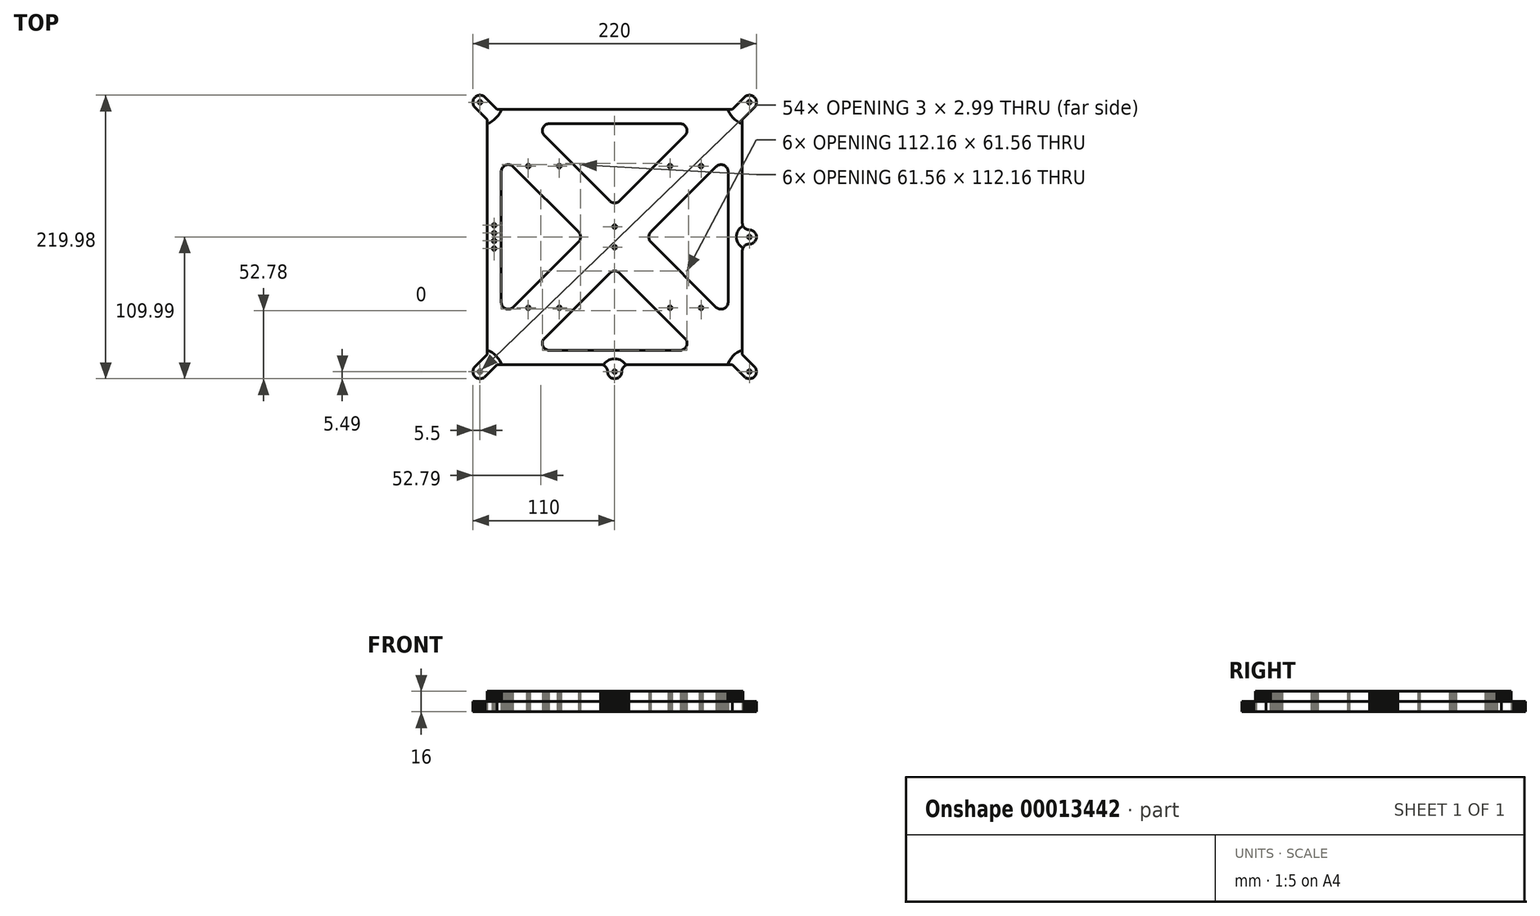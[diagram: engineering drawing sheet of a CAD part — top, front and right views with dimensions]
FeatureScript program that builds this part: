
annotation { "Feature Type Name" : "Feature", "Feature Type Description" : "" }
export const myFeature = defineFeature(function(context is Context, id is Id, definition is map)
    precondition{}
    {
        {
            var Q0;
            Q0=qCreatedBy(makeId("Top.planeOp"),FACE);
            var sketch = newSketch(context, id + "F0", { "sketchPlane" : qUnion([Q0])});
            skLineSegment(sketch, "E0", {"start": v(391.25, -176.92) * mm, "end": v(392.49, -176.69) * mm});
            skLineSegment(sketch, "E1", {"start": v(392.49, -176.69) * mm, "end": v(393.68, -176.3) * mm});
            skLineSegment(sketch, "E2", {"start": v(393.68, -176.3) * mm, "end": v(394.82, -175.76) * mm});
            skLineSegment(sketch, "E3", {"start": v(394.82, -175.76) * mm, "end": v(395.88, -175.1) * mm});
            skLineSegment(sketch, "E4", {"start": v(395.88, -175.1) * mm, "end": v(396.85, -174.29) * mm});
            skLineSegment(sketch, "E5", {"start": v(396.85, -174.29) * mm, "end": v(397.7, -173.37) * mm});
            skLineSegment(sketch, "E6", {"start": v(397.7, -173.37) * mm, "end": v(398.44, -172.36) * mm});
            skLineSegment(sketch, "E7", {"start": v(398.44, -172.36) * mm, "end": v(399.05, -171.26) * mm});
            skLineSegment(sketch, "E8", {"start": v(399.05, -171.26) * mm, "end": v(399.51, -170.1) * mm});
            skLineSegment(sketch, "E9", {"start": v(399.51, -170.1) * mm, "end": v(399.82, -168.87) * mm});
            skLineSegment(sketch, "E10", {"start": v(399.82, -168.87) * mm, "end": v(399.98, -167.63) * mm});
            skLineSegment(sketch, "E11", {"start": v(399.98, -167.63) * mm, "end": v(399.98, -167) * mm});
            skLineSegment(sketch, "E12", {"start": v(399.98, -167) * mm, "end": v(400, -167) * mm});
            skLineSegment(sketch, "E13", {"start": v(400, -167) * mm, "end": v(400, 109) * mm});
            skLineSegment(sketch, "E14", {"start": v(400, 109) * mm, "end": v(360, 109) * mm});
            skLineSegment(sketch, "E15", {"start": v(360, 109) * mm, "end": v(360, 125) * mm});
            skLineSegment(sketch, "E16", {"start": v(360, 125) * mm, "end": v(400, 125) * mm});
            skLineSegment(sketch, "E17", {"start": v(400, 125) * mm, "end": v(400, 253) * mm});
            skLineSegment(sketch, "E18", {"start": v(400, 253) * mm, "end": v(399.92, 254.25) * mm});
            skLineSegment(sketch, "E19", {"start": v(399.92, 254.25) * mm, "end": v(399.69, 255.49) * mm});
            skLineSegment(sketch, "E20", {"start": v(399.69, 255.49) * mm, "end": v(399.3, 256.68) * mm});
            skLineSegment(sketch, "E21", {"start": v(399.3, 256.68) * mm, "end": v(398.76, 257.82) * mm});
            skLineSegment(sketch, "E22", {"start": v(398.76, 257.82) * mm, "end": v(398.09, 258.88) * mm});
            skLineSegment(sketch, "E23", {"start": v(398.09, 258.88) * mm, "end": v(397.3, 259.85) * mm});
            skLineSegment(sketch, "E24", {"start": v(397.3, 259.85) * mm, "end": v(396.37, 260.7) * mm});
            skLineSegment(sketch, "E25", {"start": v(396.37, 260.7) * mm, "end": v(395.36, 261.44) * mm});
            skLineSegment(sketch, "E26", {"start": v(395.36, 261.44) * mm, "end": v(394.26, 262.05) * mm});
            skLineSegment(sketch, "E27", {"start": v(394.26, 262.05) * mm, "end": v(393.09, 262.51) * mm});
            skLineSegment(sketch, "E28", {"start": v(393.09, 262.51) * mm, "end": v(391.87, 262.82) * mm});
            skLineSegment(sketch, "E29", {"start": v(391.87, 262.82) * mm, "end": v(390.63, 262.98) * mm});
            skLineSegment(sketch, "E30", {"start": v(390.63, 262.98) * mm, "end": v(390, 262.98) * mm});
            skLineSegment(sketch, "E31", {"start": v(390, 262.98) * mm, "end": v(390, 263) * mm});
            skLineSegment(sketch, "E32", {"start": v(390, 263) * mm, "end": v(20, 263) * mm});
            skLineSegment(sketch, "E33", {"start": v(20, 263) * mm, "end": v(18.75, 262.92) * mm});
            skLineSegment(sketch, "E34", {"start": v(18.75, 262.92) * mm, "end": v(17.51, 262.69) * mm});
            skLineSegment(sketch, "E35", {"start": v(17.51, 262.69) * mm, "end": v(16.32, 262.3) * mm});
            skLineSegment(sketch, "E36", {"start": v(16.32, 262.3) * mm, "end": v(15.18, 261.76) * mm});
            skLineSegment(sketch, "E37", {"start": v(15.18, 261.76) * mm, "end": v(14.12, 261.09) * mm});
            skLineSegment(sketch, "E38", {"start": v(14.12, 261.09) * mm, "end": v(13.15, 260.3) * mm});
            skLineSegment(sketch, "E39", {"start": v(13.15, 260.3) * mm, "end": v(12.3, 259.37) * mm});
            skLineSegment(sketch, "E40", {"start": v(12.3, 259.37) * mm, "end": v(11.56, 258.36) * mm});
            skLineSegment(sketch, "E41", {"start": v(11.56, 258.36) * mm, "end": v(10.95, 257.26) * mm});
            skLineSegment(sketch, "E42", {"start": v(10.95, 257.26) * mm, "end": v(10.49, 256.09) * mm});
            skLineSegment(sketch, "E43", {"start": v(10.49, 256.09) * mm, "end": v(10.18, 254.87) * mm});
            skLineSegment(sketch, "E44", {"start": v(10.18, 254.87) * mm, "end": v(10.02, 253.63) * mm});
            skLineSegment(sketch, "E45", {"start": v(10.02, 253.63) * mm, "end": v(10.02, 253) * mm});
            skLineSegment(sketch, "E46", {"start": v(10.02, 253) * mm, "end": v(10, 253) * mm});
            skLineSegment(sketch, "E47", {"start": v(10, 253) * mm, "end": v(10, 125) * mm});
            skLineSegment(sketch, "E48", {"start": v(10, 125) * mm, "end": v(50, 125) * mm});
            skLineSegment(sketch, "E49", {"start": v(50, 125) * mm, "end": v(50, 109) * mm});
            skLineSegment(sketch, "E50", {"start": v(50, 109) * mm, "end": v(10, 109) * mm});
            skLineSegment(sketch, "E51", {"start": v(10, 109) * mm, "end": v(10, -167) * mm});
            skLineSegment(sketch, "E52", {"start": v(10, -167) * mm, "end": v(10.08, -168.25) * mm});
            skLineSegment(sketch, "E53", {"start": v(10.08, -168.25) * mm, "end": v(10.31, -169.49) * mm});
            skLineSegment(sketch, "E54", {"start": v(10.31, -169.49) * mm, "end": v(10.7, -170.68) * mm});
            skLineSegment(sketch, "E55", {"start": v(10.7, -170.68) * mm, "end": v(11.24, -171.82) * mm});
            skLineSegment(sketch, "E56", {"start": v(11.24, -171.82) * mm, "end": v(11.9, -172.88) * mm});
            skLineSegment(sketch, "E57", {"start": v(11.9, -172.88) * mm, "end": v(12.71, -173.85) * mm});
            skLineSegment(sketch, "E58", {"start": v(12.71, -173.85) * mm, "end": v(13.63, -174.7) * mm});
            skLineSegment(sketch, "E59", {"start": v(13.63, -174.7) * mm, "end": v(14.64, -175.44) * mm});
            skLineSegment(sketch, "E60", {"start": v(14.64, -175.44) * mm, "end": v(15.74, -176.05) * mm});
            skLineSegment(sketch, "E61", {"start": v(15.74, -176.05) * mm, "end": v(16.9, -176.51) * mm});
            skLineSegment(sketch, "E62", {"start": v(16.9, -176.51) * mm, "end": v(18.13, -176.82) * mm});
            skLineSegment(sketch, "E63", {"start": v(18.13, -176.82) * mm, "end": v(19.37, -176.98) * mm});
            skLineSegment(sketch, "E64", {"start": v(19.37, -176.98) * mm, "end": v(20, -176.98) * mm});
            skLineSegment(sketch, "E65", {"start": v(20, -176.98) * mm, "end": v(20, -177) * mm});
            skLineSegment(sketch, "E66", {"start": v(20, -177) * mm, "end": v(390, -177) * mm});
            skLineSegment(sketch, "E67", {"start": v(390, -177) * mm, "end": v(391.25, -176.92) * mm});
            skLineSegment(sketch, "E68", {"start": v(50, 236.5) * mm, "end": v(50, 252.5) * mm});
            skLineSegment(sketch, "E69", {"start": v(50, 252.5) * mm, "end": v(70, 252.5) * mm});
            skLineSegment(sketch, "E70", {"start": v(70, 252.5) * mm, "end": v(70, 236.5) * mm});
            skLineSegment(sketch, "E71", {"start": v(70, 236.5) * mm, "end": v(50, 236.5) * mm});
            skLineSegment(sketch, "E72", {"start": v(195, 236.5) * mm, "end": v(195, 252.5) * mm});
            skLineSegment(sketch, "E73", {"start": v(195, 252.5) * mm, "end": v(215, 252.5) * mm});
            skLineSegment(sketch, "E74", {"start": v(215, 252.5) * mm, "end": v(215, 236.5) * mm});
            skLineSegment(sketch, "E75", {"start": v(215, 236.5) * mm, "end": v(195, 236.5) * mm});
            skLineSegment(sketch, "E76", {"start": v(340, 236.5) * mm, "end": v(340, 252.5) * mm});
            skLineSegment(sketch, "E77", {"start": v(340, 252.5) * mm, "end": v(360, 252.5) * mm});
            skLineSegment(sketch, "E78", {"start": v(360, 252.5) * mm, "end": v(360, 236.5) * mm});
            skLineSegment(sketch, "E79", {"start": v(360, 236.5) * mm, "end": v(340, 236.5) * mm});
            skLineSegment(sketch, "E80", {"start": v(287.37, 242.5) * mm, "end": v(287.12, 242.53) * mm});
            skLineSegment(sketch, "E81", {"start": v(287.12, 242.53) * mm, "end": v(286.88, 242.6) * mm});
            skLineSegment(sketch, "E82", {"start": v(286.88, 242.6) * mm, "end": v(286.65, 242.7) * mm});
            skLineSegment(sketch, "E83", {"start": v(286.65, 242.7) * mm, "end": v(286.43, 242.81) * mm});
            skLineSegment(sketch, "E84", {"start": v(286.43, 242.81) * mm, "end": v(286.23, 242.96) * mm});
            skLineSegment(sketch, "E85", {"start": v(286.23, 242.96) * mm, "end": v(286.04, 243.13) * mm});
            skLineSegment(sketch, "E86", {"start": v(286.04, 243.13) * mm, "end": v(285.88, 243.32) * mm});
            skLineSegment(sketch, "E87", {"start": v(285.88, 243.32) * mm, "end": v(285.75, 243.54) * mm});
            skLineSegment(sketch, "E88", {"start": v(285.75, 243.54) * mm, "end": v(285.64, 243.76) * mm});
            skLineSegment(sketch, "E89", {"start": v(285.64, 243.76) * mm, "end": v(285.56, 244) * mm});
            skLineSegment(sketch, "E90", {"start": v(285.56, 244) * mm, "end": v(285.52, 244.25) * mm});
            skLineSegment(sketch, "E91", {"start": v(285.52, 244.25) * mm, "end": v(285.5, 244.5) * mm});
            skLineSegment(sketch, "E92", {"start": v(285.5, 244.5) * mm, "end": v(285.52, 244.75) * mm});
            skLineSegment(sketch, "E93", {"start": v(285.52, 244.75) * mm, "end": v(285.56, 245) * mm});
            skLineSegment(sketch, "E94", {"start": v(285.56, 245) * mm, "end": v(285.64, 245.24) * mm});
            skLineSegment(sketch, "E95", {"start": v(285.64, 245.24) * mm, "end": v(285.75, 245.46) * mm});
            skLineSegment(sketch, "E96", {"start": v(285.75, 245.46) * mm, "end": v(285.88, 245.68) * mm});
            skLineSegment(sketch, "E97", {"start": v(285.88, 245.68) * mm, "end": v(286.04, 245.87) * mm});
            skLineSegment(sketch, "E98", {"start": v(286.04, 245.87) * mm, "end": v(286.23, 246.04) * mm});
            skLineSegment(sketch, "E99", {"start": v(286.23, 246.04) * mm, "end": v(286.43, 246.19) * mm});
            skLineSegment(sketch, "E100", {"start": v(286.43, 246.19) * mm, "end": v(286.65, 246.3) * mm});
            skLineSegment(sketch, "E101", {"start": v(286.65, 246.3) * mm, "end": v(286.88, 246.4) * mm});
            skLineSegment(sketch, "E102", {"start": v(286.88, 246.4) * mm, "end": v(287.12, 246.47) * mm});
            skLineSegment(sketch, "E103", {"start": v(287.12, 246.47) * mm, "end": v(287.37, 246.5) * mm});
            skLineSegment(sketch, "E104", {"start": v(287.37, 246.5) * mm, "end": v(287.63, 246.5) * mm});
            skLineSegment(sketch, "E105", {"start": v(287.63, 246.5) * mm, "end": v(287.88, 246.47) * mm});
            skLineSegment(sketch, "E106", {"start": v(287.88, 246.47) * mm, "end": v(288.12, 246.4) * mm});
            skLineSegment(sketch, "E107", {"start": v(288.12, 246.4) * mm, "end": v(288.35, 246.3) * mm});
            skLineSegment(sketch, "E108", {"start": v(288.35, 246.3) * mm, "end": v(288.57, 246.19) * mm});
            skLineSegment(sketch, "E109", {"start": v(288.57, 246.19) * mm, "end": v(288.77, 246.04) * mm});
            skLineSegment(sketch, "E110", {"start": v(288.77, 246.04) * mm, "end": v(288.96, 245.87) * mm});
            skLineSegment(sketch, "E111", {"start": v(288.96, 245.87) * mm, "end": v(289.12, 245.68) * mm});
            skLineSegment(sketch, "E112", {"start": v(289.12, 245.68) * mm, "end": v(289.25, 245.46) * mm});
            skLineSegment(sketch, "E113", {"start": v(289.25, 245.46) * mm, "end": v(289.36, 245.24) * mm});
            skLineSegment(sketch, "E114", {"start": v(289.36, 245.24) * mm, "end": v(289.44, 245) * mm});
            skLineSegment(sketch, "E115", {"start": v(289.44, 245) * mm, "end": v(289.48, 244.75) * mm});
            skLineSegment(sketch, "E116", {"start": v(289.48, 244.75) * mm, "end": v(289.5, 244.5) * mm});
            skLineSegment(sketch, "E117", {"start": v(289.5, 244.5) * mm, "end": v(289.48, 244.25) * mm});
            skLineSegment(sketch, "E118", {"start": v(289.48, 244.25) * mm, "end": v(289.44, 244) * mm});
            skLineSegment(sketch, "E119", {"start": v(289.44, 244) * mm, "end": v(289.36, 243.76) * mm});
            skLineSegment(sketch, "E120", {"start": v(289.36, 243.76) * mm, "end": v(289.25, 243.54) * mm});
            skLineSegment(sketch, "E121", {"start": v(289.25, 243.54) * mm, "end": v(289.12, 243.32) * mm});
            skLineSegment(sketch, "E122", {"start": v(289.12, 243.32) * mm, "end": v(288.96, 243.13) * mm});
            skLineSegment(sketch, "E123", {"start": v(288.96, 243.13) * mm, "end": v(288.77, 242.96) * mm});
            skLineSegment(sketch, "E124", {"start": v(288.77, 242.96) * mm, "end": v(288.57, 242.81) * mm});
            skLineSegment(sketch, "E125", {"start": v(288.57, 242.81) * mm, "end": v(288.35, 242.7) * mm});
            skLineSegment(sketch, "E126", {"start": v(288.35, 242.7) * mm, "end": v(288.12, 242.6) * mm});
            skLineSegment(sketch, "E127", {"start": v(288.12, 242.6) * mm, "end": v(287.88, 242.53) * mm});
            skLineSegment(sketch, "E128", {"start": v(287.88, 242.53) * mm, "end": v(287.63, 242.5) * mm});
            skLineSegment(sketch, "E129", {"start": v(287.63, 242.5) * mm, "end": v(287.37, 242.5) * mm});
            skLineSegment(sketch, "E130", {"start": v(122.37, 242.5) * mm, "end": v(122.12, 242.53) * mm});
            skLineSegment(sketch, "E131", {"start": v(122.12, 242.53) * mm, "end": v(121.88, 242.6) * mm});
            skLineSegment(sketch, "E132", {"start": v(121.88, 242.6) * mm, "end": v(121.65, 242.7) * mm});
            skLineSegment(sketch, "E133", {"start": v(121.65, 242.7) * mm, "end": v(121.43, 242.81) * mm});
            skLineSegment(sketch, "E134", {"start": v(121.43, 242.81) * mm, "end": v(121.22, 242.96) * mm});
            skLineSegment(sketch, "E135", {"start": v(121.22, 242.96) * mm, "end": v(121.04, 243.13) * mm});
            skLineSegment(sketch, "E136", {"start": v(121.04, 243.13) * mm, "end": v(120.88, 243.32) * mm});
            skLineSegment(sketch, "E137", {"start": v(120.88, 243.32) * mm, "end": v(120.75, 243.54) * mm});
            skLineSegment(sketch, "E138", {"start": v(120.75, 243.54) * mm, "end": v(120.64, 243.76) * mm});
            skLineSegment(sketch, "E139", {"start": v(120.64, 243.76) * mm, "end": v(120.56, 244) * mm});
            skLineSegment(sketch, "E140", {"start": v(120.56, 244) * mm, "end": v(120.52, 244.25) * mm});
            skLineSegment(sketch, "E141", {"start": v(120.52, 244.25) * mm, "end": v(120.5, 244.5) * mm});
            skLineSegment(sketch, "E142", {"start": v(120.5, 244.5) * mm, "end": v(120.52, 244.75) * mm});
            skLineSegment(sketch, "E143", {"start": v(120.52, 244.75) * mm, "end": v(120.56, 245) * mm});
            skLineSegment(sketch, "E144", {"start": v(120.56, 245) * mm, "end": v(120.64, 245.24) * mm});
            skLineSegment(sketch, "E145", {"start": v(120.64, 245.24) * mm, "end": v(120.75, 245.46) * mm});
            skLineSegment(sketch, "E146", {"start": v(120.75, 245.46) * mm, "end": v(120.88, 245.68) * mm});
            skLineSegment(sketch, "E147", {"start": v(120.88, 245.68) * mm, "end": v(121.04, 245.87) * mm});
            skLineSegment(sketch, "E148", {"start": v(121.04, 245.87) * mm, "end": v(121.22, 246.04) * mm});
            skLineSegment(sketch, "E149", {"start": v(121.22, 246.04) * mm, "end": v(121.43, 246.19) * mm});
            skLineSegment(sketch, "E150", {"start": v(121.43, 246.19) * mm, "end": v(121.65, 246.3) * mm});
            skLineSegment(sketch, "E151", {"start": v(121.65, 246.3) * mm, "end": v(121.88, 246.4) * mm});
            skLineSegment(sketch, "E152", {"start": v(121.88, 246.4) * mm, "end": v(122.12, 246.47) * mm});
            skLineSegment(sketch, "E153", {"start": v(122.12, 246.47) * mm, "end": v(122.37, 246.5) * mm});
            skLineSegment(sketch, "E154", {"start": v(122.37, 246.5) * mm, "end": v(122.63, 246.5) * mm});
            skLineSegment(sketch, "E155", {"start": v(122.63, 246.5) * mm, "end": v(122.88, 246.47) * mm});
            skLineSegment(sketch, "E156", {"start": v(122.88, 246.47) * mm, "end": v(123.12, 246.4) * mm});
            skLineSegment(sketch, "E157", {"start": v(123.12, 246.4) * mm, "end": v(123.35, 246.3) * mm});
            skLineSegment(sketch, "E158", {"start": v(123.35, 246.3) * mm, "end": v(123.57, 246.19) * mm});
            skLineSegment(sketch, "E159", {"start": v(123.57, 246.19) * mm, "end": v(123.78, 246.04) * mm});
            skLineSegment(sketch, "E160", {"start": v(123.78, 246.04) * mm, "end": v(123.96, 245.87) * mm});
            skLineSegment(sketch, "E161", {"start": v(123.96, 245.87) * mm, "end": v(124.12, 245.68) * mm});
            skLineSegment(sketch, "E162", {"start": v(124.12, 245.68) * mm, "end": v(124.25, 245.46) * mm});
            skLineSegment(sketch, "E163", {"start": v(124.25, 245.46) * mm, "end": v(124.36, 245.24) * mm});
            skLineSegment(sketch, "E164", {"start": v(124.36, 245.24) * mm, "end": v(124.44, 245) * mm});
            skLineSegment(sketch, "E165", {"start": v(124.44, 245) * mm, "end": v(124.48, 244.75) * mm});
            skLineSegment(sketch, "E166", {"start": v(124.48, 244.75) * mm, "end": v(124.5, 244.5) * mm});
            skLineSegment(sketch, "E167", {"start": v(124.5, 244.5) * mm, "end": v(124.48, 244.25) * mm});
            skLineSegment(sketch, "E168", {"start": v(124.48, 244.25) * mm, "end": v(124.44, 244) * mm});
            skLineSegment(sketch, "E169", {"start": v(124.44, 244) * mm, "end": v(124.36, 243.76) * mm});
            skLineSegment(sketch, "E170", {"start": v(124.36, 243.76) * mm, "end": v(124.25, 243.54) * mm});
            skLineSegment(sketch, "E171", {"start": v(124.25, 243.54) * mm, "end": v(124.12, 243.32) * mm});
            skLineSegment(sketch, "E172", {"start": v(124.12, 243.32) * mm, "end": v(123.96, 243.13) * mm});
            skLineSegment(sketch, "E173", {"start": v(123.96, 243.13) * mm, "end": v(123.78, 242.96) * mm});
            skLineSegment(sketch, "E174", {"start": v(123.78, 242.96) * mm, "end": v(123.57, 242.81) * mm});
            skLineSegment(sketch, "E175", {"start": v(123.57, 242.81) * mm, "end": v(123.35, 242.7) * mm});
            skLineSegment(sketch, "E176", {"start": v(123.35, 242.7) * mm, "end": v(123.12, 242.6) * mm});
            skLineSegment(sketch, "E177", {"start": v(123.12, 242.6) * mm, "end": v(122.88, 242.53) * mm});
            skLineSegment(sketch, "E178", {"start": v(122.88, 242.53) * mm, "end": v(122.63, 242.5) * mm});
            skLineSegment(sketch, "E179", {"start": v(122.63, 242.5) * mm, "end": v(122.37, 242.5) * mm});
            skLineSegment(sketch, "E180", {"start": v(267.9, 231.5) * mm, "end": v(267.72, 231.53) * mm});
            skLineSegment(sketch, "E181", {"start": v(267.72, 231.53) * mm, "end": v(267.54, 231.57) * mm});
            skLineSegment(sketch, "E182", {"start": v(267.54, 231.57) * mm, "end": v(267.36, 231.64) * mm});
            skLineSegment(sketch, "E183", {"start": v(267.36, 231.64) * mm, "end": v(267.2, 231.73) * mm});
            skLineSegment(sketch, "E184", {"start": v(267.2, 231.73) * mm, "end": v(267.04, 231.84) * mm});
            skLineSegment(sketch, "E185", {"start": v(267.04, 231.84) * mm, "end": v(266.9, 231.97) * mm});
            skLineSegment(sketch, "E186", {"start": v(266.9, 231.97) * mm, "end": v(266.79, 232.12) * mm});
            skLineSegment(sketch, "E187", {"start": v(266.79, 232.12) * mm, "end": v(266.69, 232.28) * mm});
            skLineSegment(sketch, "E188", {"start": v(266.69, 232.28) * mm, "end": v(266.6, 232.45) * mm});
            skLineSegment(sketch, "E189", {"start": v(266.6, 232.45) * mm, "end": v(266.55, 232.63) * mm});
            skLineSegment(sketch, "E190", {"start": v(266.55, 232.63) * mm, "end": v(266.51, 232.81) * mm});
            skLineSegment(sketch, "E191", {"start": v(266.51, 232.81) * mm, "end": v(266.5, 233) * mm});
            skLineSegment(sketch, "E192", {"start": v(266.5, 233) * mm, "end": v(266.51, 233.19) * mm});
            skLineSegment(sketch, "E193", {"start": v(266.51, 233.19) * mm, "end": v(266.55, 233.37) * mm});
            skLineSegment(sketch, "E194", {"start": v(266.55, 233.37) * mm, "end": v(266.6, 233.55) * mm});
            skLineSegment(sketch, "E195", {"start": v(266.6, 233.55) * mm, "end": v(266.69, 233.72) * mm});
            skLineSegment(sketch, "E196", {"start": v(266.69, 233.72) * mm, "end": v(266.79, 233.88) * mm});
            skLineSegment(sketch, "E197", {"start": v(266.79, 233.88) * mm, "end": v(266.9, 234.03) * mm});
            skLineSegment(sketch, "E198", {"start": v(266.9, 234.03) * mm, "end": v(267.04, 234.16) * mm});
            skLineSegment(sketch, "E199", {"start": v(267.04, 234.16) * mm, "end": v(267.2, 234.27) * mm});
            skLineSegment(sketch, "E200", {"start": v(267.2, 234.27) * mm, "end": v(267.36, 234.36) * mm});
            skLineSegment(sketch, "E201", {"start": v(267.36, 234.36) * mm, "end": v(267.54, 234.43) * mm});
            skLineSegment(sketch, "E202", {"start": v(267.54, 234.43) * mm, "end": v(267.72, 234.47) * mm});
            skLineSegment(sketch, "E203", {"start": v(267.72, 234.47) * mm, "end": v(267.9, 234.5) * mm});
            skLineSegment(sketch, "E204", {"start": v(267.9, 234.5) * mm, "end": v(268.1, 234.5) * mm});
            skLineSegment(sketch, "E205", {"start": v(268.1, 234.5) * mm, "end": v(268.28, 234.47) * mm});
            skLineSegment(sketch, "E206", {"start": v(268.28, 234.47) * mm, "end": v(268.46, 234.43) * mm});
            skLineSegment(sketch, "E207", {"start": v(268.46, 234.43) * mm, "end": v(268.64, 234.36) * mm});
            skLineSegment(sketch, "E208", {"start": v(268.64, 234.36) * mm, "end": v(268.8, 234.27) * mm});
            skLineSegment(sketch, "E209", {"start": v(268.8, 234.27) * mm, "end": v(268.96, 234.16) * mm});
            skLineSegment(sketch, "E210", {"start": v(268.96, 234.16) * mm, "end": v(269.1, 234.03) * mm});
            skLineSegment(sketch, "E211", {"start": v(269.1, 234.03) * mm, "end": v(269.21, 233.88) * mm});
            skLineSegment(sketch, "E212", {"start": v(269.21, 233.88) * mm, "end": v(269.31, 233.72) * mm});
            skLineSegment(sketch, "E213", {"start": v(269.31, 233.72) * mm, "end": v(269.4, 233.55) * mm});
            skLineSegment(sketch, "E214", {"start": v(269.4, 233.55) * mm, "end": v(269.45, 233.37) * mm});
            skLineSegment(sketch, "E215", {"start": v(269.45, 233.37) * mm, "end": v(269.49, 233.19) * mm});
            skLineSegment(sketch, "E216", {"start": v(269.49, 233.19) * mm, "end": v(269.5, 233) * mm});
            skLineSegment(sketch, "E217", {"start": v(269.5, 233) * mm, "end": v(269.49, 232.81) * mm});
            skLineSegment(sketch, "E218", {"start": v(269.49, 232.81) * mm, "end": v(269.45, 232.63) * mm});
            skLineSegment(sketch, "E219", {"start": v(269.45, 232.63) * mm, "end": v(269.4, 232.45) * mm});
            skLineSegment(sketch, "E220", {"start": v(269.4, 232.45) * mm, "end": v(269.31, 232.28) * mm});
            skLineSegment(sketch, "E221", {"start": v(269.31, 232.28) * mm, "end": v(269.21, 232.12) * mm});
            skLineSegment(sketch, "E222", {"start": v(269.21, 232.12) * mm, "end": v(269.1, 231.97) * mm});
            skLineSegment(sketch, "E223", {"start": v(269.1, 231.97) * mm, "end": v(268.96, 231.84) * mm});
            skLineSegment(sketch, "E224", {"start": v(268.96, 231.84) * mm, "end": v(268.8, 231.73) * mm});
            skLineSegment(sketch, "E225", {"start": v(268.8, 231.73) * mm, "end": v(268.64, 231.64) * mm});
            skLineSegment(sketch, "E226", {"start": v(268.64, 231.64) * mm, "end": v(268.46, 231.57) * mm});
            skLineSegment(sketch, "E227", {"start": v(268.46, 231.57) * mm, "end": v(268.28, 231.53) * mm});
            skLineSegment(sketch, "E228", {"start": v(268.28, 231.53) * mm, "end": v(268.1, 231.5) * mm});
            skLineSegment(sketch, "E229", {"start": v(268.1, 231.5) * mm, "end": v(267.9, 231.5) * mm});
            skLineSegment(sketch, "E230", {"start": v(251.9, 231.5) * mm, "end": v(251.72, 231.53) * mm});
            skLineSegment(sketch, "E231", {"start": v(251.72, 231.53) * mm, "end": v(251.54, 231.57) * mm});
            skLineSegment(sketch, "E232", {"start": v(251.54, 231.57) * mm, "end": v(251.36, 231.64) * mm});
            skLineSegment(sketch, "E233", {"start": v(251.36, 231.64) * mm, "end": v(251.2, 231.73) * mm});
            skLineSegment(sketch, "E234", {"start": v(251.2, 231.73) * mm, "end": v(251.04, 231.84) * mm});
            skLineSegment(sketch, "E235", {"start": v(251.04, 231.84) * mm, "end": v(250.9, 231.97) * mm});
            skLineSegment(sketch, "E236", {"start": v(250.9, 231.97) * mm, "end": v(250.79, 232.12) * mm});
            skLineSegment(sketch, "E237", {"start": v(250.79, 232.12) * mm, "end": v(250.69, 232.28) * mm});
            skLineSegment(sketch, "E238", {"start": v(250.69, 232.28) * mm, "end": v(250.6, 232.45) * mm});
            skLineSegment(sketch, "E239", {"start": v(250.6, 232.45) * mm, "end": v(250.55, 232.63) * mm});
            skLineSegment(sketch, "E240", {"start": v(250.55, 232.63) * mm, "end": v(250.51, 232.81) * mm});
            skLineSegment(sketch, "E241", {"start": v(250.51, 232.81) * mm, "end": v(250.5, 233) * mm});
            skLineSegment(sketch, "E242", {"start": v(250.5, 233) * mm, "end": v(250.51, 233.19) * mm});
            skLineSegment(sketch, "E243", {"start": v(250.51, 233.19) * mm, "end": v(250.55, 233.37) * mm});
            skLineSegment(sketch, "E244", {"start": v(250.55, 233.37) * mm, "end": v(250.6, 233.55) * mm});
            skLineSegment(sketch, "E245", {"start": v(250.6, 233.55) * mm, "end": v(250.69, 233.72) * mm});
            skLineSegment(sketch, "E246", {"start": v(250.69, 233.72) * mm, "end": v(250.79, 233.88) * mm});
            skLineSegment(sketch, "E247", {"start": v(250.79, 233.88) * mm, "end": v(250.9, 234.03) * mm});
            skLineSegment(sketch, "E248", {"start": v(250.9, 234.03) * mm, "end": v(251.04, 234.16) * mm});
            skLineSegment(sketch, "E249", {"start": v(251.04, 234.16) * mm, "end": v(251.2, 234.27) * mm});
            skLineSegment(sketch, "E250", {"start": v(251.2, 234.27) * mm, "end": v(251.36, 234.36) * mm});
            skLineSegment(sketch, "E251", {"start": v(251.36, 234.36) * mm, "end": v(251.54, 234.43) * mm});
            skLineSegment(sketch, "E252", {"start": v(251.54, 234.43) * mm, "end": v(251.72, 234.47) * mm});
            skLineSegment(sketch, "E253", {"start": v(251.72, 234.47) * mm, "end": v(251.9, 234.5) * mm});
            skLineSegment(sketch, "E254", {"start": v(251.9, 234.5) * mm, "end": v(252.1, 234.5) * mm});
            skLineSegment(sketch, "E255", {"start": v(252.1, 234.5) * mm, "end": v(252.28, 234.47) * mm});
            skLineSegment(sketch, "E256", {"start": v(252.28, 234.47) * mm, "end": v(252.46, 234.43) * mm});
            skLineSegment(sketch, "E257", {"start": v(252.46, 234.43) * mm, "end": v(252.64, 234.36) * mm});
            skLineSegment(sketch, "E258", {"start": v(252.64, 234.36) * mm, "end": v(252.8, 234.27) * mm});
            skLineSegment(sketch, "E259", {"start": v(252.8, 234.27) * mm, "end": v(252.96, 234.16) * mm});
            skLineSegment(sketch, "E260", {"start": v(252.96, 234.16) * mm, "end": v(253.1, 234.03) * mm});
            skLineSegment(sketch, "E261", {"start": v(253.1, 234.03) * mm, "end": v(253.21, 233.88) * mm});
            skLineSegment(sketch, "E262", {"start": v(253.21, 233.88) * mm, "end": v(253.31, 233.72) * mm});
            skLineSegment(sketch, "E263", {"start": v(253.31, 233.72) * mm, "end": v(253.4, 233.55) * mm});
            skLineSegment(sketch, "E264", {"start": v(253.4, 233.55) * mm, "end": v(253.45, 233.37) * mm});
            skLineSegment(sketch, "E265", {"start": v(253.45, 233.37) * mm, "end": v(253.49, 233.19) * mm});
            skLineSegment(sketch, "E266", {"start": v(253.49, 233.19) * mm, "end": v(253.5, 233) * mm});
            skLineSegment(sketch, "E267", {"start": v(253.5, 233) * mm, "end": v(253.49, 232.81) * mm});
            skLineSegment(sketch, "E268", {"start": v(253.49, 232.81) * mm, "end": v(253.45, 232.63) * mm});
            skLineSegment(sketch, "E269", {"start": v(253.45, 232.63) * mm, "end": v(253.4, 232.45) * mm});
            skLineSegment(sketch, "E270", {"start": v(253.4, 232.45) * mm, "end": v(253.31, 232.28) * mm});
            skLineSegment(sketch, "E271", {"start": v(253.31, 232.28) * mm, "end": v(253.21, 232.12) * mm});
            skLineSegment(sketch, "E272", {"start": v(253.21, 232.12) * mm, "end": v(253.1, 231.97) * mm});
            skLineSegment(sketch, "E273", {"start": v(253.1, 231.97) * mm, "end": v(252.96, 231.84) * mm});
            skLineSegment(sketch, "E274", {"start": v(252.96, 231.84) * mm, "end": v(252.8, 231.73) * mm});
            skLineSegment(sketch, "E275", {"start": v(252.8, 231.73) * mm, "end": v(252.64, 231.64) * mm});
            skLineSegment(sketch, "E276", {"start": v(252.64, 231.64) * mm, "end": v(252.46, 231.57) * mm});
            skLineSegment(sketch, "E277", {"start": v(252.46, 231.57) * mm, "end": v(252.28, 231.53) * mm});
            skLineSegment(sketch, "E278", {"start": v(252.28, 231.53) * mm, "end": v(252.1, 231.5) * mm});
            skLineSegment(sketch, "E279", {"start": v(252.1, 231.5) * mm, "end": v(251.9, 231.5) * mm});
            skLineSegment(sketch, "E280", {"start": v(157.9, 231.5) * mm, "end": v(157.72, 231.53) * mm});
            skLineSegment(sketch, "E281", {"start": v(157.72, 231.53) * mm, "end": v(157.54, 231.57) * mm});
            skLineSegment(sketch, "E282", {"start": v(157.54, 231.57) * mm, "end": v(157.36, 231.64) * mm});
            skLineSegment(sketch, "E283", {"start": v(157.36, 231.64) * mm, "end": v(157.2, 231.73) * mm});
            skLineSegment(sketch, "E284", {"start": v(157.2, 231.73) * mm, "end": v(157.04, 231.84) * mm});
            skLineSegment(sketch, "E285", {"start": v(157.04, 231.84) * mm, "end": v(156.9, 231.97) * mm});
            skLineSegment(sketch, "E286", {"start": v(156.9, 231.97) * mm, "end": v(156.79, 232.12) * mm});
            skLineSegment(sketch, "E287", {"start": v(156.79, 232.12) * mm, "end": v(156.69, 232.28) * mm});
            skLineSegment(sketch, "E288", {"start": v(156.69, 232.28) * mm, "end": v(156.6, 232.45) * mm});
            skLineSegment(sketch, "E289", {"start": v(156.6, 232.45) * mm, "end": v(156.55, 232.63) * mm});
            skLineSegment(sketch, "E290", {"start": v(156.55, 232.63) * mm, "end": v(156.51, 232.81) * mm});
            skLineSegment(sketch, "E291", {"start": v(156.51, 232.81) * mm, "end": v(156.5, 233) * mm});
            skLineSegment(sketch, "E292", {"start": v(156.5, 233) * mm, "end": v(156.51, 233.19) * mm});
            skLineSegment(sketch, "E293", {"start": v(156.51, 233.19) * mm, "end": v(156.55, 233.37) * mm});
            skLineSegment(sketch, "E294", {"start": v(156.55, 233.37) * mm, "end": v(156.6, 233.55) * mm});
            skLineSegment(sketch, "E295", {"start": v(156.6, 233.55) * mm, "end": v(156.69, 233.72) * mm});
            skLineSegment(sketch, "E296", {"start": v(156.69, 233.72) * mm, "end": v(156.79, 233.88) * mm});
            skLineSegment(sketch, "E297", {"start": v(156.79, 233.88) * mm, "end": v(156.9, 234.03) * mm});
            skLineSegment(sketch, "E298", {"start": v(156.9, 234.03) * mm, "end": v(157.04, 234.16) * mm});
            skLineSegment(sketch, "E299", {"start": v(157.04, 234.16) * mm, "end": v(157.2, 234.27) * mm});
            skLineSegment(sketch, "E300", {"start": v(157.2, 234.27) * mm, "end": v(157.36, 234.36) * mm});
            skLineSegment(sketch, "E301", {"start": v(157.36, 234.36) * mm, "end": v(157.54, 234.43) * mm});
            skLineSegment(sketch, "E302", {"start": v(157.54, 234.43) * mm, "end": v(157.72, 234.47) * mm});
            skLineSegment(sketch, "E303", {"start": v(157.72, 234.47) * mm, "end": v(157.9, 234.5) * mm});
            skLineSegment(sketch, "E304", {"start": v(157.9, 234.5) * mm, "end": v(158.1, 234.5) * mm});
            skLineSegment(sketch, "E305", {"start": v(158.1, 234.5) * mm, "end": v(158.28, 234.47) * mm});
            skLineSegment(sketch, "E306", {"start": v(158.28, 234.47) * mm, "end": v(158.46, 234.43) * mm});
            skLineSegment(sketch, "E307", {"start": v(158.46, 234.43) * mm, "end": v(158.64, 234.36) * mm});
            skLineSegment(sketch, "E308", {"start": v(158.64, 234.36) * mm, "end": v(158.8, 234.27) * mm});
            skLineSegment(sketch, "E309", {"start": v(158.8, 234.27) * mm, "end": v(158.96, 234.16) * mm});
            skLineSegment(sketch, "E310", {"start": v(158.96, 234.16) * mm, "end": v(159.1, 234.03) * mm});
            skLineSegment(sketch, "E311", {"start": v(159.1, 234.03) * mm, "end": v(159.21, 233.88) * mm});
            skLineSegment(sketch, "E312", {"start": v(159.21, 233.88) * mm, "end": v(159.31, 233.72) * mm});
            skLineSegment(sketch, "E313", {"start": v(159.31, 233.72) * mm, "end": v(159.4, 233.55) * mm});
            skLineSegment(sketch, "E314", {"start": v(159.4, 233.55) * mm, "end": v(159.45, 233.37) * mm});
            skLineSegment(sketch, "E315", {"start": v(159.45, 233.37) * mm, "end": v(159.49, 233.19) * mm});
            skLineSegment(sketch, "E316", {"start": v(159.49, 233.19) * mm, "end": v(159.5, 233) * mm});
            skLineSegment(sketch, "E317", {"start": v(159.5, 233) * mm, "end": v(159.49, 232.81) * mm});
            skLineSegment(sketch, "E318", {"start": v(159.49, 232.81) * mm, "end": v(159.45, 232.63) * mm});
            skLineSegment(sketch, "E319", {"start": v(159.45, 232.63) * mm, "end": v(159.4, 232.45) * mm});
            skLineSegment(sketch, "E320", {"start": v(159.4, 232.45) * mm, "end": v(159.31, 232.28) * mm});
            skLineSegment(sketch, "E321", {"start": v(159.31, 232.28) * mm, "end": v(159.21, 232.12) * mm});
            skLineSegment(sketch, "E322", {"start": v(159.21, 232.12) * mm, "end": v(159.1, 231.97) * mm});
            skLineSegment(sketch, "E323", {"start": v(159.1, 231.97) * mm, "end": v(158.96, 231.84) * mm});
            skLineSegment(sketch, "E324", {"start": v(158.96, 231.84) * mm, "end": v(158.8, 231.73) * mm});
            skLineSegment(sketch, "E325", {"start": v(158.8, 231.73) * mm, "end": v(158.64, 231.64) * mm});
            skLineSegment(sketch, "E326", {"start": v(158.64, 231.64) * mm, "end": v(158.46, 231.57) * mm});
            skLineSegment(sketch, "E327", {"start": v(158.46, 231.57) * mm, "end": v(158.28, 231.53) * mm});
            skLineSegment(sketch, "E328", {"start": v(158.28, 231.53) * mm, "end": v(158.1, 231.5) * mm});
            skLineSegment(sketch, "E329", {"start": v(158.1, 231.5) * mm, "end": v(157.9, 231.5) * mm});
            skLineSegment(sketch, "E330", {"start": v(141.9, 231.5) * mm, "end": v(141.72, 231.53) * mm});
            skLineSegment(sketch, "E331", {"start": v(141.72, 231.53) * mm, "end": v(141.54, 231.57) * mm});
            skLineSegment(sketch, "E332", {"start": v(141.54, 231.57) * mm, "end": v(141.36, 231.64) * mm});
            skLineSegment(sketch, "E333", {"start": v(141.36, 231.64) * mm, "end": v(141.2, 231.73) * mm});
            skLineSegment(sketch, "E334", {"start": v(141.2, 231.73) * mm, "end": v(141.04, 231.84) * mm});
            skLineSegment(sketch, "E335", {"start": v(141.04, 231.84) * mm, "end": v(140.9, 231.97) * mm});
            skLineSegment(sketch, "E336", {"start": v(140.9, 231.97) * mm, "end": v(140.79, 232.12) * mm});
            skLineSegment(sketch, "E337", {"start": v(140.79, 232.12) * mm, "end": v(140.69, 232.28) * mm});
            skLineSegment(sketch, "E338", {"start": v(140.69, 232.28) * mm, "end": v(140.6, 232.45) * mm});
            skLineSegment(sketch, "E339", {"start": v(140.6, 232.45) * mm, "end": v(140.55, 232.63) * mm});
            skLineSegment(sketch, "E340", {"start": v(140.55, 232.63) * mm, "end": v(140.51, 232.81) * mm});
            skLineSegment(sketch, "E341", {"start": v(140.51, 232.81) * mm, "end": v(140.5, 233) * mm});
            skLineSegment(sketch, "E342", {"start": v(140.5, 233) * mm, "end": v(140.51, 233.19) * mm});
            skLineSegment(sketch, "E343", {"start": v(140.51, 233.19) * mm, "end": v(140.55, 233.37) * mm});
            skLineSegment(sketch, "E344", {"start": v(140.55, 233.37) * mm, "end": v(140.6, 233.55) * mm});
            skLineSegment(sketch, "E345", {"start": v(140.6, 233.55) * mm, "end": v(140.69, 233.72) * mm});
            skLineSegment(sketch, "E346", {"start": v(140.69, 233.72) * mm, "end": v(140.79, 233.88) * mm});
            skLineSegment(sketch, "E347", {"start": v(140.79, 233.88) * mm, "end": v(140.9, 234.03) * mm});
            skLineSegment(sketch, "E348", {"start": v(140.9, 234.03) * mm, "end": v(141.04, 234.16) * mm});
            skLineSegment(sketch, "E349", {"start": v(141.04, 234.16) * mm, "end": v(141.2, 234.27) * mm});
            skLineSegment(sketch, "E350", {"start": v(141.2, 234.27) * mm, "end": v(141.36, 234.36) * mm});
            skLineSegment(sketch, "E351", {"start": v(141.36, 234.36) * mm, "end": v(141.54, 234.43) * mm});
            skLineSegment(sketch, "E352", {"start": v(141.54, 234.43) * mm, "end": v(141.72, 234.47) * mm});
            skLineSegment(sketch, "E353", {"start": v(141.72, 234.47) * mm, "end": v(141.9, 234.5) * mm});
            skLineSegment(sketch, "E354", {"start": v(141.9, 234.5) * mm, "end": v(142.1, 234.5) * mm});
            skLineSegment(sketch, "E355", {"start": v(142.1, 234.5) * mm, "end": v(142.28, 234.47) * mm});
            skLineSegment(sketch, "E356", {"start": v(142.28, 234.47) * mm, "end": v(142.46, 234.43) * mm});
            skLineSegment(sketch, "E357", {"start": v(142.46, 234.43) * mm, "end": v(142.64, 234.36) * mm});
            skLineSegment(sketch, "E358", {"start": v(142.64, 234.36) * mm, "end": v(142.8, 234.27) * mm});
            skLineSegment(sketch, "E359", {"start": v(142.8, 234.27) * mm, "end": v(142.96, 234.16) * mm});
            skLineSegment(sketch, "E360", {"start": v(142.96, 234.16) * mm, "end": v(143.1, 234.03) * mm});
            skLineSegment(sketch, "E361", {"start": v(143.1, 234.03) * mm, "end": v(143.21, 233.88) * mm});
            skLineSegment(sketch, "E362", {"start": v(143.21, 233.88) * mm, "end": v(143.31, 233.72) * mm});
            skLineSegment(sketch, "E363", {"start": v(143.31, 233.72) * mm, "end": v(143.4, 233.55) * mm});
            skLineSegment(sketch, "E364", {"start": v(143.4, 233.55) * mm, "end": v(143.45, 233.37) * mm});
            skLineSegment(sketch, "E365", {"start": v(143.45, 233.37) * mm, "end": v(143.49, 233.19) * mm});
            skLineSegment(sketch, "E366", {"start": v(143.49, 233.19) * mm, "end": v(143.5, 233) * mm});
            skLineSegment(sketch, "E367", {"start": v(143.5, 233) * mm, "end": v(143.49, 232.81) * mm});
            skLineSegment(sketch, "E368", {"start": v(143.49, 232.81) * mm, "end": v(143.45, 232.63) * mm});
            skLineSegment(sketch, "E369", {"start": v(143.45, 232.63) * mm, "end": v(143.4, 232.45) * mm});
            skLineSegment(sketch, "E370", {"start": v(143.4, 232.45) * mm, "end": v(143.31, 232.28) * mm});
            skLineSegment(sketch, "E371", {"start": v(143.31, 232.28) * mm, "end": v(143.21, 232.12) * mm});
            skLineSegment(sketch, "E372", {"start": v(143.21, 232.12) * mm, "end": v(143.1, 231.97) * mm});
            skLineSegment(sketch, "E373", {"start": v(143.1, 231.97) * mm, "end": v(142.96, 231.84) * mm});
            skLineSegment(sketch, "E374", {"start": v(142.96, 231.84) * mm, "end": v(142.8, 231.73) * mm});
            skLineSegment(sketch, "E375", {"start": v(142.8, 231.73) * mm, "end": v(142.64, 231.64) * mm});
            skLineSegment(sketch, "E376", {"start": v(142.64, 231.64) * mm, "end": v(142.46, 231.57) * mm});
            skLineSegment(sketch, "E377", {"start": v(142.46, 231.57) * mm, "end": v(142.28, 231.53) * mm});
            skLineSegment(sketch, "E378", {"start": v(142.28, 231.53) * mm, "end": v(142.1, 231.5) * mm});
            skLineSegment(sketch, "E379", {"start": v(142.1, 231.5) * mm, "end": v(141.9, 231.5) * mm});
            skLineSegment(sketch, "E380", {"start": v(220.4, 225) * mm, "end": v(220.32, 225.01) * mm});
            skLineSegment(sketch, "E381", {"start": v(220.32, 225.01) * mm, "end": v(220.22, 225.03) * mm});
            skLineSegment(sketch, "E382", {"start": v(220.22, 225.03) * mm, "end": v(220.19, 225.03) * mm});
            skLineSegment(sketch, "E383", {"start": v(220.19, 225.03) * mm, "end": v(220.06, 225.07) * mm});
            skLineSegment(sketch, "E384", {"start": v(220.06, 225.07) * mm, "end": v(219.93, 225.11) * mm});
            skLineSegment(sketch, "E385", {"start": v(219.93, 225.11) * mm, "end": v(219.86, 225.14) * mm});
            skLineSegment(sketch, "E386", {"start": v(219.86, 225.14) * mm, "end": v(219.8, 225.17) * mm});
            skLineSegment(sketch, "E387", {"start": v(219.8, 225.17) * mm, "end": v(219.7, 225.23) * mm});
            skLineSegment(sketch, "E388", {"start": v(219.7, 225.23) * mm, "end": v(219.59, 225.31) * mm});
            skLineSegment(sketch, "E389", {"start": v(219.59, 225.31) * mm, "end": v(219.54, 225.34) * mm});
            skLineSegment(sketch, "E390", {"start": v(219.54, 225.34) * mm, "end": v(219.48, 225.4) * mm});
            skLineSegment(sketch, "E391", {"start": v(219.48, 225.4) * mm, "end": v(219.4, 225.47) * mm});
            skLineSegment(sketch, "E392", {"start": v(219.4, 225.47) * mm, "end": v(219.38, 225.5) * mm});
            skLineSegment(sketch, "E393", {"start": v(219.38, 225.5) * mm, "end": v(219.3, 225.6) * mm});
            skLineSegment(sketch, "E394", {"start": v(219.3, 225.6) * mm, "end": v(219.22, 225.71) * mm});
            skLineSegment(sketch, "E395", {"start": v(219.22, 225.71) * mm, "end": v(219.2, 225.75) * mm});
            skLineSegment(sketch, "E396", {"start": v(219.2, 225.75) * mm, "end": v(219.19, 225.78) * mm});
            skLineSegment(sketch, "E397", {"start": v(219.19, 225.78) * mm, "end": v(219.16, 225.83) * mm});
            skLineSegment(sketch, "E398", {"start": v(219.16, 225.83) * mm, "end": v(219.1, 225.95) * mm});
            skLineSegment(sketch, "E399", {"start": v(219.1, 225.95) * mm, "end": v(219.06, 226.08) * mm});
            skLineSegment(sketch, "E400", {"start": v(219.06, 226.08) * mm, "end": v(219.05, 226.13) * mm});
            skLineSegment(sketch, "E401", {"start": v(219.05, 226.13) * mm, "end": v(219.03, 226.2) * mm});
            skLineSegment(sketch, "E402", {"start": v(219.03, 226.2) * mm, "end": v(219.01, 226.31) * mm});
            skLineSegment(sketch, "E403", {"start": v(219.01, 226.31) * mm, "end": v(219, 226.34) * mm});
            skLineSegment(sketch, "E404", {"start": v(219, 226.34) * mm, "end": v(219, 226.47) * mm});
            skLineSegment(sketch, "E405", {"start": v(219, 226.47) * mm, "end": v(219, 226.61) * mm});
            skLineSegment(sketch, "E406", {"start": v(219, 226.61) * mm, "end": v(219, 226.66) * mm});
            skLineSegment(sketch, "E407", {"start": v(219, 226.66) * mm, "end": v(219.01, 226.69) * mm});
            skLineSegment(sketch, "E408", {"start": v(219.01, 226.69) * mm, "end": v(219.02, 226.75) * mm});
            skLineSegment(sketch, "E409", {"start": v(219.02, 226.75) * mm, "end": v(219.05, 226.87) * mm});
            skLineSegment(sketch, "E410", {"start": v(219.05, 226.87) * mm, "end": v(219.09, 227) * mm});
            skLineSegment(sketch, "E411", {"start": v(219.09, 227) * mm, "end": v(219.1, 227.05) * mm});
            skLineSegment(sketch, "E412", {"start": v(219.1, 227.05) * mm, "end": v(219.14, 227.13) * mm});
            skLineSegment(sketch, "E413", {"start": v(219.14, 227.13) * mm, "end": v(219.19, 227.22) * mm});
            skLineSegment(sketch, "E414", {"start": v(219.19, 227.22) * mm, "end": v(219.2, 227.25) * mm});
            skLineSegment(sketch, "E415", {"start": v(219.2, 227.25) * mm, "end": v(219.27, 227.36) * mm});
            skLineSegment(sketch, "E416", {"start": v(219.27, 227.36) * mm, "end": v(219.35, 227.47) * mm});
            skLineSegment(sketch, "E417", {"start": v(219.35, 227.47) * mm, "end": v(219.4, 227.53) * mm});
            skLineSegment(sketch, "E418", {"start": v(219.4, 227.53) * mm, "end": v(219.45, 227.57) * mm});
            skLineSegment(sketch, "E419", {"start": v(219.45, 227.57) * mm, "end": v(219.54, 227.66) * mm});
            skLineSegment(sketch, "E420", {"start": v(219.54, 227.66) * mm, "end": v(219.65, 227.74) * mm});
            skLineSegment(sketch, "E421", {"start": v(219.65, 227.74) * mm, "end": v(219.7, 227.77) * mm});
            skLineSegment(sketch, "E422", {"start": v(219.7, 227.77) * mm, "end": v(219.77, 227.8) * mm});
            skLineSegment(sketch, "E423", {"start": v(219.77, 227.8) * mm, "end": v(219.86, 227.86) * mm});
            skLineSegment(sketch, "E424", {"start": v(219.86, 227.86) * mm, "end": v(219.9, 227.87) * mm});
            skLineSegment(sketch, "E425", {"start": v(219.9, 227.87) * mm, "end": v(220.01, 227.92) * mm});
            skLineSegment(sketch, "E426", {"start": v(220.01, 227.92) * mm, "end": v(220.14, 227.96) * mm});
            skLineSegment(sketch, "E427", {"start": v(220.14, 227.96) * mm, "end": v(220.22, 227.97) * mm});
            skLineSegment(sketch, "E428", {"start": v(220.22, 227.97) * mm, "end": v(220.28, 227.98) * mm});
            skLineSegment(sketch, "E429", {"start": v(220.28, 227.98) * mm, "end": v(220.4, 228) * mm});
            skLineSegment(sketch, "E430", {"start": v(220.4, 228) * mm, "end": v(220.54, 228) * mm});
            skLineSegment(sketch, "E431", {"start": v(220.54, 228) * mm, "end": v(220.6, 228) * mm});
            skLineSegment(sketch, "E432", {"start": v(220.6, 228) * mm, "end": v(220.68, 227.99) * mm});
            skLineSegment(sketch, "E433", {"start": v(220.68, 227.99) * mm, "end": v(220.78, 227.97) * mm});
            skLineSegment(sketch, "E434", {"start": v(220.78, 227.97) * mm, "end": v(220.81, 227.97) * mm});
            skLineSegment(sketch, "E435", {"start": v(220.81, 227.97) * mm, "end": v(220.94, 227.93) * mm});
            skLineSegment(sketch, "E436", {"start": v(220.94, 227.93) * mm, "end": v(221.07, 227.89) * mm});
            skLineSegment(sketch, "E437", {"start": v(221.07, 227.89) * mm, "end": v(221.14, 227.86) * mm});
            skLineSegment(sketch, "E438", {"start": v(221.14, 227.86) * mm, "end": v(221.2, 227.83) * mm});
            skLineSegment(sketch, "E439", {"start": v(221.2, 227.83) * mm, "end": v(221.3, 227.77) * mm});
            skLineSegment(sketch, "E440", {"start": v(221.3, 227.77) * mm, "end": v(221.41, 227.69) * mm});
            skLineSegment(sketch, "E441", {"start": v(221.41, 227.69) * mm, "end": v(221.46, 227.66) * mm});
            skLineSegment(sketch, "E442", {"start": v(221.46, 227.66) * mm, "end": v(221.52, 227.6) * mm});
            skLineSegment(sketch, "E443", {"start": v(221.52, 227.6) * mm, "end": v(221.6, 227.53) * mm});
            skLineSegment(sketch, "E444", {"start": v(221.6, 227.53) * mm, "end": v(221.62, 227.5) * mm});
            skLineSegment(sketch, "E445", {"start": v(221.62, 227.5) * mm, "end": v(221.7, 227.4) * mm});
            skLineSegment(sketch, "E446", {"start": v(221.7, 227.4) * mm, "end": v(221.78, 227.29) * mm});
            skLineSegment(sketch, "E447", {"start": v(221.78, 227.29) * mm, "end": v(221.81, 227.22) * mm});
            skLineSegment(sketch, "E448", {"start": v(221.81, 227.22) * mm, "end": v(221.84, 227.17) * mm});
            skLineSegment(sketch, "E449", {"start": v(221.84, 227.17) * mm, "end": v(221.9, 227.05) * mm});
            skLineSegment(sketch, "E450", {"start": v(221.9, 227.05) * mm, "end": v(221.94, 226.92) * mm});
            skLineSegment(sketch, "E451", {"start": v(221.94, 226.92) * mm, "end": v(221.95, 226.87) * mm});
            skLineSegment(sketch, "E452", {"start": v(221.95, 226.87) * mm, "end": v(221.97, 226.8) * mm});
            skLineSegment(sketch, "E453", {"start": v(221.97, 226.8) * mm, "end": v(221.99, 226.69) * mm});
            skLineSegment(sketch, "E454", {"start": v(221.99, 226.69) * mm, "end": v(222, 226.66) * mm});
            skLineSegment(sketch, "E455", {"start": v(222, 226.66) * mm, "end": v(222, 226.53) * mm});
            skLineSegment(sketch, "E456", {"start": v(222, 226.53) * mm, "end": v(222, 226.39) * mm});
            skLineSegment(sketch, "E457", {"start": v(222, 226.39) * mm, "end": v(221.99, 226.31) * mm});
            skLineSegment(sketch, "E458", {"start": v(221.99, 226.31) * mm, "end": v(221.98, 226.26) * mm});
            skLineSegment(sketch, "E459", {"start": v(221.98, 226.26) * mm, "end": v(221.95, 226.13) * mm});
            skLineSegment(sketch, "E460", {"start": v(221.95, 226.13) * mm, "end": v(221.91, 226) * mm});
            skLineSegment(sketch, "E461", {"start": v(221.91, 226) * mm, "end": v(221.9, 225.95) * mm});
            skLineSegment(sketch, "E462", {"start": v(221.9, 225.95) * mm, "end": v(221.86, 225.87) * mm});
            skLineSegment(sketch, "E463", {"start": v(221.86, 225.87) * mm, "end": v(221.81, 225.78) * mm});
            skLineSegment(sketch, "E464", {"start": v(221.81, 225.78) * mm, "end": v(221.8, 225.75) * mm});
            skLineSegment(sketch, "E465", {"start": v(221.8, 225.75) * mm, "end": v(221.73, 225.64) * mm});
            skLineSegment(sketch, "E466", {"start": v(221.73, 225.64) * mm, "end": v(221.65, 225.53) * mm});
            skLineSegment(sketch, "E467", {"start": v(221.65, 225.53) * mm, "end": v(221.6, 225.47) * mm});
            skLineSegment(sketch, "E468", {"start": v(221.6, 225.47) * mm, "end": v(221.55, 225.43) * mm});
            skLineSegment(sketch, "E469", {"start": v(221.55, 225.43) * mm, "end": v(221.46, 225.34) * mm});
            skLineSegment(sketch, "E470", {"start": v(221.46, 225.34) * mm, "end": v(221.35, 225.26) * mm});
            skLineSegment(sketch, "E471", {"start": v(221.35, 225.26) * mm, "end": v(221.3, 225.23) * mm});
            skLineSegment(sketch, "E472", {"start": v(221.3, 225.23) * mm, "end": v(221.23, 225.2) * mm});
            skLineSegment(sketch, "E473", {"start": v(221.23, 225.2) * mm, "end": v(221.14, 225.14) * mm});
            skLineSegment(sketch, "E474", {"start": v(221.14, 225.14) * mm, "end": v(221.11, 225.13) * mm});
            skLineSegment(sketch, "E475", {"start": v(221.11, 225.13) * mm, "end": v(220.99, 225.08) * mm});
            skLineSegment(sketch, "E476", {"start": v(220.99, 225.08) * mm, "end": v(220.86, 225.04) * mm});
            skLineSegment(sketch, "E477", {"start": v(220.86, 225.04) * mm, "end": v(220.8, 225.03) * mm});
            skLineSegment(sketch, "E478", {"start": v(220.8, 225.03) * mm, "end": v(220.78, 225.03) * mm});
            skLineSegment(sketch, "E479", {"start": v(220.78, 225.03) * mm, "end": v(220.72, 225.02) * mm});
            skLineSegment(sketch, "E480", {"start": v(220.72, 225.02) * mm, "end": v(220.6, 225) * mm});
            skLineSegment(sketch, "E481", {"start": v(220.6, 225) * mm, "end": v(220.46, 225) * mm});
            skLineSegment(sketch, "E482", {"start": v(220.46, 225) * mm, "end": v(220.4, 225) * mm});
            skLineSegment(sketch, "E483", {"start": v(189.54, 220.7) * mm, "end": v(189.36, 220.75) * mm});
            skLineSegment(sketch, "E484", {"start": v(189.36, 220.75) * mm, "end": v(189.18, 220.82) * mm});
            skLineSegment(sketch, "E485", {"start": v(189.18, 220.82) * mm, "end": v(189.02, 220.9) * mm});
            skLineSegment(sketch, "E486", {"start": v(189.02, 220.9) * mm, "end": v(188.86, 221.02) * mm});
            skLineSegment(sketch, "E487", {"start": v(188.86, 221.02) * mm, "end": v(188.72, 221.14) * mm});
            skLineSegment(sketch, "E488", {"start": v(188.72, 221.14) * mm, "end": v(188.6, 221.29) * mm});
            skLineSegment(sketch, "E489", {"start": v(188.6, 221.29) * mm, "end": v(188.5, 221.44) * mm});
            skLineSegment(sketch, "E490", {"start": v(188.5, 221.44) * mm, "end": v(188.41, 221.61) * mm});
            skLineSegment(sketch, "E491", {"start": v(188.41, 221.61) * mm, "end": v(188.35, 221.8) * mm});
            skLineSegment(sketch, "E492", {"start": v(188.35, 221.8) * mm, "end": v(188.32, 221.98) * mm});
            skLineSegment(sketch, "E493", {"start": v(188.32, 221.98) * mm, "end": v(188.3, 222.16) * mm});
            skLineSegment(sketch, "E494", {"start": v(188.3, 222.16) * mm, "end": v(188.3, 222.26) * mm});
            skLineSegment(sketch, "E495", {"start": v(188.3, 222.26) * mm, "end": v(188.28, 222.35) * mm});
            skLineSegment(sketch, "E496", {"start": v(188.28, 222.35) * mm, "end": v(188.24, 222.54) * mm});
            skLineSegment(sketch, "E497", {"start": v(188.24, 222.54) * mm, "end": v(188.23, 222.73) * mm});
            skLineSegment(sketch, "E498", {"start": v(188.23, 222.73) * mm, "end": v(188.24, 222.82) * mm});
            skLineSegment(sketch, "E499", {"start": v(188.24, 222.82) * mm, "end": v(188.2, 222.92) * mm});
            skLineSegment(sketch, "E500", {"start": v(188.2, 222.92) * mm, "end": v(188.18, 223.1) * mm});
            skLineSegment(sketch, "E501", {"start": v(188.18, 223.1) * mm, "end": v(188.17, 223.3) * mm});
            skLineSegment(sketch, "E502", {"start": v(188.17, 223.3) * mm, "end": v(188.18, 223.39) * mm});
            skLineSegment(sketch, "E503", {"start": v(188.18, 223.39) * mm, "end": v(188.15, 223.48) * mm});
            skLineSegment(sketch, "E504", {"start": v(188.15, 223.48) * mm, "end": v(188.12, 223.67) * mm});
            skLineSegment(sketch, "E505", {"start": v(188.12, 223.67) * mm, "end": v(188.12, 223.86) * mm});
            skLineSegment(sketch, "E506", {"start": v(188.12, 223.86) * mm, "end": v(188.13, 223.95) * mm});
            skLineSegment(sketch, "E507", {"start": v(188.13, 223.95) * mm, "end": v(188.1, 224.05) * mm});
            skLineSegment(sketch, "E508", {"start": v(188.1, 224.05) * mm, "end": v(188.08, 224.23) * mm});
            skLineSegment(sketch, "E509", {"start": v(188.08, 224.23) * mm, "end": v(188.08, 224.42) * mm});
            skLineSegment(sketch, "E510", {"start": v(188.08, 224.42) * mm, "end": v(188.09, 224.52) * mm});
            skLineSegment(sketch, "E511", {"start": v(188.09, 224.52) * mm, "end": v(188.07, 224.61) * mm});
            skLineSegment(sketch, "E512", {"start": v(188.07, 224.61) * mm, "end": v(188.04, 224.8) * mm});
            skLineSegment(sketch, "E513", {"start": v(188.04, 224.8) * mm, "end": v(188.05, 224.99) * mm});
            skLineSegment(sketch, "E514", {"start": v(188.05, 224.99) * mm, "end": v(188.06, 225.08) * mm});
            skLineSegment(sketch, "E515", {"start": v(188.06, 225.08) * mm, "end": v(188.04, 225.18) * mm});
            skLineSegment(sketch, "E516", {"start": v(188.04, 225.18) * mm, "end": v(188.02, 225.37) * mm});
            skLineSegment(sketch, "E517", {"start": v(188.02, 225.37) * mm, "end": v(188.03, 225.55) * mm});
            skLineSegment(sketch, "E518", {"start": v(188.03, 225.55) * mm, "end": v(188.04, 225.65) * mm});
            skLineSegment(sketch, "E519", {"start": v(188.04, 225.65) * mm, "end": v(188.02, 225.75) * mm});
            skLineSegment(sketch, "E520", {"start": v(188.02, 225.75) * mm, "end": v(188, 225.93) * mm});
            skLineSegment(sketch, "E521", {"start": v(188, 225.93) * mm, "end": v(188.01, 226.12) * mm});
            skLineSegment(sketch, "E522", {"start": v(188.01, 226.12) * mm, "end": v(188.03, 226.22) * mm});
            skLineSegment(sketch, "E523", {"start": v(188.03, 226.22) * mm, "end": v(188.01, 226.31) * mm});
            skLineSegment(sketch, "E524", {"start": v(188.01, 226.31) * mm, "end": v(188, 226.5) * mm});
            skLineSegment(sketch, "E525", {"start": v(188, 226.5) * mm, "end": v(188.01, 226.69) * mm});
            skLineSegment(sketch, "E526", {"start": v(188.01, 226.69) * mm, "end": v(188.05, 226.87) * mm});
            skLineSegment(sketch, "E527", {"start": v(188.05, 226.87) * mm, "end": v(188.1, 227.05) * mm});
            skLineSegment(sketch, "E528", {"start": v(188.1, 227.05) * mm, "end": v(188.19, 227.22) * mm});
            skLineSegment(sketch, "E529", {"start": v(188.19, 227.22) * mm, "end": v(188.29, 227.38) * mm});
            skLineSegment(sketch, "E530", {"start": v(188.29, 227.38) * mm, "end": v(188.4, 227.53) * mm});
            skLineSegment(sketch, "E531", {"start": v(188.4, 227.53) * mm, "end": v(188.54, 227.66) * mm});
            skLineSegment(sketch, "E532", {"start": v(188.54, 227.66) * mm, "end": v(188.7, 227.77) * mm});
            skLineSegment(sketch, "E533", {"start": v(188.7, 227.77) * mm, "end": v(188.86, 227.86) * mm});
            skLineSegment(sketch, "E534", {"start": v(188.86, 227.86) * mm, "end": v(189.04, 227.93) * mm});
            skLineSegment(sketch, "E535", {"start": v(189.04, 227.93) * mm, "end": v(189.22, 227.97) * mm});
            skLineSegment(sketch, "E536", {"start": v(189.22, 227.97) * mm, "end": v(189.4, 228) * mm});
            skLineSegment(sketch, "E537", {"start": v(189.4, 228) * mm, "end": v(189.6, 228) * mm});
            skLineSegment(sketch, "E538", {"start": v(189.6, 228) * mm, "end": v(189.78, 227.97) * mm});
            skLineSegment(sketch, "E539", {"start": v(189.78, 227.97) * mm, "end": v(189.96, 227.93) * mm});
            skLineSegment(sketch, "E540", {"start": v(189.96, 227.93) * mm, "end": v(190.14, 227.86) * mm});
            skLineSegment(sketch, "E541", {"start": v(190.14, 227.86) * mm, "end": v(190.3, 227.77) * mm});
            skLineSegment(sketch, "E542", {"start": v(190.3, 227.77) * mm, "end": v(190.46, 227.66) * mm});
            skLineSegment(sketch, "E543", {"start": v(190.46, 227.66) * mm, "end": v(190.6, 227.53) * mm});
            skLineSegment(sketch, "E544", {"start": v(190.6, 227.53) * mm, "end": v(190.71, 227.38) * mm});
            skLineSegment(sketch, "E545", {"start": v(190.71, 227.38) * mm, "end": v(190.81, 227.22) * mm});
            skLineSegment(sketch, "E546", {"start": v(190.81, 227.22) * mm, "end": v(190.9, 227.05) * mm});
            skLineSegment(sketch, "E547", {"start": v(190.9, 227.05) * mm, "end": v(190.95, 226.87) * mm});
            skLineSegment(sketch, "E548", {"start": v(190.95, 226.87) * mm, "end": v(190.99, 226.69) * mm});
            skLineSegment(sketch, "E549", {"start": v(190.99, 226.69) * mm, "end": v(191, 226.5) * mm});
            skLineSegment(sketch, "E550", {"start": v(191, 226.5) * mm, "end": v(190.99, 226.31) * mm});
            skLineSegment(sketch, "E551", {"start": v(190.99, 226.31) * mm, "end": v(190.97, 226.24) * mm});
            skLineSegment(sketch, "E552", {"start": v(190.97, 226.24) * mm, "end": v(190.99, 226.17) * mm});
            skLineSegment(sketch, "E553", {"start": v(190.99, 226.17) * mm, "end": v(191, 225.99) * mm});
            skLineSegment(sketch, "E554", {"start": v(191, 225.99) * mm, "end": v(191, 225.8) * mm});
            skLineSegment(sketch, "E555", {"start": v(191, 225.8) * mm, "end": v(190.98, 225.73) * mm});
            skLineSegment(sketch, "E556", {"start": v(190.98, 225.73) * mm, "end": v(191, 225.66) * mm});
            skLineSegment(sketch, "E557", {"start": v(191, 225.66) * mm, "end": v(191.02, 225.47) * mm});
            skLineSegment(sketch, "E558", {"start": v(191.02, 225.47) * mm, "end": v(191.01, 225.28) * mm});
            skLineSegment(sketch, "E559", {"start": v(191.01, 225.28) * mm, "end": v(191, 225.21) * mm});
            skLineSegment(sketch, "E560", {"start": v(191, 225.21) * mm, "end": v(191.02, 225.14) * mm});
            skLineSegment(sketch, "E561", {"start": v(191.02, 225.14) * mm, "end": v(191.04, 224.96) * mm});
            skLineSegment(sketch, "E562", {"start": v(191.04, 224.96) * mm, "end": v(191.04, 224.77) * mm});
            skLineSegment(sketch, "E563", {"start": v(191.04, 224.77) * mm, "end": v(191.03, 224.7) * mm});
            skLineSegment(sketch, "E564", {"start": v(191.03, 224.7) * mm, "end": v(191.05, 224.63) * mm});
            skLineSegment(sketch, "E565", {"start": v(191.05, 224.63) * mm, "end": v(191.07, 224.44) * mm});
            skLineSegment(sketch, "E566", {"start": v(191.07, 224.44) * mm, "end": v(191.07, 224.25) * mm});
            skLineSegment(sketch, "E567", {"start": v(191.07, 224.25) * mm, "end": v(191.07, 224.18) * mm});
            skLineSegment(sketch, "E568", {"start": v(191.07, 224.18) * mm, "end": v(191.08, 224.12) * mm});
            skLineSegment(sketch, "E569", {"start": v(191.08, 224.12) * mm, "end": v(191.11, 223.93) * mm});
            skLineSegment(sketch, "E570", {"start": v(191.11, 223.93) * mm, "end": v(191.12, 223.74) * mm});
            skLineSegment(sketch, "E571", {"start": v(191.12, 223.74) * mm, "end": v(191.11, 223.67) * mm});
            skLineSegment(sketch, "E572", {"start": v(191.11, 223.67) * mm, "end": v(191.13, 223.6) * mm});
            skLineSegment(sketch, "E573", {"start": v(191.13, 223.6) * mm, "end": v(191.16, 223.42) * mm});
            skLineSegment(sketch, "E574", {"start": v(191.16, 223.42) * mm, "end": v(191.17, 223.23) * mm});
            skLineSegment(sketch, "E575", {"start": v(191.17, 223.23) * mm, "end": v(191.16, 223.16) * mm});
            skLineSegment(sketch, "E576", {"start": v(191.16, 223.16) * mm, "end": v(191.19, 223.1) * mm});
            skLineSegment(sketch, "E577", {"start": v(191.19, 223.1) * mm, "end": v(191.22, 222.9) * mm});
            skLineSegment(sketch, "E578", {"start": v(191.22, 222.9) * mm, "end": v(191.23, 222.72) * mm});
            skLineSegment(sketch, "E579", {"start": v(191.23, 222.72) * mm, "end": v(191.23, 222.65) * mm});
            skLineSegment(sketch, "E580", {"start": v(191.23, 222.65) * mm, "end": v(191.25, 222.58) * mm});
            skLineSegment(sketch, "E581", {"start": v(191.25, 222.58) * mm, "end": v(191.29, 222.4) * mm});
            skLineSegment(sketch, "E582", {"start": v(191.29, 222.4) * mm, "end": v(191.3, 222.2) * mm});
            skLineSegment(sketch, "E583", {"start": v(191.3, 222.2) * mm, "end": v(191.3, 222.02) * mm});
            skLineSegment(sketch, "E584", {"start": v(191.3, 222.02) * mm, "end": v(191.26, 221.83) * mm});
            skLineSegment(sketch, "E585", {"start": v(191.26, 221.83) * mm, "end": v(191.2, 221.65) * mm});
            skLineSegment(sketch, "E586", {"start": v(191.2, 221.65) * mm, "end": v(191.13, 221.48) * mm});
            skLineSegment(sketch, "E587", {"start": v(191.13, 221.48) * mm, "end": v(191.03, 221.32) * mm});
            skLineSegment(sketch, "E588", {"start": v(191.03, 221.32) * mm, "end": v(190.9, 221.17) * mm});
            skLineSegment(sketch, "E589", {"start": v(190.9, 221.17) * mm, "end": v(190.77, 221.04) * mm});
            skLineSegment(sketch, "E590", {"start": v(190.77, 221.04) * mm, "end": v(190.62, 220.93) * mm});
            skLineSegment(sketch, "E591", {"start": v(190.62, 220.93) * mm, "end": v(190.46, 220.84) * mm});
            skLineSegment(sketch, "E592", {"start": v(190.46, 220.84) * mm, "end": v(190.28, 220.77) * mm});
            skLineSegment(sketch, "E593", {"start": v(190.28, 220.77) * mm, "end": v(190.1, 220.72) * mm});
            skLineSegment(sketch, "E594", {"start": v(190.1, 220.72) * mm, "end": v(189.92, 220.7) * mm});
            skLineSegment(sketch, "E595", {"start": v(189.92, 220.7) * mm, "end": v(189.73, 220.69) * mm});
            skLineSegment(sketch, "E596", {"start": v(189.73, 220.69) * mm, "end": v(189.54, 220.7) * mm});
            skLineSegment(sketch, "E597", {"start": v(122, -137) * mm, "end": v(122, -136.94) * mm});
            skLineSegment(sketch, "E598", {"start": v(122, -136.94) * mm, "end": v(120.12, -136.94) * mm});
            skLineSegment(sketch, "E599", {"start": v(120.12, -136.94) * mm, "end": v(116.38, -136.47) * mm});
            skLineSegment(sketch, "E600", {"start": v(116.38, -136.47) * mm, "end": v(112.73, -135.53) * mm});
            skLineSegment(sketch, "E601", {"start": v(112.73, -135.53) * mm, "end": v(109.23, -134.15) * mm});
            skLineSegment(sketch, "E602", {"start": v(109.23, -134.15) * mm, "end": v(105.93, -132.33) * mm});
            skLineSegment(sketch, "E603", {"start": v(105.93, -132.33) * mm, "end": v(102.88, -130.12) * mm});
            skLineSegment(sketch, "E604", {"start": v(102.88, -130.12) * mm, "end": v(100.13, -127.54) * mm});
            skLineSegment(sketch, "E605", {"start": v(100.13, -127.54) * mm, "end": v(97.73, -124.63) * mm});
            skLineSegment(sketch, "E606", {"start": v(97.73, -124.63) * mm, "end": v(95.71, -121.45) * mm});
            skLineSegment(sketch, "E607", {"start": v(95.71, -121.45) * mm, "end": v(94.1, -118.04) * mm});
            skLineSegment(sketch, "E608", {"start": v(94.1, -118.04) * mm, "end": v(92.94, -114.46) * mm});
            skLineSegment(sketch, "E609", {"start": v(92.94, -114.46) * mm, "end": v(92.24, -110.76) * mm});
            skLineSegment(sketch, "E610", {"start": v(92.24, -110.76) * mm, "end": v(92, -107) * mm});
            skLineSegment(sketch, "E611", {"start": v(92, -107) * mm, "end": v(92, 154.6) * mm});
            skLineSegment(sketch, "E612", {"start": v(92, 154.6) * mm, "end": v(92.02, 154.6) * mm});
            skLineSegment(sketch, "E613", {"start": v(92.02, 154.6) * mm, "end": v(92.02, 155.23) * mm});
            skLineSegment(sketch, "E614", {"start": v(92.02, 155.23) * mm, "end": v(92.18, 156.47) * mm});
            skLineSegment(sketch, "E615", {"start": v(92.18, 156.47) * mm, "end": v(92.49, 157.7) * mm});
            skLineSegment(sketch, "E616", {"start": v(92.49, 157.7) * mm, "end": v(92.95, 158.86) * mm});
            skLineSegment(sketch, "E617", {"start": v(92.95, 158.86) * mm, "end": v(93.56, 159.96) * mm});
            skLineSegment(sketch, "E618", {"start": v(93.56, 159.96) * mm, "end": v(94.3, 160.97) * mm});
            skLineSegment(sketch, "E619", {"start": v(94.3, 160.97) * mm, "end": v(95.15, 161.89) * mm});
            skLineSegment(sketch, "E620", {"start": v(95.15, 161.89) * mm, "end": v(96.12, 162.7) * mm});
            skLineSegment(sketch, "E621", {"start": v(96.12, 162.7) * mm, "end": v(97.18, 163.36) * mm});
            skLineSegment(sketch, "E622", {"start": v(97.18, 163.36) * mm, "end": v(98.32, 163.9) * mm});
            skLineSegment(sketch, "E623", {"start": v(98.32, 163.9) * mm, "end": v(99.51, 164.29) * mm});
            skLineSegment(sketch, "E624", {"start": v(99.51, 164.29) * mm, "end": v(100.75, 164.52) * mm});
            skLineSegment(sketch, "E625", {"start": v(100.75, 164.52) * mm, "end": v(102, 164.6) * mm});
            skLineSegment(sketch, "E626", {"start": v(102, 164.6) * mm, "end": v(108.8, 164.6) * mm});
            skLineSegment(sketch, "E627", {"start": v(108.8, 164.6) * mm, "end": v(109.83, 164.66) * mm});
            skLineSegment(sketch, "E628", {"start": v(109.83, 164.66) * mm, "end": v(110.84, 164.86) * mm});
            skLineSegment(sketch, "E629", {"start": v(110.84, 164.86) * mm, "end": v(111.82, 165.18) * mm});
            skLineSegment(sketch, "E630", {"start": v(111.82, 165.18) * mm, "end": v(112.75, 165.61) * mm});
            skLineSegment(sketch, "E631", {"start": v(112.75, 165.61) * mm, "end": v(113.62, 166.17) * mm});
            skLineSegment(sketch, "E632", {"start": v(113.62, 166.17) * mm, "end": v(114.41, 166.82) * mm});
            skLineSegment(sketch, "E633", {"start": v(114.41, 166.82) * mm, "end": v(115.12, 167.57) * mm});
            skLineSegment(sketch, "E634", {"start": v(115.12, 167.57) * mm, "end": v(115.72, 168.4) * mm});
            skLineSegment(sketch, "E635", {"start": v(115.72, 168.4) * mm, "end": v(116.22, 169.3) * mm});
            skLineSegment(sketch, "E636", {"start": v(116.22, 169.3) * mm, "end": v(116.6, 170.27) * mm});
            skLineSegment(sketch, "E637", {"start": v(116.6, 170.27) * mm, "end": v(116.86, 171.26) * mm});
            skLineSegment(sketch, "E638", {"start": v(116.86, 171.26) * mm, "end": v(116.98, 172.28) * mm});
            skLineSegment(sketch, "E639", {"start": v(116.98, 172.28) * mm, "end": v(116.98, 172.8) * mm});
            skLineSegment(sketch, "E640", {"start": v(116.98, 172.8) * mm, "end": v(117, 172.8) * mm});
            skLineSegment(sketch, "E641", {"start": v(117, 172.8) * mm, "end": v(116.94, 173.83) * mm});
            skLineSegment(sketch, "E642", {"start": v(116.94, 173.83) * mm, "end": v(116.74, 174.84) * mm});
            skLineSegment(sketch, "E643", {"start": v(116.74, 174.84) * mm, "end": v(116.42, 175.82) * mm});
            skLineSegment(sketch, "E644", {"start": v(116.42, 175.82) * mm, "end": v(115.99, 176.75) * mm});
            skLineSegment(sketch, "E645", {"start": v(115.99, 176.75) * mm, "end": v(115.43, 177.62) * mm});
            skLineSegment(sketch, "E646", {"start": v(115.43, 177.62) * mm, "end": v(114.78, 178.41) * mm});
            skLineSegment(sketch, "E647", {"start": v(114.78, 178.41) * mm, "end": v(114.03, 179.12) * mm});
            skLineSegment(sketch, "E648", {"start": v(114.03, 179.12) * mm, "end": v(113.2, 179.72) * mm});
            skLineSegment(sketch, "E649", {"start": v(113.2, 179.72) * mm, "end": v(112.3, 180.22) * mm});
            skLineSegment(sketch, "E650", {"start": v(112.3, 180.22) * mm, "end": v(111.33, 180.6) * mm});
            skLineSegment(sketch, "E651", {"start": v(111.33, 180.6) * mm, "end": v(110.34, 180.85) * mm});
            skLineSegment(sketch, "E652", {"start": v(110.34, 180.85) * mm, "end": v(109.31, 180.98) * mm});
            skLineSegment(sketch, "E653", {"start": v(109.31, 180.98) * mm, "end": v(108.8, 180.98) * mm});
            skLineSegment(sketch, "E654", {"start": v(108.8, 180.98) * mm, "end": v(108.8, 181) * mm});
            skLineSegment(sketch, "E655", {"start": v(108.8, 181) * mm, "end": v(102, 181) * mm});
            skLineSegment(sketch, "E656", {"start": v(102, 181) * mm, "end": v(100.75, 181.08) * mm});
            skLineSegment(sketch, "E657", {"start": v(100.75, 181.08) * mm, "end": v(99.51, 181.31) * mm});
            skLineSegment(sketch, "E658", {"start": v(99.51, 181.31) * mm, "end": v(98.32, 181.7) * mm});
            skLineSegment(sketch, "E659", {"start": v(98.32, 181.7) * mm, "end": v(97.18, 182.24) * mm});
            skLineSegment(sketch, "E660", {"start": v(97.18, 182.24) * mm, "end": v(96.12, 182.9) * mm});
            skLineSegment(sketch, "E661", {"start": v(96.12, 182.9) * mm, "end": v(95.15, 183.71) * mm});
            skLineSegment(sketch, "E662", {"start": v(95.15, 183.71) * mm, "end": v(94.3, 184.63) * mm});
            skLineSegment(sketch, "E663", {"start": v(94.3, 184.63) * mm, "end": v(93.56, 185.64) * mm});
            skLineSegment(sketch, "E664", {"start": v(93.56, 185.64) * mm, "end": v(92.95, 186.74) * mm});
            skLineSegment(sketch, "E665", {"start": v(92.95, 186.74) * mm, "end": v(92.49, 187.9) * mm});
            skLineSegment(sketch, "E666", {"start": v(92.49, 187.9) * mm, "end": v(92.18, 189.13) * mm});
            skLineSegment(sketch, "E667", {"start": v(92.18, 189.13) * mm, "end": v(92.02, 190.37) * mm});
            skLineSegment(sketch, "E668", {"start": v(92.02, 190.37) * mm, "end": v(92.02, 191) * mm});
            skLineSegment(sketch, "E669", {"start": v(92.02, 191) * mm, "end": v(92, 191) * mm});
            skLineSegment(sketch, "E670", {"start": v(92, 191) * mm, "end": v(92, 193) * mm});
            skLineSegment(sketch, "E671", {"start": v(92, 193) * mm, "end": v(92.06, 193) * mm});
            skLineSegment(sketch, "E672", {"start": v(92.06, 193) * mm, "end": v(92.06, 194.88) * mm});
            skLineSegment(sketch, "E673", {"start": v(92.06, 194.88) * mm, "end": v(92.53, 198.62) * mm});
            skLineSegment(sketch, "E674", {"start": v(92.53, 198.62) * mm, "end": v(93.47, 202.27) * mm});
            skLineSegment(sketch, "E675", {"start": v(93.47, 202.27) * mm, "end": v(94.86, 205.77) * mm});
            skLineSegment(sketch, "E676", {"start": v(94.86, 205.77) * mm, "end": v(96.67, 209.07) * mm});
            skLineSegment(sketch, "E677", {"start": v(96.67, 209.07) * mm, "end": v(98.88, 212.12) * mm});
            skLineSegment(sketch, "E678", {"start": v(98.88, 212.12) * mm, "end": v(101.46, 214.87) * mm});
            skLineSegment(sketch, "E679", {"start": v(101.46, 214.87) * mm, "end": v(104.37, 217.27) * mm});
            skLineSegment(sketch, "E680", {"start": v(104.37, 217.27) * mm, "end": v(107.55, 219.29) * mm});
            skLineSegment(sketch, "E681", {"start": v(107.55, 219.29) * mm, "end": v(110.96, 220.9) * mm});
            skLineSegment(sketch, "E682", {"start": v(110.96, 220.9) * mm, "end": v(114.54, 222.06) * mm});
            skLineSegment(sketch, "E683", {"start": v(114.54, 222.06) * mm, "end": v(118.24, 222.76) * mm});
            skLineSegment(sketch, "E684", {"start": v(118.24, 222.76) * mm, "end": v(122, 223) * mm});
            skLineSegment(sketch, "E685", {"start": v(122, 223) * mm, "end": v(170, 223) * mm});
            skLineSegment(sketch, "E686", {"start": v(170, 223) * mm, "end": v(170, 222.98) * mm});
            skLineSegment(sketch, "E687", {"start": v(170, 222.98) * mm, "end": v(170.63, 222.98) * mm});
            skLineSegment(sketch, "E688", {"start": v(170.63, 222.98) * mm, "end": v(171.87, 222.82) * mm});
            skLineSegment(sketch, "E689", {"start": v(171.87, 222.82) * mm, "end": v(173.1, 222.51) * mm});
            skLineSegment(sketch, "E690", {"start": v(173.1, 222.51) * mm, "end": v(174.26, 222.05) * mm});
            skLineSegment(sketch, "E691", {"start": v(174.26, 222.05) * mm, "end": v(175.36, 221.44) * mm});
            skLineSegment(sketch, "E692", {"start": v(175.36, 221.44) * mm, "end": v(176.37, 220.7) * mm});
            skLineSegment(sketch, "E693", {"start": v(176.37, 220.7) * mm, "end": v(177.29, 219.84) * mm});
            skLineSegment(sketch, "E694", {"start": v(177.29, 219.84) * mm, "end": v(178.1, 218.88) * mm});
            skLineSegment(sketch, "E695", {"start": v(178.1, 218.88) * mm, "end": v(178.76, 217.82) * mm});
            skLineSegment(sketch, "E696", {"start": v(178.76, 217.82) * mm, "end": v(179.3, 216.68) * mm});
            skLineSegment(sketch, "E697", {"start": v(179.3, 216.68) * mm, "end": v(179.69, 215.49) * mm});
            skLineSegment(sketch, "E698", {"start": v(179.69, 215.49) * mm, "end": v(179.92, 214.25) * mm});
            skLineSegment(sketch, "E699", {"start": v(179.92, 214.25) * mm, "end": v(180, 213) * mm});
            skLineSegment(sketch, "E700", {"start": v(180, 213) * mm, "end": v(180, 192) * mm});
            skLineSegment(sketch, "E701", {"start": v(180, 192) * mm, "end": v(180, 192) * mm});
            skLineSegment(sketch, "E702", {"start": v(180, 192) * mm, "end": v(180, 191.69) * mm});
            skLineSegment(sketch, "E703", {"start": v(180, 191.69) * mm, "end": v(180.09, 191.06) * mm});
            skLineSegment(sketch, "E704", {"start": v(180.09, 191.06) * mm, "end": v(180.25, 190.46) * mm});
            skLineSegment(sketch, "E705", {"start": v(180.25, 190.46) * mm, "end": v(180.48, 189.87) * mm});
            skLineSegment(sketch, "E706", {"start": v(180.48, 189.87) * mm, "end": v(180.78, 189.32) * mm});
            skLineSegment(sketch, "E707", {"start": v(180.78, 189.32) * mm, "end": v(181.15, 188.81) * mm});
            skLineSegment(sketch, "E708", {"start": v(181.15, 188.81) * mm, "end": v(181.58, 188.35) * mm});
            skLineSegment(sketch, "E709", {"start": v(181.58, 188.35) * mm, "end": v(182.06, 187.96) * mm});
            skLineSegment(sketch, "E710", {"start": v(182.06, 187.96) * mm, "end": v(182.6, 187.62) * mm});
            skLineSegment(sketch, "E711", {"start": v(182.6, 187.62) * mm, "end": v(183.16, 187.35) * mm});
            skLineSegment(sketch, "E712", {"start": v(183.16, 187.35) * mm, "end": v(183.76, 187.16) * mm});
            skLineSegment(sketch, "E713", {"start": v(183.76, 187.16) * mm, "end": v(184.37, 187.04) * mm});
            skLineSegment(sketch, "E714", {"start": v(184.37, 187.04) * mm, "end": v(185, 187) * mm});
            skLineSegment(sketch, "E715", {"start": v(185, 187) * mm, "end": v(225, 187) * mm});
            skLineSegment(sketch, "E716", {"start": v(225, 187) * mm, "end": v(225, 187) * mm});
            skLineSegment(sketch, "E717", {"start": v(225, 187) * mm, "end": v(225.31, 187) * mm});
            skLineSegment(sketch, "E718", {"start": v(225.31, 187) * mm, "end": v(225.94, 187.09) * mm});
            skLineSegment(sketch, "E719", {"start": v(225.94, 187.09) * mm, "end": v(226.54, 187.25) * mm});
            skLineSegment(sketch, "E720", {"start": v(226.54, 187.25) * mm, "end": v(227.13, 187.48) * mm});
            skLineSegment(sketch, "E721", {"start": v(227.13, 187.48) * mm, "end": v(227.68, 187.78) * mm});
            skLineSegment(sketch, "E722", {"start": v(227.68, 187.78) * mm, "end": v(228.19, 188.15) * mm});
            skLineSegment(sketch, "E723", {"start": v(228.19, 188.15) * mm, "end": v(228.65, 188.58) * mm});
            skLineSegment(sketch, "E724", {"start": v(228.65, 188.58) * mm, "end": v(229.04, 189.06) * mm});
            skLineSegment(sketch, "E725", {"start": v(229.04, 189.06) * mm, "end": v(229.38, 189.6) * mm});
            skLineSegment(sketch, "E726", {"start": v(229.38, 189.6) * mm, "end": v(229.65, 190.16) * mm});
            skLineSegment(sketch, "E727", {"start": v(229.65, 190.16) * mm, "end": v(229.84, 190.76) * mm});
            skLineSegment(sketch, "E728", {"start": v(229.84, 190.76) * mm, "end": v(229.96, 191.37) * mm});
            skLineSegment(sketch, "E729", {"start": v(229.96, 191.37) * mm, "end": v(230, 192) * mm});
            skLineSegment(sketch, "E730", {"start": v(230, 192) * mm, "end": v(230, 213) * mm});
            skLineSegment(sketch, "E731", {"start": v(230, 213) * mm, "end": v(230.08, 214.25) * mm});
            skLineSegment(sketch, "E732", {"start": v(230.08, 214.25) * mm, "end": v(230.31, 215.49) * mm});
            skLineSegment(sketch, "E733", {"start": v(230.31, 215.49) * mm, "end": v(230.7, 216.68) * mm});
            skLineSegment(sketch, "E734", {"start": v(230.7, 216.68) * mm, "end": v(231.24, 217.82) * mm});
            skLineSegment(sketch, "E735", {"start": v(231.24, 217.82) * mm, "end": v(231.9, 218.88) * mm});
            skLineSegment(sketch, "E736", {"start": v(231.9, 218.88) * mm, "end": v(232.71, 219.84) * mm});
            skLineSegment(sketch, "E737", {"start": v(232.71, 219.84) * mm, "end": v(233.63, 220.7) * mm});
            skLineSegment(sketch, "E738", {"start": v(233.63, 220.7) * mm, "end": v(234.64, 221.44) * mm});
            skLineSegment(sketch, "E739", {"start": v(234.64, 221.44) * mm, "end": v(235.74, 222.05) * mm});
            skLineSegment(sketch, "E740", {"start": v(235.74, 222.05) * mm, "end": v(236.9, 222.51) * mm});
            skLineSegment(sketch, "E741", {"start": v(236.9, 222.51) * mm, "end": v(238.13, 222.82) * mm});
            skLineSegment(sketch, "E742", {"start": v(238.13, 222.82) * mm, "end": v(239.37, 222.98) * mm});
            skLineSegment(sketch, "E743", {"start": v(239.37, 222.98) * mm, "end": v(240, 222.98) * mm});
            skLineSegment(sketch, "E744", {"start": v(240, 222.98) * mm, "end": v(240, 223) * mm});
            skLineSegment(sketch, "E745", {"start": v(240, 223) * mm, "end": v(288, 223) * mm});
            skLineSegment(sketch, "E746", {"start": v(288, 223) * mm, "end": v(288, 222.94) * mm});
            skLineSegment(sketch, "E747", {"start": v(288, 222.94) * mm, "end": v(289.88, 222.94) * mm});
            skLineSegment(sketch, "E748", {"start": v(289.88, 222.94) * mm, "end": v(293.62, 222.47) * mm});
            skLineSegment(sketch, "E749", {"start": v(293.62, 222.47) * mm, "end": v(297.27, 221.53) * mm});
            skLineSegment(sketch, "E750", {"start": v(297.27, 221.53) * mm, "end": v(300.77, 220.15) * mm});
            skLineSegment(sketch, "E751", {"start": v(300.77, 220.15) * mm, "end": v(304.07, 218.33) * mm});
            skLineSegment(sketch, "E752", {"start": v(304.07, 218.33) * mm, "end": v(307.12, 216.12) * mm});
            skLineSegment(sketch, "E753", {"start": v(307.12, 216.12) * mm, "end": v(309.87, 213.54) * mm});
            skLineSegment(sketch, "E754", {"start": v(309.87, 213.54) * mm, "end": v(312.27, 210.63) * mm});
            skLineSegment(sketch, "E755", {"start": v(312.27, 210.63) * mm, "end": v(314.29, 207.45) * mm});
            skLineSegment(sketch, "E756", {"start": v(314.29, 207.45) * mm, "end": v(315.9, 204.04) * mm});
            skLineSegment(sketch, "E757", {"start": v(315.9, 204.04) * mm, "end": v(317.06, 200.46) * mm});
            skLineSegment(sketch, "E758", {"start": v(317.06, 200.46) * mm, "end": v(317.76, 196.76) * mm});
            skLineSegment(sketch, "E759", {"start": v(317.76, 196.76) * mm, "end": v(318, 193) * mm});
            skLineSegment(sketch, "E760", {"start": v(318, 193) * mm, "end": v(318, -107) * mm});
            skLineSegment(sketch, "E761", {"start": v(318, -107) * mm, "end": v(317.94, -107) * mm});
            skLineSegment(sketch, "E762", {"start": v(317.94, -107) * mm, "end": v(317.94, -108.88) * mm});
            skLineSegment(sketch, "E763", {"start": v(317.94, -108.88) * mm, "end": v(317.47, -112.62) * mm});
            skLineSegment(sketch, "E764", {"start": v(317.47, -112.62) * mm, "end": v(316.53, -116.27) * mm});
            skLineSegment(sketch, "E765", {"start": v(316.53, -116.27) * mm, "end": v(315.14, -119.77) * mm});
            skLineSegment(sketch, "E766", {"start": v(315.14, -119.77) * mm, "end": v(313.33, -123.08) * mm});
            skLineSegment(sketch, "E767", {"start": v(313.33, -123.08) * mm, "end": v(311.12, -126.12) * mm});
            skLineSegment(sketch, "E768", {"start": v(311.12, -126.12) * mm, "end": v(308.54, -128.87) * mm});
            skLineSegment(sketch, "E769", {"start": v(308.54, -128.87) * mm, "end": v(305.63, -131.27) * mm});
            skLineSegment(sketch, "E770", {"start": v(305.63, -131.27) * mm, "end": v(302.45, -133.29) * mm});
            skLineSegment(sketch, "E771", {"start": v(302.45, -133.29) * mm, "end": v(299.04, -134.9) * mm});
            skLineSegment(sketch, "E772", {"start": v(299.04, -134.9) * mm, "end": v(295.46, -136.06) * mm});
            skLineSegment(sketch, "E773", {"start": v(295.46, -136.06) * mm, "end": v(291.76, -136.76) * mm});
            skLineSegment(sketch, "E774", {"start": v(291.76, -136.76) * mm, "end": v(288, -137) * mm});
            skLineSegment(sketch, "E775", {"start": v(288, -137) * mm, "end": v(237, -137) * mm});
            skLineSegment(sketch, "E776", {"start": v(237, -137) * mm, "end": v(237, -136.98) * mm});
            skLineSegment(sketch, "E777", {"start": v(237, -136.98) * mm, "end": v(236.37, -136.98) * mm});
            skLineSegment(sketch, "E778", {"start": v(236.37, -136.98) * mm, "end": v(235.13, -136.82) * mm});
            skLineSegment(sketch, "E779", {"start": v(235.13, -136.82) * mm, "end": v(233.9, -136.51) * mm});
            skLineSegment(sketch, "E780", {"start": v(233.9, -136.51) * mm, "end": v(232.74, -136.05) * mm});
            skLineSegment(sketch, "E781", {"start": v(232.74, -136.05) * mm, "end": v(231.64, -135.44) * mm});
            skLineSegment(sketch, "E782", {"start": v(231.64, -135.44) * mm, "end": v(230.63, -134.7) * mm});
            skLineSegment(sketch, "E783", {"start": v(230.63, -134.7) * mm, "end": v(229.71, -133.84) * mm});
            skLineSegment(sketch, "E784", {"start": v(229.71, -133.84) * mm, "end": v(228.9, -132.88) * mm});
            skLineSegment(sketch, "E785", {"start": v(228.9, -132.88) * mm, "end": v(228.24, -131.82) * mm});
            skLineSegment(sketch, "E786", {"start": v(228.24, -131.82) * mm, "end": v(227.7, -130.68) * mm});
            skLineSegment(sketch, "E787", {"start": v(227.7, -130.68) * mm, "end": v(227.31, -129.49) * mm});
            skLineSegment(sketch, "E788", {"start": v(227.31, -129.49) * mm, "end": v(227.08, -128.25) * mm});
            skLineSegment(sketch, "E789", {"start": v(227.08, -128.25) * mm, "end": v(227, -127) * mm});
            skLineSegment(sketch, "E790", {"start": v(227, -127) * mm, "end": v(227, -118) * mm});
            skLineSegment(sketch, "E791", {"start": v(227, -118) * mm, "end": v(226.96, -117.37) * mm});
            skLineSegment(sketch, "E792", {"start": v(226.96, -117.37) * mm, "end": v(226.84, -116.76) * mm});
            skLineSegment(sketch, "E793", {"start": v(226.84, -116.76) * mm, "end": v(226.65, -116.16) * mm});
            skLineSegment(sketch, "E794", {"start": v(226.65, -116.16) * mm, "end": v(226.38, -115.6) * mm});
            skLineSegment(sketch, "E795", {"start": v(226.38, -115.6) * mm, "end": v(226.04, -115.06) * mm});
            skLineSegment(sketch, "E796", {"start": v(226.04, -115.06) * mm, "end": v(225.65, -114.58) * mm});
            skLineSegment(sketch, "E797", {"start": v(225.65, -114.58) * mm, "end": v(225.19, -114.15) * mm});
            skLineSegment(sketch, "E798", {"start": v(225.19, -114.15) * mm, "end": v(224.68, -113.78) * mm});
            skLineSegment(sketch, "E799", {"start": v(224.68, -113.78) * mm, "end": v(224.13, -113.48) * mm});
            skLineSegment(sketch, "E800", {"start": v(224.13, -113.48) * mm, "end": v(223.54, -113.25) * mm});
            skLineSegment(sketch, "E801", {"start": v(223.54, -113.25) * mm, "end": v(222.94, -113.09) * mm});
            skLineSegment(sketch, "E802", {"start": v(222.94, -113.09) * mm, "end": v(222.31, -113.01) * mm});
            skLineSegment(sketch, "E803", {"start": v(222.31, -113.01) * mm, "end": v(222, -113.01) * mm});
            skLineSegment(sketch, "E804", {"start": v(222, -113.01) * mm, "end": v(222, -113) * mm});
            skLineSegment(sketch, "E805", {"start": v(222, -113) * mm, "end": v(188, -113) * mm});
            skLineSegment(sketch, "E806", {"start": v(188, -113) * mm, "end": v(187.37, -113.04) * mm});
            skLineSegment(sketch, "E807", {"start": v(187.37, -113.04) * mm, "end": v(186.76, -113.16) * mm});
            skLineSegment(sketch, "E808", {"start": v(186.76, -113.16) * mm, "end": v(186.16, -113.35) * mm});
            skLineSegment(sketch, "E809", {"start": v(186.16, -113.35) * mm, "end": v(185.6, -113.62) * mm});
            skLineSegment(sketch, "E810", {"start": v(185.6, -113.62) * mm, "end": v(185.06, -113.95) * mm});
            skLineSegment(sketch, "E811", {"start": v(185.06, -113.95) * mm, "end": v(184.58, -114.36) * mm});
            skLineSegment(sketch, "E812", {"start": v(184.58, -114.36) * mm, "end": v(184.15, -114.81) * mm});
            skLineSegment(sketch, "E813", {"start": v(184.15, -114.81) * mm, "end": v(183.78, -115.32) * mm});
            skLineSegment(sketch, "E814", {"start": v(183.78, -115.32) * mm, "end": v(183.48, -115.87) * mm});
            skLineSegment(sketch, "E815", {"start": v(183.48, -115.87) * mm, "end": v(183.25, -116.45) * mm});
            skLineSegment(sketch, "E816", {"start": v(183.25, -116.45) * mm, "end": v(183.09, -117.06) * mm});
            skLineSegment(sketch, "E817", {"start": v(183.09, -117.06) * mm, "end": v(183.01, -117.69) * mm});
            skLineSegment(sketch, "E818", {"start": v(183.01, -117.69) * mm, "end": v(183.01, -118) * mm});
            skLineSegment(sketch, "E819", {"start": v(183.01, -118) * mm, "end": v(183, -118) * mm});
            skLineSegment(sketch, "E820", {"start": v(183, -118) * mm, "end": v(183, -127) * mm});
            skLineSegment(sketch, "E821", {"start": v(183, -127) * mm, "end": v(182.92, -128.25) * mm});
            skLineSegment(sketch, "E822", {"start": v(182.92, -128.25) * mm, "end": v(182.69, -129.49) * mm});
            skLineSegment(sketch, "E823", {"start": v(182.69, -129.49) * mm, "end": v(182.3, -130.68) * mm});
            skLineSegment(sketch, "E824", {"start": v(182.3, -130.68) * mm, "end": v(181.76, -131.82) * mm});
            skLineSegment(sketch, "E825", {"start": v(181.76, -131.82) * mm, "end": v(181.1, -132.88) * mm});
            skLineSegment(sketch, "E826", {"start": v(181.1, -132.88) * mm, "end": v(180.29, -133.84) * mm});
            skLineSegment(sketch, "E827", {"start": v(180.29, -133.84) * mm, "end": v(179.37, -134.7) * mm});
            skLineSegment(sketch, "E828", {"start": v(179.37, -134.7) * mm, "end": v(178.36, -135.44) * mm});
            skLineSegment(sketch, "E829", {"start": v(178.36, -135.44) * mm, "end": v(177.26, -136.05) * mm});
            skLineSegment(sketch, "E830", {"start": v(177.26, -136.05) * mm, "end": v(176.1, -136.51) * mm});
            skLineSegment(sketch, "E831", {"start": v(176.1, -136.51) * mm, "end": v(174.87, -136.82) * mm});
            skLineSegment(sketch, "E832", {"start": v(174.87, -136.82) * mm, "end": v(173.63, -136.98) * mm});
            skLineSegment(sketch, "E833", {"start": v(173.63, -136.98) * mm, "end": v(173, -136.98) * mm});
            skLineSegment(sketch, "E834", {"start": v(173, -136.98) * mm, "end": v(173, -137) * mm});
            skLineSegment(sketch, "E835", {"start": v(173, -137) * mm, "end": v(122, -137) * mm});
            skLineSegment(sketch, "E836", {"start": v(101.53, -102.9) * mm, "end": v(102.2, -102.73) * mm});
            skLineSegment(sketch, "E837", {"start": v(102.2, -102.73) * mm, "end": v(102.84, -102.48) * mm});
            skLineSegment(sketch, "E838", {"start": v(102.84, -102.48) * mm, "end": v(103.45, -102.14) * mm});
            skLineSegment(sketch, "E839", {"start": v(103.45, -102.14) * mm, "end": v(104, -101.74) * mm});
            skLineSegment(sketch, "E840", {"start": v(104, -101.74) * mm, "end": v(104.5, -101.27) * mm});
            skLineSegment(sketch, "E841", {"start": v(104.5, -101.27) * mm, "end": v(113.77, -92) * mm});
            skLineSegment(sketch, "E842", {"start": v(113.77, -92) * mm, "end": v(194, -92) * mm});
            skLineSegment(sketch, "E843", {"start": v(194, -92) * mm, "end": v(194, -92.01) * mm});
            skLineSegment(sketch, "E844", {"start": v(194, -92.01) * mm, "end": v(194.34, -92.01) * mm});
            skLineSegment(sketch, "E845", {"start": v(194.34, -92.01) * mm, "end": v(195.03, -92.1) * mm});
            skLineSegment(sketch, "E846", {"start": v(195.03, -92.1) * mm, "end": v(195.7, -92.27) * mm});
            skLineSegment(sketch, "E847", {"start": v(195.7, -92.27) * mm, "end": v(196.34, -92.52) * mm});
            skLineSegment(sketch, "E848", {"start": v(196.34, -92.52) * mm, "end": v(196.95, -92.86) * mm});
            skLineSegment(sketch, "E849", {"start": v(196.95, -92.86) * mm, "end": v(197.5, -93.26) * mm});
            skLineSegment(sketch, "E850", {"start": v(197.5, -93.26) * mm, "end": v(198, -93.73) * mm});
            skLineSegment(sketch, "E851", {"start": v(198, -93.73) * mm, "end": v(198.45, -94.27) * mm});
            skLineSegment(sketch, "E852", {"start": v(198.45, -94.27) * mm, "end": v(198.82, -94.85) * mm});
            skLineSegment(sketch, "E853", {"start": v(198.82, -94.85) * mm, "end": v(199.11, -95.47) * mm});
            skLineSegment(sketch, "E854", {"start": v(199.11, -95.47) * mm, "end": v(199.33, -96.13) * mm});
            skLineSegment(sketch, "E855", {"start": v(199.33, -96.13) * mm, "end": v(199.46, -96.81) * mm});
            skLineSegment(sketch, "E856", {"start": v(199.46, -96.81) * mm, "end": v(199.54, -98.19) * mm});
            skLineSegment(sketch, "E857", {"start": v(199.54, -98.19) * mm, "end": v(199.67, -98.87) * mm});
            skLineSegment(sketch, "E858", {"start": v(199.67, -98.87) * mm, "end": v(199.89, -99.53) * mm});
            skLineSegment(sketch, "E859", {"start": v(199.89, -99.53) * mm, "end": v(200.18, -100.15) * mm});
            skLineSegment(sketch, "E860", {"start": v(200.18, -100.15) * mm, "end": v(200.55, -100.73) * mm});
            skLineSegment(sketch, "E861", {"start": v(200.55, -100.73) * mm, "end": v(201, -101.27) * mm});
            skLineSegment(sketch, "E862", {"start": v(201, -101.27) * mm, "end": v(201.5, -101.74) * mm});
            skLineSegment(sketch, "E863", {"start": v(201.5, -101.74) * mm, "end": v(202.05, -102.14) * mm});
            skLineSegment(sketch, "E864", {"start": v(202.05, -102.14) * mm, "end": v(202.66, -102.48) * mm});
            skLineSegment(sketch, "E865", {"start": v(202.66, -102.48) * mm, "end": v(203.3, -102.73) * mm});
            skLineSegment(sketch, "E866", {"start": v(203.3, -102.73) * mm, "end": v(203.97, -102.9) * mm});
            skLineSegment(sketch, "E867", {"start": v(203.97, -102.9) * mm, "end": v(204.66, -102.99) * mm});
            skLineSegment(sketch, "E868", {"start": v(204.66, -102.99) * mm, "end": v(205.34, -102.99) * mm});
            skLineSegment(sketch, "E869", {"start": v(205.34, -102.99) * mm, "end": v(206.03, -102.9) * mm});
            skLineSegment(sketch, "E870", {"start": v(206.03, -102.9) * mm, "end": v(206.7, -102.73) * mm});
            skLineSegment(sketch, "E871", {"start": v(206.7, -102.73) * mm, "end": v(207.34, -102.48) * mm});
            skLineSegment(sketch, "E872", {"start": v(207.34, -102.48) * mm, "end": v(207.95, -102.14) * mm});
            skLineSegment(sketch, "E873", {"start": v(207.95, -102.14) * mm, "end": v(208.5, -101.74) * mm});
            skLineSegment(sketch, "E874", {"start": v(208.5, -101.74) * mm, "end": v(209, -101.27) * mm});
            skLineSegment(sketch, "E875", {"start": v(209, -101.27) * mm, "end": v(209.45, -100.73) * mm});
            skLineSegment(sketch, "E876", {"start": v(209.45, -100.73) * mm, "end": v(209.82, -100.15) * mm});
            skLineSegment(sketch, "E877", {"start": v(209.82, -100.15) * mm, "end": v(210.11, -99.53) * mm});
            skLineSegment(sketch, "E878", {"start": v(210.11, -99.53) * mm, "end": v(210.33, -98.87) * mm});
            skLineSegment(sketch, "E879", {"start": v(210.33, -98.87) * mm, "end": v(210.46, -98.19) * mm});
            skLineSegment(sketch, "E880", {"start": v(210.46, -98.19) * mm, "end": v(210.54, -96.81) * mm});
            skLineSegment(sketch, "E881", {"start": v(210.54, -96.81) * mm, "end": v(210.67, -96.13) * mm});
            skLineSegment(sketch, "E882", {"start": v(210.67, -96.13) * mm, "end": v(210.89, -95.47) * mm});
            skLineSegment(sketch, "E883", {"start": v(210.89, -95.47) * mm, "end": v(211.18, -94.85) * mm});
            skLineSegment(sketch, "E884", {"start": v(211.18, -94.85) * mm, "end": v(211.55, -94.27) * mm});
            skLineSegment(sketch, "E885", {"start": v(211.55, -94.27) * mm, "end": v(212, -93.73) * mm});
            skLineSegment(sketch, "E886", {"start": v(212, -93.73) * mm, "end": v(212.5, -93.26) * mm});
            skLineSegment(sketch, "E887", {"start": v(212.5, -93.26) * mm, "end": v(213.05, -92.86) * mm});
            skLineSegment(sketch, "E888", {"start": v(213.05, -92.86) * mm, "end": v(213.66, -92.52) * mm});
            skLineSegment(sketch, "E889", {"start": v(213.66, -92.52) * mm, "end": v(214.3, -92.27) * mm});
            skLineSegment(sketch, "E890", {"start": v(214.3, -92.27) * mm, "end": v(214.97, -92.1) * mm});
            skLineSegment(sketch, "E891", {"start": v(214.97, -92.1) * mm, "end": v(215.66, -92.01) * mm});
            skLineSegment(sketch, "E892", {"start": v(215.66, -92.01) * mm, "end": v(216, -92.01) * mm});
            skLineSegment(sketch, "E893", {"start": v(216, -92.01) * mm, "end": v(216, -92) * mm});
            skLineSegment(sketch, "E894", {"start": v(216, -92) * mm, "end": v(296.23, -92) * mm});
            skLineSegment(sketch, "E895", {"start": v(296.23, -92) * mm, "end": v(305.5, -101.27) * mm});
            skLineSegment(sketch, "E896", {"start": v(305.5, -101.27) * mm, "end": v(306, -101.74) * mm});
            skLineSegment(sketch, "E897", {"start": v(306, -101.74) * mm, "end": v(306.55, -102.14) * mm});
            skLineSegment(sketch, "E898", {"start": v(306.55, -102.14) * mm, "end": v(307.16, -102.48) * mm});
            skLineSegment(sketch, "E899", {"start": v(307.16, -102.48) * mm, "end": v(307.8, -102.73) * mm});
            skLineSegment(sketch, "E900", {"start": v(307.8, -102.73) * mm, "end": v(308.47, -102.9) * mm});
            skLineSegment(sketch, "E901", {"start": v(308.47, -102.9) * mm, "end": v(309.15, -102.99) * mm});
            skLineSegment(sketch, "E902", {"start": v(309.15, -102.99) * mm, "end": v(309.85, -102.99) * mm});
            skLineSegment(sketch, "E903", {"start": v(309.85, -102.99) * mm, "end": v(310.53, -102.9) * mm});
            skLineSegment(sketch, "E904", {"start": v(310.53, -102.9) * mm, "end": v(311.2, -102.73) * mm});
            skLineSegment(sketch, "E905", {"start": v(311.2, -102.73) * mm, "end": v(311.84, -102.48) * mm});
            skLineSegment(sketch, "E906", {"start": v(311.84, -102.48) * mm, "end": v(312.45, -102.14) * mm});
            skLineSegment(sketch, "E907", {"start": v(312.45, -102.14) * mm, "end": v(313, -101.74) * mm});
            skLineSegment(sketch, "E908", {"start": v(313, -101.74) * mm, "end": v(313.5, -101.27) * mm});
            skLineSegment(sketch, "E909", {"start": v(313.5, -101.27) * mm, "end": v(313.95, -100.73) * mm});
            skLineSegment(sketch, "E910", {"start": v(313.95, -100.73) * mm, "end": v(314.32, -100.15) * mm});
            skLineSegment(sketch, "E911", {"start": v(314.32, -100.15) * mm, "end": v(314.61, -99.53) * mm});
            skLineSegment(sketch, "E912", {"start": v(314.61, -99.53) * mm, "end": v(314.83, -98.87) * mm});
            skLineSegment(sketch, "E913", {"start": v(314.83, -98.87) * mm, "end": v(314.96, -98.19) * mm});
            skLineSegment(sketch, "E914", {"start": v(314.96, -98.19) * mm, "end": v(315, -97.5) * mm});
            skLineSegment(sketch, "E915", {"start": v(315, -97.5) * mm, "end": v(314.96, -96.81) * mm});
            skLineSegment(sketch, "E916", {"start": v(314.96, -96.81) * mm, "end": v(314.83, -96.13) * mm});
            skLineSegment(sketch, "E917", {"start": v(314.83, -96.13) * mm, "end": v(314.61, -95.47) * mm});
            skLineSegment(sketch, "E918", {"start": v(314.61, -95.47) * mm, "end": v(314.32, -94.85) * mm});
            skLineSegment(sketch, "E919", {"start": v(314.32, -94.85) * mm, "end": v(313.95, -94.27) * mm});
            skLineSegment(sketch, "E920", {"start": v(313.95, -94.27) * mm, "end": v(313.5, -93.73) * mm});
            skLineSegment(sketch, "E921", {"start": v(313.5, -93.73) * mm, "end": v(304, -84.23) * mm});
            skLineSegment(sketch, "E922", {"start": v(304, -84.23) * mm, "end": v(304, -4) * mm});
            skLineSegment(sketch, "E923", {"start": v(304, -4) * mm, "end": v(304.01, -4) * mm});
            skLineSegment(sketch, "E924", {"start": v(304.01, -4) * mm, "end": v(304.01, -3.65) * mm});
            skLineSegment(sketch, "E925", {"start": v(304.01, -3.65) * mm, "end": v(304.1, -2.97) * mm});
            skLineSegment(sketch, "E926", {"start": v(304.1, -2.97) * mm, "end": v(304.27, -2.3) * mm});
            skLineSegment(sketch, "E927", {"start": v(304.27, -2.3) * mm, "end": v(304.52, -1.66) * mm});
            skLineSegment(sketch, "E928", {"start": v(304.52, -1.66) * mm, "end": v(304.86, -1.05) * mm});
            skLineSegment(sketch, "E929", {"start": v(304.86, -1.05) * mm, "end": v(305.26, -0.5) * mm});
            skLineSegment(sketch, "E930", {"start": v(305.26, -0.5) * mm, "end": v(305.74, 0) * mm});
            skLineSegment(sketch, "E931", {"start": v(305.74, 0) * mm, "end": v(306.27, 0.45) * mm});
            skLineSegment(sketch, "E932", {"start": v(306.27, 0.45) * mm, "end": v(306.85, 0.82) * mm});
            skLineSegment(sketch, "E933", {"start": v(306.85, 0.82) * mm, "end": v(307.48, 1.11) * mm});
            skLineSegment(sketch, "E934", {"start": v(307.48, 1.11) * mm, "end": v(308.13, 1.33) * mm});
            skLineSegment(sketch, "E935", {"start": v(308.13, 1.33) * mm, "end": v(308.81, 1.46) * mm});
            skLineSegment(sketch, "E936", {"start": v(308.81, 1.46) * mm, "end": v(310.19, 1.54) * mm});
            skLineSegment(sketch, "E937", {"start": v(310.19, 1.54) * mm, "end": v(310.87, 1.67) * mm});
            skLineSegment(sketch, "E938", {"start": v(310.87, 1.67) * mm, "end": v(311.52, 1.89) * mm});
            skLineSegment(sketch, "E939", {"start": v(311.52, 1.89) * mm, "end": v(312.15, 2.18) * mm});
            skLineSegment(sketch, "E940", {"start": v(312.15, 2.18) * mm, "end": v(312.73, 2.55) * mm});
            skLineSegment(sketch, "E941", {"start": v(312.73, 2.55) * mm, "end": v(313.27, 3) * mm});
            skLineSegment(sketch, "E942", {"start": v(313.27, 3) * mm, "end": v(313.74, 3.5) * mm});
            skLineSegment(sketch, "E943", {"start": v(313.74, 3.5) * mm, "end": v(314.14, 4.05) * mm});
            skLineSegment(sketch, "E944", {"start": v(314.14, 4.05) * mm, "end": v(314.48, 4.66) * mm});
            skLineSegment(sketch, "E945", {"start": v(314.48, 4.66) * mm, "end": v(314.73, 5.3) * mm});
            skLineSegment(sketch, "E946", {"start": v(314.73, 5.3) * mm, "end": v(314.9, 5.97) * mm});
            skLineSegment(sketch, "E947", {"start": v(314.9, 5.97) * mm, "end": v(314.99, 6.66) * mm});
            skLineSegment(sketch, "E948", {"start": v(314.99, 6.66) * mm, "end": v(314.99, 7.34) * mm});
            skLineSegment(sketch, "E949", {"start": v(314.99, 7.34) * mm, "end": v(314.9, 8.03) * mm});
            skLineSegment(sketch, "E950", {"start": v(314.9, 8.03) * mm, "end": v(314.73, 8.7) * mm});
            skLineSegment(sketch, "E951", {"start": v(314.73, 8.7) * mm, "end": v(314.48, 9.34) * mm});
            skLineSegment(sketch, "E952", {"start": v(314.48, 9.34) * mm, "end": v(314.14, 9.95) * mm});
            skLineSegment(sketch, "E953", {"start": v(314.14, 9.95) * mm, "end": v(313.74, 10.5) * mm});
            skLineSegment(sketch, "E954", {"start": v(313.74, 10.5) * mm, "end": v(313.27, 11) * mm});
            skLineSegment(sketch, "E955", {"start": v(313.27, 11) * mm, "end": v(312.73, 11.45) * mm});
            skLineSegment(sketch, "E956", {"start": v(312.73, 11.45) * mm, "end": v(312.15, 11.82) * mm});
            skLineSegment(sketch, "E957", {"start": v(312.15, 11.82) * mm, "end": v(311.52, 12.11) * mm});
            skLineSegment(sketch, "E958", {"start": v(311.52, 12.11) * mm, "end": v(310.87, 12.33) * mm});
            skLineSegment(sketch, "E959", {"start": v(310.87, 12.33) * mm, "end": v(310.19, 12.46) * mm});
            skLineSegment(sketch, "E960", {"start": v(310.19, 12.46) * mm, "end": v(308.81, 12.54) * mm});
            skLineSegment(sketch, "E961", {"start": v(308.81, 12.54) * mm, "end": v(308.13, 12.67) * mm});
            skLineSegment(sketch, "E962", {"start": v(308.13, 12.67) * mm, "end": v(307.48, 12.89) * mm});
            skLineSegment(sketch, "E963", {"start": v(307.48, 12.89) * mm, "end": v(306.85, 13.18) * mm});
            skLineSegment(sketch, "E964", {"start": v(306.85, 13.18) * mm, "end": v(306.27, 13.55) * mm});
            skLineSegment(sketch, "E965", {"start": v(306.27, 13.55) * mm, "end": v(305.74, 14) * mm});
            skLineSegment(sketch, "E966", {"start": v(305.74, 14) * mm, "end": v(305.26, 14.5) * mm});
            skLineSegment(sketch, "E967", {"start": v(305.26, 14.5) * mm, "end": v(304.86, 15.05) * mm});
            skLineSegment(sketch, "E968", {"start": v(304.86, 15.05) * mm, "end": v(304.52, 15.66) * mm});
            skLineSegment(sketch, "E969", {"start": v(304.52, 15.66) * mm, "end": v(304.27, 16.3) * mm});
            skLineSegment(sketch, "E970", {"start": v(304.27, 16.3) * mm, "end": v(304.1, 16.97) * mm});
            skLineSegment(sketch, "E971", {"start": v(304.1, 16.97) * mm, "end": v(304.01, 17.66) * mm});
            skLineSegment(sketch, "E972", {"start": v(304.01, 17.66) * mm, "end": v(304.01, 18) * mm});
            skLineSegment(sketch, "E973", {"start": v(304.01, 18) * mm, "end": v(304, 18) * mm});
            skLineSegment(sketch, "E974", {"start": v(304, 18) * mm, "end": v(304, 98.23) * mm});
            skLineSegment(sketch, "E975", {"start": v(304, 98.23) * mm, "end": v(313.5, 107.73) * mm});
            skLineSegment(sketch, "E976", {"start": v(313.5, 107.73) * mm, "end": v(313.95, 108.27) * mm});
            skLineSegment(sketch, "E977", {"start": v(313.95, 108.27) * mm, "end": v(314.32, 108.85) * mm});
            skLineSegment(sketch, "E978", {"start": v(314.32, 108.85) * mm, "end": v(314.61, 109.48) * mm});
            skLineSegment(sketch, "E979", {"start": v(314.61, 109.48) * mm, "end": v(314.83, 110.13) * mm});
            skLineSegment(sketch, "E980", {"start": v(314.83, 110.13) * mm, "end": v(314.96, 110.81) * mm});
            skLineSegment(sketch, "E981", {"start": v(314.96, 110.81) * mm, "end": v(315, 111.5) * mm});
            skLineSegment(sketch, "E982", {"start": v(315, 111.5) * mm, "end": v(314.96, 112.19) * mm});
            skLineSegment(sketch, "E983", {"start": v(314.96, 112.19) * mm, "end": v(314.83, 112.87) * mm});
            skLineSegment(sketch, "E984", {"start": v(314.83, 112.87) * mm, "end": v(314.61, 113.53) * mm});
            skLineSegment(sketch, "E985", {"start": v(314.61, 113.53) * mm, "end": v(314.32, 114.15) * mm});
            skLineSegment(sketch, "E986", {"start": v(314.32, 114.15) * mm, "end": v(313.95, 114.73) * mm});
            skLineSegment(sketch, "E987", {"start": v(313.95, 114.73) * mm, "end": v(313.5, 115.27) * mm});
            skLineSegment(sketch, "E988", {"start": v(313.5, 115.27) * mm, "end": v(313, 115.74) * mm});
            skLineSegment(sketch, "E989", {"start": v(313, 115.74) * mm, "end": v(312.45, 116.14) * mm});
            skLineSegment(sketch, "E990", {"start": v(312.45, 116.14) * mm, "end": v(311.84, 116.48) * mm});
            skLineSegment(sketch, "E991", {"start": v(311.84, 116.48) * mm, "end": v(311.2, 116.73) * mm});
            skLineSegment(sketch, "E992", {"start": v(311.2, 116.73) * mm, "end": v(310.53, 116.9) * mm});
            skLineSegment(sketch, "E993", {"start": v(310.53, 116.9) * mm, "end": v(309.85, 116.99) * mm});
            skLineSegment(sketch, "E994", {"start": v(309.85, 116.99) * mm, "end": v(309.15, 116.99) * mm});
            skLineSegment(sketch, "E995", {"start": v(309.15, 116.99) * mm, "end": v(308.47, 116.9) * mm});
            skLineSegment(sketch, "E996", {"start": v(308.47, 116.9) * mm, "end": v(307.8, 116.73) * mm});
            skLineSegment(sketch, "E997", {"start": v(307.8, 116.73) * mm, "end": v(307.16, 116.48) * mm});
            skLineSegment(sketch, "E998", {"start": v(307.16, 116.48) * mm, "end": v(306.55, 116.14) * mm});
            skLineSegment(sketch, "E999", {"start": v(306.55, 116.14) * mm, "end": v(306, 115.74) * mm});
            skLineSegment(sketch, "E1000", {"start": v(306, 115.74) * mm, "end": v(305.5, 115.27) * mm});
            skLineSegment(sketch, "E1001", {"start": v(305.5, 115.27) * mm, "end": v(296.23, 106) * mm});
            skLineSegment(sketch, "E1002", {"start": v(296.23, 106) * mm, "end": v(113.77, 106) * mm});
            skLineSegment(sketch, "E1003", {"start": v(113.77, 106) * mm, "end": v(104.5, 115.27) * mm});
            skLineSegment(sketch, "E1004", {"start": v(104.5, 115.27) * mm, "end": v(104, 115.74) * mm});
            skLineSegment(sketch, "E1005", {"start": v(104, 115.74) * mm, "end": v(103.45, 116.14) * mm});
            skLineSegment(sketch, "E1006", {"start": v(103.45, 116.14) * mm, "end": v(102.84, 116.48) * mm});
            skLineSegment(sketch, "E1007", {"start": v(102.84, 116.48) * mm, "end": v(102.2, 116.73) * mm});
            skLineSegment(sketch, "E1008", {"start": v(102.2, 116.73) * mm, "end": v(101.53, 116.9) * mm});
            skLineSegment(sketch, "E1009", {"start": v(101.53, 116.9) * mm, "end": v(100.84, 116.99) * mm});
            skLineSegment(sketch, "E1010", {"start": v(100.84, 116.99) * mm, "end": v(100.16, 116.99) * mm});
            skLineSegment(sketch, "E1011", {"start": v(100.16, 116.99) * mm, "end": v(99.47, 116.9) * mm});
            skLineSegment(sketch, "E1012", {"start": v(99.47, 116.9) * mm, "end": v(98.8, 116.73) * mm});
            skLineSegment(sketch, "E1013", {"start": v(98.8, 116.73) * mm, "end": v(98.16, 116.48) * mm});
            skLineSegment(sketch, "E1014", {"start": v(98.16, 116.48) * mm, "end": v(97.55, 116.14) * mm});
            skLineSegment(sketch, "E1015", {"start": v(97.55, 116.14) * mm, "end": v(97, 115.74) * mm});
            skLineSegment(sketch, "E1016", {"start": v(97, 115.74) * mm, "end": v(96.5, 115.27) * mm});
            skLineSegment(sketch, "E1017", {"start": v(96.5, 115.27) * mm, "end": v(96.05, 114.73) * mm});
            skLineSegment(sketch, "E1018", {"start": v(96.05, 114.73) * mm, "end": v(95.68, 114.15) * mm});
            skLineSegment(sketch, "E1019", {"start": v(95.68, 114.15) * mm, "end": v(95.39, 113.53) * mm});
            skLineSegment(sketch, "E1020", {"start": v(95.39, 113.53) * mm, "end": v(95.17, 112.87) * mm});
            skLineSegment(sketch, "E1021", {"start": v(95.17, 112.87) * mm, "end": v(95.04, 112.19) * mm});
            skLineSegment(sketch, "E1022", {"start": v(95.04, 112.19) * mm, "end": v(95, 111.5) * mm});
            skLineSegment(sketch, "E1023", {"start": v(95, 111.5) * mm, "end": v(95.04, 110.81) * mm});
            skLineSegment(sketch, "E1024", {"start": v(95.04, 110.81) * mm, "end": v(95.17, 110.13) * mm});
            skLineSegment(sketch, "E1025", {"start": v(95.17, 110.13) * mm, "end": v(95.39, 109.48) * mm});
            skLineSegment(sketch, "E1026", {"start": v(95.39, 109.48) * mm, "end": v(95.68, 108.85) * mm});
            skLineSegment(sketch, "E1027", {"start": v(95.68, 108.85) * mm, "end": v(96.05, 108.27) * mm});
            skLineSegment(sketch, "E1028", {"start": v(96.05, 108.27) * mm, "end": v(96.5, 107.73) * mm});
            skLineSegment(sketch, "E1029", {"start": v(96.5, 107.73) * mm, "end": v(106, 98.23) * mm});
            skLineSegment(sketch, "E1030", {"start": v(106, 98.23) * mm, "end": v(106, -84.23) * mm});
            skLineSegment(sketch, "E1031", {"start": v(106, -84.23) * mm, "end": v(96.5, -93.73) * mm});
            skLineSegment(sketch, "E1032", {"start": v(96.5, -93.73) * mm, "end": v(96.05, -94.27) * mm});
            skLineSegment(sketch, "E1033", {"start": v(96.05, -94.27) * mm, "end": v(95.68, -94.85) * mm});
            skLineSegment(sketch, "E1034", {"start": v(95.68, -94.85) * mm, "end": v(95.39, -95.47) * mm});
            skLineSegment(sketch, "E1035", {"start": v(95.39, -95.47) * mm, "end": v(95.17, -96.13) * mm});
            skLineSegment(sketch, "E1036", {"start": v(95.17, -96.13) * mm, "end": v(95.04, -96.81) * mm});
            skLineSegment(sketch, "E1037", {"start": v(95.04, -96.81) * mm, "end": v(95, -97.5) * mm});
            skLineSegment(sketch, "E1038", {"start": v(95, -97.5) * mm, "end": v(95.04, -98.19) * mm});
            skLineSegment(sketch, "E1039", {"start": v(95.04, -98.19) * mm, "end": v(95.17, -98.87) * mm});
            skLineSegment(sketch, "E1040", {"start": v(95.17, -98.87) * mm, "end": v(95.39, -99.53) * mm});
            skLineSegment(sketch, "E1041", {"start": v(95.39, -99.53) * mm, "end": v(95.68, -100.15) * mm});
            skLineSegment(sketch, "E1042", {"start": v(95.68, -100.15) * mm, "end": v(96.05, -100.73) * mm});
            skLineSegment(sketch, "E1043", {"start": v(96.05, -100.73) * mm, "end": v(96.5, -101.27) * mm});
            skLineSegment(sketch, "E1044", {"start": v(96.5, -101.27) * mm, "end": v(97, -101.74) * mm});
            skLineSegment(sketch, "E1045", {"start": v(97, -101.74) * mm, "end": v(97.55, -102.14) * mm});
            skLineSegment(sketch, "E1046", {"start": v(97.55, -102.14) * mm, "end": v(98.16, -102.48) * mm});
            skLineSegment(sketch, "E1047", {"start": v(98.16, -102.48) * mm, "end": v(98.8, -102.73) * mm});
            skLineSegment(sketch, "E1048", {"start": v(98.8, -102.73) * mm, "end": v(99.47, -102.9) * mm});
            skLineSegment(sketch, "E1049", {"start": v(99.47, -102.9) * mm, "end": v(100.16, -102.99) * mm});
            skLineSegment(sketch, "E1050", {"start": v(100.16, -102.99) * mm, "end": v(100.84, -102.99) * mm});
            skLineSegment(sketch, "E1051", {"start": v(100.84, -102.99) * mm, "end": v(101.53, -102.9) * mm});
            skLineSegment(sketch, "E1052", {"start": v(100.4, 110) * mm, "end": v(100.22, 110.03) * mm});
            skLineSegment(sketch, "E1053", {"start": v(100.22, 110.03) * mm, "end": v(100.04, 110.07) * mm});
            skLineSegment(sketch, "E1054", {"start": v(100.04, 110.07) * mm, "end": v(99.86, 110.14) * mm});
            skLineSegment(sketch, "E1055", {"start": v(99.86, 110.14) * mm, "end": v(99.7, 110.23) * mm});
            skLineSegment(sketch, "E1056", {"start": v(99.7, 110.23) * mm, "end": v(99.54, 110.34) * mm});
            skLineSegment(sketch, "E1057", {"start": v(99.54, 110.34) * mm, "end": v(99.4, 110.47) * mm});
            skLineSegment(sketch, "E1058", {"start": v(99.4, 110.47) * mm, "end": v(99.29, 110.62) * mm});
            skLineSegment(sketch, "E1059", {"start": v(99.29, 110.62) * mm, "end": v(99.19, 110.78) * mm});
            skLineSegment(sketch, "E1060", {"start": v(99.19, 110.78) * mm, "end": v(99.1, 110.95) * mm});
            skLineSegment(sketch, "E1061", {"start": v(99.1, 110.95) * mm, "end": v(99.05, 111.13) * mm});
            skLineSegment(sketch, "E1062", {"start": v(99.05, 111.13) * mm, "end": v(99.01, 111.31) * mm});
            skLineSegment(sketch, "E1063", {"start": v(99.01, 111.31) * mm, "end": v(99, 111.5) * mm});
            skLineSegment(sketch, "E1064", {"start": v(99, 111.5) * mm, "end": v(99.01, 111.69) * mm});
            skLineSegment(sketch, "E1065", {"start": v(99.01, 111.69) * mm, "end": v(99.05, 111.87) * mm});
            skLineSegment(sketch, "E1066", {"start": v(99.05, 111.87) * mm, "end": v(99.1, 112.05) * mm});
            skLineSegment(sketch, "E1067", {"start": v(99.1, 112.05) * mm, "end": v(99.19, 112.22) * mm});
            skLineSegment(sketch, "E1068", {"start": v(99.19, 112.22) * mm, "end": v(99.29, 112.38) * mm});
            skLineSegment(sketch, "E1069", {"start": v(99.29, 112.38) * mm, "end": v(99.4, 112.53) * mm});
            skLineSegment(sketch, "E1070", {"start": v(99.4, 112.53) * mm, "end": v(99.54, 112.66) * mm});
            skLineSegment(sketch, "E1071", {"start": v(99.54, 112.66) * mm, "end": v(99.7, 112.77) * mm});
            skLineSegment(sketch, "E1072", {"start": v(99.7, 112.77) * mm, "end": v(99.86, 112.86) * mm});
            skLineSegment(sketch, "E1073", {"start": v(99.86, 112.86) * mm, "end": v(100.04, 112.93) * mm});
            skLineSegment(sketch, "E1074", {"start": v(100.04, 112.93) * mm, "end": v(100.22, 112.97) * mm});
            skLineSegment(sketch, "E1075", {"start": v(100.22, 112.97) * mm, "end": v(100.4, 113) * mm});
            skLineSegment(sketch, "E1076", {"start": v(100.4, 113) * mm, "end": v(100.6, 113) * mm});
            skLineSegment(sketch, "E1077", {"start": v(100.6, 113) * mm, "end": v(100.78, 112.97) * mm});
            skLineSegment(sketch, "E1078", {"start": v(100.78, 112.97) * mm, "end": v(100.96, 112.93) * mm});
            skLineSegment(sketch, "E1079", {"start": v(100.96, 112.93) * mm, "end": v(101.14, 112.86) * mm});
            skLineSegment(sketch, "E1080", {"start": v(101.14, 112.86) * mm, "end": v(101.3, 112.77) * mm});
            skLineSegment(sketch, "E1081", {"start": v(101.3, 112.77) * mm, "end": v(101.46, 112.66) * mm});
            skLineSegment(sketch, "E1082", {"start": v(101.46, 112.66) * mm, "end": v(101.6, 112.53) * mm});
            skLineSegment(sketch, "E1083", {"start": v(101.6, 112.53) * mm, "end": v(101.71, 112.38) * mm});
            skLineSegment(sketch, "E1084", {"start": v(101.71, 112.38) * mm, "end": v(101.81, 112.22) * mm});
            skLineSegment(sketch, "E1085", {"start": v(101.81, 112.22) * mm, "end": v(101.9, 112.05) * mm});
            skLineSegment(sketch, "E1086", {"start": v(101.9, 112.05) * mm, "end": v(101.95, 111.87) * mm});
            skLineSegment(sketch, "E1087", {"start": v(101.95, 111.87) * mm, "end": v(101.99, 111.69) * mm});
            skLineSegment(sketch, "E1088", {"start": v(101.99, 111.69) * mm, "end": v(102, 111.5) * mm});
            skLineSegment(sketch, "E1089", {"start": v(102, 111.5) * mm, "end": v(101.99, 111.31) * mm});
            skLineSegment(sketch, "E1090", {"start": v(101.99, 111.31) * mm, "end": v(101.95, 111.13) * mm});
            skLineSegment(sketch, "E1091", {"start": v(101.95, 111.13) * mm, "end": v(101.9, 110.95) * mm});
            skLineSegment(sketch, "E1092", {"start": v(101.9, 110.95) * mm, "end": v(101.81, 110.78) * mm});
            skLineSegment(sketch, "E1093", {"start": v(101.81, 110.78) * mm, "end": v(101.71, 110.62) * mm});
            skLineSegment(sketch, "E1094", {"start": v(101.71, 110.62) * mm, "end": v(101.6, 110.47) * mm});
            skLineSegment(sketch, "E1095", {"start": v(101.6, 110.47) * mm, "end": v(101.46, 110.34) * mm});
            skLineSegment(sketch, "E1096", {"start": v(101.46, 110.34) * mm, "end": v(101.3, 110.23) * mm});
            skLineSegment(sketch, "E1097", {"start": v(101.3, 110.23) * mm, "end": v(101.14, 110.14) * mm});
            skLineSegment(sketch, "E1098", {"start": v(101.14, 110.14) * mm, "end": v(100.96, 110.07) * mm});
            skLineSegment(sketch, "E1099", {"start": v(100.96, 110.07) * mm, "end": v(100.78, 110.03) * mm});
            skLineSegment(sketch, "E1100", {"start": v(100.78, 110.03) * mm, "end": v(100.6, 110) * mm});
            skLineSegment(sketch, "E1101", {"start": v(100.6, 110) * mm, "end": v(100.4, 110) * mm});
            skLineSegment(sketch, "E1102", {"start": v(309.4, 110) * mm, "end": v(309.22, 110.03) * mm});
            skLineSegment(sketch, "E1103", {"start": v(309.22, 110.03) * mm, "end": v(309.04, 110.07) * mm});
            skLineSegment(sketch, "E1104", {"start": v(309.04, 110.07) * mm, "end": v(308.86, 110.14) * mm});
            skLineSegment(sketch, "E1105", {"start": v(308.86, 110.14) * mm, "end": v(308.7, 110.23) * mm});
            skLineSegment(sketch, "E1106", {"start": v(308.7, 110.23) * mm, "end": v(308.54, 110.34) * mm});
            skLineSegment(sketch, "E1107", {"start": v(308.54, 110.34) * mm, "end": v(308.4, 110.47) * mm});
            skLineSegment(sketch, "E1108", {"start": v(308.4, 110.47) * mm, "end": v(308.29, 110.62) * mm});
            skLineSegment(sketch, "E1109", {"start": v(308.29, 110.62) * mm, "end": v(308.19, 110.78) * mm});
            skLineSegment(sketch, "E1110", {"start": v(308.19, 110.78) * mm, "end": v(308.1, 110.95) * mm});
            skLineSegment(sketch, "E1111", {"start": v(308.1, 110.95) * mm, "end": v(308.05, 111.13) * mm});
            skLineSegment(sketch, "E1112", {"start": v(308.05, 111.13) * mm, "end": v(308.01, 111.31) * mm});
            skLineSegment(sketch, "E1113", {"start": v(308.01, 111.31) * mm, "end": v(308, 111.5) * mm});
            skLineSegment(sketch, "E1114", {"start": v(308, 111.5) * mm, "end": v(308.01, 111.69) * mm});
            skLineSegment(sketch, "E1115", {"start": v(308.01, 111.69) * mm, "end": v(308.05, 111.87) * mm});
            skLineSegment(sketch, "E1116", {"start": v(308.05, 111.87) * mm, "end": v(308.1, 112.05) * mm});
            skLineSegment(sketch, "E1117", {"start": v(308.1, 112.05) * mm, "end": v(308.19, 112.22) * mm});
            skLineSegment(sketch, "E1118", {"start": v(308.19, 112.22) * mm, "end": v(308.29, 112.38) * mm});
            skLineSegment(sketch, "E1119", {"start": v(308.29, 112.38) * mm, "end": v(308.4, 112.53) * mm});
            skLineSegment(sketch, "E1120", {"start": v(308.4, 112.53) * mm, "end": v(308.54, 112.66) * mm});
            skLineSegment(sketch, "E1121", {"start": v(308.54, 112.66) * mm, "end": v(308.7, 112.77) * mm});
            skLineSegment(sketch, "E1122", {"start": v(308.7, 112.77) * mm, "end": v(308.86, 112.86) * mm});
            skLineSegment(sketch, "E1123", {"start": v(308.86, 112.86) * mm, "end": v(309.04, 112.93) * mm});
            skLineSegment(sketch, "E1124", {"start": v(309.04, 112.93) * mm, "end": v(309.22, 112.97) * mm});
            skLineSegment(sketch, "E1125", {"start": v(309.22, 112.97) * mm, "end": v(309.4, 113) * mm});
            skLineSegment(sketch, "E1126", {"start": v(309.4, 113) * mm, "end": v(309.6, 113) * mm});
            skLineSegment(sketch, "E1127", {"start": v(309.6, 113) * mm, "end": v(309.78, 112.97) * mm});
            skLineSegment(sketch, "E1128", {"start": v(309.78, 112.97) * mm, "end": v(309.96, 112.93) * mm});
            skLineSegment(sketch, "E1129", {"start": v(309.96, 112.93) * mm, "end": v(310.14, 112.86) * mm});
            skLineSegment(sketch, "E1130", {"start": v(310.14, 112.86) * mm, "end": v(310.3, 112.77) * mm});
            skLineSegment(sketch, "E1131", {"start": v(310.3, 112.77) * mm, "end": v(310.46, 112.66) * mm});
            skLineSegment(sketch, "E1132", {"start": v(310.46, 112.66) * mm, "end": v(310.6, 112.53) * mm});
            skLineSegment(sketch, "E1133", {"start": v(310.6, 112.53) * mm, "end": v(310.71, 112.38) * mm});
            skLineSegment(sketch, "E1134", {"start": v(310.71, 112.38) * mm, "end": v(310.81, 112.22) * mm});
            skLineSegment(sketch, "E1135", {"start": v(310.81, 112.22) * mm, "end": v(310.9, 112.05) * mm});
            skLineSegment(sketch, "E1136", {"start": v(310.9, 112.05) * mm, "end": v(310.95, 111.87) * mm});
            skLineSegment(sketch, "E1137", {"start": v(310.95, 111.87) * mm, "end": v(310.99, 111.69) * mm});
            skLineSegment(sketch, "E1138", {"start": v(310.99, 111.69) * mm, "end": v(311, 111.5) * mm});
            skLineSegment(sketch, "E1139", {"start": v(311, 111.5) * mm, "end": v(310.99, 111.31) * mm});
            skLineSegment(sketch, "E1140", {"start": v(310.99, 111.31) * mm, "end": v(310.95, 111.13) * mm});
            skLineSegment(sketch, "E1141", {"start": v(310.95, 111.13) * mm, "end": v(310.9, 110.95) * mm});
            skLineSegment(sketch, "E1142", {"start": v(310.9, 110.95) * mm, "end": v(310.81, 110.78) * mm});
            skLineSegment(sketch, "E1143", {"start": v(310.81, 110.78) * mm, "end": v(310.71, 110.62) * mm});
            skLineSegment(sketch, "E1144", {"start": v(310.71, 110.62) * mm, "end": v(310.6, 110.47) * mm});
            skLineSegment(sketch, "E1145", {"start": v(310.6, 110.47) * mm, "end": v(310.46, 110.34) * mm});
            skLineSegment(sketch, "E1146", {"start": v(310.46, 110.34) * mm, "end": v(310.3, 110.23) * mm});
            skLineSegment(sketch, "E1147", {"start": v(310.3, 110.23) * mm, "end": v(310.14, 110.14) * mm});
            skLineSegment(sketch, "E1148", {"start": v(310.14, 110.14) * mm, "end": v(309.96, 110.07) * mm});
            skLineSegment(sketch, "E1149", {"start": v(309.96, 110.07) * mm, "end": v(309.78, 110.03) * mm});
            skLineSegment(sketch, "E1150", {"start": v(309.78, 110.03) * mm, "end": v(309.6, 110) * mm});
            skLineSegment(sketch, "E1151", {"start": v(309.6, 110) * mm, "end": v(309.4, 110) * mm});
            skLineSegment(sketch, "E1152", {"start": v(204.66, 33.43) * mm, "end": v(203.97, 33.52) * mm});
            skLineSegment(sketch, "E1153", {"start": v(203.97, 33.52) * mm, "end": v(203.3, 33.69) * mm});
            skLineSegment(sketch, "E1154", {"start": v(203.3, 33.69) * mm, "end": v(202.66, 33.94) * mm});
            skLineSegment(sketch, "E1155", {"start": v(202.66, 33.94) * mm, "end": v(202.05, 34.28) * mm});
            skLineSegment(sketch, "E1156", {"start": v(202.05, 34.28) * mm, "end": v(201.5, 34.68) * mm});
            skLineSegment(sketch, "E1157", {"start": v(201.5, 34.68) * mm, "end": v(201, 35.16) * mm});
            skLineSegment(sketch, "E1158", {"start": v(201, 35.16) * mm, "end": v(150.41, 85.73) * mm});
            skLineSegment(sketch, "E1159", {"start": v(150.41, 85.73) * mm, "end": v(149.97, 86.27) * mm});
            skLineSegment(sketch, "E1160", {"start": v(149.97, 86.27) * mm, "end": v(149.6, 86.85) * mm});
            skLineSegment(sketch, "E1161", {"start": v(149.6, 86.85) * mm, "end": v(149.3, 87.47) * mm});
            skLineSegment(sketch, "E1162", {"start": v(149.3, 87.47) * mm, "end": v(149.1, 88.13) * mm});
            skLineSegment(sketch, "E1163", {"start": v(149.1, 88.13) * mm, "end": v(148.96, 88.81) * mm});
            skLineSegment(sketch, "E1164", {"start": v(148.96, 88.81) * mm, "end": v(148.92, 89.5) * mm});
            skLineSegment(sketch, "E1165", {"start": v(148.92, 89.5) * mm, "end": v(148.96, 90.19) * mm});
            skLineSegment(sketch, "E1166", {"start": v(148.96, 90.19) * mm, "end": v(149.1, 90.87) * mm});
            skLineSegment(sketch, "E1167", {"start": v(149.1, 90.87) * mm, "end": v(149.3, 91.53) * mm});
            skLineSegment(sketch, "E1168", {"start": v(149.3, 91.53) * mm, "end": v(149.6, 92.15) * mm});
            skLineSegment(sketch, "E1169", {"start": v(149.6, 92.15) * mm, "end": v(149.97, 92.73) * mm});
            skLineSegment(sketch, "E1170", {"start": v(149.97, 92.73) * mm, "end": v(150.41, 93.27) * mm});
            skLineSegment(sketch, "E1171", {"start": v(150.41, 93.27) * mm, "end": v(150.91, 93.74) * mm});
            skLineSegment(sketch, "E1172", {"start": v(150.91, 93.74) * mm, "end": v(151.47, 94.14) * mm});
            skLineSegment(sketch, "E1173", {"start": v(151.47, 94.14) * mm, "end": v(152.08, 94.48) * mm});
            skLineSegment(sketch, "E1174", {"start": v(152.08, 94.48) * mm, "end": v(152.72, 94.73) * mm});
            skLineSegment(sketch, "E1175", {"start": v(152.72, 94.73) * mm, "end": v(153.39, 94.9) * mm});
            skLineSegment(sketch, "E1176", {"start": v(153.39, 94.9) * mm, "end": v(154.07, 94.99) * mm});
            skLineSegment(sketch, "E1177", {"start": v(154.07, 94.99) * mm, "end": v(255.93, 94.99) * mm});
            skLineSegment(sketch, "E1178", {"start": v(255.93, 94.99) * mm, "end": v(256.6, 94.9) * mm});
            skLineSegment(sketch, "E1179", {"start": v(256.6, 94.9) * mm, "end": v(257.28, 94.73) * mm});
            skLineSegment(sketch, "E1180", {"start": v(257.28, 94.73) * mm, "end": v(257.92, 94.48) * mm});
            skLineSegment(sketch, "E1181", {"start": v(257.92, 94.48) * mm, "end": v(258.53, 94.14) * mm});
            skLineSegment(sketch, "E1182", {"start": v(258.53, 94.14) * mm, "end": v(259.09, 93.74) * mm});
            skLineSegment(sketch, "E1183", {"start": v(259.09, 93.74) * mm, "end": v(259.59, 93.27) * mm});
            skLineSegment(sketch, "E1184", {"start": v(259.59, 93.27) * mm, "end": v(260.03, 92.73) * mm});
            skLineSegment(sketch, "E1185", {"start": v(260.03, 92.73) * mm, "end": v(260.4, 92.15) * mm});
            skLineSegment(sketch, "E1186", {"start": v(260.4, 92.15) * mm, "end": v(260.7, 91.53) * mm});
            skLineSegment(sketch, "E1187", {"start": v(260.7, 91.53) * mm, "end": v(260.9, 90.87) * mm});
            skLineSegment(sketch, "E1188", {"start": v(260.9, 90.87) * mm, "end": v(261.04, 90.19) * mm});
            skLineSegment(sketch, "E1189", {"start": v(261.04, 90.19) * mm, "end": v(261.08, 89.5) * mm});
            skLineSegment(sketch, "E1190", {"start": v(261.08, 89.5) * mm, "end": v(261.04, 88.81) * mm});
            skLineSegment(sketch, "E1191", {"start": v(261.04, 88.81) * mm, "end": v(260.9, 88.13) * mm});
            skLineSegment(sketch, "E1192", {"start": v(260.9, 88.13) * mm, "end": v(260.7, 87.47) * mm});
            skLineSegment(sketch, "E1193", {"start": v(260.7, 87.47) * mm, "end": v(260.4, 86.85) * mm});
            skLineSegment(sketch, "E1194", {"start": v(260.4, 86.85) * mm, "end": v(260.03, 86.27) * mm});
            skLineSegment(sketch, "E1195", {"start": v(260.03, 86.27) * mm, "end": v(259.59, 85.73) * mm});
            skLineSegment(sketch, "E1196", {"start": v(259.59, 85.73) * mm, "end": v(209, 35.16) * mm});
            skLineSegment(sketch, "E1197", {"start": v(209, 35.16) * mm, "end": v(208.5, 34.68) * mm});
            skLineSegment(sketch, "E1198", {"start": v(208.5, 34.68) * mm, "end": v(207.95, 34.28) * mm});
            skLineSegment(sketch, "E1199", {"start": v(207.95, 34.28) * mm, "end": v(207.34, 33.94) * mm});
            skLineSegment(sketch, "E1200", {"start": v(207.34, 33.94) * mm, "end": v(206.7, 33.69) * mm});
            skLineSegment(sketch, "E1201", {"start": v(206.7, 33.69) * mm, "end": v(206.03, 33.52) * mm});
            skLineSegment(sketch, "E1202", {"start": v(206.03, 33.52) * mm, "end": v(205.34, 33.43) * mm});
            skLineSegment(sketch, "E1203", {"start": v(205.34, 33.43) * mm, "end": v(204.66, 33.43) * mm});
            skLineSegment(sketch, "E1204", {"start": v(247.9, 60.5) * mm, "end": v(247.72, 60.53) * mm});
            skLineSegment(sketch, "E1205", {"start": v(247.72, 60.53) * mm, "end": v(247.54, 60.57) * mm});
            skLineSegment(sketch, "E1206", {"start": v(247.54, 60.57) * mm, "end": v(247.36, 60.64) * mm});
            skLineSegment(sketch, "E1207", {"start": v(247.36, 60.64) * mm, "end": v(247.2, 60.73) * mm});
            skLineSegment(sketch, "E1208", {"start": v(247.2, 60.73) * mm, "end": v(247.04, 60.84) * mm});
            skLineSegment(sketch, "E1209", {"start": v(247.04, 60.84) * mm, "end": v(246.9, 60.97) * mm});
            skLineSegment(sketch, "E1210", {"start": v(246.9, 60.97) * mm, "end": v(246.79, 61.12) * mm});
            skLineSegment(sketch, "E1211", {"start": v(246.79, 61.12) * mm, "end": v(246.69, 61.28) * mm});
            skLineSegment(sketch, "E1212", {"start": v(246.69, 61.28) * mm, "end": v(246.6, 61.45) * mm});
            skLineSegment(sketch, "E1213", {"start": v(246.6, 61.45) * mm, "end": v(246.55, 61.63) * mm});
            skLineSegment(sketch, "E1214", {"start": v(246.55, 61.63) * mm, "end": v(246.51, 61.81) * mm});
            skLineSegment(sketch, "E1215", {"start": v(246.51, 61.81) * mm, "end": v(246.5, 62) * mm});
            skLineSegment(sketch, "E1216", {"start": v(246.5, 62) * mm, "end": v(246.51, 62.19) * mm});
            skLineSegment(sketch, "E1217", {"start": v(246.51, 62.19) * mm, "end": v(246.55, 62.37) * mm});
            skLineSegment(sketch, "E1218", {"start": v(246.55, 62.37) * mm, "end": v(246.6, 62.55) * mm});
            skLineSegment(sketch, "E1219", {"start": v(246.6, 62.55) * mm, "end": v(246.69, 62.72) * mm});
            skLineSegment(sketch, "E1220", {"start": v(246.69, 62.72) * mm, "end": v(246.79, 62.88) * mm});
            skLineSegment(sketch, "E1221", {"start": v(246.79, 62.88) * mm, "end": v(246.9, 63.03) * mm});
            skLineSegment(sketch, "E1222", {"start": v(246.9, 63.03) * mm, "end": v(247.04, 63.16) * mm});
            skLineSegment(sketch, "E1223", {"start": v(247.04, 63.16) * mm, "end": v(247.2, 63.27) * mm});
            skLineSegment(sketch, "E1224", {"start": v(247.2, 63.27) * mm, "end": v(247.36, 63.36) * mm});
            skLineSegment(sketch, "E1225", {"start": v(247.36, 63.36) * mm, "end": v(247.54, 63.43) * mm});
            skLineSegment(sketch, "E1226", {"start": v(247.54, 63.43) * mm, "end": v(247.72, 63.47) * mm});
            skLineSegment(sketch, "E1227", {"start": v(247.72, 63.47) * mm, "end": v(247.9, 63.5) * mm});
            skLineSegment(sketch, "E1228", {"start": v(247.9, 63.5) * mm, "end": v(248.1, 63.5) * mm});
            skLineSegment(sketch, "E1229", {"start": v(248.1, 63.5) * mm, "end": v(248.28, 63.47) * mm});
            skLineSegment(sketch, "E1230", {"start": v(248.28, 63.47) * mm, "end": v(248.46, 63.43) * mm});
            skLineSegment(sketch, "E1231", {"start": v(248.46, 63.43) * mm, "end": v(248.64, 63.36) * mm});
            skLineSegment(sketch, "E1232", {"start": v(248.64, 63.36) * mm, "end": v(248.8, 63.27) * mm});
            skLineSegment(sketch, "E1233", {"start": v(248.8, 63.27) * mm, "end": v(248.96, 63.16) * mm});
            skLineSegment(sketch, "E1234", {"start": v(248.96, 63.16) * mm, "end": v(249.1, 63.03) * mm});
            skLineSegment(sketch, "E1235", {"start": v(249.1, 63.03) * mm, "end": v(249.21, 62.88) * mm});
            skLineSegment(sketch, "E1236", {"start": v(249.21, 62.88) * mm, "end": v(249.31, 62.72) * mm});
            skLineSegment(sketch, "E1237", {"start": v(249.31, 62.72) * mm, "end": v(249.4, 62.55) * mm});
            skLineSegment(sketch, "E1238", {"start": v(249.4, 62.55) * mm, "end": v(249.45, 62.37) * mm});
            skLineSegment(sketch, "E1239", {"start": v(249.45, 62.37) * mm, "end": v(249.49, 62.19) * mm});
            skLineSegment(sketch, "E1240", {"start": v(249.49, 62.19) * mm, "end": v(249.5, 62) * mm});
            skLineSegment(sketch, "E1241", {"start": v(249.5, 62) * mm, "end": v(249.49, 61.81) * mm});
            skLineSegment(sketch, "E1242", {"start": v(249.49, 61.81) * mm, "end": v(249.45, 61.63) * mm});
            skLineSegment(sketch, "E1243", {"start": v(249.45, 61.63) * mm, "end": v(249.4, 61.45) * mm});
            skLineSegment(sketch, "E1244", {"start": v(249.4, 61.45) * mm, "end": v(249.31, 61.28) * mm});
            skLineSegment(sketch, "E1245", {"start": v(249.31, 61.28) * mm, "end": v(249.21, 61.12) * mm});
            skLineSegment(sketch, "E1246", {"start": v(249.21, 61.12) * mm, "end": v(249.1, 60.97) * mm});
            skLineSegment(sketch, "E1247", {"start": v(249.1, 60.97) * mm, "end": v(248.96, 60.84) * mm});
            skLineSegment(sketch, "E1248", {"start": v(248.96, 60.84) * mm, "end": v(248.8, 60.73) * mm});
            skLineSegment(sketch, "E1249", {"start": v(248.8, 60.73) * mm, "end": v(248.64, 60.64) * mm});
            skLineSegment(sketch, "E1250", {"start": v(248.64, 60.64) * mm, "end": v(248.46, 60.57) * mm});
            skLineSegment(sketch, "E1251", {"start": v(248.46, 60.57) * mm, "end": v(248.28, 60.53) * mm});
            skLineSegment(sketch, "E1252", {"start": v(248.28, 60.53) * mm, "end": v(248.1, 60.5) * mm});
            skLineSegment(sketch, "E1253", {"start": v(248.1, 60.5) * mm, "end": v(247.9, 60.5) * mm});
            skLineSegment(sketch, "E1254", {"start": v(271.9, 60.5) * mm, "end": v(271.72, 60.53) * mm});
            skLineSegment(sketch, "E1255", {"start": v(271.72, 60.53) * mm, "end": v(271.54, 60.57) * mm});
            skLineSegment(sketch, "E1256", {"start": v(271.54, 60.57) * mm, "end": v(271.36, 60.64) * mm});
            skLineSegment(sketch, "E1257", {"start": v(271.36, 60.64) * mm, "end": v(271.2, 60.73) * mm});
            skLineSegment(sketch, "E1258", {"start": v(271.2, 60.73) * mm, "end": v(271.04, 60.84) * mm});
            skLineSegment(sketch, "E1259", {"start": v(271.04, 60.84) * mm, "end": v(270.9, 60.97) * mm});
            skLineSegment(sketch, "E1260", {"start": v(270.9, 60.97) * mm, "end": v(270.79, 61.12) * mm});
            skLineSegment(sketch, "E1261", {"start": v(270.79, 61.12) * mm, "end": v(270.69, 61.28) * mm});
            skLineSegment(sketch, "E1262", {"start": v(270.69, 61.28) * mm, "end": v(270.6, 61.45) * mm});
            skLineSegment(sketch, "E1263", {"start": v(270.6, 61.45) * mm, "end": v(270.55, 61.63) * mm});
            skLineSegment(sketch, "E1264", {"start": v(270.55, 61.63) * mm, "end": v(270.51, 61.81) * mm});
            skLineSegment(sketch, "E1265", {"start": v(270.51, 61.81) * mm, "end": v(270.5, 62) * mm});
            skLineSegment(sketch, "E1266", {"start": v(270.5, 62) * mm, "end": v(270.51, 62.19) * mm});
            skLineSegment(sketch, "E1267", {"start": v(270.51, 62.19) * mm, "end": v(270.55, 62.37) * mm});
            skLineSegment(sketch, "E1268", {"start": v(270.55, 62.37) * mm, "end": v(270.6, 62.55) * mm});
            skLineSegment(sketch, "E1269", {"start": v(270.6, 62.55) * mm, "end": v(270.69, 62.72) * mm});
            skLineSegment(sketch, "E1270", {"start": v(270.69, 62.72) * mm, "end": v(270.79, 62.88) * mm});
            skLineSegment(sketch, "E1271", {"start": v(270.79, 62.88) * mm, "end": v(270.9, 63.03) * mm});
            skLineSegment(sketch, "E1272", {"start": v(270.9, 63.03) * mm, "end": v(271.04, 63.16) * mm});
            skLineSegment(sketch, "E1273", {"start": v(271.04, 63.16) * mm, "end": v(271.2, 63.27) * mm});
            skLineSegment(sketch, "E1274", {"start": v(271.2, 63.27) * mm, "end": v(271.36, 63.36) * mm});
            skLineSegment(sketch, "E1275", {"start": v(271.36, 63.36) * mm, "end": v(271.54, 63.43) * mm});
            skLineSegment(sketch, "E1276", {"start": v(271.54, 63.43) * mm, "end": v(271.72, 63.47) * mm});
            skLineSegment(sketch, "E1277", {"start": v(271.72, 63.47) * mm, "end": v(271.9, 63.5) * mm});
            skLineSegment(sketch, "E1278", {"start": v(271.9, 63.5) * mm, "end": v(272.1, 63.5) * mm});
            skLineSegment(sketch, "E1279", {"start": v(272.1, 63.5) * mm, "end": v(272.28, 63.47) * mm});
            skLineSegment(sketch, "E1280", {"start": v(272.28, 63.47) * mm, "end": v(272.46, 63.43) * mm});
            skLineSegment(sketch, "E1281", {"start": v(272.46, 63.43) * mm, "end": v(272.64, 63.36) * mm});
            skLineSegment(sketch, "E1282", {"start": v(272.64, 63.36) * mm, "end": v(272.8, 63.27) * mm});
            skLineSegment(sketch, "E1283", {"start": v(272.8, 63.27) * mm, "end": v(272.96, 63.16) * mm});
            skLineSegment(sketch, "E1284", {"start": v(272.96, 63.16) * mm, "end": v(273.1, 63.03) * mm});
            skLineSegment(sketch, "E1285", {"start": v(273.1, 63.03) * mm, "end": v(273.21, 62.88) * mm});
            skLineSegment(sketch, "E1286", {"start": v(273.21, 62.88) * mm, "end": v(273.31, 62.72) * mm});
            skLineSegment(sketch, "E1287", {"start": v(273.31, 62.72) * mm, "end": v(273.4, 62.55) * mm});
            skLineSegment(sketch, "E1288", {"start": v(273.4, 62.55) * mm, "end": v(273.45, 62.37) * mm});
            skLineSegment(sketch, "E1289", {"start": v(273.45, 62.37) * mm, "end": v(273.49, 62.19) * mm});
            skLineSegment(sketch, "E1290", {"start": v(273.49, 62.19) * mm, "end": v(273.5, 62) * mm});
            skLineSegment(sketch, "E1291", {"start": v(273.5, 62) * mm, "end": v(273.49, 61.81) * mm});
            skLineSegment(sketch, "E1292", {"start": v(273.49, 61.81) * mm, "end": v(273.45, 61.63) * mm});
            skLineSegment(sketch, "E1293", {"start": v(273.45, 61.63) * mm, "end": v(273.4, 61.45) * mm});
            skLineSegment(sketch, "E1294", {"start": v(273.4, 61.45) * mm, "end": v(273.31, 61.28) * mm});
            skLineSegment(sketch, "E1295", {"start": v(273.31, 61.28) * mm, "end": v(273.21, 61.12) * mm});
            skLineSegment(sketch, "E1296", {"start": v(273.21, 61.12) * mm, "end": v(273.1, 60.97) * mm});
            skLineSegment(sketch, "E1297", {"start": v(273.1, 60.97) * mm, "end": v(272.96, 60.84) * mm});
            skLineSegment(sketch, "E1298", {"start": v(272.96, 60.84) * mm, "end": v(272.8, 60.73) * mm});
            skLineSegment(sketch, "E1299", {"start": v(272.8, 60.73) * mm, "end": v(272.64, 60.64) * mm});
            skLineSegment(sketch, "E1300", {"start": v(272.64, 60.64) * mm, "end": v(272.46, 60.57) * mm});
            skLineSegment(sketch, "E1301", {"start": v(272.46, 60.57) * mm, "end": v(272.28, 60.53) * mm});
            skLineSegment(sketch, "E1302", {"start": v(272.28, 60.53) * mm, "end": v(272.1, 60.5) * mm});
            skLineSegment(sketch, "E1303", {"start": v(272.1, 60.5) * mm, "end": v(271.9, 60.5) * mm});
            skLineSegment(sketch, "E1304", {"start": v(137.9, 60.5) * mm, "end": v(137.72, 60.53) * mm});
            skLineSegment(sketch, "E1305", {"start": v(137.72, 60.53) * mm, "end": v(137.54, 60.57) * mm});
            skLineSegment(sketch, "E1306", {"start": v(137.54, 60.57) * mm, "end": v(137.36, 60.64) * mm});
            skLineSegment(sketch, "E1307", {"start": v(137.36, 60.64) * mm, "end": v(137.2, 60.73) * mm});
            skLineSegment(sketch, "E1308", {"start": v(137.2, 60.73) * mm, "end": v(137.04, 60.84) * mm});
            skLineSegment(sketch, "E1309", {"start": v(137.04, 60.84) * mm, "end": v(136.9, 60.97) * mm});
            skLineSegment(sketch, "E1310", {"start": v(136.9, 60.97) * mm, "end": v(136.79, 61.12) * mm});
            skLineSegment(sketch, "E1311", {"start": v(136.79, 61.12) * mm, "end": v(136.69, 61.28) * mm});
            skLineSegment(sketch, "E1312", {"start": v(136.69, 61.28) * mm, "end": v(136.6, 61.45) * mm});
            skLineSegment(sketch, "E1313", {"start": v(136.6, 61.45) * mm, "end": v(136.55, 61.63) * mm});
            skLineSegment(sketch, "E1314", {"start": v(136.55, 61.63) * mm, "end": v(136.51, 61.81) * mm});
            skLineSegment(sketch, "E1315", {"start": v(136.51, 61.81) * mm, "end": v(136.5, 62) * mm});
            skLineSegment(sketch, "E1316", {"start": v(136.5, 62) * mm, "end": v(136.51, 62.19) * mm});
            skLineSegment(sketch, "E1317", {"start": v(136.51, 62.19) * mm, "end": v(136.55, 62.37) * mm});
            skLineSegment(sketch, "E1318", {"start": v(136.55, 62.37) * mm, "end": v(136.6, 62.55) * mm});
            skLineSegment(sketch, "E1319", {"start": v(136.6, 62.55) * mm, "end": v(136.69, 62.72) * mm});
            skLineSegment(sketch, "E1320", {"start": v(136.69, 62.72) * mm, "end": v(136.79, 62.88) * mm});
            skLineSegment(sketch, "E1321", {"start": v(136.79, 62.88) * mm, "end": v(136.9, 63.03) * mm});
            skLineSegment(sketch, "E1322", {"start": v(136.9, 63.03) * mm, "end": v(137.04, 63.16) * mm});
            skLineSegment(sketch, "E1323", {"start": v(137.04, 63.16) * mm, "end": v(137.2, 63.27) * mm});
            skLineSegment(sketch, "E1324", {"start": v(137.2, 63.27) * mm, "end": v(137.36, 63.36) * mm});
            skLineSegment(sketch, "E1325", {"start": v(137.36, 63.36) * mm, "end": v(137.54, 63.43) * mm});
            skLineSegment(sketch, "E1326", {"start": v(137.54, 63.43) * mm, "end": v(137.72, 63.47) * mm});
            skLineSegment(sketch, "E1327", {"start": v(137.72, 63.47) * mm, "end": v(137.9, 63.5) * mm});
            skLineSegment(sketch, "E1328", {"start": v(137.9, 63.5) * mm, "end": v(138.1, 63.5) * mm});
            skLineSegment(sketch, "E1329", {"start": v(138.1, 63.5) * mm, "end": v(138.28, 63.47) * mm});
            skLineSegment(sketch, "E1330", {"start": v(138.28, 63.47) * mm, "end": v(138.46, 63.43) * mm});
            skLineSegment(sketch, "E1331", {"start": v(138.46, 63.43) * mm, "end": v(138.64, 63.36) * mm});
            skLineSegment(sketch, "E1332", {"start": v(138.64, 63.36) * mm, "end": v(138.8, 63.27) * mm});
            skLineSegment(sketch, "E1333", {"start": v(138.8, 63.27) * mm, "end": v(138.96, 63.16) * mm});
            skLineSegment(sketch, "E1334", {"start": v(138.96, 63.16) * mm, "end": v(139.1, 63.03) * mm});
            skLineSegment(sketch, "E1335", {"start": v(139.1, 63.03) * mm, "end": v(139.21, 62.88) * mm});
            skLineSegment(sketch, "E1336", {"start": v(139.21, 62.88) * mm, "end": v(139.31, 62.72) * mm});
            skLineSegment(sketch, "E1337", {"start": v(139.31, 62.72) * mm, "end": v(139.4, 62.55) * mm});
            skLineSegment(sketch, "E1338", {"start": v(139.4, 62.55) * mm, "end": v(139.45, 62.37) * mm});
            skLineSegment(sketch, "E1339", {"start": v(139.45, 62.37) * mm, "end": v(139.49, 62.19) * mm});
            skLineSegment(sketch, "E1340", {"start": v(139.49, 62.19) * mm, "end": v(139.5, 62) * mm});
            skLineSegment(sketch, "E1341", {"start": v(139.5, 62) * mm, "end": v(139.49, 61.81) * mm});
            skLineSegment(sketch, "E1342", {"start": v(139.49, 61.81) * mm, "end": v(139.45, 61.63) * mm});
            skLineSegment(sketch, "E1343", {"start": v(139.45, 61.63) * mm, "end": v(139.4, 61.45) * mm});
            skLineSegment(sketch, "E1344", {"start": v(139.4, 61.45) * mm, "end": v(139.31, 61.28) * mm});
            skLineSegment(sketch, "E1345", {"start": v(139.31, 61.28) * mm, "end": v(139.21, 61.12) * mm});
            skLineSegment(sketch, "E1346", {"start": v(139.21, 61.12) * mm, "end": v(139.1, 60.97) * mm});
            skLineSegment(sketch, "E1347", {"start": v(139.1, 60.97) * mm, "end": v(138.96, 60.84) * mm});
            skLineSegment(sketch, "E1348", {"start": v(138.96, 60.84) * mm, "end": v(138.8, 60.73) * mm});
            skLineSegment(sketch, "E1349", {"start": v(138.8, 60.73) * mm, "end": v(138.64, 60.64) * mm});
            skLineSegment(sketch, "E1350", {"start": v(138.64, 60.64) * mm, "end": v(138.46, 60.57) * mm});
            skLineSegment(sketch, "E1351", {"start": v(138.46, 60.57) * mm, "end": v(138.28, 60.53) * mm});
            skLineSegment(sketch, "E1352", {"start": v(138.28, 60.53) * mm, "end": v(138.1, 60.5) * mm});
            skLineSegment(sketch, "E1353", {"start": v(138.1, 60.5) * mm, "end": v(137.9, 60.5) * mm});
            skLineSegment(sketch, "E1354", {"start": v(161.9, 60.5) * mm, "end": v(161.72, 60.53) * mm});
            skLineSegment(sketch, "E1355", {"start": v(161.72, 60.53) * mm, "end": v(161.54, 60.57) * mm});
            skLineSegment(sketch, "E1356", {"start": v(161.54, 60.57) * mm, "end": v(161.36, 60.64) * mm});
            skLineSegment(sketch, "E1357", {"start": v(161.36, 60.64) * mm, "end": v(161.2, 60.73) * mm});
            skLineSegment(sketch, "E1358", {"start": v(161.2, 60.73) * mm, "end": v(161.04, 60.84) * mm});
            skLineSegment(sketch, "E1359", {"start": v(161.04, 60.84) * mm, "end": v(160.9, 60.97) * mm});
            skLineSegment(sketch, "E1360", {"start": v(160.9, 60.97) * mm, "end": v(160.79, 61.12) * mm});
            skLineSegment(sketch, "E1361", {"start": v(160.79, 61.12) * mm, "end": v(160.69, 61.28) * mm});
            skLineSegment(sketch, "E1362", {"start": v(160.69, 61.28) * mm, "end": v(160.6, 61.45) * mm});
            skLineSegment(sketch, "E1363", {"start": v(160.6, 61.45) * mm, "end": v(160.55, 61.63) * mm});
            skLineSegment(sketch, "E1364", {"start": v(160.55, 61.63) * mm, "end": v(160.51, 61.81) * mm});
            skLineSegment(sketch, "E1365", {"start": v(160.51, 61.81) * mm, "end": v(160.5, 62) * mm});
            skLineSegment(sketch, "E1366", {"start": v(160.5, 62) * mm, "end": v(160.51, 62.19) * mm});
            skLineSegment(sketch, "E1367", {"start": v(160.51, 62.19) * mm, "end": v(160.55, 62.37) * mm});
            skLineSegment(sketch, "E1368", {"start": v(160.55, 62.37) * mm, "end": v(160.6, 62.55) * mm});
            skLineSegment(sketch, "E1369", {"start": v(160.6, 62.55) * mm, "end": v(160.69, 62.72) * mm});
            skLineSegment(sketch, "E1370", {"start": v(160.69, 62.72) * mm, "end": v(160.79, 62.88) * mm});
            skLineSegment(sketch, "E1371", {"start": v(160.79, 62.88) * mm, "end": v(160.9, 63.03) * mm});
            skLineSegment(sketch, "E1372", {"start": v(160.9, 63.03) * mm, "end": v(161.04, 63.16) * mm});
            skLineSegment(sketch, "E1373", {"start": v(161.04, 63.16) * mm, "end": v(161.2, 63.27) * mm});
            skLineSegment(sketch, "E1374", {"start": v(161.2, 63.27) * mm, "end": v(161.36, 63.36) * mm});
            skLineSegment(sketch, "E1375", {"start": v(161.36, 63.36) * mm, "end": v(161.54, 63.43) * mm});
            skLineSegment(sketch, "E1376", {"start": v(161.54, 63.43) * mm, "end": v(161.72, 63.47) * mm});
            skLineSegment(sketch, "E1377", {"start": v(161.72, 63.47) * mm, "end": v(161.9, 63.5) * mm});
            skLineSegment(sketch, "E1378", {"start": v(161.9, 63.5) * mm, "end": v(162.1, 63.5) * mm});
            skLineSegment(sketch, "E1379", {"start": v(162.1, 63.5) * mm, "end": v(162.28, 63.47) * mm});
            skLineSegment(sketch, "E1380", {"start": v(162.28, 63.47) * mm, "end": v(162.46, 63.43) * mm});
            skLineSegment(sketch, "E1381", {"start": v(162.46, 63.43) * mm, "end": v(162.64, 63.36) * mm});
            skLineSegment(sketch, "E1382", {"start": v(162.64, 63.36) * mm, "end": v(162.8, 63.27) * mm});
            skLineSegment(sketch, "E1383", {"start": v(162.8, 63.27) * mm, "end": v(162.96, 63.16) * mm});
            skLineSegment(sketch, "E1384", {"start": v(162.96, 63.16) * mm, "end": v(163.1, 63.03) * mm});
            skLineSegment(sketch, "E1385", {"start": v(163.1, 63.03) * mm, "end": v(163.21, 62.88) * mm});
            skLineSegment(sketch, "E1386", {"start": v(163.21, 62.88) * mm, "end": v(163.31, 62.72) * mm});
            skLineSegment(sketch, "E1387", {"start": v(163.31, 62.72) * mm, "end": v(163.4, 62.55) * mm});
            skLineSegment(sketch, "E1388", {"start": v(163.4, 62.55) * mm, "end": v(163.45, 62.37) * mm});
            skLineSegment(sketch, "E1389", {"start": v(163.45, 62.37) * mm, "end": v(163.49, 62.19) * mm});
            skLineSegment(sketch, "E1390", {"start": v(163.49, 62.19) * mm, "end": v(163.5, 62) * mm});
            skLineSegment(sketch, "E1391", {"start": v(163.5, 62) * mm, "end": v(163.49, 61.81) * mm});
            skLineSegment(sketch, "E1392", {"start": v(163.49, 61.81) * mm, "end": v(163.45, 61.63) * mm});
            skLineSegment(sketch, "E1393", {"start": v(163.45, 61.63) * mm, "end": v(163.4, 61.45) * mm});
            skLineSegment(sketch, "E1394", {"start": v(163.4, 61.45) * mm, "end": v(163.31, 61.28) * mm});
            skLineSegment(sketch, "E1395", {"start": v(163.31, 61.28) * mm, "end": v(163.21, 61.12) * mm});
            skLineSegment(sketch, "E1396", {"start": v(163.21, 61.12) * mm, "end": v(163.1, 60.97) * mm});
            skLineSegment(sketch, "E1397", {"start": v(163.1, 60.97) * mm, "end": v(162.96, 60.84) * mm});
            skLineSegment(sketch, "E1398", {"start": v(162.96, 60.84) * mm, "end": v(162.8, 60.73) * mm});
            skLineSegment(sketch, "E1399", {"start": v(162.8, 60.73) * mm, "end": v(162.64, 60.64) * mm});
            skLineSegment(sketch, "E1400", {"start": v(162.64, 60.64) * mm, "end": v(162.46, 60.57) * mm});
            skLineSegment(sketch, "E1401", {"start": v(162.46, 60.57) * mm, "end": v(162.28, 60.53) * mm});
            skLineSegment(sketch, "E1402", {"start": v(162.28, 60.53) * mm, "end": v(162.1, 60.5) * mm});
            skLineSegment(sketch, "E1403", {"start": v(162.1, 60.5) * mm, "end": v(161.9, 60.5) * mm});
            skLineSegment(sketch, "E1404", {"start": v(121.81, -49.04) * mm, "end": v(121.13, -48.9) * mm});
            skLineSegment(sketch, "E1405", {"start": v(121.13, -48.9) * mm, "end": v(120.47, -48.7) * mm});
            skLineSegment(sketch, "E1406", {"start": v(120.47, -48.7) * mm, "end": v(119.85, -48.4) * mm});
            skLineSegment(sketch, "E1407", {"start": v(119.85, -48.4) * mm, "end": v(119.27, -48.03) * mm});
            skLineSegment(sketch, "E1408", {"start": v(119.27, -48.03) * mm, "end": v(118.74, -47.59) * mm});
            skLineSegment(sketch, "E1409", {"start": v(118.74, -47.59) * mm, "end": v(118.26, -47.09) * mm});
            skLineSegment(sketch, "E1410", {"start": v(118.26, -47.09) * mm, "end": v(117.86, -46.53) * mm});
            skLineSegment(sketch, "E1411", {"start": v(117.86, -46.53) * mm, "end": v(117.52, -45.92) * mm});
            skLineSegment(sketch, "E1412", {"start": v(117.52, -45.92) * mm, "end": v(117.27, -45.28) * mm});
            skLineSegment(sketch, "E1413", {"start": v(117.27, -45.28) * mm, "end": v(117.1, -44.61) * mm});
            skLineSegment(sketch, "E1414", {"start": v(117.1, -44.61) * mm, "end": v(117.01, -43.92) * mm});
            skLineSegment(sketch, "E1415", {"start": v(117.01, -43.92) * mm, "end": v(117.01, 57.92) * mm});
            skLineSegment(sketch, "E1416", {"start": v(117.01, 57.92) * mm, "end": v(117.1, 58.6) * mm});
            skLineSegment(sketch, "E1417", {"start": v(117.1, 58.6) * mm, "end": v(117.27, 59.28) * mm});
            skLineSegment(sketch, "E1418", {"start": v(117.27, 59.28) * mm, "end": v(117.52, 59.92) * mm});
            skLineSegment(sketch, "E1419", {"start": v(117.52, 59.92) * mm, "end": v(117.86, 60.53) * mm});
            skLineSegment(sketch, "E1420", {"start": v(117.86, 60.53) * mm, "end": v(118.26, 61.09) * mm});
            skLineSegment(sketch, "E1421", {"start": v(118.26, 61.09) * mm, "end": v(118.74, 61.59) * mm});
            skLineSegment(sketch, "E1422", {"start": v(118.74, 61.59) * mm, "end": v(119.27, 62.03) * mm});
            skLineSegment(sketch, "E1423", {"start": v(119.27, 62.03) * mm, "end": v(119.85, 62.4) * mm});
            skLineSegment(sketch, "E1424", {"start": v(119.85, 62.4) * mm, "end": v(120.47, 62.7) * mm});
            skLineSegment(sketch, "E1425", {"start": v(120.47, 62.7) * mm, "end": v(121.13, 62.9) * mm});
            skLineSegment(sketch, "E1426", {"start": v(121.13, 62.9) * mm, "end": v(121.81, 63.04) * mm});
            skLineSegment(sketch, "E1427", {"start": v(121.81, 63.04) * mm, "end": v(122.5, 63.08) * mm});
            skLineSegment(sketch, "E1428", {"start": v(122.5, 63.08) * mm, "end": v(123.19, 63.04) * mm});
            skLineSegment(sketch, "E1429", {"start": v(123.19, 63.04) * mm, "end": v(123.87, 62.9) * mm});
            skLineSegment(sketch, "E1430", {"start": v(123.87, 62.9) * mm, "end": v(124.53, 62.7) * mm});
            skLineSegment(sketch, "E1431", {"start": v(124.53, 62.7) * mm, "end": v(125.15, 62.4) * mm});
            skLineSegment(sketch, "E1432", {"start": v(125.15, 62.4) * mm, "end": v(125.73, 62.03) * mm});
            skLineSegment(sketch, "E1433", {"start": v(125.73, 62.03) * mm, "end": v(126.27, 61.59) * mm});
            skLineSegment(sketch, "E1434", {"start": v(126.27, 61.59) * mm, "end": v(176.84, 11) * mm});
            skLineSegment(sketch, "E1435", {"start": v(176.84, 11) * mm, "end": v(177.32, 10.5) * mm});
            skLineSegment(sketch, "E1436", {"start": v(177.32, 10.5) * mm, "end": v(177.72, 9.95) * mm});
            skLineSegment(sketch, "E1437", {"start": v(177.72, 9.95) * mm, "end": v(178.06, 9.34) * mm});
            skLineSegment(sketch, "E1438", {"start": v(178.06, 9.34) * mm, "end": v(178.3, 8.7) * mm});
            skLineSegment(sketch, "E1439", {"start": v(178.3, 8.7) * mm, "end": v(178.48, 8.03) * mm});
            skLineSegment(sketch, "E1440", {"start": v(178.48, 8.03) * mm, "end": v(178.57, 7.34) * mm});
            skLineSegment(sketch, "E1441", {"start": v(178.57, 7.34) * mm, "end": v(178.57, 6.66) * mm});
            skLineSegment(sketch, "E1442", {"start": v(178.57, 6.66) * mm, "end": v(178.48, 5.97) * mm});
            skLineSegment(sketch, "E1443", {"start": v(178.48, 5.97) * mm, "end": v(178.3, 5.3) * mm});
            skLineSegment(sketch, "E1444", {"start": v(178.3, 5.3) * mm, "end": v(178.06, 4.66) * mm});
            skLineSegment(sketch, "E1445", {"start": v(178.06, 4.66) * mm, "end": v(177.72, 4.05) * mm});
            skLineSegment(sketch, "E1446", {"start": v(177.72, 4.05) * mm, "end": v(177.32, 3.5) * mm});
            skLineSegment(sketch, "E1447", {"start": v(177.32, 3.5) * mm, "end": v(176.84, 3) * mm});
            skLineSegment(sketch, "E1448", {"start": v(176.84, 3) * mm, "end": v(126.27, -47.59) * mm});
            skLineSegment(sketch, "E1449", {"start": v(126.27, -47.59) * mm, "end": v(125.73, -48.03) * mm});
            skLineSegment(sketch, "E1450", {"start": v(125.73, -48.03) * mm, "end": v(125.15, -48.4) * mm});
            skLineSegment(sketch, "E1451", {"start": v(125.15, -48.4) * mm, "end": v(124.53, -48.7) * mm});
            skLineSegment(sketch, "E1452", {"start": v(124.53, -48.7) * mm, "end": v(123.87, -48.9) * mm});
            skLineSegment(sketch, "E1453", {"start": v(123.87, -48.9) * mm, "end": v(123.19, -49.04) * mm});
            skLineSegment(sketch, "E1454", {"start": v(123.19, -49.04) * mm, "end": v(122.5, -49.08) * mm});
            skLineSegment(sketch, "E1455", {"start": v(122.5, -49.08) * mm, "end": v(121.81, -49.04) * mm});
            skLineSegment(sketch, "E1456", {"start": v(286.81, -49.04) * mm, "end": v(286.13, -48.9) * mm});
            skLineSegment(sketch, "E1457", {"start": v(286.13, -48.9) * mm, "end": v(285.48, -48.7) * mm});
            skLineSegment(sketch, "E1458", {"start": v(285.48, -48.7) * mm, "end": v(284.85, -48.4) * mm});
            skLineSegment(sketch, "E1459", {"start": v(284.85, -48.4) * mm, "end": v(284.27, -48.03) * mm});
            skLineSegment(sketch, "E1460", {"start": v(284.27, -48.03) * mm, "end": v(283.74, -47.59) * mm});
            skLineSegment(sketch, "E1461", {"start": v(283.74, -47.59) * mm, "end": v(233.16, 3) * mm});
            skLineSegment(sketch, "E1462", {"start": v(233.16, 3) * mm, "end": v(232.68, 3.5) * mm});
            skLineSegment(sketch, "E1463", {"start": v(232.68, 3.5) * mm, "end": v(232.28, 4.05) * mm});
            skLineSegment(sketch, "E1464", {"start": v(232.28, 4.05) * mm, "end": v(231.94, 4.66) * mm});
            skLineSegment(sketch, "E1465", {"start": v(231.94, 4.66) * mm, "end": v(231.7, 5.3) * mm});
            skLineSegment(sketch, "E1466", {"start": v(231.7, 5.3) * mm, "end": v(231.52, 5.97) * mm});
            skLineSegment(sketch, "E1467", {"start": v(231.52, 5.97) * mm, "end": v(231.43, 6.66) * mm});
            skLineSegment(sketch, "E1468", {"start": v(231.43, 6.66) * mm, "end": v(231.43, 7.34) * mm});
            skLineSegment(sketch, "E1469", {"start": v(231.43, 7.34) * mm, "end": v(231.52, 8.03) * mm});
            skLineSegment(sketch, "E1470", {"start": v(231.52, 8.03) * mm, "end": v(231.7, 8.7) * mm});
            skLineSegment(sketch, "E1471", {"start": v(231.7, 8.7) * mm, "end": v(231.94, 9.34) * mm});
            skLineSegment(sketch, "E1472", {"start": v(231.94, 9.34) * mm, "end": v(232.28, 9.95) * mm});
            skLineSegment(sketch, "E1473", {"start": v(232.28, 9.95) * mm, "end": v(232.68, 10.5) * mm});
            skLineSegment(sketch, "E1474", {"start": v(232.68, 10.5) * mm, "end": v(233.16, 11) * mm});
            skLineSegment(sketch, "E1475", {"start": v(233.16, 11) * mm, "end": v(283.74, 61.59) * mm});
            skLineSegment(sketch, "E1476", {"start": v(283.74, 61.59) * mm, "end": v(284.27, 62.03) * mm});
            skLineSegment(sketch, "E1477", {"start": v(284.27, 62.03) * mm, "end": v(284.85, 62.4) * mm});
            skLineSegment(sketch, "E1478", {"start": v(284.85, 62.4) * mm, "end": v(285.48, 62.7) * mm});
            skLineSegment(sketch, "E1479", {"start": v(285.48, 62.7) * mm, "end": v(286.13, 62.9) * mm});
            skLineSegment(sketch, "E1480", {"start": v(286.13, 62.9) * mm, "end": v(286.81, 63.04) * mm});
            skLineSegment(sketch, "E1481", {"start": v(286.81, 63.04) * mm, "end": v(287.5, 63.08) * mm});
            skLineSegment(sketch, "E1482", {"start": v(287.5, 63.08) * mm, "end": v(288.19, 63.04) * mm});
            skLineSegment(sketch, "E1483", {"start": v(288.19, 63.04) * mm, "end": v(288.87, 62.9) * mm});
            skLineSegment(sketch, "E1484", {"start": v(288.87, 62.9) * mm, "end": v(289.52, 62.7) * mm});
            skLineSegment(sketch, "E1485", {"start": v(289.52, 62.7) * mm, "end": v(290.15, 62.4) * mm});
            skLineSegment(sketch, "E1486", {"start": v(290.15, 62.4) * mm, "end": v(290.73, 62.03) * mm});
            skLineSegment(sketch, "E1487", {"start": v(290.73, 62.03) * mm, "end": v(291.26, 61.59) * mm});
            skLineSegment(sketch, "E1488", {"start": v(291.26, 61.59) * mm, "end": v(291.74, 61.09) * mm});
            skLineSegment(sketch, "E1489", {"start": v(291.74, 61.09) * mm, "end": v(292.14, 60.53) * mm});
            skLineSegment(sketch, "E1490", {"start": v(292.14, 60.53) * mm, "end": v(292.48, 59.92) * mm});
            skLineSegment(sketch, "E1491", {"start": v(292.48, 59.92) * mm, "end": v(292.73, 59.28) * mm});
            skLineSegment(sketch, "E1492", {"start": v(292.73, 59.28) * mm, "end": v(292.9, 58.6) * mm});
            skLineSegment(sketch, "E1493", {"start": v(292.9, 58.6) * mm, "end": v(292.99, 57.92) * mm});
            skLineSegment(sketch, "E1494", {"start": v(292.99, 57.92) * mm, "end": v(292.99, -43.92) * mm});
            skLineSegment(sketch, "E1495", {"start": v(292.99, -43.92) * mm, "end": v(292.9, -44.61) * mm});
            skLineSegment(sketch, "E1496", {"start": v(292.9, -44.61) * mm, "end": v(292.73, -45.28) * mm});
            skLineSegment(sketch, "E1497", {"start": v(292.73, -45.28) * mm, "end": v(292.48, -45.92) * mm});
            skLineSegment(sketch, "E1498", {"start": v(292.48, -45.92) * mm, "end": v(292.14, -46.53) * mm});
            skLineSegment(sketch, "E1499", {"start": v(292.14, -46.53) * mm, "end": v(291.74, -47.09) * mm});
            skLineSegment(sketch, "E1500", {"start": v(291.74, -47.09) * mm, "end": v(291.26, -47.59) * mm});
            skLineSegment(sketch, "E1501", {"start": v(291.26, -47.59) * mm, "end": v(290.73, -48.03) * mm});
            skLineSegment(sketch, "E1502", {"start": v(290.73, -48.03) * mm, "end": v(290.15, -48.4) * mm});
            skLineSegment(sketch, "E1503", {"start": v(290.15, -48.4) * mm, "end": v(289.52, -48.7) * mm});
            skLineSegment(sketch, "E1504", {"start": v(289.52, -48.7) * mm, "end": v(288.87, -48.9) * mm});
            skLineSegment(sketch, "E1505", {"start": v(288.87, -48.9) * mm, "end": v(288.19, -49.04) * mm});
            skLineSegment(sketch, "E1506", {"start": v(288.19, -49.04) * mm, "end": v(287.5, -49.08) * mm});
            skLineSegment(sketch, "E1507", {"start": v(287.5, -49.08) * mm, "end": v(286.81, -49.04) * mm});
            skLineSegment(sketch, "E1508", {"start": v(111.4, 14.5) * mm, "end": v(111.22, 14.53) * mm});
            skLineSegment(sketch, "E1509", {"start": v(111.22, 14.53) * mm, "end": v(111.04, 14.57) * mm});
            skLineSegment(sketch, "E1510", {"start": v(111.04, 14.57) * mm, "end": v(110.86, 14.64) * mm});
            skLineSegment(sketch, "E1511", {"start": v(110.86, 14.64) * mm, "end": v(110.7, 14.73) * mm});
            skLineSegment(sketch, "E1512", {"start": v(110.7, 14.73) * mm, "end": v(110.54, 14.84) * mm});
            skLineSegment(sketch, "E1513", {"start": v(110.54, 14.84) * mm, "end": v(110.4, 14.97) * mm});
            skLineSegment(sketch, "E1514", {"start": v(110.4, 14.97) * mm, "end": v(110.29, 15.12) * mm});
            skLineSegment(sketch, "E1515", {"start": v(110.29, 15.12) * mm, "end": v(110.19, 15.28) * mm});
            skLineSegment(sketch, "E1516", {"start": v(110.19, 15.28) * mm, "end": v(110.1, 15.45) * mm});
            skLineSegment(sketch, "E1517", {"start": v(110.1, 15.45) * mm, "end": v(110.05, 15.63) * mm});
            skLineSegment(sketch, "E1518", {"start": v(110.05, 15.63) * mm, "end": v(110.01, 15.81) * mm});
            skLineSegment(sketch, "E1519", {"start": v(110.01, 15.81) * mm, "end": v(110, 16) * mm});
            skLineSegment(sketch, "E1520", {"start": v(110, 16) * mm, "end": v(110.01, 16.19) * mm});
            skLineSegment(sketch, "E1521", {"start": v(110.01, 16.19) * mm, "end": v(110.05, 16.37) * mm});
            skLineSegment(sketch, "E1522", {"start": v(110.05, 16.37) * mm, "end": v(110.1, 16.55) * mm});
            skLineSegment(sketch, "E1523", {"start": v(110.1, 16.55) * mm, "end": v(110.19, 16.72) * mm});
            skLineSegment(sketch, "E1524", {"start": v(110.19, 16.72) * mm, "end": v(110.29, 16.88) * mm});
            skLineSegment(sketch, "E1525", {"start": v(110.29, 16.88) * mm, "end": v(110.4, 17.03) * mm});
            skLineSegment(sketch, "E1526", {"start": v(110.4, 17.03) * mm, "end": v(110.54, 17.16) * mm});
            skLineSegment(sketch, "E1527", {"start": v(110.54, 17.16) * mm, "end": v(110.7, 17.27) * mm});
            skLineSegment(sketch, "E1528", {"start": v(110.7, 17.27) * mm, "end": v(110.86, 17.36) * mm});
            skLineSegment(sketch, "E1529", {"start": v(110.86, 17.36) * mm, "end": v(111.04, 17.43) * mm});
            skLineSegment(sketch, "E1530", {"start": v(111.04, 17.43) * mm, "end": v(111.22, 17.47) * mm});
            skLineSegment(sketch, "E1531", {"start": v(111.22, 17.47) * mm, "end": v(111.4, 17.5) * mm});
            skLineSegment(sketch, "E1532", {"start": v(111.4, 17.5) * mm, "end": v(111.6, 17.5) * mm});
            skLineSegment(sketch, "E1533", {"start": v(111.6, 17.5) * mm, "end": v(111.78, 17.47) * mm});
            skLineSegment(sketch, "E1534", {"start": v(111.78, 17.47) * mm, "end": v(111.96, 17.43) * mm});
            skLineSegment(sketch, "E1535", {"start": v(111.96, 17.43) * mm, "end": v(112.14, 17.36) * mm});
            skLineSegment(sketch, "E1536", {"start": v(112.14, 17.36) * mm, "end": v(112.3, 17.27) * mm});
            skLineSegment(sketch, "E1537", {"start": v(112.3, 17.27) * mm, "end": v(112.46, 17.16) * mm});
            skLineSegment(sketch, "E1538", {"start": v(112.46, 17.16) * mm, "end": v(112.6, 17.03) * mm});
            skLineSegment(sketch, "E1539", {"start": v(112.6, 17.03) * mm, "end": v(112.71, 16.88) * mm});
            skLineSegment(sketch, "E1540", {"start": v(112.71, 16.88) * mm, "end": v(112.81, 16.72) * mm});
            skLineSegment(sketch, "E1541", {"start": v(112.81, 16.72) * mm, "end": v(112.9, 16.55) * mm});
            skLineSegment(sketch, "E1542", {"start": v(112.9, 16.55) * mm, "end": v(112.95, 16.37) * mm});
            skLineSegment(sketch, "E1543", {"start": v(112.95, 16.37) * mm, "end": v(112.99, 16.19) * mm});
            skLineSegment(sketch, "E1544", {"start": v(112.99, 16.19) * mm, "end": v(113, 16) * mm});
            skLineSegment(sketch, "E1545", {"start": v(113, 16) * mm, "end": v(112.99, 15.81) * mm});
            skLineSegment(sketch, "E1546", {"start": v(112.99, 15.81) * mm, "end": v(112.95, 15.63) * mm});
            skLineSegment(sketch, "E1547", {"start": v(112.95, 15.63) * mm, "end": v(112.9, 15.45) * mm});
            skLineSegment(sketch, "E1548", {"start": v(112.9, 15.45) * mm, "end": v(112.81, 15.28) * mm});
            skLineSegment(sketch, "E1549", {"start": v(112.81, 15.28) * mm, "end": v(112.71, 15.12) * mm});
            skLineSegment(sketch, "E1550", {"start": v(112.71, 15.12) * mm, "end": v(112.6, 14.97) * mm});
            skLineSegment(sketch, "E1551", {"start": v(112.6, 14.97) * mm, "end": v(112.46, 14.84) * mm});
            skLineSegment(sketch, "E1552", {"start": v(112.46, 14.84) * mm, "end": v(112.3, 14.73) * mm});
            skLineSegment(sketch, "E1553", {"start": v(112.3, 14.73) * mm, "end": v(112.14, 14.64) * mm});
            skLineSegment(sketch, "E1554", {"start": v(112.14, 14.64) * mm, "end": v(111.96, 14.57) * mm});
            skLineSegment(sketch, "E1555", {"start": v(111.96, 14.57) * mm, "end": v(111.78, 14.53) * mm});
            skLineSegment(sketch, "E1556", {"start": v(111.78, 14.53) * mm, "end": v(111.6, 14.5) * mm});
            skLineSegment(sketch, "E1557", {"start": v(111.6, 14.5) * mm, "end": v(111.4, 14.5) * mm});
            skLineSegment(sketch, "E1558", {"start": v(204.9, 13.5) * mm, "end": v(204.72, 13.53) * mm});
            skLineSegment(sketch, "E1559", {"start": v(204.72, 13.53) * mm, "end": v(204.54, 13.57) * mm});
            skLineSegment(sketch, "E1560", {"start": v(204.54, 13.57) * mm, "end": v(204.36, 13.64) * mm});
            skLineSegment(sketch, "E1561", {"start": v(204.36, 13.64) * mm, "end": v(204.2, 13.73) * mm});
            skLineSegment(sketch, "E1562", {"start": v(204.2, 13.73) * mm, "end": v(204.04, 13.84) * mm});
            skLineSegment(sketch, "E1563", {"start": v(204.04, 13.84) * mm, "end": v(203.9, 13.97) * mm});
            skLineSegment(sketch, "E1564", {"start": v(203.9, 13.97) * mm, "end": v(203.79, 14.12) * mm});
            skLineSegment(sketch, "E1565", {"start": v(203.79, 14.12) * mm, "end": v(203.69, 14.28) * mm});
            skLineSegment(sketch, "E1566", {"start": v(203.69, 14.28) * mm, "end": v(203.6, 14.45) * mm});
            skLineSegment(sketch, "E1567", {"start": v(203.6, 14.45) * mm, "end": v(203.55, 14.63) * mm});
            skLineSegment(sketch, "E1568", {"start": v(203.55, 14.63) * mm, "end": v(203.51, 14.81) * mm});
            skLineSegment(sketch, "E1569", {"start": v(203.51, 14.81) * mm, "end": v(203.5, 15) * mm});
            skLineSegment(sketch, "E1570", {"start": v(203.5, 15) * mm, "end": v(203.51, 15.19) * mm});
            skLineSegment(sketch, "E1571", {"start": v(203.51, 15.19) * mm, "end": v(203.55, 15.37) * mm});
            skLineSegment(sketch, "E1572", {"start": v(203.55, 15.37) * mm, "end": v(203.6, 15.55) * mm});
            skLineSegment(sketch, "E1573", {"start": v(203.6, 15.55) * mm, "end": v(203.69, 15.72) * mm});
            skLineSegment(sketch, "E1574", {"start": v(203.69, 15.72) * mm, "end": v(203.79, 15.88) * mm});
            skLineSegment(sketch, "E1575", {"start": v(203.79, 15.88) * mm, "end": v(203.9, 16.03) * mm});
            skLineSegment(sketch, "E1576", {"start": v(203.9, 16.03) * mm, "end": v(204.04, 16.16) * mm});
            skLineSegment(sketch, "E1577", {"start": v(204.04, 16.16) * mm, "end": v(204.2, 16.27) * mm});
            skLineSegment(sketch, "E1578", {"start": v(204.2, 16.27) * mm, "end": v(204.36, 16.36) * mm});
            skLineSegment(sketch, "E1579", {"start": v(204.36, 16.36) * mm, "end": v(204.54, 16.43) * mm});
            skLineSegment(sketch, "E1580", {"start": v(204.54, 16.43) * mm, "end": v(204.72, 16.47) * mm});
            skLineSegment(sketch, "E1581", {"start": v(204.72, 16.47) * mm, "end": v(204.9, 16.5) * mm});
            skLineSegment(sketch, "E1582", {"start": v(204.9, 16.5) * mm, "end": v(205.1, 16.5) * mm});
            skLineSegment(sketch, "E1583", {"start": v(205.1, 16.5) * mm, "end": v(205.28, 16.47) * mm});
            skLineSegment(sketch, "E1584", {"start": v(205.28, 16.47) * mm, "end": v(205.46, 16.43) * mm});
            skLineSegment(sketch, "E1585", {"start": v(205.46, 16.43) * mm, "end": v(205.64, 16.36) * mm});
            skLineSegment(sketch, "E1586", {"start": v(205.64, 16.36) * mm, "end": v(205.8, 16.27) * mm});
            skLineSegment(sketch, "E1587", {"start": v(205.8, 16.27) * mm, "end": v(205.96, 16.16) * mm});
            skLineSegment(sketch, "E1588", {"start": v(205.96, 16.16) * mm, "end": v(206.1, 16.03) * mm});
            skLineSegment(sketch, "E1589", {"start": v(206.1, 16.03) * mm, "end": v(206.21, 15.88) * mm});
            skLineSegment(sketch, "E1590", {"start": v(206.21, 15.88) * mm, "end": v(206.31, 15.72) * mm});
            skLineSegment(sketch, "E1591", {"start": v(206.31, 15.72) * mm, "end": v(206.4, 15.55) * mm});
            skLineSegment(sketch, "E1592", {"start": v(206.4, 15.55) * mm, "end": v(206.45, 15.37) * mm});
            skLineSegment(sketch, "E1593", {"start": v(206.45, 15.37) * mm, "end": v(206.49, 15.19) * mm});
            skLineSegment(sketch, "E1594", {"start": v(206.49, 15.19) * mm, "end": v(206.5, 15) * mm});
            skLineSegment(sketch, "E1595", {"start": v(206.5, 15) * mm, "end": v(206.49, 14.81) * mm});
            skLineSegment(sketch, "E1596", {"start": v(206.49, 14.81) * mm, "end": v(206.45, 14.63) * mm});
            skLineSegment(sketch, "E1597", {"start": v(206.45, 14.63) * mm, "end": v(206.4, 14.45) * mm});
            skLineSegment(sketch, "E1598", {"start": v(206.4, 14.45) * mm, "end": v(206.31, 14.28) * mm});
            skLineSegment(sketch, "E1599", {"start": v(206.31, 14.28) * mm, "end": v(206.21, 14.12) * mm});
            skLineSegment(sketch, "E1600", {"start": v(206.21, 14.12) * mm, "end": v(206.1, 13.97) * mm});
            skLineSegment(sketch, "E1601", {"start": v(206.1, 13.97) * mm, "end": v(205.96, 13.84) * mm});
            skLineSegment(sketch, "E1602", {"start": v(205.96, 13.84) * mm, "end": v(205.8, 13.73) * mm});
            skLineSegment(sketch, "E1603", {"start": v(205.8, 13.73) * mm, "end": v(205.64, 13.64) * mm});
            skLineSegment(sketch, "E1604", {"start": v(205.64, 13.64) * mm, "end": v(205.46, 13.57) * mm});
            skLineSegment(sketch, "E1605", {"start": v(205.46, 13.57) * mm, "end": v(205.28, 13.53) * mm});
            skLineSegment(sketch, "E1606", {"start": v(205.28, 13.53) * mm, "end": v(205.1, 13.5) * mm});
            skLineSegment(sketch, "E1607", {"start": v(205.1, 13.5) * mm, "end": v(204.9, 13.5) * mm});
            skLineSegment(sketch, "E1608", {"start": v(111.4, 8.5) * mm, "end": v(111.22, 8.53) * mm});
            skLineSegment(sketch, "E1609", {"start": v(111.22, 8.53) * mm, "end": v(111.04, 8.57) * mm});
            skLineSegment(sketch, "E1610", {"start": v(111.04, 8.57) * mm, "end": v(110.86, 8.64) * mm});
            skLineSegment(sketch, "E1611", {"start": v(110.86, 8.64) * mm, "end": v(110.7, 8.73) * mm});
            skLineSegment(sketch, "E1612", {"start": v(110.7, 8.73) * mm, "end": v(110.54, 8.84) * mm});
            skLineSegment(sketch, "E1613", {"start": v(110.54, 8.84) * mm, "end": v(110.4, 8.97) * mm});
            skLineSegment(sketch, "E1614", {"start": v(110.4, 8.97) * mm, "end": v(110.29, 9.12) * mm});
            skLineSegment(sketch, "E1615", {"start": v(110.29, 9.12) * mm, "end": v(110.19, 9.28) * mm});
            skLineSegment(sketch, "E1616", {"start": v(110.19, 9.28) * mm, "end": v(110.1, 9.45) * mm});
            skLineSegment(sketch, "E1617", {"start": v(110.1, 9.45) * mm, "end": v(110.05, 9.63) * mm});
            skLineSegment(sketch, "E1618", {"start": v(110.05, 9.63) * mm, "end": v(110.01, 9.81) * mm});
            skLineSegment(sketch, "E1619", {"start": v(110.01, 9.81) * mm, "end": v(110, 10) * mm});
            skLineSegment(sketch, "E1620", {"start": v(110, 10) * mm, "end": v(110.01, 10.19) * mm});
            skLineSegment(sketch, "E1621", {"start": v(110.01, 10.19) * mm, "end": v(110.05, 10.37) * mm});
            skLineSegment(sketch, "E1622", {"start": v(110.05, 10.37) * mm, "end": v(110.1, 10.55) * mm});
            skLineSegment(sketch, "E1623", {"start": v(110.1, 10.55) * mm, "end": v(110.19, 10.72) * mm});
            skLineSegment(sketch, "E1624", {"start": v(110.19, 10.72) * mm, "end": v(110.29, 10.88) * mm});
            skLineSegment(sketch, "E1625", {"start": v(110.29, 10.88) * mm, "end": v(110.4, 11.03) * mm});
            skLineSegment(sketch, "E1626", {"start": v(110.4, 11.03) * mm, "end": v(110.54, 11.16) * mm});
            skLineSegment(sketch, "E1627", {"start": v(110.54, 11.16) * mm, "end": v(110.7, 11.27) * mm});
            skLineSegment(sketch, "E1628", {"start": v(110.7, 11.27) * mm, "end": v(110.86, 11.36) * mm});
            skLineSegment(sketch, "E1629", {"start": v(110.86, 11.36) * mm, "end": v(111.04, 11.43) * mm});
            skLineSegment(sketch, "E1630", {"start": v(111.04, 11.43) * mm, "end": v(111.22, 11.47) * mm});
            skLineSegment(sketch, "E1631", {"start": v(111.22, 11.47) * mm, "end": v(111.4, 11.5) * mm});
            skLineSegment(sketch, "E1632", {"start": v(111.4, 11.5) * mm, "end": v(111.6, 11.5) * mm});
            skLineSegment(sketch, "E1633", {"start": v(111.6, 11.5) * mm, "end": v(111.78, 11.47) * mm});
            skLineSegment(sketch, "E1634", {"start": v(111.78, 11.47) * mm, "end": v(111.96, 11.43) * mm});
            skLineSegment(sketch, "E1635", {"start": v(111.96, 11.43) * mm, "end": v(112.14, 11.36) * mm});
            skLineSegment(sketch, "E1636", {"start": v(112.14, 11.36) * mm, "end": v(112.3, 11.27) * mm});
            skLineSegment(sketch, "E1637", {"start": v(112.3, 11.27) * mm, "end": v(112.46, 11.16) * mm});
            skLineSegment(sketch, "E1638", {"start": v(112.46, 11.16) * mm, "end": v(112.6, 11.03) * mm});
            skLineSegment(sketch, "E1639", {"start": v(112.6, 11.03) * mm, "end": v(112.71, 10.88) * mm});
            skLineSegment(sketch, "E1640", {"start": v(112.71, 10.88) * mm, "end": v(112.81, 10.72) * mm});
            skLineSegment(sketch, "E1641", {"start": v(112.81, 10.72) * mm, "end": v(112.9, 10.55) * mm});
            skLineSegment(sketch, "E1642", {"start": v(112.9, 10.55) * mm, "end": v(112.95, 10.37) * mm});
            skLineSegment(sketch, "E1643", {"start": v(112.95, 10.37) * mm, "end": v(112.99, 10.19) * mm});
            skLineSegment(sketch, "E1644", {"start": v(112.99, 10.19) * mm, "end": v(113, 10) * mm});
            skLineSegment(sketch, "E1645", {"start": v(113, 10) * mm, "end": v(112.99, 9.81) * mm});
            skLineSegment(sketch, "E1646", {"start": v(112.99, 9.81) * mm, "end": v(112.95, 9.63) * mm});
            skLineSegment(sketch, "E1647", {"start": v(112.95, 9.63) * mm, "end": v(112.9, 9.45) * mm});
            skLineSegment(sketch, "E1648", {"start": v(112.9, 9.45) * mm, "end": v(112.81, 9.28) * mm});
            skLineSegment(sketch, "E1649", {"start": v(112.81, 9.28) * mm, "end": v(112.71, 9.12) * mm});
            skLineSegment(sketch, "E1650", {"start": v(112.71, 9.12) * mm, "end": v(112.6, 8.97) * mm});
            skLineSegment(sketch, "E1651", {"start": v(112.6, 8.97) * mm, "end": v(112.46, 8.84) * mm});
            skLineSegment(sketch, "E1652", {"start": v(112.46, 8.84) * mm, "end": v(112.3, 8.73) * mm});
            skLineSegment(sketch, "E1653", {"start": v(112.3, 8.73) * mm, "end": v(112.14, 8.64) * mm});
            skLineSegment(sketch, "E1654", {"start": v(112.14, 8.64) * mm, "end": v(111.96, 8.57) * mm});
            skLineSegment(sketch, "E1655", {"start": v(111.96, 8.57) * mm, "end": v(111.78, 8.53) * mm});
            skLineSegment(sketch, "E1656", {"start": v(111.78, 8.53) * mm, "end": v(111.6, 8.5) * mm});
            skLineSegment(sketch, "E1657", {"start": v(111.6, 8.5) * mm, "end": v(111.4, 8.5) * mm});
            skLineSegment(sketch, "E1658", {"start": v(309.4, 5.5) * mm, "end": v(309.22, 5.53) * mm});
            skLineSegment(sketch, "E1659", {"start": v(309.22, 5.53) * mm, "end": v(309.04, 5.57) * mm});
            skLineSegment(sketch, "E1660", {"start": v(309.04, 5.57) * mm, "end": v(308.86, 5.64) * mm});
            skLineSegment(sketch, "E1661", {"start": v(308.86, 5.64) * mm, "end": v(308.7, 5.73) * mm});
            skLineSegment(sketch, "E1662", {"start": v(308.7, 5.73) * mm, "end": v(308.54, 5.84) * mm});
            skLineSegment(sketch, "E1663", {"start": v(308.54, 5.84) * mm, "end": v(308.4, 5.97) * mm});
            skLineSegment(sketch, "E1664", {"start": v(308.4, 5.97) * mm, "end": v(308.29, 6.12) * mm});
            skLineSegment(sketch, "E1665", {"start": v(308.29, 6.12) * mm, "end": v(308.19, 6.28) * mm});
            skLineSegment(sketch, "E1666", {"start": v(308.19, 6.28) * mm, "end": v(308.1, 6.45) * mm});
            skLineSegment(sketch, "E1667", {"start": v(308.1, 6.45) * mm, "end": v(308.05, 6.63) * mm});
            skLineSegment(sketch, "E1668", {"start": v(308.05, 6.63) * mm, "end": v(308.01, 6.81) * mm});
            skLineSegment(sketch, "E1669", {"start": v(308.01, 6.81) * mm, "end": v(308, 7) * mm});
            skLineSegment(sketch, "E1670", {"start": v(308, 7) * mm, "end": v(308.01, 7.19) * mm});
            skLineSegment(sketch, "E1671", {"start": v(308.01, 7.19) * mm, "end": v(308.05, 7.37) * mm});
            skLineSegment(sketch, "E1672", {"start": v(308.05, 7.37) * mm, "end": v(308.1, 7.55) * mm});
            skLineSegment(sketch, "E1673", {"start": v(308.1, 7.55) * mm, "end": v(308.19, 7.72) * mm});
            skLineSegment(sketch, "E1674", {"start": v(308.19, 7.72) * mm, "end": v(308.29, 7.88) * mm});
            skLineSegment(sketch, "E1675", {"start": v(308.29, 7.88) * mm, "end": v(308.4, 8.03) * mm});
            skLineSegment(sketch, "E1676", {"start": v(308.4, 8.03) * mm, "end": v(308.54, 8.16) * mm});
            skLineSegment(sketch, "E1677", {"start": v(308.54, 8.16) * mm, "end": v(308.7, 8.27) * mm});
            skLineSegment(sketch, "E1678", {"start": v(308.7, 8.27) * mm, "end": v(308.86, 8.36) * mm});
            skLineSegment(sketch, "E1679", {"start": v(308.86, 8.36) * mm, "end": v(309.04, 8.43) * mm});
            skLineSegment(sketch, "E1680", {"start": v(309.04, 8.43) * mm, "end": v(309.22, 8.47) * mm});
            skLineSegment(sketch, "E1681", {"start": v(309.22, 8.47) * mm, "end": v(309.4, 8.5) * mm});
            skLineSegment(sketch, "E1682", {"start": v(309.4, 8.5) * mm, "end": v(309.6, 8.5) * mm});
            skLineSegment(sketch, "E1683", {"start": v(309.6, 8.5) * mm, "end": v(309.78, 8.47) * mm});
            skLineSegment(sketch, "E1684", {"start": v(309.78, 8.47) * mm, "end": v(309.96, 8.43) * mm});
            skLineSegment(sketch, "E1685", {"start": v(309.96, 8.43) * mm, "end": v(310.14, 8.36) * mm});
            skLineSegment(sketch, "E1686", {"start": v(310.14, 8.36) * mm, "end": v(310.3, 8.27) * mm});
            skLineSegment(sketch, "E1687", {"start": v(310.3, 8.27) * mm, "end": v(310.46, 8.16) * mm});
            skLineSegment(sketch, "E1688", {"start": v(310.46, 8.16) * mm, "end": v(310.6, 8.03) * mm});
            skLineSegment(sketch, "E1689", {"start": v(310.6, 8.03) * mm, "end": v(310.71, 7.88) * mm});
            skLineSegment(sketch, "E1690", {"start": v(310.71, 7.88) * mm, "end": v(310.81, 7.72) * mm});
            skLineSegment(sketch, "E1691", {"start": v(310.81, 7.72) * mm, "end": v(310.9, 7.55) * mm});
            skLineSegment(sketch, "E1692", {"start": v(310.9, 7.55) * mm, "end": v(310.95, 7.37) * mm});
            skLineSegment(sketch, "E1693", {"start": v(310.95, 7.37) * mm, "end": v(310.99, 7.19) * mm});
            skLineSegment(sketch, "E1694", {"start": v(310.99, 7.19) * mm, "end": v(311, 7) * mm});
            skLineSegment(sketch, "E1695", {"start": v(311, 7) * mm, "end": v(310.99, 6.81) * mm});
            skLineSegment(sketch, "E1696", {"start": v(310.99, 6.81) * mm, "end": v(310.95, 6.63) * mm});
            skLineSegment(sketch, "E1697", {"start": v(310.95, 6.63) * mm, "end": v(310.9, 6.45) * mm});
            skLineSegment(sketch, "E1698", {"start": v(310.9, 6.45) * mm, "end": v(310.81, 6.28) * mm});
            skLineSegment(sketch, "E1699", {"start": v(310.81, 6.28) * mm, "end": v(310.71, 6.12) * mm});
            skLineSegment(sketch, "E1700", {"start": v(310.71, 6.12) * mm, "end": v(310.6, 5.97) * mm});
            skLineSegment(sketch, "E1701", {"start": v(310.6, 5.97) * mm, "end": v(310.46, 5.84) * mm});
            skLineSegment(sketch, "E1702", {"start": v(310.46, 5.84) * mm, "end": v(310.3, 5.73) * mm});
            skLineSegment(sketch, "E1703", {"start": v(310.3, 5.73) * mm, "end": v(310.14, 5.64) * mm});
            skLineSegment(sketch, "E1704", {"start": v(310.14, 5.64) * mm, "end": v(309.96, 5.57) * mm});
            skLineSegment(sketch, "E1705", {"start": v(309.96, 5.57) * mm, "end": v(309.78, 5.53) * mm});
            skLineSegment(sketch, "E1706", {"start": v(309.78, 5.53) * mm, "end": v(309.6, 5.5) * mm});
            skLineSegment(sketch, "E1707", {"start": v(309.6, 5.5) * mm, "end": v(309.4, 5.5) * mm});
            skLineSegment(sketch, "E1708", {"start": v(111.4, 2.5) * mm, "end": v(111.22, 2.53) * mm});
            skLineSegment(sketch, "E1709", {"start": v(111.22, 2.53) * mm, "end": v(111.04, 2.57) * mm});
            skLineSegment(sketch, "E1710", {"start": v(111.04, 2.57) * mm, "end": v(110.86, 2.64) * mm});
            skLineSegment(sketch, "E1711", {"start": v(110.86, 2.64) * mm, "end": v(110.7, 2.73) * mm});
            skLineSegment(sketch, "E1712", {"start": v(110.7, 2.73) * mm, "end": v(110.54, 2.84) * mm});
            skLineSegment(sketch, "E1713", {"start": v(110.54, 2.84) * mm, "end": v(110.4, 2.97) * mm});
            skLineSegment(sketch, "E1714", {"start": v(110.4, 2.97) * mm, "end": v(110.29, 3.12) * mm});
            skLineSegment(sketch, "E1715", {"start": v(110.29, 3.12) * mm, "end": v(110.19, 3.28) * mm});
            skLineSegment(sketch, "E1716", {"start": v(110.19, 3.28) * mm, "end": v(110.1, 3.45) * mm});
            skLineSegment(sketch, "E1717", {"start": v(110.1, 3.45) * mm, "end": v(110.05, 3.63) * mm});
            skLineSegment(sketch, "E1718", {"start": v(110.05, 3.63) * mm, "end": v(110.01, 3.81) * mm});
            skLineSegment(sketch, "E1719", {"start": v(110.01, 3.81) * mm, "end": v(110, 4) * mm});
            skLineSegment(sketch, "E1720", {"start": v(110, 4) * mm, "end": v(110.01, 4.19) * mm});
            skLineSegment(sketch, "E1721", {"start": v(110.01, 4.19) * mm, "end": v(110.05, 4.37) * mm});
            skLineSegment(sketch, "E1722", {"start": v(110.05, 4.37) * mm, "end": v(110.1, 4.55) * mm});
            skLineSegment(sketch, "E1723", {"start": v(110.1, 4.55) * mm, "end": v(110.19, 4.72) * mm});
            skLineSegment(sketch, "E1724", {"start": v(110.19, 4.72) * mm, "end": v(110.29, 4.88) * mm});
            skLineSegment(sketch, "E1725", {"start": v(110.29, 4.88) * mm, "end": v(110.4, 5.03) * mm});
            skLineSegment(sketch, "E1726", {"start": v(110.4, 5.03) * mm, "end": v(110.54, 5.16) * mm});
            skLineSegment(sketch, "E1727", {"start": v(110.54, 5.16) * mm, "end": v(110.7, 5.27) * mm});
            skLineSegment(sketch, "E1728", {"start": v(110.7, 5.27) * mm, "end": v(110.86, 5.36) * mm});
            skLineSegment(sketch, "E1729", {"start": v(110.86, 5.36) * mm, "end": v(111.04, 5.43) * mm});
            skLineSegment(sketch, "E1730", {"start": v(111.04, 5.43) * mm, "end": v(111.22, 5.47) * mm});
            skLineSegment(sketch, "E1731", {"start": v(111.22, 5.47) * mm, "end": v(111.4, 5.5) * mm});
            skLineSegment(sketch, "E1732", {"start": v(111.4, 5.5) * mm, "end": v(111.6, 5.5) * mm});
            skLineSegment(sketch, "E1733", {"start": v(111.6, 5.5) * mm, "end": v(111.78, 5.47) * mm});
            skLineSegment(sketch, "E1734", {"start": v(111.78, 5.47) * mm, "end": v(111.96, 5.43) * mm});
            skLineSegment(sketch, "E1735", {"start": v(111.96, 5.43) * mm, "end": v(112.14, 5.36) * mm});
            skLineSegment(sketch, "E1736", {"start": v(112.14, 5.36) * mm, "end": v(112.3, 5.27) * mm});
            skLineSegment(sketch, "E1737", {"start": v(112.3, 5.27) * mm, "end": v(112.46, 5.16) * mm});
            skLineSegment(sketch, "E1738", {"start": v(112.46, 5.16) * mm, "end": v(112.6, 5.03) * mm});
            skLineSegment(sketch, "E1739", {"start": v(112.6, 5.03) * mm, "end": v(112.71, 4.88) * mm});
            skLineSegment(sketch, "E1740", {"start": v(112.71, 4.88) * mm, "end": v(112.81, 4.72) * mm});
            skLineSegment(sketch, "E1741", {"start": v(112.81, 4.72) * mm, "end": v(112.9, 4.55) * mm});
            skLineSegment(sketch, "E1742", {"start": v(112.9, 4.55) * mm, "end": v(112.95, 4.37) * mm});
            skLineSegment(sketch, "E1743", {"start": v(112.95, 4.37) * mm, "end": v(112.99, 4.19) * mm});
            skLineSegment(sketch, "E1744", {"start": v(112.99, 4.19) * mm, "end": v(113, 4) * mm});
            skLineSegment(sketch, "E1745", {"start": v(113, 4) * mm, "end": v(112.99, 3.81) * mm});
            skLineSegment(sketch, "E1746", {"start": v(112.99, 3.81) * mm, "end": v(112.95, 3.63) * mm});
            skLineSegment(sketch, "E1747", {"start": v(112.95, 3.63) * mm, "end": v(112.9, 3.45) * mm});
            skLineSegment(sketch, "E1748", {"start": v(112.9, 3.45) * mm, "end": v(112.81, 3.28) * mm});
            skLineSegment(sketch, "E1749", {"start": v(112.81, 3.28) * mm, "end": v(112.71, 3.12) * mm});
            skLineSegment(sketch, "E1750", {"start": v(112.71, 3.12) * mm, "end": v(112.6, 2.97) * mm});
            skLineSegment(sketch, "E1751", {"start": v(112.6, 2.97) * mm, "end": v(112.46, 2.84) * mm});
            skLineSegment(sketch, "E1752", {"start": v(112.46, 2.84) * mm, "end": v(112.3, 2.73) * mm});
            skLineSegment(sketch, "E1753", {"start": v(112.3, 2.73) * mm, "end": v(112.14, 2.64) * mm});
            skLineSegment(sketch, "E1754", {"start": v(112.14, 2.64) * mm, "end": v(111.96, 2.57) * mm});
            skLineSegment(sketch, "E1755", {"start": v(111.96, 2.57) * mm, "end": v(111.78, 2.53) * mm});
            skLineSegment(sketch, "E1756", {"start": v(111.78, 2.53) * mm, "end": v(111.6, 2.5) * mm});
            skLineSegment(sketch, "E1757", {"start": v(111.6, 2.5) * mm, "end": v(111.4, 2.5) * mm});
            skLineSegment(sketch, "E1758", {"start": v(204.9, -2.5) * mm, "end": v(204.72, -2.47) * mm});
            skLineSegment(sketch, "E1759", {"start": v(204.72, -2.47) * mm, "end": v(204.54, -2.43) * mm});
            skLineSegment(sketch, "E1760", {"start": v(204.54, -2.43) * mm, "end": v(204.36, -2.36) * mm});
            skLineSegment(sketch, "E1761", {"start": v(204.36, -2.36) * mm, "end": v(204.2, -2.27) * mm});
            skLineSegment(sketch, "E1762", {"start": v(204.2, -2.27) * mm, "end": v(204.04, -2.16) * mm});
            skLineSegment(sketch, "E1763", {"start": v(204.04, -2.16) * mm, "end": v(203.9, -2.03) * mm});
            skLineSegment(sketch, "E1764", {"start": v(203.9, -2.03) * mm, "end": v(203.79, -1.88) * mm});
            skLineSegment(sketch, "E1765", {"start": v(203.79, -1.88) * mm, "end": v(203.69, -1.72) * mm});
            skLineSegment(sketch, "E1766", {"start": v(203.69, -1.72) * mm, "end": v(203.6, -1.55) * mm});
            skLineSegment(sketch, "E1767", {"start": v(203.6, -1.55) * mm, "end": v(203.55, -1.37) * mm});
            skLineSegment(sketch, "E1768", {"start": v(203.55, -1.37) * mm, "end": v(203.51, -1.19) * mm});
            skLineSegment(sketch, "E1769", {"start": v(203.51, -1.19) * mm, "end": v(203.5, -1) * mm});
            skLineSegment(sketch, "E1770", {"start": v(203.5, -1) * mm, "end": v(203.51, -0.81) * mm});
            skLineSegment(sketch, "E1771", {"start": v(203.51, -0.81) * mm, "end": v(203.55, -0.63) * mm});
            skLineSegment(sketch, "E1772", {"start": v(203.55, -0.63) * mm, "end": v(203.6, -0.45) * mm});
            skLineSegment(sketch, "E1773", {"start": v(203.6, -0.45) * mm, "end": v(203.69, -0.28) * mm});
            skLineSegment(sketch, "E1774", {"start": v(203.69, -0.28) * mm, "end": v(203.79, -0.12) * mm});
            skLineSegment(sketch, "E1775", {"start": v(203.79, -0.12) * mm, "end": v(203.9, 0.03) * mm});
            skLineSegment(sketch, "E1776", {"start": v(203.9, 0.03) * mm, "end": v(204.04, 0.16) * mm});
            skLineSegment(sketch, "E1777", {"start": v(204.04, 0.16) * mm, "end": v(204.2, 0.27) * mm});
            skLineSegment(sketch, "E1778", {"start": v(204.2, 0.27) * mm, "end": v(204.36, 0.36) * mm});
            skLineSegment(sketch, "E1779", {"start": v(204.36, 0.36) * mm, "end": v(204.54, 0.43) * mm});
            skLineSegment(sketch, "E1780", {"start": v(204.54, 0.43) * mm, "end": v(204.72, 0.47) * mm});
            skLineSegment(sketch, "E1781", {"start": v(204.72, 0.47) * mm, "end": v(204.9, 0.5) * mm});
            skLineSegment(sketch, "E1782", {"start": v(204.9, 0.5) * mm, "end": v(205.1, 0.5) * mm});
            skLineSegment(sketch, "E1783", {"start": v(205.1, 0.5) * mm, "end": v(205.28, 0.47) * mm});
            skLineSegment(sketch, "E1784", {"start": v(205.28, 0.47) * mm, "end": v(205.46, 0.43) * mm});
            skLineSegment(sketch, "E1785", {"start": v(205.46, 0.43) * mm, "end": v(205.64, 0.36) * mm});
            skLineSegment(sketch, "E1786", {"start": v(205.64, 0.36) * mm, "end": v(205.8, 0.27) * mm});
            skLineSegment(sketch, "E1787", {"start": v(205.8, 0.27) * mm, "end": v(205.96, 0.16) * mm});
            skLineSegment(sketch, "E1788", {"start": v(205.96, 0.16) * mm, "end": v(206.1, 0.03) * mm});
            skLineSegment(sketch, "E1789", {"start": v(206.1, 0.03) * mm, "end": v(206.21, -0.12) * mm});
            skLineSegment(sketch, "E1790", {"start": v(206.21, -0.12) * mm, "end": v(206.31, -0.28) * mm});
            skLineSegment(sketch, "E1791", {"start": v(206.31, -0.28) * mm, "end": v(206.4, -0.45) * mm});
            skLineSegment(sketch, "E1792", {"start": v(206.4, -0.45) * mm, "end": v(206.45, -0.63) * mm});
            skLineSegment(sketch, "E1793", {"start": v(206.45, -0.63) * mm, "end": v(206.49, -0.81) * mm});
            skLineSegment(sketch, "E1794", {"start": v(206.49, -0.81) * mm, "end": v(206.5, -1) * mm});
            skLineSegment(sketch, "E1795", {"start": v(206.5, -1) * mm, "end": v(206.49, -1.19) * mm});
            skLineSegment(sketch, "E1796", {"start": v(206.49, -1.19) * mm, "end": v(206.45, -1.37) * mm});
            skLineSegment(sketch, "E1797", {"start": v(206.45, -1.37) * mm, "end": v(206.4, -1.55) * mm});
            skLineSegment(sketch, "E1798", {"start": v(206.4, -1.55) * mm, "end": v(206.31, -1.72) * mm});
            skLineSegment(sketch, "E1799", {"start": v(206.31, -1.72) * mm, "end": v(206.21, -1.88) * mm});
            skLineSegment(sketch, "E1800", {"start": v(206.21, -1.88) * mm, "end": v(206.1, -2.03) * mm});
            skLineSegment(sketch, "E1801", {"start": v(206.1, -2.03) * mm, "end": v(205.96, -2.16) * mm});
            skLineSegment(sketch, "E1802", {"start": v(205.96, -2.16) * mm, "end": v(205.8, -2.27) * mm});
            skLineSegment(sketch, "E1803", {"start": v(205.8, -2.27) * mm, "end": v(205.64, -2.36) * mm});
            skLineSegment(sketch, "E1804", {"start": v(205.64, -2.36) * mm, "end": v(205.46, -2.43) * mm});
            skLineSegment(sketch, "E1805", {"start": v(205.46, -2.43) * mm, "end": v(205.28, -2.47) * mm});
            skLineSegment(sketch, "E1806", {"start": v(205.28, -2.47) * mm, "end": v(205.1, -2.5) * mm});
            skLineSegment(sketch, "E1807", {"start": v(205.1, -2.5) * mm, "end": v(204.9, -2.5) * mm});
            skLineSegment(sketch, "E1808", {"start": v(111.4, -3.5) * mm, "end": v(111.22, -3.47) * mm});
            skLineSegment(sketch, "E1809", {"start": v(111.22, -3.47) * mm, "end": v(111.04, -3.43) * mm});
            skLineSegment(sketch, "E1810", {"start": v(111.04, -3.43) * mm, "end": v(110.86, -3.36) * mm});
            skLineSegment(sketch, "E1811", {"start": v(110.86, -3.36) * mm, "end": v(110.7, -3.27) * mm});
            skLineSegment(sketch, "E1812", {"start": v(110.7, -3.27) * mm, "end": v(110.54, -3.16) * mm});
            skLineSegment(sketch, "E1813", {"start": v(110.54, -3.16) * mm, "end": v(110.4, -3.03) * mm});
            skLineSegment(sketch, "E1814", {"start": v(110.4, -3.03) * mm, "end": v(110.29, -2.88) * mm});
            skLineSegment(sketch, "E1815", {"start": v(110.29, -2.88) * mm, "end": v(110.19, -2.72) * mm});
            skLineSegment(sketch, "E1816", {"start": v(110.19, -2.72) * mm, "end": v(110.1, -2.55) * mm});
            skLineSegment(sketch, "E1817", {"start": v(110.1, -2.55) * mm, "end": v(110.05, -2.37) * mm});
            skLineSegment(sketch, "E1818", {"start": v(110.05, -2.37) * mm, "end": v(110.01, -2.19) * mm});
            skLineSegment(sketch, "E1819", {"start": v(110.01, -2.19) * mm, "end": v(110, -2) * mm});
            skLineSegment(sketch, "E1820", {"start": v(110, -2) * mm, "end": v(110.01, -1.81) * mm});
            skLineSegment(sketch, "E1821", {"start": v(110.01, -1.81) * mm, "end": v(110.05, -1.63) * mm});
            skLineSegment(sketch, "E1822", {"start": v(110.05, -1.63) * mm, "end": v(110.1, -1.45) * mm});
            skLineSegment(sketch, "E1823", {"start": v(110.1, -1.45) * mm, "end": v(110.19, -1.28) * mm});
            skLineSegment(sketch, "E1824", {"start": v(110.19, -1.28) * mm, "end": v(110.29, -1.12) * mm});
            skLineSegment(sketch, "E1825", {"start": v(110.29, -1.12) * mm, "end": v(110.4, -0.97) * mm});
            skLineSegment(sketch, "E1826", {"start": v(110.4, -0.97) * mm, "end": v(110.54, -0.84) * mm});
            skLineSegment(sketch, "E1827", {"start": v(110.54, -0.84) * mm, "end": v(110.7, -0.73) * mm});
            skLineSegment(sketch, "E1828", {"start": v(110.7, -0.73) * mm, "end": v(110.86, -0.64) * mm});
            skLineSegment(sketch, "E1829", {"start": v(110.86, -0.64) * mm, "end": v(111.04, -0.57) * mm});
            skLineSegment(sketch, "E1830", {"start": v(111.04, -0.57) * mm, "end": v(111.22, -0.53) * mm});
            skLineSegment(sketch, "E1831", {"start": v(111.22, -0.53) * mm, "end": v(111.4, -0.5) * mm});
            skLineSegment(sketch, "E1832", {"start": v(111.4, -0.5) * mm, "end": v(111.6, -0.5) * mm});
            skLineSegment(sketch, "E1833", {"start": v(111.6, -0.5) * mm, "end": v(111.78, -0.53) * mm});
            skLineSegment(sketch, "E1834", {"start": v(111.78, -0.53) * mm, "end": v(111.96, -0.57) * mm});
            skLineSegment(sketch, "E1835", {"start": v(111.96, -0.57) * mm, "end": v(112.14, -0.64) * mm});
            skLineSegment(sketch, "E1836", {"start": v(112.14, -0.64) * mm, "end": v(112.3, -0.73) * mm});
            skLineSegment(sketch, "E1837", {"start": v(112.3, -0.73) * mm, "end": v(112.46, -0.84) * mm});
            skLineSegment(sketch, "E1838", {"start": v(112.46, -0.84) * mm, "end": v(112.6, -0.97) * mm});
            skLineSegment(sketch, "E1839", {"start": v(112.6, -0.97) * mm, "end": v(112.71, -1.12) * mm});
            skLineSegment(sketch, "E1840", {"start": v(112.71, -1.12) * mm, "end": v(112.81, -1.28) * mm});
            skLineSegment(sketch, "E1841", {"start": v(112.81, -1.28) * mm, "end": v(112.9, -1.45) * mm});
            skLineSegment(sketch, "E1842", {"start": v(112.9, -1.45) * mm, "end": v(112.95, -1.63) * mm});
            skLineSegment(sketch, "E1843", {"start": v(112.95, -1.63) * mm, "end": v(112.99, -1.81) * mm});
            skLineSegment(sketch, "E1844", {"start": v(112.99, -1.81) * mm, "end": v(113, -2) * mm});
            skLineSegment(sketch, "E1845", {"start": v(113, -2) * mm, "end": v(112.99, -2.19) * mm});
            skLineSegment(sketch, "E1846", {"start": v(112.99, -2.19) * mm, "end": v(112.95, -2.37) * mm});
            skLineSegment(sketch, "E1847", {"start": v(112.95, -2.37) * mm, "end": v(112.9, -2.55) * mm});
            skLineSegment(sketch, "E1848", {"start": v(112.9, -2.55) * mm, "end": v(112.81, -2.72) * mm});
            skLineSegment(sketch, "E1849", {"start": v(112.81, -2.72) * mm, "end": v(112.71, -2.88) * mm});
            skLineSegment(sketch, "E1850", {"start": v(112.71, -2.88) * mm, "end": v(112.6, -3.03) * mm});
            skLineSegment(sketch, "E1851", {"start": v(112.6, -3.03) * mm, "end": v(112.46, -3.16) * mm});
            skLineSegment(sketch, "E1852", {"start": v(112.46, -3.16) * mm, "end": v(112.3, -3.27) * mm});
            skLineSegment(sketch, "E1853", {"start": v(112.3, -3.27) * mm, "end": v(112.14, -3.36) * mm});
            skLineSegment(sketch, "E1854", {"start": v(112.14, -3.36) * mm, "end": v(111.96, -3.43) * mm});
            skLineSegment(sketch, "E1855", {"start": v(111.96, -3.43) * mm, "end": v(111.78, -3.47) * mm});
            skLineSegment(sketch, "E1856", {"start": v(111.78, -3.47) * mm, "end": v(111.6, -3.5) * mm});
            skLineSegment(sketch, "E1857", {"start": v(111.6, -3.5) * mm, "end": v(111.4, -3.5) * mm});
            skLineSegment(sketch, "E1858", {"start": v(154.07, -80.99) * mm, "end": v(153.39, -80.9) * mm});
            skLineSegment(sketch, "E1859", {"start": v(153.39, -80.9) * mm, "end": v(152.72, -80.73) * mm});
            skLineSegment(sketch, "E1860", {"start": v(152.72, -80.73) * mm, "end": v(152.08, -80.48) * mm});
            skLineSegment(sketch, "E1861", {"start": v(152.08, -80.48) * mm, "end": v(151.47, -80.14) * mm});
            skLineSegment(sketch, "E1862", {"start": v(151.47, -80.14) * mm, "end": v(150.91, -79.74) * mm});
            skLineSegment(sketch, "E1863", {"start": v(150.91, -79.74) * mm, "end": v(150.41, -79.27) * mm});
            skLineSegment(sketch, "E1864", {"start": v(150.41, -79.27) * mm, "end": v(149.97, -78.73) * mm});
            skLineSegment(sketch, "E1865", {"start": v(149.97, -78.73) * mm, "end": v(149.6, -78.15) * mm});
            skLineSegment(sketch, "E1866", {"start": v(149.6, -78.15) * mm, "end": v(149.3, -77.53) * mm});
            skLineSegment(sketch, "E1867", {"start": v(149.3, -77.53) * mm, "end": v(149.1, -76.87) * mm});
            skLineSegment(sketch, "E1868", {"start": v(149.1, -76.87) * mm, "end": v(148.96, -76.19) * mm});
            skLineSegment(sketch, "E1869", {"start": v(148.96, -76.19) * mm, "end": v(148.92, -75.5) * mm});
            skLineSegment(sketch, "E1870", {"start": v(148.92, -75.5) * mm, "end": v(148.96, -74.81) * mm});
            skLineSegment(sketch, "E1871", {"start": v(148.96, -74.81) * mm, "end": v(149.1, -74.13) * mm});
            skLineSegment(sketch, "E1872", {"start": v(149.1, -74.13) * mm, "end": v(149.3, -73.47) * mm});
            skLineSegment(sketch, "E1873", {"start": v(149.3, -73.47) * mm, "end": v(149.6, -72.85) * mm});
            skLineSegment(sketch, "E1874", {"start": v(149.6, -72.85) * mm, "end": v(149.97, -72.27) * mm});
            skLineSegment(sketch, "E1875", {"start": v(149.97, -72.27) * mm, "end": v(150.41, -71.74) * mm});
            skLineSegment(sketch, "E1876", {"start": v(150.41, -71.74) * mm, "end": v(201, -21.16) * mm});
            skLineSegment(sketch, "E1877", {"start": v(201, -21.16) * mm, "end": v(201.5, -20.68) * mm});
            skLineSegment(sketch, "E1878", {"start": v(201.5, -20.68) * mm, "end": v(202.05, -20.28) * mm});
            skLineSegment(sketch, "E1879", {"start": v(202.05, -20.28) * mm, "end": v(202.66, -19.94) * mm});
            skLineSegment(sketch, "E1880", {"start": v(202.66, -19.94) * mm, "end": v(203.3, -19.7) * mm});
            skLineSegment(sketch, "E1881", {"start": v(203.3, -19.7) * mm, "end": v(203.97, -19.52) * mm});
            skLineSegment(sketch, "E1882", {"start": v(203.97, -19.52) * mm, "end": v(204.66, -19.43) * mm});
            skLineSegment(sketch, "E1883", {"start": v(204.66, -19.43) * mm, "end": v(205.34, -19.43) * mm});
            skLineSegment(sketch, "E1884", {"start": v(205.34, -19.43) * mm, "end": v(206.03, -19.52) * mm});
            skLineSegment(sketch, "E1885", {"start": v(206.03, -19.52) * mm, "end": v(206.7, -19.7) * mm});
            skLineSegment(sketch, "E1886", {"start": v(206.7, -19.7) * mm, "end": v(207.34, -19.94) * mm});
            skLineSegment(sketch, "E1887", {"start": v(207.34, -19.94) * mm, "end": v(207.95, -20.28) * mm});
            skLineSegment(sketch, "E1888", {"start": v(207.95, -20.28) * mm, "end": v(208.5, -20.68) * mm});
            skLineSegment(sketch, "E1889", {"start": v(208.5, -20.68) * mm, "end": v(209, -21.16) * mm});
            skLineSegment(sketch, "E1890", {"start": v(209, -21.16) * mm, "end": v(259.59, -71.73) * mm});
            skLineSegment(sketch, "E1891", {"start": v(259.59, -71.74) * mm, "end": v(260.03, -72.27) * mm});
            skLineSegment(sketch, "E1892", {"start": v(260.03, -72.27) * mm, "end": v(260.4, -72.85) * mm});
            skLineSegment(sketch, "E1893", {"start": v(260.4, -72.85) * mm, "end": v(260.7, -73.47) * mm});
            skLineSegment(sketch, "E1894", {"start": v(260.7, -73.47) * mm, "end": v(260.9, -74.13) * mm});
            skLineSegment(sketch, "E1895", {"start": v(260.9, -74.13) * mm, "end": v(261.04, -74.81) * mm});
            skLineSegment(sketch, "E1896", {"start": v(261.04, -74.81) * mm, "end": v(261.08, -75.5) * mm});
            skLineSegment(sketch, "E1897", {"start": v(261.08, -75.5) * mm, "end": v(261.04, -76.19) * mm});
            skLineSegment(sketch, "E1898", {"start": v(261.04, -76.19) * mm, "end": v(260.9, -76.87) * mm});
            skLineSegment(sketch, "E1899", {"start": v(260.9, -76.87) * mm, "end": v(260.7, -77.53) * mm});
            skLineSegment(sketch, "E1900", {"start": v(260.7, -77.53) * mm, "end": v(260.4, -78.15) * mm});
            skLineSegment(sketch, "E1901", {"start": v(260.4, -78.15) * mm, "end": v(260.03, -78.73) * mm});
            skLineSegment(sketch, "E1902", {"start": v(260.03, -78.73) * mm, "end": v(259.59, -79.27) * mm});
            skLineSegment(sketch, "E1903", {"start": v(259.59, -79.27) * mm, "end": v(259.09, -79.74) * mm});
            skLineSegment(sketch, "E1904", {"start": v(259.09, -79.74) * mm, "end": v(258.53, -80.14) * mm});
            skLineSegment(sketch, "E1905", {"start": v(258.53, -80.14) * mm, "end": v(257.92, -80.48) * mm});
            skLineSegment(sketch, "E1906", {"start": v(257.92, -80.48) * mm, "end": v(257.28, -80.73) * mm});
            skLineSegment(sketch, "E1907", {"start": v(257.28, -80.73) * mm, "end": v(256.6, -80.9) * mm});
            skLineSegment(sketch, "E1908", {"start": v(256.6, -80.9) * mm, "end": v(255.93, -80.99) * mm});
            skLineSegment(sketch, "E1909", {"start": v(255.93, -80.99) * mm, "end": v(154.07, -80.99) * mm});
            skLineSegment(sketch, "E1910", {"start": v(247.9, -49.5) * mm, "end": v(247.72, -49.47) * mm});
            skLineSegment(sketch, "E1911", {"start": v(247.72, -49.47) * mm, "end": v(247.54, -49.43) * mm});
            skLineSegment(sketch, "E1912", {"start": v(247.54, -49.43) * mm, "end": v(247.36, -49.36) * mm});
            skLineSegment(sketch, "E1913", {"start": v(247.36, -49.36) * mm, "end": v(247.2, -49.27) * mm});
            skLineSegment(sketch, "E1914", {"start": v(247.2, -49.27) * mm, "end": v(247.04, -49.16) * mm});
            skLineSegment(sketch, "E1915", {"start": v(247.04, -49.16) * mm, "end": v(246.9, -49.03) * mm});
            skLineSegment(sketch, "E1916", {"start": v(246.9, -49.03) * mm, "end": v(246.79, -48.88) * mm});
            skLineSegment(sketch, "E1917", {"start": v(246.79, -48.88) * mm, "end": v(246.69, -48.72) * mm});
            skLineSegment(sketch, "E1918", {"start": v(246.69, -48.72) * mm, "end": v(246.6, -48.55) * mm});
            skLineSegment(sketch, "E1919", {"start": v(246.6, -48.55) * mm, "end": v(246.55, -48.37) * mm});
            skLineSegment(sketch, "E1920", {"start": v(246.55, -48.37) * mm, "end": v(246.51, -48.19) * mm});
            skLineSegment(sketch, "E1921", {"start": v(246.51, -48.19) * mm, "end": v(246.5, -48) * mm});
            skLineSegment(sketch, "E1922", {"start": v(246.5, -48) * mm, "end": v(246.51, -47.81) * mm});
            skLineSegment(sketch, "E1923", {"start": v(246.51, -47.81) * mm, "end": v(246.55, -47.63) * mm});
            skLineSegment(sketch, "E1924", {"start": v(246.55, -47.63) * mm, "end": v(246.6, -47.45) * mm});
            skLineSegment(sketch, "E1925", {"start": v(246.6, -47.45) * mm, "end": v(246.69, -47.28) * mm});
            skLineSegment(sketch, "E1926", {"start": v(246.69, -47.28) * mm, "end": v(246.79, -47.12) * mm});
            skLineSegment(sketch, "E1927", {"start": v(246.79, -47.12) * mm, "end": v(246.9, -46.97) * mm});
            skLineSegment(sketch, "E1928", {"start": v(246.9, -46.97) * mm, "end": v(247.04, -46.84) * mm});
            skLineSegment(sketch, "E1929", {"start": v(247.04, -46.84) * mm, "end": v(247.2, -46.73) * mm});
            skLineSegment(sketch, "E1930", {"start": v(247.2, -46.73) * mm, "end": v(247.36, -46.64) * mm});
            skLineSegment(sketch, "E1931", {"start": v(247.36, -46.64) * mm, "end": v(247.54, -46.57) * mm});
            skLineSegment(sketch, "E1932", {"start": v(247.54, -46.57) * mm, "end": v(247.72, -46.53) * mm});
            skLineSegment(sketch, "E1933", {"start": v(247.72, -46.53) * mm, "end": v(247.9, -46.5) * mm});
            skLineSegment(sketch, "E1934", {"start": v(247.9, -46.5) * mm, "end": v(248.1, -46.5) * mm});
            skLineSegment(sketch, "E1935", {"start": v(248.1, -46.5) * mm, "end": v(248.28, -46.53) * mm});
            skLineSegment(sketch, "E1936", {"start": v(248.28, -46.53) * mm, "end": v(248.46, -46.57) * mm});
            skLineSegment(sketch, "E1937", {"start": v(248.46, -46.57) * mm, "end": v(248.64, -46.64) * mm});
            skLineSegment(sketch, "E1938", {"start": v(248.64, -46.64) * mm, "end": v(248.8, -46.73) * mm});
            skLineSegment(sketch, "E1939", {"start": v(248.8, -46.73) * mm, "end": v(248.96, -46.84) * mm});
            skLineSegment(sketch, "E1940", {"start": v(248.96, -46.84) * mm, "end": v(249.1, -46.97) * mm});
            skLineSegment(sketch, "E1941", {"start": v(249.1, -46.97) * mm, "end": v(249.21, -47.12) * mm});
            skLineSegment(sketch, "E1942", {"start": v(249.21, -47.12) * mm, "end": v(249.31, -47.28) * mm});
            skLineSegment(sketch, "E1943", {"start": v(249.31, -47.28) * mm, "end": v(249.4, -47.45) * mm});
            skLineSegment(sketch, "E1944", {"start": v(249.4, -47.45) * mm, "end": v(249.45, -47.63) * mm});
            skLineSegment(sketch, "E1945", {"start": v(249.45, -47.63) * mm, "end": v(249.49, -47.81) * mm});
            skLineSegment(sketch, "E1946", {"start": v(249.49, -47.81) * mm, "end": v(249.5, -48) * mm});
            skLineSegment(sketch, "E1947", {"start": v(249.5, -48) * mm, "end": v(249.49, -48.19) * mm});
            skLineSegment(sketch, "E1948", {"start": v(249.49, -48.19) * mm, "end": v(249.45, -48.37) * mm});
            skLineSegment(sketch, "E1949", {"start": v(249.45, -48.37) * mm, "end": v(249.4, -48.55) * mm});
            skLineSegment(sketch, "E1950", {"start": v(249.4, -48.55) * mm, "end": v(249.31, -48.72) * mm});
            skLineSegment(sketch, "E1951", {"start": v(249.31, -48.72) * mm, "end": v(249.21, -48.88) * mm});
            skLineSegment(sketch, "E1952", {"start": v(249.21, -48.88) * mm, "end": v(249.1, -49.03) * mm});
            skLineSegment(sketch, "E1953", {"start": v(249.1, -49.03) * mm, "end": v(248.96, -49.16) * mm});
            skLineSegment(sketch, "E1954", {"start": v(248.96, -49.16) * mm, "end": v(248.8, -49.27) * mm});
            skLineSegment(sketch, "E1955", {"start": v(248.8, -49.27) * mm, "end": v(248.64, -49.36) * mm});
            skLineSegment(sketch, "E1956", {"start": v(248.64, -49.36) * mm, "end": v(248.46, -49.43) * mm});
            skLineSegment(sketch, "E1957", {"start": v(248.46, -49.43) * mm, "end": v(248.28, -49.47) * mm});
            skLineSegment(sketch, "E1958", {"start": v(248.28, -49.47) * mm, "end": v(248.1, -49.5) * mm});
            skLineSegment(sketch, "E1959", {"start": v(248.1, -49.5) * mm, "end": v(247.9, -49.5) * mm});
            skLineSegment(sketch, "E1960", {"start": v(271.9, -49.5) * mm, "end": v(271.72, -49.47) * mm});
            skLineSegment(sketch, "E1961", {"start": v(271.72, -49.47) * mm, "end": v(271.54, -49.43) * mm});
            skLineSegment(sketch, "E1962", {"start": v(271.54, -49.43) * mm, "end": v(271.36, -49.36) * mm});
            skLineSegment(sketch, "E1963", {"start": v(271.36, -49.36) * mm, "end": v(271.2, -49.27) * mm});
            skLineSegment(sketch, "E1964", {"start": v(271.2, -49.27) * mm, "end": v(271.04, -49.16) * mm});
            skLineSegment(sketch, "E1965", {"start": v(271.04, -49.16) * mm, "end": v(270.9, -49.03) * mm});
            skLineSegment(sketch, "E1966", {"start": v(270.9, -49.03) * mm, "end": v(270.79, -48.88) * mm});
            skLineSegment(sketch, "E1967", {"start": v(270.79, -48.88) * mm, "end": v(270.69, -48.72) * mm});
            skLineSegment(sketch, "E1968", {"start": v(270.69, -48.72) * mm, "end": v(270.6, -48.55) * mm});
            skLineSegment(sketch, "E1969", {"start": v(270.6, -48.55) * mm, "end": v(270.55, -48.37) * mm});
            skLineSegment(sketch, "E1970", {"start": v(270.55, -48.37) * mm, "end": v(270.51, -48.19) * mm});
            skLineSegment(sketch, "E1971", {"start": v(270.51, -48.19) * mm, "end": v(270.5, -48) * mm});
            skLineSegment(sketch, "E1972", {"start": v(270.5, -48) * mm, "end": v(270.51, -47.81) * mm});
            skLineSegment(sketch, "E1973", {"start": v(270.51, -47.81) * mm, "end": v(270.55, -47.63) * mm});
            skLineSegment(sketch, "E1974", {"start": v(270.55, -47.63) * mm, "end": v(270.6, -47.45) * mm});
            skLineSegment(sketch, "E1975", {"start": v(270.6, -47.45) * mm, "end": v(270.69, -47.28) * mm});
            skLineSegment(sketch, "E1976", {"start": v(270.69, -47.28) * mm, "end": v(270.79, -47.12) * mm});
            skLineSegment(sketch, "E1977", {"start": v(270.79, -47.12) * mm, "end": v(270.9, -46.97) * mm});
            skLineSegment(sketch, "E1978", {"start": v(270.9, -46.97) * mm, "end": v(271.04, -46.84) * mm});
            skLineSegment(sketch, "E1979", {"start": v(271.04, -46.84) * mm, "end": v(271.2, -46.73) * mm});
            skLineSegment(sketch, "E1980", {"start": v(271.2, -46.73) * mm, "end": v(271.36, -46.64) * mm});
            skLineSegment(sketch, "E1981", {"start": v(271.36, -46.64) * mm, "end": v(271.54, -46.57) * mm});
            skLineSegment(sketch, "E1982", {"start": v(271.54, -46.57) * mm, "end": v(271.72, -46.53) * mm});
            skLineSegment(sketch, "E1983", {"start": v(271.72, -46.53) * mm, "end": v(271.9, -46.5) * mm});
            skLineSegment(sketch, "E1984", {"start": v(271.9, -46.5) * mm, "end": v(272.1, -46.5) * mm});
            skLineSegment(sketch, "E1985", {"start": v(272.1, -46.5) * mm, "end": v(272.28, -46.53) * mm});
            skLineSegment(sketch, "E1986", {"start": v(272.28, -46.53) * mm, "end": v(272.46, -46.57) * mm});
            skLineSegment(sketch, "E1987", {"start": v(272.46, -46.57) * mm, "end": v(272.64, -46.64) * mm});
            skLineSegment(sketch, "E1988", {"start": v(272.64, -46.64) * mm, "end": v(272.8, -46.73) * mm});
            skLineSegment(sketch, "E1989", {"start": v(272.8, -46.73) * mm, "end": v(272.96, -46.84) * mm});
            skLineSegment(sketch, "E1990", {"start": v(272.96, -46.84) * mm, "end": v(273.1, -46.97) * mm});
            skLineSegment(sketch, "E1991", {"start": v(273.1, -46.97) * mm, "end": v(273.21, -47.12) * mm});
            skLineSegment(sketch, "E1992", {"start": v(273.21, -47.12) * mm, "end": v(273.31, -47.28) * mm});
            skLineSegment(sketch, "E1993", {"start": v(273.31, -47.28) * mm, "end": v(273.4, -47.45) * mm});
            skLineSegment(sketch, "E1994", {"start": v(273.4, -47.45) * mm, "end": v(273.45, -47.63) * mm});
            skLineSegment(sketch, "E1995", {"start": v(273.45, -47.63) * mm, "end": v(273.49, -47.81) * mm});
            skLineSegment(sketch, "E1996", {"start": v(273.49, -47.81) * mm, "end": v(273.5, -48) * mm});
            skLineSegment(sketch, "E1997", {"start": v(273.5, -48) * mm, "end": v(273.49, -48.19) * mm});
            skLineSegment(sketch, "E1998", {"start": v(273.49, -48.19) * mm, "end": v(273.45, -48.37) * mm});
            skLineSegment(sketch, "E1999", {"start": v(273.45, -48.37) * mm, "end": v(273.4, -48.55) * mm});
            skLineSegment(sketch, "E2000", {"start": v(273.4, -48.55) * mm, "end": v(273.31, -48.72) * mm});
            skLineSegment(sketch, "E2001", {"start": v(273.31, -48.72) * mm, "end": v(273.21, -48.88) * mm});
            skLineSegment(sketch, "E2002", {"start": v(273.21, -48.88) * mm, "end": v(273.1, -49.03) * mm});
            skLineSegment(sketch, "E2003", {"start": v(273.1, -49.03) * mm, "end": v(272.96, -49.16) * mm});
            skLineSegment(sketch, "E2004", {"start": v(272.96, -49.16) * mm, "end": v(272.8, -49.27) * mm});
            skLineSegment(sketch, "E2005", {"start": v(272.8, -49.27) * mm, "end": v(272.64, -49.36) * mm});
            skLineSegment(sketch, "E2006", {"start": v(272.64, -49.36) * mm, "end": v(272.46, -49.43) * mm});
            skLineSegment(sketch, "E2007", {"start": v(272.46, -49.43) * mm, "end": v(272.28, -49.47) * mm});
            skLineSegment(sketch, "E2008", {"start": v(272.28, -49.47) * mm, "end": v(272.1, -49.5) * mm});
            skLineSegment(sketch, "E2009", {"start": v(272.1, -49.5) * mm, "end": v(271.9, -49.5) * mm});
            skLineSegment(sketch, "E2010", {"start": v(137.9, -49.5) * mm, "end": v(137.72, -49.47) * mm});
            skLineSegment(sketch, "E2011", {"start": v(137.72, -49.47) * mm, "end": v(137.54, -49.43) * mm});
            skLineSegment(sketch, "E2012", {"start": v(137.54, -49.43) * mm, "end": v(137.36, -49.36) * mm});
            skLineSegment(sketch, "E2013", {"start": v(137.36, -49.36) * mm, "end": v(137.2, -49.27) * mm});
            skLineSegment(sketch, "E2014", {"start": v(137.2, -49.27) * mm, "end": v(137.04, -49.16) * mm});
            skLineSegment(sketch, "E2015", {"start": v(137.04, -49.16) * mm, "end": v(136.9, -49.03) * mm});
            skLineSegment(sketch, "E2016", {"start": v(136.9, -49.03) * mm, "end": v(136.79, -48.88) * mm});
            skLineSegment(sketch, "E2017", {"start": v(136.79, -48.88) * mm, "end": v(136.69, -48.72) * mm});
            skLineSegment(sketch, "E2018", {"start": v(136.69, -48.72) * mm, "end": v(136.6, -48.55) * mm});
            skLineSegment(sketch, "E2019", {"start": v(136.6, -48.55) * mm, "end": v(136.55, -48.37) * mm});
            skLineSegment(sketch, "E2020", {"start": v(136.55, -48.37) * mm, "end": v(136.51, -48.19) * mm});
            skLineSegment(sketch, "E2021", {"start": v(136.51, -48.19) * mm, "end": v(136.5, -48) * mm});
            skLineSegment(sketch, "E2022", {"start": v(136.5, -48) * mm, "end": v(136.51, -47.81) * mm});
            skLineSegment(sketch, "E2023", {"start": v(136.51, -47.81) * mm, "end": v(136.55, -47.63) * mm});
            skLineSegment(sketch, "E2024", {"start": v(136.55, -47.63) * mm, "end": v(136.6, -47.45) * mm});
            skLineSegment(sketch, "E2025", {"start": v(136.6, -47.45) * mm, "end": v(136.69, -47.28) * mm});
            skLineSegment(sketch, "E2026", {"start": v(136.69, -47.28) * mm, "end": v(136.79, -47.12) * mm});
            skLineSegment(sketch, "E2027", {"start": v(136.79, -47.12) * mm, "end": v(136.9, -46.97) * mm});
            skLineSegment(sketch, "E2028", {"start": v(136.9, -46.97) * mm, "end": v(137.04, -46.84) * mm});
            skLineSegment(sketch, "E2029", {"start": v(137.04, -46.84) * mm, "end": v(137.2, -46.73) * mm});
            skLineSegment(sketch, "E2030", {"start": v(137.2, -46.73) * mm, "end": v(137.36, -46.64) * mm});
            skLineSegment(sketch, "E2031", {"start": v(137.36, -46.64) * mm, "end": v(137.54, -46.57) * mm});
            skLineSegment(sketch, "E2032", {"start": v(137.54, -46.57) * mm, "end": v(137.72, -46.53) * mm});
            skLineSegment(sketch, "E2033", {"start": v(137.72, -46.53) * mm, "end": v(137.9, -46.5) * mm});
            skLineSegment(sketch, "E2034", {"start": v(137.9, -46.5) * mm, "end": v(138.1, -46.5) * mm});
            skLineSegment(sketch, "E2035", {"start": v(138.1, -46.5) * mm, "end": v(138.28, -46.53) * mm});
            skLineSegment(sketch, "E2036", {"start": v(138.28, -46.53) * mm, "end": v(138.46, -46.57) * mm});
            skLineSegment(sketch, "E2037", {"start": v(138.46, -46.57) * mm, "end": v(138.64, -46.64) * mm});
            skLineSegment(sketch, "E2038", {"start": v(138.64, -46.64) * mm, "end": v(138.8, -46.73) * mm});
            skLineSegment(sketch, "E2039", {"start": v(138.8, -46.73) * mm, "end": v(138.96, -46.84) * mm});
            skLineSegment(sketch, "E2040", {"start": v(138.96, -46.84) * mm, "end": v(139.1, -46.97) * mm});
            skLineSegment(sketch, "E2041", {"start": v(139.1, -46.97) * mm, "end": v(139.21, -47.12) * mm});
            skLineSegment(sketch, "E2042", {"start": v(139.21, -47.12) * mm, "end": v(139.31, -47.28) * mm});
            skLineSegment(sketch, "E2043", {"start": v(139.31, -47.28) * mm, "end": v(139.4, -47.45) * mm});
            skLineSegment(sketch, "E2044", {"start": v(139.4, -47.45) * mm, "end": v(139.45, -47.63) * mm});
            skLineSegment(sketch, "E2045", {"start": v(139.45, -47.63) * mm, "end": v(139.49, -47.81) * mm});
            skLineSegment(sketch, "E2046", {"start": v(139.49, -47.81) * mm, "end": v(139.5, -48) * mm});
            skLineSegment(sketch, "E2047", {"start": v(139.5, -48) * mm, "end": v(139.49, -48.19) * mm});
            skLineSegment(sketch, "E2048", {"start": v(139.49, -48.19) * mm, "end": v(139.45, -48.37) * mm});
            skLineSegment(sketch, "E2049", {"start": v(139.45, -48.37) * mm, "end": v(139.4, -48.55) * mm});
            skLineSegment(sketch, "E2050", {"start": v(139.4, -48.55) * mm, "end": v(139.31, -48.72) * mm});
            skLineSegment(sketch, "E2051", {"start": v(139.31, -48.72) * mm, "end": v(139.21, -48.88) * mm});
            skLineSegment(sketch, "E2052", {"start": v(139.21, -48.88) * mm, "end": v(139.1, -49.03) * mm});
            skLineSegment(sketch, "E2053", {"start": v(139.1, -49.03) * mm, "end": v(138.96, -49.16) * mm});
            skLineSegment(sketch, "E2054", {"start": v(138.96, -49.16) * mm, "end": v(138.8, -49.27) * mm});
            skLineSegment(sketch, "E2055", {"start": v(138.8, -49.27) * mm, "end": v(138.64, -49.36) * mm});
            skLineSegment(sketch, "E2056", {"start": v(138.64, -49.36) * mm, "end": v(138.46, -49.43) * mm});
            skLineSegment(sketch, "E2057", {"start": v(138.46, -49.43) * mm, "end": v(138.28, -49.47) * mm});
            skLineSegment(sketch, "E2058", {"start": v(138.28, -49.47) * mm, "end": v(138.1, -49.5) * mm});
            skLineSegment(sketch, "E2059", {"start": v(138.1, -49.5) * mm, "end": v(137.9, -49.5) * mm});
            skLineSegment(sketch, "E2060", {"start": v(161.9, -49.5) * mm, "end": v(161.72, -49.47) * mm});
            skLineSegment(sketch, "E2061", {"start": v(161.72, -49.47) * mm, "end": v(161.54, -49.43) * mm});
            skLineSegment(sketch, "E2062", {"start": v(161.54, -49.43) * mm, "end": v(161.36, -49.36) * mm});
            skLineSegment(sketch, "E2063", {"start": v(161.36, -49.36) * mm, "end": v(161.2, -49.27) * mm});
            skLineSegment(sketch, "E2064", {"start": v(161.2, -49.27) * mm, "end": v(161.04, -49.16) * mm});
            skLineSegment(sketch, "E2065", {"start": v(161.04, -49.16) * mm, "end": v(160.9, -49.03) * mm});
            skLineSegment(sketch, "E2066", {"start": v(160.9, -49.03) * mm, "end": v(160.79, -48.88) * mm});
            skLineSegment(sketch, "E2067", {"start": v(160.79, -48.88) * mm, "end": v(160.69, -48.72) * mm});
            skLineSegment(sketch, "E2068", {"start": v(160.69, -48.72) * mm, "end": v(160.6, -48.55) * mm});
            skLineSegment(sketch, "E2069", {"start": v(160.6, -48.55) * mm, "end": v(160.55, -48.37) * mm});
            skLineSegment(sketch, "E2070", {"start": v(160.55, -48.37) * mm, "end": v(160.51, -48.19) * mm});
            skLineSegment(sketch, "E2071", {"start": v(160.51, -48.19) * mm, "end": v(160.5, -48) * mm});
            skLineSegment(sketch, "E2072", {"start": v(160.5, -48) * mm, "end": v(160.51, -47.81) * mm});
            skLineSegment(sketch, "E2073", {"start": v(160.51, -47.81) * mm, "end": v(160.55, -47.63) * mm});
            skLineSegment(sketch, "E2074", {"start": v(160.55, -47.63) * mm, "end": v(160.6, -47.45) * mm});
            skLineSegment(sketch, "E2075", {"start": v(160.6, -47.45) * mm, "end": v(160.69, -47.28) * mm});
            skLineSegment(sketch, "E2076", {"start": v(160.69, -47.28) * mm, "end": v(160.79, -47.12) * mm});
            skLineSegment(sketch, "E2077", {"start": v(160.79, -47.12) * mm, "end": v(160.9, -46.97) * mm});
            skLineSegment(sketch, "E2078", {"start": v(160.9, -46.97) * mm, "end": v(161.04, -46.84) * mm});
            skLineSegment(sketch, "E2079", {"start": v(161.04, -46.84) * mm, "end": v(161.2, -46.73) * mm});
            skLineSegment(sketch, "E2080", {"start": v(161.2, -46.73) * mm, "end": v(161.36, -46.64) * mm});
            skLineSegment(sketch, "E2081", {"start": v(161.36, -46.64) * mm, "end": v(161.54, -46.57) * mm});
            skLineSegment(sketch, "E2082", {"start": v(161.54, -46.57) * mm, "end": v(161.72, -46.53) * mm});
            skLineSegment(sketch, "E2083", {"start": v(161.72, -46.53) * mm, "end": v(161.9, -46.5) * mm});
            skLineSegment(sketch, "E2084", {"start": v(161.9, -46.5) * mm, "end": v(162.1, -46.5) * mm});
            skLineSegment(sketch, "E2085", {"start": v(162.1, -46.5) * mm, "end": v(162.28, -46.53) * mm});
            skLineSegment(sketch, "E2086", {"start": v(162.28, -46.53) * mm, "end": v(162.46, -46.57) * mm});
            skLineSegment(sketch, "E2087", {"start": v(162.46, -46.57) * mm, "end": v(162.64, -46.64) * mm});
            skLineSegment(sketch, "E2088", {"start": v(162.64, -46.64) * mm, "end": v(162.8, -46.73) * mm});
            skLineSegment(sketch, "E2089", {"start": v(162.8, -46.73) * mm, "end": v(162.96, -46.84) * mm});
            skLineSegment(sketch, "E2090", {"start": v(162.96, -46.84) * mm, "end": v(163.1, -46.97) * mm});
            skLineSegment(sketch, "E2091", {"start": v(163.1, -46.97) * mm, "end": v(163.21, -47.12) * mm});
            skLineSegment(sketch, "E2092", {"start": v(163.21, -47.12) * mm, "end": v(163.31, -47.28) * mm});
            skLineSegment(sketch, "E2093", {"start": v(163.31, -47.28) * mm, "end": v(163.4, -47.45) * mm});
            skLineSegment(sketch, "E2094", {"start": v(163.4, -47.45) * mm, "end": v(163.45, -47.63) * mm});
            skLineSegment(sketch, "E2095", {"start": v(163.45, -47.63) * mm, "end": v(163.49, -47.81) * mm});
            skLineSegment(sketch, "E2096", {"start": v(163.49, -47.81) * mm, "end": v(163.5, -48) * mm});
            skLineSegment(sketch, "E2097", {"start": v(163.5, -48) * mm, "end": v(163.49, -48.19) * mm});
            skLineSegment(sketch, "E2098", {"start": v(163.49, -48.19) * mm, "end": v(163.45, -48.37) * mm});
            skLineSegment(sketch, "E2099", {"start": v(163.45, -48.37) * mm, "end": v(163.4, -48.55) * mm});
            skLineSegment(sketch, "E2100", {"start": v(163.4, -48.55) * mm, "end": v(163.31, -48.72) * mm});
            skLineSegment(sketch, "E2101", {"start": v(163.31, -48.72) * mm, "end": v(163.21, -48.88) * mm});
            skLineSegment(sketch, "E2102", {"start": v(163.21, -48.88) * mm, "end": v(163.1, -49.03) * mm});
            skLineSegment(sketch, "E2103", {"start": v(163.1, -49.03) * mm, "end": v(162.96, -49.16) * mm});
            skLineSegment(sketch, "E2104", {"start": v(162.96, -49.16) * mm, "end": v(162.8, -49.27) * mm});
            skLineSegment(sketch, "E2105", {"start": v(162.8, -49.27) * mm, "end": v(162.64, -49.36) * mm});
            skLineSegment(sketch, "E2106", {"start": v(162.64, -49.36) * mm, "end": v(162.46, -49.43) * mm});
            skLineSegment(sketch, "E2107", {"start": v(162.46, -49.43) * mm, "end": v(162.28, -49.47) * mm});
            skLineSegment(sketch, "E2108", {"start": v(162.28, -49.47) * mm, "end": v(162.1, -49.5) * mm});
            skLineSegment(sketch, "E2109", {"start": v(162.1, -49.5) * mm, "end": v(161.9, -49.5) * mm});
            skLineSegment(sketch, "E2110", {"start": v(309.4, -99) * mm, "end": v(309.22, -98.97) * mm});
            skLineSegment(sketch, "E2111", {"start": v(309.22, -98.97) * mm, "end": v(309.04, -98.93) * mm});
            skLineSegment(sketch, "E2112", {"start": v(309.04, -98.93) * mm, "end": v(308.86, -98.86) * mm});
            skLineSegment(sketch, "E2113", {"start": v(308.86, -98.86) * mm, "end": v(308.7, -98.77) * mm});
            skLineSegment(sketch, "E2114", {"start": v(308.7, -98.77) * mm, "end": v(308.54, -98.66) * mm});
            skLineSegment(sketch, "E2115", {"start": v(308.54, -98.66) * mm, "end": v(308.4, -98.53) * mm});
            skLineSegment(sketch, "E2116", {"start": v(308.4, -98.53) * mm, "end": v(308.29, -98.38) * mm});
            skLineSegment(sketch, "E2117", {"start": v(308.29, -98.38) * mm, "end": v(308.19, -98.22) * mm});
            skLineSegment(sketch, "E2118", {"start": v(308.19, -98.22) * mm, "end": v(308.1, -98.05) * mm});
            skLineSegment(sketch, "E2119", {"start": v(308.1, -98.05) * mm, "end": v(308.05, -97.87) * mm});
            skLineSegment(sketch, "E2120", {"start": v(308.05, -97.87) * mm, "end": v(308.01, -97.69) * mm});
            skLineSegment(sketch, "E2121", {"start": v(308.01, -97.69) * mm, "end": v(308, -97.5) * mm});
            skLineSegment(sketch, "E2122", {"start": v(308, -97.5) * mm, "end": v(308.01, -97.31) * mm});
            skLineSegment(sketch, "E2123", {"start": v(308.01, -97.31) * mm, "end": v(308.05, -97.13) * mm});
            skLineSegment(sketch, "E2124", {"start": v(308.05, -97.13) * mm, "end": v(308.1, -96.95) * mm});
            skLineSegment(sketch, "E2125", {"start": v(308.1, -96.95) * mm, "end": v(308.19, -96.78) * mm});
            skLineSegment(sketch, "E2126", {"start": v(308.19, -96.78) * mm, "end": v(308.29, -96.62) * mm});
            skLineSegment(sketch, "E2127", {"start": v(308.29, -96.62) * mm, "end": v(308.4, -96.47) * mm});
            skLineSegment(sketch, "E2128", {"start": v(308.4, -96.47) * mm, "end": v(308.54, -96.34) * mm});
            skLineSegment(sketch, "E2129", {"start": v(308.54, -96.34) * mm, "end": v(308.7, -96.23) * mm});
            skLineSegment(sketch, "E2130", {"start": v(308.7, -96.23) * mm, "end": v(308.86, -96.14) * mm});
            skLineSegment(sketch, "E2131", {"start": v(308.86, -96.14) * mm, "end": v(309.04, -96.07) * mm});
            skLineSegment(sketch, "E2132", {"start": v(309.04, -96.07) * mm, "end": v(309.22, -96.03) * mm});
            skLineSegment(sketch, "E2133", {"start": v(309.22, -96.03) * mm, "end": v(309.4, -96) * mm});
            skLineSegment(sketch, "E2134", {"start": v(309.4, -96) * mm, "end": v(309.6, -96) * mm});
            skLineSegment(sketch, "E2135", {"start": v(309.6, -96) * mm, "end": v(309.78, -96.03) * mm});
            skLineSegment(sketch, "E2136", {"start": v(309.78, -96.03) * mm, "end": v(309.96, -96.07) * mm});
            skLineSegment(sketch, "E2137", {"start": v(309.96, -96.07) * mm, "end": v(310.14, -96.14) * mm});
            skLineSegment(sketch, "E2138", {"start": v(310.14, -96.14) * mm, "end": v(310.3, -96.23) * mm});
            skLineSegment(sketch, "E2139", {"start": v(310.3, -96.23) * mm, "end": v(310.46, -96.34) * mm});
            skLineSegment(sketch, "E2140", {"start": v(310.46, -96.34) * mm, "end": v(310.6, -96.47) * mm});
            skLineSegment(sketch, "E2141", {"start": v(310.6, -96.47) * mm, "end": v(310.71, -96.62) * mm});
            skLineSegment(sketch, "E2142", {"start": v(310.71, -96.62) * mm, "end": v(310.81, -96.78) * mm});
            skLineSegment(sketch, "E2143", {"start": v(310.81, -96.78) * mm, "end": v(310.9, -96.95) * mm});
            skLineSegment(sketch, "E2144", {"start": v(310.9, -96.95) * mm, "end": v(310.95, -97.13) * mm});
            skLineSegment(sketch, "E2145", {"start": v(310.95, -97.13) * mm, "end": v(310.99, -97.31) * mm});
            skLineSegment(sketch, "E2146", {"start": v(310.99, -97.31) * mm, "end": v(311, -97.5) * mm});
            skLineSegment(sketch, "E2147", {"start": v(311, -97.5) * mm, "end": v(310.99, -97.69) * mm});
            skLineSegment(sketch, "E2148", {"start": v(310.99, -97.69) * mm, "end": v(310.95, -97.87) * mm});
            skLineSegment(sketch, "E2149", {"start": v(310.95, -97.87) * mm, "end": v(310.9, -98.05) * mm});
            skLineSegment(sketch, "E2150", {"start": v(310.9, -98.05) * mm, "end": v(310.81, -98.22) * mm});
            skLineSegment(sketch, "E2151", {"start": v(310.81, -98.22) * mm, "end": v(310.71, -98.38) * mm});
            skLineSegment(sketch, "E2152", {"start": v(310.71, -98.38) * mm, "end": v(310.6, -98.53) * mm});
            skLineSegment(sketch, "E2153", {"start": v(310.6, -98.53) * mm, "end": v(310.46, -98.66) * mm});
            skLineSegment(sketch, "E2154", {"start": v(310.46, -98.66) * mm, "end": v(310.3, -98.77) * mm});
            skLineSegment(sketch, "E2155", {"start": v(310.3, -98.77) * mm, "end": v(310.14, -98.86) * mm});
            skLineSegment(sketch, "E2156", {"start": v(310.14, -98.86) * mm, "end": v(309.96, -98.93) * mm});
            skLineSegment(sketch, "E2157", {"start": v(309.96, -98.93) * mm, "end": v(309.78, -98.97) * mm});
            skLineSegment(sketch, "E2158", {"start": v(309.78, -98.97) * mm, "end": v(309.6, -99) * mm});
            skLineSegment(sketch, "E2159", {"start": v(309.6, -99) * mm, "end": v(309.4, -99) * mm});
            skLineSegment(sketch, "E2160", {"start": v(100.4, -99) * mm, "end": v(100.22, -98.97) * mm});
            skLineSegment(sketch, "E2161", {"start": v(100.22, -98.97) * mm, "end": v(100.04, -98.93) * mm});
            skLineSegment(sketch, "E2162", {"start": v(100.04, -98.93) * mm, "end": v(99.86, -98.86) * mm});
            skLineSegment(sketch, "E2163", {"start": v(99.86, -98.86) * mm, "end": v(99.7, -98.77) * mm});
            skLineSegment(sketch, "E2164", {"start": v(99.7, -98.77) * mm, "end": v(99.54, -98.66) * mm});
            skLineSegment(sketch, "E2165", {"start": v(99.54, -98.66) * mm, "end": v(99.4, -98.53) * mm});
            skLineSegment(sketch, "E2166", {"start": v(99.4, -98.53) * mm, "end": v(99.29, -98.38) * mm});
            skLineSegment(sketch, "E2167", {"start": v(99.29, -98.38) * mm, "end": v(99.19, -98.22) * mm});
            skLineSegment(sketch, "E2168", {"start": v(99.19, -98.22) * mm, "end": v(99.1, -98.05) * mm});
            skLineSegment(sketch, "E2169", {"start": v(99.1, -98.05) * mm, "end": v(99.05, -97.87) * mm});
            skLineSegment(sketch, "E2170", {"start": v(99.05, -97.87) * mm, "end": v(99.01, -97.69) * mm});
            skLineSegment(sketch, "E2171", {"start": v(99.01, -97.69) * mm, "end": v(99, -97.5) * mm});
            skLineSegment(sketch, "E2172", {"start": v(99, -97.5) * mm, "end": v(99.01, -97.31) * mm});
            skLineSegment(sketch, "E2173", {"start": v(99.01, -97.31) * mm, "end": v(99.05, -97.13) * mm});
            skLineSegment(sketch, "E2174", {"start": v(99.05, -97.13) * mm, "end": v(99.1, -96.95) * mm});
            skLineSegment(sketch, "E2175", {"start": v(99.1, -96.95) * mm, "end": v(99.19, -96.78) * mm});
            skLineSegment(sketch, "E2176", {"start": v(99.19, -96.78) * mm, "end": v(99.29, -96.62) * mm});
            skLineSegment(sketch, "E2177", {"start": v(99.29, -96.62) * mm, "end": v(99.4, -96.47) * mm});
            skLineSegment(sketch, "E2178", {"start": v(99.4, -96.47) * mm, "end": v(99.54, -96.34) * mm});
            skLineSegment(sketch, "E2179", {"start": v(99.54, -96.34) * mm, "end": v(99.7, -96.23) * mm});
            skLineSegment(sketch, "E2180", {"start": v(99.7, -96.23) * mm, "end": v(99.86, -96.14) * mm});
            skLineSegment(sketch, "E2181", {"start": v(99.86, -96.14) * mm, "end": v(100.04, -96.07) * mm});
            skLineSegment(sketch, "E2182", {"start": v(100.04, -96.07) * mm, "end": v(100.22, -96.03) * mm});
            skLineSegment(sketch, "E2183", {"start": v(100.22, -96.03) * mm, "end": v(100.4, -96) * mm});
            skLineSegment(sketch, "E2184", {"start": v(100.4, -96) * mm, "end": v(100.6, -96) * mm});
            skLineSegment(sketch, "E2185", {"start": v(100.6, -96) * mm, "end": v(100.78, -96.03) * mm});
            skLineSegment(sketch, "E2186", {"start": v(100.78, -96.03) * mm, "end": v(100.96, -96.07) * mm});
            skLineSegment(sketch, "E2187", {"start": v(100.96, -96.07) * mm, "end": v(101.14, -96.14) * mm});
            skLineSegment(sketch, "E2188", {"start": v(101.14, -96.14) * mm, "end": v(101.3, -96.23) * mm});
            skLineSegment(sketch, "E2189", {"start": v(101.3, -96.23) * mm, "end": v(101.46, -96.34) * mm});
            skLineSegment(sketch, "E2190", {"start": v(101.46, -96.34) * mm, "end": v(101.6, -96.47) * mm});
            skLineSegment(sketch, "E2191", {"start": v(101.6, -96.47) * mm, "end": v(101.71, -96.62) * mm});
            skLineSegment(sketch, "E2192", {"start": v(101.71, -96.62) * mm, "end": v(101.81, -96.78) * mm});
            skLineSegment(sketch, "E2193", {"start": v(101.81, -96.78) * mm, "end": v(101.9, -96.95) * mm});
            skLineSegment(sketch, "E2194", {"start": v(101.9, -96.95) * mm, "end": v(101.95, -97.13) * mm});
            skLineSegment(sketch, "E2195", {"start": v(101.95, -97.13) * mm, "end": v(101.99, -97.31) * mm});
            skLineSegment(sketch, "E2196", {"start": v(101.99, -97.31) * mm, "end": v(102, -97.5) * mm});
            skLineSegment(sketch, "E2197", {"start": v(102, -97.5) * mm, "end": v(101.99, -97.69) * mm});
            skLineSegment(sketch, "E2198", {"start": v(101.99, -97.69) * mm, "end": v(101.95, -97.87) * mm});
            skLineSegment(sketch, "E2199", {"start": v(101.95, -97.87) * mm, "end": v(101.9, -98.05) * mm});
            skLineSegment(sketch, "E2200", {"start": v(101.9, -98.05) * mm, "end": v(101.81, -98.22) * mm});
            skLineSegment(sketch, "E2201", {"start": v(101.81, -98.22) * mm, "end": v(101.71, -98.38) * mm});
            skLineSegment(sketch, "E2202", {"start": v(101.71, -98.38) * mm, "end": v(101.6, -98.53) * mm});
            skLineSegment(sketch, "E2203", {"start": v(101.6, -98.53) * mm, "end": v(101.46, -98.66) * mm});
            skLineSegment(sketch, "E2204", {"start": v(101.46, -98.66) * mm, "end": v(101.3, -98.77) * mm});
            skLineSegment(sketch, "E2205", {"start": v(101.3, -98.77) * mm, "end": v(101.14, -98.86) * mm});
            skLineSegment(sketch, "E2206", {"start": v(101.14, -98.86) * mm, "end": v(100.96, -98.93) * mm});
            skLineSegment(sketch, "E2207", {"start": v(100.96, -98.93) * mm, "end": v(100.78, -98.97) * mm});
            skLineSegment(sketch, "E2208", {"start": v(100.78, -98.97) * mm, "end": v(100.6, -99) * mm});
            skLineSegment(sketch, "E2209", {"start": v(100.6, -99) * mm, "end": v(100.4, -99) * mm});
            skLineSegment(sketch, "E2210", {"start": v(204.9, -99) * mm, "end": v(204.72, -98.97) * mm});
            skLineSegment(sketch, "E2211", {"start": v(204.72, -98.97) * mm, "end": v(204.54, -98.93) * mm});
            skLineSegment(sketch, "E2212", {"start": v(204.54, -98.93) * mm, "end": v(204.36, -98.86) * mm});
            skLineSegment(sketch, "E2213", {"start": v(204.36, -98.86) * mm, "end": v(204.2, -98.77) * mm});
            skLineSegment(sketch, "E2214", {"start": v(204.2, -98.77) * mm, "end": v(204.04, -98.66) * mm});
            skLineSegment(sketch, "E2215", {"start": v(204.04, -98.66) * mm, "end": v(203.9, -98.53) * mm});
            skLineSegment(sketch, "E2216", {"start": v(203.9, -98.53) * mm, "end": v(203.79, -98.38) * mm});
            skLineSegment(sketch, "E2217", {"start": v(203.79, -98.38) * mm, "end": v(203.69, -98.22) * mm});
            skLineSegment(sketch, "E2218", {"start": v(203.69, -98.22) * mm, "end": v(203.6, -98.05) * mm});
            skLineSegment(sketch, "E2219", {"start": v(203.6, -98.05) * mm, "end": v(203.55, -97.87) * mm});
            skLineSegment(sketch, "E2220", {"start": v(203.55, -97.87) * mm, "end": v(203.51, -97.69) * mm});
            skLineSegment(sketch, "E2221", {"start": v(203.51, -97.69) * mm, "end": v(203.5, -97.5) * mm});
            skLineSegment(sketch, "E2222", {"start": v(203.5, -97.5) * mm, "end": v(203.51, -97.31) * mm});
            skLineSegment(sketch, "E2223", {"start": v(203.51, -97.31) * mm, "end": v(203.55, -97.13) * mm});
            skLineSegment(sketch, "E2224", {"start": v(203.55, -97.13) * mm, "end": v(203.6, -96.95) * mm});
            skLineSegment(sketch, "E2225", {"start": v(203.6, -96.95) * mm, "end": v(203.69, -96.78) * mm});
            skLineSegment(sketch, "E2226", {"start": v(203.69, -96.78) * mm, "end": v(203.79, -96.62) * mm});
            skLineSegment(sketch, "E2227", {"start": v(203.79, -96.62) * mm, "end": v(203.9, -96.47) * mm});
            skLineSegment(sketch, "E2228", {"start": v(203.9, -96.47) * mm, "end": v(204.04, -96.34) * mm});
            skLineSegment(sketch, "E2229", {"start": v(204.04, -96.34) * mm, "end": v(204.2, -96.23) * mm});
            skLineSegment(sketch, "E2230", {"start": v(204.2, -96.23) * mm, "end": v(204.36, -96.14) * mm});
            skLineSegment(sketch, "E2231", {"start": v(204.36, -96.14) * mm, "end": v(204.54, -96.07) * mm});
            skLineSegment(sketch, "E2232", {"start": v(204.54, -96.07) * mm, "end": v(204.72, -96.03) * mm});
            skLineSegment(sketch, "E2233", {"start": v(204.72, -96.03) * mm, "end": v(204.9, -96) * mm});
            skLineSegment(sketch, "E2234", {"start": v(204.9, -96) * mm, "end": v(205.1, -96) * mm});
            skLineSegment(sketch, "E2235", {"start": v(205.1, -96) * mm, "end": v(205.28, -96.03) * mm});
            skLineSegment(sketch, "E2236", {"start": v(205.28, -96.03) * mm, "end": v(205.46, -96.07) * mm});
            skLineSegment(sketch, "E2237", {"start": v(205.46, -96.07) * mm, "end": v(205.64, -96.14) * mm});
            skLineSegment(sketch, "E2238", {"start": v(205.64, -96.14) * mm, "end": v(205.8, -96.23) * mm});
            skLineSegment(sketch, "E2239", {"start": v(205.8, -96.23) * mm, "end": v(205.96, -96.34) * mm});
            skLineSegment(sketch, "E2240", {"start": v(205.96, -96.34) * mm, "end": v(206.1, -96.47) * mm});
            skLineSegment(sketch, "E2241", {"start": v(206.1, -96.47) * mm, "end": v(206.21, -96.62) * mm});
            skLineSegment(sketch, "E2242", {"start": v(206.21, -96.62) * mm, "end": v(206.31, -96.78) * mm});
            skLineSegment(sketch, "E2243", {"start": v(206.31, -96.78) * mm, "end": v(206.4, -96.95) * mm});
            skLineSegment(sketch, "E2244", {"start": v(206.4, -96.95) * mm, "end": v(206.45, -97.13) * mm});
            skLineSegment(sketch, "E2245", {"start": v(206.45, -97.13) * mm, "end": v(206.49, -97.31) * mm});
            skLineSegment(sketch, "E2246", {"start": v(206.49, -97.31) * mm, "end": v(206.5, -97.5) * mm});
            skLineSegment(sketch, "E2247", {"start": v(206.5, -97.5) * mm, "end": v(206.49, -97.69) * mm});
            skLineSegment(sketch, "E2248", {"start": v(206.49, -97.69) * mm, "end": v(206.45, -97.87) * mm});
            skLineSegment(sketch, "E2249", {"start": v(206.45, -97.87) * mm, "end": v(206.4, -98.05) * mm});
            skLineSegment(sketch, "E2250", {"start": v(206.4, -98.05) * mm, "end": v(206.31, -98.22) * mm});
            skLineSegment(sketch, "E2251", {"start": v(206.31, -98.22) * mm, "end": v(206.21, -98.38) * mm});
            skLineSegment(sketch, "E2252", {"start": v(206.21, -98.38) * mm, "end": v(206.1, -98.53) * mm});
            skLineSegment(sketch, "E2253", {"start": v(206.1, -98.53) * mm, "end": v(205.96, -98.66) * mm});
            skLineSegment(sketch, "E2254", {"start": v(205.96, -98.66) * mm, "end": v(205.8, -98.77) * mm});
            skLineSegment(sketch, "E2255", {"start": v(205.8, -98.77) * mm, "end": v(205.64, -98.86) * mm});
            skLineSegment(sketch, "E2256", {"start": v(205.64, -98.86) * mm, "end": v(205.46, -98.93) * mm});
            skLineSegment(sketch, "E2257", {"start": v(205.46, -98.93) * mm, "end": v(205.28, -98.97) * mm});
            skLineSegment(sketch, "E2258", {"start": v(205.28, -98.97) * mm, "end": v(205.1, -99) * mm});
            skLineSegment(sketch, "E2259", {"start": v(205.1, -99) * mm, "end": v(204.9, -99) * mm});
            skLineSegment(sketch, "E2260", {"start": v(205.22, 197.18) * mm, "end": v(203.76, 197.53) * mm});
            skLineSegment(sketch, "E2261", {"start": v(203.76, 197.53) * mm, "end": v(202.35, 198.06) * mm});
            skLineSegment(sketch, "E2262", {"start": v(202.35, 198.06) * mm, "end": v(201.02, 198.77) * mm});
            skLineSegment(sketch, "E2263", {"start": v(201.02, 198.77) * mm, "end": v(199.79, 199.64) * mm});
            skLineSegment(sketch, "E2264", {"start": v(199.79, 199.64) * mm, "end": v(199.65, 199.77) * mm});
            skLineSegment(sketch, "E2265", {"start": v(199.65, 199.77) * mm, "end": v(199.32, 200) * mm});
            skLineSegment(sketch, "E2266", {"start": v(199.32, 200) * mm, "end": v(199.19, 200.13) * mm});
            skLineSegment(sketch, "E2267", {"start": v(199.19, 200.13) * mm, "end": v(198.86, 200.38) * mm});
            skLineSegment(sketch, "E2268", {"start": v(198.86, 200.38) * mm, "end": v(198.73, 200.5) * mm});
            skLineSegment(sketch, "E2269", {"start": v(198.73, 200.5) * mm, "end": v(198.41, 200.76) * mm});
            skLineSegment(sketch, "E2270", {"start": v(198.41, 200.76) * mm, "end": v(198.28, 200.9) * mm});
            skLineSegment(sketch, "E2271", {"start": v(198.28, 200.9) * mm, "end": v(197.97, 201.15) * mm});
            skLineSegment(sketch, "E2272", {"start": v(197.97, 201.15) * mm, "end": v(197.84, 201.29) * mm});
            skLineSegment(sketch, "E2273", {"start": v(197.84, 201.29) * mm, "end": v(197.53, 201.55) * mm});
            skLineSegment(sketch, "E2274", {"start": v(197.53, 201.55) * mm, "end": v(197.4, 201.69) * mm});
            skLineSegment(sketch, "E2275", {"start": v(197.4, 201.69) * mm, "end": v(197.1, 201.95) * mm});
            skLineSegment(sketch, "E2276", {"start": v(197.1, 201.95) * mm, "end": v(196.97, 202.1) * mm});
            skLineSegment(sketch, "E2277", {"start": v(196.97, 202.1) * mm, "end": v(196.67, 202.37) * mm});
            skLineSegment(sketch, "E2278", {"start": v(196.67, 202.37) * mm, "end": v(196.55, 202.5) * mm});
            skLineSegment(sketch, "E2279", {"start": v(196.55, 202.5) * mm, "end": v(196.25, 202.78) * mm});
            skLineSegment(sketch, "E2280", {"start": v(196.25, 202.78) * mm, "end": v(195.3, 203.95) * mm});
            skLineSegment(sketch, "E2281", {"start": v(195.3, 203.95) * mm, "end": v(194.48, 205.22) * mm});
            skLineSegment(sketch, "E2282", {"start": v(194.48, 205.22) * mm, "end": v(193.84, 206.58) * mm});
            skLineSegment(sketch, "E2283", {"start": v(193.84, 206.58) * mm, "end": v(193.38, 208.02) * mm});
            skLineSegment(sketch, "E2284", {"start": v(193.38, 208.02) * mm, "end": v(193.1, 209.5) * mm});
            skLineSegment(sketch, "E2285", {"start": v(193.1, 209.5) * mm, "end": v(193, 211) * mm});
            skLineSegment(sketch, "E2286", {"start": v(193, 211) * mm, "end": v(193.1, 212.5) * mm});
            skLineSegment(sketch, "E2287", {"start": v(193.1, 212.5) * mm, "end": v(193.38, 213.98) * mm});
            skLineSegment(sketch, "E2288", {"start": v(193.38, 213.98) * mm, "end": v(193.84, 215.42) * mm});
            skLineSegment(sketch, "E2289", {"start": v(193.84, 215.42) * mm, "end": v(194.48, 216.78) * mm});
            skLineSegment(sketch, "E2290", {"start": v(194.48, 216.78) * mm, "end": v(195.3, 218.05) * mm});
            skLineSegment(sketch, "E2291", {"start": v(195.3, 218.05) * mm, "end": v(196.25, 219.22) * mm});
            skLineSegment(sketch, "E2292", {"start": v(196.25, 219.22) * mm, "end": v(197.35, 220.25) * mm});
            skLineSegment(sketch, "E2293", {"start": v(197.35, 220.25) * mm, "end": v(198.57, 221.13) * mm});
            skLineSegment(sketch, "E2294", {"start": v(198.57, 221.13) * mm, "end": v(199.9, 221.86) * mm});
            skLineSegment(sketch, "E2295", {"start": v(199.9, 221.86) * mm, "end": v(201.3, 222.41) * mm});
            skLineSegment(sketch, "E2296", {"start": v(201.3, 222.41) * mm, "end": v(202.75, 222.79) * mm});
            skLineSegment(sketch, "E2297", {"start": v(202.75, 222.79) * mm, "end": v(204.25, 222.98) * mm});
            skLineSegment(sketch, "E2298", {"start": v(204.25, 222.98) * mm, "end": v(205.75, 222.98) * mm});
            skLineSegment(sketch, "E2299", {"start": v(205.75, 222.98) * mm, "end": v(207.25, 222.79) * mm});
            skLineSegment(sketch, "E2300", {"start": v(207.25, 222.79) * mm, "end": v(208.7, 222.41) * mm});
            skLineSegment(sketch, "E2301", {"start": v(208.7, 222.41) * mm, "end": v(210.1, 221.86) * mm});
            skLineSegment(sketch, "E2302", {"start": v(210.1, 221.86) * mm, "end": v(211.43, 221.13) * mm});
            skLineSegment(sketch, "E2303", {"start": v(211.43, 221.13) * mm, "end": v(212.65, 220.25) * mm});
            skLineSegment(sketch, "E2304", {"start": v(212.65, 220.25) * mm, "end": v(213.75, 219.22) * mm});
            skLineSegment(sketch, "E2305", {"start": v(213.75, 219.22) * mm, "end": v(213.88, 219.1) * mm});
            skLineSegment(sketch, "E2306", {"start": v(213.88, 219.1) * mm, "end": v(214, 218.98) * mm});
            skLineSegment(sketch, "E2307", {"start": v(214, 218.98) * mm, "end": v(214.14, 218.87) * mm});
            skLineSegment(sketch, "E2308", {"start": v(214.14, 218.87) * mm, "end": v(214.27, 218.76) * mm});
            skLineSegment(sketch, "E2309", {"start": v(214.27, 218.76) * mm, "end": v(214.4, 218.65) * mm});
            skLineSegment(sketch, "E2310", {"start": v(214.4, 218.65) * mm, "end": v(214.55, 218.55) * mm});
            skLineSegment(sketch, "E2311", {"start": v(214.55, 218.55) * mm, "end": v(214.69, 218.45) * mm});
            skLineSegment(sketch, "E2312", {"start": v(214.69, 218.45) * mm, "end": v(214.83, 218.35) * mm});
            skLineSegment(sketch, "E2313", {"start": v(214.83, 218.35) * mm, "end": v(215.94, 217.33) * mm});
            skLineSegment(sketch, "E2314", {"start": v(215.94, 217.33) * mm, "end": v(216.92, 216.18) * mm});
            skLineSegment(sketch, "E2315", {"start": v(216.92, 216.18) * mm, "end": v(217.74, 214.92) * mm});
            skLineSegment(sketch, "E2316", {"start": v(217.74, 214.92) * mm, "end": v(218.4, 213.57) * mm});
            skLineSegment(sketch, "E2317", {"start": v(218.4, 213.57) * mm, "end": v(218.89, 212.14) * mm});
            skLineSegment(sketch, "E2318", {"start": v(218.89, 212.14) * mm, "end": v(219.2, 210.66) * mm});
            skLineSegment(sketch, "E2319", {"start": v(219.2, 210.66) * mm, "end": v(219.3, 209.16) * mm});
            skLineSegment(sketch, "E2320", {"start": v(219.3, 209.16) * mm, "end": v(219.23, 207.66) * mm});
            skLineSegment(sketch, "E2321", {"start": v(219.23, 207.66) * mm, "end": v(218.97, 206.17) * mm});
            skLineSegment(sketch, "E2322", {"start": v(218.97, 206.17) * mm, "end": v(218.53, 204.73) * mm});
            skLineSegment(sketch, "E2323", {"start": v(218.53, 204.73) * mm, "end": v(217.9, 203.36) * mm});
            skLineSegment(sketch, "E2324", {"start": v(217.9, 203.36) * mm, "end": v(217.11, 202.08) * mm});
            skLineSegment(sketch, "E2325", {"start": v(217.11, 202.08) * mm, "end": v(216.17, 200.9) * mm});
            skLineSegment(sketch, "E2326", {"start": v(216.17, 200.9) * mm, "end": v(215.09, 199.86) * mm});
            skLineSegment(sketch, "E2327", {"start": v(215.09, 199.86) * mm, "end": v(213.88, 198.95) * mm});
            skLineSegment(sketch, "E2328", {"start": v(213.88, 198.95) * mm, "end": v(212.57, 198.2) * mm});
            skLineSegment(sketch, "E2329", {"start": v(212.57, 198.2) * mm, "end": v(211.18, 197.63) * mm});
            skLineSegment(sketch, "E2330", {"start": v(211.18, 197.63) * mm, "end": v(209.72, 197.24) * mm});
            skLineSegment(sketch, "E2331", {"start": v(209.72, 197.24) * mm, "end": v(208.23, 197.03) * mm});
            skLineSegment(sketch, "E2332", {"start": v(208.23, 197.03) * mm, "end": v(206.72, 197) * mm});
            skLineSegment(sketch, "E2333", {"start": v(206.72, 197) * mm, "end": v(205.22, 197.18) * mm});
            skLineSegment(sketch, "E2334", {"start": v(39.87, 218) * mm, "end": v(39.63, 218.03) * mm});
            skLineSegment(sketch, "E2335", {"start": v(39.63, 218.03) * mm, "end": v(39.38, 218.1) * mm});
            skLineSegment(sketch, "E2336", {"start": v(39.38, 218.1) * mm, "end": v(39.15, 218.2) * mm});
            skLineSegment(sketch, "E2337", {"start": v(39.15, 218.2) * mm, "end": v(38.93, 218.31) * mm});
            skLineSegment(sketch, "E2338", {"start": v(38.93, 218.31) * mm, "end": v(38.73, 218.46) * mm});
            skLineSegment(sketch, "E2339", {"start": v(38.73, 218.46) * mm, "end": v(38.54, 218.63) * mm});
            skLineSegment(sketch, "E2340", {"start": v(38.54, 218.63) * mm, "end": v(38.38, 218.82) * mm});
            skLineSegment(sketch, "E2341", {"start": v(38.38, 218.82) * mm, "end": v(38.25, 219.04) * mm});
            skLineSegment(sketch, "E2342", {"start": v(38.25, 219.04) * mm, "end": v(38.14, 219.26) * mm});
            skLineSegment(sketch, "E2343", {"start": v(38.14, 219.26) * mm, "end": v(38.06, 219.5) * mm});
            skLineSegment(sketch, "E2344", {"start": v(38.06, 219.5) * mm, "end": v(38.02, 219.75) * mm});
            skLineSegment(sketch, "E2345", {"start": v(38.02, 219.75) * mm, "end": v(38, 220) * mm});
            skLineSegment(sketch, "E2346", {"start": v(38, 220) * mm, "end": v(38.02, 220.25) * mm});
            skLineSegment(sketch, "E2347", {"start": v(38.02, 220.25) * mm, "end": v(38.06, 220.5) * mm});
            skLineSegment(sketch, "E2348", {"start": v(38.06, 220.5) * mm, "end": v(38.14, 220.74) * mm});
            skLineSegment(sketch, "E2349", {"start": v(38.14, 220.74) * mm, "end": v(38.25, 220.96) * mm});
            skLineSegment(sketch, "E2350", {"start": v(38.25, 220.96) * mm, "end": v(38.38, 221.18) * mm});
            skLineSegment(sketch, "E2351", {"start": v(38.38, 221.18) * mm, "end": v(38.54, 221.37) * mm});
            skLineSegment(sketch, "E2352", {"start": v(38.54, 221.37) * mm, "end": v(38.73, 221.54) * mm});
            skLineSegment(sketch, "E2353", {"start": v(38.73, 221.54) * mm, "end": v(38.93, 221.69) * mm});
            skLineSegment(sketch, "E2354", {"start": v(38.93, 221.69) * mm, "end": v(39.15, 221.8) * mm});
            skLineSegment(sketch, "E2355", {"start": v(39.15, 221.8) * mm, "end": v(39.38, 221.9) * mm});
            skLineSegment(sketch, "E2356", {"start": v(39.38, 221.9) * mm, "end": v(39.63, 221.97) * mm});
            skLineSegment(sketch, "E2357", {"start": v(39.63, 221.97) * mm, "end": v(39.87, 222) * mm});
            skLineSegment(sketch, "E2358", {"start": v(39.87, 222) * mm, "end": v(40.13, 222) * mm});
            skLineSegment(sketch, "E2359", {"start": v(40.13, 222) * mm, "end": v(40.37, 221.97) * mm});
            skLineSegment(sketch, "E2360", {"start": v(40.37, 221.97) * mm, "end": v(40.62, 221.9) * mm});
            skLineSegment(sketch, "E2361", {"start": v(40.62, 221.9) * mm, "end": v(40.85, 221.8) * mm});
            skLineSegment(sketch, "E2362", {"start": v(40.85, 221.8) * mm, "end": v(41.07, 221.69) * mm});
            skLineSegment(sketch, "E2363", {"start": v(41.07, 221.69) * mm, "end": v(41.27, 221.54) * mm});
            skLineSegment(sketch, "E2364", {"start": v(41.27, 221.54) * mm, "end": v(41.46, 221.37) * mm});
            skLineSegment(sketch, "E2365", {"start": v(41.46, 221.37) * mm, "end": v(41.62, 221.18) * mm});
            skLineSegment(sketch, "E2366", {"start": v(41.62, 221.18) * mm, "end": v(41.75, 220.96) * mm});
            skLineSegment(sketch, "E2367", {"start": v(41.75, 220.96) * mm, "end": v(41.86, 220.74) * mm});
            skLineSegment(sketch, "E2368", {"start": v(41.86, 220.74) * mm, "end": v(41.94, 220.5) * mm});
            skLineSegment(sketch, "E2369", {"start": v(41.94, 220.5) * mm, "end": v(41.98, 220.25) * mm});
            skLineSegment(sketch, "E2370", {"start": v(41.98, 220.25) * mm, "end": v(42, 220) * mm});
            skLineSegment(sketch, "E2371", {"start": v(42, 220) * mm, "end": v(41.98, 219.75) * mm});
            skLineSegment(sketch, "E2372", {"start": v(41.98, 219.75) * mm, "end": v(41.94, 219.5) * mm});
            skLineSegment(sketch, "E2373", {"start": v(41.94, 219.5) * mm, "end": v(41.86, 219.26) * mm});
            skLineSegment(sketch, "E2374", {"start": v(41.86, 219.26) * mm, "end": v(41.75, 219.04) * mm});
            skLineSegment(sketch, "E2375", {"start": v(41.75, 219.04) * mm, "end": v(41.62, 218.82) * mm});
            skLineSegment(sketch, "E2376", {"start": v(41.62, 218.82) * mm, "end": v(41.46, 218.63) * mm});
            skLineSegment(sketch, "E2377", {"start": v(41.46, 218.63) * mm, "end": v(41.27, 218.46) * mm});
            skLineSegment(sketch, "E2378", {"start": v(41.27, 218.46) * mm, "end": v(41.07, 218.31) * mm});
            skLineSegment(sketch, "E2379", {"start": v(41.07, 218.31) * mm, "end": v(40.85, 218.2) * mm});
            skLineSegment(sketch, "E2380", {"start": v(40.85, 218.2) * mm, "end": v(40.62, 218.1) * mm});
            skLineSegment(sketch, "E2381", {"start": v(40.62, 218.1) * mm, "end": v(40.37, 218.03) * mm});
            skLineSegment(sketch, "E2382", {"start": v(40.37, 218.03) * mm, "end": v(40.13, 218) * mm});
            skLineSegment(sketch, "E2383", {"start": v(40.13, 218) * mm, "end": v(39.87, 218) * mm});
            skLineSegment(sketch, "E2384", {"start": v(369.87, 218) * mm, "end": v(369.62, 218.03) * mm});
            skLineSegment(sketch, "E2385", {"start": v(369.62, 218.03) * mm, "end": v(369.38, 218.1) * mm});
            skLineSegment(sketch, "E2386", {"start": v(369.38, 218.1) * mm, "end": v(369.15, 218.2) * mm});
            skLineSegment(sketch, "E2387", {"start": v(369.15, 218.2) * mm, "end": v(368.93, 218.31) * mm});
            skLineSegment(sketch, "E2388", {"start": v(368.93, 218.31) * mm, "end": v(368.73, 218.46) * mm});
            skLineSegment(sketch, "E2389", {"start": v(368.73, 218.46) * mm, "end": v(368.54, 218.63) * mm});
            skLineSegment(sketch, "E2390", {"start": v(368.54, 218.63) * mm, "end": v(368.38, 218.82) * mm});
            skLineSegment(sketch, "E2391", {"start": v(368.38, 218.82) * mm, "end": v(368.25, 219.04) * mm});
            skLineSegment(sketch, "E2392", {"start": v(368.25, 219.04) * mm, "end": v(368.14, 219.26) * mm});
            skLineSegment(sketch, "E2393", {"start": v(368.14, 219.26) * mm, "end": v(368.06, 219.5) * mm});
            skLineSegment(sketch, "E2394", {"start": v(368.06, 219.5) * mm, "end": v(368.02, 219.75) * mm});
            skLineSegment(sketch, "E2395", {"start": v(368.02, 219.75) * mm, "end": v(368, 220) * mm});
            skLineSegment(sketch, "E2396", {"start": v(368, 220) * mm, "end": v(368.02, 220.25) * mm});
            skLineSegment(sketch, "E2397", {"start": v(368.02, 220.25) * mm, "end": v(368.06, 220.5) * mm});
            skLineSegment(sketch, "E2398", {"start": v(368.06, 220.5) * mm, "end": v(368.14, 220.74) * mm});
            skLineSegment(sketch, "E2399", {"start": v(368.14, 220.74) * mm, "end": v(368.25, 220.96) * mm});
            skLineSegment(sketch, "E2400", {"start": v(368.25, 220.96) * mm, "end": v(368.38, 221.18) * mm});
            skLineSegment(sketch, "E2401", {"start": v(368.38, 221.18) * mm, "end": v(368.54, 221.37) * mm});
            skLineSegment(sketch, "E2402", {"start": v(368.54, 221.37) * mm, "end": v(368.73, 221.54) * mm});
            skLineSegment(sketch, "E2403", {"start": v(368.73, 221.54) * mm, "end": v(368.93, 221.69) * mm});
            skLineSegment(sketch, "E2404", {"start": v(368.93, 221.69) * mm, "end": v(369.15, 221.8) * mm});
            skLineSegment(sketch, "E2405", {"start": v(369.15, 221.8) * mm, "end": v(369.38, 221.9) * mm});
            skLineSegment(sketch, "E2406", {"start": v(369.38, 221.9) * mm, "end": v(369.62, 221.97) * mm});
            skLineSegment(sketch, "E2407", {"start": v(369.62, 221.97) * mm, "end": v(369.87, 222) * mm});
            skLineSegment(sketch, "E2408", {"start": v(369.87, 222) * mm, "end": v(370.13, 222) * mm});
            skLineSegment(sketch, "E2409", {"start": v(370.13, 222) * mm, "end": v(370.38, 221.97) * mm});
            skLineSegment(sketch, "E2410", {"start": v(370.38, 221.97) * mm, "end": v(370.62, 221.9) * mm});
            skLineSegment(sketch, "E2411", {"start": v(370.62, 221.9) * mm, "end": v(370.85, 221.8) * mm});
            skLineSegment(sketch, "E2412", {"start": v(370.85, 221.8) * mm, "end": v(371.07, 221.69) * mm});
            skLineSegment(sketch, "E2413", {"start": v(371.07, 221.69) * mm, "end": v(371.27, 221.54) * mm});
            skLineSegment(sketch, "E2414", {"start": v(371.27, 221.54) * mm, "end": v(371.46, 221.37) * mm});
            skLineSegment(sketch, "E2415", {"start": v(371.46, 221.37) * mm, "end": v(371.62, 221.18) * mm});
            skLineSegment(sketch, "E2416", {"start": v(371.62, 221.18) * mm, "end": v(371.75, 220.96) * mm});
            skLineSegment(sketch, "E2417", {"start": v(371.75, 220.96) * mm, "end": v(371.86, 220.74) * mm});
            skLineSegment(sketch, "E2418", {"start": v(371.86, 220.74) * mm, "end": v(371.94, 220.5) * mm});
            skLineSegment(sketch, "E2419", {"start": v(371.94, 220.5) * mm, "end": v(371.98, 220.25) * mm});
            skLineSegment(sketch, "E2420", {"start": v(371.98, 220.25) * mm, "end": v(372, 220) * mm});
            skLineSegment(sketch, "E2421", {"start": v(372, 220) * mm, "end": v(371.98, 219.75) * mm});
            skLineSegment(sketch, "E2422", {"start": v(371.98, 219.75) * mm, "end": v(371.94, 219.5) * mm});
            skLineSegment(sketch, "E2423", {"start": v(371.94, 219.5) * mm, "end": v(371.86, 219.26) * mm});
            skLineSegment(sketch, "E2424", {"start": v(371.86, 219.26) * mm, "end": v(371.75, 219.04) * mm});
            skLineSegment(sketch, "E2425", {"start": v(371.75, 219.04) * mm, "end": v(371.62, 218.82) * mm});
            skLineSegment(sketch, "E2426", {"start": v(371.62, 218.82) * mm, "end": v(371.46, 218.63) * mm});
            skLineSegment(sketch, "E2427", {"start": v(371.46, 218.63) * mm, "end": v(371.27, 218.46) * mm});
            skLineSegment(sketch, "E2428", {"start": v(371.27, 218.46) * mm, "end": v(371.07, 218.31) * mm});
            skLineSegment(sketch, "E2429", {"start": v(371.07, 218.31) * mm, "end": v(370.85, 218.2) * mm});
            skLineSegment(sketch, "E2430", {"start": v(370.85, 218.2) * mm, "end": v(370.62, 218.1) * mm});
            skLineSegment(sketch, "E2431", {"start": v(370.62, 218.1) * mm, "end": v(370.38, 218.03) * mm});
            skLineSegment(sketch, "E2432", {"start": v(370.38, 218.03) * mm, "end": v(370.13, 218) * mm});
            skLineSegment(sketch, "E2433", {"start": v(370.13, 218) * mm, "end": v(369.87, 218) * mm});
            skLineSegment(sketch, "E2434", {"start": v(362, 180) * mm, "end": v(362, 200) * mm});
            skLineSegment(sketch, "E2435", {"start": v(362, 200) * mm, "end": v(378, 200) * mm});
            skLineSegment(sketch, "E2436", {"start": v(378, 200) * mm, "end": v(378, 180) * mm});
            skLineSegment(sketch, "E2437", {"start": v(378, 180) * mm, "end": v(362, 180) * mm});
            skLineSegment(sketch, "E2438", {"start": v(32, 180) * mm, "end": v(32, 200) * mm});
            skLineSegment(sketch, "E2439", {"start": v(32, 200) * mm, "end": v(48, 200) * mm});
            skLineSegment(sketch, "E2440", {"start": v(48, 200) * mm, "end": v(48, 180) * mm});
            skLineSegment(sketch, "E2441", {"start": v(48, 180) * mm, "end": v(32, 180) * mm});
            skLineSegment(sketch, "E2442", {"start": v(220.4, 194) * mm, "end": v(220.22, 194.03) * mm});
            skLineSegment(sketch, "E2443", {"start": v(220.22, 194.03) * mm, "end": v(220.04, 194.07) * mm});
            skLineSegment(sketch, "E2444", {"start": v(220.04, 194.07) * mm, "end": v(219.86, 194.14) * mm});
            skLineSegment(sketch, "E2445", {"start": v(219.86, 194.14) * mm, "end": v(219.7, 194.23) * mm});
            skLineSegment(sketch, "E2446", {"start": v(219.7, 194.23) * mm, "end": v(219.54, 194.34) * mm});
            skLineSegment(sketch, "E2447", {"start": v(219.54, 194.34) * mm, "end": v(219.4, 194.47) * mm});
            skLineSegment(sketch, "E2448", {"start": v(219.4, 194.47) * mm, "end": v(219.29, 194.62) * mm});
            skLineSegment(sketch, "E2449", {"start": v(219.29, 194.62) * mm, "end": v(219.19, 194.78) * mm});
            skLineSegment(sketch, "E2450", {"start": v(219.19, 194.78) * mm, "end": v(219.1, 194.95) * mm});
            skLineSegment(sketch, "E2451", {"start": v(219.1, 194.95) * mm, "end": v(219.05, 195.13) * mm});
            skLineSegment(sketch, "E2452", {"start": v(219.05, 195.13) * mm, "end": v(219.01, 195.31) * mm});
            skLineSegment(sketch, "E2453", {"start": v(219.01, 195.31) * mm, "end": v(219, 195.5) * mm});
            skLineSegment(sketch, "E2454", {"start": v(219, 195.5) * mm, "end": v(219.01, 195.69) * mm});
            skLineSegment(sketch, "E2455", {"start": v(219.01, 195.69) * mm, "end": v(219.05, 195.87) * mm});
            skLineSegment(sketch, "E2456", {"start": v(219.05, 195.87) * mm, "end": v(219.1, 196.05) * mm});
            skLineSegment(sketch, "E2457", {"start": v(219.1, 196.05) * mm, "end": v(219.19, 196.22) * mm});
            skLineSegment(sketch, "E2458", {"start": v(219.19, 196.22) * mm, "end": v(219.29, 196.38) * mm});
            skLineSegment(sketch, "E2459", {"start": v(219.29, 196.38) * mm, "end": v(219.4, 196.53) * mm});
            skLineSegment(sketch, "E2460", {"start": v(219.4, 196.53) * mm, "end": v(219.54, 196.66) * mm});
            skLineSegment(sketch, "E2461", {"start": v(219.54, 196.66) * mm, "end": v(219.7, 196.77) * mm});
            skLineSegment(sketch, "E2462", {"start": v(219.7, 196.77) * mm, "end": v(219.86, 196.86) * mm});
            skLineSegment(sketch, "E2463", {"start": v(219.86, 196.86) * mm, "end": v(220.04, 196.93) * mm});
            skLineSegment(sketch, "E2464", {"start": v(220.04, 196.93) * mm, "end": v(220.22, 196.97) * mm});
            skLineSegment(sketch, "E2465", {"start": v(220.22, 196.97) * mm, "end": v(220.4, 197) * mm});
            skLineSegment(sketch, "E2466", {"start": v(220.4, 197) * mm, "end": v(220.6, 197) * mm});
            skLineSegment(sketch, "E2467", {"start": v(220.6, 197) * mm, "end": v(220.76, 196.98) * mm});
            skLineSegment(sketch, "E2468", {"start": v(220.76, 196.98) * mm, "end": v(220.92, 197) * mm});
            skLineSegment(sketch, "E2469", {"start": v(220.92, 197) * mm, "end": v(221.1, 197) * mm});
            skLineSegment(sketch, "E2470", {"start": v(221.1, 197) * mm, "end": v(221.27, 196.99) * mm});
            skLineSegment(sketch, "E2471", {"start": v(221.27, 196.99) * mm, "end": v(221.44, 197.01) * mm});
            skLineSegment(sketch, "E2472", {"start": v(221.44, 197.01) * mm, "end": v(221.62, 197.02) * mm});
            skLineSegment(sketch, "E2473", {"start": v(221.62, 197.02) * mm, "end": v(221.79, 197) * mm});
            skLineSegment(sketch, "E2474", {"start": v(221.79, 197) * mm, "end": v(221.95, 197.03) * mm});
            skLineSegment(sketch, "E2475", {"start": v(221.95, 197.03) * mm, "end": v(222.14, 197.04) * mm});
            skLineSegment(sketch, "E2476", {"start": v(222.14, 197.04) * mm, "end": v(222.3, 197.03) * mm});
            skLineSegment(sketch, "E2477", {"start": v(222.3, 197.03) * mm, "end": v(222.46, 197.06) * mm});
            skLineSegment(sketch, "E2478", {"start": v(222.46, 197.06) * mm, "end": v(222.65, 197.08) * mm});
            skLineSegment(sketch, "E2479", {"start": v(222.65, 197.08) * mm, "end": v(222.82, 197.07) * mm});
            skLineSegment(sketch, "E2480", {"start": v(222.82, 197.07) * mm, "end": v(222.98, 197.1) * mm});
            skLineSegment(sketch, "E2481", {"start": v(222.98, 197.1) * mm, "end": v(223.16, 197.12) * mm});
            skLineSegment(sketch, "E2482", {"start": v(223.16, 197.12) * mm, "end": v(223.33, 197.11) * mm});
            skLineSegment(sketch, "E2483", {"start": v(223.33, 197.11) * mm, "end": v(223.5, 197.15) * mm});
            skLineSegment(sketch, "E2484", {"start": v(223.5, 197.15) * mm, "end": v(223.68, 197.17) * mm});
            skLineSegment(sketch, "E2485", {"start": v(223.68, 197.17) * mm, "end": v(223.84, 197.17) * mm});
            skLineSegment(sketch, "E2486", {"start": v(223.84, 197.17) * mm, "end": v(224, 197.2) * mm});
            skLineSegment(sketch, "E2487", {"start": v(224, 197.2) * mm, "end": v(224.19, 197.23) * mm});
            skLineSegment(sketch, "E2488", {"start": v(224.19, 197.23) * mm, "end": v(224.35, 197.23) * mm});
            skLineSegment(sketch, "E2489", {"start": v(224.35, 197.23) * mm, "end": v(224.51, 197.27) * mm});
            skLineSegment(sketch, "E2490", {"start": v(224.51, 197.27) * mm, "end": v(224.7, 197.3) * mm});
            skLineSegment(sketch, "E2491", {"start": v(224.7, 197.3) * mm, "end": v(224.89, 197.3) * mm});
            skLineSegment(sketch, "E2492", {"start": v(224.89, 197.3) * mm, "end": v(225.07, 197.28) * mm});
            skLineSegment(sketch, "E2493", {"start": v(225.07, 197.28) * mm, "end": v(225.26, 197.24) * mm});
            skLineSegment(sketch, "E2494", {"start": v(225.26, 197.24) * mm, "end": v(225.43, 197.17) * mm});
            skLineSegment(sketch, "E2495", {"start": v(225.43, 197.17) * mm, "end": v(225.6, 197.08) * mm});
            skLineSegment(sketch, "E2496", {"start": v(225.6, 197.08) * mm, "end": v(225.75, 196.97) * mm});
            skLineSegment(sketch, "E2497", {"start": v(225.75, 196.97) * mm, "end": v(225.9, 196.84) * mm});
            skLineSegment(sketch, "E2498", {"start": v(225.9, 196.84) * mm, "end": v(226.01, 196.7) * mm});
            skLineSegment(sketch, "E2499", {"start": v(226.01, 196.7) * mm, "end": v(226.12, 196.54) * mm});
            skLineSegment(sketch, "E2500", {"start": v(226.12, 196.54) * mm, "end": v(226.2, 196.37) * mm});
            skLineSegment(sketch, "E2501", {"start": v(226.2, 196.37) * mm, "end": v(226.26, 196.2) * mm});
            skLineSegment(sketch, "E2502", {"start": v(226.26, 196.2) * mm, "end": v(226.3, 196) * mm});
            skLineSegment(sketch, "E2503", {"start": v(226.3, 196) * mm, "end": v(226.31, 195.82) * mm});
            skLineSegment(sketch, "E2504", {"start": v(226.31, 195.82) * mm, "end": v(226.3, 195.63) * mm});
            skLineSegment(sketch, "E2505", {"start": v(226.3, 195.63) * mm, "end": v(226.27, 195.45) * mm});
            skLineSegment(sketch, "E2506", {"start": v(226.27, 195.45) * mm, "end": v(226.22, 195.27) * mm});
            skLineSegment(sketch, "E2507", {"start": v(226.22, 195.27) * mm, "end": v(226.14, 195.1) * mm});
            skLineSegment(sketch, "E2508", {"start": v(226.14, 195.1) * mm, "end": v(226.04, 194.94) * mm});
            skLineSegment(sketch, "E2509", {"start": v(226.04, 194.94) * mm, "end": v(225.92, 194.79) * mm});
            skLineSegment(sketch, "E2510", {"start": v(225.92, 194.79) * mm, "end": v(225.79, 194.66) * mm});
            skLineSegment(sketch, "E2511", {"start": v(225.79, 194.66) * mm, "end": v(225.64, 194.55) * mm});
            skLineSegment(sketch, "E2512", {"start": v(225.64, 194.55) * mm, "end": v(225.47, 194.45) * mm});
            skLineSegment(sketch, "E2513", {"start": v(225.47, 194.45) * mm, "end": v(225.3, 194.38) * mm});
            skLineSegment(sketch, "E2514", {"start": v(225.3, 194.38) * mm, "end": v(225.12, 194.33) * mm});
            skLineSegment(sketch, "E2515", {"start": v(225.12, 194.33) * mm, "end": v(224.93, 194.3) * mm});
            skLineSegment(sketch, "E2516", {"start": v(224.93, 194.3) * mm, "end": v(224.74, 194.3) * mm});
            skLineSegment(sketch, "E2517", {"start": v(224.74, 194.3) * mm, "end": v(224.55, 194.26) * mm});
            skLineSegment(sketch, "E2518", {"start": v(224.55, 194.26) * mm, "end": v(224.37, 194.23) * mm});
            skLineSegment(sketch, "E2519", {"start": v(224.37, 194.23) * mm, "end": v(224.18, 194.23) * mm});
            skLineSegment(sketch, "E2520", {"start": v(224.18, 194.23) * mm, "end": v(224, 194.2) * mm});
            skLineSegment(sketch, "E2521", {"start": v(224, 194.2) * mm, "end": v(223.8, 194.17) * mm});
            skLineSegment(sketch, "E2522", {"start": v(223.8, 194.17) * mm, "end": v(223.62, 194.18) * mm});
            skLineSegment(sketch, "E2523", {"start": v(223.62, 194.18) * mm, "end": v(223.43, 194.13) * mm});
            skLineSegment(sketch, "E2524", {"start": v(223.43, 194.13) * mm, "end": v(223.24, 194.12) * mm});
            skLineSegment(sketch, "E2525", {"start": v(223.24, 194.12) * mm, "end": v(223.05, 194.13) * mm});
            skLineSegment(sketch, "E2526", {"start": v(223.05, 194.13) * mm, "end": v(222.86, 194.09) * mm});
            skLineSegment(sketch, "E2527", {"start": v(222.86, 194.09) * mm, "end": v(222.67, 194.08) * mm});
            skLineSegment(sketch, "E2528", {"start": v(222.67, 194.08) * mm, "end": v(222.49, 194.09) * mm});
            skLineSegment(sketch, "E2529", {"start": v(222.49, 194.09) * mm, "end": v(222.3, 194.05) * mm});
            skLineSegment(sketch, "E2530", {"start": v(222.3, 194.05) * mm, "end": v(222.1, 194.04) * mm});
            skLineSegment(sketch, "E2531", {"start": v(222.1, 194.04) * mm, "end": v(221.92, 194.06) * mm});
            skLineSegment(sketch, "E2532", {"start": v(221.92, 194.06) * mm, "end": v(221.73, 194.03) * mm});
            skLineSegment(sketch, "E2533", {"start": v(221.73, 194.03) * mm, "end": v(221.54, 194.02) * mm});
            skLineSegment(sketch, "E2534", {"start": v(221.54, 194.02) * mm, "end": v(221.35, 194.04) * mm});
            skLineSegment(sketch, "E2535", {"start": v(221.35, 194.04) * mm, "end": v(221.16, 194) * mm});
            skLineSegment(sketch, "E2536", {"start": v(221.16, 194) * mm, "end": v(220.97, 194) * mm});
            skLineSegment(sketch, "E2537", {"start": v(220.97, 194) * mm, "end": v(220.79, 194.03) * mm});
            skLineSegment(sketch, "E2538", {"start": v(220.79, 194.03) * mm, "end": v(220.6, 194) * mm});
            skLineSegment(sketch, "E2539", {"start": v(220.6, 194) * mm, "end": v(220.4, 194) * mm});
            skLineSegment(sketch, "E2540", {"start": v(193.86, 190) * mm, "end": v(193.67, 190.05) * mm});
            skLineSegment(sketch, "E2541", {"start": v(193.67, 190.05) * mm, "end": v(193.5, 190.12) * mm});
            skLineSegment(sketch, "E2542", {"start": v(193.5, 190.12) * mm, "end": v(193.33, 190.21) * mm});
            skLineSegment(sketch, "E2543", {"start": v(193.33, 190.21) * mm, "end": v(193.18, 190.32) * mm});
            skLineSegment(sketch, "E2544", {"start": v(193.18, 190.32) * mm, "end": v(193.04, 190.44) * mm});
            skLineSegment(sketch, "E2545", {"start": v(193.04, 190.44) * mm, "end": v(192.93, 190.57) * mm});
            skLineSegment(sketch, "E2546", {"start": v(192.93, 190.57) * mm, "end": v(192.87, 190.6) * mm});
            skLineSegment(sketch, "E2547", {"start": v(192.87, 190.6) * mm, "end": v(192.7, 190.69) * mm});
            skLineSegment(sketch, "E2548", {"start": v(192.7, 190.69) * mm, "end": v(192.55, 190.8) * mm});
            skLineSegment(sketch, "E2549", {"start": v(192.55, 190.8) * mm, "end": v(192.41, 190.93) * mm});
            skLineSegment(sketch, "E2550", {"start": v(192.41, 190.93) * mm, "end": v(192.3, 191.06) * mm});
            skLineSegment(sketch, "E2551", {"start": v(192.3, 191.06) * mm, "end": v(192.24, 191.09) * mm});
            skLineSegment(sketch, "E2552", {"start": v(192.24, 191.09) * mm, "end": v(192.08, 191.18) * mm});
            skLineSegment(sketch, "E2553", {"start": v(192.08, 191.18) * mm, "end": v(191.93, 191.3) * mm});
            skLineSegment(sketch, "E2554", {"start": v(191.93, 191.3) * mm, "end": v(191.8, 191.43) * mm});
            skLineSegment(sketch, "E2555", {"start": v(191.8, 191.43) * mm, "end": v(191.7, 191.56) * mm});
            skLineSegment(sketch, "E2556", {"start": v(191.7, 191.56) * mm, "end": v(191.63, 191.58) * mm});
            skLineSegment(sketch, "E2557", {"start": v(191.63, 191.58) * mm, "end": v(191.47, 191.68) * mm});
            skLineSegment(sketch, "E2558", {"start": v(191.47, 191.68) * mm, "end": v(191.32, 191.8) * mm});
            skLineSegment(sketch, "E2559", {"start": v(191.32, 191.8) * mm, "end": v(191.19, 191.93) * mm});
            skLineSegment(sketch, "E2560", {"start": v(191.19, 191.93) * mm, "end": v(191.09, 192.07) * mm});
            skLineSegment(sketch, "E2561", {"start": v(191.09, 192.07) * mm, "end": v(191.03, 192.1) * mm});
            skLineSegment(sketch, "E2562", {"start": v(191.03, 192.1) * mm, "end": v(190.87, 192.2) * mm});
            skLineSegment(sketch, "E2563", {"start": v(190.87, 192.2) * mm, "end": v(190.72, 192.31) * mm});
            skLineSegment(sketch, "E2564", {"start": v(190.72, 192.31) * mm, "end": v(190.59, 192.45) * mm});
            skLineSegment(sketch, "E2565", {"start": v(190.59, 192.45) * mm, "end": v(190.49, 192.58) * mm});
            skLineSegment(sketch, "E2566", {"start": v(190.49, 192.58) * mm, "end": v(190.43, 192.61) * mm});
            skLineSegment(sketch, "E2567", {"start": v(190.43, 192.61) * mm, "end": v(190.27, 192.72) * mm});
            skLineSegment(sketch, "E2568", {"start": v(190.27, 192.72) * mm, "end": v(190.13, 192.84) * mm});
            skLineSegment(sketch, "E2569", {"start": v(190.13, 192.84) * mm, "end": v(190, 192.98) * mm});
            skLineSegment(sketch, "E2570", {"start": v(190, 192.98) * mm, "end": v(189.9, 193.11) * mm});
            skLineSegment(sketch, "E2571", {"start": v(189.9, 193.11) * mm, "end": v(189.84, 193.14) * mm});
            skLineSegment(sketch, "E2572", {"start": v(189.84, 193.14) * mm, "end": v(189.69, 193.25) * mm});
            skLineSegment(sketch, "E2573", {"start": v(189.69, 193.25) * mm, "end": v(189.54, 193.37) * mm});
            skLineSegment(sketch, "E2574", {"start": v(189.54, 193.37) * mm, "end": v(189.42, 193.51) * mm});
            skLineSegment(sketch, "E2575", {"start": v(189.42, 193.51) * mm, "end": v(189.32, 193.65) * mm});
            skLineSegment(sketch, "E2576", {"start": v(189.32, 193.65) * mm, "end": v(189.26, 193.68) * mm});
            skLineSegment(sketch, "E2577", {"start": v(189.26, 193.68) * mm, "end": v(189.11, 193.8) * mm});
            skLineSegment(sketch, "E2578", {"start": v(189.11, 193.8) * mm, "end": v(188.97, 193.92) * mm});
            skLineSegment(sketch, "E2579", {"start": v(188.97, 193.92) * mm, "end": v(188.85, 194.06) * mm});
            skLineSegment(sketch, "E2580", {"start": v(188.85, 194.06) * mm, "end": v(188.76, 194.2) * mm});
            skLineSegment(sketch, "E2581", {"start": v(188.76, 194.2) * mm, "end": v(188.7, 194.23) * mm});
            skLineSegment(sketch, "E2582", {"start": v(188.7, 194.23) * mm, "end": v(188.54, 194.34) * mm});
            skLineSegment(sketch, "E2583", {"start": v(188.54, 194.34) * mm, "end": v(188.4, 194.47) * mm});
            skLineSegment(sketch, "E2584", {"start": v(188.4, 194.47) * mm, "end": v(188.29, 194.62) * mm});
            skLineSegment(sketch, "E2585", {"start": v(188.29, 194.62) * mm, "end": v(188.19, 194.78) * mm});
            skLineSegment(sketch, "E2586", {"start": v(188.19, 194.78) * mm, "end": v(188.1, 194.95) * mm});
            skLineSegment(sketch, "E2587", {"start": v(188.1, 194.95) * mm, "end": v(188.05, 195.13) * mm});
            skLineSegment(sketch, "E2588", {"start": v(188.05, 195.13) * mm, "end": v(188.01, 195.31) * mm});
            skLineSegment(sketch, "E2589", {"start": v(188.01, 195.31) * mm, "end": v(188, 195.5) * mm});
            skLineSegment(sketch, "E2590", {"start": v(188, 195.5) * mm, "end": v(188.01, 195.69) * mm});
            skLineSegment(sketch, "E2591", {"start": v(188.01, 195.69) * mm, "end": v(188.05, 195.87) * mm});
            skLineSegment(sketch, "E2592", {"start": v(188.05, 195.87) * mm, "end": v(188.1, 196.05) * mm});
            skLineSegment(sketch, "E2593", {"start": v(188.1, 196.05) * mm, "end": v(188.19, 196.22) * mm});
            skLineSegment(sketch, "E2594", {"start": v(188.19, 196.22) * mm, "end": v(188.29, 196.38) * mm});
            skLineSegment(sketch, "E2595", {"start": v(188.29, 196.38) * mm, "end": v(188.4, 196.53) * mm});
            skLineSegment(sketch, "E2596", {"start": v(188.4, 196.53) * mm, "end": v(188.54, 196.66) * mm});
            skLineSegment(sketch, "E2597", {"start": v(188.54, 196.66) * mm, "end": v(188.7, 196.77) * mm});
            skLineSegment(sketch, "E2598", {"start": v(188.7, 196.77) * mm, "end": v(188.86, 196.86) * mm});
            skLineSegment(sketch, "E2599", {"start": v(188.86, 196.86) * mm, "end": v(189.04, 196.93) * mm});
            skLineSegment(sketch, "E2600", {"start": v(189.04, 196.93) * mm, "end": v(189.22, 196.97) * mm});
            skLineSegment(sketch, "E2601", {"start": v(189.22, 196.97) * mm, "end": v(189.4, 197) * mm});
            skLineSegment(sketch, "E2602", {"start": v(189.4, 197) * mm, "end": v(189.6, 197) * mm});
            skLineSegment(sketch, "E2603", {"start": v(189.6, 197) * mm, "end": v(189.78, 196.97) * mm});
            skLineSegment(sketch, "E2604", {"start": v(189.78, 196.97) * mm, "end": v(189.96, 196.93) * mm});
            skLineSegment(sketch, "E2605", {"start": v(189.96, 196.93) * mm, "end": v(190.14, 196.86) * mm});
            skLineSegment(sketch, "E2606", {"start": v(190.14, 196.86) * mm, "end": v(190.3, 196.77) * mm});
            skLineSegment(sketch, "E2607", {"start": v(190.3, 196.77) * mm, "end": v(190.46, 196.66) * mm});
            skLineSegment(sketch, "E2608", {"start": v(190.46, 196.66) * mm, "end": v(190.6, 196.53) * mm});
            skLineSegment(sketch, "E2609", {"start": v(190.6, 196.53) * mm, "end": v(190.71, 196.38) * mm});
            skLineSegment(sketch, "E2610", {"start": v(190.71, 196.38) * mm, "end": v(190.79, 196.26) * mm});
            skLineSegment(sketch, "E2611", {"start": v(190.79, 196.26) * mm, "end": v(190.83, 196.24) * mm});
            skLineSegment(sketch, "E2612", {"start": v(190.83, 196.24) * mm, "end": v(190.98, 196.14) * mm});
            skLineSegment(sketch, "E2613", {"start": v(190.98, 196.14) * mm, "end": v(191.12, 196) * mm});
            skLineSegment(sketch, "E2614", {"start": v(191.12, 196) * mm, "end": v(191.24, 195.87) * mm});
            skLineSegment(sketch, "E2615", {"start": v(191.24, 195.87) * mm, "end": v(191.32, 195.75) * mm});
            skLineSegment(sketch, "E2616", {"start": v(191.32, 195.75) * mm, "end": v(191.36, 195.73) * mm});
            skLineSegment(sketch, "E2617", {"start": v(191.36, 195.73) * mm, "end": v(191.52, 195.62) * mm});
            skLineSegment(sketch, "E2618", {"start": v(191.52, 195.62) * mm, "end": v(191.66, 195.5) * mm});
            skLineSegment(sketch, "E2619", {"start": v(191.66, 195.5) * mm, "end": v(191.78, 195.36) * mm});
            skLineSegment(sketch, "E2620", {"start": v(191.78, 195.36) * mm, "end": v(191.86, 195.25) * mm});
            skLineSegment(sketch, "E2621", {"start": v(191.86, 195.25) * mm, "end": v(191.9, 195.23) * mm});
            skLineSegment(sketch, "E2622", {"start": v(191.9, 195.23) * mm, "end": v(192.06, 195.12) * mm});
            skLineSegment(sketch, "E2623", {"start": v(192.06, 195.12) * mm, "end": v(192.2, 195) * mm});
            skLineSegment(sketch, "E2624", {"start": v(192.2, 195) * mm, "end": v(192.33, 194.86) * mm});
            skLineSegment(sketch, "E2625", {"start": v(192.33, 194.86) * mm, "end": v(192.41, 194.75) * mm});
            skLineSegment(sketch, "E2626", {"start": v(192.41, 194.75) * mm, "end": v(192.45, 194.73) * mm});
            skLineSegment(sketch, "E2627", {"start": v(192.45, 194.73) * mm, "end": v(192.61, 194.63) * mm});
            skLineSegment(sketch, "E2628", {"start": v(192.61, 194.63) * mm, "end": v(192.76, 194.51) * mm});
            skLineSegment(sketch, "E2629", {"start": v(192.76, 194.51) * mm, "end": v(192.89, 194.38) * mm});
            skLineSegment(sketch, "E2630", {"start": v(192.89, 194.38) * mm, "end": v(192.97, 194.27) * mm});
            skLineSegment(sketch, "E2631", {"start": v(192.97, 194.27) * mm, "end": v(193, 194.25) * mm});
            skLineSegment(sketch, "E2632", {"start": v(193, 194.25) * mm, "end": v(193.17, 194.15) * mm});
            skLineSegment(sketch, "E2633", {"start": v(193.17, 194.15) * mm, "end": v(193.32, 194.03) * mm});
            skLineSegment(sketch, "E2634", {"start": v(193.32, 194.03) * mm, "end": v(193.45, 193.9) * mm});
            skLineSegment(sketch, "E2635", {"start": v(193.45, 193.9) * mm, "end": v(193.54, 193.79) * mm});
            skLineSegment(sketch, "E2636", {"start": v(193.54, 193.79) * mm, "end": v(193.58, 193.77) * mm});
            skLineSegment(sketch, "E2637", {"start": v(193.58, 193.77) * mm, "end": v(193.74, 193.68) * mm});
            skLineSegment(sketch, "E2638", {"start": v(193.74, 193.68) * mm, "end": v(193.89, 193.57) * mm});
            skLineSegment(sketch, "E2639", {"start": v(193.89, 193.57) * mm, "end": v(194.03, 193.43) * mm});
            skLineSegment(sketch, "E2640", {"start": v(194.03, 193.43) * mm, "end": v(194.11, 193.32) * mm});
            skLineSegment(sketch, "E2641", {"start": v(194.11, 193.32) * mm, "end": v(194.15, 193.3) * mm});
            skLineSegment(sketch, "E2642", {"start": v(194.15, 193.3) * mm, "end": v(194.32, 193.22) * mm});
            skLineSegment(sketch, "E2643", {"start": v(194.32, 193.22) * mm, "end": v(194.47, 193.1) * mm});
            skLineSegment(sketch, "E2644", {"start": v(194.47, 193.1) * mm, "end": v(194.6, 192.98) * mm});
            skLineSegment(sketch, "E2645", {"start": v(194.6, 192.98) * mm, "end": v(194.7, 192.87) * mm});
            skLineSegment(sketch, "E2646", {"start": v(194.7, 192.87) * mm, "end": v(194.74, 192.85) * mm});
            skLineSegment(sketch, "E2647", {"start": v(194.74, 192.85) * mm, "end": v(194.9, 192.76) * mm});
            skLineSegment(sketch, "E2648", {"start": v(194.9, 192.76) * mm, "end": v(195.06, 192.66) * mm});
            skLineSegment(sketch, "E2649", {"start": v(195.06, 192.66) * mm, "end": v(195.2, 192.53) * mm});
            skLineSegment(sketch, "E2650", {"start": v(195.2, 192.53) * mm, "end": v(195.32, 192.39) * mm});
            skLineSegment(sketch, "E2651", {"start": v(195.32, 192.39) * mm, "end": v(195.42, 192.23) * mm});
            skLineSegment(sketch, "E2652", {"start": v(195.42, 192.23) * mm, "end": v(195.5, 192.06) * mm});
            skLineSegment(sketch, "E2653", {"start": v(195.5, 192.06) * mm, "end": v(195.56, 191.88) * mm});
            skLineSegment(sketch, "E2654", {"start": v(195.56, 191.88) * mm, "end": v(195.6, 191.7) * mm});
            skLineSegment(sketch, "E2655", {"start": v(195.6, 191.7) * mm, "end": v(195.62, 191.5) * mm});
            skLineSegment(sketch, "E2656", {"start": v(195.62, 191.5) * mm, "end": v(195.6, 191.32) * mm});
            skLineSegment(sketch, "E2657", {"start": v(195.6, 191.32) * mm, "end": v(195.57, 191.13) * mm});
            skLineSegment(sketch, "E2658", {"start": v(195.57, 191.13) * mm, "end": v(195.52, 190.96) * mm});
            skLineSegment(sketch, "E2659", {"start": v(195.52, 190.96) * mm, "end": v(195.44, 190.78) * mm});
            skLineSegment(sketch, "E2660", {"start": v(195.44, 190.78) * mm, "end": v(195.34, 190.62) * mm});
            skLineSegment(sketch, "E2661", {"start": v(195.34, 190.62) * mm, "end": v(195.22, 190.48) * mm});
            skLineSegment(sketch, "E2662", {"start": v(195.22, 190.48) * mm, "end": v(195.09, 190.35) * mm});
            skLineSegment(sketch, "E2663", {"start": v(195.09, 190.35) * mm, "end": v(194.94, 190.23) * mm});
            skLineSegment(sketch, "E2664", {"start": v(194.94, 190.23) * mm, "end": v(194.77, 190.14) * mm});
            skLineSegment(sketch, "E2665", {"start": v(194.77, 190.14) * mm, "end": v(194.6, 190.07) * mm});
            skLineSegment(sketch, "E2666", {"start": v(194.6, 190.07) * mm, "end": v(194.42, 190.02) * mm});
            skLineSegment(sketch, "E2667", {"start": v(194.42, 190.02) * mm, "end": v(194.23, 190) * mm});
            skLineSegment(sketch, "E2668", {"start": v(194.23, 190) * mm, "end": v(194.04, 189.99) * mm});
            skLineSegment(sketch, "E2669", {"start": v(194.04, 189.99) * mm, "end": v(193.86, 190) * mm});
            skLineSegment(sketch, "E2670", {"start": v(98.9, 171.3) * mm, "end": v(98.72, 171.33) * mm});
            skLineSegment(sketch, "E2671", {"start": v(98.72, 171.33) * mm, "end": v(98.54, 171.37) * mm});
            skLineSegment(sketch, "E2672", {"start": v(98.54, 171.37) * mm, "end": v(98.36, 171.44) * mm});
            skLineSegment(sketch, "E2673", {"start": v(98.36, 171.44) * mm, "end": v(98.2, 171.53) * mm});
            skLineSegment(sketch, "E2674", {"start": v(98.2, 171.53) * mm, "end": v(98.04, 171.64) * mm});
            skLineSegment(sketch, "E2675", {"start": v(98.04, 171.64) * mm, "end": v(97.9, 171.77) * mm});
            skLineSegment(sketch, "E2676", {"start": v(97.9, 171.77) * mm, "end": v(97.79, 171.92) * mm});
            skLineSegment(sketch, "E2677", {"start": v(97.79, 171.92) * mm, "end": v(97.69, 172.08) * mm});
            skLineSegment(sketch, "E2678", {"start": v(97.69, 172.08) * mm, "end": v(97.6, 172.25) * mm});
            skLineSegment(sketch, "E2679", {"start": v(97.6, 172.25) * mm, "end": v(97.55, 172.43) * mm});
            skLineSegment(sketch, "E2680", {"start": v(97.55, 172.43) * mm, "end": v(97.51, 172.61) * mm});
            skLineSegment(sketch, "E2681", {"start": v(97.51, 172.61) * mm, "end": v(97.5, 172.8) * mm});
            skLineSegment(sketch, "E2682", {"start": v(97.5, 172.8) * mm, "end": v(97.51, 172.99) * mm});
            skLineSegment(sketch, "E2683", {"start": v(97.51, 172.99) * mm, "end": v(97.55, 173.17) * mm});
            skLineSegment(sketch, "E2684", {"start": v(97.55, 173.17) * mm, "end": v(97.6, 173.35) * mm});
            skLineSegment(sketch, "E2685", {"start": v(97.6, 173.35) * mm, "end": v(97.69, 173.52) * mm});
            skLineSegment(sketch, "E2686", {"start": v(97.69, 173.52) * mm, "end": v(97.79, 173.68) * mm});
            skLineSegment(sketch, "E2687", {"start": v(97.79, 173.68) * mm, "end": v(97.9, 173.83) * mm});
            skLineSegment(sketch, "E2688", {"start": v(97.9, 173.83) * mm, "end": v(98.04, 173.96) * mm});
            skLineSegment(sketch, "E2689", {"start": v(98.04, 173.96) * mm, "end": v(98.2, 174.07) * mm});
            skLineSegment(sketch, "E2690", {"start": v(98.2, 174.07) * mm, "end": v(98.36, 174.16) * mm});
            skLineSegment(sketch, "E2691", {"start": v(98.36, 174.16) * mm, "end": v(98.54, 174.23) * mm});
            skLineSegment(sketch, "E2692", {"start": v(98.54, 174.23) * mm, "end": v(98.72, 174.27) * mm});
            skLineSegment(sketch, "E2693", {"start": v(98.72, 174.27) * mm, "end": v(98.9, 174.3) * mm});
            skLineSegment(sketch, "E2694", {"start": v(98.9, 174.3) * mm, "end": v(99.1, 174.3) * mm});
            skLineSegment(sketch, "E2695", {"start": v(99.1, 174.3) * mm, "end": v(99.28, 174.27) * mm});
            skLineSegment(sketch, "E2696", {"start": v(99.28, 174.27) * mm, "end": v(99.46, 174.23) * mm});
            skLineSegment(sketch, "E2697", {"start": v(99.46, 174.23) * mm, "end": v(99.64, 174.16) * mm});
            skLineSegment(sketch, "E2698", {"start": v(99.64, 174.16) * mm, "end": v(99.8, 174.07) * mm});
            skLineSegment(sketch, "E2699", {"start": v(99.8, 174.07) * mm, "end": v(99.96, 173.96) * mm});
            skLineSegment(sketch, "E2700", {"start": v(99.96, 173.96) * mm, "end": v(100.1, 173.83) * mm});
            skLineSegment(sketch, "E2701", {"start": v(100.1, 173.83) * mm, "end": v(100.21, 173.68) * mm});
            skLineSegment(sketch, "E2702", {"start": v(100.21, 173.68) * mm, "end": v(100.31, 173.52) * mm});
            skLineSegment(sketch, "E2703", {"start": v(100.31, 173.52) * mm, "end": v(100.4, 173.35) * mm});
            skLineSegment(sketch, "E2704", {"start": v(100.4, 173.35) * mm, "end": v(100.45, 173.17) * mm});
            skLineSegment(sketch, "E2705", {"start": v(100.45, 173.17) * mm, "end": v(100.49, 172.99) * mm});
            skLineSegment(sketch, "E2706", {"start": v(100.49, 172.99) * mm, "end": v(100.5, 172.8) * mm});
            skLineSegment(sketch, "E2707", {"start": v(100.5, 172.8) * mm, "end": v(100.49, 172.61) * mm});
            skLineSegment(sketch, "E2708", {"start": v(100.49, 172.61) * mm, "end": v(100.45, 172.43) * mm});
            skLineSegment(sketch, "E2709", {"start": v(100.45, 172.43) * mm, "end": v(100.4, 172.25) * mm});
            skLineSegment(sketch, "E2710", {"start": v(100.4, 172.25) * mm, "end": v(100.31, 172.08) * mm});
            skLineSegment(sketch, "E2711", {"start": v(100.31, 172.08) * mm, "end": v(100.21, 171.92) * mm});
            skLineSegment(sketch, "E2712", {"start": v(100.21, 171.92) * mm, "end": v(100.1, 171.77) * mm});
            skLineSegment(sketch, "E2713", {"start": v(100.1, 171.77) * mm, "end": v(99.96, 171.64) * mm});
            skLineSegment(sketch, "E2714", {"start": v(99.96, 171.64) * mm, "end": v(99.8, 171.53) * mm});
            skLineSegment(sketch, "E2715", {"start": v(99.8, 171.53) * mm, "end": v(99.64, 171.44) * mm});
            skLineSegment(sketch, "E2716", {"start": v(99.64, 171.44) * mm, "end": v(99.46, 171.37) * mm});
            skLineSegment(sketch, "E2717", {"start": v(99.46, 171.37) * mm, "end": v(99.28, 171.33) * mm});
            skLineSegment(sketch, "E2718", {"start": v(99.28, 171.33) * mm, "end": v(99.1, 171.3) * mm});
            skLineSegment(sketch, "E2719", {"start": v(99.1, 171.3) * mm, "end": v(98.9, 171.3) * mm});
            skLineSegment(sketch, "E2720", {"start": v(108.4, 171.3) * mm, "end": v(108.22, 171.33) * mm});
            skLineSegment(sketch, "E2721", {"start": v(108.22, 171.33) * mm, "end": v(108.04, 171.37) * mm});
            skLineSegment(sketch, "E2722", {"start": v(108.04, 171.37) * mm, "end": v(107.86, 171.44) * mm});
            skLineSegment(sketch, "E2723", {"start": v(107.86, 171.44) * mm, "end": v(107.7, 171.53) * mm});
            skLineSegment(sketch, "E2724", {"start": v(107.7, 171.53) * mm, "end": v(107.54, 171.64) * mm});
            skLineSegment(sketch, "E2725", {"start": v(107.54, 171.64) * mm, "end": v(107.4, 171.77) * mm});
            skLineSegment(sketch, "E2726", {"start": v(107.4, 171.77) * mm, "end": v(107.29, 171.92) * mm});
            skLineSegment(sketch, "E2727", {"start": v(107.29, 171.92) * mm, "end": v(107.19, 172.08) * mm});
            skLineSegment(sketch, "E2728", {"start": v(107.19, 172.08) * mm, "end": v(107.1, 172.25) * mm});
            skLineSegment(sketch, "E2729", {"start": v(107.1, 172.25) * mm, "end": v(107.05, 172.43) * mm});
            skLineSegment(sketch, "E2730", {"start": v(107.05, 172.43) * mm, "end": v(107.01, 172.61) * mm});
            skLineSegment(sketch, "E2731", {"start": v(107.01, 172.61) * mm, "end": v(107, 172.8) * mm});
            skLineSegment(sketch, "E2732", {"start": v(107, 172.8) * mm, "end": v(107.01, 172.99) * mm});
            skLineSegment(sketch, "E2733", {"start": v(107.01, 172.99) * mm, "end": v(107.05, 173.17) * mm});
            skLineSegment(sketch, "E2734", {"start": v(107.05, 173.17) * mm, "end": v(107.1, 173.35) * mm});
            skLineSegment(sketch, "E2735", {"start": v(107.1, 173.35) * mm, "end": v(107.19, 173.52) * mm});
            skLineSegment(sketch, "E2736", {"start": v(107.19, 173.52) * mm, "end": v(107.29, 173.68) * mm});
            skLineSegment(sketch, "E2737", {"start": v(107.29, 173.68) * mm, "end": v(107.4, 173.83) * mm});
            skLineSegment(sketch, "E2738", {"start": v(107.4, 173.83) * mm, "end": v(107.54, 173.96) * mm});
            skLineSegment(sketch, "E2739", {"start": v(107.54, 173.96) * mm, "end": v(107.7, 174.07) * mm});
            skLineSegment(sketch, "E2740", {"start": v(107.7, 174.07) * mm, "end": v(107.86, 174.16) * mm});
            skLineSegment(sketch, "E2741", {"start": v(107.86, 174.16) * mm, "end": v(108.04, 174.23) * mm});
            skLineSegment(sketch, "E2742", {"start": v(108.04, 174.23) * mm, "end": v(108.22, 174.27) * mm});
            skLineSegment(sketch, "E2743", {"start": v(108.22, 174.27) * mm, "end": v(108.4, 174.3) * mm});
            skLineSegment(sketch, "E2744", {"start": v(108.4, 174.3) * mm, "end": v(108.6, 174.3) * mm});
            skLineSegment(sketch, "E2745", {"start": v(108.6, 174.3) * mm, "end": v(108.78, 174.27) * mm});
            skLineSegment(sketch, "E2746", {"start": v(108.78, 174.27) * mm, "end": v(108.96, 174.23) * mm});
            skLineSegment(sketch, "E2747", {"start": v(108.96, 174.23) * mm, "end": v(109.14, 174.16) * mm});
            skLineSegment(sketch, "E2748", {"start": v(109.14, 174.16) * mm, "end": v(109.3, 174.07) * mm});
            skLineSegment(sketch, "E2749", {"start": v(109.3, 174.07) * mm, "end": v(109.46, 173.96) * mm});
            skLineSegment(sketch, "E2750", {"start": v(109.46, 173.96) * mm, "end": v(109.6, 173.83) * mm});
            skLineSegment(sketch, "E2751", {"start": v(109.6, 173.83) * mm, "end": v(109.71, 173.68) * mm});
            skLineSegment(sketch, "E2752", {"start": v(109.71, 173.68) * mm, "end": v(109.81, 173.52) * mm});
            skLineSegment(sketch, "E2753", {"start": v(109.81, 173.52) * mm, "end": v(109.9, 173.35) * mm});
            skLineSegment(sketch, "E2754", {"start": v(109.9, 173.35) * mm, "end": v(109.95, 173.17) * mm});
            skLineSegment(sketch, "E2755", {"start": v(109.95, 173.17) * mm, "end": v(109.99, 172.99) * mm});
            skLineSegment(sketch, "E2756", {"start": v(109.99, 172.99) * mm, "end": v(110, 172.8) * mm});
            skLineSegment(sketch, "E2757", {"start": v(110, 172.8) * mm, "end": v(109.99, 172.61) * mm});
            skLineSegment(sketch, "E2758", {"start": v(109.99, 172.61) * mm, "end": v(109.95, 172.43) * mm});
            skLineSegment(sketch, "E2759", {"start": v(109.95, 172.43) * mm, "end": v(109.9, 172.25) * mm});
            skLineSegment(sketch, "E2760", {"start": v(109.9, 172.25) * mm, "end": v(109.81, 172.08) * mm});
            skLineSegment(sketch, "E2761", {"start": v(109.81, 172.08) * mm, "end": v(109.71, 171.92) * mm});
            skLineSegment(sketch, "E2762", {"start": v(109.71, 171.92) * mm, "end": v(109.6, 171.77) * mm});
            skLineSegment(sketch, "E2763", {"start": v(109.6, 171.77) * mm, "end": v(109.46, 171.64) * mm});
            skLineSegment(sketch, "E2764", {"start": v(109.46, 171.64) * mm, "end": v(109.3, 171.53) * mm});
            skLineSegment(sketch, "E2765", {"start": v(109.3, 171.53) * mm, "end": v(109.14, 171.44) * mm});
            skLineSegment(sketch, "E2766", {"start": v(109.14, 171.44) * mm, "end": v(108.96, 171.37) * mm});
            skLineSegment(sketch, "E2767", {"start": v(108.96, 171.37) * mm, "end": v(108.78, 171.33) * mm});
            skLineSegment(sketch, "E2768", {"start": v(108.78, 171.33) * mm, "end": v(108.6, 171.3) * mm});
            skLineSegment(sketch, "E2769", {"start": v(108.6, 171.3) * mm, "end": v(108.4, 171.3) * mm});
            skLineSegment(sketch, "E2770", {"start": v(369.87, 158) * mm, "end": v(369.62, 158.03) * mm});
            skLineSegment(sketch, "E2771", {"start": v(369.62, 158.03) * mm, "end": v(369.38, 158.1) * mm});
            skLineSegment(sketch, "E2772", {"start": v(369.38, 158.1) * mm, "end": v(369.15, 158.2) * mm});
            skLineSegment(sketch, "E2773", {"start": v(369.15, 158.2) * mm, "end": v(368.93, 158.31) * mm});
            skLineSegment(sketch, "E2774", {"start": v(368.93, 158.31) * mm, "end": v(368.73, 158.46) * mm});
            skLineSegment(sketch, "E2775", {"start": v(368.73, 158.46) * mm, "end": v(368.54, 158.63) * mm});
            skLineSegment(sketch, "E2776", {"start": v(368.54, 158.63) * mm, "end": v(368.38, 158.82) * mm});
            skLineSegment(sketch, "E2777", {"start": v(368.38, 158.82) * mm, "end": v(368.25, 159.04) * mm});
            skLineSegment(sketch, "E2778", {"start": v(368.25, 159.04) * mm, "end": v(368.14, 159.26) * mm});
            skLineSegment(sketch, "E2779", {"start": v(368.14, 159.26) * mm, "end": v(368.06, 159.5) * mm});
            skLineSegment(sketch, "E2780", {"start": v(368.06, 159.5) * mm, "end": v(368.02, 159.75) * mm});
            skLineSegment(sketch, "E2781", {"start": v(368.02, 159.75) * mm, "end": v(368, 160) * mm});
            skLineSegment(sketch, "E2782", {"start": v(368, 160) * mm, "end": v(368.02, 160.25) * mm});
            skLineSegment(sketch, "E2783", {"start": v(368.02, 160.25) * mm, "end": v(368.06, 160.5) * mm});
            skLineSegment(sketch, "E2784", {"start": v(368.06, 160.5) * mm, "end": v(368.14, 160.74) * mm});
            skLineSegment(sketch, "E2785", {"start": v(368.14, 160.74) * mm, "end": v(368.25, 160.96) * mm});
            skLineSegment(sketch, "E2786", {"start": v(368.25, 160.96) * mm, "end": v(368.38, 161.18) * mm});
            skLineSegment(sketch, "E2787", {"start": v(368.38, 161.18) * mm, "end": v(368.54, 161.37) * mm});
            skLineSegment(sketch, "E2788", {"start": v(368.54, 161.37) * mm, "end": v(368.73, 161.54) * mm});
            skLineSegment(sketch, "E2789", {"start": v(368.73, 161.54) * mm, "end": v(368.93, 161.69) * mm});
            skLineSegment(sketch, "E2790", {"start": v(368.93, 161.69) * mm, "end": v(369.15, 161.8) * mm});
            skLineSegment(sketch, "E2791", {"start": v(369.15, 161.8) * mm, "end": v(369.38, 161.9) * mm});
            skLineSegment(sketch, "E2792", {"start": v(369.38, 161.9) * mm, "end": v(369.62, 161.97) * mm});
            skLineSegment(sketch, "E2793", {"start": v(369.62, 161.97) * mm, "end": v(369.87, 162) * mm});
            skLineSegment(sketch, "E2794", {"start": v(369.87, 162) * mm, "end": v(370.13, 162) * mm});
            skLineSegment(sketch, "E2795", {"start": v(370.13, 162) * mm, "end": v(370.38, 161.97) * mm});
            skLineSegment(sketch, "E2796", {"start": v(370.38, 161.97) * mm, "end": v(370.62, 161.9) * mm});
            skLineSegment(sketch, "E2797", {"start": v(370.62, 161.9) * mm, "end": v(370.85, 161.8) * mm});
            skLineSegment(sketch, "E2798", {"start": v(370.85, 161.8) * mm, "end": v(371.07, 161.69) * mm});
            skLineSegment(sketch, "E2799", {"start": v(371.07, 161.69) * mm, "end": v(371.27, 161.54) * mm});
            skLineSegment(sketch, "E2800", {"start": v(371.27, 161.54) * mm, "end": v(371.46, 161.37) * mm});
            skLineSegment(sketch, "E2801", {"start": v(371.46, 161.37) * mm, "end": v(371.62, 161.18) * mm});
            skLineSegment(sketch, "E2802", {"start": v(371.62, 161.18) * mm, "end": v(371.75, 160.96) * mm});
            skLineSegment(sketch, "E2803", {"start": v(371.75, 160.96) * mm, "end": v(371.86, 160.74) * mm});
            skLineSegment(sketch, "E2804", {"start": v(371.86, 160.74) * mm, "end": v(371.94, 160.5) * mm});
            skLineSegment(sketch, "E2805", {"start": v(371.94, 160.5) * mm, "end": v(371.98, 160.25) * mm});
            skLineSegment(sketch, "E2806", {"start": v(371.98, 160.25) * mm, "end": v(372, 160) * mm});
            skLineSegment(sketch, "E2807", {"start": v(372, 160) * mm, "end": v(371.98, 159.75) * mm});
            skLineSegment(sketch, "E2808", {"start": v(371.98, 159.75) * mm, "end": v(371.94, 159.5) * mm});
            skLineSegment(sketch, "E2809", {"start": v(371.94, 159.5) * mm, "end": v(371.86, 159.26) * mm});
            skLineSegment(sketch, "E2810", {"start": v(371.86, 159.26) * mm, "end": v(371.75, 159.04) * mm});
            skLineSegment(sketch, "E2811", {"start": v(371.75, 159.04) * mm, "end": v(371.62, 158.82) * mm});
            skLineSegment(sketch, "E2812", {"start": v(371.62, 158.82) * mm, "end": v(371.46, 158.63) * mm});
            skLineSegment(sketch, "E2813", {"start": v(371.46, 158.63) * mm, "end": v(371.27, 158.46) * mm});
            skLineSegment(sketch, "E2814", {"start": v(371.27, 158.46) * mm, "end": v(371.07, 158.31) * mm});
            skLineSegment(sketch, "E2815", {"start": v(371.07, 158.31) * mm, "end": v(370.85, 158.2) * mm});
            skLineSegment(sketch, "E2816", {"start": v(370.85, 158.2) * mm, "end": v(370.62, 158.1) * mm});
            skLineSegment(sketch, "E2817", {"start": v(370.62, 158.1) * mm, "end": v(370.38, 158.03) * mm});
            skLineSegment(sketch, "E2818", {"start": v(370.38, 158.03) * mm, "end": v(370.13, 158) * mm});
            skLineSegment(sketch, "E2819", {"start": v(370.13, 158) * mm, "end": v(369.87, 158) * mm});
            skLineSegment(sketch, "E2820", {"start": v(39.87, 158) * mm, "end": v(39.63, 158.03) * mm});
            skLineSegment(sketch, "E2821", {"start": v(39.63, 158.03) * mm, "end": v(39.38, 158.1) * mm});
            skLineSegment(sketch, "E2822", {"start": v(39.38, 158.1) * mm, "end": v(39.15, 158.2) * mm});
            skLineSegment(sketch, "E2823", {"start": v(39.15, 158.2) * mm, "end": v(38.93, 158.31) * mm});
            skLineSegment(sketch, "E2824", {"start": v(38.93, 158.31) * mm, "end": v(38.73, 158.46) * mm});
            skLineSegment(sketch, "E2825", {"start": v(38.73, 158.46) * mm, "end": v(38.54, 158.63) * mm});
            skLineSegment(sketch, "E2826", {"start": v(38.54, 158.63) * mm, "end": v(38.38, 158.82) * mm});
            skLineSegment(sketch, "E2827", {"start": v(38.38, 158.82) * mm, "end": v(38.25, 159.04) * mm});
            skLineSegment(sketch, "E2828", {"start": v(38.25, 159.04) * mm, "end": v(38.14, 159.26) * mm});
            skLineSegment(sketch, "E2829", {"start": v(38.14, 159.26) * mm, "end": v(38.06, 159.5) * mm});
            skLineSegment(sketch, "E2830", {"start": v(38.06, 159.5) * mm, "end": v(38.02, 159.75) * mm});
            skLineSegment(sketch, "E2831", {"start": v(38.02, 159.75) * mm, "end": v(38, 160) * mm});
            skLineSegment(sketch, "E2832", {"start": v(38, 160) * mm, "end": v(38.02, 160.25) * mm});
            skLineSegment(sketch, "E2833", {"start": v(38.02, 160.25) * mm, "end": v(38.06, 160.5) * mm});
            skLineSegment(sketch, "E2834", {"start": v(38.06, 160.5) * mm, "end": v(38.14, 160.74) * mm});
            skLineSegment(sketch, "E2835", {"start": v(38.14, 160.74) * mm, "end": v(38.25, 160.96) * mm});
            skLineSegment(sketch, "E2836", {"start": v(38.25, 160.96) * mm, "end": v(38.38, 161.18) * mm});
            skLineSegment(sketch, "E2837", {"start": v(38.38, 161.18) * mm, "end": v(38.54, 161.37) * mm});
            skLineSegment(sketch, "E2838", {"start": v(38.54, 161.37) * mm, "end": v(38.73, 161.54) * mm});
            skLineSegment(sketch, "E2839", {"start": v(38.73, 161.54) * mm, "end": v(38.93, 161.69) * mm});
            skLineSegment(sketch, "E2840", {"start": v(38.93, 161.69) * mm, "end": v(39.15, 161.8) * mm});
            skLineSegment(sketch, "E2841", {"start": v(39.15, 161.8) * mm, "end": v(39.38, 161.9) * mm});
            skLineSegment(sketch, "E2842", {"start": v(39.38, 161.9) * mm, "end": v(39.63, 161.97) * mm});
            skLineSegment(sketch, "E2843", {"start": v(39.63, 161.97) * mm, "end": v(39.87, 162) * mm});
            skLineSegment(sketch, "E2844", {"start": v(39.87, 162) * mm, "end": v(40.13, 162) * mm});
            skLineSegment(sketch, "E2845", {"start": v(40.13, 162) * mm, "end": v(40.37, 161.97) * mm});
            skLineSegment(sketch, "E2846", {"start": v(40.37, 161.97) * mm, "end": v(40.62, 161.9) * mm});
            skLineSegment(sketch, "E2847", {"start": v(40.62, 161.9) * mm, "end": v(40.85, 161.8) * mm});
            skLineSegment(sketch, "E2848", {"start": v(40.85, 161.8) * mm, "end": v(41.07, 161.69) * mm});
            skLineSegment(sketch, "E2849", {"start": v(41.07, 161.69) * mm, "end": v(41.27, 161.54) * mm});
            skLineSegment(sketch, "E2850", {"start": v(41.27, 161.54) * mm, "end": v(41.46, 161.37) * mm});
            skLineSegment(sketch, "E2851", {"start": v(41.46, 161.37) * mm, "end": v(41.62, 161.18) * mm});
            skLineSegment(sketch, "E2852", {"start": v(41.62, 161.18) * mm, "end": v(41.75, 160.96) * mm});
            skLineSegment(sketch, "E2853", {"start": v(41.75, 160.96) * mm, "end": v(41.86, 160.74) * mm});
            skLineSegment(sketch, "E2854", {"start": v(41.86, 160.74) * mm, "end": v(41.94, 160.5) * mm});
            skLineSegment(sketch, "E2855", {"start": v(41.94, 160.5) * mm, "end": v(41.98, 160.25) * mm});
            skLineSegment(sketch, "E2856", {"start": v(41.98, 160.25) * mm, "end": v(42, 160) * mm});
            skLineSegment(sketch, "E2857", {"start": v(42, 160) * mm, "end": v(41.98, 159.75) * mm});
            skLineSegment(sketch, "E2858", {"start": v(41.98, 159.75) * mm, "end": v(41.94, 159.5) * mm});
            skLineSegment(sketch, "E2859", {"start": v(41.94, 159.5) * mm, "end": v(41.86, 159.26) * mm});
            skLineSegment(sketch, "E2860", {"start": v(41.86, 159.26) * mm, "end": v(41.75, 159.04) * mm});
            skLineSegment(sketch, "E2861", {"start": v(41.75, 159.04) * mm, "end": v(41.62, 158.82) * mm});
            skLineSegment(sketch, "E2862", {"start": v(41.62, 158.82) * mm, "end": v(41.46, 158.63) * mm});
            skLineSegment(sketch, "E2863", {"start": v(41.46, 158.63) * mm, "end": v(41.27, 158.46) * mm});
            skLineSegment(sketch, "E2864", {"start": v(41.27, 158.46) * mm, "end": v(41.07, 158.31) * mm});
            skLineSegment(sketch, "E2865", {"start": v(41.07, 158.31) * mm, "end": v(40.85, 158.2) * mm});
            skLineSegment(sketch, "E2866", {"start": v(40.85, 158.2) * mm, "end": v(40.62, 158.1) * mm});
            skLineSegment(sketch, "E2867", {"start": v(40.62, 158.1) * mm, "end": v(40.37, 158.03) * mm});
            skLineSegment(sketch, "E2868", {"start": v(40.37, 158.03) * mm, "end": v(40.13, 158) * mm});
            skLineSegment(sketch, "E2869", {"start": v(40.13, 158) * mm, "end": v(39.87, 158) * mm});
            skLineSegment(sketch, "E2870", {"start": v(385.4, 94) * mm, "end": v(385.22, 94.03) * mm});
            skLineSegment(sketch, "E2871", {"start": v(385.22, 94.03) * mm, "end": v(385.04, 94.07) * mm});
            skLineSegment(sketch, "E2872", {"start": v(385.04, 94.07) * mm, "end": v(384.86, 94.14) * mm});
            skLineSegment(sketch, "E2873", {"start": v(384.86, 94.14) * mm, "end": v(384.7, 94.23) * mm});
            skLineSegment(sketch, "E2874", {"start": v(384.7, 94.23) * mm, "end": v(384.54, 94.34) * mm});
            skLineSegment(sketch, "E2875", {"start": v(384.54, 94.34) * mm, "end": v(384.4, 94.47) * mm});
            skLineSegment(sketch, "E2876", {"start": v(384.4, 94.47) * mm, "end": v(384.29, 94.62) * mm});
            skLineSegment(sketch, "E2877", {"start": v(384.29, 94.62) * mm, "end": v(384.19, 94.78) * mm});
            skLineSegment(sketch, "E2878", {"start": v(384.19, 94.78) * mm, "end": v(384.1, 94.95) * mm});
            skLineSegment(sketch, "E2879", {"start": v(384.1, 94.95) * mm, "end": v(384.05, 95.13) * mm});
            skLineSegment(sketch, "E2880", {"start": v(384.05, 95.13) * mm, "end": v(384.01, 95.31) * mm});
            skLineSegment(sketch, "E2881", {"start": v(384.01, 95.31) * mm, "end": v(384, 95.5) * mm});
            skLineSegment(sketch, "E2882", {"start": v(384, 95.5) * mm, "end": v(384.01, 95.69) * mm});
            skLineSegment(sketch, "E2883", {"start": v(384.01, 95.69) * mm, "end": v(384.05, 95.87) * mm});
            skLineSegment(sketch, "E2884", {"start": v(384.05, 95.87) * mm, "end": v(384.1, 96.05) * mm});
            skLineSegment(sketch, "E2885", {"start": v(384.1, 96.05) * mm, "end": v(384.19, 96.22) * mm});
            skLineSegment(sketch, "E2886", {"start": v(384.19, 96.22) * mm, "end": v(384.29, 96.38) * mm});
            skLineSegment(sketch, "E2887", {"start": v(384.29, 96.38) * mm, "end": v(384.4, 96.53) * mm});
            skLineSegment(sketch, "E2888", {"start": v(384.4, 96.53) * mm, "end": v(384.54, 96.66) * mm});
            skLineSegment(sketch, "E2889", {"start": v(384.54, 96.66) * mm, "end": v(384.7, 96.77) * mm});
            skLineSegment(sketch, "E2890", {"start": v(384.7, 96.77) * mm, "end": v(384.86, 96.86) * mm});
            skLineSegment(sketch, "E2891", {"start": v(384.86, 96.86) * mm, "end": v(385.04, 96.93) * mm});
            skLineSegment(sketch, "E2892", {"start": v(385.04, 96.93) * mm, "end": v(385.22, 96.97) * mm});
            skLineSegment(sketch, "E2893", {"start": v(385.22, 96.97) * mm, "end": v(385.4, 97) * mm});
            skLineSegment(sketch, "E2894", {"start": v(385.4, 97) * mm, "end": v(385.6, 97) * mm});
            skLineSegment(sketch, "E2895", {"start": v(385.6, 97) * mm, "end": v(385.78, 96.97) * mm});
            skLineSegment(sketch, "E2896", {"start": v(385.78, 96.97) * mm, "end": v(385.96, 96.93) * mm});
            skLineSegment(sketch, "E2897", {"start": v(385.96, 96.93) * mm, "end": v(386.14, 96.86) * mm});
            skLineSegment(sketch, "E2898", {"start": v(386.14, 96.86) * mm, "end": v(386.3, 96.77) * mm});
            skLineSegment(sketch, "E2899", {"start": v(386.3, 96.77) * mm, "end": v(386.46, 96.66) * mm});
            skLineSegment(sketch, "E2900", {"start": v(386.46, 96.66) * mm, "end": v(386.6, 96.53) * mm});
            skLineSegment(sketch, "E2901", {"start": v(386.6, 96.53) * mm, "end": v(386.71, 96.38) * mm});
            skLineSegment(sketch, "E2902", {"start": v(386.71, 96.38) * mm, "end": v(386.81, 96.22) * mm});
            skLineSegment(sketch, "E2903", {"start": v(386.81, 96.22) * mm, "end": v(386.9, 96.05) * mm});
            skLineSegment(sketch, "E2904", {"start": v(386.9, 96.05) * mm, "end": v(386.95, 95.87) * mm});
            skLineSegment(sketch, "E2905", {"start": v(386.95, 95.87) * mm, "end": v(386.99, 95.69) * mm});
            skLineSegment(sketch, "E2906", {"start": v(386.99, 95.69) * mm, "end": v(387, 95.5) * mm});
            skLineSegment(sketch, "E2907", {"start": v(387, 95.5) * mm, "end": v(386.99, 95.31) * mm});
            skLineSegment(sketch, "E2908", {"start": v(386.99, 95.31) * mm, "end": v(386.95, 95.13) * mm});
            skLineSegment(sketch, "E2909", {"start": v(386.95, 95.13) * mm, "end": v(386.9, 94.95) * mm});
            skLineSegment(sketch, "E2910", {"start": v(386.9, 94.95) * mm, "end": v(386.81, 94.78) * mm});
            skLineSegment(sketch, "E2911", {"start": v(386.81, 94.78) * mm, "end": v(386.71, 94.62) * mm});
            skLineSegment(sketch, "E2912", {"start": v(386.71, 94.62) * mm, "end": v(386.6, 94.47) * mm});
            skLineSegment(sketch, "E2913", {"start": v(386.6, 94.47) * mm, "end": v(386.46, 94.34) * mm});
            skLineSegment(sketch, "E2914", {"start": v(386.46, 94.34) * mm, "end": v(386.3, 94.23) * mm});
            skLineSegment(sketch, "E2915", {"start": v(386.3, 94.23) * mm, "end": v(386.14, 94.14) * mm});
            skLineSegment(sketch, "E2916", {"start": v(386.14, 94.14) * mm, "end": v(385.96, 94.07) * mm});
            skLineSegment(sketch, "E2917", {"start": v(385.96, 94.07) * mm, "end": v(385.78, 94.03) * mm});
            skLineSegment(sketch, "E2918", {"start": v(385.78, 94.03) * mm, "end": v(385.6, 94) * mm});
            skLineSegment(sketch, "E2919", {"start": v(385.6, 94) * mm, "end": v(385.4, 94) * mm});
            skLineSegment(sketch, "E2920", {"start": v(354.4, 94) * mm, "end": v(354.22, 94.03) * mm});
            skLineSegment(sketch, "E2921", {"start": v(354.22, 94.03) * mm, "end": v(354.04, 94.07) * mm});
            skLineSegment(sketch, "E2922", {"start": v(354.04, 94.07) * mm, "end": v(353.86, 94.14) * mm});
            skLineSegment(sketch, "E2923", {"start": v(353.86, 94.14) * mm, "end": v(353.7, 94.23) * mm});
            skLineSegment(sketch, "E2924", {"start": v(353.7, 94.23) * mm, "end": v(353.54, 94.34) * mm});
            skLineSegment(sketch, "E2925", {"start": v(353.54, 94.34) * mm, "end": v(353.4, 94.47) * mm});
            skLineSegment(sketch, "E2926", {"start": v(353.4, 94.47) * mm, "end": v(353.29, 94.62) * mm});
            skLineSegment(sketch, "E2927", {"start": v(353.29, 94.62) * mm, "end": v(353.19, 94.78) * mm});
            skLineSegment(sketch, "E2928", {"start": v(353.19, 94.78) * mm, "end": v(353.1, 94.95) * mm});
            skLineSegment(sketch, "E2929", {"start": v(353.1, 94.95) * mm, "end": v(353.05, 95.13) * mm});
            skLineSegment(sketch, "E2930", {"start": v(353.05, 95.13) * mm, "end": v(353.01, 95.31) * mm});
            skLineSegment(sketch, "E2931", {"start": v(353.01, 95.31) * mm, "end": v(353, 95.5) * mm});
            skLineSegment(sketch, "E2932", {"start": v(353, 95.5) * mm, "end": v(353.01, 95.69) * mm});
            skLineSegment(sketch, "E2933", {"start": v(353.01, 95.69) * mm, "end": v(353.05, 95.87) * mm});
            skLineSegment(sketch, "E2934", {"start": v(353.05, 95.87) * mm, "end": v(353.1, 96.05) * mm});
            skLineSegment(sketch, "E2935", {"start": v(353.1, 96.05) * mm, "end": v(353.19, 96.22) * mm});
            skLineSegment(sketch, "E2936", {"start": v(353.19, 96.22) * mm, "end": v(353.29, 96.38) * mm});
            skLineSegment(sketch, "E2937", {"start": v(353.29, 96.38) * mm, "end": v(353.4, 96.53) * mm});
            skLineSegment(sketch, "E2938", {"start": v(353.4, 96.53) * mm, "end": v(353.54, 96.66) * mm});
            skLineSegment(sketch, "E2939", {"start": v(353.54, 96.66) * mm, "end": v(353.7, 96.77) * mm});
            skLineSegment(sketch, "E2940", {"start": v(353.7, 96.77) * mm, "end": v(353.86, 96.86) * mm});
            skLineSegment(sketch, "E2941", {"start": v(353.86, 96.86) * mm, "end": v(354.04, 96.93) * mm});
            skLineSegment(sketch, "E2942", {"start": v(354.04, 96.93) * mm, "end": v(354.22, 96.97) * mm});
            skLineSegment(sketch, "E2943", {"start": v(354.22, 96.97) * mm, "end": v(354.4, 97) * mm});
            skLineSegment(sketch, "E2944", {"start": v(354.4, 97) * mm, "end": v(354.6, 97) * mm});
            skLineSegment(sketch, "E2945", {"start": v(354.6, 97) * mm, "end": v(354.78, 96.97) * mm});
            skLineSegment(sketch, "E2946", {"start": v(354.78, 96.97) * mm, "end": v(354.96, 96.93) * mm});
            skLineSegment(sketch, "E2947", {"start": v(354.96, 96.93) * mm, "end": v(355.14, 96.86) * mm});
            skLineSegment(sketch, "E2948", {"start": v(355.14, 96.86) * mm, "end": v(355.3, 96.77) * mm});
            skLineSegment(sketch, "E2949", {"start": v(355.3, 96.77) * mm, "end": v(355.46, 96.66) * mm});
            skLineSegment(sketch, "E2950", {"start": v(355.46, 96.66) * mm, "end": v(355.6, 96.53) * mm});
            skLineSegment(sketch, "E2951", {"start": v(355.6, 96.53) * mm, "end": v(355.71, 96.38) * mm});
            skLineSegment(sketch, "E2952", {"start": v(355.71, 96.38) * mm, "end": v(355.81, 96.22) * mm});
            skLineSegment(sketch, "E2953", {"start": v(355.81, 96.22) * mm, "end": v(355.9, 96.05) * mm});
            skLineSegment(sketch, "E2954", {"start": v(355.9, 96.05) * mm, "end": v(355.95, 95.87) * mm});
            skLineSegment(sketch, "E2955", {"start": v(355.95, 95.87) * mm, "end": v(355.99, 95.69) * mm});
            skLineSegment(sketch, "E2956", {"start": v(355.99, 95.69) * mm, "end": v(356, 95.5) * mm});
            skLineSegment(sketch, "E2957", {"start": v(356, 95.5) * mm, "end": v(355.99, 95.31) * mm});
            skLineSegment(sketch, "E2958", {"start": v(355.99, 95.31) * mm, "end": v(355.95, 95.13) * mm});
            skLineSegment(sketch, "E2959", {"start": v(355.95, 95.13) * mm, "end": v(355.9, 94.95) * mm});
            skLineSegment(sketch, "E2960", {"start": v(355.9, 94.95) * mm, "end": v(355.81, 94.78) * mm});
            skLineSegment(sketch, "E2961", {"start": v(355.81, 94.78) * mm, "end": v(355.71, 94.62) * mm});
            skLineSegment(sketch, "E2962", {"start": v(355.71, 94.62) * mm, "end": v(355.6, 94.47) * mm});
            skLineSegment(sketch, "E2963", {"start": v(355.6, 94.47) * mm, "end": v(355.46, 94.34) * mm});
            skLineSegment(sketch, "E2964", {"start": v(355.46, 94.34) * mm, "end": v(355.3, 94.23) * mm});
            skLineSegment(sketch, "E2965", {"start": v(355.3, 94.23) * mm, "end": v(355.14, 94.14) * mm});
            skLineSegment(sketch, "E2966", {"start": v(355.14, 94.14) * mm, "end": v(354.96, 94.07) * mm});
            skLineSegment(sketch, "E2967", {"start": v(354.96, 94.07) * mm, "end": v(354.78, 94.03) * mm});
            skLineSegment(sketch, "E2968", {"start": v(354.78, 94.03) * mm, "end": v(354.6, 94) * mm});
            skLineSegment(sketch, "E2969", {"start": v(354.6, 94) * mm, "end": v(354.4, 94) * mm});
            skLineSegment(sketch, "E2970", {"start": v(55.4, 94) * mm, "end": v(55.22, 94.03) * mm});
            skLineSegment(sketch, "E2971", {"start": v(55.22, 94.03) * mm, "end": v(55.04, 94.07) * mm});
            skLineSegment(sketch, "E2972", {"start": v(55.04, 94.07) * mm, "end": v(54.86, 94.14) * mm});
            skLineSegment(sketch, "E2973", {"start": v(54.86, 94.14) * mm, "end": v(54.7, 94.23) * mm});
            skLineSegment(sketch, "E2974", {"start": v(54.7, 94.23) * mm, "end": v(54.54, 94.34) * mm});
            skLineSegment(sketch, "E2975", {"start": v(54.54, 94.34) * mm, "end": v(54.4, 94.47) * mm});
            skLineSegment(sketch, "E2976", {"start": v(54.4, 94.47) * mm, "end": v(54.29, 94.62) * mm});
            skLineSegment(sketch, "E2977", {"start": v(54.29, 94.62) * mm, "end": v(54.19, 94.78) * mm});
            skLineSegment(sketch, "E2978", {"start": v(54.19, 94.78) * mm, "end": v(54.1, 94.95) * mm});
            skLineSegment(sketch, "E2979", {"start": v(54.1, 94.95) * mm, "end": v(54.05, 95.13) * mm});
            skLineSegment(sketch, "E2980", {"start": v(54.05, 95.13) * mm, "end": v(54.01, 95.31) * mm});
            skLineSegment(sketch, "E2981", {"start": v(54.01, 95.31) * mm, "end": v(54, 95.5) * mm});
            skLineSegment(sketch, "E2982", {"start": v(54, 95.5) * mm, "end": v(54.01, 95.69) * mm});
            skLineSegment(sketch, "E2983", {"start": v(54.01, 95.69) * mm, "end": v(54.05, 95.87) * mm});
            skLineSegment(sketch, "E2984", {"start": v(54.05, 95.87) * mm, "end": v(54.1, 96.05) * mm});
            skLineSegment(sketch, "E2985", {"start": v(54.1, 96.05) * mm, "end": v(54.19, 96.22) * mm});
            skLineSegment(sketch, "E2986", {"start": v(54.19, 96.22) * mm, "end": v(54.29, 96.38) * mm});
            skLineSegment(sketch, "E2987", {"start": v(54.29, 96.38) * mm, "end": v(54.4, 96.53) * mm});
            skLineSegment(sketch, "E2988", {"start": v(54.4, 96.53) * mm, "end": v(54.54, 96.66) * mm});
            skLineSegment(sketch, "E2989", {"start": v(54.54, 96.66) * mm, "end": v(54.7, 96.77) * mm});
            skLineSegment(sketch, "E2990", {"start": v(54.7, 96.77) * mm, "end": v(54.86, 96.86) * mm});
            skLineSegment(sketch, "E2991", {"start": v(54.86, 96.86) * mm, "end": v(55.04, 96.93) * mm});
            skLineSegment(sketch, "E2992", {"start": v(55.04, 96.93) * mm, "end": v(55.22, 96.97) * mm});
            skLineSegment(sketch, "E2993", {"start": v(55.22, 96.97) * mm, "end": v(55.4, 97) * mm});
            skLineSegment(sketch, "E2994", {"start": v(55.4, 97) * mm, "end": v(55.6, 97) * mm});
            skLineSegment(sketch, "E2995", {"start": v(55.6, 97) * mm, "end": v(55.78, 96.97) * mm});
            skLineSegment(sketch, "E2996", {"start": v(55.78, 96.97) * mm, "end": v(55.96, 96.93) * mm});
            skLineSegment(sketch, "E2997", {"start": v(55.96, 96.93) * mm, "end": v(56.14, 96.86) * mm});
            skLineSegment(sketch, "E2998", {"start": v(56.14, 96.86) * mm, "end": v(56.3, 96.77) * mm});
            skLineSegment(sketch, "E2999", {"start": v(56.3, 96.77) * mm, "end": v(56.46, 96.66) * mm});
            skLineSegment(sketch, "E3000", {"start": v(56.46, 96.66) * mm, "end": v(56.6, 96.53) * mm});
            skLineSegment(sketch, "E3001", {"start": v(56.6, 96.53) * mm, "end": v(56.71, 96.38) * mm});
            skLineSegment(sketch, "E3002", {"start": v(56.71, 96.38) * mm, "end": v(56.81, 96.22) * mm});
            skLineSegment(sketch, "E3003", {"start": v(56.81, 96.22) * mm, "end": v(56.9, 96.05) * mm});
            skLineSegment(sketch, "E3004", {"start": v(56.9, 96.05) * mm, "end": v(56.95, 95.87) * mm});
            skLineSegment(sketch, "E3005", {"start": v(56.95, 95.87) * mm, "end": v(56.99, 95.69) * mm});
            skLineSegment(sketch, "E3006", {"start": v(56.99, 95.69) * mm, "end": v(57, 95.5) * mm});
            skLineSegment(sketch, "E3007", {"start": v(57, 95.5) * mm, "end": v(56.99, 95.31) * mm});
            skLineSegment(sketch, "E3008", {"start": v(56.99, 95.31) * mm, "end": v(56.95, 95.13) * mm});
            skLineSegment(sketch, "E3009", {"start": v(56.95, 95.13) * mm, "end": v(56.9, 94.95) * mm});
            skLineSegment(sketch, "E3010", {"start": v(56.9, 94.95) * mm, "end": v(56.81, 94.78) * mm});
            skLineSegment(sketch, "E3011", {"start": v(56.81, 94.78) * mm, "end": v(56.71, 94.62) * mm});
            skLineSegment(sketch, "E3012", {"start": v(56.71, 94.62) * mm, "end": v(56.6, 94.47) * mm});
            skLineSegment(sketch, "E3013", {"start": v(56.6, 94.47) * mm, "end": v(56.46, 94.34) * mm});
            skLineSegment(sketch, "E3014", {"start": v(56.46, 94.34) * mm, "end": v(56.3, 94.23) * mm});
            skLineSegment(sketch, "E3015", {"start": v(56.3, 94.23) * mm, "end": v(56.14, 94.14) * mm});
            skLineSegment(sketch, "E3016", {"start": v(56.14, 94.14) * mm, "end": v(55.96, 94.07) * mm});
            skLineSegment(sketch, "E3017", {"start": v(55.96, 94.07) * mm, "end": v(55.78, 94.03) * mm});
            skLineSegment(sketch, "E3018", {"start": v(55.78, 94.03) * mm, "end": v(55.6, 94) * mm});
            skLineSegment(sketch, "E3019", {"start": v(55.6, 94) * mm, "end": v(55.4, 94) * mm});
            skLineSegment(sketch, "E3020", {"start": v(24.4, 94) * mm, "end": v(24.22, 94.03) * mm});
            skLineSegment(sketch, "E3021", {"start": v(24.22, 94.03) * mm, "end": v(24.04, 94.07) * mm});
            skLineSegment(sketch, "E3022", {"start": v(24.04, 94.07) * mm, "end": v(23.86, 94.14) * mm});
            skLineSegment(sketch, "E3023", {"start": v(23.86, 94.14) * mm, "end": v(23.7, 94.23) * mm});
            skLineSegment(sketch, "E3024", {"start": v(23.7, 94.23) * mm, "end": v(23.54, 94.34) * mm});
            skLineSegment(sketch, "E3025", {"start": v(23.54, 94.34) * mm, "end": v(23.4, 94.47) * mm});
            skLineSegment(sketch, "E3026", {"start": v(23.4, 94.47) * mm, "end": v(23.29, 94.62) * mm});
            skLineSegment(sketch, "E3027", {"start": v(23.29, 94.62) * mm, "end": v(23.19, 94.78) * mm});
            skLineSegment(sketch, "E3028", {"start": v(23.19, 94.78) * mm, "end": v(23.1, 94.95) * mm});
            skLineSegment(sketch, "E3029", {"start": v(23.1, 94.95) * mm, "end": v(23.05, 95.13) * mm});
            skLineSegment(sketch, "E3030", {"start": v(23.05, 95.13) * mm, "end": v(23.01, 95.31) * mm});
            skLineSegment(sketch, "E3031", {"start": v(23.01, 95.31) * mm, "end": v(23, 95.5) * mm});
            skLineSegment(sketch, "E3032", {"start": v(23, 95.5) * mm, "end": v(23.01, 95.69) * mm});
            skLineSegment(sketch, "E3033", {"start": v(23.01, 95.69) * mm, "end": v(23.05, 95.87) * mm});
            skLineSegment(sketch, "E3034", {"start": v(23.05, 95.87) * mm, "end": v(23.1, 96.05) * mm});
            skLineSegment(sketch, "E3035", {"start": v(23.1, 96.05) * mm, "end": v(23.19, 96.22) * mm});
            skLineSegment(sketch, "E3036", {"start": v(23.19, 96.22) * mm, "end": v(23.29, 96.38) * mm});
            skLineSegment(sketch, "E3037", {"start": v(23.29, 96.38) * mm, "end": v(23.4, 96.53) * mm});
            skLineSegment(sketch, "E3038", {"start": v(23.4, 96.53) * mm, "end": v(23.54, 96.66) * mm});
            skLineSegment(sketch, "E3039", {"start": v(23.54, 96.66) * mm, "end": v(23.7, 96.77) * mm});
            skLineSegment(sketch, "E3040", {"start": v(23.7, 96.77) * mm, "end": v(23.86, 96.86) * mm});
            skLineSegment(sketch, "E3041", {"start": v(23.86, 96.86) * mm, "end": v(24.04, 96.93) * mm});
            skLineSegment(sketch, "E3042", {"start": v(24.04, 96.93) * mm, "end": v(24.22, 96.97) * mm});
            skLineSegment(sketch, "E3043", {"start": v(24.22, 96.97) * mm, "end": v(24.4, 97) * mm});
            skLineSegment(sketch, "E3044", {"start": v(24.4, 97) * mm, "end": v(24.6, 97) * mm});
            skLineSegment(sketch, "E3045", {"start": v(24.6, 97) * mm, "end": v(24.78, 96.97) * mm});
            skLineSegment(sketch, "E3046", {"start": v(24.78, 96.97) * mm, "end": v(24.96, 96.93) * mm});
            skLineSegment(sketch, "E3047", {"start": v(24.96, 96.93) * mm, "end": v(25.14, 96.86) * mm});
            skLineSegment(sketch, "E3048", {"start": v(25.14, 96.86) * mm, "end": v(25.3, 96.77) * mm});
            skLineSegment(sketch, "E3049", {"start": v(25.3, 96.77) * mm, "end": v(25.46, 96.66) * mm});
            skLineSegment(sketch, "E3050", {"start": v(25.46, 96.66) * mm, "end": v(25.6, 96.53) * mm});
            skLineSegment(sketch, "E3051", {"start": v(25.6, 96.53) * mm, "end": v(25.71, 96.38) * mm});
            skLineSegment(sketch, "E3052", {"start": v(25.71, 96.38) * mm, "end": v(25.81, 96.22) * mm});
            skLineSegment(sketch, "E3053", {"start": v(25.81, 96.22) * mm, "end": v(25.9, 96.05) * mm});
            skLineSegment(sketch, "E3054", {"start": v(25.9, 96.05) * mm, "end": v(25.95, 95.87) * mm});
            skLineSegment(sketch, "E3055", {"start": v(25.95, 95.87) * mm, "end": v(25.99, 95.69) * mm});
            skLineSegment(sketch, "E3056", {"start": v(25.99, 95.69) * mm, "end": v(26, 95.5) * mm});
            skLineSegment(sketch, "E3057", {"start": v(26, 95.5) * mm, "end": v(25.99, 95.31) * mm});
            skLineSegment(sketch, "E3058", {"start": v(25.99, 95.31) * mm, "end": v(25.95, 95.13) * mm});
            skLineSegment(sketch, "E3059", {"start": v(25.95, 95.13) * mm, "end": v(25.9, 94.95) * mm});
            skLineSegment(sketch, "E3060", {"start": v(25.9, 94.95) * mm, "end": v(25.81, 94.78) * mm});
            skLineSegment(sketch, "E3061", {"start": v(25.81, 94.78) * mm, "end": v(25.71, 94.62) * mm});
            skLineSegment(sketch, "E3062", {"start": v(25.71, 94.62) * mm, "end": v(25.6, 94.47) * mm});
            skLineSegment(sketch, "E3063", {"start": v(25.6, 94.47) * mm, "end": v(25.46, 94.34) * mm});
            skLineSegment(sketch, "E3064", {"start": v(25.46, 94.34) * mm, "end": v(25.3, 94.23) * mm});
            skLineSegment(sketch, "E3065", {"start": v(25.3, 94.23) * mm, "end": v(25.14, 94.14) * mm});
            skLineSegment(sketch, "E3066", {"start": v(25.14, 94.14) * mm, "end": v(24.96, 94.07) * mm});
            skLineSegment(sketch, "E3067", {"start": v(24.96, 94.07) * mm, "end": v(24.78, 94.03) * mm});
            skLineSegment(sketch, "E3068", {"start": v(24.78, 94.03) * mm, "end": v(24.6, 94) * mm});
            skLineSegment(sketch, "E3069", {"start": v(24.6, 94) * mm, "end": v(24.4, 94) * mm});
            skLineSegment(sketch, "E3070", {"start": v(39.25, 68.02) * mm, "end": v(37.75, 68.21) * mm});
            skLineSegment(sketch, "E3071", {"start": v(37.75, 68.21) * mm, "end": v(36.3, 68.59) * mm});
            skLineSegment(sketch, "E3072", {"start": v(36.3, 68.59) * mm, "end": v(34.9, 69.14) * mm});
            skLineSegment(sketch, "E3073", {"start": v(34.9, 69.14) * mm, "end": v(33.57, 69.87) * mm});
            skLineSegment(sketch, "E3074", {"start": v(33.57, 69.87) * mm, "end": v(32.35, 70.75) * mm});
            skLineSegment(sketch, "E3075", {"start": v(32.35, 70.75) * mm, "end": v(31.25, 71.78) * mm});
            skLineSegment(sketch, "E3076", {"start": v(31.25, 71.78) * mm, "end": v(30.3, 72.95) * mm});
            skLineSegment(sketch, "E3077", {"start": v(30.3, 72.95) * mm, "end": v(29.48, 74.22) * mm});
            skLineSegment(sketch, "E3078", {"start": v(29.48, 74.22) * mm, "end": v(28.84, 75.58) * mm});
            skLineSegment(sketch, "E3079", {"start": v(28.84, 75.58) * mm, "end": v(28.38, 77.02) * mm});
            skLineSegment(sketch, "E3080", {"start": v(28.38, 77.02) * mm, "end": v(28.1, 78.5) * mm});
            skLineSegment(sketch, "E3081", {"start": v(28.1, 78.5) * mm, "end": v(28, 80) * mm});
            skLineSegment(sketch, "E3082", {"start": v(28, 80) * mm, "end": v(28.1, 81.5) * mm});
            skLineSegment(sketch, "E3083", {"start": v(28.1, 81.5) * mm, "end": v(28.38, 82.98) * mm});
            skLineSegment(sketch, "E3084", {"start": v(28.38, 82.98) * mm, "end": v(28.84, 84.42) * mm});
            skLineSegment(sketch, "E3085", {"start": v(28.84, 84.42) * mm, "end": v(29.48, 85.78) * mm});
            skLineSegment(sketch, "E3086", {"start": v(29.48, 85.78) * mm, "end": v(30.3, 87.05) * mm});
            skLineSegment(sketch, "E3087", {"start": v(30.3, 87.05) * mm, "end": v(31.25, 88.22) * mm});
            skLineSegment(sketch, "E3088", {"start": v(31.25, 88.22) * mm, "end": v(32.35, 89.25) * mm});
            skLineSegment(sketch, "E3089", {"start": v(32.35, 89.25) * mm, "end": v(33.57, 90.13) * mm});
            skLineSegment(sketch, "E3090", {"start": v(33.57, 90.13) * mm, "end": v(34.9, 90.86) * mm});
            skLineSegment(sketch, "E3091", {"start": v(34.9, 90.86) * mm, "end": v(36.3, 91.41) * mm});
            skLineSegment(sketch, "E3092", {"start": v(36.3, 91.41) * mm, "end": v(37.75, 91.79) * mm});
            skLineSegment(sketch, "E3093", {"start": v(37.75, 91.79) * mm, "end": v(39.25, 91.98) * mm});
            skLineSegment(sketch, "E3094", {"start": v(39.25, 91.98) * mm, "end": v(40.75, 91.98) * mm});
            skLineSegment(sketch, "E3095", {"start": v(40.75, 91.98) * mm, "end": v(42.25, 91.79) * mm});
            skLineSegment(sketch, "E3096", {"start": v(42.25, 91.79) * mm, "end": v(43.7, 91.41) * mm});
            skLineSegment(sketch, "E3097", {"start": v(43.7, 91.41) * mm, "end": v(45.1, 90.86) * mm});
            skLineSegment(sketch, "E3098", {"start": v(45.1, 90.86) * mm, "end": v(46.43, 90.13) * mm});
            skLineSegment(sketch, "E3099", {"start": v(46.43, 90.13) * mm, "end": v(47.65, 89.25) * mm});
            skLineSegment(sketch, "E3100", {"start": v(47.65, 89.25) * mm, "end": v(48.75, 88.22) * mm});
            skLineSegment(sketch, "E3101", {"start": v(48.75, 88.22) * mm, "end": v(49.7, 87.05) * mm});
            skLineSegment(sketch, "E3102", {"start": v(49.7, 87.05) * mm, "end": v(50.52, 85.78) * mm});
            skLineSegment(sketch, "E3103", {"start": v(50.52, 85.78) * mm, "end": v(51.16, 84.42) * mm});
            skLineSegment(sketch, "E3104", {"start": v(51.16, 84.42) * mm, "end": v(51.62, 82.98) * mm});
            skLineSegment(sketch, "E3105", {"start": v(51.62, 82.98) * mm, "end": v(51.9, 81.5) * mm});
            skLineSegment(sketch, "E3106", {"start": v(51.9, 81.5) * mm, "end": v(52, 80) * mm});
            skLineSegment(sketch, "E3107", {"start": v(52, 80) * mm, "end": v(51.9, 78.5) * mm});
            skLineSegment(sketch, "E3108", {"start": v(51.9, 78.5) * mm, "end": v(51.62, 77.02) * mm});
            skLineSegment(sketch, "E3109", {"start": v(51.62, 77.02) * mm, "end": v(51.16, 75.58) * mm});
            skLineSegment(sketch, "E3110", {"start": v(51.16, 75.58) * mm, "end": v(50.52, 74.22) * mm});
            skLineSegment(sketch, "E3111", {"start": v(50.52, 74.22) * mm, "end": v(49.7, 72.95) * mm});
            skLineSegment(sketch, "E3112", {"start": v(49.7, 72.95) * mm, "end": v(48.75, 71.78) * mm});
            skLineSegment(sketch, "E3113", {"start": v(48.75, 71.78) * mm, "end": v(47.65, 70.75) * mm});
            skLineSegment(sketch, "E3114", {"start": v(47.65, 70.75) * mm, "end": v(46.43, 69.87) * mm});
            skLineSegment(sketch, "E3115", {"start": v(46.43, 69.87) * mm, "end": v(45.1, 69.14) * mm});
            skLineSegment(sketch, "E3116", {"start": v(45.1, 69.14) * mm, "end": v(43.7, 68.59) * mm});
            skLineSegment(sketch, "E3117", {"start": v(43.7, 68.59) * mm, "end": v(42.25, 68.21) * mm});
            skLineSegment(sketch, "E3118", {"start": v(42.25, 68.21) * mm, "end": v(40.75, 68.02) * mm});
            skLineSegment(sketch, "E3119", {"start": v(40.75, 68.02) * mm, "end": v(39.25, 68.02) * mm});
            skLineSegment(sketch, "E3120", {"start": v(369.25, 68.02) * mm, "end": v(367.75, 68.21) * mm});
            skLineSegment(sketch, "E3121", {"start": v(367.75, 68.21) * mm, "end": v(366.3, 68.59) * mm});
            skLineSegment(sketch, "E3122", {"start": v(366.3, 68.59) * mm, "end": v(364.9, 69.14) * mm});
            skLineSegment(sketch, "E3123", {"start": v(364.9, 69.14) * mm, "end": v(363.57, 69.87) * mm});
            skLineSegment(sketch, "E3124", {"start": v(363.57, 69.87) * mm, "end": v(362.35, 70.75) * mm});
            skLineSegment(sketch, "E3125", {"start": v(362.35, 70.75) * mm, "end": v(361.25, 71.78) * mm});
            skLineSegment(sketch, "E3126", {"start": v(361.25, 71.78) * mm, "end": v(360.3, 72.95) * mm});
            skLineSegment(sketch, "E3127", {"start": v(360.3, 72.95) * mm, "end": v(359.48, 74.22) * mm});
            skLineSegment(sketch, "E3128", {"start": v(359.48, 74.22) * mm, "end": v(358.84, 75.58) * mm});
            skLineSegment(sketch, "E3129", {"start": v(358.84, 75.58) * mm, "end": v(358.38, 77.02) * mm});
            skLineSegment(sketch, "E3130", {"start": v(358.38, 77.02) * mm, "end": v(358.1, 78.5) * mm});
            skLineSegment(sketch, "E3131", {"start": v(358.1, 78.5) * mm, "end": v(358, 80) * mm});
            skLineSegment(sketch, "E3132", {"start": v(358, 80) * mm, "end": v(358.1, 81.5) * mm});
            skLineSegment(sketch, "E3133", {"start": v(358.1, 81.5) * mm, "end": v(358.38, 82.98) * mm});
            skLineSegment(sketch, "E3134", {"start": v(358.38, 82.98) * mm, "end": v(358.84, 84.42) * mm});
            skLineSegment(sketch, "E3135", {"start": v(358.84, 84.42) * mm, "end": v(359.48, 85.78) * mm});
            skLineSegment(sketch, "E3136", {"start": v(359.48, 85.78) * mm, "end": v(360.3, 87.05) * mm});
            skLineSegment(sketch, "E3137", {"start": v(360.3, 87.05) * mm, "end": v(361.25, 88.22) * mm});
            skLineSegment(sketch, "E3138", {"start": v(361.25, 88.22) * mm, "end": v(362.35, 89.25) * mm});
            skLineSegment(sketch, "E3139", {"start": v(362.35, 89.25) * mm, "end": v(363.57, 90.13) * mm});
            skLineSegment(sketch, "E3140", {"start": v(363.57, 90.13) * mm, "end": v(364.9, 90.86) * mm});
            skLineSegment(sketch, "E3141", {"start": v(364.9, 90.86) * mm, "end": v(366.3, 91.41) * mm});
            skLineSegment(sketch, "E3142", {"start": v(366.3, 91.41) * mm, "end": v(367.75, 91.79) * mm});
            skLineSegment(sketch, "E3143", {"start": v(367.75, 91.79) * mm, "end": v(369.25, 91.98) * mm});
            skLineSegment(sketch, "E3144", {"start": v(369.25, 91.98) * mm, "end": v(370.75, 91.98) * mm});
            skLineSegment(sketch, "E3145", {"start": v(370.75, 91.98) * mm, "end": v(372.25, 91.79) * mm});
            skLineSegment(sketch, "E3146", {"start": v(372.25, 91.79) * mm, "end": v(373.7, 91.41) * mm});
            skLineSegment(sketch, "E3147", {"start": v(373.7, 91.41) * mm, "end": v(375.1, 90.86) * mm});
            skLineSegment(sketch, "E3148", {"start": v(375.1, 90.86) * mm, "end": v(376.43, 90.13) * mm});
            skLineSegment(sketch, "E3149", {"start": v(376.43, 90.13) * mm, "end": v(377.65, 89.25) * mm});
            skLineSegment(sketch, "E3150", {"start": v(377.65, 89.25) * mm, "end": v(378.75, 88.22) * mm});
            skLineSegment(sketch, "E3151", {"start": v(378.75, 88.22) * mm, "end": v(379.7, 87.05) * mm});
            skLineSegment(sketch, "E3152", {"start": v(379.7, 87.05) * mm, "end": v(380.52, 85.78) * mm});
            skLineSegment(sketch, "E3153", {"start": v(380.52, 85.78) * mm, "end": v(381.16, 84.42) * mm});
            skLineSegment(sketch, "E3154", {"start": v(381.16, 84.42) * mm, "end": v(381.62, 82.98) * mm});
            skLineSegment(sketch, "E3155", {"start": v(381.62, 82.98) * mm, "end": v(381.9, 81.5) * mm});
            skLineSegment(sketch, "E3156", {"start": v(381.9, 81.5) * mm, "end": v(382, 80) * mm});
            skLineSegment(sketch, "E3157", {"start": v(382, 80) * mm, "end": v(381.9, 78.5) * mm});
            skLineSegment(sketch, "E3158", {"start": v(381.9, 78.5) * mm, "end": v(381.62, 77.02) * mm});
            skLineSegment(sketch, "E3159", {"start": v(381.62, 77.02) * mm, "end": v(381.16, 75.58) * mm});
            skLineSegment(sketch, "E3160", {"start": v(381.16, 75.58) * mm, "end": v(380.52, 74.22) * mm});
            skLineSegment(sketch, "E3161", {"start": v(380.52, 74.22) * mm, "end": v(379.7, 72.95) * mm});
            skLineSegment(sketch, "E3162", {"start": v(379.7, 72.95) * mm, "end": v(378.75, 71.78) * mm});
            skLineSegment(sketch, "E3163", {"start": v(378.75, 71.78) * mm, "end": v(377.65, 70.75) * mm});
            skLineSegment(sketch, "E3164", {"start": v(377.65, 70.75) * mm, "end": v(376.43, 69.87) * mm});
            skLineSegment(sketch, "E3165", {"start": v(376.43, 69.87) * mm, "end": v(375.1, 69.14) * mm});
            skLineSegment(sketch, "E3166", {"start": v(375.1, 69.14) * mm, "end": v(373.7, 68.59) * mm});
            skLineSegment(sketch, "E3167", {"start": v(373.7, 68.59) * mm, "end": v(372.25, 68.21) * mm});
            skLineSegment(sketch, "E3168", {"start": v(372.25, 68.21) * mm, "end": v(370.75, 68.02) * mm});
            skLineSegment(sketch, "E3169", {"start": v(370.75, 68.02) * mm, "end": v(369.25, 68.02) * mm});
            skLineSegment(sketch, "E3170", {"start": v(386.75, 76) * mm, "end": v(386.25, 76.07) * mm});
            skLineSegment(sketch, "E3171", {"start": v(386.25, 76.07) * mm, "end": v(385.76, 76.2) * mm});
            skLineSegment(sketch, "E3172", {"start": v(385.76, 76.2) * mm, "end": v(385.3, 76.38) * mm});
            skLineSegment(sketch, "E3173", {"start": v(385.3, 76.38) * mm, "end": v(384.86, 76.62) * mm});
            skLineSegment(sketch, "E3174", {"start": v(384.86, 76.62) * mm, "end": v(384.45, 76.92) * mm});
            skLineSegment(sketch, "E3175", {"start": v(384.45, 76.92) * mm, "end": v(384.08, 77.26) * mm});
            skLineSegment(sketch, "E3176", {"start": v(384.08, 77.26) * mm, "end": v(383.76, 77.65) * mm});
            skLineSegment(sketch, "E3177", {"start": v(383.76, 77.65) * mm, "end": v(383.5, 78.07) * mm});
            skLineSegment(sketch, "E3178", {"start": v(383.5, 78.07) * mm, "end": v(383.28, 78.53) * mm});
            skLineSegment(sketch, "E3179", {"start": v(383.28, 78.53) * mm, "end": v(383.13, 79) * mm});
            skLineSegment(sketch, "E3180", {"start": v(383.13, 79) * mm, "end": v(383.03, 79.5) * mm});
            skLineSegment(sketch, "E3181", {"start": v(383.03, 79.5) * mm, "end": v(383, 80) * mm});
            skLineSegment(sketch, "E3182", {"start": v(383, 80) * mm, "end": v(383.03, 80.5) * mm});
            skLineSegment(sketch, "E3183", {"start": v(383.03, 80.5) * mm, "end": v(383.13, 81) * mm});
            skLineSegment(sketch, "E3184", {"start": v(383.13, 81) * mm, "end": v(383.28, 81.47) * mm});
            skLineSegment(sketch, "E3185", {"start": v(383.28, 81.47) * mm, "end": v(383.5, 81.93) * mm});
            skLineSegment(sketch, "E3186", {"start": v(383.5, 81.93) * mm, "end": v(383.76, 82.35) * mm});
            skLineSegment(sketch, "E3187", {"start": v(383.76, 82.35) * mm, "end": v(384.08, 82.74) * mm});
            skLineSegment(sketch, "E3188", {"start": v(384.08, 82.74) * mm, "end": v(384.45, 83.08) * mm});
            skLineSegment(sketch, "E3189", {"start": v(384.45, 83.08) * mm, "end": v(384.86, 83.38) * mm});
            skLineSegment(sketch, "E3190", {"start": v(384.86, 83.38) * mm, "end": v(385.3, 83.62) * mm});
            skLineSegment(sketch, "E3191", {"start": v(385.3, 83.62) * mm, "end": v(385.76, 83.8) * mm});
            skLineSegment(sketch, "E3192", {"start": v(385.76, 83.8) * mm, "end": v(386.25, 83.93) * mm});
            skLineSegment(sketch, "E3193", {"start": v(386.25, 83.93) * mm, "end": v(386.75, 84) * mm});
            skLineSegment(sketch, "E3194", {"start": v(386.75, 84) * mm, "end": v(387.25, 84) * mm});
            skLineSegment(sketch, "E3195", {"start": v(387.25, 84) * mm, "end": v(387.75, 83.93) * mm});
            skLineSegment(sketch, "E3196", {"start": v(387.75, 83.93) * mm, "end": v(388.24, 83.8) * mm});
            skLineSegment(sketch, "E3197", {"start": v(388.24, 83.8) * mm, "end": v(388.7, 83.62) * mm});
            skLineSegment(sketch, "E3198", {"start": v(388.7, 83.62) * mm, "end": v(389.14, 83.38) * mm});
            skLineSegment(sketch, "E3199", {"start": v(389.14, 83.38) * mm, "end": v(389.55, 83.08) * mm});
            skLineSegment(sketch, "E3200", {"start": v(389.55, 83.08) * mm, "end": v(389.92, 82.74) * mm});
            skLineSegment(sketch, "E3201", {"start": v(389.92, 82.74) * mm, "end": v(390.24, 82.35) * mm});
            skLineSegment(sketch, "E3202", {"start": v(390.24, 82.35) * mm, "end": v(390.5, 81.93) * mm});
            skLineSegment(sketch, "E3203", {"start": v(390.5, 81.93) * mm, "end": v(390.72, 81.47) * mm});
            skLineSegment(sketch, "E3204", {"start": v(390.72, 81.47) * mm, "end": v(390.87, 81) * mm});
            skLineSegment(sketch, "E3205", {"start": v(390.87, 81) * mm, "end": v(390.97, 80.5) * mm});
            skLineSegment(sketch, "E3206", {"start": v(390.97, 80.5) * mm, "end": v(391, 80) * mm});
            skLineSegment(sketch, "E3207", {"start": v(391, 80) * mm, "end": v(390.97, 79.5) * mm});
            skLineSegment(sketch, "E3208", {"start": v(390.97, 79.5) * mm, "end": v(390.87, 79) * mm});
            skLineSegment(sketch, "E3209", {"start": v(390.87, 79) * mm, "end": v(390.72, 78.53) * mm});
            skLineSegment(sketch, "E3210", {"start": v(390.72, 78.53) * mm, "end": v(390.5, 78.07) * mm});
            skLineSegment(sketch, "E3211", {"start": v(390.5, 78.07) * mm, "end": v(390.24, 77.65) * mm});
            skLineSegment(sketch, "E3212", {"start": v(390.24, 77.65) * mm, "end": v(389.92, 77.26) * mm});
            skLineSegment(sketch, "E3213", {"start": v(389.92, 77.26) * mm, "end": v(389.55, 76.92) * mm});
            skLineSegment(sketch, "E3214", {"start": v(389.55, 76.92) * mm, "end": v(389.14, 76.62) * mm});
            skLineSegment(sketch, "E3215", {"start": v(389.14, 76.62) * mm, "end": v(388.7, 76.38) * mm});
            skLineSegment(sketch, "E3216", {"start": v(388.7, 76.38) * mm, "end": v(388.24, 76.2) * mm});
            skLineSegment(sketch, "E3217", {"start": v(388.24, 76.2) * mm, "end": v(387.75, 76.07) * mm});
            skLineSegment(sketch, "E3218", {"start": v(387.75, 76.07) * mm, "end": v(387.25, 76) * mm});
            skLineSegment(sketch, "E3219", {"start": v(387.25, 76) * mm, "end": v(386.75, 76) * mm});
            skLineSegment(sketch, "E3220", {"start": v(22.75, 76) * mm, "end": v(22.25, 76.07) * mm});
            skLineSegment(sketch, "E3221", {"start": v(22.25, 76.07) * mm, "end": v(21.76, 76.2) * mm});
            skLineSegment(sketch, "E3222", {"start": v(21.76, 76.2) * mm, "end": v(21.3, 76.38) * mm});
            skLineSegment(sketch, "E3223", {"start": v(21.3, 76.38) * mm, "end": v(20.86, 76.62) * mm});
            skLineSegment(sketch, "E3224", {"start": v(20.86, 76.62) * mm, "end": v(20.45, 76.92) * mm});
            skLineSegment(sketch, "E3225", {"start": v(20.45, 76.92) * mm, "end": v(20.08, 77.26) * mm});
            skLineSegment(sketch, "E3226", {"start": v(20.08, 77.26) * mm, "end": v(19.76, 77.65) * mm});
            skLineSegment(sketch, "E3227", {"start": v(19.76, 77.65) * mm, "end": v(19.5, 78.07) * mm});
            skLineSegment(sketch, "E3228", {"start": v(19.5, 78.07) * mm, "end": v(19.28, 78.53) * mm});
            skLineSegment(sketch, "E3229", {"start": v(19.28, 78.53) * mm, "end": v(19.13, 79) * mm});
            skLineSegment(sketch, "E3230", {"start": v(19.13, 79) * mm, "end": v(19.03, 79.5) * mm});
            skLineSegment(sketch, "E3231", {"start": v(19.03, 79.5) * mm, "end": v(19, 80) * mm});
            skLineSegment(sketch, "E3232", {"start": v(19, 80) * mm, "end": v(19.03, 80.5) * mm});
            skLineSegment(sketch, "E3233", {"start": v(19.03, 80.5) * mm, "end": v(19.13, 81) * mm});
            skLineSegment(sketch, "E3234", {"start": v(19.13, 81) * mm, "end": v(19.28, 81.47) * mm});
            skLineSegment(sketch, "E3235", {"start": v(19.28, 81.47) * mm, "end": v(19.5, 81.93) * mm});
            skLineSegment(sketch, "E3236", {"start": v(19.5, 81.93) * mm, "end": v(19.76, 82.35) * mm});
            skLineSegment(sketch, "E3237", {"start": v(19.76, 82.35) * mm, "end": v(20.08, 82.74) * mm});
            skLineSegment(sketch, "E3238", {"start": v(20.08, 82.74) * mm, "end": v(20.45, 83.08) * mm});
            skLineSegment(sketch, "E3239", {"start": v(20.45, 83.08) * mm, "end": v(20.86, 83.38) * mm});
            skLineSegment(sketch, "E3240", {"start": v(20.86, 83.38) * mm, "end": v(21.3, 83.62) * mm});
            skLineSegment(sketch, "E3241", {"start": v(21.3, 83.62) * mm, "end": v(21.76, 83.8) * mm});
            skLineSegment(sketch, "E3242", {"start": v(21.76, 83.8) * mm, "end": v(22.25, 83.93) * mm});
            skLineSegment(sketch, "E3243", {"start": v(22.25, 83.93) * mm, "end": v(22.75, 84) * mm});
            skLineSegment(sketch, "E3244", {"start": v(22.75, 84) * mm, "end": v(23.25, 84) * mm});
            skLineSegment(sketch, "E3245", {"start": v(23.25, 84) * mm, "end": v(23.75, 83.93) * mm});
            skLineSegment(sketch, "E3246", {"start": v(23.75, 83.93) * mm, "end": v(24.24, 83.8) * mm});
            skLineSegment(sketch, "E3247", {"start": v(24.24, 83.8) * mm, "end": v(24.7, 83.62) * mm});
            skLineSegment(sketch, "E3248", {"start": v(24.7, 83.62) * mm, "end": v(25.14, 83.38) * mm});
            skLineSegment(sketch, "E3249", {"start": v(25.14, 83.38) * mm, "end": v(25.55, 83.08) * mm});
            skLineSegment(sketch, "E3250", {"start": v(25.55, 83.08) * mm, "end": v(25.92, 82.74) * mm});
            skLineSegment(sketch, "E3251", {"start": v(25.92, 82.74) * mm, "end": v(26.24, 82.35) * mm});
            skLineSegment(sketch, "E3252", {"start": v(26.24, 82.35) * mm, "end": v(26.5, 81.93) * mm});
            skLineSegment(sketch, "E3253", {"start": v(26.5, 81.93) * mm, "end": v(26.72, 81.47) * mm});
            skLineSegment(sketch, "E3254", {"start": v(26.72, 81.47) * mm, "end": v(26.87, 81) * mm});
            skLineSegment(sketch, "E3255", {"start": v(26.87, 81) * mm, "end": v(26.97, 80.5) * mm});
            skLineSegment(sketch, "E3256", {"start": v(26.97, 80.5) * mm, "end": v(27, 80) * mm});
            skLineSegment(sketch, "E3257", {"start": v(27, 80) * mm, "end": v(26.97, 79.5) * mm});
            skLineSegment(sketch, "E3258", {"start": v(26.97, 79.5) * mm, "end": v(26.87, 79) * mm});
            skLineSegment(sketch, "E3259", {"start": v(26.87, 79) * mm, "end": v(26.72, 78.53) * mm});
            skLineSegment(sketch, "E3260", {"start": v(26.72, 78.53) * mm, "end": v(26.5, 78.07) * mm});
            skLineSegment(sketch, "E3261", {"start": v(26.5, 78.07) * mm, "end": v(26.24, 77.65) * mm});
            skLineSegment(sketch, "E3262", {"start": v(26.24, 77.65) * mm, "end": v(25.92, 77.26) * mm});
            skLineSegment(sketch, "E3263", {"start": v(25.92, 77.26) * mm, "end": v(25.55, 76.92) * mm});
            skLineSegment(sketch, "E3264", {"start": v(25.55, 76.92) * mm, "end": v(25.14, 76.62) * mm});
            skLineSegment(sketch, "E3265", {"start": v(25.14, 76.62) * mm, "end": v(24.7, 76.38) * mm});
            skLineSegment(sketch, "E3266", {"start": v(24.7, 76.38) * mm, "end": v(24.24, 76.2) * mm});
            skLineSegment(sketch, "E3267", {"start": v(24.24, 76.2) * mm, "end": v(23.75, 76.07) * mm});
            skLineSegment(sketch, "E3268", {"start": v(23.75, 76.07) * mm, "end": v(23.25, 76) * mm});
            skLineSegment(sketch, "E3269", {"start": v(23.25, 76) * mm, "end": v(22.75, 76) * mm});
            skLineSegment(sketch, "E3270", {"start": v(24.4, 63) * mm, "end": v(24.22, 63.03) * mm});
            skLineSegment(sketch, "E3271", {"start": v(24.22, 63.03) * mm, "end": v(24.04, 63.07) * mm});
            skLineSegment(sketch, "E3272", {"start": v(24.04, 63.07) * mm, "end": v(23.86, 63.14) * mm});
            skLineSegment(sketch, "E3273", {"start": v(23.86, 63.14) * mm, "end": v(23.7, 63.23) * mm});
            skLineSegment(sketch, "E3274", {"start": v(23.7, 63.23) * mm, "end": v(23.54, 63.34) * mm});
            skLineSegment(sketch, "E3275", {"start": v(23.54, 63.34) * mm, "end": v(23.4, 63.47) * mm});
            skLineSegment(sketch, "E3276", {"start": v(23.4, 63.47) * mm, "end": v(23.29, 63.62) * mm});
            skLineSegment(sketch, "E3277", {"start": v(23.29, 63.62) * mm, "end": v(23.19, 63.78) * mm});
            skLineSegment(sketch, "E3278", {"start": v(23.19, 63.78) * mm, "end": v(23.1, 63.95) * mm});
            skLineSegment(sketch, "E3279", {"start": v(23.1, 63.95) * mm, "end": v(23.05, 64.13) * mm});
            skLineSegment(sketch, "E3280", {"start": v(23.05, 64.13) * mm, "end": v(23.01, 64.31) * mm});
            skLineSegment(sketch, "E3281", {"start": v(23.01, 64.31) * mm, "end": v(23, 64.5) * mm});
            skLineSegment(sketch, "E3282", {"start": v(23, 64.5) * mm, "end": v(23.01, 64.69) * mm});
            skLineSegment(sketch, "E3283", {"start": v(23.01, 64.69) * mm, "end": v(23.05, 64.87) * mm});
            skLineSegment(sketch, "E3284", {"start": v(23.05, 64.87) * mm, "end": v(23.1, 65.05) * mm});
            skLineSegment(sketch, "E3285", {"start": v(23.1, 65.05) * mm, "end": v(23.19, 65.22) * mm});
            skLineSegment(sketch, "E3286", {"start": v(23.19, 65.22) * mm, "end": v(23.29, 65.38) * mm});
            skLineSegment(sketch, "E3287", {"start": v(23.29, 65.38) * mm, "end": v(23.4, 65.53) * mm});
            skLineSegment(sketch, "E3288", {"start": v(23.4, 65.53) * mm, "end": v(23.54, 65.66) * mm});
            skLineSegment(sketch, "E3289", {"start": v(23.54, 65.66) * mm, "end": v(23.7, 65.77) * mm});
            skLineSegment(sketch, "E3290", {"start": v(23.7, 65.77) * mm, "end": v(23.86, 65.86) * mm});
            skLineSegment(sketch, "E3291", {"start": v(23.86, 65.86) * mm, "end": v(24.04, 65.93) * mm});
            skLineSegment(sketch, "E3292", {"start": v(24.04, 65.93) * mm, "end": v(24.22, 65.97) * mm});
            skLineSegment(sketch, "E3293", {"start": v(24.22, 65.97) * mm, "end": v(24.4, 66) * mm});
            skLineSegment(sketch, "E3294", {"start": v(24.4, 66) * mm, "end": v(24.6, 66) * mm});
            skLineSegment(sketch, "E3295", {"start": v(24.6, 66) * mm, "end": v(24.78, 65.97) * mm});
            skLineSegment(sketch, "E3296", {"start": v(24.78, 65.97) * mm, "end": v(24.96, 65.93) * mm});
            skLineSegment(sketch, "E3297", {"start": v(24.96, 65.93) * mm, "end": v(25.14, 65.86) * mm});
            skLineSegment(sketch, "E3298", {"start": v(25.14, 65.86) * mm, "end": v(25.3, 65.77) * mm});
            skLineSegment(sketch, "E3299", {"start": v(25.3, 65.77) * mm, "end": v(25.46, 65.66) * mm});
            skLineSegment(sketch, "E3300", {"start": v(25.46, 65.66) * mm, "end": v(25.6, 65.53) * mm});
            skLineSegment(sketch, "E3301", {"start": v(25.6, 65.53) * mm, "end": v(25.71, 65.38) * mm});
            skLineSegment(sketch, "E3302", {"start": v(25.71, 65.38) * mm, "end": v(25.81, 65.22) * mm});
            skLineSegment(sketch, "E3303", {"start": v(25.81, 65.22) * mm, "end": v(25.9, 65.05) * mm});
            skLineSegment(sketch, "E3304", {"start": v(25.9, 65.05) * mm, "end": v(25.95, 64.87) * mm});
            skLineSegment(sketch, "E3305", {"start": v(25.95, 64.87) * mm, "end": v(25.99, 64.69) * mm});
            skLineSegment(sketch, "E3306", {"start": v(25.99, 64.69) * mm, "end": v(26, 64.5) * mm});
            skLineSegment(sketch, "E3307", {"start": v(26, 64.5) * mm, "end": v(25.99, 64.31) * mm});
            skLineSegment(sketch, "E3308", {"start": v(25.99, 64.31) * mm, "end": v(25.95, 64.13) * mm});
            skLineSegment(sketch, "E3309", {"start": v(25.95, 64.13) * mm, "end": v(25.9, 63.95) * mm});
            skLineSegment(sketch, "E3310", {"start": v(25.9, 63.95) * mm, "end": v(25.81, 63.78) * mm});
            skLineSegment(sketch, "E3311", {"start": v(25.81, 63.78) * mm, "end": v(25.71, 63.62) * mm});
            skLineSegment(sketch, "E3312", {"start": v(25.71, 63.62) * mm, "end": v(25.6, 63.47) * mm});
            skLineSegment(sketch, "E3313", {"start": v(25.6, 63.47) * mm, "end": v(25.46, 63.34) * mm});
            skLineSegment(sketch, "E3314", {"start": v(25.46, 63.34) * mm, "end": v(25.3, 63.23) * mm});
            skLineSegment(sketch, "E3315", {"start": v(25.3, 63.23) * mm, "end": v(25.14, 63.14) * mm});
            skLineSegment(sketch, "E3316", {"start": v(25.14, 63.14) * mm, "end": v(24.96, 63.07) * mm});
            skLineSegment(sketch, "E3317", {"start": v(24.96, 63.07) * mm, "end": v(24.78, 63.03) * mm});
            skLineSegment(sketch, "E3318", {"start": v(24.78, 63.03) * mm, "end": v(24.6, 63) * mm});
            skLineSegment(sketch, "E3319", {"start": v(24.6, 63) * mm, "end": v(24.4, 63) * mm});
            skLineSegment(sketch, "E3320", {"start": v(55.4, 63) * mm, "end": v(55.22, 63.03) * mm});
            skLineSegment(sketch, "E3321", {"start": v(55.22, 63.03) * mm, "end": v(55.04, 63.07) * mm});
            skLineSegment(sketch, "E3322", {"start": v(55.04, 63.07) * mm, "end": v(54.86, 63.14) * mm});
            skLineSegment(sketch, "E3323", {"start": v(54.86, 63.14) * mm, "end": v(54.7, 63.23) * mm});
            skLineSegment(sketch, "E3324", {"start": v(54.7, 63.23) * mm, "end": v(54.54, 63.34) * mm});
            skLineSegment(sketch, "E3325", {"start": v(54.54, 63.34) * mm, "end": v(54.4, 63.47) * mm});
            skLineSegment(sketch, "E3326", {"start": v(54.4, 63.47) * mm, "end": v(54.29, 63.62) * mm});
            skLineSegment(sketch, "E3327", {"start": v(54.29, 63.62) * mm, "end": v(54.19, 63.78) * mm});
            skLineSegment(sketch, "E3328", {"start": v(54.19, 63.78) * mm, "end": v(54.1, 63.95) * mm});
            skLineSegment(sketch, "E3329", {"start": v(54.1, 63.95) * mm, "end": v(54.05, 64.13) * mm});
            skLineSegment(sketch, "E3330", {"start": v(54.05, 64.13) * mm, "end": v(54.01, 64.31) * mm});
            skLineSegment(sketch, "E3331", {"start": v(54.01, 64.31) * mm, "end": v(54, 64.5) * mm});
            skLineSegment(sketch, "E3332", {"start": v(54, 64.5) * mm, "end": v(54.01, 64.69) * mm});
            skLineSegment(sketch, "E3333", {"start": v(54.01, 64.69) * mm, "end": v(54.05, 64.87) * mm});
            skLineSegment(sketch, "E3334", {"start": v(54.05, 64.87) * mm, "end": v(54.1, 65.05) * mm});
            skLineSegment(sketch, "E3335", {"start": v(54.1, 65.05) * mm, "end": v(54.19, 65.22) * mm});
            skLineSegment(sketch, "E3336", {"start": v(54.19, 65.22) * mm, "end": v(54.29, 65.38) * mm});
            skLineSegment(sketch, "E3337", {"start": v(54.29, 65.38) * mm, "end": v(54.4, 65.53) * mm});
            skLineSegment(sketch, "E3338", {"start": v(54.4, 65.53) * mm, "end": v(54.54, 65.66) * mm});
            skLineSegment(sketch, "E3339", {"start": v(54.54, 65.66) * mm, "end": v(54.7, 65.77) * mm});
            skLineSegment(sketch, "E3340", {"start": v(54.7, 65.77) * mm, "end": v(54.86, 65.86) * mm});
            skLineSegment(sketch, "E3341", {"start": v(54.86, 65.86) * mm, "end": v(55.04, 65.93) * mm});
            skLineSegment(sketch, "E3342", {"start": v(55.04, 65.93) * mm, "end": v(55.22, 65.97) * mm});
            skLineSegment(sketch, "E3343", {"start": v(55.22, 65.97) * mm, "end": v(55.4, 66) * mm});
            skLineSegment(sketch, "E3344", {"start": v(55.4, 66) * mm, "end": v(55.6, 66) * mm});
            skLineSegment(sketch, "E3345", {"start": v(55.6, 66) * mm, "end": v(55.78, 65.97) * mm});
            skLineSegment(sketch, "E3346", {"start": v(55.78, 65.97) * mm, "end": v(55.96, 65.93) * mm});
            skLineSegment(sketch, "E3347", {"start": v(55.96, 65.93) * mm, "end": v(56.14, 65.86) * mm});
            skLineSegment(sketch, "E3348", {"start": v(56.14, 65.86) * mm, "end": v(56.3, 65.77) * mm});
            skLineSegment(sketch, "E3349", {"start": v(56.3, 65.77) * mm, "end": v(56.46, 65.66) * mm});
            skLineSegment(sketch, "E3350", {"start": v(56.46, 65.66) * mm, "end": v(56.6, 65.53) * mm});
            skLineSegment(sketch, "E3351", {"start": v(56.6, 65.53) * mm, "end": v(56.71, 65.38) * mm});
            skLineSegment(sketch, "E3352", {"start": v(56.71, 65.38) * mm, "end": v(56.81, 65.22) * mm});
            skLineSegment(sketch, "E3353", {"start": v(56.81, 65.22) * mm, "end": v(56.9, 65.05) * mm});
            skLineSegment(sketch, "E3354", {"start": v(56.9, 65.05) * mm, "end": v(56.95, 64.87) * mm});
            skLineSegment(sketch, "E3355", {"start": v(56.95, 64.87) * mm, "end": v(56.99, 64.69) * mm});
            skLineSegment(sketch, "E3356", {"start": v(56.99, 64.69) * mm, "end": v(57, 64.5) * mm});
            skLineSegment(sketch, "E3357", {"start": v(57, 64.5) * mm, "end": v(56.99, 64.31) * mm});
            skLineSegment(sketch, "E3358", {"start": v(56.99, 64.31) * mm, "end": v(56.95, 64.13) * mm});
            skLineSegment(sketch, "E3359", {"start": v(56.95, 64.13) * mm, "end": v(56.9, 63.95) * mm});
            skLineSegment(sketch, "E3360", {"start": v(56.9, 63.95) * mm, "end": v(56.81, 63.78) * mm});
            skLineSegment(sketch, "E3361", {"start": v(56.81, 63.78) * mm, "end": v(56.71, 63.62) * mm});
            skLineSegment(sketch, "E3362", {"start": v(56.71, 63.62) * mm, "end": v(56.6, 63.47) * mm});
            skLineSegment(sketch, "E3363", {"start": v(56.6, 63.47) * mm, "end": v(56.46, 63.34) * mm});
            skLineSegment(sketch, "E3364", {"start": v(56.46, 63.34) * mm, "end": v(56.3, 63.23) * mm});
            skLineSegment(sketch, "E3365", {"start": v(56.3, 63.23) * mm, "end": v(56.14, 63.14) * mm});
            skLineSegment(sketch, "E3366", {"start": v(56.14, 63.14) * mm, "end": v(55.96, 63.07) * mm});
            skLineSegment(sketch, "E3367", {"start": v(55.96, 63.07) * mm, "end": v(55.78, 63.03) * mm});
            skLineSegment(sketch, "E3368", {"start": v(55.78, 63.03) * mm, "end": v(55.6, 63) * mm});
            skLineSegment(sketch, "E3369", {"start": v(55.6, 63) * mm, "end": v(55.4, 63) * mm});
            skLineSegment(sketch, "E3370", {"start": v(354.4, 63) * mm, "end": v(354.22, 63.03) * mm});
            skLineSegment(sketch, "E3371", {"start": v(354.22, 63.03) * mm, "end": v(354.04, 63.07) * mm});
            skLineSegment(sketch, "E3372", {"start": v(354.04, 63.07) * mm, "end": v(353.86, 63.14) * mm});
            skLineSegment(sketch, "E3373", {"start": v(353.86, 63.14) * mm, "end": v(353.7, 63.23) * mm});
            skLineSegment(sketch, "E3374", {"start": v(353.7, 63.23) * mm, "end": v(353.54, 63.34) * mm});
            skLineSegment(sketch, "E3375", {"start": v(353.54, 63.34) * mm, "end": v(353.4, 63.47) * mm});
            skLineSegment(sketch, "E3376", {"start": v(353.4, 63.47) * mm, "end": v(353.29, 63.62) * mm});
            skLineSegment(sketch, "E3377", {"start": v(353.29, 63.62) * mm, "end": v(353.19, 63.78) * mm});
            skLineSegment(sketch, "E3378", {"start": v(353.19, 63.78) * mm, "end": v(353.1, 63.95) * mm});
            skLineSegment(sketch, "E3379", {"start": v(353.1, 63.95) * mm, "end": v(353.05, 64.13) * mm});
            skLineSegment(sketch, "E3380", {"start": v(353.05, 64.13) * mm, "end": v(353.01, 64.31) * mm});
            skLineSegment(sketch, "E3381", {"start": v(353.01, 64.31) * mm, "end": v(353, 64.5) * mm});
            skLineSegment(sketch, "E3382", {"start": v(353, 64.5) * mm, "end": v(353.01, 64.69) * mm});
            skLineSegment(sketch, "E3383", {"start": v(353.01, 64.69) * mm, "end": v(353.05, 64.87) * mm});
            skLineSegment(sketch, "E3384", {"start": v(353.05, 64.87) * mm, "end": v(353.1, 65.05) * mm});
            skLineSegment(sketch, "E3385", {"start": v(353.1, 65.05) * mm, "end": v(353.19, 65.22) * mm});
            skLineSegment(sketch, "E3386", {"start": v(353.19, 65.22) * mm, "end": v(353.29, 65.38) * mm});
            skLineSegment(sketch, "E3387", {"start": v(353.29, 65.38) * mm, "end": v(353.4, 65.53) * mm});
            skLineSegment(sketch, "E3388", {"start": v(353.4, 65.53) * mm, "end": v(353.54, 65.66) * mm});
            skLineSegment(sketch, "E3389", {"start": v(353.54, 65.66) * mm, "end": v(353.7, 65.77) * mm});
            skLineSegment(sketch, "E3390", {"start": v(353.7, 65.77) * mm, "end": v(353.86, 65.86) * mm});
            skLineSegment(sketch, "E3391", {"start": v(353.86, 65.86) * mm, "end": v(354.04, 65.93) * mm});
            skLineSegment(sketch, "E3392", {"start": v(354.04, 65.93) * mm, "end": v(354.22, 65.97) * mm});
            skLineSegment(sketch, "E3393", {"start": v(354.22, 65.97) * mm, "end": v(354.4, 66) * mm});
            skLineSegment(sketch, "E3394", {"start": v(354.4, 66) * mm, "end": v(354.6, 66) * mm});
            skLineSegment(sketch, "E3395", {"start": v(354.6, 66) * mm, "end": v(354.78, 65.97) * mm});
            skLineSegment(sketch, "E3396", {"start": v(354.78, 65.97) * mm, "end": v(354.96, 65.93) * mm});
            skLineSegment(sketch, "E3397", {"start": v(354.96, 65.93) * mm, "end": v(355.14, 65.86) * mm});
            skLineSegment(sketch, "E3398", {"start": v(355.14, 65.86) * mm, "end": v(355.3, 65.77) * mm});
            skLineSegment(sketch, "E3399", {"start": v(355.3, 65.77) * mm, "end": v(355.46, 65.66) * mm});
            skLineSegment(sketch, "E3400", {"start": v(355.46, 65.66) * mm, "end": v(355.6, 65.53) * mm});
            skLineSegment(sketch, "E3401", {"start": v(355.6, 65.53) * mm, "end": v(355.71, 65.38) * mm});
            skLineSegment(sketch, "E3402", {"start": v(355.71, 65.38) * mm, "end": v(355.81, 65.22) * mm});
            skLineSegment(sketch, "E3403", {"start": v(355.81, 65.22) * mm, "end": v(355.9, 65.05) * mm});
            skLineSegment(sketch, "E3404", {"start": v(355.9, 65.05) * mm, "end": v(355.95, 64.87) * mm});
            skLineSegment(sketch, "E3405", {"start": v(355.95, 64.87) * mm, "end": v(355.99, 64.69) * mm});
            skLineSegment(sketch, "E3406", {"start": v(355.99, 64.69) * mm, "end": v(356, 64.5) * mm});
            skLineSegment(sketch, "E3407", {"start": v(356, 64.5) * mm, "end": v(355.99, 64.31) * mm});
            skLineSegment(sketch, "E3408", {"start": v(355.99, 64.31) * mm, "end": v(355.95, 64.13) * mm});
            skLineSegment(sketch, "E3409", {"start": v(355.95, 64.13) * mm, "end": v(355.9, 63.95) * mm});
            skLineSegment(sketch, "E3410", {"start": v(355.9, 63.95) * mm, "end": v(355.81, 63.78) * mm});
            skLineSegment(sketch, "E3411", {"start": v(355.81, 63.78) * mm, "end": v(355.71, 63.62) * mm});
            skLineSegment(sketch, "E3412", {"start": v(355.71, 63.62) * mm, "end": v(355.6, 63.47) * mm});
            skLineSegment(sketch, "E3413", {"start": v(355.6, 63.47) * mm, "end": v(355.46, 63.34) * mm});
            skLineSegment(sketch, "E3414", {"start": v(355.46, 63.34) * mm, "end": v(355.3, 63.23) * mm});
            skLineSegment(sketch, "E3415", {"start": v(355.3, 63.23) * mm, "end": v(355.14, 63.14) * mm});
            skLineSegment(sketch, "E3416", {"start": v(355.14, 63.14) * mm, "end": v(354.96, 63.07) * mm});
            skLineSegment(sketch, "E3417", {"start": v(354.96, 63.07) * mm, "end": v(354.78, 63.03) * mm});
            skLineSegment(sketch, "E3418", {"start": v(354.78, 63.03) * mm, "end": v(354.6, 63) * mm});
            skLineSegment(sketch, "E3419", {"start": v(354.6, 63) * mm, "end": v(354.4, 63) * mm});
            skLineSegment(sketch, "E3420", {"start": v(385.4, 63) * mm, "end": v(385.22, 63.03) * mm});
            skLineSegment(sketch, "E3421", {"start": v(385.22, 63.03) * mm, "end": v(385.04, 63.07) * mm});
            skLineSegment(sketch, "E3422", {"start": v(385.04, 63.07) * mm, "end": v(384.86, 63.14) * mm});
            skLineSegment(sketch, "E3423", {"start": v(384.86, 63.14) * mm, "end": v(384.7, 63.23) * mm});
            skLineSegment(sketch, "E3424", {"start": v(384.7, 63.23) * mm, "end": v(384.54, 63.34) * mm});
            skLineSegment(sketch, "E3425", {"start": v(384.54, 63.34) * mm, "end": v(384.4, 63.47) * mm});
            skLineSegment(sketch, "E3426", {"start": v(384.4, 63.47) * mm, "end": v(384.29, 63.62) * mm});
            skLineSegment(sketch, "E3427", {"start": v(384.29, 63.62) * mm, "end": v(384.19, 63.78) * mm});
            skLineSegment(sketch, "E3428", {"start": v(384.19, 63.78) * mm, "end": v(384.1, 63.95) * mm});
            skLineSegment(sketch, "E3429", {"start": v(384.1, 63.95) * mm, "end": v(384.05, 64.13) * mm});
            skLineSegment(sketch, "E3430", {"start": v(384.05, 64.13) * mm, "end": v(384.01, 64.31) * mm});
            skLineSegment(sketch, "E3431", {"start": v(384.01, 64.31) * mm, "end": v(384, 64.5) * mm});
            skLineSegment(sketch, "E3432", {"start": v(384, 64.5) * mm, "end": v(384.01, 64.69) * mm});
            skLineSegment(sketch, "E3433", {"start": v(384.01, 64.69) * mm, "end": v(384.05, 64.87) * mm});
            skLineSegment(sketch, "E3434", {"start": v(384.05, 64.87) * mm, "end": v(384.1, 65.05) * mm});
            skLineSegment(sketch, "E3435", {"start": v(384.1, 65.05) * mm, "end": v(384.19, 65.22) * mm});
            skLineSegment(sketch, "E3436", {"start": v(384.19, 65.22) * mm, "end": v(384.29, 65.38) * mm});
            skLineSegment(sketch, "E3437", {"start": v(384.29, 65.38) * mm, "end": v(384.4, 65.53) * mm});
            skLineSegment(sketch, "E3438", {"start": v(384.4, 65.53) * mm, "end": v(384.54, 65.66) * mm});
            skLineSegment(sketch, "E3439", {"start": v(384.54, 65.66) * mm, "end": v(384.7, 65.77) * mm});
            skLineSegment(sketch, "E3440", {"start": v(384.7, 65.77) * mm, "end": v(384.86, 65.86) * mm});
            skLineSegment(sketch, "E3441", {"start": v(384.86, 65.86) * mm, "end": v(385.04, 65.93) * mm});
            skLineSegment(sketch, "E3442", {"start": v(385.04, 65.93) * mm, "end": v(385.22, 65.97) * mm});
            skLineSegment(sketch, "E3443", {"start": v(385.22, 65.97) * mm, "end": v(385.4, 66) * mm});
            skLineSegment(sketch, "E3444", {"start": v(385.4, 66) * mm, "end": v(385.6, 66) * mm});
            skLineSegment(sketch, "E3445", {"start": v(385.6, 66) * mm, "end": v(385.78, 65.97) * mm});
            skLineSegment(sketch, "E3446", {"start": v(385.78, 65.97) * mm, "end": v(385.96, 65.93) * mm});
            skLineSegment(sketch, "E3447", {"start": v(385.96, 65.93) * mm, "end": v(386.14, 65.86) * mm});
            skLineSegment(sketch, "E3448", {"start": v(386.14, 65.86) * mm, "end": v(386.3, 65.77) * mm});
            skLineSegment(sketch, "E3449", {"start": v(386.3, 65.77) * mm, "end": v(386.46, 65.66) * mm});
            skLineSegment(sketch, "E3450", {"start": v(386.46, 65.66) * mm, "end": v(386.6, 65.53) * mm});
            skLineSegment(sketch, "E3451", {"start": v(386.6, 65.53) * mm, "end": v(386.71, 65.38) * mm});
            skLineSegment(sketch, "E3452", {"start": v(386.71, 65.38) * mm, "end": v(386.81, 65.22) * mm});
            skLineSegment(sketch, "E3453", {"start": v(386.81, 65.22) * mm, "end": v(386.9, 65.05) * mm});
            skLineSegment(sketch, "E3454", {"start": v(386.9, 65.05) * mm, "end": v(386.95, 64.87) * mm});
            skLineSegment(sketch, "E3455", {"start": v(386.95, 64.87) * mm, "end": v(386.99, 64.69) * mm});
            skLineSegment(sketch, "E3456", {"start": v(386.99, 64.69) * mm, "end": v(387, 64.5) * mm});
            skLineSegment(sketch, "E3457", {"start": v(387, 64.5) * mm, "end": v(386.99, 64.31) * mm});
            skLineSegment(sketch, "E3458", {"start": v(386.99, 64.31) * mm, "end": v(386.95, 64.13) * mm});
            skLineSegment(sketch, "E3459", {"start": v(386.95, 64.13) * mm, "end": v(386.9, 63.95) * mm});
            skLineSegment(sketch, "E3460", {"start": v(386.9, 63.95) * mm, "end": v(386.81, 63.78) * mm});
            skLineSegment(sketch, "E3461", {"start": v(386.81, 63.78) * mm, "end": v(386.71, 63.62) * mm});
            skLineSegment(sketch, "E3462", {"start": v(386.71, 63.62) * mm, "end": v(386.6, 63.47) * mm});
            skLineSegment(sketch, "E3463", {"start": v(386.6, 63.47) * mm, "end": v(386.46, 63.34) * mm});
            skLineSegment(sketch, "E3464", {"start": v(386.46, 63.34) * mm, "end": v(386.3, 63.23) * mm});
            skLineSegment(sketch, "E3465", {"start": v(386.3, 63.23) * mm, "end": v(386.14, 63.14) * mm});
            skLineSegment(sketch, "E3466", {"start": v(386.14, 63.14) * mm, "end": v(385.96, 63.07) * mm});
            skLineSegment(sketch, "E3467", {"start": v(385.96, 63.07) * mm, "end": v(385.78, 63.03) * mm});
            skLineSegment(sketch, "E3468", {"start": v(385.78, 63.03) * mm, "end": v(385.6, 63) * mm});
            skLineSegment(sketch, "E3469", {"start": v(385.6, 63) * mm, "end": v(385.4, 63) * mm});
            skLineSegment(sketch, "E3470", {"start": v(204.84, -127.5) * mm, "end": v(204.53, -127.46) * mm});
            skLineSegment(sketch, "E3471", {"start": v(204.53, -127.46) * mm, "end": v(204.23, -127.38) * mm});
            skLineSegment(sketch, "E3472", {"start": v(204.23, -127.38) * mm, "end": v(203.94, -127.26) * mm});
            skLineSegment(sketch, "E3473", {"start": v(203.94, -127.26) * mm, "end": v(203.66, -127.11) * mm});
            skLineSegment(sketch, "E3474", {"start": v(203.66, -127.11) * mm, "end": v(203.4, -126.93) * mm});
            skLineSegment(sketch, "E3475", {"start": v(203.4, -126.93) * mm, "end": v(203.18, -126.71) * mm});
            skLineSegment(sketch, "E3476", {"start": v(203.18, -126.71) * mm, "end": v(202.98, -126.47) * mm});
            skLineSegment(sketch, "E3477", {"start": v(202.98, -126.47) * mm, "end": v(202.8, -126.2) * mm});
            skLineSegment(sketch, "E3478", {"start": v(202.8, -126.2) * mm, "end": v(202.68, -125.92) * mm});
            skLineSegment(sketch, "E3479", {"start": v(202.68, -125.92) * mm, "end": v(202.58, -125.62) * mm});
            skLineSegment(sketch, "E3480", {"start": v(202.58, -125.62) * mm, "end": v(202.52, -125.31) * mm});
            skLineSegment(sketch, "E3481", {"start": v(202.52, -125.31) * mm, "end": v(202.5, -125) * mm});
            skLineSegment(sketch, "E3482", {"start": v(202.5, -125) * mm, "end": v(202.52, -124.69) * mm});
            skLineSegment(sketch, "E3483", {"start": v(202.52, -124.69) * mm, "end": v(202.58, -124.38) * mm});
            skLineSegment(sketch, "E3484", {"start": v(202.58, -124.38) * mm, "end": v(202.68, -124.08) * mm});
            skLineSegment(sketch, "E3485", {"start": v(202.68, -124.08) * mm, "end": v(202.8, -123.8) * mm});
            skLineSegment(sketch, "E3486", {"start": v(202.8, -123.8) * mm, "end": v(202.98, -123.53) * mm});
            skLineSegment(sketch, "E3487", {"start": v(202.98, -123.53) * mm, "end": v(203.18, -123.29) * mm});
            skLineSegment(sketch, "E3488", {"start": v(203.18, -123.29) * mm, "end": v(203.4, -123.07) * mm});
            skLineSegment(sketch, "E3489", {"start": v(203.4, -123.07) * mm, "end": v(203.66, -122.89) * mm});
            skLineSegment(sketch, "E3490", {"start": v(203.66, -122.89) * mm, "end": v(203.94, -122.74) * mm});
            skLineSegment(sketch, "E3491", {"start": v(203.94, -122.74) * mm, "end": v(204.23, -122.62) * mm});
            skLineSegment(sketch, "E3492", {"start": v(204.23, -122.62) * mm, "end": v(204.53, -122.54) * mm});
            skLineSegment(sketch, "E3493", {"start": v(204.53, -122.54) * mm, "end": v(204.84, -122.5) * mm});
            skLineSegment(sketch, "E3494", {"start": v(204.84, -122.5) * mm, "end": v(205.16, -122.5) * mm});
            skLineSegment(sketch, "E3495", {"start": v(205.16, -122.5) * mm, "end": v(205.47, -122.54) * mm});
            skLineSegment(sketch, "E3496", {"start": v(205.47, -122.54) * mm, "end": v(205.77, -122.62) * mm});
            skLineSegment(sketch, "E3497", {"start": v(205.77, -122.62) * mm, "end": v(206.06, -122.74) * mm});
            skLineSegment(sketch, "E3498", {"start": v(206.06, -122.74) * mm, "end": v(206.34, -122.89) * mm});
            skLineSegment(sketch, "E3499", {"start": v(206.34, -122.89) * mm, "end": v(206.6, -123.07) * mm});
            skLineSegment(sketch, "E3500", {"start": v(206.6, -123.07) * mm, "end": v(206.82, -123.29) * mm});
            skLineSegment(sketch, "E3501", {"start": v(206.82, -123.29) * mm, "end": v(207.02, -123.53) * mm});
            skLineSegment(sketch, "E3502", {"start": v(207.02, -123.53) * mm, "end": v(207.2, -123.8) * mm});
            skLineSegment(sketch, "E3503", {"start": v(207.2, -123.8) * mm, "end": v(207.32, -124.08) * mm});
            skLineSegment(sketch, "E3504", {"start": v(207.32, -124.08) * mm, "end": v(207.42, -124.38) * mm});
            skLineSegment(sketch, "E3505", {"start": v(207.42, -124.38) * mm, "end": v(207.48, -124.69) * mm});
            skLineSegment(sketch, "E3506", {"start": v(207.48, -124.69) * mm, "end": v(207.5, -125) * mm});
            skLineSegment(sketch, "E3507", {"start": v(207.5, -125) * mm, "end": v(207.48, -125.31) * mm});
            skLineSegment(sketch, "E3508", {"start": v(207.48, -125.31) * mm, "end": v(207.42, -125.62) * mm});
            skLineSegment(sketch, "E3509", {"start": v(207.42, -125.62) * mm, "end": v(207.32, -125.92) * mm});
            skLineSegment(sketch, "E3510", {"start": v(207.32, -125.92) * mm, "end": v(207.2, -126.2) * mm});
            skLineSegment(sketch, "E3511", {"start": v(207.2, -126.2) * mm, "end": v(207.02, -126.47) * mm});
            skLineSegment(sketch, "E3512", {"start": v(207.02, -126.47) * mm, "end": v(206.82, -126.71) * mm});
            skLineSegment(sketch, "E3513", {"start": v(206.82, -126.71) * mm, "end": v(206.6, -126.93) * mm});
            skLineSegment(sketch, "E3514", {"start": v(206.6, -126.93) * mm, "end": v(206.34, -127.11) * mm});
            skLineSegment(sketch, "E3515", {"start": v(206.34, -127.11) * mm, "end": v(206.06, -127.26) * mm});
            skLineSegment(sketch, "E3516", {"start": v(206.06, -127.26) * mm, "end": v(205.77, -127.38) * mm});
            skLineSegment(sketch, "E3517", {"start": v(205.77, -127.38) * mm, "end": v(205.47, -127.46) * mm});
            skLineSegment(sketch, "E3518", {"start": v(205.47, -127.46) * mm, "end": v(205.16, -127.5) * mm});
            skLineSegment(sketch, "E3519", {"start": v(205.16, -127.5) * mm, "end": v(204.84, -127.5) * mm});
            skLineSegment(sketch, "E3520", {"start": v(267.9, -148.5) * mm, "end": v(267.72, -148.47) * mm});
            skLineSegment(sketch, "E3521", {"start": v(267.72, -148.47) * mm, "end": v(267.54, -148.43) * mm});
            skLineSegment(sketch, "E3522", {"start": v(267.54, -148.43) * mm, "end": v(267.36, -148.36) * mm});
            skLineSegment(sketch, "E3523", {"start": v(267.36, -148.36) * mm, "end": v(267.2, -148.27) * mm});
            skLineSegment(sketch, "E3524", {"start": v(267.2, -148.27) * mm, "end": v(267.04, -148.16) * mm});
            skLineSegment(sketch, "E3525", {"start": v(267.04, -148.16) * mm, "end": v(266.9, -148.03) * mm});
            skLineSegment(sketch, "E3526", {"start": v(266.9, -148.03) * mm, "end": v(266.79, -147.88) * mm});
            skLineSegment(sketch, "E3527", {"start": v(266.79, -147.88) * mm, "end": v(266.69, -147.72) * mm});
            skLineSegment(sketch, "E3528", {"start": v(266.69, -147.72) * mm, "end": v(266.6, -147.55) * mm});
            skLineSegment(sketch, "E3529", {"start": v(266.6, -147.55) * mm, "end": v(266.55, -147.37) * mm});
            skLineSegment(sketch, "E3530", {"start": v(266.55, -147.37) * mm, "end": v(266.51, -147.19) * mm});
            skLineSegment(sketch, "E3531", {"start": v(266.51, -147.19) * mm, "end": v(266.5, -147) * mm});
            skLineSegment(sketch, "E3532", {"start": v(266.5, -147) * mm, "end": v(266.51, -146.81) * mm});
            skLineSegment(sketch, "E3533", {"start": v(266.51, -146.81) * mm, "end": v(266.55, -146.63) * mm});
            skLineSegment(sketch, "E3534", {"start": v(266.55, -146.63) * mm, "end": v(266.6, -146.45) * mm});
            skLineSegment(sketch, "E3535", {"start": v(266.6, -146.45) * mm, "end": v(266.69, -146.28) * mm});
            skLineSegment(sketch, "E3536", {"start": v(266.69, -146.28) * mm, "end": v(266.79, -146.12) * mm});
            skLineSegment(sketch, "E3537", {"start": v(266.79, -146.12) * mm, "end": v(266.9, -145.97) * mm});
            skLineSegment(sketch, "E3538", {"start": v(266.9, -145.97) * mm, "end": v(267.04, -145.84) * mm});
            skLineSegment(sketch, "E3539", {"start": v(267.04, -145.84) * mm, "end": v(267.2, -145.73) * mm});
            skLineSegment(sketch, "E3540", {"start": v(267.2, -145.73) * mm, "end": v(267.36, -145.64) * mm});
            skLineSegment(sketch, "E3541", {"start": v(267.36, -145.64) * mm, "end": v(267.54, -145.57) * mm});
            skLineSegment(sketch, "E3542", {"start": v(267.54, -145.57) * mm, "end": v(267.72, -145.53) * mm});
            skLineSegment(sketch, "E3543", {"start": v(267.72, -145.53) * mm, "end": v(267.9, -145.5) * mm});
            skLineSegment(sketch, "E3544", {"start": v(267.9, -145.5) * mm, "end": v(268.1, -145.5) * mm});
            skLineSegment(sketch, "E3545", {"start": v(268.1, -145.5) * mm, "end": v(268.28, -145.53) * mm});
            skLineSegment(sketch, "E3546", {"start": v(268.28, -145.53) * mm, "end": v(268.46, -145.57) * mm});
            skLineSegment(sketch, "E3547", {"start": v(268.46, -145.57) * mm, "end": v(268.64, -145.64) * mm});
            skLineSegment(sketch, "E3548", {"start": v(268.64, -145.64) * mm, "end": v(268.8, -145.73) * mm});
            skLineSegment(sketch, "E3549", {"start": v(268.8, -145.73) * mm, "end": v(268.96, -145.84) * mm});
            skLineSegment(sketch, "E3550", {"start": v(268.96, -145.84) * mm, "end": v(269.1, -145.97) * mm});
            skLineSegment(sketch, "E3551", {"start": v(269.1, -145.97) * mm, "end": v(269.21, -146.12) * mm});
            skLineSegment(sketch, "E3552", {"start": v(269.21, -146.12) * mm, "end": v(269.31, -146.28) * mm});
            skLineSegment(sketch, "E3553", {"start": v(269.31, -146.28) * mm, "end": v(269.4, -146.45) * mm});
            skLineSegment(sketch, "E3554", {"start": v(269.4, -146.45) * mm, "end": v(269.45, -146.63) * mm});
            skLineSegment(sketch, "E3555", {"start": v(269.45, -146.63) * mm, "end": v(269.49, -146.81) * mm});
            skLineSegment(sketch, "E3556", {"start": v(269.49, -146.81) * mm, "end": v(269.5, -147) * mm});
            skLineSegment(sketch, "E3557", {"start": v(269.5, -147) * mm, "end": v(269.49, -147.19) * mm});
            skLineSegment(sketch, "E3558", {"start": v(269.49, -147.19) * mm, "end": v(269.45, -147.37) * mm});
            skLineSegment(sketch, "E3559", {"start": v(269.45, -147.37) * mm, "end": v(269.4, -147.55) * mm});
            skLineSegment(sketch, "E3560", {"start": v(269.4, -147.55) * mm, "end": v(269.31, -147.72) * mm});
            skLineSegment(sketch, "E3561", {"start": v(269.31, -147.72) * mm, "end": v(269.21, -147.88) * mm});
            skLineSegment(sketch, "E3562", {"start": v(269.21, -147.88) * mm, "end": v(269.1, -148.03) * mm});
            skLineSegment(sketch, "E3563", {"start": v(269.1, -148.03) * mm, "end": v(268.96, -148.16) * mm});
            skLineSegment(sketch, "E3564", {"start": v(268.96, -148.16) * mm, "end": v(268.8, -148.27) * mm});
            skLineSegment(sketch, "E3565", {"start": v(268.8, -148.27) * mm, "end": v(268.64, -148.36) * mm});
            skLineSegment(sketch, "E3566", {"start": v(268.64, -148.36) * mm, "end": v(268.46, -148.43) * mm});
            skLineSegment(sketch, "E3567", {"start": v(268.46, -148.43) * mm, "end": v(268.28, -148.47) * mm});
            skLineSegment(sketch, "E3568", {"start": v(268.28, -148.47) * mm, "end": v(268.1, -148.5) * mm});
            skLineSegment(sketch, "E3569", {"start": v(268.1, -148.5) * mm, "end": v(267.9, -148.5) * mm});
            skLineSegment(sketch, "E3570", {"start": v(251.9, -148.5) * mm, "end": v(251.72, -148.47) * mm});
            skLineSegment(sketch, "E3571", {"start": v(251.72, -148.47) * mm, "end": v(251.54, -148.43) * mm});
            skLineSegment(sketch, "E3572", {"start": v(251.54, -148.43) * mm, "end": v(251.36, -148.36) * mm});
            skLineSegment(sketch, "E3573", {"start": v(251.36, -148.36) * mm, "end": v(251.2, -148.27) * mm});
            skLineSegment(sketch, "E3574", {"start": v(251.2, -148.27) * mm, "end": v(251.04, -148.16) * mm});
            skLineSegment(sketch, "E3575", {"start": v(251.04, -148.16) * mm, "end": v(250.9, -148.03) * mm});
            skLineSegment(sketch, "E3576", {"start": v(250.9, -148.03) * mm, "end": v(250.79, -147.88) * mm});
            skLineSegment(sketch, "E3577", {"start": v(250.79, -147.88) * mm, "end": v(250.69, -147.72) * mm});
            skLineSegment(sketch, "E3578", {"start": v(250.69, -147.72) * mm, "end": v(250.6, -147.55) * mm});
            skLineSegment(sketch, "E3579", {"start": v(250.6, -147.55) * mm, "end": v(250.55, -147.37) * mm});
            skLineSegment(sketch, "E3580", {"start": v(250.55, -147.37) * mm, "end": v(250.51, -147.19) * mm});
            skLineSegment(sketch, "E3581", {"start": v(250.51, -147.19) * mm, "end": v(250.5, -147) * mm});
            skLineSegment(sketch, "E3582", {"start": v(250.5, -147) * mm, "end": v(250.51, -146.81) * mm});
            skLineSegment(sketch, "E3583", {"start": v(250.51, -146.81) * mm, "end": v(250.55, -146.63) * mm});
            skLineSegment(sketch, "E3584", {"start": v(250.55, -146.63) * mm, "end": v(250.6, -146.45) * mm});
            skLineSegment(sketch, "E3585", {"start": v(250.6, -146.45) * mm, "end": v(250.69, -146.28) * mm});
            skLineSegment(sketch, "E3586", {"start": v(250.69, -146.28) * mm, "end": v(250.79, -146.12) * mm});
            skLineSegment(sketch, "E3587", {"start": v(250.79, -146.12) * mm, "end": v(250.9, -145.97) * mm});
            skLineSegment(sketch, "E3588", {"start": v(250.9, -145.97) * mm, "end": v(251.04, -145.84) * mm});
            skLineSegment(sketch, "E3589", {"start": v(251.04, -145.84) * mm, "end": v(251.2, -145.73) * mm});
            skLineSegment(sketch, "E3590", {"start": v(251.2, -145.73) * mm, "end": v(251.36, -145.64) * mm});
            skLineSegment(sketch, "E3591", {"start": v(251.36, -145.64) * mm, "end": v(251.54, -145.57) * mm});
            skLineSegment(sketch, "E3592", {"start": v(251.54, -145.57) * mm, "end": v(251.72, -145.53) * mm});
            skLineSegment(sketch, "E3593", {"start": v(251.72, -145.53) * mm, "end": v(251.9, -145.5) * mm});
            skLineSegment(sketch, "E3594", {"start": v(251.9, -145.5) * mm, "end": v(252.1, -145.5) * mm});
            skLineSegment(sketch, "E3595", {"start": v(252.1, -145.5) * mm, "end": v(252.28, -145.53) * mm});
            skLineSegment(sketch, "E3596", {"start": v(252.28, -145.53) * mm, "end": v(252.46, -145.57) * mm});
            skLineSegment(sketch, "E3597", {"start": v(252.46, -145.57) * mm, "end": v(252.64, -145.64) * mm});
            skLineSegment(sketch, "E3598", {"start": v(252.64, -145.64) * mm, "end": v(252.8, -145.73) * mm});
            skLineSegment(sketch, "E3599", {"start": v(252.8, -145.73) * mm, "end": v(252.96, -145.84) * mm});
            skLineSegment(sketch, "E3600", {"start": v(252.96, -145.84) * mm, "end": v(253.1, -145.97) * mm});
            skLineSegment(sketch, "E3601", {"start": v(253.1, -145.97) * mm, "end": v(253.21, -146.12) * mm});
            skLineSegment(sketch, "E3602", {"start": v(253.21, -146.12) * mm, "end": v(253.31, -146.28) * mm});
            skLineSegment(sketch, "E3603", {"start": v(253.31, -146.28) * mm, "end": v(253.4, -146.45) * mm});
            skLineSegment(sketch, "E3604", {"start": v(253.4, -146.45) * mm, "end": v(253.45, -146.63) * mm});
            skLineSegment(sketch, "E3605", {"start": v(253.45, -146.63) * mm, "end": v(253.49, -146.81) * mm});
            skLineSegment(sketch, "E3606", {"start": v(253.49, -146.81) * mm, "end": v(253.5, -147) * mm});
            skLineSegment(sketch, "E3607", {"start": v(253.5, -147) * mm, "end": v(253.49, -147.19) * mm});
            skLineSegment(sketch, "E3608", {"start": v(253.49, -147.19) * mm, "end": v(253.45, -147.37) * mm});
            skLineSegment(sketch, "E3609", {"start": v(253.45, -147.37) * mm, "end": v(253.4, -147.55) * mm});
            skLineSegment(sketch, "E3610", {"start": v(253.4, -147.55) * mm, "end": v(253.31, -147.72) * mm});
            skLineSegment(sketch, "E3611", {"start": v(253.31, -147.72) * mm, "end": v(253.21, -147.88) * mm});
            skLineSegment(sketch, "E3612", {"start": v(253.21, -147.88) * mm, "end": v(253.1, -148.03) * mm});
            skLineSegment(sketch, "E3613", {"start": v(253.1, -148.03) * mm, "end": v(252.96, -148.16) * mm});
            skLineSegment(sketch, "E3614", {"start": v(252.96, -148.16) * mm, "end": v(252.8, -148.27) * mm});
            skLineSegment(sketch, "E3615", {"start": v(252.8, -148.27) * mm, "end": v(252.64, -148.36) * mm});
            skLineSegment(sketch, "E3616", {"start": v(252.64, -148.36) * mm, "end": v(252.46, -148.43) * mm});
            skLineSegment(sketch, "E3617", {"start": v(252.46, -148.43) * mm, "end": v(252.28, -148.47) * mm});
            skLineSegment(sketch, "E3618", {"start": v(252.28, -148.47) * mm, "end": v(252.1, -148.5) * mm});
            skLineSegment(sketch, "E3619", {"start": v(252.1, -148.5) * mm, "end": v(251.9, -148.5) * mm});
            skLineSegment(sketch, "E3620", {"start": v(157.9, -148.5) * mm, "end": v(157.72, -148.47) * mm});
            skLineSegment(sketch, "E3621", {"start": v(157.72, -148.47) * mm, "end": v(157.54, -148.43) * mm});
            skLineSegment(sketch, "E3622", {"start": v(157.54, -148.43) * mm, "end": v(157.36, -148.36) * mm});
            skLineSegment(sketch, "E3623", {"start": v(157.36, -148.36) * mm, "end": v(157.2, -148.27) * mm});
            skLineSegment(sketch, "E3624", {"start": v(157.2, -148.27) * mm, "end": v(157.04, -148.16) * mm});
            skLineSegment(sketch, "E3625", {"start": v(157.04, -148.16) * mm, "end": v(156.9, -148.03) * mm});
            skLineSegment(sketch, "E3626", {"start": v(156.9, -148.03) * mm, "end": v(156.79, -147.88) * mm});
            skLineSegment(sketch, "E3627", {"start": v(156.79, -147.88) * mm, "end": v(156.69, -147.72) * mm});
            skLineSegment(sketch, "E3628", {"start": v(156.69, -147.72) * mm, "end": v(156.6, -147.55) * mm});
            skLineSegment(sketch, "E3629", {"start": v(156.6, -147.55) * mm, "end": v(156.55, -147.37) * mm});
            skLineSegment(sketch, "E3630", {"start": v(156.55, -147.37) * mm, "end": v(156.51, -147.19) * mm});
            skLineSegment(sketch, "E3631", {"start": v(156.51, -147.19) * mm, "end": v(156.5, -147) * mm});
            skLineSegment(sketch, "E3632", {"start": v(156.5, -147) * mm, "end": v(156.51, -146.81) * mm});
            skLineSegment(sketch, "E3633", {"start": v(156.51, -146.81) * mm, "end": v(156.55, -146.63) * mm});
            skLineSegment(sketch, "E3634", {"start": v(156.55, -146.63) * mm, "end": v(156.6, -146.45) * mm});
            skLineSegment(sketch, "E3635", {"start": v(156.6, -146.45) * mm, "end": v(156.69, -146.28) * mm});
            skLineSegment(sketch, "E3636", {"start": v(156.69, -146.28) * mm, "end": v(156.79, -146.12) * mm});
            skLineSegment(sketch, "E3637", {"start": v(156.79, -146.12) * mm, "end": v(156.9, -145.97) * mm});
            skLineSegment(sketch, "E3638", {"start": v(156.9, -145.97) * mm, "end": v(157.04, -145.84) * mm});
            skLineSegment(sketch, "E3639", {"start": v(157.04, -145.84) * mm, "end": v(157.2, -145.73) * mm});
            skLineSegment(sketch, "E3640", {"start": v(157.2, -145.73) * mm, "end": v(157.36, -145.64) * mm});
            skLineSegment(sketch, "E3641", {"start": v(157.36, -145.64) * mm, "end": v(157.54, -145.57) * mm});
            skLineSegment(sketch, "E3642", {"start": v(157.54, -145.57) * mm, "end": v(157.72, -145.53) * mm});
            skLineSegment(sketch, "E3643", {"start": v(157.72, -145.53) * mm, "end": v(157.9, -145.5) * mm});
            skLineSegment(sketch, "E3644", {"start": v(157.9, -145.5) * mm, "end": v(158.1, -145.5) * mm});
            skLineSegment(sketch, "E3645", {"start": v(158.1, -145.5) * mm, "end": v(158.28, -145.53) * mm});
            skLineSegment(sketch, "E3646", {"start": v(158.28, -145.53) * mm, "end": v(158.46, -145.57) * mm});
            skLineSegment(sketch, "E3647", {"start": v(158.46, -145.57) * mm, "end": v(158.64, -145.64) * mm});
            skLineSegment(sketch, "E3648", {"start": v(158.64, -145.64) * mm, "end": v(158.8, -145.73) * mm});
            skLineSegment(sketch, "E3649", {"start": v(158.8, -145.73) * mm, "end": v(158.96, -145.84) * mm});
            skLineSegment(sketch, "E3650", {"start": v(158.96, -145.84) * mm, "end": v(159.1, -145.97) * mm});
            skLineSegment(sketch, "E3651", {"start": v(159.1, -145.97) * mm, "end": v(159.21, -146.12) * mm});
            skLineSegment(sketch, "E3652", {"start": v(159.21, -146.12) * mm, "end": v(159.31, -146.28) * mm});
            skLineSegment(sketch, "E3653", {"start": v(159.31, -146.28) * mm, "end": v(159.4, -146.45) * mm});
            skLineSegment(sketch, "E3654", {"start": v(159.4, -146.45) * mm, "end": v(159.45, -146.63) * mm});
            skLineSegment(sketch, "E3655", {"start": v(159.45, -146.63) * mm, "end": v(159.49, -146.81) * mm});
            skLineSegment(sketch, "E3656", {"start": v(159.49, -146.81) * mm, "end": v(159.5, -147) * mm});
            skLineSegment(sketch, "E3657", {"start": v(159.5, -147) * mm, "end": v(159.49, -147.19) * mm});
            skLineSegment(sketch, "E3658", {"start": v(159.49, -147.19) * mm, "end": v(159.45, -147.37) * mm});
            skLineSegment(sketch, "E3659", {"start": v(159.45, -147.37) * mm, "end": v(159.4, -147.55) * mm});
            skLineSegment(sketch, "E3660", {"start": v(159.4, -147.55) * mm, "end": v(159.31, -147.72) * mm});
            skLineSegment(sketch, "E3661", {"start": v(159.31, -147.72) * mm, "end": v(159.21, -147.88) * mm});
            skLineSegment(sketch, "E3662", {"start": v(159.21, -147.88) * mm, "end": v(159.1, -148.03) * mm});
            skLineSegment(sketch, "E3663", {"start": v(159.1, -148.03) * mm, "end": v(158.96, -148.16) * mm});
            skLineSegment(sketch, "E3664", {"start": v(158.96, -148.16) * mm, "end": v(158.8, -148.27) * mm});
            skLineSegment(sketch, "E3665", {"start": v(158.8, -148.27) * mm, "end": v(158.64, -148.36) * mm});
            skLineSegment(sketch, "E3666", {"start": v(158.64, -148.36) * mm, "end": v(158.46, -148.43) * mm});
            skLineSegment(sketch, "E3667", {"start": v(158.46, -148.43) * mm, "end": v(158.28, -148.47) * mm});
            skLineSegment(sketch, "E3668", {"start": v(158.28, -148.47) * mm, "end": v(158.1, -148.5) * mm});
            skLineSegment(sketch, "E3669", {"start": v(158.1, -148.5) * mm, "end": v(157.9, -148.5) * mm});
            skLineSegment(sketch, "E3670", {"start": v(141.9, -148.5) * mm, "end": v(141.72, -148.47) * mm});
            skLineSegment(sketch, "E3671", {"start": v(141.72, -148.47) * mm, "end": v(141.54, -148.43) * mm});
            skLineSegment(sketch, "E3672", {"start": v(141.54, -148.43) * mm, "end": v(141.36, -148.36) * mm});
            skLineSegment(sketch, "E3673", {"start": v(141.36, -148.36) * mm, "end": v(141.2, -148.27) * mm});
            skLineSegment(sketch, "E3674", {"start": v(141.2, -148.27) * mm, "end": v(141.04, -148.16) * mm});
            skLineSegment(sketch, "E3675", {"start": v(141.04, -148.16) * mm, "end": v(140.9, -148.03) * mm});
            skLineSegment(sketch, "E3676", {"start": v(140.9, -148.03) * mm, "end": v(140.79, -147.88) * mm});
            skLineSegment(sketch, "E3677", {"start": v(140.79, -147.88) * mm, "end": v(140.69, -147.72) * mm});
            skLineSegment(sketch, "E3678", {"start": v(140.69, -147.72) * mm, "end": v(140.6, -147.55) * mm});
            skLineSegment(sketch, "E3679", {"start": v(140.6, -147.55) * mm, "end": v(140.55, -147.37) * mm});
            skLineSegment(sketch, "E3680", {"start": v(140.55, -147.37) * mm, "end": v(140.51, -147.19) * mm});
            skLineSegment(sketch, "E3681", {"start": v(140.51, -147.19) * mm, "end": v(140.5, -147) * mm});
            skLineSegment(sketch, "E3682", {"start": v(140.5, -147) * mm, "end": v(140.51, -146.81) * mm});
            skLineSegment(sketch, "E3683", {"start": v(140.51, -146.81) * mm, "end": v(140.55, -146.63) * mm});
            skLineSegment(sketch, "E3684", {"start": v(140.55, -146.63) * mm, "end": v(140.6, -146.45) * mm});
            skLineSegment(sketch, "E3685", {"start": v(140.6, -146.45) * mm, "end": v(140.69, -146.28) * mm});
            skLineSegment(sketch, "E3686", {"start": v(140.69, -146.28) * mm, "end": v(140.79, -146.12) * mm});
            skLineSegment(sketch, "E3687", {"start": v(140.79, -146.12) * mm, "end": v(140.9, -145.97) * mm});
            skLineSegment(sketch, "E3688", {"start": v(140.9, -145.97) * mm, "end": v(141.04, -145.84) * mm});
            skLineSegment(sketch, "E3689", {"start": v(141.04, -145.84) * mm, "end": v(141.2, -145.73) * mm});
            skLineSegment(sketch, "E3690", {"start": v(141.2, -145.73) * mm, "end": v(141.36, -145.64) * mm});
            skLineSegment(sketch, "E3691", {"start": v(141.36, -145.64) * mm, "end": v(141.54, -145.57) * mm});
            skLineSegment(sketch, "E3692", {"start": v(141.54, -145.57) * mm, "end": v(141.72, -145.53) * mm});
            skLineSegment(sketch, "E3693", {"start": v(141.72, -145.53) * mm, "end": v(141.9, -145.5) * mm});
            skLineSegment(sketch, "E3694", {"start": v(141.9, -145.5) * mm, "end": v(142.1, -145.5) * mm});
            skLineSegment(sketch, "E3695", {"start": v(142.1, -145.5) * mm, "end": v(142.28, -145.53) * mm});
            skLineSegment(sketch, "E3696", {"start": v(142.28, -145.53) * mm, "end": v(142.46, -145.57) * mm});
            skLineSegment(sketch, "E3697", {"start": v(142.46, -145.57) * mm, "end": v(142.64, -145.64) * mm});
            skLineSegment(sketch, "E3698", {"start": v(142.64, -145.64) * mm, "end": v(142.8, -145.73) * mm});
            skLineSegment(sketch, "E3699", {"start": v(142.8, -145.73) * mm, "end": v(142.96, -145.84) * mm});
            skLineSegment(sketch, "E3700", {"start": v(142.96, -145.84) * mm, "end": v(143.1, -145.97) * mm});
            skLineSegment(sketch, "E3701", {"start": v(143.1, -145.97) * mm, "end": v(143.21, -146.12) * mm});
            skLineSegment(sketch, "E3702", {"start": v(143.21, -146.12) * mm, "end": v(143.31, -146.28) * mm});
            skLineSegment(sketch, "E3703", {"start": v(143.31, -146.28) * mm, "end": v(143.4, -146.45) * mm});
            skLineSegment(sketch, "E3704", {"start": v(143.4, -146.45) * mm, "end": v(143.45, -146.63) * mm});
            skLineSegment(sketch, "E3705", {"start": v(143.45, -146.63) * mm, "end": v(143.49, -146.81) * mm});
            skLineSegment(sketch, "E3706", {"start": v(143.49, -146.81) * mm, "end": v(143.5, -147) * mm});
            skLineSegment(sketch, "E3707", {"start": v(143.5, -147) * mm, "end": v(143.49, -147.19) * mm});
            skLineSegment(sketch, "E3708", {"start": v(143.49, -147.19) * mm, "end": v(143.45, -147.37) * mm});
            skLineSegment(sketch, "E3709", {"start": v(143.45, -147.37) * mm, "end": v(143.4, -147.55) * mm});
            skLineSegment(sketch, "E3710", {"start": v(143.4, -147.55) * mm, "end": v(143.31, -147.72) * mm});
            skLineSegment(sketch, "E3711", {"start": v(143.31, -147.72) * mm, "end": v(143.21, -147.88) * mm});
            skLineSegment(sketch, "E3712", {"start": v(143.21, -147.88) * mm, "end": v(143.1, -148.03) * mm});
            skLineSegment(sketch, "E3713", {"start": v(143.1, -148.03) * mm, "end": v(142.96, -148.16) * mm});
            skLineSegment(sketch, "E3714", {"start": v(142.96, -148.16) * mm, "end": v(142.8, -148.27) * mm});
            skLineSegment(sketch, "E3715", {"start": v(142.8, -148.27) * mm, "end": v(142.64, -148.36) * mm});
            skLineSegment(sketch, "E3716", {"start": v(142.64, -148.36) * mm, "end": v(142.46, -148.43) * mm});
            skLineSegment(sketch, "E3717", {"start": v(142.46, -148.43) * mm, "end": v(142.28, -148.47) * mm});
            skLineSegment(sketch, "E3718", {"start": v(142.28, -148.47) * mm, "end": v(142.1, -148.5) * mm});
            skLineSegment(sketch, "E3719", {"start": v(142.1, -148.5) * mm, "end": v(141.9, -148.5) * mm});
            skLineSegment(sketch, "E3720", {"start": v(50, -166.5) * mm, "end": v(50, -150.5) * mm});
            skLineSegment(sketch, "E3721", {"start": v(50, -150.5) * mm, "end": v(70, -150.5) * mm});
            skLineSegment(sketch, "E3722", {"start": v(70, -150.5) * mm, "end": v(70, -166.5) * mm});
            skLineSegment(sketch, "E3723", {"start": v(70, -166.5) * mm, "end": v(50, -166.5) * mm});
            skLineSegment(sketch, "E3724", {"start": v(340, -166.5) * mm, "end": v(340, -150.5) * mm});
            skLineSegment(sketch, "E3725", {"start": v(340, -150.5) * mm, "end": v(360, -150.5) * mm});
            skLineSegment(sketch, "E3726", {"start": v(360, -150.5) * mm, "end": v(360, -166.5) * mm});
            skLineSegment(sketch, "E3727", {"start": v(360, -166.5) * mm, "end": v(340, -166.5) * mm});
            skLineSegment(sketch, "E3728", {"start": v(195, -166.5) * mm, "end": v(195, -150.5) * mm});
            skLineSegment(sketch, "E3729", {"start": v(195, -150.5) * mm, "end": v(215, -150.5) * mm});
            skLineSegment(sketch, "E3730", {"start": v(215, -150.5) * mm, "end": v(215, -166.5) * mm});
            skLineSegment(sketch, "E3731", {"start": v(215, -166.5) * mm, "end": v(195, -166.5) * mm});
            skLineSegment(sketch, "E3732", {"start": v(287.37, -160.5) * mm, "end": v(287.12, -160.47) * mm});
            skLineSegment(sketch, "E3733", {"start": v(287.12, -160.47) * mm, "end": v(286.88, -160.4) * mm});
            skLineSegment(sketch, "E3734", {"start": v(286.88, -160.4) * mm, "end": v(286.65, -160.3) * mm});
            skLineSegment(sketch, "E3735", {"start": v(286.65, -160.3) * mm, "end": v(286.43, -160.19) * mm});
            skLineSegment(sketch, "E3736", {"start": v(286.43, -160.19) * mm, "end": v(286.23, -160.04) * mm});
            skLineSegment(sketch, "E3737", {"start": v(286.23, -160.04) * mm, "end": v(286.04, -159.87) * mm});
            skLineSegment(sketch, "E3738", {"start": v(286.04, -159.87) * mm, "end": v(285.88, -159.68) * mm});
            skLineSegment(sketch, "E3739", {"start": v(285.88, -159.68) * mm, "end": v(285.75, -159.46) * mm});
            skLineSegment(sketch, "E3740", {"start": v(285.75, -159.46) * mm, "end": v(285.64, -159.24) * mm});
            skLineSegment(sketch, "E3741", {"start": v(285.64, -159.24) * mm, "end": v(285.56, -159) * mm});
            skLineSegment(sketch, "E3742", {"start": v(285.56, -159) * mm, "end": v(285.52, -158.75) * mm});
            skLineSegment(sketch, "E3743", {"start": v(285.52, -158.75) * mm, "end": v(285.5, -158.5) * mm});
            skLineSegment(sketch, "E3744", {"start": v(285.5, -158.5) * mm, "end": v(285.52, -158.25) * mm});
            skLineSegment(sketch, "E3745", {"start": v(285.52, -158.25) * mm, "end": v(285.56, -158) * mm});
            skLineSegment(sketch, "E3746", {"start": v(285.56, -158) * mm, "end": v(285.64, -157.76) * mm});
            skLineSegment(sketch, "E3747", {"start": v(285.64, -157.76) * mm, "end": v(285.75, -157.54) * mm});
            skLineSegment(sketch, "E3748", {"start": v(285.75, -157.54) * mm, "end": v(285.88, -157.32) * mm});
            skLineSegment(sketch, "E3749", {"start": v(285.88, -157.32) * mm, "end": v(286.04, -157.13) * mm});
            skLineSegment(sketch, "E3750", {"start": v(286.04, -157.13) * mm, "end": v(286.23, -156.96) * mm});
            skLineSegment(sketch, "E3751", {"start": v(286.23, -156.96) * mm, "end": v(286.43, -156.81) * mm});
            skLineSegment(sketch, "E3752", {"start": v(286.43, -156.81) * mm, "end": v(286.65, -156.7) * mm});
            skLineSegment(sketch, "E3753", {"start": v(286.65, -156.7) * mm, "end": v(286.88, -156.6) * mm});
            skLineSegment(sketch, "E3754", {"start": v(286.88, -156.6) * mm, "end": v(287.12, -156.53) * mm});
            skLineSegment(sketch, "E3755", {"start": v(287.12, -156.53) * mm, "end": v(287.37, -156.5) * mm});
            skLineSegment(sketch, "E3756", {"start": v(287.37, -156.5) * mm, "end": v(287.63, -156.5) * mm});
            skLineSegment(sketch, "E3757", {"start": v(287.63, -156.5) * mm, "end": v(287.88, -156.53) * mm});
            skLineSegment(sketch, "E3758", {"start": v(287.88, -156.53) * mm, "end": v(288.12, -156.6) * mm});
            skLineSegment(sketch, "E3759", {"start": v(288.12, -156.6) * mm, "end": v(288.35, -156.7) * mm});
            skLineSegment(sketch, "E3760", {"start": v(288.35, -156.7) * mm, "end": v(288.57, -156.81) * mm});
            skLineSegment(sketch, "E3761", {"start": v(288.57, -156.81) * mm, "end": v(288.77, -156.96) * mm});
            skLineSegment(sketch, "E3762", {"start": v(288.77, -156.96) * mm, "end": v(288.96, -157.13) * mm});
            skLineSegment(sketch, "E3763", {"start": v(288.96, -157.13) * mm, "end": v(289.12, -157.32) * mm});
            skLineSegment(sketch, "E3764", {"start": v(289.12, -157.32) * mm, "end": v(289.25, -157.54) * mm});
            skLineSegment(sketch, "E3765", {"start": v(289.25, -157.54) * mm, "end": v(289.36, -157.76) * mm});
            skLineSegment(sketch, "E3766", {"start": v(289.36, -157.76) * mm, "end": v(289.44, -158) * mm});
            skLineSegment(sketch, "E3767", {"start": v(289.44, -158) * mm, "end": v(289.48, -158.25) * mm});
            skLineSegment(sketch, "E3768", {"start": v(289.48, -158.25) * mm, "end": v(289.5, -158.5) * mm});
            skLineSegment(sketch, "E3769", {"start": v(289.5, -158.5) * mm, "end": v(289.48, -158.75) * mm});
            skLineSegment(sketch, "E3770", {"start": v(289.48, -158.75) * mm, "end": v(289.44, -159) * mm});
            skLineSegment(sketch, "E3771", {"start": v(289.44, -159) * mm, "end": v(289.36, -159.24) * mm});
            skLineSegment(sketch, "E3772", {"start": v(289.36, -159.24) * mm, "end": v(289.25, -159.46) * mm});
            skLineSegment(sketch, "E3773", {"start": v(289.25, -159.46) * mm, "end": v(289.12, -159.68) * mm});
            skLineSegment(sketch, "E3774", {"start": v(289.12, -159.68) * mm, "end": v(288.96, -159.87) * mm});
            skLineSegment(sketch, "E3775", {"start": v(288.96, -159.87) * mm, "end": v(288.77, -160.04) * mm});
            skLineSegment(sketch, "E3776", {"start": v(288.77, -160.04) * mm, "end": v(288.57, -160.19) * mm});
            skLineSegment(sketch, "E3777", {"start": v(288.57, -160.19) * mm, "end": v(288.35, -160.3) * mm});
            skLineSegment(sketch, "E3778", {"start": v(288.35, -160.3) * mm, "end": v(288.12, -160.4) * mm});
            skLineSegment(sketch, "E3779", {"start": v(288.12, -160.4) * mm, "end": v(287.88, -160.47) * mm});
            skLineSegment(sketch, "E3780", {"start": v(287.88, -160.47) * mm, "end": v(287.63, -160.5) * mm});
            skLineSegment(sketch, "E3781", {"start": v(287.63, -160.5) * mm, "end": v(287.37, -160.5) * mm});
            skLineSegment(sketch, "E3782", {"start": v(122.37, -160.5) * mm, "end": v(122.12, -160.47) * mm});
            skLineSegment(sketch, "E3783", {"start": v(122.12, -160.47) * mm, "end": v(121.88, -160.4) * mm});
            skLineSegment(sketch, "E3784", {"start": v(121.88, -160.4) * mm, "end": v(121.65, -160.3) * mm});
            skLineSegment(sketch, "E3785", {"start": v(121.65, -160.3) * mm, "end": v(121.43, -160.19) * mm});
            skLineSegment(sketch, "E3786", {"start": v(121.43, -160.19) * mm, "end": v(121.22, -160.04) * mm});
            skLineSegment(sketch, "E3787", {"start": v(121.22, -160.04) * mm, "end": v(121.04, -159.87) * mm});
            skLineSegment(sketch, "E3788", {"start": v(121.04, -159.87) * mm, "end": v(120.88, -159.68) * mm});
            skLineSegment(sketch, "E3789", {"start": v(120.88, -159.68) * mm, "end": v(120.75, -159.46) * mm});
            skLineSegment(sketch, "E3790", {"start": v(120.75, -159.46) * mm, "end": v(120.64, -159.24) * mm});
            skLineSegment(sketch, "E3791", {"start": v(120.64, -159.24) * mm, "end": v(120.56, -159) * mm});
            skLineSegment(sketch, "E3792", {"start": v(120.56, -159) * mm, "end": v(120.52, -158.75) * mm});
            skLineSegment(sketch, "E3793", {"start": v(120.52, -158.75) * mm, "end": v(120.5, -158.5) * mm});
            skLineSegment(sketch, "E3794", {"start": v(120.5, -158.5) * mm, "end": v(120.52, -158.25) * mm});
            skLineSegment(sketch, "E3795", {"start": v(120.52, -158.25) * mm, "end": v(120.56, -158) * mm});
            skLineSegment(sketch, "E3796", {"start": v(120.56, -158) * mm, "end": v(120.64, -157.76) * mm});
            skLineSegment(sketch, "E3797", {"start": v(120.64, -157.76) * mm, "end": v(120.75, -157.54) * mm});
            skLineSegment(sketch, "E3798", {"start": v(120.75, -157.54) * mm, "end": v(120.88, -157.32) * mm});
            skLineSegment(sketch, "E3799", {"start": v(120.88, -157.32) * mm, "end": v(121.04, -157.13) * mm});
            skLineSegment(sketch, "E3800", {"start": v(121.04, -157.13) * mm, "end": v(121.22, -156.96) * mm});
            skLineSegment(sketch, "E3801", {"start": v(121.22, -156.96) * mm, "end": v(121.43, -156.81) * mm});
            skLineSegment(sketch, "E3802", {"start": v(121.43, -156.81) * mm, "end": v(121.65, -156.7) * mm});
            skLineSegment(sketch, "E3803", {"start": v(121.65, -156.7) * mm, "end": v(121.88, -156.6) * mm});
            skLineSegment(sketch, "E3804", {"start": v(121.88, -156.6) * mm, "end": v(122.12, -156.53) * mm});
            skLineSegment(sketch, "E3805", {"start": v(122.12, -156.53) * mm, "end": v(122.37, -156.5) * mm});
            skLineSegment(sketch, "E3806", {"start": v(122.37, -156.5) * mm, "end": v(122.63, -156.5) * mm});
            skLineSegment(sketch, "E3807", {"start": v(122.63, -156.5) * mm, "end": v(122.88, -156.53) * mm});
            skLineSegment(sketch, "E3808", {"start": v(122.88, -156.53) * mm, "end": v(123.12, -156.6) * mm});
            skLineSegment(sketch, "E3809", {"start": v(123.12, -156.6) * mm, "end": v(123.35, -156.7) * mm});
            skLineSegment(sketch, "E3810", {"start": v(123.35, -156.7) * mm, "end": v(123.57, -156.81) * mm});
            skLineSegment(sketch, "E3811", {"start": v(123.57, -156.81) * mm, "end": v(123.78, -156.96) * mm});
            skLineSegment(sketch, "E3812", {"start": v(123.78, -156.96) * mm, "end": v(123.96, -157.13) * mm});
            skLineSegment(sketch, "E3813", {"start": v(123.96, -157.13) * mm, "end": v(124.12, -157.32) * mm});
            skLineSegment(sketch, "E3814", {"start": v(124.12, -157.32) * mm, "end": v(124.25, -157.54) * mm});
            skLineSegment(sketch, "E3815", {"start": v(124.25, -157.54) * mm, "end": v(124.36, -157.76) * mm});
            skLineSegment(sketch, "E3816", {"start": v(124.36, -157.76) * mm, "end": v(124.44, -158) * mm});
            skLineSegment(sketch, "E3817", {"start": v(124.44, -158) * mm, "end": v(124.48, -158.25) * mm});
            skLineSegment(sketch, "E3818", {"start": v(124.48, -158.25) * mm, "end": v(124.5, -158.5) * mm});
            skLineSegment(sketch, "E3819", {"start": v(124.5, -158.5) * mm, "end": v(124.48, -158.75) * mm});
            skLineSegment(sketch, "E3820", {"start": v(124.48, -158.75) * mm, "end": v(124.44, -159) * mm});
            skLineSegment(sketch, "E3821", {"start": v(124.44, -159) * mm, "end": v(124.36, -159.24) * mm});
            skLineSegment(sketch, "E3822", {"start": v(124.36, -159.24) * mm, "end": v(124.25, -159.46) * mm});
            skLineSegment(sketch, "E3823", {"start": v(124.25, -159.46) * mm, "end": v(124.12, -159.68) * mm});
            skLineSegment(sketch, "E3824", {"start": v(124.12, -159.68) * mm, "end": v(123.96, -159.87) * mm});
            skLineSegment(sketch, "E3825", {"start": v(123.96, -159.87) * mm, "end": v(123.78, -160.04) * mm});
            skLineSegment(sketch, "E3826", {"start": v(123.78, -160.04) * mm, "end": v(123.57, -160.19) * mm});
            skLineSegment(sketch, "E3827", {"start": v(123.57, -160.19) * mm, "end": v(123.35, -160.3) * mm});
            skLineSegment(sketch, "E3828", {"start": v(123.35, -160.3) * mm, "end": v(123.12, -160.4) * mm});
            skLineSegment(sketch, "E3829", {"start": v(123.12, -160.4) * mm, "end": v(122.88, -160.47) * mm});
            skLineSegment(sketch, "E3830", {"start": v(122.88, -160.47) * mm, "end": v(122.63, -160.5) * mm});
            skLineSegment(sketch, "E3831", {"start": v(122.63, -160.5) * mm, "end": v(122.37, -160.5) * mm});
            skLineSegment(sketch, "E3832", {"start": v(-368.75, -176.92) * mm, "end": v(-367.51, -176.69) * mm});
            skLineSegment(sketch, "E3833", {"start": v(-367.51, -176.69) * mm, "end": v(-366.32, -176.3) * mm});
            skLineSegment(sketch, "E3834", {"start": v(-366.32, -176.3) * mm, "end": v(-365.18, -175.76) * mm});
            skLineSegment(sketch, "E3835", {"start": v(-365.18, -175.76) * mm, "end": v(-364.12, -175.1) * mm});
            skLineSegment(sketch, "E3836", {"start": v(-364.12, -175.1) * mm, "end": v(-363.16, -174.29) * mm});
            skLineSegment(sketch, "E3837", {"start": v(-363.16, -174.29) * mm, "end": v(-362.3, -173.37) * mm});
            skLineSegment(sketch, "E3838", {"start": v(-362.3, -173.37) * mm, "end": v(-361.56, -172.36) * mm});
            skLineSegment(sketch, "E3839", {"start": v(-361.56, -172.36) * mm, "end": v(-360.95, -171.26) * mm});
            skLineSegment(sketch, "E3840", {"start": v(-360.95, -171.26) * mm, "end": v(-360.49, -170.1) * mm});
            skLineSegment(sketch, "E3841", {"start": v(-360.49, -170.1) * mm, "end": v(-360.18, -168.87) * mm});
            skLineSegment(sketch, "E3842", {"start": v(-360.18, -168.87) * mm, "end": v(-360.02, -167.63) * mm});
            skLineSegment(sketch, "E3843", {"start": v(-360.02, -167.63) * mm, "end": v(-360.02, -167) * mm});
            skLineSegment(sketch, "E3844", {"start": v(-360.02, -167) * mm, "end": v(-360, -167) * mm});
            skLineSegment(sketch, "E3845", {"start": v(-360, -167) * mm, "end": v(-360, -117) * mm});
            skLineSegment(sketch, "E3846", {"start": v(-360, -117) * mm, "end": v(-340, -117) * mm});
            skLineSegment(sketch, "E3847", {"start": v(-340, -117) * mm, "end": v(-340, 193) * mm});
            skLineSegment(sketch, "E3848", {"start": v(-340, 193) * mm, "end": v(-339.98, 193) * mm});
            skLineSegment(sketch, "E3849", {"start": v(-339.98, 193) * mm, "end": v(-339.98, 193.63) * mm});
            skLineSegment(sketch, "E3850", {"start": v(-339.98, 193.63) * mm, "end": v(-339.82, 194.87) * mm});
            skLineSegment(sketch, "E3851", {"start": v(-339.82, 194.87) * mm, "end": v(-339.51, 196.1) * mm});
            skLineSegment(sketch, "E3852", {"start": v(-339.51, 196.1) * mm, "end": v(-339.05, 197.26) * mm});
            skLineSegment(sketch, "E3853", {"start": v(-339.05, 197.26) * mm, "end": v(-338.44, 198.36) * mm});
            skLineSegment(sketch, "E3854", {"start": v(-338.44, 198.36) * mm, "end": v(-337.7, 199.37) * mm});
            skLineSegment(sketch, "E3855", {"start": v(-337.7, 199.37) * mm, "end": v(-336.85, 200.29) * mm});
            skLineSegment(sketch, "E3856", {"start": v(-336.85, 200.29) * mm, "end": v(-335.88, 201.1) * mm});
            skLineSegment(sketch, "E3857", {"start": v(-335.88, 201.1) * mm, "end": v(-334.82, 201.76) * mm});
            skLineSegment(sketch, "E3858", {"start": v(-334.82, 201.76) * mm, "end": v(-333.68, 202.3) * mm});
            skLineSegment(sketch, "E3859", {"start": v(-333.68, 202.3) * mm, "end": v(-332.49, 202.69) * mm});
            skLineSegment(sketch, "E3860", {"start": v(-332.49, 202.69) * mm, "end": v(-331.25, 202.92) * mm});
            skLineSegment(sketch, "E3861", {"start": v(-331.25, 202.92) * mm, "end": v(-330, 203) * mm});
            skLineSegment(sketch, "E3862", {"start": v(-330, 203) * mm, "end": v(-80, 203) * mm});
            skLineSegment(sketch, "E3863", {"start": v(-80, 203) * mm, "end": v(-80, 202.98) * mm});
            skLineSegment(sketch, "E3864", {"start": v(-80, 202.98) * mm, "end": v(-79.37, 202.98) * mm});
            skLineSegment(sketch, "E3865", {"start": v(-79.37, 202.98) * mm, "end": v(-78.13, 202.82) * mm});
            skLineSegment(sketch, "E3866", {"start": v(-78.13, 202.82) * mm, "end": v(-76.9, 202.51) * mm});
            skLineSegment(sketch, "E3867", {"start": v(-76.9, 202.51) * mm, "end": v(-75.74, 202.05) * mm});
            skLineSegment(sketch, "E3868", {"start": v(-75.74, 202.05) * mm, "end": v(-74.64, 201.44) * mm});
            skLineSegment(sketch, "E3869", {"start": v(-74.64, 201.44) * mm, "end": v(-73.63, 200.7) * mm});
            skLineSegment(sketch, "E3870", {"start": v(-73.63, 200.7) * mm, "end": v(-72.71, 199.84) * mm});
            skLineSegment(sketch, "E3871", {"start": v(-72.71, 199.84) * mm, "end": v(-71.9, 198.88) * mm});
            skLineSegment(sketch, "E3872", {"start": v(-71.9, 198.88) * mm, "end": v(-71.24, 197.82) * mm});
            skLineSegment(sketch, "E3873", {"start": v(-71.24, 197.82) * mm, "end": v(-70.7, 196.68) * mm});
            skLineSegment(sketch, "E3874", {"start": v(-70.7, 196.68) * mm, "end": v(-70.31, 195.49) * mm});
            skLineSegment(sketch, "E3875", {"start": v(-70.31, 195.49) * mm, "end": v(-70.08, 194.25) * mm});
            skLineSegment(sketch, "E3876", {"start": v(-70.08, 194.25) * mm, "end": v(-70, 193) * mm});
            skLineSegment(sketch, "E3877", {"start": v(-70, 193) * mm, "end": v(-70, -117) * mm});
            skLineSegment(sketch, "E3878", {"start": v(-70, -117) * mm, "end": v(-50, -117) * mm});
            skLineSegment(sketch, "E3879", {"start": v(-50, -117) * mm, "end": v(-50, -167) * mm});
            skLineSegment(sketch, "E3880", {"start": v(-50, -167) * mm, "end": v(-49.92, -168.25) * mm});
            skLineSegment(sketch, "E3881", {"start": v(-49.92, -168.25) * mm, "end": v(-49.69, -169.49) * mm});
            skLineSegment(sketch, "E3882", {"start": v(-49.69, -169.49) * mm, "end": v(-49.3, -170.68) * mm});
            skLineSegment(sketch, "E3883", {"start": v(-49.3, -170.68) * mm, "end": v(-48.76, -171.82) * mm});
            skLineSegment(sketch, "E3884", {"start": v(-48.76, -171.82) * mm, "end": v(-48.1, -172.88) * mm});
            skLineSegment(sketch, "E3885", {"start": v(-48.1, -172.88) * mm, "end": v(-47.29, -173.85) * mm});
            skLineSegment(sketch, "E3886", {"start": v(-47.29, -173.85) * mm, "end": v(-46.37, -174.7) * mm});
            skLineSegment(sketch, "E3887", {"start": v(-46.37, -174.7) * mm, "end": v(-45.36, -175.44) * mm});
            skLineSegment(sketch, "E3888", {"start": v(-45.36, -175.44) * mm, "end": v(-44.26, -176.05) * mm});
            skLineSegment(sketch, "E3889", {"start": v(-44.26, -176.05) * mm, "end": v(-43.1, -176.51) * mm});
            skLineSegment(sketch, "E3890", {"start": v(-43.1, -176.51) * mm, "end": v(-41.87, -176.82) * mm});
            skLineSegment(sketch, "E3891", {"start": v(-41.87, -176.82) * mm, "end": v(-40.63, -176.98) * mm});
            skLineSegment(sketch, "E3892", {"start": v(-40.63, -176.98) * mm, "end": v(-40, -176.98) * mm});
            skLineSegment(sketch, "E3893", {"start": v(-40, -176.98) * mm, "end": v(-40, -177) * mm});
            skLineSegment(sketch, "E3894", {"start": v(-40, -177) * mm, "end": v(-20, -177) * mm});
            skLineSegment(sketch, "E3895", {"start": v(-20, -177) * mm, "end": v(-18.75, -176.92) * mm});
            skLineSegment(sketch, "E3896", {"start": v(-18.75, -176.92) * mm, "end": v(-17.51, -176.69) * mm});
            skLineSegment(sketch, "E3897", {"start": v(-17.51, -176.69) * mm, "end": v(-16.32, -176.3) * mm});
            skLineSegment(sketch, "E3898", {"start": v(-16.32, -176.3) * mm, "end": v(-15.18, -175.76) * mm});
            skLineSegment(sketch, "E3899", {"start": v(-15.18, -175.76) * mm, "end": v(-14.12, -175.1) * mm});
            skLineSegment(sketch, "E3900", {"start": v(-14.12, -175.1) * mm, "end": v(-13.15, -174.29) * mm});
            skLineSegment(sketch, "E3901", {"start": v(-13.15, -174.29) * mm, "end": v(-12.3, -173.37) * mm});
            skLineSegment(sketch, "E3902", {"start": v(-12.3, -173.37) * mm, "end": v(-11.56, -172.36) * mm});
            skLineSegment(sketch, "E3903", {"start": v(-11.56, -172.36) * mm, "end": v(-10.95, -171.26) * mm});
            skLineSegment(sketch, "E3904", {"start": v(-10.95, -171.26) * mm, "end": v(-10.49, -170.1) * mm});
            skLineSegment(sketch, "E3905", {"start": v(-10.49, -170.1) * mm, "end": v(-10.18, -168.87) * mm});
            skLineSegment(sketch, "E3906", {"start": v(-10.18, -168.87) * mm, "end": v(-10.02, -167.63) * mm});
            skLineSegment(sketch, "E3907", {"start": v(-10.02, -167.63) * mm, "end": v(-10.02, -167) * mm});
            skLineSegment(sketch, "E3908", {"start": v(-10.02, -167) * mm, "end": v(-10, -167) * mm});
            skLineSegment(sketch, "E3909", {"start": v(-10, -167) * mm, "end": v(-10, 253) * mm});
            skLineSegment(sketch, "E3910", {"start": v(-10, 253) * mm, "end": v(-10.08, 254.25) * mm});
            skLineSegment(sketch, "E3911", {"start": v(-10.08, 254.25) * mm, "end": v(-10.31, 255.49) * mm});
            skLineSegment(sketch, "E3912", {"start": v(-10.31, 255.49) * mm, "end": v(-10.7, 256.68) * mm});
            skLineSegment(sketch, "E3913", {"start": v(-10.7, 256.68) * mm, "end": v(-11.24, 257.82) * mm});
            skLineSegment(sketch, "E3914", {"start": v(-11.24, 257.82) * mm, "end": v(-11.9, 258.88) * mm});
            skLineSegment(sketch, "E3915", {"start": v(-11.9, 258.88) * mm, "end": v(-12.71, 259.85) * mm});
            skLineSegment(sketch, "E3916", {"start": v(-12.71, 259.85) * mm, "end": v(-13.63, 260.7) * mm});
            skLineSegment(sketch, "E3917", {"start": v(-13.63, 260.7) * mm, "end": v(-14.64, 261.44) * mm});
            skLineSegment(sketch, "E3918", {"start": v(-14.64, 261.44) * mm, "end": v(-15.74, 262.05) * mm});
            skLineSegment(sketch, "E3919", {"start": v(-15.74, 262.05) * mm, "end": v(-16.9, 262.51) * mm});
            skLineSegment(sketch, "E3920", {"start": v(-16.9, 262.51) * mm, "end": v(-18.13, 262.82) * mm});
            skLineSegment(sketch, "E3921", {"start": v(-18.13, 262.82) * mm, "end": v(-19.37, 262.98) * mm});
            skLineSegment(sketch, "E3922", {"start": v(-19.37, 262.98) * mm, "end": v(-20, 262.98) * mm});
            skLineSegment(sketch, "E3923", {"start": v(-20, 262.98) * mm, "end": v(-20, 263) * mm});
            skLineSegment(sketch, "E3924", {"start": v(-20, 263) * mm, "end": v(-390, 263) * mm});
            skLineSegment(sketch, "E3925", {"start": v(-390, 263) * mm, "end": v(-391.25, 262.92) * mm});
            skLineSegment(sketch, "E3926", {"start": v(-391.25, 262.92) * mm, "end": v(-392.49, 262.69) * mm});
            skLineSegment(sketch, "E3927", {"start": v(-392.49, 262.69) * mm, "end": v(-393.68, 262.3) * mm});
            skLineSegment(sketch, "E3928", {"start": v(-393.68, 262.3) * mm, "end": v(-394.82, 261.76) * mm});
            skLineSegment(sketch, "E3929", {"start": v(-394.82, 261.76) * mm, "end": v(-395.88, 261.09) * mm});
            skLineSegment(sketch, "E3930", {"start": v(-395.88, 261.09) * mm, "end": v(-396.85, 260.3) * mm});
            skLineSegment(sketch, "E3931", {"start": v(-396.85, 260.3) * mm, "end": v(-397.7, 259.37) * mm});
            skLineSegment(sketch, "E3932", {"start": v(-397.7, 259.37) * mm, "end": v(-398.44, 258.36) * mm});
            skLineSegment(sketch, "E3933", {"start": v(-398.44, 258.36) * mm, "end": v(-399.05, 257.26) * mm});
            skLineSegment(sketch, "E3934", {"start": v(-399.05, 257.26) * mm, "end": v(-399.51, 256.09) * mm});
            skLineSegment(sketch, "E3935", {"start": v(-399.51, 256.09) * mm, "end": v(-399.82, 254.87) * mm});
            skLineSegment(sketch, "E3936", {"start": v(-399.82, 254.87) * mm, "end": v(-399.98, 253.63) * mm});
            skLineSegment(sketch, "E3937", {"start": v(-399.98, 253.63) * mm, "end": v(-399.98, 253) * mm});
            skLineSegment(sketch, "E3938", {"start": v(-399.98, 253) * mm, "end": v(-400, 253) * mm});
            skLineSegment(sketch, "E3939", {"start": v(-400, 253) * mm, "end": v(-400, -167) * mm});
            skLineSegment(sketch, "E3940", {"start": v(-400, -167) * mm, "end": v(-399.92, -168.25) * mm});
            skLineSegment(sketch, "E3941", {"start": v(-399.92, -168.25) * mm, "end": v(-399.69, -169.49) * mm});
            skLineSegment(sketch, "E3942", {"start": v(-399.69, -169.49) * mm, "end": v(-399.3, -170.68) * mm});
            skLineSegment(sketch, "E3943", {"start": v(-399.3, -170.68) * mm, "end": v(-398.76, -171.82) * mm});
            skLineSegment(sketch, "E3944", {"start": v(-398.76, -171.82) * mm, "end": v(-398.09, -172.88) * mm});
            skLineSegment(sketch, "E3945", {"start": v(-398.09, -172.88) * mm, "end": v(-397.3, -173.85) * mm});
            skLineSegment(sketch, "E3946", {"start": v(-397.3, -173.85) * mm, "end": v(-396.37, -174.7) * mm});
            skLineSegment(sketch, "E3947", {"start": v(-396.37, -174.7) * mm, "end": v(-395.36, -175.44) * mm});
            skLineSegment(sketch, "E3948", {"start": v(-395.36, -175.44) * mm, "end": v(-394.26, -176.05) * mm});
            skLineSegment(sketch, "E3949", {"start": v(-394.26, -176.05) * mm, "end": v(-393.09, -176.51) * mm});
            skLineSegment(sketch, "E3950", {"start": v(-393.09, -176.51) * mm, "end": v(-391.87, -176.82) * mm});
            skLineSegment(sketch, "E3951", {"start": v(-391.87, -176.82) * mm, "end": v(-390.63, -176.98) * mm});
            skLineSegment(sketch, "E3952", {"start": v(-390.63, -176.98) * mm, "end": v(-390, -176.98) * mm});
            skLineSegment(sketch, "E3953", {"start": v(-390, -176.98) * mm, "end": v(-390, -177) * mm});
            skLineSegment(sketch, "E3954", {"start": v(-390, -177) * mm, "end": v(-370, -177) * mm});
            skLineSegment(sketch, "E3955", {"start": v(-370, -177) * mm, "end": v(-368.75, -176.92) * mm});
            skLineSegment(sketch, "E3956", {"start": v(-387.1, 249.5) * mm, "end": v(-387.28, 249.53) * mm});
            skLineSegment(sketch, "E3957", {"start": v(-387.28, 249.53) * mm, "end": v(-387.46, 249.57) * mm});
            skLineSegment(sketch, "E3958", {"start": v(-387.46, 249.57) * mm, "end": v(-387.64, 249.64) * mm});
            skLineSegment(sketch, "E3959", {"start": v(-387.64, 249.64) * mm, "end": v(-387.8, 249.73) * mm});
            skLineSegment(sketch, "E3960", {"start": v(-387.8, 249.73) * mm, "end": v(-387.96, 249.84) * mm});
            skLineSegment(sketch, "E3961", {"start": v(-387.96, 249.84) * mm, "end": v(-388.1, 249.97) * mm});
            skLineSegment(sketch, "E3962", {"start": v(-388.1, 249.97) * mm, "end": v(-388.21, 250.12) * mm});
            skLineSegment(sketch, "E3963", {"start": v(-388.21, 250.12) * mm, "end": v(-388.31, 250.28) * mm});
            skLineSegment(sketch, "E3964", {"start": v(-388.31, 250.28) * mm, "end": v(-388.4, 250.45) * mm});
            skLineSegment(sketch, "E3965", {"start": v(-388.4, 250.45) * mm, "end": v(-388.45, 250.63) * mm});
            skLineSegment(sketch, "E3966", {"start": v(-388.45, 250.63) * mm, "end": v(-388.49, 250.81) * mm});
            skLineSegment(sketch, "E3967", {"start": v(-388.49, 250.81) * mm, "end": v(-388.5, 251) * mm});
            skLineSegment(sketch, "E3968", {"start": v(-388.5, 251) * mm, "end": v(-388.49, 251.19) * mm});
            skLineSegment(sketch, "E3969", {"start": v(-388.49, 251.19) * mm, "end": v(-388.45, 251.37) * mm});
            skLineSegment(sketch, "E3970", {"start": v(-388.45, 251.37) * mm, "end": v(-388.4, 251.55) * mm});
            skLineSegment(sketch, "E3971", {"start": v(-388.4, 251.55) * mm, "end": v(-388.31, 251.72) * mm});
            skLineSegment(sketch, "E3972", {"start": v(-388.31, 251.72) * mm, "end": v(-388.21, 251.88) * mm});
            skLineSegment(sketch, "E3973", {"start": v(-388.21, 251.88) * mm, "end": v(-388.1, 252.03) * mm});
            skLineSegment(sketch, "E3974", {"start": v(-388.1, 252.03) * mm, "end": v(-387.96, 252.16) * mm});
            skLineSegment(sketch, "E3975", {"start": v(-387.96, 252.16) * mm, "end": v(-387.8, 252.27) * mm});
            skLineSegment(sketch, "E3976", {"start": v(-387.8, 252.27) * mm, "end": v(-387.64, 252.36) * mm});
            skLineSegment(sketch, "E3977", {"start": v(-387.64, 252.36) * mm, "end": v(-387.46, 252.43) * mm});
            skLineSegment(sketch, "E3978", {"start": v(-387.46, 252.43) * mm, "end": v(-387.28, 252.47) * mm});
            skLineSegment(sketch, "E3979", {"start": v(-387.28, 252.47) * mm, "end": v(-387.1, 252.5) * mm});
            skLineSegment(sketch, "E3980", {"start": v(-387.1, 252.5) * mm, "end": v(-386.9, 252.5) * mm});
            skLineSegment(sketch, "E3981", {"start": v(-386.9, 252.5) * mm, "end": v(-386.72, 252.47) * mm});
            skLineSegment(sketch, "E3982", {"start": v(-386.72, 252.47) * mm, "end": v(-386.54, 252.43) * mm});
            skLineSegment(sketch, "E3983", {"start": v(-386.54, 252.43) * mm, "end": v(-386.36, 252.36) * mm});
            skLineSegment(sketch, "E3984", {"start": v(-386.36, 252.36) * mm, "end": v(-386.2, 252.27) * mm});
            skLineSegment(sketch, "E3985", {"start": v(-386.2, 252.27) * mm, "end": v(-386.04, 252.16) * mm});
            skLineSegment(sketch, "E3986", {"start": v(-386.04, 252.16) * mm, "end": v(-385.9, 252.03) * mm});
            skLineSegment(sketch, "E3987", {"start": v(-385.9, 252.03) * mm, "end": v(-385.79, 251.88) * mm});
            skLineSegment(sketch, "E3988", {"start": v(-385.79, 251.88) * mm, "end": v(-385.69, 251.72) * mm});
            skLineSegment(sketch, "E3989", {"start": v(-385.69, 251.72) * mm, "end": v(-385.6, 251.55) * mm});
            skLineSegment(sketch, "E3990", {"start": v(-385.6, 251.55) * mm, "end": v(-385.55, 251.37) * mm});
            skLineSegment(sketch, "E3991", {"start": v(-385.55, 251.37) * mm, "end": v(-385.51, 251.19) * mm});
            skLineSegment(sketch, "E3992", {"start": v(-385.51, 251.19) * mm, "end": v(-385.5, 251) * mm});
            skLineSegment(sketch, "E3993", {"start": v(-385.5, 251) * mm, "end": v(-385.51, 250.81) * mm});
            skLineSegment(sketch, "E3994", {"start": v(-385.51, 250.81) * mm, "end": v(-385.55, 250.63) * mm});
            skLineSegment(sketch, "E3995", {"start": v(-385.55, 250.63) * mm, "end": v(-385.6, 250.45) * mm});
            skLineSegment(sketch, "E3996", {"start": v(-385.6, 250.45) * mm, "end": v(-385.69, 250.28) * mm});
            skLineSegment(sketch, "E3997", {"start": v(-385.69, 250.28) * mm, "end": v(-385.79, 250.12) * mm});
            skLineSegment(sketch, "E3998", {"start": v(-385.79, 250.12) * mm, "end": v(-385.9, 249.97) * mm});
            skLineSegment(sketch, "E3999", {"start": v(-385.9, 249.97) * mm, "end": v(-386.04, 249.84) * mm});
            skLineSegment(sketch, "E4000", {"start": v(-386.04, 249.84) * mm, "end": v(-386.2, 249.73) * mm});
            skLineSegment(sketch, "E4001", {"start": v(-386.2, 249.73) * mm, "end": v(-386.36, 249.64) * mm});
            skLineSegment(sketch, "E4002", {"start": v(-386.36, 249.64) * mm, "end": v(-386.54, 249.57) * mm});
            skLineSegment(sketch, "E4003", {"start": v(-386.54, 249.57) * mm, "end": v(-386.72, 249.53) * mm});
            skLineSegment(sketch, "E4004", {"start": v(-386.72, 249.53) * mm, "end": v(-386.9, 249.5) * mm});
            skLineSegment(sketch, "E4005", {"start": v(-386.9, 249.5) * mm, "end": v(-387.1, 249.5) * mm});
            skLineSegment(sketch, "E4006", {"start": v(-367.1, 249.5) * mm, "end": v(-367.28, 249.53) * mm});
            skLineSegment(sketch, "E4007", {"start": v(-367.28, 249.53) * mm, "end": v(-367.46, 249.57) * mm});
            skLineSegment(sketch, "E4008", {"start": v(-367.46, 249.57) * mm, "end": v(-367.64, 249.64) * mm});
            skLineSegment(sketch, "E4009", {"start": v(-367.64, 249.64) * mm, "end": v(-367.8, 249.73) * mm});
            skLineSegment(sketch, "E4010", {"start": v(-367.8, 249.73) * mm, "end": v(-367.96, 249.84) * mm});
            skLineSegment(sketch, "E4011", {"start": v(-367.96, 249.84) * mm, "end": v(-368.1, 249.97) * mm});
            skLineSegment(sketch, "E4012", {"start": v(-368.1, 249.97) * mm, "end": v(-368.21, 250.12) * mm});
            skLineSegment(sketch, "E4013", {"start": v(-368.21, 250.12) * mm, "end": v(-368.31, 250.28) * mm});
            skLineSegment(sketch, "E4014", {"start": v(-368.31, 250.28) * mm, "end": v(-368.4, 250.45) * mm});
            skLineSegment(sketch, "E4015", {"start": v(-368.4, 250.45) * mm, "end": v(-368.45, 250.63) * mm});
            skLineSegment(sketch, "E4016", {"start": v(-368.45, 250.63) * mm, "end": v(-368.49, 250.81) * mm});
            skLineSegment(sketch, "E4017", {"start": v(-368.49, 250.81) * mm, "end": v(-368.5, 251) * mm});
            skLineSegment(sketch, "E4018", {"start": v(-368.5, 251) * mm, "end": v(-368.49, 251.19) * mm});
            skLineSegment(sketch, "E4019", {"start": v(-368.49, 251.19) * mm, "end": v(-368.45, 251.37) * mm});
            skLineSegment(sketch, "E4020", {"start": v(-368.45, 251.37) * mm, "end": v(-368.4, 251.55) * mm});
            skLineSegment(sketch, "E4021", {"start": v(-368.4, 251.55) * mm, "end": v(-368.31, 251.72) * mm});
            skLineSegment(sketch, "E4022", {"start": v(-368.31, 251.72) * mm, "end": v(-368.21, 251.88) * mm});
            skLineSegment(sketch, "E4023", {"start": v(-368.21, 251.88) * mm, "end": v(-368.1, 252.03) * mm});
            skLineSegment(sketch, "E4024", {"start": v(-368.1, 252.03) * mm, "end": v(-367.96, 252.16) * mm});
            skLineSegment(sketch, "E4025", {"start": v(-367.96, 252.16) * mm, "end": v(-367.8, 252.27) * mm});
            skLineSegment(sketch, "E4026", {"start": v(-367.8, 252.27) * mm, "end": v(-367.64, 252.36) * mm});
            skLineSegment(sketch, "E4027", {"start": v(-367.64, 252.36) * mm, "end": v(-367.46, 252.43) * mm});
            skLineSegment(sketch, "E4028", {"start": v(-367.46, 252.43) * mm, "end": v(-367.28, 252.47) * mm});
            skLineSegment(sketch, "E4029", {"start": v(-367.28, 252.47) * mm, "end": v(-367.1, 252.5) * mm});
            skLineSegment(sketch, "E4030", {"start": v(-367.1, 252.5) * mm, "end": v(-366.9, 252.5) * mm});
            skLineSegment(sketch, "E4031", {"start": v(-366.9, 252.5) * mm, "end": v(-366.72, 252.47) * mm});
            skLineSegment(sketch, "E4032", {"start": v(-366.72, 252.47) * mm, "end": v(-366.54, 252.43) * mm});
            skLineSegment(sketch, "E4033", {"start": v(-366.54, 252.43) * mm, "end": v(-366.36, 252.36) * mm});
            skLineSegment(sketch, "E4034", {"start": v(-366.36, 252.36) * mm, "end": v(-366.2, 252.27) * mm});
            skLineSegment(sketch, "E4035", {"start": v(-366.2, 252.27) * mm, "end": v(-366.04, 252.16) * mm});
            skLineSegment(sketch, "E4036", {"start": v(-366.04, 252.16) * mm, "end": v(-365.9, 252.03) * mm});
            skLineSegment(sketch, "E4037", {"start": v(-365.9, 252.03) * mm, "end": v(-365.79, 251.88) * mm});
            skLineSegment(sketch, "E4038", {"start": v(-365.79, 251.88) * mm, "end": v(-365.69, 251.72) * mm});
            skLineSegment(sketch, "E4039", {"start": v(-365.69, 251.72) * mm, "end": v(-365.6, 251.55) * mm});
            skLineSegment(sketch, "E4040", {"start": v(-365.6, 251.55) * mm, "end": v(-365.55, 251.37) * mm});
            skLineSegment(sketch, "E4041", {"start": v(-365.55, 251.37) * mm, "end": v(-365.51, 251.19) * mm});
            skLineSegment(sketch, "E4042", {"start": v(-365.51, 251.19) * mm, "end": v(-365.5, 251) * mm});
            skLineSegment(sketch, "E4043", {"start": v(-365.5, 251) * mm, "end": v(-365.51, 250.81) * mm});
            skLineSegment(sketch, "E4044", {"start": v(-365.51, 250.81) * mm, "end": v(-365.55, 250.63) * mm});
            skLineSegment(sketch, "E4045", {"start": v(-365.55, 250.63) * mm, "end": v(-365.6, 250.45) * mm});
            skLineSegment(sketch, "E4046", {"start": v(-365.6, 250.45) * mm, "end": v(-365.69, 250.28) * mm});
            skLineSegment(sketch, "E4047", {"start": v(-365.69, 250.28) * mm, "end": v(-365.79, 250.12) * mm});
            skLineSegment(sketch, "E4048", {"start": v(-365.79, 250.12) * mm, "end": v(-365.9, 249.97) * mm});
            skLineSegment(sketch, "E4049", {"start": v(-365.9, 249.97) * mm, "end": v(-366.04, 249.84) * mm});
            skLineSegment(sketch, "E4050", {"start": v(-366.04, 249.84) * mm, "end": v(-366.2, 249.73) * mm});
            skLineSegment(sketch, "E4051", {"start": v(-366.2, 249.73) * mm, "end": v(-366.36, 249.64) * mm});
            skLineSegment(sketch, "E4052", {"start": v(-366.36, 249.64) * mm, "end": v(-366.54, 249.57) * mm});
            skLineSegment(sketch, "E4053", {"start": v(-366.54, 249.57) * mm, "end": v(-366.72, 249.53) * mm});
            skLineSegment(sketch, "E4054", {"start": v(-366.72, 249.53) * mm, "end": v(-366.9, 249.5) * mm});
            skLineSegment(sketch, "E4055", {"start": v(-366.9, 249.5) * mm, "end": v(-367.1, 249.5) * mm});
            skLineSegment(sketch, "E4056", {"start": v(-43.1, 249.5) * mm, "end": v(-43.28, 249.53) * mm});
            skLineSegment(sketch, "E4057", {"start": v(-43.28, 249.53) * mm, "end": v(-43.46, 249.57) * mm});
            skLineSegment(sketch, "E4058", {"start": v(-43.46, 249.57) * mm, "end": v(-43.64, 249.64) * mm});
            skLineSegment(sketch, "E4059", {"start": v(-43.64, 249.64) * mm, "end": v(-43.8, 249.73) * mm});
            skLineSegment(sketch, "E4060", {"start": v(-43.8, 249.73) * mm, "end": v(-43.96, 249.84) * mm});
            skLineSegment(sketch, "E4061", {"start": v(-43.96, 249.84) * mm, "end": v(-44.1, 249.97) * mm});
            skLineSegment(sketch, "E4062", {"start": v(-44.1, 249.97) * mm, "end": v(-44.21, 250.12) * mm});
            skLineSegment(sketch, "E4063", {"start": v(-44.21, 250.12) * mm, "end": v(-44.31, 250.28) * mm});
            skLineSegment(sketch, "E4064", {"start": v(-44.31, 250.28) * mm, "end": v(-44.4, 250.45) * mm});
            skLineSegment(sketch, "E4065", {"start": v(-44.4, 250.45) * mm, "end": v(-44.45, 250.63) * mm});
            skLineSegment(sketch, "E4066", {"start": v(-44.45, 250.63) * mm, "end": v(-44.49, 250.81) * mm});
            skLineSegment(sketch, "E4067", {"start": v(-44.49, 250.81) * mm, "end": v(-44.5, 251) * mm});
            skLineSegment(sketch, "E4068", {"start": v(-44.5, 251) * mm, "end": v(-44.49, 251.19) * mm});
            skLineSegment(sketch, "E4069", {"start": v(-44.49, 251.19) * mm, "end": v(-44.45, 251.37) * mm});
            skLineSegment(sketch, "E4070", {"start": v(-44.45, 251.37) * mm, "end": v(-44.4, 251.55) * mm});
            skLineSegment(sketch, "E4071", {"start": v(-44.4, 251.55) * mm, "end": v(-44.31, 251.72) * mm});
            skLineSegment(sketch, "E4072", {"start": v(-44.31, 251.72) * mm, "end": v(-44.21, 251.88) * mm});
            skLineSegment(sketch, "E4073", {"start": v(-44.21, 251.88) * mm, "end": v(-44.1, 252.03) * mm});
            skLineSegment(sketch, "E4074", {"start": v(-44.1, 252.03) * mm, "end": v(-43.96, 252.16) * mm});
            skLineSegment(sketch, "E4075", {"start": v(-43.96, 252.16) * mm, "end": v(-43.8, 252.27) * mm});
            skLineSegment(sketch, "E4076", {"start": v(-43.8, 252.27) * mm, "end": v(-43.64, 252.36) * mm});
            skLineSegment(sketch, "E4077", {"start": v(-43.64, 252.36) * mm, "end": v(-43.46, 252.43) * mm});
            skLineSegment(sketch, "E4078", {"start": v(-43.46, 252.43) * mm, "end": v(-43.28, 252.47) * mm});
            skLineSegment(sketch, "E4079", {"start": v(-43.28, 252.47) * mm, "end": v(-43.1, 252.5) * mm});
            skLineSegment(sketch, "E4080", {"start": v(-43.1, 252.5) * mm, "end": v(-42.9, 252.5) * mm});
            skLineSegment(sketch, "E4081", {"start": v(-42.9, 252.5) * mm, "end": v(-42.72, 252.47) * mm});
            skLineSegment(sketch, "E4082", {"start": v(-42.72, 252.47) * mm, "end": v(-42.54, 252.43) * mm});
            skLineSegment(sketch, "E4083", {"start": v(-42.54, 252.43) * mm, "end": v(-42.36, 252.36) * mm});
            skLineSegment(sketch, "E4084", {"start": v(-42.36, 252.36) * mm, "end": v(-42.2, 252.27) * mm});
            skLineSegment(sketch, "E4085", {"start": v(-42.2, 252.27) * mm, "end": v(-42.04, 252.16) * mm});
            skLineSegment(sketch, "E4086", {"start": v(-42.04, 252.16) * mm, "end": v(-41.9, 252.03) * mm});
            skLineSegment(sketch, "E4087", {"start": v(-41.9, 252.03) * mm, "end": v(-41.79, 251.88) * mm});
            skLineSegment(sketch, "E4088", {"start": v(-41.79, 251.88) * mm, "end": v(-41.69, 251.72) * mm});
            skLineSegment(sketch, "E4089", {"start": v(-41.69, 251.72) * mm, "end": v(-41.6, 251.55) * mm});
            skLineSegment(sketch, "E4090", {"start": v(-41.6, 251.55) * mm, "end": v(-41.55, 251.37) * mm});
            skLineSegment(sketch, "E4091", {"start": v(-41.55, 251.37) * mm, "end": v(-41.51, 251.19) * mm});
            skLineSegment(sketch, "E4092", {"start": v(-41.51, 251.19) * mm, "end": v(-41.5, 251) * mm});
            skLineSegment(sketch, "E4093", {"start": v(-41.5, 251) * mm, "end": v(-41.51, 250.81) * mm});
            skLineSegment(sketch, "E4094", {"start": v(-41.51, 250.81) * mm, "end": v(-41.55, 250.63) * mm});
            skLineSegment(sketch, "E4095", {"start": v(-41.55, 250.63) * mm, "end": v(-41.6, 250.45) * mm});
            skLineSegment(sketch, "E4096", {"start": v(-41.6, 250.45) * mm, "end": v(-41.69, 250.28) * mm});
            skLineSegment(sketch, "E4097", {"start": v(-41.69, 250.28) * mm, "end": v(-41.79, 250.12) * mm});
            skLineSegment(sketch, "E4098", {"start": v(-41.79, 250.12) * mm, "end": v(-41.9, 249.97) * mm});
            skLineSegment(sketch, "E4099", {"start": v(-41.9, 249.97) * mm, "end": v(-42.04, 249.84) * mm});
            skLineSegment(sketch, "E4100", {"start": v(-42.04, 249.84) * mm, "end": v(-42.2, 249.73) * mm});
            skLineSegment(sketch, "E4101", {"start": v(-42.2, 249.73) * mm, "end": v(-42.36, 249.64) * mm});
            skLineSegment(sketch, "E4102", {"start": v(-42.36, 249.64) * mm, "end": v(-42.54, 249.57) * mm});
            skLineSegment(sketch, "E4103", {"start": v(-42.54, 249.57) * mm, "end": v(-42.72, 249.53) * mm});
            skLineSegment(sketch, "E4104", {"start": v(-42.72, 249.53) * mm, "end": v(-42.9, 249.5) * mm});
            skLineSegment(sketch, "E4105", {"start": v(-42.9, 249.5) * mm, "end": v(-43.1, 249.5) * mm});
            skLineSegment(sketch, "E4106", {"start": v(-23.1, 249.5) * mm, "end": v(-23.28, 249.53) * mm});
            skLineSegment(sketch, "E4107", {"start": v(-23.28, 249.53) * mm, "end": v(-23.46, 249.57) * mm});
            skLineSegment(sketch, "E4108", {"start": v(-23.46, 249.57) * mm, "end": v(-23.64, 249.64) * mm});
            skLineSegment(sketch, "E4109", {"start": v(-23.64, 249.64) * mm, "end": v(-23.8, 249.73) * mm});
            skLineSegment(sketch, "E4110", {"start": v(-23.8, 249.73) * mm, "end": v(-23.96, 249.84) * mm});
            skLineSegment(sketch, "E4111", {"start": v(-23.96, 249.84) * mm, "end": v(-24.1, 249.97) * mm});
            skLineSegment(sketch, "E4112", {"start": v(-24.1, 249.97) * mm, "end": v(-24.21, 250.12) * mm});
            skLineSegment(sketch, "E4113", {"start": v(-24.21, 250.12) * mm, "end": v(-24.31, 250.28) * mm});
            skLineSegment(sketch, "E4114", {"start": v(-24.31, 250.28) * mm, "end": v(-24.4, 250.45) * mm});
            skLineSegment(sketch, "E4115", {"start": v(-24.4, 250.45) * mm, "end": v(-24.45, 250.63) * mm});
            skLineSegment(sketch, "E4116", {"start": v(-24.45, 250.63) * mm, "end": v(-24.49, 250.81) * mm});
            skLineSegment(sketch, "E4117", {"start": v(-24.49, 250.81) * mm, "end": v(-24.5, 251) * mm});
            skLineSegment(sketch, "E4118", {"start": v(-24.5, 251) * mm, "end": v(-24.49, 251.19) * mm});
            skLineSegment(sketch, "E4119", {"start": v(-24.49, 251.19) * mm, "end": v(-24.45, 251.37) * mm});
            skLineSegment(sketch, "E4120", {"start": v(-24.45, 251.37) * mm, "end": v(-24.4, 251.55) * mm});
            skLineSegment(sketch, "E4121", {"start": v(-24.4, 251.55) * mm, "end": v(-24.31, 251.72) * mm});
            skLineSegment(sketch, "E4122", {"start": v(-24.31, 251.72) * mm, "end": v(-24.21, 251.88) * mm});
            skLineSegment(sketch, "E4123", {"start": v(-24.21, 251.88) * mm, "end": v(-24.1, 252.03) * mm});
            skLineSegment(sketch, "E4124", {"start": v(-24.1, 252.03) * mm, "end": v(-23.96, 252.16) * mm});
            skLineSegment(sketch, "E4125", {"start": v(-23.96, 252.16) * mm, "end": v(-23.8, 252.27) * mm});
            skLineSegment(sketch, "E4126", {"start": v(-23.8, 252.27) * mm, "end": v(-23.64, 252.36) * mm});
            skLineSegment(sketch, "E4127", {"start": v(-23.64, 252.36) * mm, "end": v(-23.46, 252.43) * mm});
            skLineSegment(sketch, "E4128", {"start": v(-23.46, 252.43) * mm, "end": v(-23.28, 252.47) * mm});
            skLineSegment(sketch, "E4129", {"start": v(-23.28, 252.47) * mm, "end": v(-23.1, 252.5) * mm});
            skLineSegment(sketch, "E4130", {"start": v(-23.1, 252.5) * mm, "end": v(-22.9, 252.5) * mm});
            skLineSegment(sketch, "E4131", {"start": v(-22.9, 252.5) * mm, "end": v(-22.72, 252.47) * mm});
            skLineSegment(sketch, "E4132", {"start": v(-22.72, 252.47) * mm, "end": v(-22.54, 252.43) * mm});
            skLineSegment(sketch, "E4133", {"start": v(-22.54, 252.43) * mm, "end": v(-22.36, 252.36) * mm});
            skLineSegment(sketch, "E4134", {"start": v(-22.36, 252.36) * mm, "end": v(-22.2, 252.27) * mm});
            skLineSegment(sketch, "E4135", {"start": v(-22.2, 252.27) * mm, "end": v(-22.04, 252.16) * mm});
            skLineSegment(sketch, "E4136", {"start": v(-22.04, 252.16) * mm, "end": v(-21.9, 252.03) * mm});
            skLineSegment(sketch, "E4137", {"start": v(-21.9, 252.03) * mm, "end": v(-21.79, 251.88) * mm});
            skLineSegment(sketch, "E4138", {"start": v(-21.79, 251.88) * mm, "end": v(-21.69, 251.72) * mm});
            skLineSegment(sketch, "E4139", {"start": v(-21.69, 251.72) * mm, "end": v(-21.6, 251.55) * mm});
            skLineSegment(sketch, "E4140", {"start": v(-21.6, 251.55) * mm, "end": v(-21.55, 251.37) * mm});
            skLineSegment(sketch, "E4141", {"start": v(-21.55, 251.37) * mm, "end": v(-21.51, 251.19) * mm});
            skLineSegment(sketch, "E4142", {"start": v(-21.51, 251.19) * mm, "end": v(-21.5, 251) * mm});
            skLineSegment(sketch, "E4143", {"start": v(-21.5, 251) * mm, "end": v(-21.51, 250.81) * mm});
            skLineSegment(sketch, "E4144", {"start": v(-21.51, 250.81) * mm, "end": v(-21.55, 250.63) * mm});
            skLineSegment(sketch, "E4145", {"start": v(-21.55, 250.63) * mm, "end": v(-21.6, 250.45) * mm});
            skLineSegment(sketch, "E4146", {"start": v(-21.6, 250.45) * mm, "end": v(-21.69, 250.28) * mm});
            skLineSegment(sketch, "E4147", {"start": v(-21.69, 250.28) * mm, "end": v(-21.79, 250.12) * mm});
            skLineSegment(sketch, "E4148", {"start": v(-21.79, 250.12) * mm, "end": v(-21.9, 249.97) * mm});
            skLineSegment(sketch, "E4149", {"start": v(-21.9, 249.97) * mm, "end": v(-22.04, 249.84) * mm});
            skLineSegment(sketch, "E4150", {"start": v(-22.04, 249.84) * mm, "end": v(-22.2, 249.73) * mm});
            skLineSegment(sketch, "E4151", {"start": v(-22.2, 249.73) * mm, "end": v(-22.36, 249.64) * mm});
            skLineSegment(sketch, "E4152", {"start": v(-22.36, 249.64) * mm, "end": v(-22.54, 249.57) * mm});
            skLineSegment(sketch, "E4153", {"start": v(-22.54, 249.57) * mm, "end": v(-22.72, 249.53) * mm});
            skLineSegment(sketch, "E4154", {"start": v(-22.72, 249.53) * mm, "end": v(-22.9, 249.5) * mm});
            skLineSegment(sketch, "E4155", {"start": v(-22.9, 249.5) * mm, "end": v(-23.1, 249.5) * mm});
            skLineSegment(sketch, "E4156", {"start": v(-48, 183) * mm, "end": v(-48, 203) * mm});
            skLineSegment(sketch, "E4157", {"start": v(-48, 203) * mm, "end": v(-32, 203) * mm});
            skLineSegment(sketch, "E4158", {"start": v(-32, 203) * mm, "end": v(-32, 183) * mm});
            skLineSegment(sketch, "E4159", {"start": v(-32, 183) * mm, "end": v(-48, 183) * mm});
            skLineSegment(sketch, "E4160", {"start": v(-378, 183) * mm, "end": v(-378, 203) * mm});
            skLineSegment(sketch, "E4161", {"start": v(-378, 203) * mm, "end": v(-362, 203) * mm});
            skLineSegment(sketch, "E4162", {"start": v(-362, 203) * mm, "end": v(-362, 183) * mm});
            skLineSegment(sketch, "E4163", {"start": v(-362, 183) * mm, "end": v(-378, 183) * mm});
            skLineSegment(sketch, "E4164", {"start": v(-40.13, 121) * mm, "end": v(-40.37, 121.03) * mm});
            skLineSegment(sketch, "E4165", {"start": v(-40.37, 121.03) * mm, "end": v(-40.62, 121.1) * mm});
            skLineSegment(sketch, "E4166", {"start": v(-40.62, 121.1) * mm, "end": v(-40.85, 121.2) * mm});
            skLineSegment(sketch, "E4167", {"start": v(-40.85, 121.2) * mm, "end": v(-41.07, 121.31) * mm});
            skLineSegment(sketch, "E4168", {"start": v(-41.07, 121.31) * mm, "end": v(-41.27, 121.46) * mm});
            skLineSegment(sketch, "E4169", {"start": v(-41.27, 121.46) * mm, "end": v(-41.46, 121.63) * mm});
            skLineSegment(sketch, "E4170", {"start": v(-41.46, 121.63) * mm, "end": v(-41.62, 121.82) * mm});
            skLineSegment(sketch, "E4171", {"start": v(-41.62, 121.82) * mm, "end": v(-41.75, 122.04) * mm});
            skLineSegment(sketch, "E4172", {"start": v(-41.75, 122.04) * mm, "end": v(-41.86, 122.26) * mm});
            skLineSegment(sketch, "E4173", {"start": v(-41.86, 122.26) * mm, "end": v(-41.94, 122.5) * mm});
            skLineSegment(sketch, "E4174", {"start": v(-41.94, 122.5) * mm, "end": v(-41.98, 122.75) * mm});
            skLineSegment(sketch, "E4175", {"start": v(-41.98, 122.75) * mm, "end": v(-42, 123) * mm});
            skLineSegment(sketch, "E4176", {"start": v(-42, 123) * mm, "end": v(-41.98, 123.25) * mm});
            skLineSegment(sketch, "E4177", {"start": v(-41.98, 123.25) * mm, "end": v(-41.94, 123.5) * mm});
            skLineSegment(sketch, "E4178", {"start": v(-41.94, 123.5) * mm, "end": v(-41.86, 123.74) * mm});
            skLineSegment(sketch, "E4179", {"start": v(-41.86, 123.74) * mm, "end": v(-41.75, 123.96) * mm});
            skLineSegment(sketch, "E4180", {"start": v(-41.75, 123.96) * mm, "end": v(-41.62, 124.18) * mm});
            skLineSegment(sketch, "E4181", {"start": v(-41.62, 124.18) * mm, "end": v(-41.46, 124.37) * mm});
            skLineSegment(sketch, "E4182", {"start": v(-41.46, 124.37) * mm, "end": v(-41.27, 124.54) * mm});
            skLineSegment(sketch, "E4183", {"start": v(-41.27, 124.54) * mm, "end": v(-41.07, 124.69) * mm});
            skLineSegment(sketch, "E4184", {"start": v(-41.07, 124.69) * mm, "end": v(-40.85, 124.81) * mm});
            skLineSegment(sketch, "E4185", {"start": v(-40.85, 124.81) * mm, "end": v(-40.62, 124.9) * mm});
            skLineSegment(sketch, "E4186", {"start": v(-40.62, 124.9) * mm, "end": v(-40.37, 124.97) * mm});
            skLineSegment(sketch, "E4187", {"start": v(-40.37, 124.97) * mm, "end": v(-40.13, 125) * mm});
            skLineSegment(sketch, "E4188", {"start": v(-40.13, 125) * mm, "end": v(-39.87, 125) * mm});
            skLineSegment(sketch, "E4189", {"start": v(-39.87, 125) * mm, "end": v(-39.63, 124.97) * mm});
            skLineSegment(sketch, "E4190", {"start": v(-39.63, 124.97) * mm, "end": v(-39.38, 124.9) * mm});
            skLineSegment(sketch, "E4191", {"start": v(-39.38, 124.9) * mm, "end": v(-39.15, 124.81) * mm});
            skLineSegment(sketch, "E4192", {"start": v(-39.15, 124.81) * mm, "end": v(-38.93, 124.69) * mm});
            skLineSegment(sketch, "E4193", {"start": v(-38.93, 124.69) * mm, "end": v(-38.73, 124.54) * mm});
            skLineSegment(sketch, "E4194", {"start": v(-38.73, 124.54) * mm, "end": v(-38.54, 124.37) * mm});
            skLineSegment(sketch, "E4195", {"start": v(-38.54, 124.37) * mm, "end": v(-38.38, 124.18) * mm});
            skLineSegment(sketch, "E4196", {"start": v(-38.38, 124.18) * mm, "end": v(-38.25, 123.96) * mm});
            skLineSegment(sketch, "E4197", {"start": v(-38.25, 123.96) * mm, "end": v(-38.14, 123.74) * mm});
            skLineSegment(sketch, "E4198", {"start": v(-38.14, 123.74) * mm, "end": v(-38.06, 123.5) * mm});
            skLineSegment(sketch, "E4199", {"start": v(-38.06, 123.5) * mm, "end": v(-38.02, 123.25) * mm});
            skLineSegment(sketch, "E4200", {"start": v(-38.02, 123.25) * mm, "end": v(-38, 123) * mm});
            skLineSegment(sketch, "E4201", {"start": v(-38, 123) * mm, "end": v(-38.02, 122.75) * mm});
            skLineSegment(sketch, "E4202", {"start": v(-38.02, 122.75) * mm, "end": v(-38.06, 122.5) * mm});
            skLineSegment(sketch, "E4203", {"start": v(-38.06, 122.5) * mm, "end": v(-38.14, 122.26) * mm});
            skLineSegment(sketch, "E4204", {"start": v(-38.14, 122.26) * mm, "end": v(-38.25, 122.04) * mm});
            skLineSegment(sketch, "E4205", {"start": v(-38.25, 122.04) * mm, "end": v(-38.38, 121.82) * mm});
            skLineSegment(sketch, "E4206", {"start": v(-38.38, 121.82) * mm, "end": v(-38.54, 121.63) * mm});
            skLineSegment(sketch, "E4207", {"start": v(-38.54, 121.63) * mm, "end": v(-38.73, 121.46) * mm});
            skLineSegment(sketch, "E4208", {"start": v(-38.73, 121.46) * mm, "end": v(-38.93, 121.31) * mm});
            skLineSegment(sketch, "E4209", {"start": v(-38.93, 121.31) * mm, "end": v(-39.15, 121.2) * mm});
            skLineSegment(sketch, "E4210", {"start": v(-39.15, 121.2) * mm, "end": v(-39.38, 121.1) * mm});
            skLineSegment(sketch, "E4211", {"start": v(-39.38, 121.1) * mm, "end": v(-39.63, 121.03) * mm});
            skLineSegment(sketch, "E4212", {"start": v(-39.63, 121.03) * mm, "end": v(-39.87, 121) * mm});
            skLineSegment(sketch, "E4213", {"start": v(-39.87, 121) * mm, "end": v(-40.13, 121) * mm});
            skLineSegment(sketch, "E4214", {"start": v(-370.13, 121) * mm, "end": v(-370.38, 121.03) * mm});
            skLineSegment(sketch, "E4215", {"start": v(-370.38, 121.03) * mm, "end": v(-370.62, 121.1) * mm});
            skLineSegment(sketch, "E4216", {"start": v(-370.62, 121.1) * mm, "end": v(-370.85, 121.2) * mm});
            skLineSegment(sketch, "E4217", {"start": v(-370.85, 121.2) * mm, "end": v(-371.07, 121.31) * mm});
            skLineSegment(sketch, "E4218", {"start": v(-371.07, 121.31) * mm, "end": v(-371.27, 121.46) * mm});
            skLineSegment(sketch, "E4219", {"start": v(-371.27, 121.46) * mm, "end": v(-371.46, 121.63) * mm});
            skLineSegment(sketch, "E4220", {"start": v(-371.46, 121.63) * mm, "end": v(-371.62, 121.82) * mm});
            skLineSegment(sketch, "E4221", {"start": v(-371.62, 121.82) * mm, "end": v(-371.75, 122.04) * mm});
            skLineSegment(sketch, "E4222", {"start": v(-371.75, 122.04) * mm, "end": v(-371.86, 122.26) * mm});
            skLineSegment(sketch, "E4223", {"start": v(-371.86, 122.26) * mm, "end": v(-371.94, 122.5) * mm});
            skLineSegment(sketch, "E4224", {"start": v(-371.94, 122.5) * mm, "end": v(-371.98, 122.75) * mm});
            skLineSegment(sketch, "E4225", {"start": v(-371.98, 122.75) * mm, "end": v(-372, 123) * mm});
            skLineSegment(sketch, "E4226", {"start": v(-372, 123) * mm, "end": v(-371.98, 123.25) * mm});
            skLineSegment(sketch, "E4227", {"start": v(-371.98, 123.25) * mm, "end": v(-371.94, 123.5) * mm});
            skLineSegment(sketch, "E4228", {"start": v(-371.94, 123.5) * mm, "end": v(-371.86, 123.74) * mm});
            skLineSegment(sketch, "E4229", {"start": v(-371.86, 123.74) * mm, "end": v(-371.75, 123.96) * mm});
            skLineSegment(sketch, "E4230", {"start": v(-371.75, 123.96) * mm, "end": v(-371.62, 124.18) * mm});
            skLineSegment(sketch, "E4231", {"start": v(-371.62, 124.18) * mm, "end": v(-371.46, 124.37) * mm});
            skLineSegment(sketch, "E4232", {"start": v(-371.46, 124.37) * mm, "end": v(-371.27, 124.54) * mm});
            skLineSegment(sketch, "E4233", {"start": v(-371.27, 124.54) * mm, "end": v(-371.07, 124.69) * mm});
            skLineSegment(sketch, "E4234", {"start": v(-371.07, 124.69) * mm, "end": v(-370.85, 124.81) * mm});
            skLineSegment(sketch, "E4235", {"start": v(-370.85, 124.81) * mm, "end": v(-370.62, 124.9) * mm});
            skLineSegment(sketch, "E4236", {"start": v(-370.62, 124.9) * mm, "end": v(-370.38, 124.97) * mm});
            skLineSegment(sketch, "E4237", {"start": v(-370.38, 124.97) * mm, "end": v(-370.13, 125) * mm});
            skLineSegment(sketch, "E4238", {"start": v(-370.13, 125) * mm, "end": v(-369.87, 125) * mm});
            skLineSegment(sketch, "E4239", {"start": v(-369.87, 125) * mm, "end": v(-369.62, 124.97) * mm});
            skLineSegment(sketch, "E4240", {"start": v(-369.62, 124.97) * mm, "end": v(-369.38, 124.9) * mm});
            skLineSegment(sketch, "E4241", {"start": v(-369.38, 124.9) * mm, "end": v(-369.15, 124.81) * mm});
            skLineSegment(sketch, "E4242", {"start": v(-369.15, 124.81) * mm, "end": v(-368.93, 124.69) * mm});
            skLineSegment(sketch, "E4243", {"start": v(-368.93, 124.69) * mm, "end": v(-368.73, 124.54) * mm});
            skLineSegment(sketch, "E4244", {"start": v(-368.73, 124.54) * mm, "end": v(-368.54, 124.37) * mm});
            skLineSegment(sketch, "E4245", {"start": v(-368.54, 124.37) * mm, "end": v(-368.38, 124.18) * mm});
            skLineSegment(sketch, "E4246", {"start": v(-368.38, 124.18) * mm, "end": v(-368.25, 123.96) * mm});
            skLineSegment(sketch, "E4247", {"start": v(-368.25, 123.96) * mm, "end": v(-368.14, 123.74) * mm});
            skLineSegment(sketch, "E4248", {"start": v(-368.14, 123.74) * mm, "end": v(-368.06, 123.5) * mm});
            skLineSegment(sketch, "E4249", {"start": v(-368.06, 123.5) * mm, "end": v(-368.02, 123.25) * mm});
            skLineSegment(sketch, "E4250", {"start": v(-368.02, 123.25) * mm, "end": v(-368, 123) * mm});
            skLineSegment(sketch, "E4251", {"start": v(-368, 123) * mm, "end": v(-368.02, 122.75) * mm});
            skLineSegment(sketch, "E4252", {"start": v(-368.02, 122.75) * mm, "end": v(-368.06, 122.5) * mm});
            skLineSegment(sketch, "E4253", {"start": v(-368.06, 122.5) * mm, "end": v(-368.14, 122.26) * mm});
            skLineSegment(sketch, "E4254", {"start": v(-368.14, 122.26) * mm, "end": v(-368.25, 122.04) * mm});
            skLineSegment(sketch, "E4255", {"start": v(-368.25, 122.04) * mm, "end": v(-368.38, 121.82) * mm});
            skLineSegment(sketch, "E4256", {"start": v(-368.38, 121.82) * mm, "end": v(-368.54, 121.63) * mm});
            skLineSegment(sketch, "E4257", {"start": v(-368.54, 121.63) * mm, "end": v(-368.73, 121.46) * mm});
            skLineSegment(sketch, "E4258", {"start": v(-368.73, 121.46) * mm, "end": v(-368.93, 121.31) * mm});
            skLineSegment(sketch, "E4259", {"start": v(-368.93, 121.31) * mm, "end": v(-369.15, 121.2) * mm});
            skLineSegment(sketch, "E4260", {"start": v(-369.15, 121.2) * mm, "end": v(-369.38, 121.1) * mm});
            skLineSegment(sketch, "E4261", {"start": v(-369.38, 121.1) * mm, "end": v(-369.62, 121.03) * mm});
            skLineSegment(sketch, "E4262", {"start": v(-369.62, 121.03) * mm, "end": v(-369.87, 121) * mm});
            skLineSegment(sketch, "E4263", {"start": v(-369.87, 121) * mm, "end": v(-370.13, 121) * mm});
            skLineSegment(sketch, "E4264", {"start": v(-48, 43) * mm, "end": v(-48, 63) * mm});
            skLineSegment(sketch, "E4265", {"start": v(-48, 63) * mm, "end": v(-32, 63) * mm});
            skLineSegment(sketch, "E4266", {"start": v(-32, 63) * mm, "end": v(-32, 43) * mm});
            skLineSegment(sketch, "E4267", {"start": v(-32, 43) * mm, "end": v(-48, 43) * mm});
            skLineSegment(sketch, "E4268", {"start": v(-378, 43) * mm, "end": v(-378, 63) * mm});
            skLineSegment(sketch, "E4269", {"start": v(-378, 63) * mm, "end": v(-362, 63) * mm});
            skLineSegment(sketch, "E4270", {"start": v(-362, 63) * mm, "end": v(-362, 43) * mm});
            skLineSegment(sketch, "E4271", {"start": v(-362, 43) * mm, "end": v(-378, 43) * mm});
            skLineSegment(sketch, "E4272", {"start": v(-40.13, -19) * mm, "end": v(-40.37, -18.96) * mm});
            skLineSegment(sketch, "E4273", {"start": v(-40.37, -18.96) * mm, "end": v(-40.62, -18.9) * mm});
            skLineSegment(sketch, "E4274", {"start": v(-40.62, -18.9) * mm, "end": v(-40.85, -18.8) * mm});
            skLineSegment(sketch, "E4275", {"start": v(-40.85, -18.8) * mm, "end": v(-41.07, -18.69) * mm});
            skLineSegment(sketch, "E4276", {"start": v(-41.07, -18.69) * mm, "end": v(-41.27, -18.54) * mm});
            skLineSegment(sketch, "E4277", {"start": v(-41.27, -18.54) * mm, "end": v(-41.46, -18.37) * mm});
            skLineSegment(sketch, "E4278", {"start": v(-41.46, -18.37) * mm, "end": v(-41.62, -18.18) * mm});
            skLineSegment(sketch, "E4279", {"start": v(-41.62, -18.18) * mm, "end": v(-41.75, -17.96) * mm});
            skLineSegment(sketch, "E4280", {"start": v(-41.75, -17.96) * mm, "end": v(-41.86, -17.74) * mm});
            skLineSegment(sketch, "E4281", {"start": v(-41.86, -17.74) * mm, "end": v(-41.94, -17.5) * mm});
            skLineSegment(sketch, "E4282", {"start": v(-41.94, -17.5) * mm, "end": v(-41.98, -17.25) * mm});
            skLineSegment(sketch, "E4283", {"start": v(-41.98, -17.25) * mm, "end": v(-42, -17) * mm});
            skLineSegment(sketch, "E4284", {"start": v(-42, -17) * mm, "end": v(-41.98, -16.75) * mm});
            skLineSegment(sketch, "E4285", {"start": v(-41.98, -16.75) * mm, "end": v(-41.94, -16.5) * mm});
            skLineSegment(sketch, "E4286", {"start": v(-41.94, -16.5) * mm, "end": v(-41.86, -16.26) * mm});
            skLineSegment(sketch, "E4287", {"start": v(-41.86, -16.26) * mm, "end": v(-41.75, -16.04) * mm});
            skLineSegment(sketch, "E4288", {"start": v(-41.75, -16.04) * mm, "end": v(-41.62, -15.82) * mm});
            skLineSegment(sketch, "E4289", {"start": v(-41.62, -15.82) * mm, "end": v(-41.46, -15.63) * mm});
            skLineSegment(sketch, "E4290", {"start": v(-41.46, -15.63) * mm, "end": v(-41.27, -15.46) * mm});
            skLineSegment(sketch, "E4291", {"start": v(-41.27, -15.46) * mm, "end": v(-41.07, -15.31) * mm});
            skLineSegment(sketch, "E4292", {"start": v(-41.07, -15.31) * mm, "end": v(-40.85, -15.2) * mm});
            skLineSegment(sketch, "E4293", {"start": v(-40.85, -15.2) * mm, "end": v(-40.62, -15.1) * mm});
            skLineSegment(sketch, "E4294", {"start": v(-40.62, -15.1) * mm, "end": v(-40.37, -15.04) * mm});
            skLineSegment(sketch, "E4295", {"start": v(-40.37, -15.04) * mm, "end": v(-40.13, -15) * mm});
            skLineSegment(sketch, "E4296", {"start": v(-40.13, -15) * mm, "end": v(-39.87, -15) * mm});
            skLineSegment(sketch, "E4297", {"start": v(-39.87, -15) * mm, "end": v(-39.63, -15.04) * mm});
            skLineSegment(sketch, "E4298", {"start": v(-39.63, -15.04) * mm, "end": v(-39.38, -15.1) * mm});
            skLineSegment(sketch, "E4299", {"start": v(-39.38, -15.1) * mm, "end": v(-39.15, -15.2) * mm});
            skLineSegment(sketch, "E4300", {"start": v(-39.15, -15.2) * mm, "end": v(-38.93, -15.31) * mm});
            skLineSegment(sketch, "E4301", {"start": v(-38.93, -15.31) * mm, "end": v(-38.73, -15.46) * mm});
            skLineSegment(sketch, "E4302", {"start": v(-38.73, -15.46) * mm, "end": v(-38.54, -15.63) * mm});
            skLineSegment(sketch, "E4303", {"start": v(-38.54, -15.63) * mm, "end": v(-38.38, -15.82) * mm});
            skLineSegment(sketch, "E4304", {"start": v(-38.38, -15.82) * mm, "end": v(-38.25, -16.04) * mm});
            skLineSegment(sketch, "E4305", {"start": v(-38.25, -16.04) * mm, "end": v(-38.14, -16.26) * mm});
            skLineSegment(sketch, "E4306", {"start": v(-38.14, -16.26) * mm, "end": v(-38.06, -16.5) * mm});
            skLineSegment(sketch, "E4307", {"start": v(-38.06, -16.5) * mm, "end": v(-38.02, -16.75) * mm});
            skLineSegment(sketch, "E4308", {"start": v(-38.02, -16.75) * mm, "end": v(-38, -17) * mm});
            skLineSegment(sketch, "E4309", {"start": v(-38, -17) * mm, "end": v(-38.02, -17.25) * mm});
            skLineSegment(sketch, "E4310", {"start": v(-38.02, -17.25) * mm, "end": v(-38.06, -17.5) * mm});
            skLineSegment(sketch, "E4311", {"start": v(-38.06, -17.5) * mm, "end": v(-38.14, -17.74) * mm});
            skLineSegment(sketch, "E4312", {"start": v(-38.14, -17.74) * mm, "end": v(-38.25, -17.96) * mm});
            skLineSegment(sketch, "E4313", {"start": v(-38.25, -17.96) * mm, "end": v(-38.38, -18.18) * mm});
            skLineSegment(sketch, "E4314", {"start": v(-38.38, -18.18) * mm, "end": v(-38.54, -18.37) * mm});
            skLineSegment(sketch, "E4315", {"start": v(-38.54, -18.37) * mm, "end": v(-38.73, -18.54) * mm});
            skLineSegment(sketch, "E4316", {"start": v(-38.73, -18.54) * mm, "end": v(-38.93, -18.69) * mm});
            skLineSegment(sketch, "E4317", {"start": v(-38.93, -18.69) * mm, "end": v(-39.15, -18.8) * mm});
            skLineSegment(sketch, "E4318", {"start": v(-39.15, -18.8) * mm, "end": v(-39.38, -18.9) * mm});
            skLineSegment(sketch, "E4319", {"start": v(-39.38, -18.9) * mm, "end": v(-39.63, -18.96) * mm});
            skLineSegment(sketch, "E4320", {"start": v(-39.63, -18.96) * mm, "end": v(-39.87, -19) * mm});
            skLineSegment(sketch, "E4321", {"start": v(-39.87, -19) * mm, "end": v(-40.13, -19) * mm});
            skLineSegment(sketch, "E4322", {"start": v(-370.13, -19) * mm, "end": v(-370.38, -18.96) * mm});
            skLineSegment(sketch, "E4323", {"start": v(-370.38, -18.96) * mm, "end": v(-370.62, -18.9) * mm});
            skLineSegment(sketch, "E4324", {"start": v(-370.62, -18.9) * mm, "end": v(-370.85, -18.8) * mm});
            skLineSegment(sketch, "E4325", {"start": v(-370.85, -18.8) * mm, "end": v(-371.07, -18.69) * mm});
            skLineSegment(sketch, "E4326", {"start": v(-371.07, -18.69) * mm, "end": v(-371.27, -18.54) * mm});
            skLineSegment(sketch, "E4327", {"start": v(-371.27, -18.54) * mm, "end": v(-371.46, -18.37) * mm});
            skLineSegment(sketch, "E4328", {"start": v(-371.46, -18.37) * mm, "end": v(-371.62, -18.18) * mm});
            skLineSegment(sketch, "E4329", {"start": v(-371.62, -18.18) * mm, "end": v(-371.75, -17.96) * mm});
            skLineSegment(sketch, "E4330", {"start": v(-371.75, -17.96) * mm, "end": v(-371.86, -17.74) * mm});
            skLineSegment(sketch, "E4331", {"start": v(-371.86, -17.74) * mm, "end": v(-371.94, -17.5) * mm});
            skLineSegment(sketch, "E4332", {"start": v(-371.94, -17.5) * mm, "end": v(-371.98, -17.25) * mm});
            skLineSegment(sketch, "E4333", {"start": v(-371.98, -17.25) * mm, "end": v(-372, -17) * mm});
            skLineSegment(sketch, "E4334", {"start": v(-372, -17) * mm, "end": v(-371.98, -16.75) * mm});
            skLineSegment(sketch, "E4335", {"start": v(-371.98, -16.75) * mm, "end": v(-371.94, -16.5) * mm});
            skLineSegment(sketch, "E4336", {"start": v(-371.94, -16.5) * mm, "end": v(-371.86, -16.26) * mm});
            skLineSegment(sketch, "E4337", {"start": v(-371.86, -16.26) * mm, "end": v(-371.75, -16.04) * mm});
            skLineSegment(sketch, "E4338", {"start": v(-371.75, -16.04) * mm, "end": v(-371.62, -15.82) * mm});
            skLineSegment(sketch, "E4339", {"start": v(-371.62, -15.82) * mm, "end": v(-371.46, -15.63) * mm});
            skLineSegment(sketch, "E4340", {"start": v(-371.46, -15.63) * mm, "end": v(-371.27, -15.46) * mm});
            skLineSegment(sketch, "E4341", {"start": v(-371.27, -15.46) * mm, "end": v(-371.07, -15.31) * mm});
            skLineSegment(sketch, "E4342", {"start": v(-371.07, -15.31) * mm, "end": v(-370.85, -15.2) * mm});
            skLineSegment(sketch, "E4343", {"start": v(-370.85, -15.2) * mm, "end": v(-370.62, -15.1) * mm});
            skLineSegment(sketch, "E4344", {"start": v(-370.62, -15.1) * mm, "end": v(-370.38, -15.04) * mm});
            skLineSegment(sketch, "E4345", {"start": v(-370.38, -15.04) * mm, "end": v(-370.13, -15) * mm});
            skLineSegment(sketch, "E4346", {"start": v(-370.13, -15) * mm, "end": v(-369.87, -15) * mm});
            skLineSegment(sketch, "E4347", {"start": v(-369.87, -15) * mm, "end": v(-369.62, -15.04) * mm});
            skLineSegment(sketch, "E4348", {"start": v(-369.62, -15.04) * mm, "end": v(-369.38, -15.1) * mm});
            skLineSegment(sketch, "E4349", {"start": v(-369.38, -15.1) * mm, "end": v(-369.15, -15.2) * mm});
            skLineSegment(sketch, "E4350", {"start": v(-369.15, -15.2) * mm, "end": v(-368.93, -15.31) * mm});
            skLineSegment(sketch, "E4351", {"start": v(-368.93, -15.31) * mm, "end": v(-368.73, -15.46) * mm});
            skLineSegment(sketch, "E4352", {"start": v(-368.73, -15.46) * mm, "end": v(-368.54, -15.63) * mm});
            skLineSegment(sketch, "E4353", {"start": v(-368.54, -15.63) * mm, "end": v(-368.38, -15.82) * mm});
            skLineSegment(sketch, "E4354", {"start": v(-368.38, -15.82) * mm, "end": v(-368.25, -16.04) * mm});
            skLineSegment(sketch, "E4355", {"start": v(-368.25, -16.04) * mm, "end": v(-368.14, -16.26) * mm});
            skLineSegment(sketch, "E4356", {"start": v(-368.14, -16.26) * mm, "end": v(-368.06, -16.5) * mm});
            skLineSegment(sketch, "E4357", {"start": v(-368.06, -16.5) * mm, "end": v(-368.02, -16.75) * mm});
            skLineSegment(sketch, "E4358", {"start": v(-368.02, -16.75) * mm, "end": v(-368, -17) * mm});
            skLineSegment(sketch, "E4359", {"start": v(-368, -17) * mm, "end": v(-368.02, -17.25) * mm});
            skLineSegment(sketch, "E4360", {"start": v(-368.02, -17.25) * mm, "end": v(-368.06, -17.5) * mm});
            skLineSegment(sketch, "E4361", {"start": v(-368.06, -17.5) * mm, "end": v(-368.14, -17.74) * mm});
            skLineSegment(sketch, "E4362", {"start": v(-368.14, -17.74) * mm, "end": v(-368.25, -17.96) * mm});
            skLineSegment(sketch, "E4363", {"start": v(-368.25, -17.96) * mm, "end": v(-368.38, -18.18) * mm});
            skLineSegment(sketch, "E4364", {"start": v(-368.38, -18.18) * mm, "end": v(-368.54, -18.37) * mm});
            skLineSegment(sketch, "E4365", {"start": v(-368.54, -18.37) * mm, "end": v(-368.73, -18.54) * mm});
            skLineSegment(sketch, "E4366", {"start": v(-368.73, -18.54) * mm, "end": v(-368.93, -18.69) * mm});
            skLineSegment(sketch, "E4367", {"start": v(-368.93, -18.69) * mm, "end": v(-369.15, -18.8) * mm});
            skLineSegment(sketch, "E4368", {"start": v(-369.15, -18.8) * mm, "end": v(-369.38, -18.9) * mm});
            skLineSegment(sketch, "E4369", {"start": v(-369.38, -18.9) * mm, "end": v(-369.62, -18.96) * mm});
            skLineSegment(sketch, "E4370", {"start": v(-369.62, -18.96) * mm, "end": v(-369.87, -19) * mm});
            skLineSegment(sketch, "E4371", {"start": v(-369.87, -19) * mm, "end": v(-370.13, -19) * mm});
            skLineSegment(sketch, "E4372", {"start": v(-378, -97) * mm, "end": v(-378, -77) * mm});
            skLineSegment(sketch, "E4373", {"start": v(-378, -77) * mm, "end": v(-362, -77) * mm});
            skLineSegment(sketch, "E4374", {"start": v(-362, -77) * mm, "end": v(-362, -97) * mm});
            skLineSegment(sketch, "E4375", {"start": v(-362, -97) * mm, "end": v(-378, -97) * mm});
            skLineSegment(sketch, "E4376", {"start": v(-48, -97) * mm, "end": v(-48, -77) * mm});
            skLineSegment(sketch, "E4377", {"start": v(-48, -77) * mm, "end": v(-32, -77) * mm});
            skLineSegment(sketch, "E4378", {"start": v(-32, -77) * mm, "end": v(-32, -97) * mm});
            skLineSegment(sketch, "E4379", {"start": v(-32, -97) * mm, "end": v(-48, -97) * mm});
            skLineSegment(sketch, "E4380", {"start": v(-85, -142) * mm, "end": v(-101, -142) * mm});
            skLineSegment(sketch, "E4381", {"start": v(-101, -142) * mm, "end": v(-101, -22) * mm});
            skLineSegment(sketch, "E4382", {"start": v(-101, -22) * mm, "end": v(-85, -22) * mm});
            skLineSegment(sketch, "E4383", {"start": v(-85, -22) * mm, "end": v(-85, -2) * mm});
            skLineSegment(sketch, "E4384", {"start": v(-85, -2) * mm, "end": v(-101, -2) * mm});
            skLineSegment(sketch, "E4385", {"start": v(-101, -2) * mm, "end": v(-101, 118) * mm});
            skLineSegment(sketch, "E4386", {"start": v(-101, 118) * mm, "end": v(-85, 118) * mm});
            skLineSegment(sketch, "E4387", {"start": v(-85, 118) * mm, "end": v(-85, 138) * mm});
            skLineSegment(sketch, "E4388", {"start": v(-85, 138) * mm, "end": v(-101, 138) * mm});
            skLineSegment(sketch, "E4389", {"start": v(-101, 138) * mm, "end": v(-101, 158) * mm});
            skLineSegment(sketch, "E4390", {"start": v(-101, 158) * mm, "end": v(-156, 158) * mm});
            skLineSegment(sketch, "E4391", {"start": v(-156, 158) * mm, "end": v(-156, 174) * mm});
            skLineSegment(sketch, "E4392", {"start": v(-156, 174) * mm, "end": v(-176, 174) * mm});
            skLineSegment(sketch, "E4393", {"start": v(-176, 174) * mm, "end": v(-176, 158) * mm});
            skLineSegment(sketch, "E4394", {"start": v(-176, 158) * mm, "end": v(-239, 158) * mm});
            skLineSegment(sketch, "E4395", {"start": v(-239, 158) * mm, "end": v(-187.01, -2) * mm});
            skLineSegment(sketch, "E4396", {"start": v(-187.01, -2) * mm, "end": v(-187, -2) * mm});
            skLineSegment(sketch, "E4397", {"start": v(-187, -2) * mm, "end": v(-137.06, -155.68) * mm});
            skLineSegment(sketch, "E4398", {"start": v(-137.06, -155.68) * mm, "end": v(-136.52, -156.82) * mm});
            skLineSegment(sketch, "E4399", {"start": v(-136.52, -156.82) * mm, "end": v(-135.85, -157.88) * mm});
            skLineSegment(sketch, "E4400", {"start": v(-135.85, -157.88) * mm, "end": v(-135.05, -158.85) * mm});
            skLineSegment(sketch, "E4401", {"start": v(-135.05, -158.85) * mm, "end": v(-134.13, -159.7) * mm});
            skLineSegment(sketch, "E4402", {"start": v(-134.13, -159.7) * mm, "end": v(-133.12, -160.44) * mm});
            skLineSegment(sketch, "E4403", {"start": v(-133.12, -160.44) * mm, "end": v(-132.02, -161.05) * mm});
            skLineSegment(sketch, "E4404", {"start": v(-132.02, -161.05) * mm, "end": v(-130.85, -161.51) * mm});
            skLineSegment(sketch, "E4405", {"start": v(-130.85, -161.51) * mm, "end": v(-129.63, -161.82) * mm});
            skLineSegment(sketch, "E4406", {"start": v(-129.63, -161.82) * mm, "end": v(-128.39, -161.98) * mm});
            skLineSegment(sketch, "E4407", {"start": v(-128.39, -161.98) * mm, "end": v(-111, -161.98) * mm});
            skLineSegment(sketch, "E4408", {"start": v(-111, -161.98) * mm, "end": v(-111, -162) * mm});
            skLineSegment(sketch, "E4409", {"start": v(-111, -162) * mm, "end": v(-85, -162) * mm});
            skLineSegment(sketch, "E4410", {"start": v(-85, -162) * mm, "end": v(-85, -142) * mm});
            skLineSegment(sketch, "E4411", {"start": v(-234, -146) * mm, "end": v(-171, -146) * mm});
            skLineSegment(sketch, "E4412", {"start": v(-171, -146) * mm, "end": v(-222.99, 14) * mm});
            skLineSegment(sketch, "E4413", {"start": v(-222.99, 14) * mm, "end": v(-223, 14) * mm});
            skLineSegment(sketch, "E4414", {"start": v(-223, 14) * mm, "end": v(-272.94, 167.68) * mm});
            skLineSegment(sketch, "E4415", {"start": v(-272.94, 167.68) * mm, "end": v(-273.48, 168.82) * mm});
            skLineSegment(sketch, "E4416", {"start": v(-273.48, 168.82) * mm, "end": v(-274.15, 169.88) * mm});
            skLineSegment(sketch, "E4417", {"start": v(-274.15, 169.88) * mm, "end": v(-274.95, 170.84) * mm});
            skLineSegment(sketch, "E4418", {"start": v(-274.95, 170.84) * mm, "end": v(-275.87, 171.7) * mm});
            skLineSegment(sketch, "E4419", {"start": v(-275.87, 171.7) * mm, "end": v(-276.88, 172.44) * mm});
            skLineSegment(sketch, "E4420", {"start": v(-276.88, 172.44) * mm, "end": v(-277.98, 173.05) * mm});
            skLineSegment(sketch, "E4421", {"start": v(-277.98, 173.05) * mm, "end": v(-279.15, 173.51) * mm});
            skLineSegment(sketch, "E4422", {"start": v(-279.15, 173.51) * mm, "end": v(-280.37, 173.82) * mm});
            skLineSegment(sketch, "E4423", {"start": v(-280.37, 173.82) * mm, "end": v(-281.61, 173.98) * mm});
            skLineSegment(sketch, "E4424", {"start": v(-281.61, 173.98) * mm, "end": v(-299, 173.98) * mm});
            skLineSegment(sketch, "E4425", {"start": v(-299, 173.98) * mm, "end": v(-299, 174) * mm});
            skLineSegment(sketch, "E4426", {"start": v(-299, 174) * mm, "end": v(-325, 174) * mm});
            skLineSegment(sketch, "E4427", {"start": v(-325, 174) * mm, "end": v(-325, 154) * mm});
            skLineSegment(sketch, "E4428", {"start": v(-325, 154) * mm, "end": v(-309, 154) * mm});
            skLineSegment(sketch, "E4429", {"start": v(-309, 154) * mm, "end": v(-309, 34) * mm});
            skLineSegment(sketch, "E4430", {"start": v(-309, 34) * mm, "end": v(-325, 34) * mm});
            skLineSegment(sketch, "E4431", {"start": v(-325, 34) * mm, "end": v(-325, 14) * mm});
            skLineSegment(sketch, "E4432", {"start": v(-325, 14) * mm, "end": v(-309, 14) * mm});
            skLineSegment(sketch, "E4433", {"start": v(-309, 14) * mm, "end": v(-309, -106) * mm});
            skLineSegment(sketch, "E4434", {"start": v(-309, -106) * mm, "end": v(-325, -106) * mm});
            skLineSegment(sketch, "E4435", {"start": v(-325, -106) * mm, "end": v(-325, -126) * mm});
            skLineSegment(sketch, "E4436", {"start": v(-325, -126) * mm, "end": v(-309, -126) * mm});
            skLineSegment(sketch, "E4437", {"start": v(-309, -126) * mm, "end": v(-309, -146) * mm});
            skLineSegment(sketch, "E4438", {"start": v(-309, -146) * mm, "end": v(-254, -146) * mm});
            skLineSegment(sketch, "E4439", {"start": v(-254, -146) * mm, "end": v(-254, -162) * mm});
            skLineSegment(sketch, "E4440", {"start": v(-254, -162) * mm, "end": v(-234, -162) * mm});
            skLineSegment(sketch, "E4441", {"start": v(-234, -162) * mm, "end": v(-234, -146) * mm});
            skLineSegment(sketch, "E4442", {"start": v(40, -262.98) * mm, "end": v(40.63, -262.98) * mm});
            skLineSegment(sketch, "E4443", {"start": v(40.63, -262.98) * mm, "end": v(41.87, -262.82) * mm});
            skLineSegment(sketch, "E4444", {"start": v(41.87, -262.82) * mm, "end": v(43.1, -262.51) * mm});
            skLineSegment(sketch, "E4445", {"start": v(43.1, -262.51) * mm, "end": v(44.26, -262.05) * mm});
            skLineSegment(sketch, "E4446", {"start": v(44.26, -262.05) * mm, "end": v(45.36, -261.44) * mm});
            skLineSegment(sketch, "E4447", {"start": v(45.36, -261.44) * mm, "end": v(46.37, -260.7) * mm});
            skLineSegment(sketch, "E4448", {"start": v(46.37, -260.7) * mm, "end": v(47.29, -259.85) * mm});
            skLineSegment(sketch, "E4449", {"start": v(47.29, -259.85) * mm, "end": v(48.1, -258.88) * mm});
            skLineSegment(sketch, "E4450", {"start": v(48.1, -258.88) * mm, "end": v(48.76, -257.82) * mm});
            skLineSegment(sketch, "E4451", {"start": v(48.76, -257.82) * mm, "end": v(49.3, -256.68) * mm});
            skLineSegment(sketch, "E4452", {"start": v(49.3, -256.68) * mm, "end": v(49.69, -255.49) * mm});
            skLineSegment(sketch, "E4453", {"start": v(49.69, -255.49) * mm, "end": v(49.92, -254.25) * mm});
            skLineSegment(sketch, "E4454", {"start": v(49.92, -254.25) * mm, "end": v(50, -253) * mm});
            skLineSegment(sketch, "E4455", {"start": v(50, -253) * mm, "end": v(50.02, -253) * mm});
            skLineSegment(sketch, "E4456", {"start": v(50.02, -253) * mm, "end": v(50.02, -252.37) * mm});
            skLineSegment(sketch, "E4457", {"start": v(50.02, -252.37) * mm, "end": v(50.18, -251.13) * mm});
            skLineSegment(sketch, "E4458", {"start": v(50.18, -251.13) * mm, "end": v(50.49, -249.9) * mm});
            skLineSegment(sketch, "E4459", {"start": v(50.49, -249.9) * mm, "end": v(50.95, -248.74) * mm});
            skLineSegment(sketch, "E4460", {"start": v(50.95, -248.74) * mm, "end": v(51.56, -247.64) * mm});
            skLineSegment(sketch, "E4461", {"start": v(51.56, -247.64) * mm, "end": v(52.3, -246.63) * mm});
            skLineSegment(sketch, "E4462", {"start": v(52.3, -246.63) * mm, "end": v(53.15, -245.71) * mm});
            skLineSegment(sketch, "E4463", {"start": v(53.15, -245.71) * mm, "end": v(54.12, -244.9) * mm});
            skLineSegment(sketch, "E4464", {"start": v(54.12, -244.9) * mm, "end": v(55.18, -244.24) * mm});
            skLineSegment(sketch, "E4465", {"start": v(55.18, -244.24) * mm, "end": v(56.32, -243.7) * mm});
            skLineSegment(sketch, "E4466", {"start": v(56.32, -243.7) * mm, "end": v(57.51, -243.31) * mm});
            skLineSegment(sketch, "E4467", {"start": v(57.51, -243.31) * mm, "end": v(58.75, -243.08) * mm});
            skLineSegment(sketch, "E4468", {"start": v(58.75, -243.08) * mm, "end": v(60, -243) * mm});
            skLineSegment(sketch, "E4469", {"start": v(60, -243) * mm, "end": v(350, -243) * mm});
            skLineSegment(sketch, "E4470", {"start": v(350, -243) * mm, "end": v(350, -243.02) * mm});
            skLineSegment(sketch, "E4471", {"start": v(350, -243.02) * mm, "end": v(350.63, -243.02) * mm});
            skLineSegment(sketch, "E4472", {"start": v(350.63, -243.02) * mm, "end": v(351.87, -243.18) * mm});
            skLineSegment(sketch, "E4473", {"start": v(351.87, -243.18) * mm, "end": v(353.09, -243.49) * mm});
            skLineSegment(sketch, "E4474", {"start": v(353.09, -243.49) * mm, "end": v(354.26, -243.95) * mm});
            skLineSegment(sketch, "E4475", {"start": v(354.26, -243.95) * mm, "end": v(355.36, -244.56) * mm});
            skLineSegment(sketch, "E4476", {"start": v(355.36, -244.56) * mm, "end": v(356.37, -245.3) * mm});
            skLineSegment(sketch, "E4477", {"start": v(356.37, -245.3) * mm, "end": v(357.3, -246.15) * mm});
            skLineSegment(sketch, "E4478", {"start": v(357.3, -246.15) * mm, "end": v(358.09, -247.12) * mm});
            skLineSegment(sketch, "E4479", {"start": v(358.09, -247.12) * mm, "end": v(358.76, -248.18) * mm});
            skLineSegment(sketch, "E4480", {"start": v(358.76, -248.18) * mm, "end": v(359.3, -249.32) * mm});
            skLineSegment(sketch, "E4481", {"start": v(359.3, -249.32) * mm, "end": v(359.69, -250.51) * mm});
            skLineSegment(sketch, "E4482", {"start": v(359.69, -250.51) * mm, "end": v(359.92, -251.75) * mm});
            skLineSegment(sketch, "E4483", {"start": v(359.92, -251.75) * mm, "end": v(360.08, -254.25) * mm});
            skLineSegment(sketch, "E4484", {"start": v(360.08, -254.25) * mm, "end": v(360.31, -255.49) * mm});
            skLineSegment(sketch, "E4485", {"start": v(360.31, -255.49) * mm, "end": v(360.7, -256.68) * mm});
            skLineSegment(sketch, "E4486", {"start": v(360.7, -256.68) * mm, "end": v(361.24, -257.82) * mm});
            skLineSegment(sketch, "E4487", {"start": v(361.24, -257.82) * mm, "end": v(361.91, -258.88) * mm});
            skLineSegment(sketch, "E4488", {"start": v(361.91, -258.88) * mm, "end": v(362.7, -259.85) * mm});
            skLineSegment(sketch, "E4489", {"start": v(362.7, -259.85) * mm, "end": v(363.63, -260.7) * mm});
            skLineSegment(sketch, "E4490", {"start": v(363.63, -260.7) * mm, "end": v(364.64, -261.44) * mm});
            skLineSegment(sketch, "E4491", {"start": v(364.64, -261.44) * mm, "end": v(365.74, -262.05) * mm});
            skLineSegment(sketch, "E4492", {"start": v(365.74, -262.05) * mm, "end": v(366.91, -262.51) * mm});
            skLineSegment(sketch, "E4493", {"start": v(366.91, -262.51) * mm, "end": v(368.13, -262.82) * mm});
            skLineSegment(sketch, "E4494", {"start": v(368.13, -262.82) * mm, "end": v(369.37, -262.98) * mm});
            skLineSegment(sketch, "E4495", {"start": v(369.37, -262.98) * mm, "end": v(370, -262.98) * mm});
            skLineSegment(sketch, "E4496", {"start": v(370, -262.98) * mm, "end": v(370, -263) * mm});
            skLineSegment(sketch, "E4497", {"start": v(370, -263) * mm, "end": v(390, -263) * mm});
            skLineSegment(sketch, "E4498", {"start": v(390, -263) * mm, "end": v(391.25, -262.92) * mm});
            skLineSegment(sketch, "E4499", {"start": v(391.25, -262.92) * mm, "end": v(392.49, -262.69) * mm});
            skLineSegment(sketch, "E4500", {"start": v(392.49, -262.69) * mm, "end": v(393.68, -262.3) * mm});
            skLineSegment(sketch, "E4501", {"start": v(393.68, -262.3) * mm, "end": v(394.82, -261.76) * mm});
            skLineSegment(sketch, "E4502", {"start": v(394.82, -261.76) * mm, "end": v(395.88, -261.1) * mm});
            skLineSegment(sketch, "E4503", {"start": v(395.88, -261.1) * mm, "end": v(396.85, -260.29) * mm});
            skLineSegment(sketch, "E4504", {"start": v(396.85, -260.29) * mm, "end": v(397.7, -259.37) * mm});
            skLineSegment(sketch, "E4505", {"start": v(397.7, -259.37) * mm, "end": v(398.44, -258.36) * mm});
            skLineSegment(sketch, "E4506", {"start": v(398.44, -258.36) * mm, "end": v(399.05, -257.26) * mm});
            skLineSegment(sketch, "E4507", {"start": v(399.05, -257.26) * mm, "end": v(399.51, -256.1) * mm});
            skLineSegment(sketch, "E4508", {"start": v(399.51, -256.1) * mm, "end": v(399.82, -254.87) * mm});
            skLineSegment(sketch, "E4509", {"start": v(399.82, -254.87) * mm, "end": v(399.98, -253.63) * mm});
            skLineSegment(sketch, "E4510", {"start": v(399.98, -253.63) * mm, "end": v(399.98, -253) * mm});
            skLineSegment(sketch, "E4511", {"start": v(399.98, -253) * mm, "end": v(400, -253) * mm});
            skLineSegment(sketch, "E4512", {"start": v(400, -253) * mm, "end": v(400, -203) * mm});
            skLineSegment(sketch, "E4513", {"start": v(400, -203) * mm, "end": v(360, -203) * mm});
            skLineSegment(sketch, "E4514", {"start": v(360, -203) * mm, "end": v(360, -187) * mm});
            skLineSegment(sketch, "E4515", {"start": v(360, -187) * mm, "end": v(340, -187) * mm});
            skLineSegment(sketch, "E4516", {"start": v(340, -187) * mm, "end": v(340, -203) * mm});
            skLineSegment(sketch, "E4517", {"start": v(340, -203) * mm, "end": v(215, -203) * mm});
            skLineSegment(sketch, "E4518", {"start": v(215, -203) * mm, "end": v(215, -187) * mm});
            skLineSegment(sketch, "E4519", {"start": v(215, -187) * mm, "end": v(195, -187) * mm});
            skLineSegment(sketch, "E4520", {"start": v(195, -187) * mm, "end": v(195, -203) * mm});
            skLineSegment(sketch, "E4521", {"start": v(195, -203) * mm, "end": v(70, -203) * mm});
            skLineSegment(sketch, "E4522", {"start": v(70, -203) * mm, "end": v(70, -187) * mm});
            skLineSegment(sketch, "E4523", {"start": v(70, -187) * mm, "end": v(50, -187) * mm});
            skLineSegment(sketch, "E4524", {"start": v(50, -187) * mm, "end": v(50, -203) * mm});
            skLineSegment(sketch, "E4525", {"start": v(50, -203) * mm, "end": v(10, -203) * mm});
            skLineSegment(sketch, "E4526", {"start": v(10, -203) * mm, "end": v(10, -253) * mm});
            skLineSegment(sketch, "E4527", {"start": v(10, -253) * mm, "end": v(10.08, -254.25) * mm});
            skLineSegment(sketch, "E4528", {"start": v(10.08, -254.25) * mm, "end": v(10.31, -255.49) * mm});
            skLineSegment(sketch, "E4529", {"start": v(10.31, -255.49) * mm, "end": v(10.7, -256.68) * mm});
            skLineSegment(sketch, "E4530", {"start": v(10.7, -256.68) * mm, "end": v(11.24, -257.82) * mm});
            skLineSegment(sketch, "E4531", {"start": v(11.24, -257.82) * mm, "end": v(11.9, -258.88) * mm});
            skLineSegment(sketch, "E4532", {"start": v(11.9, -258.88) * mm, "end": v(12.71, -259.85) * mm});
            skLineSegment(sketch, "E4533", {"start": v(12.71, -259.85) * mm, "end": v(13.63, -260.7) * mm});
            skLineSegment(sketch, "E4534", {"start": v(13.63, -260.7) * mm, "end": v(14.64, -261.44) * mm});
            skLineSegment(sketch, "E4535", {"start": v(14.64, -261.44) * mm, "end": v(15.74, -262.05) * mm});
            skLineSegment(sketch, "E4536", {"start": v(15.74, -262.05) * mm, "end": v(16.9, -262.51) * mm});
            skLineSegment(sketch, "E4537", {"start": v(16.9, -262.51) * mm, "end": v(18.13, -262.82) * mm});
            skLineSegment(sketch, "E4538", {"start": v(18.13, -262.82) * mm, "end": v(19.37, -262.98) * mm});
            skLineSegment(sketch, "E4539", {"start": v(19.37, -262.98) * mm, "end": v(20, -262.98) * mm});
            skLineSegment(sketch, "E4540", {"start": v(20, -262.98) * mm, "end": v(20, -263) * mm});
            skLineSegment(sketch, "E4541", {"start": v(20, -263) * mm, "end": v(40, -263) * mm});
            skLineSegment(sketch, "E4542", {"start": v(40, -263) * mm, "end": v(40, -262.98) * mm});
            skLineSegment(sketch, "E4543", {"start": v(-370, -262.98) * mm, "end": v(-369.37, -262.98) * mm});
            skLineSegment(sketch, "E4544", {"start": v(-369.37, -262.98) * mm, "end": v(-368.13, -262.82) * mm});
            skLineSegment(sketch, "E4545", {"start": v(-368.13, -262.82) * mm, "end": v(-366.91, -262.51) * mm});
            skLineSegment(sketch, "E4546", {"start": v(-366.91, -262.51) * mm, "end": v(-365.74, -262.05) * mm});
            skLineSegment(sketch, "E4547", {"start": v(-365.74, -262.05) * mm, "end": v(-364.64, -261.44) * mm});
            skLineSegment(sketch, "E4548", {"start": v(-364.64, -261.44) * mm, "end": v(-363.63, -260.7) * mm});
            skLineSegment(sketch, "E4549", {"start": v(-363.63, -260.7) * mm, "end": v(-362.7, -259.85) * mm});
            skLineSegment(sketch, "E4550", {"start": v(-362.7, -259.85) * mm, "end": v(-361.91, -258.88) * mm});
            skLineSegment(sketch, "E4551", {"start": v(-361.91, -258.88) * mm, "end": v(-361.24, -257.82) * mm});
            skLineSegment(sketch, "E4552", {"start": v(-361.24, -257.82) * mm, "end": v(-360.7, -256.68) * mm});
            skLineSegment(sketch, "E4553", {"start": v(-360.7, -256.68) * mm, "end": v(-360.31, -255.49) * mm});
            skLineSegment(sketch, "E4554", {"start": v(-360.31, -255.49) * mm, "end": v(-360.08, -254.25) * mm});
            skLineSegment(sketch, "E4555", {"start": v(-360.08, -254.25) * mm, "end": v(-360, -253) * mm});
            skLineSegment(sketch, "E4556", {"start": v(-360, -253) * mm, "end": v(-359.98, -253) * mm});
            skLineSegment(sketch, "E4557", {"start": v(-359.98, -253) * mm, "end": v(-359.98, -252.37) * mm});
            skLineSegment(sketch, "E4558", {"start": v(-359.98, -252.37) * mm, "end": v(-359.82, -251.13) * mm});
            skLineSegment(sketch, "E4559", {"start": v(-359.82, -251.13) * mm, "end": v(-359.51, -249.9) * mm});
            skLineSegment(sketch, "E4560", {"start": v(-359.51, -249.9) * mm, "end": v(-359.05, -248.74) * mm});
            skLineSegment(sketch, "E4561", {"start": v(-359.05, -248.74) * mm, "end": v(-358.44, -247.64) * mm});
            skLineSegment(sketch, "E4562", {"start": v(-358.44, -247.64) * mm, "end": v(-357.7, -246.63) * mm});
            skLineSegment(sketch, "E4563", {"start": v(-357.7, -246.63) * mm, "end": v(-356.85, -245.71) * mm});
            skLineSegment(sketch, "E4564", {"start": v(-356.85, -245.71) * mm, "end": v(-355.88, -244.9) * mm});
            skLineSegment(sketch, "E4565", {"start": v(-355.88, -244.9) * mm, "end": v(-354.82, -244.24) * mm});
            skLineSegment(sketch, "E4566", {"start": v(-354.82, -244.24) * mm, "end": v(-353.68, -243.7) * mm});
            skLineSegment(sketch, "E4567", {"start": v(-353.68, -243.7) * mm, "end": v(-352.49, -243.31) * mm});
            skLineSegment(sketch, "E4568", {"start": v(-352.49, -243.31) * mm, "end": v(-351.25, -243.08) * mm});
            skLineSegment(sketch, "E4569", {"start": v(-351.25, -243.08) * mm, "end": v(-350, -243) * mm});
            skLineSegment(sketch, "E4570", {"start": v(-350, -243) * mm, "end": v(-60, -243) * mm});
            skLineSegment(sketch, "E4571", {"start": v(-60, -243) * mm, "end": v(-60, -243.02) * mm});
            skLineSegment(sketch, "E4572", {"start": v(-60, -243.02) * mm, "end": v(-59.37, -243.02) * mm});
            skLineSegment(sketch, "E4573", {"start": v(-59.37, -243.02) * mm, "end": v(-58.13, -243.18) * mm});
            skLineSegment(sketch, "E4574", {"start": v(-58.13, -243.18) * mm, "end": v(-56.9, -243.49) * mm});
            skLineSegment(sketch, "E4575", {"start": v(-56.9, -243.49) * mm, "end": v(-55.74, -243.95) * mm});
            skLineSegment(sketch, "E4576", {"start": v(-55.74, -243.95) * mm, "end": v(-54.64, -244.56) * mm});
            skLineSegment(sketch, "E4577", {"start": v(-54.64, -244.56) * mm, "end": v(-53.63, -245.3) * mm});
            skLineSegment(sketch, "E4578", {"start": v(-53.63, -245.3) * mm, "end": v(-52.71, -246.15) * mm});
            skLineSegment(sketch, "E4579", {"start": v(-52.71, -246.15) * mm, "end": v(-51.9, -247.12) * mm});
            skLineSegment(sketch, "E4580", {"start": v(-51.9, -247.12) * mm, "end": v(-51.24, -248.18) * mm});
            skLineSegment(sketch, "E4581", {"start": v(-51.24, -248.18) * mm, "end": v(-50.7, -249.32) * mm});
            skLineSegment(sketch, "E4582", {"start": v(-50.7, -249.32) * mm, "end": v(-50.31, -250.51) * mm});
            skLineSegment(sketch, "E4583", {"start": v(-50.31, -250.51) * mm, "end": v(-50.08, -251.75) * mm});
            skLineSegment(sketch, "E4584", {"start": v(-50.08, -251.75) * mm, "end": v(-49.92, -254.25) * mm});
            skLineSegment(sketch, "E4585", {"start": v(-49.92, -254.25) * mm, "end": v(-49.69, -255.49) * mm});
            skLineSegment(sketch, "E4586", {"start": v(-49.69, -255.49) * mm, "end": v(-49.3, -256.68) * mm});
            skLineSegment(sketch, "E4587", {"start": v(-49.3, -256.68) * mm, "end": v(-48.76, -257.82) * mm});
            skLineSegment(sketch, "E4588", {"start": v(-48.76, -257.82) * mm, "end": v(-48.1, -258.88) * mm});
            skLineSegment(sketch, "E4589", {"start": v(-48.1, -258.88) * mm, "end": v(-47.29, -259.85) * mm});
            skLineSegment(sketch, "E4590", {"start": v(-47.29, -259.85) * mm, "end": v(-46.37, -260.7) * mm});
            skLineSegment(sketch, "E4591", {"start": v(-46.37, -260.7) * mm, "end": v(-45.36, -261.44) * mm});
            skLineSegment(sketch, "E4592", {"start": v(-45.36, -261.44) * mm, "end": v(-44.26, -262.05) * mm});
            skLineSegment(sketch, "E4593", {"start": v(-44.26, -262.05) * mm, "end": v(-43.1, -262.51) * mm});
            skLineSegment(sketch, "E4594", {"start": v(-43.1, -262.51) * mm, "end": v(-41.87, -262.82) * mm});
            skLineSegment(sketch, "E4595", {"start": v(-41.87, -262.82) * mm, "end": v(-40.63, -262.98) * mm});
            skLineSegment(sketch, "E4596", {"start": v(-40.63, -262.98) * mm, "end": v(-40, -262.98) * mm});
            skLineSegment(sketch, "E4597", {"start": v(-40, -262.98) * mm, "end": v(-40, -263) * mm});
            skLineSegment(sketch, "E4598", {"start": v(-40, -263) * mm, "end": v(-20, -263) * mm});
            skLineSegment(sketch, "E4599", {"start": v(-20, -263) * mm, "end": v(-18.75, -262.92) * mm});
            skLineSegment(sketch, "E4600", {"start": v(-18.75, -262.92) * mm, "end": v(-17.51, -262.69) * mm});
            skLineSegment(sketch, "E4601", {"start": v(-17.51, -262.69) * mm, "end": v(-16.32, -262.3) * mm});
            skLineSegment(sketch, "E4602", {"start": v(-16.32, -262.3) * mm, "end": v(-15.18, -261.76) * mm});
            skLineSegment(sketch, "E4603", {"start": v(-15.18, -261.76) * mm, "end": v(-14.12, -261.1) * mm});
            skLineSegment(sketch, "E4604", {"start": v(-14.12, -261.1) * mm, "end": v(-13.15, -260.29) * mm});
            skLineSegment(sketch, "E4605", {"start": v(-13.15, -260.29) * mm, "end": v(-12.3, -259.37) * mm});
            skLineSegment(sketch, "E4606", {"start": v(-12.3, -259.37) * mm, "end": v(-11.56, -258.36) * mm});
            skLineSegment(sketch, "E4607", {"start": v(-11.56, -258.36) * mm, "end": v(-10.95, -257.26) * mm});
            skLineSegment(sketch, "E4608", {"start": v(-10.95, -257.26) * mm, "end": v(-10.49, -256.1) * mm});
            skLineSegment(sketch, "E4609", {"start": v(-10.49, -256.1) * mm, "end": v(-10.18, -254.87) * mm});
            skLineSegment(sketch, "E4610", {"start": v(-10.18, -254.87) * mm, "end": v(-10.02, -253.63) * mm});
            skLineSegment(sketch, "E4611", {"start": v(-10.02, -253.63) * mm, "end": v(-10.02, -253) * mm});
            skLineSegment(sketch, "E4612", {"start": v(-10.02, -253) * mm, "end": v(-10, -253) * mm});
            skLineSegment(sketch, "E4613", {"start": v(-10, -253) * mm, "end": v(-10, -203) * mm});
            skLineSegment(sketch, "E4614", {"start": v(-10, -203) * mm, "end": v(-50, -203) * mm});
            skLineSegment(sketch, "E4615", {"start": v(-50, -203) * mm, "end": v(-50, -187) * mm});
            skLineSegment(sketch, "E4616", {"start": v(-50, -187) * mm, "end": v(-70, -187) * mm});
            skLineSegment(sketch, "E4617", {"start": v(-70, -187) * mm, "end": v(-70, -203) * mm});
            skLineSegment(sketch, "E4618", {"start": v(-70, -203) * mm, "end": v(-195, -203) * mm});
            skLineSegment(sketch, "E4619", {"start": v(-195, -203) * mm, "end": v(-195, -187) * mm});
            skLineSegment(sketch, "E4620", {"start": v(-195, -187) * mm, "end": v(-215, -187) * mm});
            skLineSegment(sketch, "E4621", {"start": v(-215, -187) * mm, "end": v(-215, -203) * mm});
            skLineSegment(sketch, "E4622", {"start": v(-215, -203) * mm, "end": v(-340, -203) * mm});
            skLineSegment(sketch, "E4623", {"start": v(-340, -203) * mm, "end": v(-340, -187) * mm});
            skLineSegment(sketch, "E4624", {"start": v(-340, -187) * mm, "end": v(-360, -187) * mm});
            skLineSegment(sketch, "E4625", {"start": v(-360, -187) * mm, "end": v(-360, -203) * mm});
            skLineSegment(sketch, "E4626", {"start": v(-360, -203) * mm, "end": v(-400, -203) * mm});
            skLineSegment(sketch, "E4627", {"start": v(-400, -203) * mm, "end": v(-400, -253) * mm});
            skLineSegment(sketch, "E4628", {"start": v(-400, -253) * mm, "end": v(-399.92, -254.25) * mm});
            skLineSegment(sketch, "E4629", {"start": v(-399.92, -254.25) * mm, "end": v(-399.69, -255.49) * mm});
            skLineSegment(sketch, "E4630", {"start": v(-399.69, -255.49) * mm, "end": v(-399.3, -256.68) * mm});
            skLineSegment(sketch, "E4631", {"start": v(-399.3, -256.68) * mm, "end": v(-398.76, -257.82) * mm});
            skLineSegment(sketch, "E4632", {"start": v(-398.76, -257.82) * mm, "end": v(-398.09, -258.88) * mm});
            skLineSegment(sketch, "E4633", {"start": v(-398.09, -258.88) * mm, "end": v(-397.3, -259.85) * mm});
            skLineSegment(sketch, "E4634", {"start": v(-397.3, -259.85) * mm, "end": v(-396.37, -260.7) * mm});
            skLineSegment(sketch, "E4635", {"start": v(-396.37, -260.7) * mm, "end": v(-395.36, -261.44) * mm});
            skLineSegment(sketch, "E4636", {"start": v(-395.36, -261.44) * mm, "end": v(-394.26, -262.05) * mm});
            skLineSegment(sketch, "E4637", {"start": v(-394.26, -262.05) * mm, "end": v(-393.09, -262.51) * mm});
            skLineSegment(sketch, "E4638", {"start": v(-393.09, -262.51) * mm, "end": v(-391.87, -262.82) * mm});
            skLineSegment(sketch, "E4639", {"start": v(-391.87, -262.82) * mm, "end": v(-390.63, -262.98) * mm});
            skLineSegment(sketch, "E4640", {"start": v(-390.63, -262.98) * mm, "end": v(-390, -262.98) * mm});
            skLineSegment(sketch, "E4641", {"start": v(-390, -262.98) * mm, "end": v(-390, -263) * mm});
            skLineSegment(sketch, "E4642", {"start": v(-390, -263) * mm, "end": v(-370, -263) * mm});
            skLineSegment(sketch, "E4643", {"start": v(-370, -263) * mm, "end": v(-370, -262.98) * mm});
            skSolve(sketch);
        }
        {
            var Q0;
            Q0=makeQuery(id+"F0.imprint","IMPRINT",FACE,{"disambiguationData":[TD([[makeQuery(id+"F0.imprint","IMPRINT",EDGE,{"derivedFrom":sQuery(id+"F0.wireOp",EDGE,"E836")}),1.0]])]});
            extrude(context, id + "F1", {"entities" : qUnion([Q0]), "depth" : 8 * mm});
        }
        {
            var Q0;
            Q0=makeQuery(id+"F1.opExtrude","CAP_FACE",FACE,{"disambiguationData":[OSD([sQuery(id+"F0.wireOp",EDGE,"E836"),sQuery(id+"F0.wireOp",EDGE,"E837"),sQuery(id+"F0.wireOp",EDGE,"E838"),sQuery(id+"F0.wireOp",EDGE,"E839"),sQuery(id+"F0.wireOp",EDGE,"E840"),sQuery(id+"F0.wireOp",EDGE,"E841"),sQuery(id+"F0.wireOp",EDGE,"E842"),sQuery(id+"F0.wireOp",EDGE,"E843"),sQuery(id+"F0.wireOp",EDGE,"E844"),sQuery(id+"F0.wireOp",EDGE,"E845"),sQuery(id+"F0.wireOp",EDGE,"E846"),sQuery(id+"F0.wireOp",EDGE,"E847"),sQuery(id+"F0.wireOp",EDGE,"E848"),sQuery(id+"F0.wireOp",EDGE,"E849"),sQuery(id+"F0.wireOp",EDGE,"E850"),sQuery(id+"F0.wireOp",EDGE,"E851"),sQuery(id+"F0.wireOp",EDGE,"E852"),sQuery(id+"F0.wireOp",EDGE,"E853"),sQuery(id+"F0.wireOp",EDGE,"E854"),sQuery(id+"F0.wireOp",EDGE,"E855"),sQuery(id+"F0.wireOp",EDGE,"E856"),sQuery(id+"F0.wireOp",EDGE,"E857"),sQuery(id+"F0.wireOp",EDGE,"E858"),sQuery(id+"F0.wireOp",EDGE,"E859"),sQuery(id+"F0.wireOp",EDGE,"E860"),sQuery(id+"F0.wireOp",EDGE,"E861"),sQuery(id+"F0.wireOp",EDGE,"E862"),sQuery(id+"F0.wireOp",EDGE,"E863"),sQuery(id+"F0.wireOp",EDGE,"E864"),sQuery(id+"F0.wireOp",EDGE,"E865"),sQuery(id+"F0.wireOp",EDGE,"E866"),sQuery(id+"F0.wireOp",EDGE,"E867"),sQuery(id+"F0.wireOp",EDGE,"E868"),sQuery(id+"F0.wireOp",EDGE,"E869"),sQuery(id+"F0.wireOp",EDGE,"E870"),sQuery(id+"F0.wireOp",EDGE,"E871"),sQuery(id+"F0.wireOp",EDGE,"E872"),sQuery(id+"F0.wireOp",EDGE,"E873"),sQuery(id+"F0.wireOp",EDGE,"E874"),sQuery(id+"F0.wireOp",EDGE,"E875"),sQuery(id+"F0.wireOp",EDGE,"E876"),sQuery(id+"F0.wireOp",EDGE,"E877"),sQuery(id+"F0.wireOp",EDGE,"E878"),sQuery(id+"F0.wireOp",EDGE,"E879"),sQuery(id+"F0.wireOp",EDGE,"E880"),sQuery(id+"F0.wireOp",EDGE,"E881"),sQuery(id+"F0.wireOp",EDGE,"E882"),sQuery(id+"F0.wireOp",EDGE,"E883"),sQuery(id+"F0.wireOp",EDGE,"E884"),sQuery(id+"F0.wireOp",EDGE,"E885"),sQuery(id+"F0.wireOp",EDGE,"E886"),sQuery(id+"F0.wireOp",EDGE,"E887"),sQuery(id+"F0.wireOp",EDGE,"E888"),sQuery(id+"F0.wireOp",EDGE,"E889"),sQuery(id+"F0.wireOp",EDGE,"E890"),sQuery(id+"F0.wireOp",EDGE,"E891"),sQuery(id+"F0.wireOp",EDGE,"E892"),sQuery(id+"F0.wireOp",EDGE,"E893"),sQuery(id+"F0.wireOp",EDGE,"E894"),sQuery(id+"F0.wireOp",EDGE,"E895"),sQuery(id+"F0.wireOp",EDGE,"E896"),sQuery(id+"F0.wireOp",EDGE,"E897"),sQuery(id+"F0.wireOp",EDGE,"E898"),sQuery(id+"F0.wireOp",EDGE,"E899"),sQuery(id+"F0.wireOp",EDGE,"E900"),sQuery(id+"F0.wireOp",EDGE,"E901"),sQuery(id+"F0.wireOp",EDGE,"E902"),sQuery(id+"F0.wireOp",EDGE,"E903"),sQuery(id+"F0.wireOp",EDGE,"E904"),sQuery(id+"F0.wireOp",EDGE,"E905"),sQuery(id+"F0.wireOp",EDGE,"E906"),sQuery(id+"F0.wireOp",EDGE,"E907"),sQuery(id+"F0.wireOp",EDGE,"E908"),sQuery(id+"F0.wireOp",EDGE,"E909"),sQuery(id+"F0.wireOp",EDGE,"E910"),sQuery(id+"F0.wireOp",EDGE,"E911"),sQuery(id+"F0.wireOp",EDGE,"E912"),sQuery(id+"F0.wireOp",EDGE,"E913"),sQuery(id+"F0.wireOp",EDGE,"E914"),sQuery(id+"F0.wireOp",EDGE,"E915"),sQuery(id+"F0.wireOp",EDGE,"E916"),sQuery(id+"F0.wireOp",EDGE,"E917"),sQuery(id+"F0.wireOp",EDGE,"E918"),sQuery(id+"F0.wireOp",EDGE,"E919"),sQuery(id+"F0.wireOp",EDGE,"E920"),sQuery(id+"F0.wireOp",EDGE,"E921"),sQuery(id+"F0.wireOp",EDGE,"E922"),sQuery(id+"F0.wireOp",EDGE,"E923"),sQuery(id+"F0.wireOp",EDGE,"E924"),sQuery(id+"F0.wireOp",EDGE,"E925"),sQuery(id+"F0.wireOp",EDGE,"E926"),sQuery(id+"F0.wireOp",EDGE,"E927"),sQuery(id+"F0.wireOp",EDGE,"E928"),sQuery(id+"F0.wireOp",EDGE,"E929"),sQuery(id+"F0.wireOp",EDGE,"E930"),sQuery(id+"F0.wireOp",EDGE,"E931"),sQuery(id+"F0.wireOp",EDGE,"E932"),sQuery(id+"F0.wireOp",EDGE,"E933"),sQuery(id+"F0.wireOp",EDGE,"E934"),sQuery(id+"F0.wireOp",EDGE,"E935"),sQuery(id+"F0.wireOp",EDGE,"E936"),sQuery(id+"F0.wireOp",EDGE,"E937"),sQuery(id+"F0.wireOp",EDGE,"E938"),sQuery(id+"F0.wireOp",EDGE,"E939"),sQuery(id+"F0.wireOp",EDGE,"E940"),sQuery(id+"F0.wireOp",EDGE,"E941"),sQuery(id+"F0.wireOp",EDGE,"E942"),sQuery(id+"F0.wireOp",EDGE,"E943"),sQuery(id+"F0.wireOp",EDGE,"E944"),sQuery(id+"F0.wireOp",EDGE,"E945"),sQuery(id+"F0.wireOp",EDGE,"E946"),sQuery(id+"F0.wireOp",EDGE,"E947"),sQuery(id+"F0.wireOp",EDGE,"E948"),sQuery(id+"F0.wireOp",EDGE,"E949"),sQuery(id+"F0.wireOp",EDGE,"E950"),sQuery(id+"F0.wireOp",EDGE,"E951"),sQuery(id+"F0.wireOp",EDGE,"E952"),sQuery(id+"F0.wireOp",EDGE,"E953"),sQuery(id+"F0.wireOp",EDGE,"E954"),sQuery(id+"F0.wireOp",EDGE,"E955"),sQuery(id+"F0.wireOp",EDGE,"E956"),sQuery(id+"F0.wireOp",EDGE,"E957"),sQuery(id+"F0.wireOp",EDGE,"E958"),sQuery(id+"F0.wireOp",EDGE,"E959"),sQuery(id+"F0.wireOp",EDGE,"E960"),sQuery(id+"F0.wireOp",EDGE,"E961"),sQuery(id+"F0.wireOp",EDGE,"E962"),sQuery(id+"F0.wireOp",EDGE,"E963"),sQuery(id+"F0.wireOp",EDGE,"E964"),sQuery(id+"F0.wireOp",EDGE,"E965"),sQuery(id+"F0.wireOp",EDGE,"E966"),sQuery(id+"F0.wireOp",EDGE,"E967"),sQuery(id+"F0.wireOp",EDGE,"E968"),sQuery(id+"F0.wireOp",EDGE,"E969"),sQuery(id+"F0.wireOp",EDGE,"E970"),sQuery(id+"F0.wireOp",EDGE,"E971"),sQuery(id+"F0.wireOp",EDGE,"E972"),sQuery(id+"F0.wireOp",EDGE,"E973"),sQuery(id+"F0.wireOp",EDGE,"E974"),sQuery(id+"F0.wireOp",EDGE,"E975"),sQuery(id+"F0.wireOp",EDGE,"E976"),sQuery(id+"F0.wireOp",EDGE,"E977"),sQuery(id+"F0.wireOp",EDGE,"E978"),sQuery(id+"F0.wireOp",EDGE,"E979"),sQuery(id+"F0.wireOp",EDGE,"E980"),sQuery(id+"F0.wireOp",EDGE,"E981"),sQuery(id+"F0.wireOp",EDGE,"E982"),sQuery(id+"F0.wireOp",EDGE,"E983"),sQuery(id+"F0.wireOp",EDGE,"E984"),sQuery(id+"F0.wireOp",EDGE,"E985"),sQuery(id+"F0.wireOp",EDGE,"E986"),sQuery(id+"F0.wireOp",EDGE,"E987"),sQuery(id+"F0.wireOp",EDGE,"E988"),sQuery(id+"F0.wireOp",EDGE,"E989"),sQuery(id+"F0.wireOp",EDGE,"E990"),sQuery(id+"F0.wireOp",EDGE,"E991"),sQuery(id+"F0.wireOp",EDGE,"E992"),sQuery(id+"F0.wireOp",EDGE,"E993"),sQuery(id+"F0.wireOp",EDGE,"E994"),sQuery(id+"F0.wireOp",EDGE,"E995"),sQuery(id+"F0.wireOp",EDGE,"E996"),sQuery(id+"F0.wireOp",EDGE,"E997"),sQuery(id+"F0.wireOp",EDGE,"E998"),sQuery(id+"F0.wireOp",EDGE,"E999"),sQuery(id+"F0.wireOp",EDGE,"E1000"),sQuery(id+"F0.wireOp",EDGE,"E1001"),sQuery(id+"F0.wireOp",EDGE,"E1002"),sQuery(id+"F0.wireOp",EDGE,"E1003"),sQuery(id+"F0.wireOp",EDGE,"E1004"),sQuery(id+"F0.wireOp",EDGE,"E1005"),sQuery(id+"F0.wireOp",EDGE,"E1006"),sQuery(id+"F0.wireOp",EDGE,"E1007"),sQuery(id+"F0.wireOp",EDGE,"E1008"),sQuery(id+"F0.wireOp",EDGE,"E1009"),sQuery(id+"F0.wireOp",EDGE,"E1010"),sQuery(id+"F0.wireOp",EDGE,"E1011"),sQuery(id+"F0.wireOp",EDGE,"E1012"),sQuery(id+"F0.wireOp",EDGE,"E1013"),sQuery(id+"F0.wireOp",EDGE,"E1014"),sQuery(id+"F0.wireOp",EDGE,"E1015"),sQuery(id+"F0.wireOp",EDGE,"E1016"),sQuery(id+"F0.wireOp",EDGE,"E1017"),sQuery(id+"F0.wireOp",EDGE,"E1018"),sQuery(id+"F0.wireOp",EDGE,"E1019"),sQuery(id+"F0.wireOp",EDGE,"E1020"),sQuery(id+"F0.wireOp",EDGE,"E1021"),sQuery(id+"F0.wireOp",EDGE,"E1022"),sQuery(id+"F0.wireOp",EDGE,"E1023"),sQuery(id+"F0.wireOp",EDGE,"E1024"),sQuery(id+"F0.wireOp",EDGE,"E1025"),sQuery(id+"F0.wireOp",EDGE,"E1026"),sQuery(id+"F0.wireOp",EDGE,"E1027"),sQuery(id+"F0.wireOp",EDGE,"E1028"),sQuery(id+"F0.wireOp",EDGE,"E1029"),sQuery(id+"F0.wireOp",EDGE,"E1030"),sQuery(id+"F0.wireOp",EDGE,"E1031"),sQuery(id+"F0.wireOp",EDGE,"E1032"),sQuery(id+"F0.wireOp",EDGE,"E1033"),sQuery(id+"F0.wireOp",EDGE,"E1034"),sQuery(id+"F0.wireOp",EDGE,"E1035"),sQuery(id+"F0.wireOp",EDGE,"E1036"),sQuery(id+"F0.wireOp",EDGE,"E1037"),sQuery(id+"F0.wireOp",EDGE,"E1038"),sQuery(id+"F0.wireOp",EDGE,"E1039"),sQuery(id+"F0.wireOp",EDGE,"E1040"),sQuery(id+"F0.wireOp",EDGE,"E1041"),sQuery(id+"F0.wireOp",EDGE,"E1042"),sQuery(id+"F0.wireOp",EDGE,"E1043"),sQuery(id+"F0.wireOp",EDGE,"E1044"),sQuery(id+"F0.wireOp",EDGE,"E1045"),sQuery(id+"F0.wireOp",EDGE,"E1046"),sQuery(id+"F0.wireOp",EDGE,"E1047"),sQuery(id+"F0.wireOp",EDGE,"E1048"),sQuery(id+"F0.wireOp",EDGE,"E1049"),sQuery(id+"F0.wireOp",EDGE,"E1050"),sQuery(id+"F0.wireOp",EDGE,"E1051"),sQuery(id+"F0.wireOp",EDGE,"E1052"),sQuery(id+"F0.wireOp",EDGE,"E1053"),sQuery(id+"F0.wireOp",EDGE,"E1054"),sQuery(id+"F0.wireOp",EDGE,"E1055"),sQuery(id+"F0.wireOp",EDGE,"E1056"),sQuery(id+"F0.wireOp",EDGE,"E1057"),sQuery(id+"F0.wireOp",EDGE,"E1058"),sQuery(id+"F0.wireOp",EDGE,"E1059"),sQuery(id+"F0.wireOp",EDGE,"E1060"),sQuery(id+"F0.wireOp",EDGE,"E1061"),sQuery(id+"F0.wireOp",EDGE,"E1062"),sQuery(id+"F0.wireOp",EDGE,"E1063"),sQuery(id+"F0.wireOp",EDGE,"E1064"),sQuery(id+"F0.wireOp",EDGE,"E1065"),sQuery(id+"F0.wireOp",EDGE,"E1066"),sQuery(id+"F0.wireOp",EDGE,"E1067"),sQuery(id+"F0.wireOp",EDGE,"E1068"),sQuery(id+"F0.wireOp",EDGE,"E1069"),sQuery(id+"F0.wireOp",EDGE,"E1070"),sQuery(id+"F0.wireOp",EDGE,"E1071"),sQuery(id+"F0.wireOp",EDGE,"E1072"),sQuery(id+"F0.wireOp",EDGE,"E1073"),sQuery(id+"F0.wireOp",EDGE,"E1074"),sQuery(id+"F0.wireOp",EDGE,"E1075"),sQuery(id+"F0.wireOp",EDGE,"E1076"),sQuery(id+"F0.wireOp",EDGE,"E1077"),sQuery(id+"F0.wireOp",EDGE,"E1078"),sQuery(id+"F0.wireOp",EDGE,"E1079"),sQuery(id+"F0.wireOp",EDGE,"E1080"),sQuery(id+"F0.wireOp",EDGE,"E1081"),sQuery(id+"F0.wireOp",EDGE,"E1082"),sQuery(id+"F0.wireOp",EDGE,"E1083"),sQuery(id+"F0.wireOp",EDGE,"E1084"),sQuery(id+"F0.wireOp",EDGE,"E1085"),sQuery(id+"F0.wireOp",EDGE,"E1086"),sQuery(id+"F0.wireOp",EDGE,"E1087"),sQuery(id+"F0.wireOp",EDGE,"E1088"),sQuery(id+"F0.wireOp",EDGE,"E1089"),sQuery(id+"F0.wireOp",EDGE,"E1090"),sQuery(id+"F0.wireOp",EDGE,"E1091"),sQuery(id+"F0.wireOp",EDGE,"E1092"),sQuery(id+"F0.wireOp",EDGE,"E1093"),sQuery(id+"F0.wireOp",EDGE,"E1094"),sQuery(id+"F0.wireOp",EDGE,"E1095"),sQuery(id+"F0.wireOp",EDGE,"E1096"),sQuery(id+"F0.wireOp",EDGE,"E1097"),sQuery(id+"F0.wireOp",EDGE,"E1098"),sQuery(id+"F0.wireOp",EDGE,"E1099"),sQuery(id+"F0.wireOp",EDGE,"E1100"),sQuery(id+"F0.wireOp",EDGE,"E1101"),sQuery(id+"F0.wireOp",EDGE,"E1102"),sQuery(id+"F0.wireOp",EDGE,"E1103"),sQuery(id+"F0.wireOp",EDGE,"E1104"),sQuery(id+"F0.wireOp",EDGE,"E1105"),sQuery(id+"F0.wireOp",EDGE,"E1106"),sQuery(id+"F0.wireOp",EDGE,"E1107"),sQuery(id+"F0.wireOp",EDGE,"E1108"),sQuery(id+"F0.wireOp",EDGE,"E1109"),sQuery(id+"F0.wireOp",EDGE,"E1110"),sQuery(id+"F0.wireOp",EDGE,"E1111"),sQuery(id+"F0.wireOp",EDGE,"E1112"),sQuery(id+"F0.wireOp",EDGE,"E1113"),sQuery(id+"F0.wireOp",EDGE,"E1114"),sQuery(id+"F0.wireOp",EDGE,"E1115"),sQuery(id+"F0.wireOp",EDGE,"E1116"),sQuery(id+"F0.wireOp",EDGE,"E1117"),sQuery(id+"F0.wireOp",EDGE,"E1118"),sQuery(id+"F0.wireOp",EDGE,"E1119"),sQuery(id+"F0.wireOp",EDGE,"E1120"),sQuery(id+"F0.wireOp",EDGE,"E1121"),sQuery(id+"F0.wireOp",EDGE,"E1122"),sQuery(id+"F0.wireOp",EDGE,"E1123"),sQuery(id+"F0.wireOp",EDGE,"E1124"),sQuery(id+"F0.wireOp",EDGE,"E1125"),sQuery(id+"F0.wireOp",EDGE,"E1126"),sQuery(id+"F0.wireOp",EDGE,"E1127"),sQuery(id+"F0.wireOp",EDGE,"E1128"),sQuery(id+"F0.wireOp",EDGE,"E1129"),sQuery(id+"F0.wireOp",EDGE,"E1130"),sQuery(id+"F0.wireOp",EDGE,"E1131"),sQuery(id+"F0.wireOp",EDGE,"E1132"),sQuery(id+"F0.wireOp",EDGE,"E1133"),sQuery(id+"F0.wireOp",EDGE,"E1134"),sQuery(id+"F0.wireOp",EDGE,"E1135"),sQuery(id+"F0.wireOp",EDGE,"E1136"),sQuery(id+"F0.wireOp",EDGE,"E1137"),sQuery(id+"F0.wireOp",EDGE,"E1138"),sQuery(id+"F0.wireOp",EDGE,"E1139"),sQuery(id+"F0.wireOp",EDGE,"E1140"),sQuery(id+"F0.wireOp",EDGE,"E1141"),sQuery(id+"F0.wireOp",EDGE,"E1142"),sQuery(id+"F0.wireOp",EDGE,"E1143"),sQuery(id+"F0.wireOp",EDGE,"E1144"),sQuery(id+"F0.wireOp",EDGE,"E1145"),sQuery(id+"F0.wireOp",EDGE,"E1146"),sQuery(id+"F0.wireOp",EDGE,"E1147"),sQuery(id+"F0.wireOp",EDGE,"E1148"),sQuery(id+"F0.wireOp",EDGE,"E1149"),sQuery(id+"F0.wireOp",EDGE,"E1150"),sQuery(id+"F0.wireOp",EDGE,"E1151"),sQuery(id+"F0.wireOp",EDGE,"E1152"),sQuery(id+"F0.wireOp",EDGE,"E1153"),sQuery(id+"F0.wireOp",EDGE,"E1154"),sQuery(id+"F0.wireOp",EDGE,"E1155"),sQuery(id+"F0.wireOp",EDGE,"E1156"),sQuery(id+"F0.wireOp",EDGE,"E1157"),sQuery(id+"F0.wireOp",EDGE,"E1158"),sQuery(id+"F0.wireOp",EDGE,"E1159"),sQuery(id+"F0.wireOp",EDGE,"E1160"),sQuery(id+"F0.wireOp",EDGE,"E1161"),sQuery(id+"F0.wireOp",EDGE,"E1162"),sQuery(id+"F0.wireOp",EDGE,"E1163"),sQuery(id+"F0.wireOp",EDGE,"E1164"),sQuery(id+"F0.wireOp",EDGE,"E1165"),sQuery(id+"F0.wireOp",EDGE,"E1166"),sQuery(id+"F0.wireOp",EDGE,"E1167"),sQuery(id+"F0.wireOp",EDGE,"E1168"),sQuery(id+"F0.wireOp",EDGE,"E1169"),sQuery(id+"F0.wireOp",EDGE,"E1170"),sQuery(id+"F0.wireOp",EDGE,"E1171"),sQuery(id+"F0.wireOp",EDGE,"E1172"),sQuery(id+"F0.wireOp",EDGE,"E1173"),sQuery(id+"F0.wireOp",EDGE,"E1174"),sQuery(id+"F0.wireOp",EDGE,"E1175"),sQuery(id+"F0.wireOp",EDGE,"E1176"),sQuery(id+"F0.wireOp",EDGE,"E1177"),sQuery(id+"F0.wireOp",EDGE,"E1178"),sQuery(id+"F0.wireOp",EDGE,"E1179"),sQuery(id+"F0.wireOp",EDGE,"E1180"),sQuery(id+"F0.wireOp",EDGE,"E1181"),sQuery(id+"F0.wireOp",EDGE,"E1182"),sQuery(id+"F0.wireOp",EDGE,"E1183"),sQuery(id+"F0.wireOp",EDGE,"E1184"),sQuery(id+"F0.wireOp",EDGE,"E1185"),sQuery(id+"F0.wireOp",EDGE,"E1186"),sQuery(id+"F0.wireOp",EDGE,"E1187"),sQuery(id+"F0.wireOp",EDGE,"E1188"),sQuery(id+"F0.wireOp",EDGE,"E1189"),sQuery(id+"F0.wireOp",EDGE,"E1190"),sQuery(id+"F0.wireOp",EDGE,"E1191"),sQuery(id+"F0.wireOp",EDGE,"E1192"),sQuery(id+"F0.wireOp",EDGE,"E1193"),sQuery(id+"F0.wireOp",EDGE,"E1194"),sQuery(id+"F0.wireOp",EDGE,"E1195"),sQuery(id+"F0.wireOp",EDGE,"E1196"),sQuery(id+"F0.wireOp",EDGE,"E1197"),sQuery(id+"F0.wireOp",EDGE,"E1198"),sQuery(id+"F0.wireOp",EDGE,"E1199"),sQuery(id+"F0.wireOp",EDGE,"E1200"),sQuery(id+"F0.wireOp",EDGE,"E1201"),sQuery(id+"F0.wireOp",EDGE,"E1202"),sQuery(id+"F0.wireOp",EDGE,"E1203"),sQuery(id+"F0.wireOp",EDGE,"E1204"),sQuery(id+"F0.wireOp",EDGE,"E1205"),sQuery(id+"F0.wireOp",EDGE,"E1206"),sQuery(id+"F0.wireOp",EDGE,"E1207"),sQuery(id+"F0.wireOp",EDGE,"E1208"),sQuery(id+"F0.wireOp",EDGE,"E1209"),sQuery(id+"F0.wireOp",EDGE,"E1210"),sQuery(id+"F0.wireOp",EDGE,"E1211"),sQuery(id+"F0.wireOp",EDGE,"E1212"),sQuery(id+"F0.wireOp",EDGE,"E1213"),sQuery(id+"F0.wireOp",EDGE,"E1214"),sQuery(id+"F0.wireOp",EDGE,"E1215"),sQuery(id+"F0.wireOp",EDGE,"E1216"),sQuery(id+"F0.wireOp",EDGE,"E1217"),sQuery(id+"F0.wireOp",EDGE,"E1218"),sQuery(id+"F0.wireOp",EDGE,"E1219"),sQuery(id+"F0.wireOp",EDGE,"E1220"),sQuery(id+"F0.wireOp",EDGE,"E1221"),sQuery(id+"F0.wireOp",EDGE,"E1222"),sQuery(id+"F0.wireOp",EDGE,"E1223"),sQuery(id+"F0.wireOp",EDGE,"E1224"),sQuery(id+"F0.wireOp",EDGE,"E1225"),sQuery(id+"F0.wireOp",EDGE,"E1226"),sQuery(id+"F0.wireOp",EDGE,"E1227"),sQuery(id+"F0.wireOp",EDGE,"E1228"),sQuery(id+"F0.wireOp",EDGE,"E1229"),sQuery(id+"F0.wireOp",EDGE,"E1230"),sQuery(id+"F0.wireOp",EDGE,"E1231"),sQuery(id+"F0.wireOp",EDGE,"E1232"),sQuery(id+"F0.wireOp",EDGE,"E1233"),sQuery(id+"F0.wireOp",EDGE,"E1234"),sQuery(id+"F0.wireOp",EDGE,"E1235"),sQuery(id+"F0.wireOp",EDGE,"E1236"),sQuery(id+"F0.wireOp",EDGE,"E1237"),sQuery(id+"F0.wireOp",EDGE,"E1238"),sQuery(id+"F0.wireOp",EDGE,"E1239"),sQuery(id+"F0.wireOp",EDGE,"E1240"),sQuery(id+"F0.wireOp",EDGE,"E1241"),sQuery(id+"F0.wireOp",EDGE,"E1242"),sQuery(id+"F0.wireOp",EDGE,"E1243"),sQuery(id+"F0.wireOp",EDGE,"E1244"),sQuery(id+"F0.wireOp",EDGE,"E1245"),sQuery(id+"F0.wireOp",EDGE,"E1246"),sQuery(id+"F0.wireOp",EDGE,"E1247"),sQuery(id+"F0.wireOp",EDGE,"E1248"),sQuery(id+"F0.wireOp",EDGE,"E1249"),sQuery(id+"F0.wireOp",EDGE,"E1250"),sQuery(id+"F0.wireOp",EDGE,"E1251"),sQuery(id+"F0.wireOp",EDGE,"E1252"),sQuery(id+"F0.wireOp",EDGE,"E1253"),sQuery(id+"F0.wireOp",EDGE,"E1254"),sQuery(id+"F0.wireOp",EDGE,"E1255"),sQuery(id+"F0.wireOp",EDGE,"E1256"),sQuery(id+"F0.wireOp",EDGE,"E1257"),sQuery(id+"F0.wireOp",EDGE,"E1258"),sQuery(id+"F0.wireOp",EDGE,"E1259"),sQuery(id+"F0.wireOp",EDGE,"E1260"),sQuery(id+"F0.wireOp",EDGE,"E1261"),sQuery(id+"F0.wireOp",EDGE,"E1262"),sQuery(id+"F0.wireOp",EDGE,"E1263"),sQuery(id+"F0.wireOp",EDGE,"E1264"),sQuery(id+"F0.wireOp",EDGE,"E1265"),sQuery(id+"F0.wireOp",EDGE,"E1266"),sQuery(id+"F0.wireOp",EDGE,"E1267"),sQuery(id+"F0.wireOp",EDGE,"E1268"),sQuery(id+"F0.wireOp",EDGE,"E1269"),sQuery(id+"F0.wireOp",EDGE,"E1270"),sQuery(id+"F0.wireOp",EDGE,"E1271"),sQuery(id+"F0.wireOp",EDGE,"E1272"),sQuery(id+"F0.wireOp",EDGE,"E1273"),sQuery(id+"F0.wireOp",EDGE,"E1274"),sQuery(id+"F0.wireOp",EDGE,"E1275"),sQuery(id+"F0.wireOp",EDGE,"E1276"),sQuery(id+"F0.wireOp",EDGE,"E1277"),sQuery(id+"F0.wireOp",EDGE,"E1278"),sQuery(id+"F0.wireOp",EDGE,"E1279"),sQuery(id+"F0.wireOp",EDGE,"E1280"),sQuery(id+"F0.wireOp",EDGE,"E1281"),sQuery(id+"F0.wireOp",EDGE,"E1282"),sQuery(id+"F0.wireOp",EDGE,"E1283"),sQuery(id+"F0.wireOp",EDGE,"E1284"),sQuery(id+"F0.wireOp",EDGE,"E1285"),sQuery(id+"F0.wireOp",EDGE,"E1286"),sQuery(id+"F0.wireOp",EDGE,"E1287"),sQuery(id+"F0.wireOp",EDGE,"E1288"),sQuery(id+"F0.wireOp",EDGE,"E1289"),sQuery(id+"F0.wireOp",EDGE,"E1290"),sQuery(id+"F0.wireOp",EDGE,"E1291"),sQuery(id+"F0.wireOp",EDGE,"E1292"),sQuery(id+"F0.wireOp",EDGE,"E1293"),sQuery(id+"F0.wireOp",EDGE,"E1294"),sQuery(id+"F0.wireOp",EDGE,"E1295"),sQuery(id+"F0.wireOp",EDGE,"E1296"),sQuery(id+"F0.wireOp",EDGE,"E1297"),sQuery(id+"F0.wireOp",EDGE,"E1298"),sQuery(id+"F0.wireOp",EDGE,"E1299"),sQuery(id+"F0.wireOp",EDGE,"E1300"),sQuery(id+"F0.wireOp",EDGE,"E1301"),sQuery(id+"F0.wireOp",EDGE,"E1302"),sQuery(id+"F0.wireOp",EDGE,"E1303"),sQuery(id+"F0.wireOp",EDGE,"E1304"),sQuery(id+"F0.wireOp",EDGE,"E1305"),sQuery(id+"F0.wireOp",EDGE,"E1306"),sQuery(id+"F0.wireOp",EDGE,"E1307"),sQuery(id+"F0.wireOp",EDGE,"E1308"),sQuery(id+"F0.wireOp",EDGE,"E1309"),sQuery(id+"F0.wireOp",EDGE,"E1310"),sQuery(id+"F0.wireOp",EDGE,"E1311"),sQuery(id+"F0.wireOp",EDGE,"E1312"),sQuery(id+"F0.wireOp",EDGE,"E1313"),sQuery(id+"F0.wireOp",EDGE,"E1314"),sQuery(id+"F0.wireOp",EDGE,"E1315"),sQuery(id+"F0.wireOp",EDGE,"E1316"),sQuery(id+"F0.wireOp",EDGE,"E1317"),sQuery(id+"F0.wireOp",EDGE,"E1318"),sQuery(id+"F0.wireOp",EDGE,"E1319"),sQuery(id+"F0.wireOp",EDGE,"E1320"),sQuery(id+"F0.wireOp",EDGE,"E1321"),sQuery(id+"F0.wireOp",EDGE,"E1322"),sQuery(id+"F0.wireOp",EDGE,"E1323"),sQuery(id+"F0.wireOp",EDGE,"E1324"),sQuery(id+"F0.wireOp",EDGE,"E1325"),sQuery(id+"F0.wireOp",EDGE,"E1326"),sQuery(id+"F0.wireOp",EDGE,"E1327"),sQuery(id+"F0.wireOp",EDGE,"E1328"),sQuery(id+"F0.wireOp",EDGE,"E1329"),sQuery(id+"F0.wireOp",EDGE,"E1330"),sQuery(id+"F0.wireOp",EDGE,"E1331"),sQuery(id+"F0.wireOp",EDGE,"E1332"),sQuery(id+"F0.wireOp",EDGE,"E1333"),sQuery(id+"F0.wireOp",EDGE,"E1334"),sQuery(id+"F0.wireOp",EDGE,"E1335"),sQuery(id+"F0.wireOp",EDGE,"E1336"),sQuery(id+"F0.wireOp",EDGE,"E1337"),sQuery(id+"F0.wireOp",EDGE,"E1338"),sQuery(id+"F0.wireOp",EDGE,"E1339"),sQuery(id+"F0.wireOp",EDGE,"E1340"),sQuery(id+"F0.wireOp",EDGE,"E1341"),sQuery(id+"F0.wireOp",EDGE,"E1342"),sQuery(id+"F0.wireOp",EDGE,"E1343"),sQuery(id+"F0.wireOp",EDGE,"E1344"),sQuery(id+"F0.wireOp",EDGE,"E1345"),sQuery(id+"F0.wireOp",EDGE,"E1346"),sQuery(id+"F0.wireOp",EDGE,"E1347"),sQuery(id+"F0.wireOp",EDGE,"E1348"),sQuery(id+"F0.wireOp",EDGE,"E1349"),sQuery(id+"F0.wireOp",EDGE,"E1350"),sQuery(id+"F0.wireOp",EDGE,"E1351"),sQuery(id+"F0.wireOp",EDGE,"E1352"),sQuery(id+"F0.wireOp",EDGE,"E1353"),sQuery(id+"F0.wireOp",EDGE,"E1354"),sQuery(id+"F0.wireOp",EDGE,"E1355"),sQuery(id+"F0.wireOp",EDGE,"E1356"),sQuery(id+"F0.wireOp",EDGE,"E1357"),sQuery(id+"F0.wireOp",EDGE,"E1358"),sQuery(id+"F0.wireOp",EDGE,"E1359"),sQuery(id+"F0.wireOp",EDGE,"E1360"),sQuery(id+"F0.wireOp",EDGE,"E1361"),sQuery(id+"F0.wireOp",EDGE,"E1362"),sQuery(id+"F0.wireOp",EDGE,"E1363"),sQuery(id+"F0.wireOp",EDGE,"E1364"),sQuery(id+"F0.wireOp",EDGE,"E1365"),sQuery(id+"F0.wireOp",EDGE,"E1366"),sQuery(id+"F0.wireOp",EDGE,"E1367"),sQuery(id+"F0.wireOp",EDGE,"E1368"),sQuery(id+"F0.wireOp",EDGE,"E1369"),sQuery(id+"F0.wireOp",EDGE,"E1370"),sQuery(id+"F0.wireOp",EDGE,"E1371"),sQuery(id+"F0.wireOp",EDGE,"E1372"),sQuery(id+"F0.wireOp",EDGE,"E1373"),sQuery(id+"F0.wireOp",EDGE,"E1374"),sQuery(id+"F0.wireOp",EDGE,"E1375"),sQuery(id+"F0.wireOp",EDGE,"E1376"),sQuery(id+"F0.wireOp",EDGE,"E1377"),sQuery(id+"F0.wireOp",EDGE,"E1378"),sQuery(id+"F0.wireOp",EDGE,"E1379"),sQuery(id+"F0.wireOp",EDGE,"E1380"),sQuery(id+"F0.wireOp",EDGE,"E1381"),sQuery(id+"F0.wireOp",EDGE,"E1382"),sQuery(id+"F0.wireOp",EDGE,"E1383"),sQuery(id+"F0.wireOp",EDGE,"E1384"),sQuery(id+"F0.wireOp",EDGE,"E1385"),sQuery(id+"F0.wireOp",EDGE,"E1386"),sQuery(id+"F0.wireOp",EDGE,"E1387"),sQuery(id+"F0.wireOp",EDGE,"E1388"),sQuery(id+"F0.wireOp",EDGE,"E1389"),sQuery(id+"F0.wireOp",EDGE,"E1390"),sQuery(id+"F0.wireOp",EDGE,"E1391"),sQuery(id+"F0.wireOp",EDGE,"E1392"),sQuery(id+"F0.wireOp",EDGE,"E1393"),sQuery(id+"F0.wireOp",EDGE,"E1394"),sQuery(id+"F0.wireOp",EDGE,"E1395"),sQuery(id+"F0.wireOp",EDGE,"E1396"),sQuery(id+"F0.wireOp",EDGE,"E1397"),sQuery(id+"F0.wireOp",EDGE,"E1398"),sQuery(id+"F0.wireOp",EDGE,"E1399"),sQuery(id+"F0.wireOp",EDGE,"E1400"),sQuery(id+"F0.wireOp",EDGE,"E1401"),sQuery(id+"F0.wireOp",EDGE,"E1402"),sQuery(id+"F0.wireOp",EDGE,"E1403"),sQuery(id+"F0.wireOp",EDGE,"E1404"),sQuery(id+"F0.wireOp",EDGE,"E1405"),sQuery(id+"F0.wireOp",EDGE,"E1406"),sQuery(id+"F0.wireOp",EDGE,"E1407"),sQuery(id+"F0.wireOp",EDGE,"E1408"),sQuery(id+"F0.wireOp",EDGE,"E1409"),sQuery(id+"F0.wireOp",EDGE,"E1410"),sQuery(id+"F0.wireOp",EDGE,"E1411"),sQuery(id+"F0.wireOp",EDGE,"E1412"),sQuery(id+"F0.wireOp",EDGE,"E1413"),sQuery(id+"F0.wireOp",EDGE,"E1414"),sQuery(id+"F0.wireOp",EDGE,"E1415"),sQuery(id+"F0.wireOp",EDGE,"E1416"),sQuery(id+"F0.wireOp",EDGE,"E1417"),sQuery(id+"F0.wireOp",EDGE,"E1418"),sQuery(id+"F0.wireOp",EDGE,"E1419"),sQuery(id+"F0.wireOp",EDGE,"E1420"),sQuery(id+"F0.wireOp",EDGE,"E1421"),sQuery(id+"F0.wireOp",EDGE,"E1422"),sQuery(id+"F0.wireOp",EDGE,"E1423"),sQuery(id+"F0.wireOp",EDGE,"E1424"),sQuery(id+"F0.wireOp",EDGE,"E1425"),sQuery(id+"F0.wireOp",EDGE,"E1426"),sQuery(id+"F0.wireOp",EDGE,"E1427"),sQuery(id+"F0.wireOp",EDGE,"E1428"),sQuery(id+"F0.wireOp",EDGE,"E1429"),sQuery(id+"F0.wireOp",EDGE,"E1430"),sQuery(id+"F0.wireOp",EDGE,"E1431"),sQuery(id+"F0.wireOp",EDGE,"E1432"),sQuery(id+"F0.wireOp",EDGE,"E1433"),sQuery(id+"F0.wireOp",EDGE,"E1434"),sQuery(id+"F0.wireOp",EDGE,"E1435"),sQuery(id+"F0.wireOp",EDGE,"E1436"),sQuery(id+"F0.wireOp",EDGE,"E1437"),sQuery(id+"F0.wireOp",EDGE,"E1438"),sQuery(id+"F0.wireOp",EDGE,"E1439"),sQuery(id+"F0.wireOp",EDGE,"E1440"),sQuery(id+"F0.wireOp",EDGE,"E1441"),sQuery(id+"F0.wireOp",EDGE,"E1442"),sQuery(id+"F0.wireOp",EDGE,"E1443"),sQuery(id+"F0.wireOp",EDGE,"E1444"),sQuery(id+"F0.wireOp",EDGE,"E1445"),sQuery(id+"F0.wireOp",EDGE,"E1446"),sQuery(id+"F0.wireOp",EDGE,"E1447"),sQuery(id+"F0.wireOp",EDGE,"E1448"),sQuery(id+"F0.wireOp",EDGE,"E1449"),sQuery(id+"F0.wireOp",EDGE,"E1450"),sQuery(id+"F0.wireOp",EDGE,"E1451"),sQuery(id+"F0.wireOp",EDGE,"E1452"),sQuery(id+"F0.wireOp",EDGE,"E1453"),sQuery(id+"F0.wireOp",EDGE,"E1454"),sQuery(id+"F0.wireOp",EDGE,"E1455"),sQuery(id+"F0.wireOp",EDGE,"E1456"),sQuery(id+"F0.wireOp",EDGE,"E1457"),sQuery(id+"F0.wireOp",EDGE,"E1458"),sQuery(id+"F0.wireOp",EDGE,"E1459"),sQuery(id+"F0.wireOp",EDGE,"E1460"),sQuery(id+"F0.wireOp",EDGE,"E1461"),sQuery(id+"F0.wireOp",EDGE,"E1462"),sQuery(id+"F0.wireOp",EDGE,"E1463"),sQuery(id+"F0.wireOp",EDGE,"E1464"),sQuery(id+"F0.wireOp",EDGE,"E1465"),sQuery(id+"F0.wireOp",EDGE,"E1466"),sQuery(id+"F0.wireOp",EDGE,"E1467"),sQuery(id+"F0.wireOp",EDGE,"E1468"),sQuery(id+"F0.wireOp",EDGE,"E1469"),sQuery(id+"F0.wireOp",EDGE,"E1470"),sQuery(id+"F0.wireOp",EDGE,"E1471"),sQuery(id+"F0.wireOp",EDGE,"E1472"),sQuery(id+"F0.wireOp",EDGE,"E1473"),sQuery(id+"F0.wireOp",EDGE,"E1474"),sQuery(id+"F0.wireOp",EDGE,"E1475"),sQuery(id+"F0.wireOp",EDGE,"E1476"),sQuery(id+"F0.wireOp",EDGE,"E1477"),sQuery(id+"F0.wireOp",EDGE,"E1478"),sQuery(id+"F0.wireOp",EDGE,"E1479"),sQuery(id+"F0.wireOp",EDGE,"E1480"),sQuery(id+"F0.wireOp",EDGE,"E1481"),sQuery(id+"F0.wireOp",EDGE,"E1482"),sQuery(id+"F0.wireOp",EDGE,"E1483"),sQuery(id+"F0.wireOp",EDGE,"E1484"),sQuery(id+"F0.wireOp",EDGE,"E1485"),sQuery(id+"F0.wireOp",EDGE,"E1486"),sQuery(id+"F0.wireOp",EDGE,"E1487"),sQuery(id+"F0.wireOp",EDGE,"E1488"),sQuery(id+"F0.wireOp",EDGE,"E1489"),sQuery(id+"F0.wireOp",EDGE,"E1490"),sQuery(id+"F0.wireOp",EDGE,"E1491"),sQuery(id+"F0.wireOp",EDGE,"E1492"),sQuery(id+"F0.wireOp",EDGE,"E1493"),sQuery(id+"F0.wireOp",EDGE,"E1494"),sQuery(id+"F0.wireOp",EDGE,"E1495"),sQuery(id+"F0.wireOp",EDGE,"E1496"),sQuery(id+"F0.wireOp",EDGE,"E1497"),sQuery(id+"F0.wireOp",EDGE,"E1498"),sQuery(id+"F0.wireOp",EDGE,"E1499"),sQuery(id+"F0.wireOp",EDGE,"E1500"),sQuery(id+"F0.wireOp",EDGE,"E1501"),sQuery(id+"F0.wireOp",EDGE,"E1502"),sQuery(id+"F0.wireOp",EDGE,"E1503"),sQuery(id+"F0.wireOp",EDGE,"E1504"),sQuery(id+"F0.wireOp",EDGE,"E1505"),sQuery(id+"F0.wireOp",EDGE,"E1506"),sQuery(id+"F0.wireOp",EDGE,"E1507"),sQuery(id+"F0.wireOp",EDGE,"E1508"),sQuery(id+"F0.wireOp",EDGE,"E1509"),sQuery(id+"F0.wireOp",EDGE,"E1510"),sQuery(id+"F0.wireOp",EDGE,"E1511"),sQuery(id+"F0.wireOp",EDGE,"E1512"),sQuery(id+"F0.wireOp",EDGE,"E1513"),sQuery(id+"F0.wireOp",EDGE,"E1514"),sQuery(id+"F0.wireOp",EDGE,"E1515"),sQuery(id+"F0.wireOp",EDGE,"E1516"),sQuery(id+"F0.wireOp",EDGE,"E1517"),sQuery(id+"F0.wireOp",EDGE,"E1518"),sQuery(id+"F0.wireOp",EDGE,"E1519"),sQuery(id+"F0.wireOp",EDGE,"E1520"),sQuery(id+"F0.wireOp",EDGE,"E1521"),sQuery(id+"F0.wireOp",EDGE,"E1522"),sQuery(id+"F0.wireOp",EDGE,"E1523"),sQuery(id+"F0.wireOp",EDGE,"E1524"),sQuery(id+"F0.wireOp",EDGE,"E1525"),sQuery(id+"F0.wireOp",EDGE,"E1526"),sQuery(id+"F0.wireOp",EDGE,"E1527"),sQuery(id+"F0.wireOp",EDGE,"E1528"),sQuery(id+"F0.wireOp",EDGE,"E1529"),sQuery(id+"F0.wireOp",EDGE,"E1530"),sQuery(id+"F0.wireOp",EDGE,"E1531"),sQuery(id+"F0.wireOp",EDGE,"E1532"),sQuery(id+"F0.wireOp",EDGE,"E1533"),sQuery(id+"F0.wireOp",EDGE,"E1534"),sQuery(id+"F0.wireOp",EDGE,"E1535"),sQuery(id+"F0.wireOp",EDGE,"E1536"),sQuery(id+"F0.wireOp",EDGE,"E1537"),sQuery(id+"F0.wireOp",EDGE,"E1538"),sQuery(id+"F0.wireOp",EDGE,"E1539"),sQuery(id+"F0.wireOp",EDGE,"E1540"),sQuery(id+"F0.wireOp",EDGE,"E1541"),sQuery(id+"F0.wireOp",EDGE,"E1542"),sQuery(id+"F0.wireOp",EDGE,"E1543"),sQuery(id+"F0.wireOp",EDGE,"E1544"),sQuery(id+"F0.wireOp",EDGE,"E1545"),sQuery(id+"F0.wireOp",EDGE,"E1546"),sQuery(id+"F0.wireOp",EDGE,"E1547"),sQuery(id+"F0.wireOp",EDGE,"E1548"),sQuery(id+"F0.wireOp",EDGE,"E1549"),sQuery(id+"F0.wireOp",EDGE,"E1550"),sQuery(id+"F0.wireOp",EDGE,"E1551"),sQuery(id+"F0.wireOp",EDGE,"E1552"),sQuery(id+"F0.wireOp",EDGE,"E1553"),sQuery(id+"F0.wireOp",EDGE,"E1554"),sQuery(id+"F0.wireOp",EDGE,"E1555"),sQuery(id+"F0.wireOp",EDGE,"E1556"),sQuery(id+"F0.wireOp",EDGE,"E1557"),sQuery(id+"F0.wireOp",EDGE,"E1558"),sQuery(id+"F0.wireOp",EDGE,"E1559"),sQuery(id+"F0.wireOp",EDGE,"E1560"),sQuery(id+"F0.wireOp",EDGE,"E1561"),sQuery(id+"F0.wireOp",EDGE,"E1562"),sQuery(id+"F0.wireOp",EDGE,"E1563"),sQuery(id+"F0.wireOp",EDGE,"E1564"),sQuery(id+"F0.wireOp",EDGE,"E1565"),sQuery(id+"F0.wireOp",EDGE,"E1566"),sQuery(id+"F0.wireOp",EDGE,"E1567"),sQuery(id+"F0.wireOp",EDGE,"E1568"),sQuery(id+"F0.wireOp",EDGE,"E1569"),sQuery(id+"F0.wireOp",EDGE,"E1570"),sQuery(id+"F0.wireOp",EDGE,"E1571"),sQuery(id+"F0.wireOp",EDGE,"E1572"),sQuery(id+"F0.wireOp",EDGE,"E1573"),sQuery(id+"F0.wireOp",EDGE,"E1574"),sQuery(id+"F0.wireOp",EDGE,"E1575"),sQuery(id+"F0.wireOp",EDGE,"E1576"),sQuery(id+"F0.wireOp",EDGE,"E1577"),sQuery(id+"F0.wireOp",EDGE,"E1578"),sQuery(id+"F0.wireOp",EDGE,"E1579"),sQuery(id+"F0.wireOp",EDGE,"E1580"),sQuery(id+"F0.wireOp",EDGE,"E1581"),sQuery(id+"F0.wireOp",EDGE,"E1582"),sQuery(id+"F0.wireOp",EDGE,"E1583"),sQuery(id+"F0.wireOp",EDGE,"E1584"),sQuery(id+"F0.wireOp",EDGE,"E1585"),sQuery(id+"F0.wireOp",EDGE,"E1586"),sQuery(id+"F0.wireOp",EDGE,"E1587"),sQuery(id+"F0.wireOp",EDGE,"E1588"),sQuery(id+"F0.wireOp",EDGE,"E1589"),sQuery(id+"F0.wireOp",EDGE,"E1590"),sQuery(id+"F0.wireOp",EDGE,"E1591"),sQuery(id+"F0.wireOp",EDGE,"E1592"),sQuery(id+"F0.wireOp",EDGE,"E1593"),sQuery(id+"F0.wireOp",EDGE,"E1594"),sQuery(id+"F0.wireOp",EDGE,"E1595"),sQuery(id+"F0.wireOp",EDGE,"E1596"),sQuery(id+"F0.wireOp",EDGE,"E1597"),sQuery(id+"F0.wireOp",EDGE,"E1598"),sQuery(id+"F0.wireOp",EDGE,"E1599"),sQuery(id+"F0.wireOp",EDGE,"E1600"),sQuery(id+"F0.wireOp",EDGE,"E1601"),sQuery(id+"F0.wireOp",EDGE,"E1602"),sQuery(id+"F0.wireOp",EDGE,"E1603"),sQuery(id+"F0.wireOp",EDGE,"E1604"),sQuery(id+"F0.wireOp",EDGE,"E1605"),sQuery(id+"F0.wireOp",EDGE,"E1606"),sQuery(id+"F0.wireOp",EDGE,"E1607"),sQuery(id+"F0.wireOp",EDGE,"E1608"),sQuery(id+"F0.wireOp",EDGE,"E1609"),sQuery(id+"F0.wireOp",EDGE,"E1610"),sQuery(id+"F0.wireOp",EDGE,"E1611"),sQuery(id+"F0.wireOp",EDGE,"E1612"),sQuery(id+"F0.wireOp",EDGE,"E1613"),sQuery(id+"F0.wireOp",EDGE,"E1614"),sQuery(id+"F0.wireOp",EDGE,"E1615"),sQuery(id+"F0.wireOp",EDGE,"E1616"),sQuery(id+"F0.wireOp",EDGE,"E1617"),sQuery(id+"F0.wireOp",EDGE,"E1618"),sQuery(id+"F0.wireOp",EDGE,"E1619"),sQuery(id+"F0.wireOp",EDGE,"E1620"),sQuery(id+"F0.wireOp",EDGE,"E1621"),sQuery(id+"F0.wireOp",EDGE,"E1622"),sQuery(id+"F0.wireOp",EDGE,"E1623"),sQuery(id+"F0.wireOp",EDGE,"E1624"),sQuery(id+"F0.wireOp",EDGE,"E1625"),sQuery(id+"F0.wireOp",EDGE,"E1626"),sQuery(id+"F0.wireOp",EDGE,"E1627"),sQuery(id+"F0.wireOp",EDGE,"E1628"),sQuery(id+"F0.wireOp",EDGE,"E1629"),sQuery(id+"F0.wireOp",EDGE,"E1630"),sQuery(id+"F0.wireOp",EDGE,"E1631"),sQuery(id+"F0.wireOp",EDGE,"E1632"),sQuery(id+"F0.wireOp",EDGE,"E1633"),sQuery(id+"F0.wireOp",EDGE,"E1634"),sQuery(id+"F0.wireOp",EDGE,"E1635"),sQuery(id+"F0.wireOp",EDGE,"E1636"),sQuery(id+"F0.wireOp",EDGE,"E1637"),sQuery(id+"F0.wireOp",EDGE,"E1638"),sQuery(id+"F0.wireOp",EDGE,"E1639"),sQuery(id+"F0.wireOp",EDGE,"E1640"),sQuery(id+"F0.wireOp",EDGE,"E1641"),sQuery(id+"F0.wireOp",EDGE,"E1642"),sQuery(id+"F0.wireOp",EDGE,"E1643"),sQuery(id+"F0.wireOp",EDGE,"E1644"),sQuery(id+"F0.wireOp",EDGE,"E1645"),sQuery(id+"F0.wireOp",EDGE,"E1646"),sQuery(id+"F0.wireOp",EDGE,"E1647"),sQuery(id+"F0.wireOp",EDGE,"E1648"),sQuery(id+"F0.wireOp",EDGE,"E1649"),sQuery(id+"F0.wireOp",EDGE,"E1650"),sQuery(id+"F0.wireOp",EDGE,"E1651"),sQuery(id+"F0.wireOp",EDGE,"E1652"),sQuery(id+"F0.wireOp",EDGE,"E1653"),sQuery(id+"F0.wireOp",EDGE,"E1654"),sQuery(id+"F0.wireOp",EDGE,"E1655"),sQuery(id+"F0.wireOp",EDGE,"E1656"),sQuery(id+"F0.wireOp",EDGE,"E1657"),sQuery(id+"F0.wireOp",EDGE,"E1658"),sQuery(id+"F0.wireOp",EDGE,"E1659"),sQuery(id+"F0.wireOp",EDGE,"E1660"),sQuery(id+"F0.wireOp",EDGE,"E1661"),sQuery(id+"F0.wireOp",EDGE,"E1662"),sQuery(id+"F0.wireOp",EDGE,"E1663"),sQuery(id+"F0.wireOp",EDGE,"E1664"),sQuery(id+"F0.wireOp",EDGE,"E1665"),sQuery(id+"F0.wireOp",EDGE,"E1666"),sQuery(id+"F0.wireOp",EDGE,"E1667"),sQuery(id+"F0.wireOp",EDGE,"E1668"),sQuery(id+"F0.wireOp",EDGE,"E1669"),sQuery(id+"F0.wireOp",EDGE,"E1670"),sQuery(id+"F0.wireOp",EDGE,"E1671"),sQuery(id+"F0.wireOp",EDGE,"E1672"),sQuery(id+"F0.wireOp",EDGE,"E1673"),sQuery(id+"F0.wireOp",EDGE,"E1674"),sQuery(id+"F0.wireOp",EDGE,"E1675"),sQuery(id+"F0.wireOp",EDGE,"E1676"),sQuery(id+"F0.wireOp",EDGE,"E1677"),sQuery(id+"F0.wireOp",EDGE,"E1678"),sQuery(id+"F0.wireOp",EDGE,"E1679"),sQuery(id+"F0.wireOp",EDGE,"E1680"),sQuery(id+"F0.wireOp",EDGE,"E1681"),sQuery(id+"F0.wireOp",EDGE,"E1682"),sQuery(id+"F0.wireOp",EDGE,"E1683"),sQuery(id+"F0.wireOp",EDGE,"E1684"),sQuery(id+"F0.wireOp",EDGE,"E1685"),sQuery(id+"F0.wireOp",EDGE,"E1686"),sQuery(id+"F0.wireOp",EDGE,"E1687"),sQuery(id+"F0.wireOp",EDGE,"E1688"),sQuery(id+"F0.wireOp",EDGE,"E1689"),sQuery(id+"F0.wireOp",EDGE,"E1690"),sQuery(id+"F0.wireOp",EDGE,"E1691"),sQuery(id+"F0.wireOp",EDGE,"E1692"),sQuery(id+"F0.wireOp",EDGE,"E1693"),sQuery(id+"F0.wireOp",EDGE,"E1694"),sQuery(id+"F0.wireOp",EDGE,"E1695"),sQuery(id+"F0.wireOp",EDGE,"E1696"),sQuery(id+"F0.wireOp",EDGE,"E1697"),sQuery(id+"F0.wireOp",EDGE,"E1698"),sQuery(id+"F0.wireOp",EDGE,"E1699"),sQuery(id+"F0.wireOp",EDGE,"E1700"),sQuery(id+"F0.wireOp",EDGE,"E1701"),sQuery(id+"F0.wireOp",EDGE,"E1702"),sQuery(id+"F0.wireOp",EDGE,"E1703"),sQuery(id+"F0.wireOp",EDGE,"E1704"),sQuery(id+"F0.wireOp",EDGE,"E1705"),sQuery(id+"F0.wireOp",EDGE,"E1706"),sQuery(id+"F0.wireOp",EDGE,"E1707"),sQuery(id+"F0.wireOp",EDGE,"E1708"),sQuery(id+"F0.wireOp",EDGE,"E1709"),sQuery(id+"F0.wireOp",EDGE,"E1710"),sQuery(id+"F0.wireOp",EDGE,"E1711"),sQuery(id+"F0.wireOp",EDGE,"E1712"),sQuery(id+"F0.wireOp",EDGE,"E1713"),sQuery(id+"F0.wireOp",EDGE,"E1714"),sQuery(id+"F0.wireOp",EDGE,"E1715"),sQuery(id+"F0.wireOp",EDGE,"E1716"),sQuery(id+"F0.wireOp",EDGE,"E1717"),sQuery(id+"F0.wireOp",EDGE,"E1718"),sQuery(id+"F0.wireOp",EDGE,"E1719"),sQuery(id+"F0.wireOp",EDGE,"E1720"),sQuery(id+"F0.wireOp",EDGE,"E1721"),sQuery(id+"F0.wireOp",EDGE,"E1722"),sQuery(id+"F0.wireOp",EDGE,"E1723"),sQuery(id+"F0.wireOp",EDGE,"E1724"),sQuery(id+"F0.wireOp",EDGE,"E1725"),sQuery(id+"F0.wireOp",EDGE,"E1726"),sQuery(id+"F0.wireOp",EDGE,"E1727"),sQuery(id+"F0.wireOp",EDGE,"E1728"),sQuery(id+"F0.wireOp",EDGE,"E1729"),sQuery(id+"F0.wireOp",EDGE,"E1730"),sQuery(id+"F0.wireOp",EDGE,"E1731"),sQuery(id+"F0.wireOp",EDGE,"E1732"),sQuery(id+"F0.wireOp",EDGE,"E1733"),sQuery(id+"F0.wireOp",EDGE,"E1734"),sQuery(id+"F0.wireOp",EDGE,"E1735"),sQuery(id+"F0.wireOp",EDGE,"E1736"),sQuery(id+"F0.wireOp",EDGE,"E1737"),sQuery(id+"F0.wireOp",EDGE,"E1738"),sQuery(id+"F0.wireOp",EDGE,"E1739"),sQuery(id+"F0.wireOp",EDGE,"E1740"),sQuery(id+"F0.wireOp",EDGE,"E1741"),sQuery(id+"F0.wireOp",EDGE,"E1742"),sQuery(id+"F0.wireOp",EDGE,"E1743"),sQuery(id+"F0.wireOp",EDGE,"E1744"),sQuery(id+"F0.wireOp",EDGE,"E1745"),sQuery(id+"F0.wireOp",EDGE,"E1746"),sQuery(id+"F0.wireOp",EDGE,"E1747"),sQuery(id+"F0.wireOp",EDGE,"E1748"),sQuery(id+"F0.wireOp",EDGE,"E1749"),sQuery(id+"F0.wireOp",EDGE,"E1750"),sQuery(id+"F0.wireOp",EDGE,"E1751"),sQuery(id+"F0.wireOp",EDGE,"E1752"),sQuery(id+"F0.wireOp",EDGE,"E1753"),sQuery(id+"F0.wireOp",EDGE,"E1754"),sQuery(id+"F0.wireOp",EDGE,"E1755"),sQuery(id+"F0.wireOp",EDGE,"E1756"),sQuery(id+"F0.wireOp",EDGE,"E1757"),sQuery(id+"F0.wireOp",EDGE,"E1758"),sQuery(id+"F0.wireOp",EDGE,"E1759"),sQuery(id+"F0.wireOp",EDGE,"E1760"),sQuery(id+"F0.wireOp",EDGE,"E1761"),sQuery(id+"F0.wireOp",EDGE,"E1762"),sQuery(id+"F0.wireOp",EDGE,"E1763"),sQuery(id+"F0.wireOp",EDGE,"E1764"),sQuery(id+"F0.wireOp",EDGE,"E1765"),sQuery(id+"F0.wireOp",EDGE,"E1766"),sQuery(id+"F0.wireOp",EDGE,"E1767"),sQuery(id+"F0.wireOp",EDGE,"E1768"),sQuery(id+"F0.wireOp",EDGE,"E1769"),sQuery(id+"F0.wireOp",EDGE,"E1770"),sQuery(id+"F0.wireOp",EDGE,"E1771"),sQuery(id+"F0.wireOp",EDGE,"E1772"),sQuery(id+"F0.wireOp",EDGE,"E1773"),sQuery(id+"F0.wireOp",EDGE,"E1774"),sQuery(id+"F0.wireOp",EDGE,"E1775"),sQuery(id+"F0.wireOp",EDGE,"E1776"),sQuery(id+"F0.wireOp",EDGE,"E1777"),sQuery(id+"F0.wireOp",EDGE,"E1778"),sQuery(id+"F0.wireOp",EDGE,"E1779"),sQuery(id+"F0.wireOp",EDGE,"E1780"),sQuery(id+"F0.wireOp",EDGE,"E1781"),sQuery(id+"F0.wireOp",EDGE,"E1782"),sQuery(id+"F0.wireOp",EDGE,"E1783"),sQuery(id+"F0.wireOp",EDGE,"E1784"),sQuery(id+"F0.wireOp",EDGE,"E1785"),sQuery(id+"F0.wireOp",EDGE,"E1786"),sQuery(id+"F0.wireOp",EDGE,"E1787"),sQuery(id+"F0.wireOp",EDGE,"E1788"),sQuery(id+"F0.wireOp",EDGE,"E1789"),sQuery(id+"F0.wireOp",EDGE,"E1790"),sQuery(id+"F0.wireOp",EDGE,"E1791"),sQuery(id+"F0.wireOp",EDGE,"E1792"),sQuery(id+"F0.wireOp",EDGE,"E1793"),sQuery(id+"F0.wireOp",EDGE,"E1794"),sQuery(id+"F0.wireOp",EDGE,"E1795"),sQuery(id+"F0.wireOp",EDGE,"E1796"),sQuery(id+"F0.wireOp",EDGE,"E1797"),sQuery(id+"F0.wireOp",EDGE,"E1798"),sQuery(id+"F0.wireOp",EDGE,"E1799"),sQuery(id+"F0.wireOp",EDGE,"E1800"),sQuery(id+"F0.wireOp",EDGE,"E1801"),sQuery(id+"F0.wireOp",EDGE,"E1802"),sQuery(id+"F0.wireOp",EDGE,"E1803"),sQuery(id+"F0.wireOp",EDGE,"E1804"),sQuery(id+"F0.wireOp",EDGE,"E1805"),sQuery(id+"F0.wireOp",EDGE,"E1806"),sQuery(id+"F0.wireOp",EDGE,"E1807"),sQuery(id+"F0.wireOp",EDGE,"E1808"),sQuery(id+"F0.wireOp",EDGE,"E1809"),sQuery(id+"F0.wireOp",EDGE,"E1810"),sQuery(id+"F0.wireOp",EDGE,"E1811"),sQuery(id+"F0.wireOp",EDGE,"E1812"),sQuery(id+"F0.wireOp",EDGE,"E1813"),sQuery(id+"F0.wireOp",EDGE,"E1814"),sQuery(id+"F0.wireOp",EDGE,"E1815"),sQuery(id+"F0.wireOp",EDGE,"E1816"),sQuery(id+"F0.wireOp",EDGE,"E1817"),sQuery(id+"F0.wireOp",EDGE,"E1818"),sQuery(id+"F0.wireOp",EDGE,"E1819"),sQuery(id+"F0.wireOp",EDGE,"E1820"),sQuery(id+"F0.wireOp",EDGE,"E1821"),sQuery(id+"F0.wireOp",EDGE,"E1822"),sQuery(id+"F0.wireOp",EDGE,"E1823"),sQuery(id+"F0.wireOp",EDGE,"E1824"),sQuery(id+"F0.wireOp",EDGE,"E1825"),sQuery(id+"F0.wireOp",EDGE,"E1826"),sQuery(id+"F0.wireOp",EDGE,"E1827"),sQuery(id+"F0.wireOp",EDGE,"E1828"),sQuery(id+"F0.wireOp",EDGE,"E1829"),sQuery(id+"F0.wireOp",EDGE,"E1830"),sQuery(id+"F0.wireOp",EDGE,"E1831"),sQuery(id+"F0.wireOp",EDGE,"E1832"),sQuery(id+"F0.wireOp",EDGE,"E1833"),sQuery(id+"F0.wireOp",EDGE,"E1834"),sQuery(id+"F0.wireOp",EDGE,"E1835"),sQuery(id+"F0.wireOp",EDGE,"E1836"),sQuery(id+"F0.wireOp",EDGE,"E1837"),sQuery(id+"F0.wireOp",EDGE,"E1838"),sQuery(id+"F0.wireOp",EDGE,"E1839"),sQuery(id+"F0.wireOp",EDGE,"E1840"),sQuery(id+"F0.wireOp",EDGE,"E1841"),sQuery(id+"F0.wireOp",EDGE,"E1842"),sQuery(id+"F0.wireOp",EDGE,"E1843"),sQuery(id+"F0.wireOp",EDGE,"E1844"),sQuery(id+"F0.wireOp",EDGE,"E1845"),sQuery(id+"F0.wireOp",EDGE,"E1846"),sQuery(id+"F0.wireOp",EDGE,"E1847"),sQuery(id+"F0.wireOp",EDGE,"E1848"),sQuery(id+"F0.wireOp",EDGE,"E1849"),sQuery(id+"F0.wireOp",EDGE,"E1850"),sQuery(id+"F0.wireOp",EDGE,"E1851"),sQuery(id+"F0.wireOp",EDGE,"E1852"),sQuery(id+"F0.wireOp",EDGE,"E1853"),sQuery(id+"F0.wireOp",EDGE,"E1854"),sQuery(id+"F0.wireOp",EDGE,"E1855"),sQuery(id+"F0.wireOp",EDGE,"E1856"),sQuery(id+"F0.wireOp",EDGE,"E1857"),sQuery(id+"F0.wireOp",EDGE,"E1858"),sQuery(id+"F0.wireOp",EDGE,"E1859"),sQuery(id+"F0.wireOp",EDGE,"E1860"),sQuery(id+"F0.wireOp",EDGE,"E1861"),sQuery(id+"F0.wireOp",EDGE,"E1862"),sQuery(id+"F0.wireOp",EDGE,"E1863"),sQuery(id+"F0.wireOp",EDGE,"E1864"),sQuery(id+"F0.wireOp",EDGE,"E1865"),sQuery(id+"F0.wireOp",EDGE,"E1866"),sQuery(id+"F0.wireOp",EDGE,"E1867"),sQuery(id+"F0.wireOp",EDGE,"E1868"),sQuery(id+"F0.wireOp",EDGE,"E1869"),sQuery(id+"F0.wireOp",EDGE,"E1870"),sQuery(id+"F0.wireOp",EDGE,"E1871"),sQuery(id+"F0.wireOp",EDGE,"E1872"),sQuery(id+"F0.wireOp",EDGE,"E1873"),sQuery(id+"F0.wireOp",EDGE,"E1874"),sQuery(id+"F0.wireOp",EDGE,"E1875"),sQuery(id+"F0.wireOp",EDGE,"E1876"),sQuery(id+"F0.wireOp",EDGE,"E1877"),sQuery(id+"F0.wireOp",EDGE,"E1878"),sQuery(id+"F0.wireOp",EDGE,"E1879"),sQuery(id+"F0.wireOp",EDGE,"E1880"),sQuery(id+"F0.wireOp",EDGE,"E1881"),sQuery(id+"F0.wireOp",EDGE,"E1882"),sQuery(id+"F0.wireOp",EDGE,"E1883"),sQuery(id+"F0.wireOp",EDGE,"E1884"),sQuery(id+"F0.wireOp",EDGE,"E1885"),sQuery(id+"F0.wireOp",EDGE,"E1886"),sQuery(id+"F0.wireOp",EDGE,"E1887"),sQuery(id+"F0.wireOp",EDGE,"E1888"),sQuery(id+"F0.wireOp",EDGE,"E1889"),sQuery(id+"F0.wireOp",EDGE,"E1890"),sQuery(id+"F0.wireOp",EDGE,"E1891"),sQuery(id+"F0.wireOp",EDGE,"E1892"),sQuery(id+"F0.wireOp",EDGE,"E1893"),sQuery(id+"F0.wireOp",EDGE,"E1894"),sQuery(id+"F0.wireOp",EDGE,"E1895"),sQuery(id+"F0.wireOp",EDGE,"E1896"),sQuery(id+"F0.wireOp",EDGE,"E1897"),sQuery(id+"F0.wireOp",EDGE,"E1898"),sQuery(id+"F0.wireOp",EDGE,"E1899"),sQuery(id+"F0.wireOp",EDGE,"E1900"),sQuery(id+"F0.wireOp",EDGE,"E1901"),sQuery(id+"F0.wireOp",EDGE,"E1902"),sQuery(id+"F0.wireOp",EDGE,"E1903"),sQuery(id+"F0.wireOp",EDGE,"E1904"),sQuery(id+"F0.wireOp",EDGE,"E1905"),sQuery(id+"F0.wireOp",EDGE,"E1906"),sQuery(id+"F0.wireOp",EDGE,"E1907"),sQuery(id+"F0.wireOp",EDGE,"E1908"),sQuery(id+"F0.wireOp",EDGE,"E1909"),sQuery(id+"F0.wireOp",EDGE,"E1910"),sQuery(id+"F0.wireOp",EDGE,"E1911"),sQuery(id+"F0.wireOp",EDGE,"E1912"),sQuery(id+"F0.wireOp",EDGE,"E1913"),sQuery(id+"F0.wireOp",EDGE,"E1914"),sQuery(id+"F0.wireOp",EDGE,"E1915"),sQuery(id+"F0.wireOp",EDGE,"E1916"),sQuery(id+"F0.wireOp",EDGE,"E1917"),sQuery(id+"F0.wireOp",EDGE,"E1918"),sQuery(id+"F0.wireOp",EDGE,"E1919"),sQuery(id+"F0.wireOp",EDGE,"E1920"),sQuery(id+"F0.wireOp",EDGE,"E1921"),sQuery(id+"F0.wireOp",EDGE,"E1922"),sQuery(id+"F0.wireOp",EDGE,"E1923"),sQuery(id+"F0.wireOp",EDGE,"E1924"),sQuery(id+"F0.wireOp",EDGE,"E1925"),sQuery(id+"F0.wireOp",EDGE,"E1926"),sQuery(id+"F0.wireOp",EDGE,"E1927"),sQuery(id+"F0.wireOp",EDGE,"E1928"),sQuery(id+"F0.wireOp",EDGE,"E1929"),sQuery(id+"F0.wireOp",EDGE,"E1930"),sQuery(id+"F0.wireOp",EDGE,"E1931"),sQuery(id+"F0.wireOp",EDGE,"E1932"),sQuery(id+"F0.wireOp",EDGE,"E1933"),sQuery(id+"F0.wireOp",EDGE,"E1934"),sQuery(id+"F0.wireOp",EDGE,"E1935"),sQuery(id+"F0.wireOp",EDGE,"E1936"),sQuery(id+"F0.wireOp",EDGE,"E1937"),sQuery(id+"F0.wireOp",EDGE,"E1938"),sQuery(id+"F0.wireOp",EDGE,"E1939"),sQuery(id+"F0.wireOp",EDGE,"E1940"),sQuery(id+"F0.wireOp",EDGE,"E1941"),sQuery(id+"F0.wireOp",EDGE,"E1942"),sQuery(id+"F0.wireOp",EDGE,"E1943"),sQuery(id+"F0.wireOp",EDGE,"E1944"),sQuery(id+"F0.wireOp",EDGE,"E1945"),sQuery(id+"F0.wireOp",EDGE,"E1946"),sQuery(id+"F0.wireOp",EDGE,"E1947"),sQuery(id+"F0.wireOp",EDGE,"E1948"),sQuery(id+"F0.wireOp",EDGE,"E1949"),sQuery(id+"F0.wireOp",EDGE,"E1950"),sQuery(id+"F0.wireOp",EDGE,"E1951"),sQuery(id+"F0.wireOp",EDGE,"E1952"),sQuery(id+"F0.wireOp",EDGE,"E1953"),sQuery(id+"F0.wireOp",EDGE,"E1954"),sQuery(id+"F0.wireOp",EDGE,"E1955"),sQuery(id+"F0.wireOp",EDGE,"E1956"),sQuery(id+"F0.wireOp",EDGE,"E1957"),sQuery(id+"F0.wireOp",EDGE,"E1958"),sQuery(id+"F0.wireOp",EDGE,"E1959"),sQuery(id+"F0.wireOp",EDGE,"E1960"),sQuery(id+"F0.wireOp",EDGE,"E1961"),sQuery(id+"F0.wireOp",EDGE,"E1962"),sQuery(id+"F0.wireOp",EDGE,"E1963"),sQuery(id+"F0.wireOp",EDGE,"E1964"),sQuery(id+"F0.wireOp",EDGE,"E1965"),sQuery(id+"F0.wireOp",EDGE,"E1966"),sQuery(id+"F0.wireOp",EDGE,"E1967"),sQuery(id+"F0.wireOp",EDGE,"E1968"),sQuery(id+"F0.wireOp",EDGE,"E1969"),sQuery(id+"F0.wireOp",EDGE,"E1970"),sQuery(id+"F0.wireOp",EDGE,"E1971"),sQuery(id+"F0.wireOp",EDGE,"E1972"),sQuery(id+"F0.wireOp",EDGE,"E1973"),sQuery(id+"F0.wireOp",EDGE,"E1974"),sQuery(id+"F0.wireOp",EDGE,"E1975"),sQuery(id+"F0.wireOp",EDGE,"E1976"),sQuery(id+"F0.wireOp",EDGE,"E1977"),sQuery(id+"F0.wireOp",EDGE,"E1978"),sQuery(id+"F0.wireOp",EDGE,"E1979"),sQuery(id+"F0.wireOp",EDGE,"E1980"),sQuery(id+"F0.wireOp",EDGE,"E1981"),sQuery(id+"F0.wireOp",EDGE,"E1982"),sQuery(id+"F0.wireOp",EDGE,"E1983"),sQuery(id+"F0.wireOp",EDGE,"E1984"),sQuery(id+"F0.wireOp",EDGE,"E1985"),sQuery(id+"F0.wireOp",EDGE,"E1986"),sQuery(id+"F0.wireOp",EDGE,"E1987"),sQuery(id+"F0.wireOp",EDGE,"E1988"),sQuery(id+"F0.wireOp",EDGE,"E1989"),sQuery(id+"F0.wireOp",EDGE,"E1990"),sQuery(id+"F0.wireOp",EDGE,"E1991"),sQuery(id+"F0.wireOp",EDGE,"E1992"),sQuery(id+"F0.wireOp",EDGE,"E1993"),sQuery(id+"F0.wireOp",EDGE,"E1994"),sQuery(id+"F0.wireOp",EDGE,"E1995"),sQuery(id+"F0.wireOp",EDGE,"E1996"),sQuery(id+"F0.wireOp",EDGE,"E1997"),sQuery(id+"F0.wireOp",EDGE,"E1998"),sQuery(id+"F0.wireOp",EDGE,"E1999"),sQuery(id+"F0.wireOp",EDGE,"E2000"),sQuery(id+"F0.wireOp",EDGE,"E2001"),sQuery(id+"F0.wireOp",EDGE,"E2002"),sQuery(id+"F0.wireOp",EDGE,"E2003"),sQuery(id+"F0.wireOp",EDGE,"E2004"),sQuery(id+"F0.wireOp",EDGE,"E2005"),sQuery(id+"F0.wireOp",EDGE,"E2006"),sQuery(id+"F0.wireOp",EDGE,"E2007"),sQuery(id+"F0.wireOp",EDGE,"E2008"),sQuery(id+"F0.wireOp",EDGE,"E2009"),sQuery(id+"F0.wireOp",EDGE,"E2010"),sQuery(id+"F0.wireOp",EDGE,"E2011"),sQuery(id+"F0.wireOp",EDGE,"E2012"),sQuery(id+"F0.wireOp",EDGE,"E2013"),sQuery(id+"F0.wireOp",EDGE,"E2014"),sQuery(id+"F0.wireOp",EDGE,"E2015"),sQuery(id+"F0.wireOp",EDGE,"E2016"),sQuery(id+"F0.wireOp",EDGE,"E2017"),sQuery(id+"F0.wireOp",EDGE,"E2018"),sQuery(id+"F0.wireOp",EDGE,"E2019"),sQuery(id+"F0.wireOp",EDGE,"E2020"),sQuery(id+"F0.wireOp",EDGE,"E2021"),sQuery(id+"F0.wireOp",EDGE,"E2022"),sQuery(id+"F0.wireOp",EDGE,"E2023"),sQuery(id+"F0.wireOp",EDGE,"E2024"),sQuery(id+"F0.wireOp",EDGE,"E2025"),sQuery(id+"F0.wireOp",EDGE,"E2026"),sQuery(id+"F0.wireOp",EDGE,"E2027"),sQuery(id+"F0.wireOp",EDGE,"E2028"),sQuery(id+"F0.wireOp",EDGE,"E2029"),sQuery(id+"F0.wireOp",EDGE,"E2030"),sQuery(id+"F0.wireOp",EDGE,"E2031"),sQuery(id+"F0.wireOp",EDGE,"E2032"),sQuery(id+"F0.wireOp",EDGE,"E2033"),sQuery(id+"F0.wireOp",EDGE,"E2034"),sQuery(id+"F0.wireOp",EDGE,"E2035"),sQuery(id+"F0.wireOp",EDGE,"E2036"),sQuery(id+"F0.wireOp",EDGE,"E2037"),sQuery(id+"F0.wireOp",EDGE,"E2038"),sQuery(id+"F0.wireOp",EDGE,"E2039"),sQuery(id+"F0.wireOp",EDGE,"E2040"),sQuery(id+"F0.wireOp",EDGE,"E2041"),sQuery(id+"F0.wireOp",EDGE,"E2042"),sQuery(id+"F0.wireOp",EDGE,"E2043"),sQuery(id+"F0.wireOp",EDGE,"E2044"),sQuery(id+"F0.wireOp",EDGE,"E2045"),sQuery(id+"F0.wireOp",EDGE,"E2046"),sQuery(id+"F0.wireOp",EDGE,"E2047"),sQuery(id+"F0.wireOp",EDGE,"E2048"),sQuery(id+"F0.wireOp",EDGE,"E2049"),sQuery(id+"F0.wireOp",EDGE,"E2050"),sQuery(id+"F0.wireOp",EDGE,"E2051"),sQuery(id+"F0.wireOp",EDGE,"E2052"),sQuery(id+"F0.wireOp",EDGE,"E2053"),sQuery(id+"F0.wireOp",EDGE,"E2054"),sQuery(id+"F0.wireOp",EDGE,"E2055"),sQuery(id+"F0.wireOp",EDGE,"E2056"),sQuery(id+"F0.wireOp",EDGE,"E2057"),sQuery(id+"F0.wireOp",EDGE,"E2058"),sQuery(id+"F0.wireOp",EDGE,"E2059"),sQuery(id+"F0.wireOp",EDGE,"E2060"),sQuery(id+"F0.wireOp",EDGE,"E2061"),sQuery(id+"F0.wireOp",EDGE,"E2062"),sQuery(id+"F0.wireOp",EDGE,"E2063"),sQuery(id+"F0.wireOp",EDGE,"E2064"),sQuery(id+"F0.wireOp",EDGE,"E2065"),sQuery(id+"F0.wireOp",EDGE,"E2066"),sQuery(id+"F0.wireOp",EDGE,"E2067"),sQuery(id+"F0.wireOp",EDGE,"E2068"),sQuery(id+"F0.wireOp",EDGE,"E2069"),sQuery(id+"F0.wireOp",EDGE,"E2070"),sQuery(id+"F0.wireOp",EDGE,"E2071"),sQuery(id+"F0.wireOp",EDGE,"E2072"),sQuery(id+"F0.wireOp",EDGE,"E2073"),sQuery(id+"F0.wireOp",EDGE,"E2074"),sQuery(id+"F0.wireOp",EDGE,"E2075"),sQuery(id+"F0.wireOp",EDGE,"E2076"),sQuery(id+"F0.wireOp",EDGE,"E2077"),sQuery(id+"F0.wireOp",EDGE,"E2078"),sQuery(id+"F0.wireOp",EDGE,"E2079"),sQuery(id+"F0.wireOp",EDGE,"E2080"),sQuery(id+"F0.wireOp",EDGE,"E2081"),sQuery(id+"F0.wireOp",EDGE,"E2082"),sQuery(id+"F0.wireOp",EDGE,"E2083"),sQuery(id+"F0.wireOp",EDGE,"E2084"),sQuery(id+"F0.wireOp",EDGE,"E2085"),sQuery(id+"F0.wireOp",EDGE,"E2086"),sQuery(id+"F0.wireOp",EDGE,"E2087"),sQuery(id+"F0.wireOp",EDGE,"E2088"),sQuery(id+"F0.wireOp",EDGE,"E2089"),sQuery(id+"F0.wireOp",EDGE,"E2090"),sQuery(id+"F0.wireOp",EDGE,"E2091"),sQuery(id+"F0.wireOp",EDGE,"E2092"),sQuery(id+"F0.wireOp",EDGE,"E2093"),sQuery(id+"F0.wireOp",EDGE,"E2094"),sQuery(id+"F0.wireOp",EDGE,"E2095"),sQuery(id+"F0.wireOp",EDGE,"E2096"),sQuery(id+"F0.wireOp",EDGE,"E2097"),sQuery(id+"F0.wireOp",EDGE,"E2098"),sQuery(id+"F0.wireOp",EDGE,"E2099"),sQuery(id+"F0.wireOp",EDGE,"E2100"),sQuery(id+"F0.wireOp",EDGE,"E2101"),sQuery(id+"F0.wireOp",EDGE,"E2102"),sQuery(id+"F0.wireOp",EDGE,"E2103"),sQuery(id+"F0.wireOp",EDGE,"E2104"),sQuery(id+"F0.wireOp",EDGE,"E2105"),sQuery(id+"F0.wireOp",EDGE,"E2106"),sQuery(id+"F0.wireOp",EDGE,"E2107"),sQuery(id+"F0.wireOp",EDGE,"E2108"),sQuery(id+"F0.wireOp",EDGE,"E2109"),sQuery(id+"F0.wireOp",EDGE,"E2110"),sQuery(id+"F0.wireOp",EDGE,"E2111"),sQuery(id+"F0.wireOp",EDGE,"E2112"),sQuery(id+"F0.wireOp",EDGE,"E2113"),sQuery(id+"F0.wireOp",EDGE,"E2114"),sQuery(id+"F0.wireOp",EDGE,"E2115"),sQuery(id+"F0.wireOp",EDGE,"E2116"),sQuery(id+"F0.wireOp",EDGE,"E2117"),sQuery(id+"F0.wireOp",EDGE,"E2118"),sQuery(id+"F0.wireOp",EDGE,"E2119"),sQuery(id+"F0.wireOp",EDGE,"E2120"),sQuery(id+"F0.wireOp",EDGE,"E2121"),sQuery(id+"F0.wireOp",EDGE,"E2122"),sQuery(id+"F0.wireOp",EDGE,"E2123"),sQuery(id+"F0.wireOp",EDGE,"E2124"),sQuery(id+"F0.wireOp",EDGE,"E2125"),sQuery(id+"F0.wireOp",EDGE,"E2126"),sQuery(id+"F0.wireOp",EDGE,"E2127"),sQuery(id+"F0.wireOp",EDGE,"E2128"),sQuery(id+"F0.wireOp",EDGE,"E2129"),sQuery(id+"F0.wireOp",EDGE,"E2130"),sQuery(id+"F0.wireOp",EDGE,"E2131"),sQuery(id+"F0.wireOp",EDGE,"E2132"),sQuery(id+"F0.wireOp",EDGE,"E2133"),sQuery(id+"F0.wireOp",EDGE,"E2134"),sQuery(id+"F0.wireOp",EDGE,"E2135"),sQuery(id+"F0.wireOp",EDGE,"E2136"),sQuery(id+"F0.wireOp",EDGE,"E2137"),sQuery(id+"F0.wireOp",EDGE,"E2138"),sQuery(id+"F0.wireOp",EDGE,"E2139"),sQuery(id+"F0.wireOp",EDGE,"E2140"),sQuery(id+"F0.wireOp",EDGE,"E2141"),sQuery(id+"F0.wireOp",EDGE,"E2142"),sQuery(id+"F0.wireOp",EDGE,"E2143"),sQuery(id+"F0.wireOp",EDGE,"E2144"),sQuery(id+"F0.wireOp",EDGE,"E2145"),sQuery(id+"F0.wireOp",EDGE,"E2146"),sQuery(id+"F0.wireOp",EDGE,"E2147"),sQuery(id+"F0.wireOp",EDGE,"E2148"),sQuery(id+"F0.wireOp",EDGE,"E2149"),sQuery(id+"F0.wireOp",EDGE,"E2150"),sQuery(id+"F0.wireOp",EDGE,"E2151"),sQuery(id+"F0.wireOp",EDGE,"E2152"),sQuery(id+"F0.wireOp",EDGE,"E2153"),sQuery(id+"F0.wireOp",EDGE,"E2154"),sQuery(id+"F0.wireOp",EDGE,"E2155"),sQuery(id+"F0.wireOp",EDGE,"E2156"),sQuery(id+"F0.wireOp",EDGE,"E2157"),sQuery(id+"F0.wireOp",EDGE,"E2158"),sQuery(id+"F0.wireOp",EDGE,"E2159"),sQuery(id+"F0.wireOp",EDGE,"E2160"),sQuery(id+"F0.wireOp",EDGE,"E2161"),sQuery(id+"F0.wireOp",EDGE,"E2162"),sQuery(id+"F0.wireOp",EDGE,"E2163"),sQuery(id+"F0.wireOp",EDGE,"E2164"),sQuery(id+"F0.wireOp",EDGE,"E2165"),sQuery(id+"F0.wireOp",EDGE,"E2166"),sQuery(id+"F0.wireOp",EDGE,"E2167"),sQuery(id+"F0.wireOp",EDGE,"E2168"),sQuery(id+"F0.wireOp",EDGE,"E2169"),sQuery(id+"F0.wireOp",EDGE,"E2170"),sQuery(id+"F0.wireOp",EDGE,"E2171"),sQuery(id+"F0.wireOp",EDGE,"E2172"),sQuery(id+"F0.wireOp",EDGE,"E2173"),sQuery(id+"F0.wireOp",EDGE,"E2174"),sQuery(id+"F0.wireOp",EDGE,"E2175"),sQuery(id+"F0.wireOp",EDGE,"E2176"),sQuery(id+"F0.wireOp",EDGE,"E2177"),sQuery(id+"F0.wireOp",EDGE,"E2178"),sQuery(id+"F0.wireOp",EDGE,"E2179"),sQuery(id+"F0.wireOp",EDGE,"E2180"),sQuery(id+"F0.wireOp",EDGE,"E2181"),sQuery(id+"F0.wireOp",EDGE,"E2182"),sQuery(id+"F0.wireOp",EDGE,"E2183"),sQuery(id+"F0.wireOp",EDGE,"E2184"),sQuery(id+"F0.wireOp",EDGE,"E2185"),sQuery(id+"F0.wireOp",EDGE,"E2186"),sQuery(id+"F0.wireOp",EDGE,"E2187"),sQuery(id+"F0.wireOp",EDGE,"E2188"),sQuery(id+"F0.wireOp",EDGE,"E2189"),sQuery(id+"F0.wireOp",EDGE,"E2190"),sQuery(id+"F0.wireOp",EDGE,"E2191"),sQuery(id+"F0.wireOp",EDGE,"E2192"),sQuery(id+"F0.wireOp",EDGE,"E2193"),sQuery(id+"F0.wireOp",EDGE,"E2194"),sQuery(id+"F0.wireOp",EDGE,"E2195"),sQuery(id+"F0.wireOp",EDGE,"E2196"),sQuery(id+"F0.wireOp",EDGE,"E2197"),sQuery(id+"F0.wireOp",EDGE,"E2198"),sQuery(id+"F0.wireOp",EDGE,"E2199"),sQuery(id+"F0.wireOp",EDGE,"E2200"),sQuery(id+"F0.wireOp",EDGE,"E2201"),sQuery(id+"F0.wireOp",EDGE,"E2202"),sQuery(id+"F0.wireOp",EDGE,"E2203"),sQuery(id+"F0.wireOp",EDGE,"E2204"),sQuery(id+"F0.wireOp",EDGE,"E2205"),sQuery(id+"F0.wireOp",EDGE,"E2206"),sQuery(id+"F0.wireOp",EDGE,"E2207"),sQuery(id+"F0.wireOp",EDGE,"E2208"),sQuery(id+"F0.wireOp",EDGE,"E2209"),sQuery(id+"F0.wireOp",EDGE,"E2210"),sQuery(id+"F0.wireOp",EDGE,"E2211"),sQuery(id+"F0.wireOp",EDGE,"E2212"),sQuery(id+"F0.wireOp",EDGE,"E2213"),sQuery(id+"F0.wireOp",EDGE,"E2214"),sQuery(id+"F0.wireOp",EDGE,"E2215"),sQuery(id+"F0.wireOp",EDGE,"E2216"),sQuery(id+"F0.wireOp",EDGE,"E2217"),sQuery(id+"F0.wireOp",EDGE,"E2218"),sQuery(id+"F0.wireOp",EDGE,"E2219"),sQuery(id+"F0.wireOp",EDGE,"E2220"),sQuery(id+"F0.wireOp",EDGE,"E2221"),sQuery(id+"F0.wireOp",EDGE,"E2222"),sQuery(id+"F0.wireOp",EDGE,"E2223"),sQuery(id+"F0.wireOp",EDGE,"E2224"),sQuery(id+"F0.wireOp",EDGE,"E2225"),sQuery(id+"F0.wireOp",EDGE,"E2226"),sQuery(id+"F0.wireOp",EDGE,"E2227"),sQuery(id+"F0.wireOp",EDGE,"E2228"),sQuery(id+"F0.wireOp",EDGE,"E2229"),sQuery(id+"F0.wireOp",EDGE,"E2230"),sQuery(id+"F0.wireOp",EDGE,"E2231"),sQuery(id+"F0.wireOp",EDGE,"E2232"),sQuery(id+"F0.wireOp",EDGE,"E2233"),sQuery(id+"F0.wireOp",EDGE,"E2234"),sQuery(id+"F0.wireOp",EDGE,"E2235"),sQuery(id+"F0.wireOp",EDGE,"E2236"),sQuery(id+"F0.wireOp",EDGE,"E2237"),sQuery(id+"F0.wireOp",EDGE,"E2238"),sQuery(id+"F0.wireOp",EDGE,"E2239"),sQuery(id+"F0.wireOp",EDGE,"E2240"),sQuery(id+"F0.wireOp",EDGE,"E2241"),sQuery(id+"F0.wireOp",EDGE,"E2242"),sQuery(id+"F0.wireOp",EDGE,"E2243"),sQuery(id+"F0.wireOp",EDGE,"E2244"),sQuery(id+"F0.wireOp",EDGE,"E2245"),sQuery(id+"F0.wireOp",EDGE,"E2246"),sQuery(id+"F0.wireOp",EDGE,"E2247"),sQuery(id+"F0.wireOp",EDGE,"E2248"),sQuery(id+"F0.wireOp",EDGE,"E2249"),sQuery(id+"F0.wireOp",EDGE,"E2250"),sQuery(id+"F0.wireOp",EDGE,"E2251"),sQuery(id+"F0.wireOp",EDGE,"E2252"),sQuery(id+"F0.wireOp",EDGE,"E2253"),sQuery(id+"F0.wireOp",EDGE,"E2254"),sQuery(id+"F0.wireOp",EDGE,"E2255"),sQuery(id+"F0.wireOp",EDGE,"E2256"),sQuery(id+"F0.wireOp",EDGE,"E2257"),sQuery(id+"F0.wireOp",EDGE,"E2258"),sQuery(id+"F0.wireOp",EDGE,"E2259")])],"isStart":false});
            var sketch = newSketch(context, id + "F2", { "sketchPlane" : qUnion([Q0])});
            skLineSegment(sketch, "E4644", {"start": v(391.25, -176.92) * mm, "end": v(392.49, -176.69) * mm});
            skLineSegment(sketch, "E4645", {"start": v(392.49, -176.69) * mm, "end": v(393.68, -176.3) * mm});
            skLineSegment(sketch, "E4646", {"start": v(393.68, -176.3) * mm, "end": v(394.82, -175.76) * mm});
            skLineSegment(sketch, "E4647", {"start": v(394.82, -175.76) * mm, "end": v(395.88, -175.1) * mm});
            skLineSegment(sketch, "E4648", {"start": v(395.88, -175.1) * mm, "end": v(396.85, -174.29) * mm});
            skLineSegment(sketch, "E4649", {"start": v(396.85, -174.29) * mm, "end": v(397.7, -173.37) * mm});
            skLineSegment(sketch, "E4650", {"start": v(397.7, -173.37) * mm, "end": v(398.44, -172.36) * mm});
            skLineSegment(sketch, "E4651", {"start": v(398.44, -172.36) * mm, "end": v(399.05, -171.26) * mm});
            skLineSegment(sketch, "E4652", {"start": v(399.05, -171.26) * mm, "end": v(399.51, -170.1) * mm});
            skLineSegment(sketch, "E4653", {"start": v(399.51, -170.1) * mm, "end": v(399.82, -168.87) * mm});
            skLineSegment(sketch, "E4654", {"start": v(399.82, -168.87) * mm, "end": v(399.98, -167.63) * mm});
            skLineSegment(sketch, "E4655", {"start": v(399.98, -167.63) * mm, "end": v(399.98, -167) * mm});
            skLineSegment(sketch, "E4656", {"start": v(399.98, -167) * mm, "end": v(400, -167) * mm});
            skLineSegment(sketch, "E4657", {"start": v(400, -167) * mm, "end": v(400, 109) * mm});
            skLineSegment(sketch, "E4658", {"start": v(400, 109) * mm, "end": v(360, 109) * mm});
            skLineSegment(sketch, "E4659", {"start": v(360, 109) * mm, "end": v(360, 125) * mm});
            skLineSegment(sketch, "E4660", {"start": v(360, 125) * mm, "end": v(400, 125) * mm});
            skLineSegment(sketch, "E4661", {"start": v(400, 125) * mm, "end": v(400, 253) * mm});
            skLineSegment(sketch, "E4662", {"start": v(400, 253) * mm, "end": v(399.92, 254.25) * mm});
            skLineSegment(sketch, "E4663", {"start": v(399.92, 254.25) * mm, "end": v(399.69, 255.49) * mm});
            skLineSegment(sketch, "E4664", {"start": v(399.69, 255.49) * mm, "end": v(399.3, 256.68) * mm});
            skLineSegment(sketch, "E4665", {"start": v(399.3, 256.68) * mm, "end": v(398.76, 257.82) * mm});
            skLineSegment(sketch, "E4666", {"start": v(398.76, 257.82) * mm, "end": v(398.09, 258.88) * mm});
            skLineSegment(sketch, "E4667", {"start": v(398.09, 258.88) * mm, "end": v(397.3, 259.85) * mm});
            skLineSegment(sketch, "E4668", {"start": v(397.3, 259.85) * mm, "end": v(396.37, 260.7) * mm});
            skLineSegment(sketch, "E4669", {"start": v(396.37, 260.7) * mm, "end": v(395.36, 261.44) * mm});
            skLineSegment(sketch, "E4670", {"start": v(395.36, 261.44) * mm, "end": v(394.26, 262.05) * mm});
            skLineSegment(sketch, "E4671", {"start": v(394.26, 262.05) * mm, "end": v(393.09, 262.51) * mm});
            skLineSegment(sketch, "E4672", {"start": v(393.09, 262.51) * mm, "end": v(391.87, 262.82) * mm});
            skLineSegment(sketch, "E4673", {"start": v(391.87, 262.82) * mm, "end": v(390.63, 262.98) * mm});
            skLineSegment(sketch, "E4674", {"start": v(390.63, 262.98) * mm, "end": v(390, 262.98) * mm});
            skLineSegment(sketch, "E4675", {"start": v(390, 262.98) * mm, "end": v(390, 263) * mm});
            skLineSegment(sketch, "E4676", {"start": v(390, 263) * mm, "end": v(20, 263) * mm});
            skLineSegment(sketch, "E4677", {"start": v(20, 263) * mm, "end": v(18.75, 262.92) * mm});
            skLineSegment(sketch, "E4678", {"start": v(18.75, 262.92) * mm, "end": v(17.51, 262.69) * mm});
            skLineSegment(sketch, "E4679", {"start": v(17.51, 262.69) * mm, "end": v(16.32, 262.3) * mm});
            skLineSegment(sketch, "E4680", {"start": v(16.32, 262.3) * mm, "end": v(15.18, 261.76) * mm});
            skLineSegment(sketch, "E4681", {"start": v(15.18, 261.76) * mm, "end": v(14.12, 261.09) * mm});
            skLineSegment(sketch, "E4682", {"start": v(14.12, 261.09) * mm, "end": v(13.15, 260.3) * mm});
            skLineSegment(sketch, "E4683", {"start": v(13.15, 260.3) * mm, "end": v(12.3, 259.37) * mm});
            skLineSegment(sketch, "E4684", {"start": v(12.3, 259.37) * mm, "end": v(11.56, 258.36) * mm});
            skLineSegment(sketch, "E4685", {"start": v(11.56, 258.36) * mm, "end": v(10.95, 257.26) * mm});
            skLineSegment(sketch, "E4686", {"start": v(10.95, 257.26) * mm, "end": v(10.49, 256.09) * mm});
            skLineSegment(sketch, "E4687", {"start": v(10.49, 256.09) * mm, "end": v(10.18, 254.87) * mm});
            skLineSegment(sketch, "E4688", {"start": v(10.18, 254.87) * mm, "end": v(10.02, 253.63) * mm});
            skLineSegment(sketch, "E4689", {"start": v(10.02, 253.63) * mm, "end": v(10.02, 253) * mm});
            skLineSegment(sketch, "E4690", {"start": v(10.02, 253) * mm, "end": v(10, 253) * mm});
            skLineSegment(sketch, "E4691", {"start": v(10, 253) * mm, "end": v(10, 125) * mm});
            skLineSegment(sketch, "E4692", {"start": v(10, 125) * mm, "end": v(50, 125) * mm});
            skLineSegment(sketch, "E4693", {"start": v(50, 125) * mm, "end": v(50, 109) * mm});
            skLineSegment(sketch, "E4694", {"start": v(50, 109) * mm, "end": v(10, 109) * mm});
            skLineSegment(sketch, "E4695", {"start": v(10, 109) * mm, "end": v(10, -167) * mm});
            skLineSegment(sketch, "E4696", {"start": v(10, -167) * mm, "end": v(10.08, -168.25) * mm});
            skLineSegment(sketch, "E4697", {"start": v(10.08, -168.25) * mm, "end": v(10.31, -169.49) * mm});
            skLineSegment(sketch, "E4698", {"start": v(10.31, -169.49) * mm, "end": v(10.7, -170.68) * mm});
            skLineSegment(sketch, "E4699", {"start": v(10.7, -170.68) * mm, "end": v(11.24, -171.82) * mm});
            skLineSegment(sketch, "E4700", {"start": v(11.24, -171.82) * mm, "end": v(11.9, -172.88) * mm});
            skLineSegment(sketch, "E4701", {"start": v(11.9, -172.88) * mm, "end": v(12.71, -173.85) * mm});
            skLineSegment(sketch, "E4702", {"start": v(12.71, -173.85) * mm, "end": v(13.63, -174.7) * mm});
            skLineSegment(sketch, "E4703", {"start": v(13.63, -174.7) * mm, "end": v(14.64, -175.44) * mm});
            skLineSegment(sketch, "E4704", {"start": v(14.64, -175.44) * mm, "end": v(15.74, -176.05) * mm});
            skLineSegment(sketch, "E4705", {"start": v(15.74, -176.05) * mm, "end": v(16.9, -176.51) * mm});
            skLineSegment(sketch, "E4706", {"start": v(16.9, -176.51) * mm, "end": v(18.13, -176.82) * mm});
            skLineSegment(sketch, "E4707", {"start": v(18.13, -176.82) * mm, "end": v(19.37, -176.98) * mm});
            skLineSegment(sketch, "E4708", {"start": v(19.37, -176.98) * mm, "end": v(20, -176.98) * mm});
            skLineSegment(sketch, "E4709", {"start": v(20, -176.98) * mm, "end": v(20, -177) * mm});
            skLineSegment(sketch, "E4710", {"start": v(20, -177) * mm, "end": v(390, -177) * mm});
            skLineSegment(sketch, "E4711", {"start": v(390, -177) * mm, "end": v(391.25, -176.92) * mm});
            skLineSegment(sketch, "E4712", {"start": v(50, 236.5) * mm, "end": v(50, 252.5) * mm});
            skLineSegment(sketch, "E4713", {"start": v(50, 252.5) * mm, "end": v(70, 252.5) * mm});
            skLineSegment(sketch, "E4714", {"start": v(70, 252.5) * mm, "end": v(70, 236.5) * mm});
            skLineSegment(sketch, "E4715", {"start": v(70, 236.5) * mm, "end": v(50, 236.5) * mm});
            skLineSegment(sketch, "E4716", {"start": v(195, 236.5) * mm, "end": v(195, 252.5) * mm});
            skLineSegment(sketch, "E4717", {"start": v(195, 252.5) * mm, "end": v(215, 252.5) * mm});
            skLineSegment(sketch, "E4718", {"start": v(215, 252.5) * mm, "end": v(215, 236.5) * mm});
            skLineSegment(sketch, "E4719", {"start": v(215, 236.5) * mm, "end": v(195, 236.5) * mm});
            skLineSegment(sketch, "E4720", {"start": v(340, 236.5) * mm, "end": v(340, 252.5) * mm});
            skLineSegment(sketch, "E4721", {"start": v(340, 252.5) * mm, "end": v(360, 252.5) * mm});
            skLineSegment(sketch, "E4722", {"start": v(360, 252.5) * mm, "end": v(360, 236.5) * mm});
            skLineSegment(sketch, "E4723", {"start": v(360, 236.5) * mm, "end": v(340, 236.5) * mm});
            skLineSegment(sketch, "E4724", {"start": v(122.37, 242.5) * mm, "end": v(122.12, 242.53) * mm});
            skLineSegment(sketch, "E4725", {"start": v(122.12, 242.53) * mm, "end": v(121.88, 242.6) * mm});
            skLineSegment(sketch, "E4726", {"start": v(121.88, 242.6) * mm, "end": v(121.65, 242.7) * mm});
            skLineSegment(sketch, "E4727", {"start": v(121.65, 242.7) * mm, "end": v(121.43, 242.81) * mm});
            skLineSegment(sketch, "E4728", {"start": v(121.43, 242.81) * mm, "end": v(121.22, 242.96) * mm});
            skLineSegment(sketch, "E4729", {"start": v(121.22, 242.96) * mm, "end": v(121.04, 243.13) * mm});
            skLineSegment(sketch, "E4730", {"start": v(121.04, 243.13) * mm, "end": v(120.88, 243.32) * mm});
            skLineSegment(sketch, "E4731", {"start": v(120.88, 243.32) * mm, "end": v(120.75, 243.54) * mm});
            skLineSegment(sketch, "E4732", {"start": v(120.75, 243.54) * mm, "end": v(120.64, 243.76) * mm});
            skLineSegment(sketch, "E4733", {"start": v(120.64, 243.76) * mm, "end": v(120.56, 244) * mm});
            skLineSegment(sketch, "E4734", {"start": v(120.56, 244) * mm, "end": v(120.52, 244.25) * mm});
            skLineSegment(sketch, "E4735", {"start": v(120.52, 244.25) * mm, "end": v(120.5, 244.5) * mm});
            skLineSegment(sketch, "E4736", {"start": v(120.5, 244.5) * mm, "end": v(120.52, 244.75) * mm});
            skLineSegment(sketch, "E4737", {"start": v(120.52, 244.75) * mm, "end": v(120.56, 245) * mm});
            skLineSegment(sketch, "E4738", {"start": v(120.56, 245) * mm, "end": v(120.64, 245.24) * mm});
            skLineSegment(sketch, "E4739", {"start": v(120.64, 245.24) * mm, "end": v(120.75, 245.46) * mm});
            skLineSegment(sketch, "E4740", {"start": v(120.75, 245.46) * mm, "end": v(120.88, 245.68) * mm});
            skLineSegment(sketch, "E4741", {"start": v(120.88, 245.68) * mm, "end": v(121.04, 245.87) * mm});
            skLineSegment(sketch, "E4742", {"start": v(121.04, 245.87) * mm, "end": v(121.22, 246.04) * mm});
            skLineSegment(sketch, "E4743", {"start": v(121.22, 246.04) * mm, "end": v(121.43, 246.19) * mm});
            skLineSegment(sketch, "E4744", {"start": v(121.43, 246.19) * mm, "end": v(121.65, 246.3) * mm});
            skLineSegment(sketch, "E4745", {"start": v(121.65, 246.3) * mm, "end": v(121.88, 246.4) * mm});
            skLineSegment(sketch, "E4746", {"start": v(121.88, 246.4) * mm, "end": v(122.12, 246.47) * mm});
            skLineSegment(sketch, "E4747", {"start": v(122.12, 246.47) * mm, "end": v(122.37, 246.5) * mm});
            skLineSegment(sketch, "E4748", {"start": v(122.37, 246.5) * mm, "end": v(122.63, 246.5) * mm});
            skLineSegment(sketch, "E4749", {"start": v(122.63, 246.5) * mm, "end": v(122.88, 246.47) * mm});
            skLineSegment(sketch, "E4750", {"start": v(122.88, 246.47) * mm, "end": v(123.12, 246.4) * mm});
            skLineSegment(sketch, "E4751", {"start": v(123.12, 246.4) * mm, "end": v(123.35, 246.3) * mm});
            skLineSegment(sketch, "E4752", {"start": v(123.35, 246.3) * mm, "end": v(123.57, 246.19) * mm});
            skLineSegment(sketch, "E4753", {"start": v(123.57, 246.19) * mm, "end": v(123.78, 246.04) * mm});
            skLineSegment(sketch, "E4754", {"start": v(123.78, 246.04) * mm, "end": v(123.96, 245.87) * mm});
            skLineSegment(sketch, "E4755", {"start": v(123.96, 245.87) * mm, "end": v(124.12, 245.68) * mm});
            skLineSegment(sketch, "E4756", {"start": v(124.12, 245.68) * mm, "end": v(124.25, 245.46) * mm});
            skLineSegment(sketch, "E4757", {"start": v(124.25, 245.46) * mm, "end": v(124.36, 245.24) * mm});
            skLineSegment(sketch, "E4758", {"start": v(124.36, 245.24) * mm, "end": v(124.44, 245) * mm});
            skLineSegment(sketch, "E4759", {"start": v(124.44, 245) * mm, "end": v(124.48, 244.75) * mm});
            skLineSegment(sketch, "E4760", {"start": v(124.48, 244.75) * mm, "end": v(124.5, 244.5) * mm});
            skLineSegment(sketch, "E4761", {"start": v(124.5, 244.5) * mm, "end": v(124.48, 244.25) * mm});
            skLineSegment(sketch, "E4762", {"start": v(124.48, 244.25) * mm, "end": v(124.44, 244) * mm});
            skLineSegment(sketch, "E4763", {"start": v(124.44, 244) * mm, "end": v(124.36, 243.76) * mm});
            skLineSegment(sketch, "E4764", {"start": v(124.36, 243.76) * mm, "end": v(124.25, 243.54) * mm});
            skLineSegment(sketch, "E4765", {"start": v(124.25, 243.54) * mm, "end": v(124.12, 243.32) * mm});
            skLineSegment(sketch, "E4766", {"start": v(124.12, 243.32) * mm, "end": v(123.96, 243.13) * mm});
            skLineSegment(sketch, "E4767", {"start": v(123.96, 243.13) * mm, "end": v(123.78, 242.96) * mm});
            skLineSegment(sketch, "E4768", {"start": v(123.78, 242.96) * mm, "end": v(123.57, 242.81) * mm});
            skLineSegment(sketch, "E4769", {"start": v(123.57, 242.81) * mm, "end": v(123.35, 242.7) * mm});
            skLineSegment(sketch, "E4770", {"start": v(123.35, 242.7) * mm, "end": v(123.12, 242.6) * mm});
            skLineSegment(sketch, "E4771", {"start": v(123.12, 242.6) * mm, "end": v(122.88, 242.53) * mm});
            skLineSegment(sketch, "E4772", {"start": v(122.88, 242.53) * mm, "end": v(122.63, 242.5) * mm});
            skLineSegment(sketch, "E4773", {"start": v(122.63, 242.5) * mm, "end": v(122.37, 242.5) * mm});
            skLineSegment(sketch, "E4774", {"start": v(287.37, 242.5) * mm, "end": v(287.12, 242.53) * mm});
            skLineSegment(sketch, "E4775", {"start": v(287.12, 242.53) * mm, "end": v(286.88, 242.6) * mm});
            skLineSegment(sketch, "E4776", {"start": v(286.88, 242.6) * mm, "end": v(286.65, 242.7) * mm});
            skLineSegment(sketch, "E4777", {"start": v(286.65, 242.7) * mm, "end": v(286.43, 242.81) * mm});
            skLineSegment(sketch, "E4778", {"start": v(286.43, 242.81) * mm, "end": v(286.23, 242.96) * mm});
            skLineSegment(sketch, "E4779", {"start": v(286.23, 242.96) * mm, "end": v(286.04, 243.13) * mm});
            skLineSegment(sketch, "E4780", {"start": v(286.04, 243.13) * mm, "end": v(285.88, 243.32) * mm});
            skLineSegment(sketch, "E4781", {"start": v(285.88, 243.32) * mm, "end": v(285.75, 243.54) * mm});
            skLineSegment(sketch, "E4782", {"start": v(285.75, 243.54) * mm, "end": v(285.64, 243.76) * mm});
            skLineSegment(sketch, "E4783", {"start": v(285.64, 243.76) * mm, "end": v(285.56, 244) * mm});
            skLineSegment(sketch, "E4784", {"start": v(285.56, 244) * mm, "end": v(285.52, 244.25) * mm});
            skLineSegment(sketch, "E4785", {"start": v(285.52, 244.25) * mm, "end": v(285.5, 244.5) * mm});
            skLineSegment(sketch, "E4786", {"start": v(285.5, 244.5) * mm, "end": v(285.52, 244.75) * mm});
            skLineSegment(sketch, "E4787", {"start": v(285.52, 244.75) * mm, "end": v(285.56, 245) * mm});
            skLineSegment(sketch, "E4788", {"start": v(285.56, 245) * mm, "end": v(285.64, 245.24) * mm});
            skLineSegment(sketch, "E4789", {"start": v(285.64, 245.24) * mm, "end": v(285.75, 245.46) * mm});
            skLineSegment(sketch, "E4790", {"start": v(285.75, 245.46) * mm, "end": v(285.88, 245.68) * mm});
            skLineSegment(sketch, "E4791", {"start": v(285.88, 245.68) * mm, "end": v(286.04, 245.87) * mm});
            skLineSegment(sketch, "E4792", {"start": v(286.04, 245.87) * mm, "end": v(286.23, 246.04) * mm});
            skLineSegment(sketch, "E4793", {"start": v(286.23, 246.04) * mm, "end": v(286.43, 246.19) * mm});
            skLineSegment(sketch, "E4794", {"start": v(286.43, 246.19) * mm, "end": v(286.65, 246.3) * mm});
            skLineSegment(sketch, "E4795", {"start": v(286.65, 246.3) * mm, "end": v(286.88, 246.4) * mm});
            skLineSegment(sketch, "E4796", {"start": v(286.88, 246.4) * mm, "end": v(287.12, 246.47) * mm});
            skLineSegment(sketch, "E4797", {"start": v(287.12, 246.47) * mm, "end": v(287.37, 246.5) * mm});
            skLineSegment(sketch, "E4798", {"start": v(287.37, 246.5) * mm, "end": v(287.63, 246.5) * mm});
            skLineSegment(sketch, "E4799", {"start": v(287.63, 246.5) * mm, "end": v(287.88, 246.47) * mm});
            skLineSegment(sketch, "E4800", {"start": v(287.88, 246.47) * mm, "end": v(288.12, 246.4) * mm});
            skLineSegment(sketch, "E4801", {"start": v(288.12, 246.4) * mm, "end": v(288.35, 246.3) * mm});
            skLineSegment(sketch, "E4802", {"start": v(288.35, 246.3) * mm, "end": v(288.57, 246.19) * mm});
            skLineSegment(sketch, "E4803", {"start": v(288.57, 246.19) * mm, "end": v(288.77, 246.04) * mm});
            skLineSegment(sketch, "E4804", {"start": v(288.77, 246.04) * mm, "end": v(288.96, 245.87) * mm});
            skLineSegment(sketch, "E4805", {"start": v(288.96, 245.87) * mm, "end": v(289.12, 245.68) * mm});
            skLineSegment(sketch, "E4806", {"start": v(289.12, 245.68) * mm, "end": v(289.25, 245.46) * mm});
            skLineSegment(sketch, "E4807", {"start": v(289.25, 245.46) * mm, "end": v(289.36, 245.24) * mm});
            skLineSegment(sketch, "E4808", {"start": v(289.36, 245.24) * mm, "end": v(289.44, 245) * mm});
            skLineSegment(sketch, "E4809", {"start": v(289.44, 245) * mm, "end": v(289.48, 244.75) * mm});
            skLineSegment(sketch, "E4810", {"start": v(289.48, 244.75) * mm, "end": v(289.5, 244.5) * mm});
            skLineSegment(sketch, "E4811", {"start": v(289.5, 244.5) * mm, "end": v(289.48, 244.25) * mm});
            skLineSegment(sketch, "E4812", {"start": v(289.48, 244.25) * mm, "end": v(289.44, 244) * mm});
            skLineSegment(sketch, "E4813", {"start": v(289.44, 244) * mm, "end": v(289.36, 243.76) * mm});
            skLineSegment(sketch, "E4814", {"start": v(289.36, 243.76) * mm, "end": v(289.25, 243.54) * mm});
            skLineSegment(sketch, "E4815", {"start": v(289.25, 243.54) * mm, "end": v(289.12, 243.32) * mm});
            skLineSegment(sketch, "E4816", {"start": v(289.12, 243.32) * mm, "end": v(288.96, 243.13) * mm});
            skLineSegment(sketch, "E4817", {"start": v(288.96, 243.13) * mm, "end": v(288.77, 242.96) * mm});
            skLineSegment(sketch, "E4818", {"start": v(288.77, 242.96) * mm, "end": v(288.57, 242.81) * mm});
            skLineSegment(sketch, "E4819", {"start": v(288.57, 242.81) * mm, "end": v(288.35, 242.7) * mm});
            skLineSegment(sketch, "E4820", {"start": v(288.35, 242.7) * mm, "end": v(288.12, 242.6) * mm});
            skLineSegment(sketch, "E4821", {"start": v(288.12, 242.6) * mm, "end": v(287.88, 242.53) * mm});
            skLineSegment(sketch, "E4822", {"start": v(287.88, 242.53) * mm, "end": v(287.63, 242.5) * mm});
            skLineSegment(sketch, "E4823", {"start": v(287.63, 242.5) * mm, "end": v(287.37, 242.5) * mm});
            skLineSegment(sketch, "E4824", {"start": v(146, -157) * mm, "end": v(146, -137) * mm});
            skLineSegment(sketch, "E4825", {"start": v(146, -137) * mm, "end": v(122, -137) * mm});
            skLineSegment(sketch, "E4826", {"start": v(122, -137) * mm, "end": v(122, -136.94) * mm});
            skLineSegment(sketch, "E4827", {"start": v(122, -136.94) * mm, "end": v(120.12, -136.94) * mm});
            skLineSegment(sketch, "E4828", {"start": v(120.12, -136.94) * mm, "end": v(116.38, -136.47) * mm});
            skLineSegment(sketch, "E4829", {"start": v(116.38, -136.47) * mm, "end": v(112.73, -135.53) * mm});
            skLineSegment(sketch, "E4830", {"start": v(112.73, -135.53) * mm, "end": v(109.23, -134.15) * mm});
            skLineSegment(sketch, "E4831", {"start": v(109.23, -134.15) * mm, "end": v(105.93, -132.33) * mm});
            skLineSegment(sketch, "E4832", {"start": v(105.93, -132.33) * mm, "end": v(102.88, -130.12) * mm});
            skLineSegment(sketch, "E4833", {"start": v(102.88, -130.12) * mm, "end": v(100.13, -127.54) * mm});
            skLineSegment(sketch, "E4834", {"start": v(100.13, -127.54) * mm, "end": v(97.73, -124.63) * mm});
            skLineSegment(sketch, "E4835", {"start": v(97.73, -124.63) * mm, "end": v(95.71, -121.45) * mm});
            skLineSegment(sketch, "E4836", {"start": v(95.71, -121.45) * mm, "end": v(94.1, -118.04) * mm});
            skLineSegment(sketch, "E4837", {"start": v(94.1, -118.04) * mm, "end": v(92.94, -114.46) * mm});
            skLineSegment(sketch, "E4838", {"start": v(92.94, -114.46) * mm, "end": v(92.24, -110.76) * mm});
            skLineSegment(sketch, "E4839", {"start": v(92.24, -110.76) * mm, "end": v(92, -107) * mm});
            skLineSegment(sketch, "E4840", {"start": v(92, -107) * mm, "end": v(92, 193) * mm});
            skLineSegment(sketch, "E4841", {"start": v(92, 193) * mm, "end": v(92.06, 193) * mm});
            skLineSegment(sketch, "E4842", {"start": v(92.06, 193) * mm, "end": v(92.06, 194.88) * mm});
            skLineSegment(sketch, "E4843", {"start": v(92.06, 194.88) * mm, "end": v(92.53, 198.62) * mm});
            skLineSegment(sketch, "E4844", {"start": v(92.53, 198.62) * mm, "end": v(93.47, 202.27) * mm});
            skLineSegment(sketch, "E4845", {"start": v(93.47, 202.27) * mm, "end": v(94.86, 205.77) * mm});
            skLineSegment(sketch, "E4846", {"start": v(94.86, 205.77) * mm, "end": v(96.67, 209.07) * mm});
            skLineSegment(sketch, "E4847", {"start": v(96.67, 209.07) * mm, "end": v(98.88, 212.12) * mm});
            skLineSegment(sketch, "E4848", {"start": v(98.88, 212.12) * mm, "end": v(101.46, 214.87) * mm});
            skLineSegment(sketch, "E4849", {"start": v(101.46, 214.87) * mm, "end": v(104.37, 217.27) * mm});
            skLineSegment(sketch, "E4850", {"start": v(104.37, 217.27) * mm, "end": v(107.55, 219.29) * mm});
            skLineSegment(sketch, "E4851", {"start": v(107.55, 219.29) * mm, "end": v(110.96, 220.9) * mm});
            skLineSegment(sketch, "E4852", {"start": v(110.96, 220.9) * mm, "end": v(114.54, 222.06) * mm});
            skLineSegment(sketch, "E4853", {"start": v(114.54, 222.06) * mm, "end": v(118.24, 222.76) * mm});
            skLineSegment(sketch, "E4854", {"start": v(118.24, 222.76) * mm, "end": v(122, 223) * mm});
            skLineSegment(sketch, "E4855", {"start": v(122, 223) * mm, "end": v(146, 223) * mm});
            skLineSegment(sketch, "E4856", {"start": v(146, 223) * mm, "end": v(146, 243) * mm});
            skLineSegment(sketch, "E4857", {"start": v(146, 243) * mm, "end": v(154, 243) * mm});
            skLineSegment(sketch, "E4858", {"start": v(154, 243) * mm, "end": v(154, 223) * mm});
            skLineSegment(sketch, "E4859", {"start": v(154, 223) * mm, "end": v(170, 223) * mm});
            skLineSegment(sketch, "E4860", {"start": v(170, 223) * mm, "end": v(170, 222.98) * mm});
            skLineSegment(sketch, "E4861", {"start": v(170, 222.98) * mm, "end": v(170.63, 222.98) * mm});
            skLineSegment(sketch, "E4862", {"start": v(170.63, 222.98) * mm, "end": v(171.87, 222.82) * mm});
            skLineSegment(sketch, "E4863", {"start": v(171.87, 222.82) * mm, "end": v(173.1, 222.51) * mm});
            skLineSegment(sketch, "E4864", {"start": v(173.1, 222.51) * mm, "end": v(174.26, 222.05) * mm});
            skLineSegment(sketch, "E4865", {"start": v(174.26, 222.05) * mm, "end": v(175.36, 221.44) * mm});
            skLineSegment(sketch, "E4866", {"start": v(175.36, 221.44) * mm, "end": v(176.37, 220.7) * mm});
            skLineSegment(sketch, "E4867", {"start": v(176.37, 220.7) * mm, "end": v(177.29, 219.84) * mm});
            skLineSegment(sketch, "E4868", {"start": v(177.29, 219.84) * mm, "end": v(178.1, 218.88) * mm});
            skLineSegment(sketch, "E4869", {"start": v(178.1, 218.88) * mm, "end": v(178.76, 217.82) * mm});
            skLineSegment(sketch, "E4870", {"start": v(178.76, 217.82) * mm, "end": v(179.3, 216.68) * mm});
            skLineSegment(sketch, "E4871", {"start": v(179.3, 216.68) * mm, "end": v(179.69, 215.49) * mm});
            skLineSegment(sketch, "E4872", {"start": v(179.69, 215.49) * mm, "end": v(179.92, 214.25) * mm});
            skLineSegment(sketch, "E4873", {"start": v(179.92, 214.25) * mm, "end": v(180, 213) * mm});
            skLineSegment(sketch, "E4874", {"start": v(180, 213) * mm, "end": v(180, 211.5) * mm});
            skLineSegment(sketch, "E4875", {"start": v(180, 211.5) * mm, "end": v(180.05, 210.69) * mm});
            skLineSegment(sketch, "E4876", {"start": v(180.05, 210.69) * mm, "end": v(180.2, 209.88) * mm});
            skLineSegment(sketch, "E4877", {"start": v(180.2, 209.88) * mm, "end": v(180.46, 209.1) * mm});
            skLineSegment(sketch, "E4878", {"start": v(180.46, 209.1) * mm, "end": v(180.8, 208.37) * mm});
            skLineSegment(sketch, "E4879", {"start": v(180.8, 208.37) * mm, "end": v(181.24, 207.68) * mm});
            skLineSegment(sketch, "E4880", {"start": v(181.24, 207.68) * mm, "end": v(181.76, 207.05) * mm});
            skLineSegment(sketch, "E4881", {"start": v(181.76, 207.05) * mm, "end": v(182.36, 206.5) * mm});
            skLineSegment(sketch, "E4882", {"start": v(182.36, 206.5) * mm, "end": v(183.02, 206.01) * mm});
            skLineSegment(sketch, "E4883", {"start": v(183.02, 206.01) * mm, "end": v(183.73, 205.62) * mm});
            skLineSegment(sketch, "E4884", {"start": v(183.73, 205.62) * mm, "end": v(184.5, 205.32) * mm});
            skLineSegment(sketch, "E4885", {"start": v(184.5, 205.32) * mm, "end": v(185.28, 205.12) * mm});
            skLineSegment(sketch, "E4886", {"start": v(185.28, 205.12) * mm, "end": v(186.1, 205.01) * mm});
            skLineSegment(sketch, "E4887", {"start": v(186.1, 205.01) * mm, "end": v(186.9, 205.01) * mm});
            skLineSegment(sketch, "E4888", {"start": v(186.9, 205.01) * mm, "end": v(187.72, 205.12) * mm});
            skLineSegment(sketch, "E4889", {"start": v(187.72, 205.12) * mm, "end": v(188.5, 205.32) * mm});
            skLineSegment(sketch, "E4890", {"start": v(188.5, 205.32) * mm, "end": v(189.27, 205.62) * mm});
            skLineSegment(sketch, "E4891", {"start": v(189.27, 205.62) * mm, "end": v(189.98, 206.01) * mm});
            skLineSegment(sketch, "E4892", {"start": v(189.98, 206.01) * mm, "end": v(190.64, 206.5) * mm});
            skLineSegment(sketch, "E4893", {"start": v(190.64, 206.5) * mm, "end": v(191.24, 207.05) * mm});
            skLineSegment(sketch, "E4894", {"start": v(191.24, 207.05) * mm, "end": v(191.76, 207.68) * mm});
            skLineSegment(sketch, "E4895", {"start": v(191.76, 207.68) * mm, "end": v(192.2, 208.37) * mm});
            skLineSegment(sketch, "E4896", {"start": v(192.2, 208.37) * mm, "end": v(192.54, 209.1) * mm});
            skLineSegment(sketch, "E4897", {"start": v(192.54, 209.1) * mm, "end": v(192.8, 209.88) * mm});
            skLineSegment(sketch, "E4898", {"start": v(192.8, 209.88) * mm, "end": v(192.95, 210.69) * mm});
            skLineSegment(sketch, "E4899", {"start": v(192.95, 210.69) * mm, "end": v(193, 211.5) * mm});
            skLineSegment(sketch, "E4900", {"start": v(193, 211.5) * mm, "end": v(193.03, 211.5) * mm});
            skLineSegment(sketch, "E4901", {"start": v(193.03, 211.5) * mm, "end": v(193.1, 212.5) * mm});
            skLineSegment(sketch, "E4902", {"start": v(193.1, 212.5) * mm, "end": v(193.38, 213.98) * mm});
            skLineSegment(sketch, "E4903", {"start": v(193.38, 213.98) * mm, "end": v(193.84, 215.42) * mm});
            skLineSegment(sketch, "E4904", {"start": v(193.84, 215.42) * mm, "end": v(194.48, 216.78) * mm});
            skLineSegment(sketch, "E4905", {"start": v(194.48, 216.78) * mm, "end": v(195.3, 218.05) * mm});
            skLineSegment(sketch, "E4906", {"start": v(195.3, 218.05) * mm, "end": v(196.25, 219.22) * mm});
            skLineSegment(sketch, "E4907", {"start": v(196.25, 219.22) * mm, "end": v(197.35, 220.25) * mm});
            skLineSegment(sketch, "E4908", {"start": v(197.35, 220.25) * mm, "end": v(198.57, 221.13) * mm});
            skLineSegment(sketch, "E4909", {"start": v(198.57, 221.13) * mm, "end": v(199.9, 221.86) * mm});
            skLineSegment(sketch, "E4910", {"start": v(199.9, 221.86) * mm, "end": v(201.3, 222.41) * mm});
            skLineSegment(sketch, "E4911", {"start": v(201.3, 222.41) * mm, "end": v(202.75, 222.79) * mm});
            skLineSegment(sketch, "E4912", {"start": v(202.75, 222.79) * mm, "end": v(204.25, 222.98) * mm});
            skLineSegment(sketch, "E4913", {"start": v(204.25, 222.98) * mm, "end": v(205.75, 222.98) * mm});
            skLineSegment(sketch, "E4914", {"start": v(205.75, 222.98) * mm, "end": v(207.25, 222.79) * mm});
            skLineSegment(sketch, "E4915", {"start": v(207.25, 222.79) * mm, "end": v(208.7, 222.41) * mm});
            skLineSegment(sketch, "E4916", {"start": v(208.7, 222.41) * mm, "end": v(210.1, 221.86) * mm});
            skLineSegment(sketch, "E4917", {"start": v(210.1, 221.86) * mm, "end": v(211.43, 221.13) * mm});
            skLineSegment(sketch, "E4918", {"start": v(211.43, 221.13) * mm, "end": v(212.65, 220.25) * mm});
            skLineSegment(sketch, "E4919", {"start": v(212.65, 220.25) * mm, "end": v(213.75, 219.22) * mm});
            skLineSegment(sketch, "E4920", {"start": v(213.75, 219.22) * mm, "end": v(213.88, 219.1) * mm});
            skLineSegment(sketch, "E4921", {"start": v(213.88, 219.1) * mm, "end": v(214, 218.98) * mm});
            skLineSegment(sketch, "E4922", {"start": v(214, 218.98) * mm, "end": v(214.14, 218.87) * mm});
            skLineSegment(sketch, "E4923", {"start": v(214.14, 218.87) * mm, "end": v(214.27, 218.76) * mm});
            skLineSegment(sketch, "E4924", {"start": v(214.27, 218.76) * mm, "end": v(214.4, 218.65) * mm});
            skLineSegment(sketch, "E4925", {"start": v(214.4, 218.65) * mm, "end": v(214.55, 218.55) * mm});
            skLineSegment(sketch, "E4926", {"start": v(214.55, 218.55) * mm, "end": v(214.69, 218.45) * mm});
            skLineSegment(sketch, "E4927", {"start": v(214.69, 218.45) * mm, "end": v(214.83, 218.35) * mm});
            skLineSegment(sketch, "E4928", {"start": v(214.83, 218.35) * mm, "end": v(215.94, 217.33) * mm});
            skLineSegment(sketch, "E4929", {"start": v(215.94, 217.33) * mm, "end": v(216.92, 216.18) * mm});
            skLineSegment(sketch, "E4930", {"start": v(216.92, 216.18) * mm, "end": v(217.74, 214.92) * mm});
            skLineSegment(sketch, "E4931", {"start": v(217.74, 214.92) * mm, "end": v(218.4, 213.57) * mm});
            skLineSegment(sketch, "E4932", {"start": v(218.4, 213.57) * mm, "end": v(218.89, 212.14) * mm});
            skLineSegment(sketch, "E4933", {"start": v(218.89, 212.14) * mm, "end": v(219.2, 210.66) * mm});
            skLineSegment(sketch, "E4934", {"start": v(219.2, 210.66) * mm, "end": v(219.3, 209.16) * mm});
            skLineSegment(sketch, "E4935", {"start": v(219.3, 209.16) * mm, "end": v(219.23, 207.66) * mm});
            skLineSegment(sketch, "E4936", {"start": v(219.23, 207.66) * mm, "end": v(219.07, 206.76) * mm});
            skLineSegment(sketch, "E4937", {"start": v(219.07, 206.76) * mm, "end": v(219.36, 206.5) * mm});
            skLineSegment(sketch, "E4938", {"start": v(219.36, 206.5) * mm, "end": v(220.02, 206.01) * mm});
            skLineSegment(sketch, "E4939", {"start": v(220.02, 206.01) * mm, "end": v(220.73, 205.62) * mm});
            skLineSegment(sketch, "E4940", {"start": v(220.73, 205.62) * mm, "end": v(221.5, 205.32) * mm});
            skLineSegment(sketch, "E4941", {"start": v(221.5, 205.32) * mm, "end": v(222.28, 205.12) * mm});
            skLineSegment(sketch, "E4942", {"start": v(222.28, 205.12) * mm, "end": v(223.1, 205.01) * mm});
            skLineSegment(sketch, "E4943", {"start": v(223.1, 205.01) * mm, "end": v(223.9, 205.01) * mm});
            skLineSegment(sketch, "E4944", {"start": v(223.9, 205.01) * mm, "end": v(224.72, 205.12) * mm});
            skLineSegment(sketch, "E4945", {"start": v(224.72, 205.12) * mm, "end": v(225.5, 205.32) * mm});
            skLineSegment(sketch, "E4946", {"start": v(225.5, 205.32) * mm, "end": v(226.27, 205.62) * mm});
            skLineSegment(sketch, "E4947", {"start": v(226.27, 205.62) * mm, "end": v(226.98, 206.01) * mm});
            skLineSegment(sketch, "E4948", {"start": v(226.98, 206.01) * mm, "end": v(227.64, 206.5) * mm});
            skLineSegment(sketch, "E4949", {"start": v(227.64, 206.5) * mm, "end": v(228.24, 207.05) * mm});
            skLineSegment(sketch, "E4950", {"start": v(228.24, 207.05) * mm, "end": v(228.76, 207.68) * mm});
            skLineSegment(sketch, "E4951", {"start": v(228.76, 207.68) * mm, "end": v(229.2, 208.37) * mm});
            skLineSegment(sketch, "E4952", {"start": v(229.2, 208.37) * mm, "end": v(229.54, 209.1) * mm});
            skLineSegment(sketch, "E4953", {"start": v(229.54, 209.1) * mm, "end": v(229.8, 209.88) * mm});
            skLineSegment(sketch, "E4954", {"start": v(229.8, 209.88) * mm, "end": v(229.95, 210.69) * mm});
            skLineSegment(sketch, "E4955", {"start": v(229.95, 210.69) * mm, "end": v(230, 211.5) * mm});
            skLineSegment(sketch, "E4956", {"start": v(230, 211.5) * mm, "end": v(230, 213) * mm});
            skLineSegment(sketch, "E4957", {"start": v(230, 213) * mm, "end": v(230.08, 214.25) * mm});
            skLineSegment(sketch, "E4958", {"start": v(230.08, 214.25) * mm, "end": v(230.31, 215.49) * mm});
            skLineSegment(sketch, "E4959", {"start": v(230.31, 215.49) * mm, "end": v(230.7, 216.68) * mm});
            skLineSegment(sketch, "E4960", {"start": v(230.7, 216.68) * mm, "end": v(231.24, 217.82) * mm});
            skLineSegment(sketch, "E4961", {"start": v(231.24, 217.82) * mm, "end": v(231.9, 218.88) * mm});
            skLineSegment(sketch, "E4962", {"start": v(231.9, 218.88) * mm, "end": v(232.71, 219.84) * mm});
            skLineSegment(sketch, "E4963", {"start": v(232.71, 219.84) * mm, "end": v(233.63, 220.7) * mm});
            skLineSegment(sketch, "E4964", {"start": v(233.63, 220.7) * mm, "end": v(234.64, 221.44) * mm});
            skLineSegment(sketch, "E4965", {"start": v(234.64, 221.44) * mm, "end": v(235.74, 222.05) * mm});
            skLineSegment(sketch, "E4966", {"start": v(235.74, 222.05) * mm, "end": v(236.9, 222.51) * mm});
            skLineSegment(sketch, "E4967", {"start": v(236.9, 222.51) * mm, "end": v(238.13, 222.82) * mm});
            skLineSegment(sketch, "E4968", {"start": v(238.13, 222.82) * mm, "end": v(239.37, 222.98) * mm});
            skLineSegment(sketch, "E4969", {"start": v(239.37, 222.98) * mm, "end": v(240, 222.98) * mm});
            skLineSegment(sketch, "E4970", {"start": v(240, 222.98) * mm, "end": v(240, 223) * mm});
            skLineSegment(sketch, "E4971", {"start": v(240, 223) * mm, "end": v(256, 223) * mm});
            skLineSegment(sketch, "E4972", {"start": v(256, 223) * mm, "end": v(256, 243) * mm});
            skLineSegment(sketch, "E4973", {"start": v(256, 243) * mm, "end": v(264, 243) * mm});
            skLineSegment(sketch, "E4974", {"start": v(264, 243) * mm, "end": v(264, 223) * mm});
            skLineSegment(sketch, "E4975", {"start": v(264, 223) * mm, "end": v(288, 223) * mm});
            skLineSegment(sketch, "E4976", {"start": v(288, 223) * mm, "end": v(288, 222.94) * mm});
            skLineSegment(sketch, "E4977", {"start": v(288, 222.94) * mm, "end": v(289.88, 222.94) * mm});
            skLineSegment(sketch, "E4978", {"start": v(289.88, 222.94) * mm, "end": v(293.62, 222.47) * mm});
            skLineSegment(sketch, "E4979", {"start": v(293.62, 222.47) * mm, "end": v(297.27, 221.53) * mm});
            skLineSegment(sketch, "E4980", {"start": v(297.27, 221.53) * mm, "end": v(300.77, 220.15) * mm});
            skLineSegment(sketch, "E4981", {"start": v(300.77, 220.15) * mm, "end": v(304.07, 218.33) * mm});
            skLineSegment(sketch, "E4982", {"start": v(304.07, 218.33) * mm, "end": v(307.12, 216.12) * mm});
            skLineSegment(sketch, "E4983", {"start": v(307.12, 216.12) * mm, "end": v(309.87, 213.54) * mm});
            skLineSegment(sketch, "E4984", {"start": v(309.87, 213.54) * mm, "end": v(312.27, 210.63) * mm});
            skLineSegment(sketch, "E4985", {"start": v(312.27, 210.63) * mm, "end": v(314.29, 207.45) * mm});
            skLineSegment(sketch, "E4986", {"start": v(314.29, 207.45) * mm, "end": v(315.9, 204.04) * mm});
            skLineSegment(sketch, "E4987", {"start": v(315.9, 204.04) * mm, "end": v(317.06, 200.46) * mm});
            skLineSegment(sketch, "E4988", {"start": v(317.06, 200.46) * mm, "end": v(317.76, 196.76) * mm});
            skLineSegment(sketch, "E4989", {"start": v(317.76, 196.76) * mm, "end": v(318, 193) * mm});
            skLineSegment(sketch, "E4990", {"start": v(318, 193) * mm, "end": v(318, -107) * mm});
            skLineSegment(sketch, "E4991", {"start": v(318, -107) * mm, "end": v(317.94, -107) * mm});
            skLineSegment(sketch, "E4992", {"start": v(317.94, -107) * mm, "end": v(317.94, -108.88) * mm});
            skLineSegment(sketch, "E4993", {"start": v(317.94, -108.88) * mm, "end": v(317.47, -112.62) * mm});
            skLineSegment(sketch, "E4994", {"start": v(317.47, -112.62) * mm, "end": v(316.53, -116.27) * mm});
            skLineSegment(sketch, "E4995", {"start": v(316.53, -116.27) * mm, "end": v(315.14, -119.77) * mm});
            skLineSegment(sketch, "E4996", {"start": v(315.14, -119.77) * mm, "end": v(313.33, -123.08) * mm});
            skLineSegment(sketch, "E4997", {"start": v(313.33, -123.08) * mm, "end": v(311.12, -126.12) * mm});
            skLineSegment(sketch, "E4998", {"start": v(311.12, -126.12) * mm, "end": v(308.54, -128.87) * mm});
            skLineSegment(sketch, "E4999", {"start": v(308.54, -128.87) * mm, "end": v(305.63, -131.27) * mm});
            skLineSegment(sketch, "E5000", {"start": v(305.63, -131.27) * mm, "end": v(302.45, -133.29) * mm});
            skLineSegment(sketch, "E5001", {"start": v(302.45, -133.29) * mm, "end": v(299.04, -134.9) * mm});
            skLineSegment(sketch, "E5002", {"start": v(299.04, -134.9) * mm, "end": v(295.46, -136.06) * mm});
            skLineSegment(sketch, "E5003", {"start": v(295.46, -136.06) * mm, "end": v(291.76, -136.76) * mm});
            skLineSegment(sketch, "E5004", {"start": v(291.76, -136.76) * mm, "end": v(288, -137) * mm});
            skLineSegment(sketch, "E5005", {"start": v(288, -137) * mm, "end": v(264, -137) * mm});
            skLineSegment(sketch, "E5006", {"start": v(264, -137) * mm, "end": v(264, -157) * mm});
            skLineSegment(sketch, "E5007", {"start": v(264, -157) * mm, "end": v(256, -157) * mm});
            skLineSegment(sketch, "E5008", {"start": v(256, -157) * mm, "end": v(256, -137) * mm});
            skLineSegment(sketch, "E5009", {"start": v(256, -137) * mm, "end": v(237, -137) * mm});
            skLineSegment(sketch, "E5010", {"start": v(237, -137) * mm, "end": v(237, -136.98) * mm});
            skLineSegment(sketch, "E5011", {"start": v(237, -136.98) * mm, "end": v(236.37, -136.98) * mm});
            skLineSegment(sketch, "E5012", {"start": v(236.37, -136.98) * mm, "end": v(235.13, -136.82) * mm});
            skLineSegment(sketch, "E5013", {"start": v(235.13, -136.82) * mm, "end": v(233.9, -136.51) * mm});
            skLineSegment(sketch, "E5014", {"start": v(233.9, -136.51) * mm, "end": v(232.74, -136.05) * mm});
            skLineSegment(sketch, "E5015", {"start": v(232.74, -136.05) * mm, "end": v(231.64, -135.44) * mm});
            skLineSegment(sketch, "E5016", {"start": v(231.64, -135.44) * mm, "end": v(230.63, -134.7) * mm});
            skLineSegment(sketch, "E5017", {"start": v(230.63, -134.7) * mm, "end": v(229.71, -133.84) * mm});
            skLineSegment(sketch, "E5018", {"start": v(229.71, -133.84) * mm, "end": v(228.9, -132.88) * mm});
            skLineSegment(sketch, "E5019", {"start": v(228.9, -132.88) * mm, "end": v(228.24, -131.82) * mm});
            skLineSegment(sketch, "E5020", {"start": v(228.24, -131.82) * mm, "end": v(227.7, -130.68) * mm});
            skLineSegment(sketch, "E5021", {"start": v(227.7, -130.68) * mm, "end": v(227.31, -129.49) * mm});
            skLineSegment(sketch, "E5022", {"start": v(227.31, -129.49) * mm, "end": v(227.08, -128.25) * mm});
            skLineSegment(sketch, "E5023", {"start": v(227.08, -128.25) * mm, "end": v(227, -127) * mm});
            skLineSegment(sketch, "E5024", {"start": v(227, -127) * mm, "end": v(227, -118) * mm});
            skLineSegment(sketch, "E5025", {"start": v(227, -118) * mm, "end": v(226.96, -117.37) * mm});
            skLineSegment(sketch, "E5026", {"start": v(226.96, -117.37) * mm, "end": v(226.84, -116.76) * mm});
            skLineSegment(sketch, "E5027", {"start": v(226.84, -116.76) * mm, "end": v(226.65, -116.16) * mm});
            skLineSegment(sketch, "E5028", {"start": v(226.65, -116.16) * mm, "end": v(226.38, -115.6) * mm});
            skLineSegment(sketch, "E5029", {"start": v(226.38, -115.6) * mm, "end": v(226.04, -115.06) * mm});
            skLineSegment(sketch, "E5030", {"start": v(226.04, -115.06) * mm, "end": v(225.65, -114.58) * mm});
            skLineSegment(sketch, "E5031", {"start": v(225.65, -114.58) * mm, "end": v(225.19, -114.15) * mm});
            skLineSegment(sketch, "E5032", {"start": v(225.19, -114.15) * mm, "end": v(224.68, -113.78) * mm});
            skLineSegment(sketch, "E5033", {"start": v(224.68, -113.78) * mm, "end": v(224.13, -113.48) * mm});
            skLineSegment(sketch, "E5034", {"start": v(224.13, -113.48) * mm, "end": v(223.54, -113.25) * mm});
            skLineSegment(sketch, "E5035", {"start": v(223.54, -113.25) * mm, "end": v(222.94, -113.09) * mm});
            skLineSegment(sketch, "E5036", {"start": v(222.94, -113.09) * mm, "end": v(222.31, -113.01) * mm});
            skLineSegment(sketch, "E5037", {"start": v(222.31, -113.01) * mm, "end": v(221.69, -113.01) * mm});
            skLineSegment(sketch, "E5038", {"start": v(221.69, -113.01) * mm, "end": v(221.06, -113.09) * mm});
            skLineSegment(sketch, "E5039", {"start": v(221.06, -113.09) * mm, "end": v(220.46, -113.25) * mm});
            skLineSegment(sketch, "E5040", {"start": v(220.46, -113.25) * mm, "end": v(219.87, -113.48) * mm});
            skLineSegment(sketch, "E5041", {"start": v(219.87, -113.48) * mm, "end": v(219.32, -113.78) * mm});
            skLineSegment(sketch, "E5042", {"start": v(219.32, -113.78) * mm, "end": v(218.81, -114.15) * mm});
            skLineSegment(sketch, "E5043", {"start": v(218.81, -114.15) * mm, "end": v(218.35, -114.58) * mm});
            skLineSegment(sketch, "E5044", {"start": v(218.35, -114.58) * mm, "end": v(217.96, -115.06) * mm});
            skLineSegment(sketch, "E5045", {"start": v(217.96, -115.06) * mm, "end": v(217.62, -115.6) * mm});
            skLineSegment(sketch, "E5046", {"start": v(217.62, -115.6) * mm, "end": v(217.35, -116.16) * mm});
            skLineSegment(sketch, "E5047", {"start": v(217.35, -116.16) * mm, "end": v(217.16, -116.76) * mm});
            skLineSegment(sketch, "E5048", {"start": v(217.16, -116.76) * mm, "end": v(217.04, -117.37) * mm});
            skLineSegment(sketch, "E5049", {"start": v(217.04, -117.37) * mm, "end": v(217, -118) * mm});
            skLineSegment(sketch, "E5050", {"start": v(217, -118) * mm, "end": v(217, -125) * mm});
            skLineSegment(sketch, "E5051", {"start": v(217, -125) * mm, "end": v(216.9, -126.5) * mm});
            skLineSegment(sketch, "E5052", {"start": v(216.9, -126.5) * mm, "end": v(216.62, -127.98) * mm});
            skLineSegment(sketch, "E5053", {"start": v(216.62, -127.98) * mm, "end": v(216.16, -129.42) * mm});
            skLineSegment(sketch, "E5054", {"start": v(216.16, -129.42) * mm, "end": v(215.52, -130.78) * mm});
            skLineSegment(sketch, "E5055", {"start": v(215.52, -130.78) * mm, "end": v(214.7, -132.05) * mm});
            skLineSegment(sketch, "E5056", {"start": v(214.7, -132.05) * mm, "end": v(213.75, -133.22) * mm});
            skLineSegment(sketch, "E5057", {"start": v(213.75, -133.22) * mm, "end": v(212.65, -134.25) * mm});
            skLineSegment(sketch, "E5058", {"start": v(212.65, -134.25) * mm, "end": v(211.43, -135.13) * mm});
            skLineSegment(sketch, "E5059", {"start": v(211.43, -135.13) * mm, "end": v(210.1, -135.86) * mm});
            skLineSegment(sketch, "E5060", {"start": v(210.1, -135.86) * mm, "end": v(208.7, -136.41) * mm});
            skLineSegment(sketch, "E5061", {"start": v(208.7, -136.41) * mm, "end": v(207.25, -136.79) * mm});
            skLineSegment(sketch, "E5062", {"start": v(207.25, -136.79) * mm, "end": v(205.75, -136.98) * mm});
            skLineSegment(sketch, "E5063", {"start": v(205.75, -136.98) * mm, "end": v(205, -136.98) * mm});
            skLineSegment(sketch, "E5064", {"start": v(205, -136.98) * mm, "end": v(205, -137) * mm});
            skLineSegment(sketch, "E5065", {"start": v(205, -137) * mm, "end": v(203.5, -136.9) * mm});
            skLineSegment(sketch, "E5066", {"start": v(203.5, -136.9) * mm, "end": v(202.02, -136.62) * mm});
            skLineSegment(sketch, "E5067", {"start": v(202.02, -136.62) * mm, "end": v(200.58, -136.16) * mm});
            skLineSegment(sketch, "E5068", {"start": v(200.58, -136.16) * mm, "end": v(199.22, -135.52) * mm});
            skLineSegment(sketch, "E5069", {"start": v(199.22, -135.52) * mm, "end": v(197.95, -134.7) * mm});
            skLineSegment(sketch, "E5070", {"start": v(197.95, -134.7) * mm, "end": v(196.78, -133.75) * mm});
            skLineSegment(sketch, "E5071", {"start": v(196.78, -133.75) * mm, "end": v(195.75, -132.65) * mm});
            skLineSegment(sketch, "E5072", {"start": v(195.75, -132.65) * mm, "end": v(194.87, -131.43) * mm});
            skLineSegment(sketch, "E5073", {"start": v(194.87, -131.43) * mm, "end": v(194.14, -130.1) * mm});
            skLineSegment(sketch, "E5074", {"start": v(194.14, -130.1) * mm, "end": v(193.59, -128.7) * mm});
            skLineSegment(sketch, "E5075", {"start": v(193.59, -128.7) * mm, "end": v(193.21, -127.25) * mm});
            skLineSegment(sketch, "E5076", {"start": v(193.21, -127.25) * mm, "end": v(193.02, -125.75) * mm});
            skLineSegment(sketch, "E5077", {"start": v(193.02, -125.75) * mm, "end": v(193.02, -125) * mm});
            skLineSegment(sketch, "E5078", {"start": v(193.02, -125) * mm, "end": v(193, -125) * mm});
            skLineSegment(sketch, "E5079", {"start": v(193, -125) * mm, "end": v(193, -118) * mm});
            skLineSegment(sketch, "E5080", {"start": v(193, -118) * mm, "end": v(192.96, -117.37) * mm});
            skLineSegment(sketch, "E5081", {"start": v(192.96, -117.37) * mm, "end": v(192.84, -116.76) * mm});
            skLineSegment(sketch, "E5082", {"start": v(192.84, -116.76) * mm, "end": v(192.65, -116.16) * mm});
            skLineSegment(sketch, "E5083", {"start": v(192.65, -116.16) * mm, "end": v(192.38, -115.6) * mm});
            skLineSegment(sketch, "E5084", {"start": v(192.38, -115.6) * mm, "end": v(192.04, -115.06) * mm});
            skLineSegment(sketch, "E5085", {"start": v(192.04, -115.06) * mm, "end": v(191.65, -114.58) * mm});
            skLineSegment(sketch, "E5086", {"start": v(191.65, -114.58) * mm, "end": v(191.19, -114.15) * mm});
            skLineSegment(sketch, "E5087", {"start": v(191.19, -114.15) * mm, "end": v(190.68, -113.78) * mm});
            skLineSegment(sketch, "E5088", {"start": v(190.68, -113.78) * mm, "end": v(190.13, -113.48) * mm});
            skLineSegment(sketch, "E5089", {"start": v(190.13, -113.48) * mm, "end": v(189.54, -113.25) * mm});
            skLineSegment(sketch, "E5090", {"start": v(189.54, -113.25) * mm, "end": v(188.94, -113.09) * mm});
            skLineSegment(sketch, "E5091", {"start": v(188.94, -113.09) * mm, "end": v(188.31, -113.01) * mm});
            skLineSegment(sketch, "E5092", {"start": v(188.31, -113.01) * mm, "end": v(188, -113.01) * mm});
            skLineSegment(sketch, "E5093", {"start": v(188, -113.01) * mm, "end": v(188, -113) * mm});
            skLineSegment(sketch, "E5094", {"start": v(188, -113) * mm, "end": v(187.37, -113.04) * mm});
            skLineSegment(sketch, "E5095", {"start": v(187.37, -113.04) * mm, "end": v(186.76, -113.16) * mm});
            skLineSegment(sketch, "E5096", {"start": v(186.76, -113.16) * mm, "end": v(186.16, -113.35) * mm});
            skLineSegment(sketch, "E5097", {"start": v(186.16, -113.35) * mm, "end": v(185.6, -113.62) * mm});
            skLineSegment(sketch, "E5098", {"start": v(185.6, -113.62) * mm, "end": v(185.06, -113.95) * mm});
            skLineSegment(sketch, "E5099", {"start": v(185.06, -113.95) * mm, "end": v(184.58, -114.36) * mm});
            skLineSegment(sketch, "E5100", {"start": v(184.58, -114.36) * mm, "end": v(184.15, -114.81) * mm});
            skLineSegment(sketch, "E5101", {"start": v(184.15, -114.81) * mm, "end": v(183.78, -115.32) * mm});
            skLineSegment(sketch, "E5102", {"start": v(183.78, -115.32) * mm, "end": v(183.48, -115.87) * mm});
            skLineSegment(sketch, "E5103", {"start": v(183.48, -115.87) * mm, "end": v(183.25, -116.45) * mm});
            skLineSegment(sketch, "E5104", {"start": v(183.25, -116.45) * mm, "end": v(183.09, -117.06) * mm});
            skLineSegment(sketch, "E5105", {"start": v(183.09, -117.06) * mm, "end": v(183.01, -117.69) * mm});
            skLineSegment(sketch, "E5106", {"start": v(183.01, -117.69) * mm, "end": v(183.01, -118) * mm});
            skLineSegment(sketch, "E5107", {"start": v(183.01, -118) * mm, "end": v(183, -118) * mm});
            skLineSegment(sketch, "E5108", {"start": v(183, -118) * mm, "end": v(183, -127) * mm});
            skLineSegment(sketch, "E5109", {"start": v(183, -127) * mm, "end": v(182.92, -128.25) * mm});
            skLineSegment(sketch, "E5110", {"start": v(182.92, -128.25) * mm, "end": v(182.69, -129.49) * mm});
            skLineSegment(sketch, "E5111", {"start": v(182.69, -129.49) * mm, "end": v(182.3, -130.68) * mm});
            skLineSegment(sketch, "E5112", {"start": v(182.3, -130.68) * mm, "end": v(181.76, -131.82) * mm});
            skLineSegment(sketch, "E5113", {"start": v(181.76, -131.82) * mm, "end": v(181.1, -132.88) * mm});
            skLineSegment(sketch, "E5114", {"start": v(181.1, -132.88) * mm, "end": v(180.29, -133.84) * mm});
            skLineSegment(sketch, "E5115", {"start": v(180.29, -133.84) * mm, "end": v(179.37, -134.7) * mm});
            skLineSegment(sketch, "E5116", {"start": v(179.37, -134.7) * mm, "end": v(178.36, -135.44) * mm});
            skLineSegment(sketch, "E5117", {"start": v(178.36, -135.44) * mm, "end": v(177.26, -136.05) * mm});
            skLineSegment(sketch, "E5118", {"start": v(177.26, -136.05) * mm, "end": v(176.1, -136.51) * mm});
            skLineSegment(sketch, "E5119", {"start": v(176.1, -136.51) * mm, "end": v(174.87, -136.82) * mm});
            skLineSegment(sketch, "E5120", {"start": v(174.87, -136.82) * mm, "end": v(173.63, -136.98) * mm});
            skLineSegment(sketch, "E5121", {"start": v(173.63, -136.98) * mm, "end": v(173, -136.98) * mm});
            skLineSegment(sketch, "E5122", {"start": v(173, -136.98) * mm, "end": v(173, -137) * mm});
            skLineSegment(sketch, "E5123", {"start": v(173, -137) * mm, "end": v(154, -137) * mm});
            skLineSegment(sketch, "E5124", {"start": v(154, -137) * mm, "end": v(154, -157) * mm});
            skLineSegment(sketch, "E5125", {"start": v(154, -157) * mm, "end": v(146, -157) * mm});
            skLineSegment(sketch, "E5126", {"start": v(230, 192) * mm, "end": v(230, 192) * mm});
            skLineSegment(sketch, "E5127", {"start": v(230, 192) * mm, "end": v(230, 191.84) * mm});
            skLineSegment(sketch, "E5128", {"start": v(230, 191.84) * mm, "end": v(230, 192) * mm});
            skLineSegment(sketch, "E5129", {"start": v(180, 191.84) * mm, "end": v(180, 191.69) * mm});
            skLineSegment(sketch, "E5130", {"start": v(180, 191.69) * mm, "end": v(180.03, 191.53) * mm});
            skLineSegment(sketch, "E5131", {"start": v(180.03, 191.53) * mm, "end": v(180, 191.84) * mm});
            skLineSegment(sketch, "E5132", {"start": v(229.96, 191.37) * mm, "end": v(229.97, 191.53) * mm});
            skLineSegment(sketch, "E5133", {"start": v(229.97, 191.53) * mm, "end": v(229.93, 191.22) * mm});
            skLineSegment(sketch, "E5134", {"start": v(229.93, 191.22) * mm, "end": v(229.96, 191.37) * mm});
            skLineSegment(sketch, "E5135", {"start": v(180.07, 191.22) * mm, "end": v(180.09, 191.06) * mm});
            skLineSegment(sketch, "E5136", {"start": v(180.09, 191.06) * mm, "end": v(180.13, 190.91) * mm});
            skLineSegment(sketch, "E5137", {"start": v(180.13, 190.91) * mm, "end": v(180.07, 191.22) * mm});
            skLineSegment(sketch, "E5138", {"start": v(229.84, 190.76) * mm, "end": v(229.87, 190.91) * mm});
            skLineSegment(sketch, "E5139", {"start": v(229.87, 190.91) * mm, "end": v(229.8, 190.6) * mm});
            skLineSegment(sketch, "E5140", {"start": v(229.8, 190.6) * mm, "end": v(229.84, 190.76) * mm});
            skLineSegment(sketch, "E5141", {"start": v(180.2, 190.6) * mm, "end": v(180.25, 190.46) * mm});
            skLineSegment(sketch, "E5142", {"start": v(180.25, 190.46) * mm, "end": v(180.3, 190.3) * mm});
            skLineSegment(sketch, "E5143", {"start": v(180.3, 190.3) * mm, "end": v(180.2, 190.6) * mm});
            skLineSegment(sketch, "E5144", {"start": v(229.65, 190.16) * mm, "end": v(229.7, 190.3) * mm});
            skLineSegment(sketch, "E5145", {"start": v(229.7, 190.3) * mm, "end": v(229.58, 190.02) * mm});
            skLineSegment(sketch, "E5146", {"start": v(229.58, 190.02) * mm, "end": v(229.65, 190.16) * mm});
            skLineSegment(sketch, "E5147", {"start": v(180.42, 190.02) * mm, "end": v(180.48, 189.87) * mm});
            skLineSegment(sketch, "E5148", {"start": v(180.48, 189.87) * mm, "end": v(180.55, 189.73) * mm});
            skLineSegment(sketch, "E5149", {"start": v(180.55, 189.73) * mm, "end": v(180.42, 190.02) * mm});
            skLineSegment(sketch, "E5150", {"start": v(229.38, 189.6) * mm, "end": v(229.45, 189.73) * mm});
            skLineSegment(sketch, "E5151", {"start": v(229.45, 189.73) * mm, "end": v(229.3, 189.46) * mm});
            skLineSegment(sketch, "E5152", {"start": v(229.3, 189.46) * mm, "end": v(229.38, 189.6) * mm});
            skLineSegment(sketch, "E5153", {"start": v(180.7, 189.46) * mm, "end": v(180.78, 189.32) * mm});
            skLineSegment(sketch, "E5154", {"start": v(180.78, 189.32) * mm, "end": v(180.87, 189.2) * mm});
            skLineSegment(sketch, "E5155", {"start": v(180.87, 189.2) * mm, "end": v(180.7, 189.46) * mm});
            skLineSegment(sketch, "E5156", {"start": v(229.04, 189.06) * mm, "end": v(229.13, 189.2) * mm});
            skLineSegment(sketch, "E5157", {"start": v(229.13, 189.2) * mm, "end": v(228.95, 188.94) * mm});
            skLineSegment(sketch, "E5158", {"start": v(228.95, 188.94) * mm, "end": v(229.04, 189.06) * mm});
            skLineSegment(sketch, "E5159", {"start": v(181.06, 188.94) * mm, "end": v(181.15, 188.81) * mm});
            skLineSegment(sketch, "E5160", {"start": v(181.15, 188.81) * mm, "end": v(181.25, 188.7) * mm});
            skLineSegment(sketch, "E5161", {"start": v(181.25, 188.7) * mm, "end": v(181.06, 188.94) * mm});
            skLineSegment(sketch, "E5162", {"start": v(228.65, 188.58) * mm, "end": v(228.75, 188.7) * mm});
            skLineSegment(sketch, "E5163", {"start": v(228.75, 188.7) * mm, "end": v(228.53, 188.47) * mm});
            skLineSegment(sketch, "E5164", {"start": v(228.53, 188.47) * mm, "end": v(228.65, 188.58) * mm});
            skLineSegment(sketch, "E5165", {"start": v(181.47, 188.47) * mm, "end": v(181.58, 188.35) * mm});
            skLineSegment(sketch, "E5166", {"start": v(181.58, 188.35) * mm, "end": v(181.7, 188.25) * mm});
            skLineSegment(sketch, "E5167", {"start": v(181.7, 188.25) * mm, "end": v(181.47, 188.47) * mm});
            skLineSegment(sketch, "E5168", {"start": v(228.19, 188.15) * mm, "end": v(228.3, 188.25) * mm});
            skLineSegment(sketch, "E5169", {"start": v(228.3, 188.25) * mm, "end": v(228.06, 188.06) * mm});
            skLineSegment(sketch, "E5170", {"start": v(228.06, 188.06) * mm, "end": v(228.19, 188.15) * mm});
            skLineSegment(sketch, "E5171", {"start": v(181.94, 188.06) * mm, "end": v(182.06, 187.96) * mm});
            skLineSegment(sketch, "E5172", {"start": v(182.06, 187.96) * mm, "end": v(182.2, 187.87) * mm});
            skLineSegment(sketch, "E5173", {"start": v(182.2, 187.87) * mm, "end": v(181.94, 188.06) * mm});
            skLineSegment(sketch, "E5174", {"start": v(227.68, 187.78) * mm, "end": v(227.8, 187.87) * mm});
            skLineSegment(sketch, "E5175", {"start": v(227.8, 187.87) * mm, "end": v(227.54, 187.7) * mm});
            skLineSegment(sketch, "E5176", {"start": v(227.54, 187.7) * mm, "end": v(227.68, 187.78) * mm});
            skLineSegment(sketch, "E5177", {"start": v(182.46, 187.7) * mm, "end": v(182.6, 187.62) * mm});
            skLineSegment(sketch, "E5178", {"start": v(182.6, 187.62) * mm, "end": v(182.73, 187.55) * mm});
            skLineSegment(sketch, "E5179", {"start": v(182.73, 187.55) * mm, "end": v(182.46, 187.7) * mm});
            skLineSegment(sketch, "E5180", {"start": v(227.13, 187.48) * mm, "end": v(227.27, 187.55) * mm});
            skLineSegment(sketch, "E5181", {"start": v(227.27, 187.55) * mm, "end": v(226.98, 187.42) * mm});
            skLineSegment(sketch, "E5182", {"start": v(226.98, 187.42) * mm, "end": v(227.13, 187.48) * mm});
            skLineSegment(sketch, "E5183", {"start": v(183.02, 187.42) * mm, "end": v(183.16, 187.35) * mm});
            skLineSegment(sketch, "E5184", {"start": v(183.16, 187.35) * mm, "end": v(183.3, 187.3) * mm});
            skLineSegment(sketch, "E5185", {"start": v(183.3, 187.3) * mm, "end": v(183.02, 187.42) * mm});
            skLineSegment(sketch, "E5186", {"start": v(226.54, 187.25) * mm, "end": v(226.7, 187.3) * mm});
            skLineSegment(sketch, "E5187", {"start": v(226.7, 187.3) * mm, "end": v(226.4, 187.2) * mm});
            skLineSegment(sketch, "E5188", {"start": v(226.4, 187.2) * mm, "end": v(226.54, 187.25) * mm});
            skLineSegment(sketch, "E5189", {"start": v(183.6, 187.2) * mm, "end": v(183.76, 187.16) * mm});
            skLineSegment(sketch, "E5190", {"start": v(183.76, 187.16) * mm, "end": v(183.91, 187.13) * mm});
            skLineSegment(sketch, "E5191", {"start": v(183.91, 187.13) * mm, "end": v(183.6, 187.2) * mm});
            skLineSegment(sketch, "E5192", {"start": v(225.94, 187.09) * mm, "end": v(226.09, 187.13) * mm});
            skLineSegment(sketch, "E5193", {"start": v(226.09, 187.13) * mm, "end": v(225.78, 187.07) * mm});
            skLineSegment(sketch, "E5194", {"start": v(225.78, 187.07) * mm, "end": v(225.94, 187.09) * mm});
            skLineSegment(sketch, "E5195", {"start": v(184.22, 187.07) * mm, "end": v(184.37, 187.04) * mm});
            skLineSegment(sketch, "E5196", {"start": v(184.37, 187.04) * mm, "end": v(184.53, 187.03) * mm});
            skLineSegment(sketch, "E5197", {"start": v(184.53, 187.03) * mm, "end": v(184.22, 187.07) * mm});
            skLineSegment(sketch, "E5198", {"start": v(225.47, 187.03) * mm, "end": v(225.16, 187) * mm});
            skLineSegment(sketch, "E5199", {"start": v(225.16, 187) * mm, "end": v(225.31, 187) * mm});
            skLineSegment(sketch, "E5200", {"start": v(225.31, 187) * mm, "end": v(225.47, 187.03) * mm});
            skLineSegment(sketch, "E5201", {"start": v(185, 187) * mm, "end": v(184.84, 187) * mm});
            skLineSegment(sketch, "E5202", {"start": v(184.84, 187) * mm, "end": v(185, 187) * mm});
            skLineSegment(sketch, "E5203", {"start": v(185, 187) * mm, "end": v(185, 187) * mm});
            skLineSegment(sketch, "E5204", {"start": v(214.3, -92.27) * mm, "end": v(214.97, -92.1) * mm});
            skLineSegment(sketch, "E5205", {"start": v(214.97, -92.1) * mm, "end": v(215.66, -92.01) * mm});
            skLineSegment(sketch, "E5206", {"start": v(215.66, -92.01) * mm, "end": v(216, -92.01) * mm});
            skLineSegment(sketch, "E5207", {"start": v(216, -92.01) * mm, "end": v(216, -92) * mm});
            skLineSegment(sketch, "E5208", {"start": v(216, -92) * mm, "end": v(292.92, -92) * mm});
            skLineSegment(sketch, "E5209", {"start": v(292.92, -92) * mm, "end": v(293.23, -91.06) * mm});
            skLineSegment(sketch, "E5210", {"start": v(293.23, -91.06) * mm, "end": v(294.17, -89.07) * mm});
            skLineSegment(sketch, "E5211", {"start": v(294.17, -89.07) * mm, "end": v(295.34, -87.21) * mm});
            skLineSegment(sketch, "E5212", {"start": v(295.34, -87.21) * mm, "end": v(296.74, -85.52) * mm});
            skLineSegment(sketch, "E5213", {"start": v(296.74, -85.52) * mm, "end": v(298.35, -84.02) * mm});
            skLineSegment(sketch, "E5214", {"start": v(298.35, -84.02) * mm, "end": v(300.12, -82.72) * mm});
            skLineSegment(sketch, "E5215", {"start": v(300.12, -82.72) * mm, "end": v(302.05, -81.67) * mm});
            skLineSegment(sketch, "E5216", {"start": v(302.05, -81.67) * mm, "end": v(304, -80.9) * mm});
            skLineSegment(sketch, "E5217", {"start": v(304, -80.9) * mm, "end": v(304, -4) * mm});
            skLineSegment(sketch, "E5218", {"start": v(304, -4) * mm, "end": v(304.01, -4) * mm});
            skLineSegment(sketch, "E5219", {"start": v(304.01, -4) * mm, "end": v(304.01, -3.65) * mm});
            skLineSegment(sketch, "E5220", {"start": v(304.01, -3.65) * mm, "end": v(304.1, -2.97) * mm});
            skLineSegment(sketch, "E5221", {"start": v(304.1, -2.97) * mm, "end": v(304.27, -2.3) * mm});
            skLineSegment(sketch, "E5222", {"start": v(304.27, -2.3) * mm, "end": v(304.53, -1.65) * mm});
            skLineSegment(sketch, "E5223", {"start": v(304.53, -1.65) * mm, "end": v(304.14, -1.44) * mm});
            skLineSegment(sketch, "E5224", {"start": v(304.14, -1.44) * mm, "end": v(303.13, -0.7) * mm});
            skLineSegment(sketch, "E5225", {"start": v(303.13, -0.7) * mm, "end": v(302.2, 0.15) * mm});
            skLineSegment(sketch, "E5226", {"start": v(302.2, 0.15) * mm, "end": v(301.41, 1.12) * mm});
            skLineSegment(sketch, "E5227", {"start": v(301.41, 1.12) * mm, "end": v(300.74, 2.18) * mm});
            skLineSegment(sketch, "E5228", {"start": v(300.74, 2.18) * mm, "end": v(300.2, 3.32) * mm});
            skLineSegment(sketch, "E5229", {"start": v(300.2, 3.32) * mm, "end": v(299.81, 4.51) * mm});
            skLineSegment(sketch, "E5230", {"start": v(299.81, 4.51) * mm, "end": v(299.58, 5.75) * mm});
            skLineSegment(sketch, "E5231", {"start": v(299.58, 5.75) * mm, "end": v(299.5, 7) * mm});
            skLineSegment(sketch, "E5232", {"start": v(299.5, 7) * mm, "end": v(299.58, 8.25) * mm});
            skLineSegment(sketch, "E5233", {"start": v(299.58, 8.25) * mm, "end": v(299.81, 9.49) * mm});
            skLineSegment(sketch, "E5234", {"start": v(299.81, 9.49) * mm, "end": v(300.2, 10.68) * mm});
            skLineSegment(sketch, "E5235", {"start": v(300.2, 10.68) * mm, "end": v(300.74, 11.82) * mm});
            skLineSegment(sketch, "E5236", {"start": v(300.74, 11.82) * mm, "end": v(301.41, 12.88) * mm});
            skLineSegment(sketch, "E5237", {"start": v(301.41, 12.88) * mm, "end": v(302.2, 13.85) * mm});
            skLineSegment(sketch, "E5238", {"start": v(302.2, 13.85) * mm, "end": v(303.13, 14.7) * mm});
            skLineSegment(sketch, "E5239", {"start": v(303.13, 14.7) * mm, "end": v(304.14, 15.44) * mm});
            skLineSegment(sketch, "E5240", {"start": v(304.14, 15.44) * mm, "end": v(304.53, 15.65) * mm});
            skLineSegment(sketch, "E5241", {"start": v(304.53, 15.65) * mm, "end": v(304.27, 16.3) * mm});
            skLineSegment(sketch, "E5242", {"start": v(304.27, 16.3) * mm, "end": v(304.1, 16.97) * mm});
            skLineSegment(sketch, "E5243", {"start": v(304.1, 16.97) * mm, "end": v(304.01, 17.66) * mm});
            skLineSegment(sketch, "E5244", {"start": v(304.01, 17.66) * mm, "end": v(304.01, 18) * mm});
            skLineSegment(sketch, "E5245", {"start": v(304.01, 18) * mm, "end": v(304, 18) * mm});
            skLineSegment(sketch, "E5246", {"start": v(304, 18) * mm, "end": v(304, 94.9) * mm});
            skLineSegment(sketch, "E5247", {"start": v(304, 94.9) * mm, "end": v(302.05, 95.67) * mm});
            skLineSegment(sketch, "E5248", {"start": v(302.05, 95.67) * mm, "end": v(300.12, 96.72) * mm});
            skLineSegment(sketch, "E5249", {"start": v(300.12, 96.72) * mm, "end": v(298.35, 98.02) * mm});
            skLineSegment(sketch, "E5250", {"start": v(298.35, 98.02) * mm, "end": v(296.74, 99.52) * mm});
            skLineSegment(sketch, "E5251", {"start": v(296.74, 99.52) * mm, "end": v(295.34, 101.21) * mm});
            skLineSegment(sketch, "E5252", {"start": v(295.34, 101.21) * mm, "end": v(294.17, 103.07) * mm});
            skLineSegment(sketch, "E5253", {"start": v(294.17, 103.07) * mm, "end": v(293.23, 105.06) * mm});
            skLineSegment(sketch, "E5254", {"start": v(293.23, 105.06) * mm, "end": v(292.92, 106) * mm});
            skLineSegment(sketch, "E5255", {"start": v(292.92, 106) * mm, "end": v(117.08, 106) * mm});
            skLineSegment(sketch, "E5256", {"start": v(117.08, 106) * mm, "end": v(116.77, 105.06) * mm});
            skLineSegment(sketch, "E5257", {"start": v(116.77, 105.06) * mm, "end": v(115.83, 103.07) * mm});
            skLineSegment(sketch, "E5258", {"start": v(115.83, 103.07) * mm, "end": v(114.66, 101.21) * mm});
            skLineSegment(sketch, "E5259", {"start": v(114.66, 101.21) * mm, "end": v(113.26, 99.52) * mm});
            skLineSegment(sketch, "E5260", {"start": v(113.26, 99.52) * mm, "end": v(111.66, 98.02) * mm});
            skLineSegment(sketch, "E5261", {"start": v(111.66, 98.02) * mm, "end": v(109.88, 96.72) * mm});
            skLineSegment(sketch, "E5262", {"start": v(109.88, 96.72) * mm, "end": v(107.95, 95.67) * mm});
            skLineSegment(sketch, "E5263", {"start": v(107.95, 95.67) * mm, "end": v(106, 94.9) * mm});
            skLineSegment(sketch, "E5264", {"start": v(106, 94.9) * mm, "end": v(106, -80.9) * mm});
            skLineSegment(sketch, "E5265", {"start": v(106, -80.9) * mm, "end": v(107.95, -81.67) * mm});
            skLineSegment(sketch, "E5266", {"start": v(107.95, -81.67) * mm, "end": v(109.88, -82.72) * mm});
            skLineSegment(sketch, "E5267", {"start": v(109.88, -82.72) * mm, "end": v(111.66, -84.02) * mm});
            skLineSegment(sketch, "E5268", {"start": v(111.66, -84.02) * mm, "end": v(113.26, -85.52) * mm});
            skLineSegment(sketch, "E5269", {"start": v(113.26, -85.52) * mm, "end": v(114.66, -87.21) * mm});
            skLineSegment(sketch, "E5270", {"start": v(114.66, -87.21) * mm, "end": v(115.83, -89.07) * mm});
            skLineSegment(sketch, "E5271", {"start": v(115.83, -89.07) * mm, "end": v(116.77, -91.06) * mm});
            skLineSegment(sketch, "E5272", {"start": v(116.77, -91.06) * mm, "end": v(117.08, -92) * mm});
            skLineSegment(sketch, "E5273", {"start": v(117.08, -92) * mm, "end": v(194, -92) * mm});
            skLineSegment(sketch, "E5274", {"start": v(194, -92) * mm, "end": v(194, -92.01) * mm});
            skLineSegment(sketch, "E5275", {"start": v(194, -92.01) * mm, "end": v(194.34, -92.01) * mm});
            skLineSegment(sketch, "E5276", {"start": v(194.34, -92.01) * mm, "end": v(195.03, -92.1) * mm});
            skLineSegment(sketch, "E5277", {"start": v(195.03, -92.1) * mm, "end": v(195.7, -92.27) * mm});
            skLineSegment(sketch, "E5278", {"start": v(195.7, -92.27) * mm, "end": v(196.34, -92.52) * mm});
            skLineSegment(sketch, "E5279", {"start": v(196.34, -92.52) * mm, "end": v(196.9, -91.62) * mm});
            skLineSegment(sketch, "E5280", {"start": v(196.9, -91.62) * mm, "end": v(197.71, -90.66) * mm});
            skLineSegment(sketch, "E5281", {"start": v(197.71, -90.66) * mm, "end": v(198.63, -89.8) * mm});
            skLineSegment(sketch, "E5282", {"start": v(198.63, -89.8) * mm, "end": v(199.64, -89.06) * mm});
            skLineSegment(sketch, "E5283", {"start": v(199.64, -89.06) * mm, "end": v(200.74, -88.45) * mm});
            skLineSegment(sketch, "E5284", {"start": v(200.74, -88.45) * mm, "end": v(201.9, -87.99) * mm});
            skLineSegment(sketch, "E5285", {"start": v(201.9, -87.99) * mm, "end": v(203.13, -87.68) * mm});
            skLineSegment(sketch, "E5286", {"start": v(203.13, -87.68) * mm, "end": v(204.37, -87.52) * mm});
            skLineSegment(sketch, "E5287", {"start": v(204.37, -87.52) * mm, "end": v(205.63, -87.52) * mm});
            skLineSegment(sketch, "E5288", {"start": v(205.63, -87.52) * mm, "end": v(206.87, -87.68) * mm});
            skLineSegment(sketch, "E5289", {"start": v(206.87, -87.68) * mm, "end": v(208.1, -87.99) * mm});
            skLineSegment(sketch, "E5290", {"start": v(208.1, -87.99) * mm, "end": v(209.26, -88.45) * mm});
            skLineSegment(sketch, "E5291", {"start": v(209.26, -88.45) * mm, "end": v(210.36, -89.06) * mm});
            skLineSegment(sketch, "E5292", {"start": v(210.36, -89.06) * mm, "end": v(211.37, -89.8) * mm});
            skLineSegment(sketch, "E5293", {"start": v(211.37, -89.8) * mm, "end": v(212.3, -90.66) * mm});
            skLineSegment(sketch, "E5294", {"start": v(212.3, -90.66) * mm, "end": v(213.1, -91.62) * mm});
            skLineSegment(sketch, "E5295", {"start": v(213.1, -91.62) * mm, "end": v(213.66, -92.52) * mm});
            skLineSegment(sketch, "E5296", {"start": v(213.66, -92.52) * mm, "end": v(214.3, -92.27) * mm});
            skLineSegment(sketch, "E5297", {"start": v(204.66, 33.43) * mm, "end": v(203.97, 33.52) * mm});
            skLineSegment(sketch, "E5298", {"start": v(203.97, 33.52) * mm, "end": v(203.3, 33.69) * mm});
            skLineSegment(sketch, "E5299", {"start": v(203.3, 33.69) * mm, "end": v(202.66, 33.94) * mm});
            skLineSegment(sketch, "E5300", {"start": v(202.66, 33.94) * mm, "end": v(202.05, 34.28) * mm});
            skLineSegment(sketch, "E5301", {"start": v(202.05, 34.28) * mm, "end": v(201.5, 34.68) * mm});
            skLineSegment(sketch, "E5302", {"start": v(201.5, 34.68) * mm, "end": v(201, 35.16) * mm});
            skLineSegment(sketch, "E5303", {"start": v(201, 35.16) * mm, "end": v(150.41, 85.73) * mm});
            skLineSegment(sketch, "E5304", {"start": v(150.41, 85.73) * mm, "end": v(149.97, 86.27) * mm});
            skLineSegment(sketch, "E5305", {"start": v(149.97, 86.27) * mm, "end": v(149.6, 86.85) * mm});
            skLineSegment(sketch, "E5306", {"start": v(149.6, 86.85) * mm, "end": v(149.3, 87.47) * mm});
            skLineSegment(sketch, "E5307", {"start": v(149.3, 87.47) * mm, "end": v(149.1, 88.13) * mm});
            skLineSegment(sketch, "E5308", {"start": v(149.1, 88.13) * mm, "end": v(148.96, 88.81) * mm});
            skLineSegment(sketch, "E5309", {"start": v(148.96, 88.81) * mm, "end": v(148.92, 89.5) * mm});
            skLineSegment(sketch, "E5310", {"start": v(148.92, 89.5) * mm, "end": v(148.96, 90.19) * mm});
            skLineSegment(sketch, "E5311", {"start": v(148.96, 90.19) * mm, "end": v(149.1, 90.87) * mm});
            skLineSegment(sketch, "E5312", {"start": v(149.1, 90.87) * mm, "end": v(149.3, 91.53) * mm});
            skLineSegment(sketch, "E5313", {"start": v(149.3, 91.53) * mm, "end": v(149.6, 92.15) * mm});
            skLineSegment(sketch, "E5314", {"start": v(149.6, 92.15) * mm, "end": v(149.97, 92.73) * mm});
            skLineSegment(sketch, "E5315", {"start": v(149.97, 92.73) * mm, "end": v(150.41, 93.27) * mm});
            skLineSegment(sketch, "E5316", {"start": v(150.41, 93.27) * mm, "end": v(150.91, 93.74) * mm});
            skLineSegment(sketch, "E5317", {"start": v(150.91, 93.74) * mm, "end": v(151.47, 94.14) * mm});
            skLineSegment(sketch, "E5318", {"start": v(151.47, 94.14) * mm, "end": v(152.08, 94.48) * mm});
            skLineSegment(sketch, "E5319", {"start": v(152.08, 94.48) * mm, "end": v(152.72, 94.73) * mm});
            skLineSegment(sketch, "E5320", {"start": v(152.72, 94.73) * mm, "end": v(153.39, 94.9) * mm});
            skLineSegment(sketch, "E5321", {"start": v(153.39, 94.9) * mm, "end": v(154.07, 94.99) * mm});
            skLineSegment(sketch, "E5322", {"start": v(154.07, 94.99) * mm, "end": v(255.93, 94.99) * mm});
            skLineSegment(sketch, "E5323", {"start": v(255.93, 94.99) * mm, "end": v(256.6, 94.9) * mm});
            skLineSegment(sketch, "E5324", {"start": v(256.6, 94.9) * mm, "end": v(257.28, 94.73) * mm});
            skLineSegment(sketch, "E5325", {"start": v(257.28, 94.73) * mm, "end": v(257.92, 94.48) * mm});
            skLineSegment(sketch, "E5326", {"start": v(257.92, 94.48) * mm, "end": v(258.53, 94.14) * mm});
            skLineSegment(sketch, "E5327", {"start": v(258.53, 94.14) * mm, "end": v(259.09, 93.74) * mm});
            skLineSegment(sketch, "E5328", {"start": v(259.09, 93.74) * mm, "end": v(259.59, 93.27) * mm});
            skLineSegment(sketch, "E5329", {"start": v(259.59, 93.27) * mm, "end": v(260.03, 92.73) * mm});
            skLineSegment(sketch, "E5330", {"start": v(260.03, 92.73) * mm, "end": v(260.4, 92.15) * mm});
            skLineSegment(sketch, "E5331", {"start": v(260.4, 92.15) * mm, "end": v(260.7, 91.53) * mm});
            skLineSegment(sketch, "E5332", {"start": v(260.7, 91.53) * mm, "end": v(260.9, 90.87) * mm});
            skLineSegment(sketch, "E5333", {"start": v(260.9, 90.87) * mm, "end": v(261.04, 90.19) * mm});
            skLineSegment(sketch, "E5334", {"start": v(261.04, 90.19) * mm, "end": v(261.08, 89.5) * mm});
            skLineSegment(sketch, "E5335", {"start": v(261.08, 89.5) * mm, "end": v(261.04, 88.81) * mm});
            skLineSegment(sketch, "E5336", {"start": v(261.04, 88.81) * mm, "end": v(260.9, 88.13) * mm});
            skLineSegment(sketch, "E5337", {"start": v(260.9, 88.13) * mm, "end": v(260.7, 87.47) * mm});
            skLineSegment(sketch, "E5338", {"start": v(260.7, 87.47) * mm, "end": v(260.4, 86.85) * mm});
            skLineSegment(sketch, "E5339", {"start": v(260.4, 86.85) * mm, "end": v(260.03, 86.27) * mm});
            skLineSegment(sketch, "E5340", {"start": v(260.03, 86.27) * mm, "end": v(259.59, 85.73) * mm});
            skLineSegment(sketch, "E5341", {"start": v(259.59, 85.73) * mm, "end": v(209, 35.16) * mm});
            skLineSegment(sketch, "E5342", {"start": v(209, 35.16) * mm, "end": v(208.5, 34.68) * mm});
            skLineSegment(sketch, "E5343", {"start": v(208.5, 34.68) * mm, "end": v(207.95, 34.28) * mm});
            skLineSegment(sketch, "E5344", {"start": v(207.95, 34.28) * mm, "end": v(207.34, 33.94) * mm});
            skLineSegment(sketch, "E5345", {"start": v(207.34, 33.94) * mm, "end": v(206.7, 33.69) * mm});
            skLineSegment(sketch, "E5346", {"start": v(206.7, 33.69) * mm, "end": v(206.03, 33.52) * mm});
            skLineSegment(sketch, "E5347", {"start": v(206.03, 33.52) * mm, "end": v(205.34, 33.43) * mm});
            skLineSegment(sketch, "E5348", {"start": v(205.34, 33.43) * mm, "end": v(204.66, 33.43) * mm});
            skLineSegment(sketch, "E5349", {"start": v(137.9, 60.5) * mm, "end": v(137.72, 60.53) * mm});
            skLineSegment(sketch, "E5350", {"start": v(137.72, 60.53) * mm, "end": v(137.54, 60.57) * mm});
            skLineSegment(sketch, "E5351", {"start": v(137.54, 60.57) * mm, "end": v(137.36, 60.64) * mm});
            skLineSegment(sketch, "E5352", {"start": v(137.36, 60.64) * mm, "end": v(137.2, 60.73) * mm});
            skLineSegment(sketch, "E5353", {"start": v(137.2, 60.73) * mm, "end": v(137.04, 60.84) * mm});
            skLineSegment(sketch, "E5354", {"start": v(137.04, 60.84) * mm, "end": v(136.9, 60.97) * mm});
            skLineSegment(sketch, "E5355", {"start": v(136.9, 60.97) * mm, "end": v(136.79, 61.12) * mm});
            skLineSegment(sketch, "E5356", {"start": v(136.79, 61.12) * mm, "end": v(136.69, 61.28) * mm});
            skLineSegment(sketch, "E5357", {"start": v(136.69, 61.28) * mm, "end": v(136.6, 61.45) * mm});
            skLineSegment(sketch, "E5358", {"start": v(136.6, 61.45) * mm, "end": v(136.55, 61.63) * mm});
            skLineSegment(sketch, "E5359", {"start": v(136.55, 61.63) * mm, "end": v(136.51, 61.81) * mm});
            skLineSegment(sketch, "E5360", {"start": v(136.51, 61.81) * mm, "end": v(136.5, 62) * mm});
            skLineSegment(sketch, "E5361", {"start": v(136.5, 62) * mm, "end": v(136.51, 62.19) * mm});
            skLineSegment(sketch, "E5362", {"start": v(136.51, 62.19) * mm, "end": v(136.55, 62.37) * mm});
            skLineSegment(sketch, "E5363", {"start": v(136.55, 62.37) * mm, "end": v(136.6, 62.55) * mm});
            skLineSegment(sketch, "E5364", {"start": v(136.6, 62.55) * mm, "end": v(136.69, 62.72) * mm});
            skLineSegment(sketch, "E5365", {"start": v(136.69, 62.72) * mm, "end": v(136.79, 62.88) * mm});
            skLineSegment(sketch, "E5366", {"start": v(136.79, 62.88) * mm, "end": v(136.9, 63.03) * mm});
            skLineSegment(sketch, "E5367", {"start": v(136.9, 63.03) * mm, "end": v(137.04, 63.16) * mm});
            skLineSegment(sketch, "E5368", {"start": v(137.04, 63.16) * mm, "end": v(137.2, 63.27) * mm});
            skLineSegment(sketch, "E5369", {"start": v(137.2, 63.27) * mm, "end": v(137.36, 63.36) * mm});
            skLineSegment(sketch, "E5370", {"start": v(137.36, 63.36) * mm, "end": v(137.54, 63.43) * mm});
            skLineSegment(sketch, "E5371", {"start": v(137.54, 63.43) * mm, "end": v(137.72, 63.47) * mm});
            skLineSegment(sketch, "E5372", {"start": v(137.72, 63.47) * mm, "end": v(137.9, 63.5) * mm});
            skLineSegment(sketch, "E5373", {"start": v(137.9, 63.5) * mm, "end": v(138.1, 63.5) * mm});
            skLineSegment(sketch, "E5374", {"start": v(138.1, 63.5) * mm, "end": v(138.28, 63.47) * mm});
            skLineSegment(sketch, "E5375", {"start": v(138.28, 63.47) * mm, "end": v(138.46, 63.43) * mm});
            skLineSegment(sketch, "E5376", {"start": v(138.46, 63.43) * mm, "end": v(138.64, 63.36) * mm});
            skLineSegment(sketch, "E5377", {"start": v(138.64, 63.36) * mm, "end": v(138.8, 63.27) * mm});
            skLineSegment(sketch, "E5378", {"start": v(138.8, 63.27) * mm, "end": v(138.96, 63.16) * mm});
            skLineSegment(sketch, "E5379", {"start": v(138.96, 63.16) * mm, "end": v(139.1, 63.03) * mm});
            skLineSegment(sketch, "E5380", {"start": v(139.1, 63.03) * mm, "end": v(139.21, 62.88) * mm});
            skLineSegment(sketch, "E5381", {"start": v(139.21, 62.88) * mm, "end": v(139.31, 62.72) * mm});
            skLineSegment(sketch, "E5382", {"start": v(139.31, 62.72) * mm, "end": v(139.4, 62.55) * mm});
            skLineSegment(sketch, "E5383", {"start": v(139.4, 62.55) * mm, "end": v(139.45, 62.37) * mm});
            skLineSegment(sketch, "E5384", {"start": v(139.45, 62.37) * mm, "end": v(139.49, 62.19) * mm});
            skLineSegment(sketch, "E5385", {"start": v(139.49, 62.19) * mm, "end": v(139.5, 62) * mm});
            skLineSegment(sketch, "E5386", {"start": v(139.5, 62) * mm, "end": v(139.49, 61.81) * mm});
            skLineSegment(sketch, "E5387", {"start": v(139.49, 61.81) * mm, "end": v(139.45, 61.63) * mm});
            skLineSegment(sketch, "E5388", {"start": v(139.45, 61.63) * mm, "end": v(139.4, 61.45) * mm});
            skLineSegment(sketch, "E5389", {"start": v(139.4, 61.45) * mm, "end": v(139.31, 61.28) * mm});
            skLineSegment(sketch, "E5390", {"start": v(139.31, 61.28) * mm, "end": v(139.21, 61.12) * mm});
            skLineSegment(sketch, "E5391", {"start": v(139.21, 61.12) * mm, "end": v(139.1, 60.97) * mm});
            skLineSegment(sketch, "E5392", {"start": v(139.1, 60.97) * mm, "end": v(138.96, 60.84) * mm});
            skLineSegment(sketch, "E5393", {"start": v(138.96, 60.84) * mm, "end": v(138.8, 60.73) * mm});
            skLineSegment(sketch, "E5394", {"start": v(138.8, 60.73) * mm, "end": v(138.64, 60.64) * mm});
            skLineSegment(sketch, "E5395", {"start": v(138.64, 60.64) * mm, "end": v(138.46, 60.57) * mm});
            skLineSegment(sketch, "E5396", {"start": v(138.46, 60.57) * mm, "end": v(138.28, 60.53) * mm});
            skLineSegment(sketch, "E5397", {"start": v(138.28, 60.53) * mm, "end": v(138.1, 60.5) * mm});
            skLineSegment(sketch, "E5398", {"start": v(138.1, 60.5) * mm, "end": v(137.9, 60.5) * mm});
            skLineSegment(sketch, "E5399", {"start": v(161.9, 60.5) * mm, "end": v(161.72, 60.53) * mm});
            skLineSegment(sketch, "E5400", {"start": v(161.72, 60.53) * mm, "end": v(161.54, 60.57) * mm});
            skLineSegment(sketch, "E5401", {"start": v(161.54, 60.57) * mm, "end": v(161.36, 60.64) * mm});
            skLineSegment(sketch, "E5402", {"start": v(161.36, 60.64) * mm, "end": v(161.2, 60.73) * mm});
            skLineSegment(sketch, "E5403", {"start": v(161.2, 60.73) * mm, "end": v(161.04, 60.84) * mm});
            skLineSegment(sketch, "E5404", {"start": v(161.04, 60.84) * mm, "end": v(160.9, 60.97) * mm});
            skLineSegment(sketch, "E5405", {"start": v(160.9, 60.97) * mm, "end": v(160.79, 61.12) * mm});
            skLineSegment(sketch, "E5406", {"start": v(160.79, 61.12) * mm, "end": v(160.69, 61.28) * mm});
            skLineSegment(sketch, "E5407", {"start": v(160.69, 61.28) * mm, "end": v(160.6, 61.45) * mm});
            skLineSegment(sketch, "E5408", {"start": v(160.6, 61.45) * mm, "end": v(160.55, 61.63) * mm});
            skLineSegment(sketch, "E5409", {"start": v(160.55, 61.63) * mm, "end": v(160.51, 61.81) * mm});
            skLineSegment(sketch, "E5410", {"start": v(160.51, 61.81) * mm, "end": v(160.5, 62) * mm});
            skLineSegment(sketch, "E5411", {"start": v(160.5, 62) * mm, "end": v(160.51, 62.19) * mm});
            skLineSegment(sketch, "E5412", {"start": v(160.51, 62.19) * mm, "end": v(160.55, 62.37) * mm});
            skLineSegment(sketch, "E5413", {"start": v(160.55, 62.37) * mm, "end": v(160.6, 62.55) * mm});
            skLineSegment(sketch, "E5414", {"start": v(160.6, 62.55) * mm, "end": v(160.69, 62.72) * mm});
            skLineSegment(sketch, "E5415", {"start": v(160.69, 62.72) * mm, "end": v(160.79, 62.88) * mm});
            skLineSegment(sketch, "E5416", {"start": v(160.79, 62.88) * mm, "end": v(160.9, 63.03) * mm});
            skLineSegment(sketch, "E5417", {"start": v(160.9, 63.03) * mm, "end": v(161.04, 63.16) * mm});
            skLineSegment(sketch, "E5418", {"start": v(161.04, 63.16) * mm, "end": v(161.2, 63.27) * mm});
            skLineSegment(sketch, "E5419", {"start": v(161.2, 63.27) * mm, "end": v(161.36, 63.36) * mm});
            skLineSegment(sketch, "E5420", {"start": v(161.36, 63.36) * mm, "end": v(161.54, 63.43) * mm});
            skLineSegment(sketch, "E5421", {"start": v(161.54, 63.43) * mm, "end": v(161.72, 63.47) * mm});
            skLineSegment(sketch, "E5422", {"start": v(161.72, 63.47) * mm, "end": v(161.9, 63.5) * mm});
            skLineSegment(sketch, "E5423", {"start": v(161.9, 63.5) * mm, "end": v(162.1, 63.5) * mm});
            skLineSegment(sketch, "E5424", {"start": v(162.1, 63.5) * mm, "end": v(162.28, 63.47) * mm});
            skLineSegment(sketch, "E5425", {"start": v(162.28, 63.47) * mm, "end": v(162.46, 63.43) * mm});
            skLineSegment(sketch, "E5426", {"start": v(162.46, 63.43) * mm, "end": v(162.64, 63.36) * mm});
            skLineSegment(sketch, "E5427", {"start": v(162.64, 63.36) * mm, "end": v(162.8, 63.27) * mm});
            skLineSegment(sketch, "E5428", {"start": v(162.8, 63.27) * mm, "end": v(162.96, 63.16) * mm});
            skLineSegment(sketch, "E5429", {"start": v(162.96, 63.16) * mm, "end": v(163.1, 63.03) * mm});
            skLineSegment(sketch, "E5430", {"start": v(163.1, 63.03) * mm, "end": v(163.21, 62.88) * mm});
            skLineSegment(sketch, "E5431", {"start": v(163.21, 62.88) * mm, "end": v(163.31, 62.72) * mm});
            skLineSegment(sketch, "E5432", {"start": v(163.31, 62.72) * mm, "end": v(163.4, 62.55) * mm});
            skLineSegment(sketch, "E5433", {"start": v(163.4, 62.55) * mm, "end": v(163.45, 62.37) * mm});
            skLineSegment(sketch, "E5434", {"start": v(163.45, 62.37) * mm, "end": v(163.49, 62.19) * mm});
            skLineSegment(sketch, "E5435", {"start": v(163.49, 62.19) * mm, "end": v(163.5, 62) * mm});
            skLineSegment(sketch, "E5436", {"start": v(163.5, 62) * mm, "end": v(163.49, 61.81) * mm});
            skLineSegment(sketch, "E5437", {"start": v(163.49, 61.81) * mm, "end": v(163.45, 61.63) * mm});
            skLineSegment(sketch, "E5438", {"start": v(163.45, 61.63) * mm, "end": v(163.4, 61.45) * mm});
            skLineSegment(sketch, "E5439", {"start": v(163.4, 61.45) * mm, "end": v(163.31, 61.28) * mm});
            skLineSegment(sketch, "E5440", {"start": v(163.31, 61.28) * mm, "end": v(163.21, 61.12) * mm});
            skLineSegment(sketch, "E5441", {"start": v(163.21, 61.12) * mm, "end": v(163.1, 60.97) * mm});
            skLineSegment(sketch, "E5442", {"start": v(163.1, 60.97) * mm, "end": v(162.96, 60.84) * mm});
            skLineSegment(sketch, "E5443", {"start": v(162.96, 60.84) * mm, "end": v(162.8, 60.73) * mm});
            skLineSegment(sketch, "E5444", {"start": v(162.8, 60.73) * mm, "end": v(162.64, 60.64) * mm});
            skLineSegment(sketch, "E5445", {"start": v(162.64, 60.64) * mm, "end": v(162.46, 60.57) * mm});
            skLineSegment(sketch, "E5446", {"start": v(162.46, 60.57) * mm, "end": v(162.28, 60.53) * mm});
            skLineSegment(sketch, "E5447", {"start": v(162.28, 60.53) * mm, "end": v(162.1, 60.5) * mm});
            skLineSegment(sketch, "E5448", {"start": v(162.1, 60.5) * mm, "end": v(161.9, 60.5) * mm});
            skLineSegment(sketch, "E5449", {"start": v(247.9, 60.5) * mm, "end": v(247.72, 60.53) * mm});
            skLineSegment(sketch, "E5450", {"start": v(247.72, 60.53) * mm, "end": v(247.54, 60.57) * mm});
            skLineSegment(sketch, "E5451", {"start": v(247.54, 60.57) * mm, "end": v(247.36, 60.64) * mm});
            skLineSegment(sketch, "E5452", {"start": v(247.36, 60.64) * mm, "end": v(247.2, 60.73) * mm});
            skLineSegment(sketch, "E5453", {"start": v(247.2, 60.73) * mm, "end": v(247.04, 60.84) * mm});
            skLineSegment(sketch, "E5454", {"start": v(247.04, 60.84) * mm, "end": v(246.9, 60.97) * mm});
            skLineSegment(sketch, "E5455", {"start": v(246.9, 60.97) * mm, "end": v(246.79, 61.12) * mm});
            skLineSegment(sketch, "E5456", {"start": v(246.79, 61.12) * mm, "end": v(246.69, 61.28) * mm});
            skLineSegment(sketch, "E5457", {"start": v(246.69, 61.28) * mm, "end": v(246.6, 61.45) * mm});
            skLineSegment(sketch, "E5458", {"start": v(246.6, 61.45) * mm, "end": v(246.55, 61.63) * mm});
            skLineSegment(sketch, "E5459", {"start": v(246.55, 61.63) * mm, "end": v(246.51, 61.81) * mm});
            skLineSegment(sketch, "E5460", {"start": v(246.51, 61.81) * mm, "end": v(246.5, 62) * mm});
            skLineSegment(sketch, "E5461", {"start": v(246.5, 62) * mm, "end": v(246.51, 62.19) * mm});
            skLineSegment(sketch, "E5462", {"start": v(246.51, 62.19) * mm, "end": v(246.55, 62.37) * mm});
            skLineSegment(sketch, "E5463", {"start": v(246.55, 62.37) * mm, "end": v(246.6, 62.55) * mm});
            skLineSegment(sketch, "E5464", {"start": v(246.6, 62.55) * mm, "end": v(246.69, 62.72) * mm});
            skLineSegment(sketch, "E5465", {"start": v(246.69, 62.72) * mm, "end": v(246.79, 62.88) * mm});
            skLineSegment(sketch, "E5466", {"start": v(246.79, 62.88) * mm, "end": v(246.9, 63.03) * mm});
            skLineSegment(sketch, "E5467", {"start": v(246.9, 63.03) * mm, "end": v(247.04, 63.16) * mm});
            skLineSegment(sketch, "E5468", {"start": v(247.04, 63.16) * mm, "end": v(247.2, 63.27) * mm});
            skLineSegment(sketch, "E5469", {"start": v(247.2, 63.27) * mm, "end": v(247.36, 63.36) * mm});
            skLineSegment(sketch, "E5470", {"start": v(247.36, 63.36) * mm, "end": v(247.54, 63.43) * mm});
            skLineSegment(sketch, "E5471", {"start": v(247.54, 63.43) * mm, "end": v(247.72, 63.47) * mm});
            skLineSegment(sketch, "E5472", {"start": v(247.72, 63.47) * mm, "end": v(247.9, 63.5) * mm});
            skLineSegment(sketch, "E5473", {"start": v(247.9, 63.5) * mm, "end": v(248.1, 63.5) * mm});
            skLineSegment(sketch, "E5474", {"start": v(248.1, 63.5) * mm, "end": v(248.28, 63.47) * mm});
            skLineSegment(sketch, "E5475", {"start": v(248.28, 63.47) * mm, "end": v(248.46, 63.43) * mm});
            skLineSegment(sketch, "E5476", {"start": v(248.46, 63.43) * mm, "end": v(248.64, 63.36) * mm});
            skLineSegment(sketch, "E5477", {"start": v(248.64, 63.36) * mm, "end": v(248.8, 63.27) * mm});
            skLineSegment(sketch, "E5478", {"start": v(248.8, 63.27) * mm, "end": v(248.96, 63.16) * mm});
            skLineSegment(sketch, "E5479", {"start": v(248.96, 63.16) * mm, "end": v(249.1, 63.03) * mm});
            skLineSegment(sketch, "E5480", {"start": v(249.1, 63.03) * mm, "end": v(249.21, 62.88) * mm});
            skLineSegment(sketch, "E5481", {"start": v(249.21, 62.88) * mm, "end": v(249.31, 62.72) * mm});
            skLineSegment(sketch, "E5482", {"start": v(249.31, 62.72) * mm, "end": v(249.4, 62.55) * mm});
            skLineSegment(sketch, "E5483", {"start": v(249.4, 62.55) * mm, "end": v(249.45, 62.37) * mm});
            skLineSegment(sketch, "E5484", {"start": v(249.45, 62.37) * mm, "end": v(249.49, 62.19) * mm});
            skLineSegment(sketch, "E5485", {"start": v(249.49, 62.19) * mm, "end": v(249.5, 62) * mm});
            skLineSegment(sketch, "E5486", {"start": v(249.5, 62) * mm, "end": v(249.49, 61.81) * mm});
            skLineSegment(sketch, "E5487", {"start": v(249.49, 61.81) * mm, "end": v(249.45, 61.63) * mm});
            skLineSegment(sketch, "E5488", {"start": v(249.45, 61.63) * mm, "end": v(249.4, 61.45) * mm});
            skLineSegment(sketch, "E5489", {"start": v(249.4, 61.45) * mm, "end": v(249.31, 61.28) * mm});
            skLineSegment(sketch, "E5490", {"start": v(249.31, 61.28) * mm, "end": v(249.21, 61.12) * mm});
            skLineSegment(sketch, "E5491", {"start": v(249.21, 61.12) * mm, "end": v(249.1, 60.97) * mm});
            skLineSegment(sketch, "E5492", {"start": v(249.1, 60.97) * mm, "end": v(248.96, 60.84) * mm});
            skLineSegment(sketch, "E5493", {"start": v(248.96, 60.84) * mm, "end": v(248.8, 60.73) * mm});
            skLineSegment(sketch, "E5494", {"start": v(248.8, 60.73) * mm, "end": v(248.64, 60.64) * mm});
            skLineSegment(sketch, "E5495", {"start": v(248.64, 60.64) * mm, "end": v(248.46, 60.57) * mm});
            skLineSegment(sketch, "E5496", {"start": v(248.46, 60.57) * mm, "end": v(248.28, 60.53) * mm});
            skLineSegment(sketch, "E5497", {"start": v(248.28, 60.53) * mm, "end": v(248.1, 60.5) * mm});
            skLineSegment(sketch, "E5498", {"start": v(248.1, 60.5) * mm, "end": v(247.9, 60.5) * mm});
            skLineSegment(sketch, "E5499", {"start": v(271.9, 60.5) * mm, "end": v(271.72, 60.53) * mm});
            skLineSegment(sketch, "E5500", {"start": v(271.72, 60.53) * mm, "end": v(271.54, 60.57) * mm});
            skLineSegment(sketch, "E5501", {"start": v(271.54, 60.57) * mm, "end": v(271.36, 60.64) * mm});
            skLineSegment(sketch, "E5502", {"start": v(271.36, 60.64) * mm, "end": v(271.2, 60.73) * mm});
            skLineSegment(sketch, "E5503", {"start": v(271.2, 60.73) * mm, "end": v(271.04, 60.84) * mm});
            skLineSegment(sketch, "E5504", {"start": v(271.04, 60.84) * mm, "end": v(270.9, 60.97) * mm});
            skLineSegment(sketch, "E5505", {"start": v(270.9, 60.97) * mm, "end": v(270.79, 61.12) * mm});
            skLineSegment(sketch, "E5506", {"start": v(270.79, 61.12) * mm, "end": v(270.69, 61.28) * mm});
            skLineSegment(sketch, "E5507", {"start": v(270.69, 61.28) * mm, "end": v(270.6, 61.45) * mm});
            skLineSegment(sketch, "E5508", {"start": v(270.6, 61.45) * mm, "end": v(270.55, 61.63) * mm});
            skLineSegment(sketch, "E5509", {"start": v(270.55, 61.63) * mm, "end": v(270.51, 61.81) * mm});
            skLineSegment(sketch, "E5510", {"start": v(270.51, 61.81) * mm, "end": v(270.5, 62) * mm});
            skLineSegment(sketch, "E5511", {"start": v(270.5, 62) * mm, "end": v(270.51, 62.19) * mm});
            skLineSegment(sketch, "E5512", {"start": v(270.51, 62.19) * mm, "end": v(270.55, 62.37) * mm});
            skLineSegment(sketch, "E5513", {"start": v(270.55, 62.37) * mm, "end": v(270.6, 62.55) * mm});
            skLineSegment(sketch, "E5514", {"start": v(270.6, 62.55) * mm, "end": v(270.69, 62.72) * mm});
            skLineSegment(sketch, "E5515", {"start": v(270.69, 62.72) * mm, "end": v(270.79, 62.88) * mm});
            skLineSegment(sketch, "E5516", {"start": v(270.79, 62.88) * mm, "end": v(270.9, 63.03) * mm});
            skLineSegment(sketch, "E5517", {"start": v(270.9, 63.03) * mm, "end": v(271.04, 63.16) * mm});
            skLineSegment(sketch, "E5518", {"start": v(271.04, 63.16) * mm, "end": v(271.2, 63.27) * mm});
            skLineSegment(sketch, "E5519", {"start": v(271.2, 63.27) * mm, "end": v(271.36, 63.36) * mm});
            skLineSegment(sketch, "E5520", {"start": v(271.36, 63.36) * mm, "end": v(271.54, 63.43) * mm});
            skLineSegment(sketch, "E5521", {"start": v(271.54, 63.43) * mm, "end": v(271.72, 63.47) * mm});
            skLineSegment(sketch, "E5522", {"start": v(271.72, 63.47) * mm, "end": v(271.9, 63.5) * mm});
            skLineSegment(sketch, "E5523", {"start": v(271.9, 63.5) * mm, "end": v(272.1, 63.5) * mm});
            skLineSegment(sketch, "E5524", {"start": v(272.1, 63.5) * mm, "end": v(272.28, 63.47) * mm});
            skLineSegment(sketch, "E5525", {"start": v(272.28, 63.47) * mm, "end": v(272.46, 63.43) * mm});
            skLineSegment(sketch, "E5526", {"start": v(272.46, 63.43) * mm, "end": v(272.64, 63.36) * mm});
            skLineSegment(sketch, "E5527", {"start": v(272.64, 63.36) * mm, "end": v(272.8, 63.27) * mm});
            skLineSegment(sketch, "E5528", {"start": v(272.8, 63.27) * mm, "end": v(272.96, 63.16) * mm});
            skLineSegment(sketch, "E5529", {"start": v(272.96, 63.16) * mm, "end": v(273.1, 63.03) * mm});
            skLineSegment(sketch, "E5530", {"start": v(273.1, 63.03) * mm, "end": v(273.21, 62.88) * mm});
            skLineSegment(sketch, "E5531", {"start": v(273.21, 62.88) * mm, "end": v(273.31, 62.72) * mm});
            skLineSegment(sketch, "E5532", {"start": v(273.31, 62.72) * mm, "end": v(273.4, 62.55) * mm});
            skLineSegment(sketch, "E5533", {"start": v(273.4, 62.55) * mm, "end": v(273.45, 62.37) * mm});
            skLineSegment(sketch, "E5534", {"start": v(273.45, 62.37) * mm, "end": v(273.49, 62.19) * mm});
            skLineSegment(sketch, "E5535", {"start": v(273.49, 62.19) * mm, "end": v(273.5, 62) * mm});
            skLineSegment(sketch, "E5536", {"start": v(273.5, 62) * mm, "end": v(273.49, 61.81) * mm});
            skLineSegment(sketch, "E5537", {"start": v(273.49, 61.81) * mm, "end": v(273.45, 61.63) * mm});
            skLineSegment(sketch, "E5538", {"start": v(273.45, 61.63) * mm, "end": v(273.4, 61.45) * mm});
            skLineSegment(sketch, "E5539", {"start": v(273.4, 61.45) * mm, "end": v(273.31, 61.28) * mm});
            skLineSegment(sketch, "E5540", {"start": v(273.31, 61.28) * mm, "end": v(273.21, 61.12) * mm});
            skLineSegment(sketch, "E5541", {"start": v(273.21, 61.12) * mm, "end": v(273.1, 60.97) * mm});
            skLineSegment(sketch, "E5542", {"start": v(273.1, 60.97) * mm, "end": v(272.96, 60.84) * mm});
            skLineSegment(sketch, "E5543", {"start": v(272.96, 60.84) * mm, "end": v(272.8, 60.73) * mm});
            skLineSegment(sketch, "E5544", {"start": v(272.8, 60.73) * mm, "end": v(272.64, 60.64) * mm});
            skLineSegment(sketch, "E5545", {"start": v(272.64, 60.64) * mm, "end": v(272.46, 60.57) * mm});
            skLineSegment(sketch, "E5546", {"start": v(272.46, 60.57) * mm, "end": v(272.28, 60.53) * mm});
            skLineSegment(sketch, "E5547", {"start": v(272.28, 60.53) * mm, "end": v(272.1, 60.5) * mm});
            skLineSegment(sketch, "E5548", {"start": v(272.1, 60.5) * mm, "end": v(271.9, 60.5) * mm});
            skLineSegment(sketch, "E5549", {"start": v(121.81, -49.04) * mm, "end": v(121.13, -48.9) * mm});
            skLineSegment(sketch, "E5550", {"start": v(121.13, -48.9) * mm, "end": v(120.47, -48.7) * mm});
            skLineSegment(sketch, "E5551", {"start": v(120.47, -48.7) * mm, "end": v(119.85, -48.4) * mm});
            skLineSegment(sketch, "E5552", {"start": v(119.85, -48.4) * mm, "end": v(119.27, -48.03) * mm});
            skLineSegment(sketch, "E5553", {"start": v(119.27, -48.03) * mm, "end": v(118.74, -47.59) * mm});
            skLineSegment(sketch, "E5554", {"start": v(118.74, -47.59) * mm, "end": v(118.26, -47.09) * mm});
            skLineSegment(sketch, "E5555", {"start": v(118.26, -47.09) * mm, "end": v(117.86, -46.53) * mm});
            skLineSegment(sketch, "E5556", {"start": v(117.86, -46.53) * mm, "end": v(117.52, -45.92) * mm});
            skLineSegment(sketch, "E5557", {"start": v(117.52, -45.92) * mm, "end": v(117.27, -45.28) * mm});
            skLineSegment(sketch, "E5558", {"start": v(117.27, -45.28) * mm, "end": v(117.1, -44.61) * mm});
            skLineSegment(sketch, "E5559", {"start": v(117.1, -44.61) * mm, "end": v(117.01, -43.92) * mm});
            skLineSegment(sketch, "E5560", {"start": v(117.01, -43.92) * mm, "end": v(117.01, 57.92) * mm});
            skLineSegment(sketch, "E5561", {"start": v(117.01, 57.92) * mm, "end": v(117.1, 58.6) * mm});
            skLineSegment(sketch, "E5562", {"start": v(117.1, 58.6) * mm, "end": v(117.27, 59.28) * mm});
            skLineSegment(sketch, "E5563", {"start": v(117.27, 59.28) * mm, "end": v(117.52, 59.92) * mm});
            skLineSegment(sketch, "E5564", {"start": v(117.52, 59.92) * mm, "end": v(117.86, 60.53) * mm});
            skLineSegment(sketch, "E5565", {"start": v(117.86, 60.53) * mm, "end": v(118.26, 61.09) * mm});
            skLineSegment(sketch, "E5566", {"start": v(118.26, 61.09) * mm, "end": v(118.74, 61.59) * mm});
            skLineSegment(sketch, "E5567", {"start": v(118.74, 61.59) * mm, "end": v(119.27, 62.03) * mm});
            skLineSegment(sketch, "E5568", {"start": v(119.27, 62.03) * mm, "end": v(119.85, 62.4) * mm});
            skLineSegment(sketch, "E5569", {"start": v(119.85, 62.4) * mm, "end": v(120.47, 62.7) * mm});
            skLineSegment(sketch, "E5570", {"start": v(120.47, 62.7) * mm, "end": v(121.13, 62.9) * mm});
            skLineSegment(sketch, "E5571", {"start": v(121.13, 62.9) * mm, "end": v(121.81, 63.04) * mm});
            skLineSegment(sketch, "E5572", {"start": v(121.81, 63.04) * mm, "end": v(122.5, 63.08) * mm});
            skLineSegment(sketch, "E5573", {"start": v(122.5, 63.08) * mm, "end": v(123.19, 63.04) * mm});
            skLineSegment(sketch, "E5574", {"start": v(123.19, 63.04) * mm, "end": v(123.87, 62.9) * mm});
            skLineSegment(sketch, "E5575", {"start": v(123.87, 62.9) * mm, "end": v(124.53, 62.7) * mm});
            skLineSegment(sketch, "E5576", {"start": v(124.53, 62.7) * mm, "end": v(125.15, 62.4) * mm});
            skLineSegment(sketch, "E5577", {"start": v(125.15, 62.4) * mm, "end": v(125.73, 62.03) * mm});
            skLineSegment(sketch, "E5578", {"start": v(125.73, 62.03) * mm, "end": v(126.27, 61.59) * mm});
            skLineSegment(sketch, "E5579", {"start": v(126.27, 61.59) * mm, "end": v(176.84, 11) * mm});
            skLineSegment(sketch, "E5580", {"start": v(176.84, 11) * mm, "end": v(177.32, 10.5) * mm});
            skLineSegment(sketch, "E5581", {"start": v(177.32, 10.5) * mm, "end": v(177.72, 9.95) * mm});
            skLineSegment(sketch, "E5582", {"start": v(177.72, 9.95) * mm, "end": v(178.06, 9.34) * mm});
            skLineSegment(sketch, "E5583", {"start": v(178.06, 9.34) * mm, "end": v(178.3, 8.7) * mm});
            skLineSegment(sketch, "E5584", {"start": v(178.3, 8.7) * mm, "end": v(178.48, 8.03) * mm});
            skLineSegment(sketch, "E5585", {"start": v(178.48, 8.03) * mm, "end": v(178.57, 7.34) * mm});
            skLineSegment(sketch, "E5586", {"start": v(178.57, 7.34) * mm, "end": v(178.57, 6.66) * mm});
            skLineSegment(sketch, "E5587", {"start": v(178.57, 6.66) * mm, "end": v(178.48, 5.97) * mm});
            skLineSegment(sketch, "E5588", {"start": v(178.48, 5.97) * mm, "end": v(178.3, 5.3) * mm});
            skLineSegment(sketch, "E5589", {"start": v(178.3, 5.3) * mm, "end": v(178.06, 4.66) * mm});
            skLineSegment(sketch, "E5590", {"start": v(178.06, 4.66) * mm, "end": v(177.72, 4.05) * mm});
            skLineSegment(sketch, "E5591", {"start": v(177.72, 4.05) * mm, "end": v(177.32, 3.5) * mm});
            skLineSegment(sketch, "E5592", {"start": v(177.32, 3.5) * mm, "end": v(176.84, 3) * mm});
            skLineSegment(sketch, "E5593", {"start": v(176.84, 3) * mm, "end": v(126.27, -47.59) * mm});
            skLineSegment(sketch, "E5594", {"start": v(126.27, -47.59) * mm, "end": v(125.73, -48.03) * mm});
            skLineSegment(sketch, "E5595", {"start": v(125.73, -48.03) * mm, "end": v(125.15, -48.4) * mm});
            skLineSegment(sketch, "E5596", {"start": v(125.15, -48.4) * mm, "end": v(124.53, -48.7) * mm});
            skLineSegment(sketch, "E5597", {"start": v(124.53, -48.7) * mm, "end": v(123.87, -48.9) * mm});
            skLineSegment(sketch, "E5598", {"start": v(123.87, -48.9) * mm, "end": v(123.19, -49.04) * mm});
            skLineSegment(sketch, "E5599", {"start": v(123.19, -49.04) * mm, "end": v(122.5, -49.08) * mm});
            skLineSegment(sketch, "E5600", {"start": v(122.5, -49.08) * mm, "end": v(121.81, -49.04) * mm});
            skLineSegment(sketch, "E5601", {"start": v(286.81, -49.04) * mm, "end": v(286.13, -48.9) * mm});
            skLineSegment(sketch, "E5602", {"start": v(286.13, -48.9) * mm, "end": v(285.48, -48.7) * mm});
            skLineSegment(sketch, "E5603", {"start": v(285.48, -48.7) * mm, "end": v(284.85, -48.4) * mm});
            skLineSegment(sketch, "E5604", {"start": v(284.85, -48.4) * mm, "end": v(284.27, -48.03) * mm});
            skLineSegment(sketch, "E5605", {"start": v(284.27, -48.03) * mm, "end": v(283.74, -47.59) * mm});
            skLineSegment(sketch, "E5606", {"start": v(283.74, -47.59) * mm, "end": v(233.16, 3) * mm});
            skLineSegment(sketch, "E5607", {"start": v(233.16, 3) * mm, "end": v(232.68, 3.5) * mm});
            skLineSegment(sketch, "E5608", {"start": v(232.68, 3.5) * mm, "end": v(232.28, 4.05) * mm});
            skLineSegment(sketch, "E5609", {"start": v(232.28, 4.05) * mm, "end": v(231.94, 4.66) * mm});
            skLineSegment(sketch, "E5610", {"start": v(231.94, 4.66) * mm, "end": v(231.7, 5.3) * mm});
            skLineSegment(sketch, "E5611", {"start": v(231.7, 5.3) * mm, "end": v(231.52, 5.97) * mm});
            skLineSegment(sketch, "E5612", {"start": v(231.52, 5.97) * mm, "end": v(231.43, 6.66) * mm});
            skLineSegment(sketch, "E5613", {"start": v(231.43, 6.66) * mm, "end": v(231.43, 7.34) * mm});
            skLineSegment(sketch, "E5614", {"start": v(231.43, 7.34) * mm, "end": v(231.52, 8.03) * mm});
            skLineSegment(sketch, "E5615", {"start": v(231.52, 8.03) * mm, "end": v(231.7, 8.7) * mm});
            skLineSegment(sketch, "E5616", {"start": v(231.7, 8.7) * mm, "end": v(231.94, 9.34) * mm});
            skLineSegment(sketch, "E5617", {"start": v(231.94, 9.34) * mm, "end": v(232.28, 9.95) * mm});
            skLineSegment(sketch, "E5618", {"start": v(232.28, 9.95) * mm, "end": v(232.68, 10.5) * mm});
            skLineSegment(sketch, "E5619", {"start": v(232.68, 10.5) * mm, "end": v(233.16, 11) * mm});
            skLineSegment(sketch, "E5620", {"start": v(233.16, 11) * mm, "end": v(283.74, 61.59) * mm});
            skLineSegment(sketch, "E5621", {"start": v(283.74, 61.59) * mm, "end": v(284.27, 62.03) * mm});
            skLineSegment(sketch, "E5622", {"start": v(284.27, 62.03) * mm, "end": v(284.85, 62.4) * mm});
            skLineSegment(sketch, "E5623", {"start": v(284.85, 62.4) * mm, "end": v(285.48, 62.7) * mm});
            skLineSegment(sketch, "E5624", {"start": v(285.48, 62.7) * mm, "end": v(286.13, 62.9) * mm});
            skLineSegment(sketch, "E5625", {"start": v(286.13, 62.9) * mm, "end": v(286.81, 63.04) * mm});
            skLineSegment(sketch, "E5626", {"start": v(286.81, 63.04) * mm, "end": v(287.5, 63.08) * mm});
            skLineSegment(sketch, "E5627", {"start": v(287.5, 63.08) * mm, "end": v(288.19, 63.04) * mm});
            skLineSegment(sketch, "E5628", {"start": v(288.19, 63.04) * mm, "end": v(288.87, 62.9) * mm});
            skLineSegment(sketch, "E5629", {"start": v(288.87, 62.9) * mm, "end": v(289.52, 62.7) * mm});
            skLineSegment(sketch, "E5630", {"start": v(289.52, 62.7) * mm, "end": v(290.15, 62.4) * mm});
            skLineSegment(sketch, "E5631", {"start": v(290.15, 62.4) * mm, "end": v(290.73, 62.03) * mm});
            skLineSegment(sketch, "E5632", {"start": v(290.73, 62.03) * mm, "end": v(291.26, 61.59) * mm});
            skLineSegment(sketch, "E5633", {"start": v(291.26, 61.59) * mm, "end": v(291.74, 61.09) * mm});
            skLineSegment(sketch, "E5634", {"start": v(291.74, 61.09) * mm, "end": v(292.14, 60.53) * mm});
            skLineSegment(sketch, "E5635", {"start": v(292.14, 60.53) * mm, "end": v(292.48, 59.92) * mm});
            skLineSegment(sketch, "E5636", {"start": v(292.48, 59.92) * mm, "end": v(292.73, 59.28) * mm});
            skLineSegment(sketch, "E5637", {"start": v(292.73, 59.28) * mm, "end": v(292.9, 58.6) * mm});
            skLineSegment(sketch, "E5638", {"start": v(292.9, 58.6) * mm, "end": v(292.99, 57.92) * mm});
            skLineSegment(sketch, "E5639", {"start": v(292.99, 57.92) * mm, "end": v(292.99, -43.92) * mm});
            skLineSegment(sketch, "E5640", {"start": v(292.99, -43.92) * mm, "end": v(292.9, -44.61) * mm});
            skLineSegment(sketch, "E5641", {"start": v(292.9, -44.61) * mm, "end": v(292.73, -45.28) * mm});
            skLineSegment(sketch, "E5642", {"start": v(292.73, -45.28) * mm, "end": v(292.48, -45.92) * mm});
            skLineSegment(sketch, "E5643", {"start": v(292.48, -45.92) * mm, "end": v(292.14, -46.53) * mm});
            skLineSegment(sketch, "E5644", {"start": v(292.14, -46.53) * mm, "end": v(291.74, -47.09) * mm});
            skLineSegment(sketch, "E5645", {"start": v(291.74, -47.09) * mm, "end": v(291.26, -47.59) * mm});
            skLineSegment(sketch, "E5646", {"start": v(291.26, -47.59) * mm, "end": v(290.73, -48.03) * mm});
            skLineSegment(sketch, "E5647", {"start": v(290.73, -48.03) * mm, "end": v(290.15, -48.4) * mm});
            skLineSegment(sketch, "E5648", {"start": v(290.15, -48.4) * mm, "end": v(289.52, -48.7) * mm});
            skLineSegment(sketch, "E5649", {"start": v(289.52, -48.7) * mm, "end": v(288.87, -48.9) * mm});
            skLineSegment(sketch, "E5650", {"start": v(288.87, -48.9) * mm, "end": v(288.19, -49.04) * mm});
            skLineSegment(sketch, "E5651", {"start": v(288.19, -49.04) * mm, "end": v(287.5, -49.08) * mm});
            skLineSegment(sketch, "E5652", {"start": v(287.5, -49.08) * mm, "end": v(286.81, -49.04) * mm});
            skLineSegment(sketch, "E5653", {"start": v(111.4, 14.5) * mm, "end": v(111.22, 14.53) * mm});
            skLineSegment(sketch, "E5654", {"start": v(111.22, 14.53) * mm, "end": v(111.04, 14.57) * mm});
            skLineSegment(sketch, "E5655", {"start": v(111.04, 14.57) * mm, "end": v(110.86, 14.64) * mm});
            skLineSegment(sketch, "E5656", {"start": v(110.86, 14.64) * mm, "end": v(110.7, 14.73) * mm});
            skLineSegment(sketch, "E5657", {"start": v(110.7, 14.73) * mm, "end": v(110.54, 14.84) * mm});
            skLineSegment(sketch, "E5658", {"start": v(110.54, 14.84) * mm, "end": v(110.4, 14.97) * mm});
            skLineSegment(sketch, "E5659", {"start": v(110.4, 14.97) * mm, "end": v(110.29, 15.12) * mm});
            skLineSegment(sketch, "E5660", {"start": v(110.29, 15.12) * mm, "end": v(110.19, 15.28) * mm});
            skLineSegment(sketch, "E5661", {"start": v(110.19, 15.28) * mm, "end": v(110.1, 15.45) * mm});
            skLineSegment(sketch, "E5662", {"start": v(110.1, 15.45) * mm, "end": v(110.05, 15.63) * mm});
            skLineSegment(sketch, "E5663", {"start": v(110.05, 15.63) * mm, "end": v(110.01, 15.81) * mm});
            skLineSegment(sketch, "E5664", {"start": v(110.01, 15.81) * mm, "end": v(110, 16) * mm});
            skLineSegment(sketch, "E5665", {"start": v(110, 16) * mm, "end": v(110.01, 16.19) * mm});
            skLineSegment(sketch, "E5666", {"start": v(110.01, 16.19) * mm, "end": v(110.05, 16.37) * mm});
            skLineSegment(sketch, "E5667", {"start": v(110.05, 16.37) * mm, "end": v(110.1, 16.55) * mm});
            skLineSegment(sketch, "E5668", {"start": v(110.1, 16.55) * mm, "end": v(110.19, 16.72) * mm});
            skLineSegment(sketch, "E5669", {"start": v(110.19, 16.72) * mm, "end": v(110.29, 16.88) * mm});
            skLineSegment(sketch, "E5670", {"start": v(110.29, 16.88) * mm, "end": v(110.4, 17.03) * mm});
            skLineSegment(sketch, "E5671", {"start": v(110.4, 17.03) * mm, "end": v(110.54, 17.16) * mm});
            skLineSegment(sketch, "E5672", {"start": v(110.54, 17.16) * mm, "end": v(110.7, 17.27) * mm});
            skLineSegment(sketch, "E5673", {"start": v(110.7, 17.27) * mm, "end": v(110.86, 17.36) * mm});
            skLineSegment(sketch, "E5674", {"start": v(110.86, 17.36) * mm, "end": v(111.04, 17.43) * mm});
            skLineSegment(sketch, "E5675", {"start": v(111.04, 17.43) * mm, "end": v(111.22, 17.47) * mm});
            skLineSegment(sketch, "E5676", {"start": v(111.22, 17.47) * mm, "end": v(111.4, 17.5) * mm});
            skLineSegment(sketch, "E5677", {"start": v(111.4, 17.5) * mm, "end": v(111.6, 17.5) * mm});
            skLineSegment(sketch, "E5678", {"start": v(111.6, 17.5) * mm, "end": v(111.78, 17.47) * mm});
            skLineSegment(sketch, "E5679", {"start": v(111.78, 17.47) * mm, "end": v(111.96, 17.43) * mm});
            skLineSegment(sketch, "E5680", {"start": v(111.96, 17.43) * mm, "end": v(112.14, 17.36) * mm});
            skLineSegment(sketch, "E5681", {"start": v(112.14, 17.36) * mm, "end": v(112.3, 17.27) * mm});
            skLineSegment(sketch, "E5682", {"start": v(112.3, 17.27) * mm, "end": v(112.46, 17.16) * mm});
            skLineSegment(sketch, "E5683", {"start": v(112.46, 17.16) * mm, "end": v(112.6, 17.03) * mm});
            skLineSegment(sketch, "E5684", {"start": v(112.6, 17.03) * mm, "end": v(112.71, 16.88) * mm});
            skLineSegment(sketch, "E5685", {"start": v(112.71, 16.88) * mm, "end": v(112.81, 16.72) * mm});
            skLineSegment(sketch, "E5686", {"start": v(112.81, 16.72) * mm, "end": v(112.9, 16.55) * mm});
            skLineSegment(sketch, "E5687", {"start": v(112.9, 16.55) * mm, "end": v(112.95, 16.37) * mm});
            skLineSegment(sketch, "E5688", {"start": v(112.95, 16.37) * mm, "end": v(112.99, 16.19) * mm});
            skLineSegment(sketch, "E5689", {"start": v(112.99, 16.19) * mm, "end": v(113, 16) * mm});
            skLineSegment(sketch, "E5690", {"start": v(113, 16) * mm, "end": v(112.99, 15.81) * mm});
            skLineSegment(sketch, "E5691", {"start": v(112.99, 15.81) * mm, "end": v(112.95, 15.63) * mm});
            skLineSegment(sketch, "E5692", {"start": v(112.95, 15.63) * mm, "end": v(112.9, 15.45) * mm});
            skLineSegment(sketch, "E5693", {"start": v(112.9, 15.45) * mm, "end": v(112.81, 15.28) * mm});
            skLineSegment(sketch, "E5694", {"start": v(112.81, 15.28) * mm, "end": v(112.71, 15.12) * mm});
            skLineSegment(sketch, "E5695", {"start": v(112.71, 15.12) * mm, "end": v(112.6, 14.97) * mm});
            skLineSegment(sketch, "E5696", {"start": v(112.6, 14.97) * mm, "end": v(112.46, 14.84) * mm});
            skLineSegment(sketch, "E5697", {"start": v(112.46, 14.84) * mm, "end": v(112.3, 14.73) * mm});
            skLineSegment(sketch, "E5698", {"start": v(112.3, 14.73) * mm, "end": v(112.14, 14.64) * mm});
            skLineSegment(sketch, "E5699", {"start": v(112.14, 14.64) * mm, "end": v(111.96, 14.57) * mm});
            skLineSegment(sketch, "E5700", {"start": v(111.96, 14.57) * mm, "end": v(111.78, 14.53) * mm});
            skLineSegment(sketch, "E5701", {"start": v(111.78, 14.53) * mm, "end": v(111.6, 14.5) * mm});
            skLineSegment(sketch, "E5702", {"start": v(111.6, 14.5) * mm, "end": v(111.4, 14.5) * mm});
            skLineSegment(sketch, "E5703", {"start": v(204.9, 13.5) * mm, "end": v(204.72, 13.53) * mm});
            skLineSegment(sketch, "E5704", {"start": v(204.72, 13.53) * mm, "end": v(204.54, 13.57) * mm});
            skLineSegment(sketch, "E5705", {"start": v(204.54, 13.57) * mm, "end": v(204.36, 13.64) * mm});
            skLineSegment(sketch, "E5706", {"start": v(204.36, 13.64) * mm, "end": v(204.2, 13.73) * mm});
            skLineSegment(sketch, "E5707", {"start": v(204.2, 13.73) * mm, "end": v(204.04, 13.84) * mm});
            skLineSegment(sketch, "E5708", {"start": v(204.04, 13.84) * mm, "end": v(203.9, 13.97) * mm});
            skLineSegment(sketch, "E5709", {"start": v(203.9, 13.97) * mm, "end": v(203.79, 14.12) * mm});
            skLineSegment(sketch, "E5710", {"start": v(203.79, 14.12) * mm, "end": v(203.69, 14.28) * mm});
            skLineSegment(sketch, "E5711", {"start": v(203.69, 14.28) * mm, "end": v(203.6, 14.45) * mm});
            skLineSegment(sketch, "E5712", {"start": v(203.6, 14.45) * mm, "end": v(203.55, 14.63) * mm});
            skLineSegment(sketch, "E5713", {"start": v(203.55, 14.63) * mm, "end": v(203.51, 14.81) * mm});
            skLineSegment(sketch, "E5714", {"start": v(203.51, 14.81) * mm, "end": v(203.5, 15) * mm});
            skLineSegment(sketch, "E5715", {"start": v(203.5, 15) * mm, "end": v(203.51, 15.19) * mm});
            skLineSegment(sketch, "E5716", {"start": v(203.51, 15.19) * mm, "end": v(203.55, 15.37) * mm});
            skLineSegment(sketch, "E5717", {"start": v(203.55, 15.37) * mm, "end": v(203.6, 15.55) * mm});
            skLineSegment(sketch, "E5718", {"start": v(203.6, 15.55) * mm, "end": v(203.69, 15.72) * mm});
            skLineSegment(sketch, "E5719", {"start": v(203.69, 15.72) * mm, "end": v(203.79, 15.88) * mm});
            skLineSegment(sketch, "E5720", {"start": v(203.79, 15.88) * mm, "end": v(203.9, 16.03) * mm});
            skLineSegment(sketch, "E5721", {"start": v(203.9, 16.03) * mm, "end": v(204.04, 16.16) * mm});
            skLineSegment(sketch, "E5722", {"start": v(204.04, 16.16) * mm, "end": v(204.2, 16.27) * mm});
            skLineSegment(sketch, "E5723", {"start": v(204.2, 16.27) * mm, "end": v(204.36, 16.36) * mm});
            skLineSegment(sketch, "E5724", {"start": v(204.36, 16.36) * mm, "end": v(204.54, 16.43) * mm});
            skLineSegment(sketch, "E5725", {"start": v(204.54, 16.43) * mm, "end": v(204.72, 16.47) * mm});
            skLineSegment(sketch, "E5726", {"start": v(204.72, 16.47) * mm, "end": v(204.9, 16.5) * mm});
            skLineSegment(sketch, "E5727", {"start": v(204.9, 16.5) * mm, "end": v(205.1, 16.5) * mm});
            skLineSegment(sketch, "E5728", {"start": v(205.1, 16.5) * mm, "end": v(205.28, 16.47) * mm});
            skLineSegment(sketch, "E5729", {"start": v(205.28, 16.47) * mm, "end": v(205.46, 16.43) * mm});
            skLineSegment(sketch, "E5730", {"start": v(205.46, 16.43) * mm, "end": v(205.64, 16.36) * mm});
            skLineSegment(sketch, "E5731", {"start": v(205.64, 16.36) * mm, "end": v(205.8, 16.27) * mm});
            skLineSegment(sketch, "E5732", {"start": v(205.8, 16.27) * mm, "end": v(205.96, 16.16) * mm});
            skLineSegment(sketch, "E5733", {"start": v(205.96, 16.16) * mm, "end": v(206.1, 16.03) * mm});
            skLineSegment(sketch, "E5734", {"start": v(206.1, 16.03) * mm, "end": v(206.21, 15.88) * mm});
            skLineSegment(sketch, "E5735", {"start": v(206.21, 15.88) * mm, "end": v(206.31, 15.72) * mm});
            skLineSegment(sketch, "E5736", {"start": v(206.31, 15.72) * mm, "end": v(206.4, 15.55) * mm});
            skLineSegment(sketch, "E5737", {"start": v(206.4, 15.55) * mm, "end": v(206.45, 15.37) * mm});
            skLineSegment(sketch, "E5738", {"start": v(206.45, 15.37) * mm, "end": v(206.49, 15.19) * mm});
            skLineSegment(sketch, "E5739", {"start": v(206.49, 15.19) * mm, "end": v(206.5, 15) * mm});
            skLineSegment(sketch, "E5740", {"start": v(206.5, 15) * mm, "end": v(206.49, 14.81) * mm});
            skLineSegment(sketch, "E5741", {"start": v(206.49, 14.81) * mm, "end": v(206.45, 14.63) * mm});
            skLineSegment(sketch, "E5742", {"start": v(206.45, 14.63) * mm, "end": v(206.4, 14.45) * mm});
            skLineSegment(sketch, "E5743", {"start": v(206.4, 14.45) * mm, "end": v(206.31, 14.28) * mm});
            skLineSegment(sketch, "E5744", {"start": v(206.31, 14.28) * mm, "end": v(206.21, 14.12) * mm});
            skLineSegment(sketch, "E5745", {"start": v(206.21, 14.12) * mm, "end": v(206.1, 13.97) * mm});
            skLineSegment(sketch, "E5746", {"start": v(206.1, 13.97) * mm, "end": v(205.96, 13.84) * mm});
            skLineSegment(sketch, "E5747", {"start": v(205.96, 13.84) * mm, "end": v(205.8, 13.73) * mm});
            skLineSegment(sketch, "E5748", {"start": v(205.8, 13.73) * mm, "end": v(205.64, 13.64) * mm});
            skLineSegment(sketch, "E5749", {"start": v(205.64, 13.64) * mm, "end": v(205.46, 13.57) * mm});
            skLineSegment(sketch, "E5750", {"start": v(205.46, 13.57) * mm, "end": v(205.28, 13.53) * mm});
            skLineSegment(sketch, "E5751", {"start": v(205.28, 13.53) * mm, "end": v(205.1, 13.5) * mm});
            skLineSegment(sketch, "E5752", {"start": v(205.1, 13.5) * mm, "end": v(204.9, 13.5) * mm});
            skLineSegment(sketch, "E5753", {"start": v(111.4, 8.5) * mm, "end": v(111.22, 8.53) * mm});
            skLineSegment(sketch, "E5754", {"start": v(111.22, 8.53) * mm, "end": v(111.04, 8.57) * mm});
            skLineSegment(sketch, "E5755", {"start": v(111.04, 8.57) * mm, "end": v(110.86, 8.64) * mm});
            skLineSegment(sketch, "E5756", {"start": v(110.86, 8.64) * mm, "end": v(110.7, 8.73) * mm});
            skLineSegment(sketch, "E5757", {"start": v(110.7, 8.73) * mm, "end": v(110.54, 8.84) * mm});
            skLineSegment(sketch, "E5758", {"start": v(110.54, 8.84) * mm, "end": v(110.4, 8.97) * mm});
            skLineSegment(sketch, "E5759", {"start": v(110.4, 8.97) * mm, "end": v(110.29, 9.12) * mm});
            skLineSegment(sketch, "E5760", {"start": v(110.29, 9.12) * mm, "end": v(110.19, 9.28) * mm});
            skLineSegment(sketch, "E5761", {"start": v(110.19, 9.28) * mm, "end": v(110.1, 9.45) * mm});
            skLineSegment(sketch, "E5762", {"start": v(110.1, 9.45) * mm, "end": v(110.05, 9.63) * mm});
            skLineSegment(sketch, "E5763", {"start": v(110.05, 9.63) * mm, "end": v(110.01, 9.81) * mm});
            skLineSegment(sketch, "E5764", {"start": v(110.01, 9.81) * mm, "end": v(110, 10) * mm});
            skLineSegment(sketch, "E5765", {"start": v(110, 10) * mm, "end": v(110.01, 10.19) * mm});
            skLineSegment(sketch, "E5766", {"start": v(110.01, 10.19) * mm, "end": v(110.05, 10.37) * mm});
            skLineSegment(sketch, "E5767", {"start": v(110.05, 10.37) * mm, "end": v(110.1, 10.55) * mm});
            skLineSegment(sketch, "E5768", {"start": v(110.1, 10.55) * mm, "end": v(110.19, 10.72) * mm});
            skLineSegment(sketch, "E5769", {"start": v(110.19, 10.72) * mm, "end": v(110.29, 10.88) * mm});
            skLineSegment(sketch, "E5770", {"start": v(110.29, 10.88) * mm, "end": v(110.4, 11.03) * mm});
            skLineSegment(sketch, "E5771", {"start": v(110.4, 11.03) * mm, "end": v(110.54, 11.16) * mm});
            skLineSegment(sketch, "E5772", {"start": v(110.54, 11.16) * mm, "end": v(110.7, 11.27) * mm});
            skLineSegment(sketch, "E5773", {"start": v(110.7, 11.27) * mm, "end": v(110.86, 11.36) * mm});
            skLineSegment(sketch, "E5774", {"start": v(110.86, 11.36) * mm, "end": v(111.04, 11.43) * mm});
            skLineSegment(sketch, "E5775", {"start": v(111.04, 11.43) * mm, "end": v(111.22, 11.47) * mm});
            skLineSegment(sketch, "E5776", {"start": v(111.22, 11.47) * mm, "end": v(111.4, 11.5) * mm});
            skLineSegment(sketch, "E5777", {"start": v(111.4, 11.5) * mm, "end": v(111.6, 11.5) * mm});
            skLineSegment(sketch, "E5778", {"start": v(111.6, 11.5) * mm, "end": v(111.78, 11.47) * mm});
            skLineSegment(sketch, "E5779", {"start": v(111.78, 11.47) * mm, "end": v(111.96, 11.43) * mm});
            skLineSegment(sketch, "E5780", {"start": v(111.96, 11.43) * mm, "end": v(112.14, 11.36) * mm});
            skLineSegment(sketch, "E5781", {"start": v(112.14, 11.36) * mm, "end": v(112.3, 11.27) * mm});
            skLineSegment(sketch, "E5782", {"start": v(112.3, 11.27) * mm, "end": v(112.46, 11.16) * mm});
            skLineSegment(sketch, "E5783", {"start": v(112.46, 11.16) * mm, "end": v(112.6, 11.03) * mm});
            skLineSegment(sketch, "E5784", {"start": v(112.6, 11.03) * mm, "end": v(112.71, 10.88) * mm});
            skLineSegment(sketch, "E5785", {"start": v(112.71, 10.88) * mm, "end": v(112.81, 10.72) * mm});
            skLineSegment(sketch, "E5786", {"start": v(112.81, 10.72) * mm, "end": v(112.9, 10.55) * mm});
            skLineSegment(sketch, "E5787", {"start": v(112.9, 10.55) * mm, "end": v(112.95, 10.37) * mm});
            skLineSegment(sketch, "E5788", {"start": v(112.95, 10.37) * mm, "end": v(112.99, 10.19) * mm});
            skLineSegment(sketch, "E5789", {"start": v(112.99, 10.19) * mm, "end": v(113, 10) * mm});
            skLineSegment(sketch, "E5790", {"start": v(113, 10) * mm, "end": v(112.99, 9.81) * mm});
            skLineSegment(sketch, "E5791", {"start": v(112.99, 9.81) * mm, "end": v(112.95, 9.63) * mm});
            skLineSegment(sketch, "E5792", {"start": v(112.95, 9.63) * mm, "end": v(112.9, 9.45) * mm});
            skLineSegment(sketch, "E5793", {"start": v(112.9, 9.45) * mm, "end": v(112.81, 9.28) * mm});
            skLineSegment(sketch, "E5794", {"start": v(112.81, 9.28) * mm, "end": v(112.71, 9.12) * mm});
            skLineSegment(sketch, "E5795", {"start": v(112.71, 9.12) * mm, "end": v(112.6, 8.97) * mm});
            skLineSegment(sketch, "E5796", {"start": v(112.6, 8.97) * mm, "end": v(112.46, 8.84) * mm});
            skLineSegment(sketch, "E5797", {"start": v(112.46, 8.84) * mm, "end": v(112.3, 8.73) * mm});
            skLineSegment(sketch, "E5798", {"start": v(112.3, 8.73) * mm, "end": v(112.14, 8.64) * mm});
            skLineSegment(sketch, "E5799", {"start": v(112.14, 8.64) * mm, "end": v(111.96, 8.57) * mm});
            skLineSegment(sketch, "E5800", {"start": v(111.96, 8.57) * mm, "end": v(111.78, 8.53) * mm});
            skLineSegment(sketch, "E5801", {"start": v(111.78, 8.53) * mm, "end": v(111.6, 8.5) * mm});
            skLineSegment(sketch, "E5802", {"start": v(111.6, 8.5) * mm, "end": v(111.4, 8.5) * mm});
            skLineSegment(sketch, "E5803", {"start": v(111.4, 2.5) * mm, "end": v(111.22, 2.53) * mm});
            skLineSegment(sketch, "E5804", {"start": v(111.22, 2.53) * mm, "end": v(111.04, 2.57) * mm});
            skLineSegment(sketch, "E5805", {"start": v(111.04, 2.57) * mm, "end": v(110.86, 2.64) * mm});
            skLineSegment(sketch, "E5806", {"start": v(110.86, 2.64) * mm, "end": v(110.7, 2.73) * mm});
            skLineSegment(sketch, "E5807", {"start": v(110.7, 2.73) * mm, "end": v(110.54, 2.84) * mm});
            skLineSegment(sketch, "E5808", {"start": v(110.54, 2.84) * mm, "end": v(110.4, 2.97) * mm});
            skLineSegment(sketch, "E5809", {"start": v(110.4, 2.97) * mm, "end": v(110.29, 3.12) * mm});
            skLineSegment(sketch, "E5810", {"start": v(110.29, 3.12) * mm, "end": v(110.19, 3.28) * mm});
            skLineSegment(sketch, "E5811", {"start": v(110.19, 3.28) * mm, "end": v(110.1, 3.45) * mm});
            skLineSegment(sketch, "E5812", {"start": v(110.1, 3.45) * mm, "end": v(110.05, 3.63) * mm});
            skLineSegment(sketch, "E5813", {"start": v(110.05, 3.63) * mm, "end": v(110.01, 3.81) * mm});
            skLineSegment(sketch, "E5814", {"start": v(110.01, 3.81) * mm, "end": v(110, 4) * mm});
            skLineSegment(sketch, "E5815", {"start": v(110, 4) * mm, "end": v(110.01, 4.19) * mm});
            skLineSegment(sketch, "E5816", {"start": v(110.01, 4.19) * mm, "end": v(110.05, 4.37) * mm});
            skLineSegment(sketch, "E5817", {"start": v(110.05, 4.37) * mm, "end": v(110.1, 4.55) * mm});
            skLineSegment(sketch, "E5818", {"start": v(110.1, 4.55) * mm, "end": v(110.19, 4.72) * mm});
            skLineSegment(sketch, "E5819", {"start": v(110.19, 4.72) * mm, "end": v(110.29, 4.88) * mm});
            skLineSegment(sketch, "E5820", {"start": v(110.29, 4.88) * mm, "end": v(110.4, 5.03) * mm});
            skLineSegment(sketch, "E5821", {"start": v(110.4, 5.03) * mm, "end": v(110.54, 5.16) * mm});
            skLineSegment(sketch, "E5822", {"start": v(110.54, 5.16) * mm, "end": v(110.7, 5.27) * mm});
            skLineSegment(sketch, "E5823", {"start": v(110.7, 5.27) * mm, "end": v(110.86, 5.36) * mm});
            skLineSegment(sketch, "E5824", {"start": v(110.86, 5.36) * mm, "end": v(111.04, 5.43) * mm});
            skLineSegment(sketch, "E5825", {"start": v(111.04, 5.43) * mm, "end": v(111.22, 5.47) * mm});
            skLineSegment(sketch, "E5826", {"start": v(111.22, 5.47) * mm, "end": v(111.4, 5.5) * mm});
            skLineSegment(sketch, "E5827", {"start": v(111.4, 5.5) * mm, "end": v(111.6, 5.5) * mm});
            skLineSegment(sketch, "E5828", {"start": v(111.6, 5.5) * mm, "end": v(111.78, 5.47) * mm});
            skLineSegment(sketch, "E5829", {"start": v(111.78, 5.47) * mm, "end": v(111.96, 5.43) * mm});
            skLineSegment(sketch, "E5830", {"start": v(111.96, 5.43) * mm, "end": v(112.14, 5.36) * mm});
            skLineSegment(sketch, "E5831", {"start": v(112.14, 5.36) * mm, "end": v(112.3, 5.27) * mm});
            skLineSegment(sketch, "E5832", {"start": v(112.3, 5.27) * mm, "end": v(112.46, 5.16) * mm});
            skLineSegment(sketch, "E5833", {"start": v(112.46, 5.16) * mm, "end": v(112.6, 5.03) * mm});
            skLineSegment(sketch, "E5834", {"start": v(112.6, 5.03) * mm, "end": v(112.71, 4.88) * mm});
            skLineSegment(sketch, "E5835", {"start": v(112.71, 4.88) * mm, "end": v(112.81, 4.72) * mm});
            skLineSegment(sketch, "E5836", {"start": v(112.81, 4.72) * mm, "end": v(112.9, 4.55) * mm});
            skLineSegment(sketch, "E5837", {"start": v(112.9, 4.55) * mm, "end": v(112.95, 4.37) * mm});
            skLineSegment(sketch, "E5838", {"start": v(112.95, 4.37) * mm, "end": v(112.99, 4.19) * mm});
            skLineSegment(sketch, "E5839", {"start": v(112.99, 4.19) * mm, "end": v(113, 4) * mm});
            skLineSegment(sketch, "E5840", {"start": v(113, 4) * mm, "end": v(112.99, 3.81) * mm});
            skLineSegment(sketch, "E5841", {"start": v(112.99, 3.81) * mm, "end": v(112.95, 3.63) * mm});
            skLineSegment(sketch, "E5842", {"start": v(112.95, 3.63) * mm, "end": v(112.9, 3.45) * mm});
            skLineSegment(sketch, "E5843", {"start": v(112.9, 3.45) * mm, "end": v(112.81, 3.28) * mm});
            skLineSegment(sketch, "E5844", {"start": v(112.81, 3.28) * mm, "end": v(112.71, 3.12) * mm});
            skLineSegment(sketch, "E5845", {"start": v(112.71, 3.12) * mm, "end": v(112.6, 2.97) * mm});
            skLineSegment(sketch, "E5846", {"start": v(112.6, 2.97) * mm, "end": v(112.46, 2.84) * mm});
            skLineSegment(sketch, "E5847", {"start": v(112.46, 2.84) * mm, "end": v(112.3, 2.73) * mm});
            skLineSegment(sketch, "E5848", {"start": v(112.3, 2.73) * mm, "end": v(112.14, 2.64) * mm});
            skLineSegment(sketch, "E5849", {"start": v(112.14, 2.64) * mm, "end": v(111.96, 2.57) * mm});
            skLineSegment(sketch, "E5850", {"start": v(111.96, 2.57) * mm, "end": v(111.78, 2.53) * mm});
            skLineSegment(sketch, "E5851", {"start": v(111.78, 2.53) * mm, "end": v(111.6, 2.5) * mm});
            skLineSegment(sketch, "E5852", {"start": v(111.6, 2.5) * mm, "end": v(111.4, 2.5) * mm});
            skLineSegment(sketch, "E5853", {"start": v(204.9, -2.5) * mm, "end": v(204.72, -2.47) * mm});
            skLineSegment(sketch, "E5854", {"start": v(204.72, -2.47) * mm, "end": v(204.54, -2.43) * mm});
            skLineSegment(sketch, "E5855", {"start": v(204.54, -2.43) * mm, "end": v(204.36, -2.36) * mm});
            skLineSegment(sketch, "E5856", {"start": v(204.36, -2.36) * mm, "end": v(204.2, -2.27) * mm});
            skLineSegment(sketch, "E5857", {"start": v(204.2, -2.27) * mm, "end": v(204.04, -2.16) * mm});
            skLineSegment(sketch, "E5858", {"start": v(204.04, -2.16) * mm, "end": v(203.9, -2.03) * mm});
            skLineSegment(sketch, "E5859", {"start": v(203.9, -2.03) * mm, "end": v(203.79, -1.88) * mm});
            skLineSegment(sketch, "E5860", {"start": v(203.79, -1.88) * mm, "end": v(203.69, -1.72) * mm});
            skLineSegment(sketch, "E5861", {"start": v(203.69, -1.72) * mm, "end": v(203.6, -1.55) * mm});
            skLineSegment(sketch, "E5862", {"start": v(203.6, -1.55) * mm, "end": v(203.55, -1.37) * mm});
            skLineSegment(sketch, "E5863", {"start": v(203.55, -1.37) * mm, "end": v(203.51, -1.19) * mm});
            skLineSegment(sketch, "E5864", {"start": v(203.51, -1.19) * mm, "end": v(203.5, -1) * mm});
            skLineSegment(sketch, "E5865", {"start": v(203.5, -1) * mm, "end": v(203.51, -0.81) * mm});
            skLineSegment(sketch, "E5866", {"start": v(203.51, -0.81) * mm, "end": v(203.55, -0.63) * mm});
            skLineSegment(sketch, "E5867", {"start": v(203.55, -0.63) * mm, "end": v(203.6, -0.45) * mm});
            skLineSegment(sketch, "E5868", {"start": v(203.6, -0.45) * mm, "end": v(203.69, -0.28) * mm});
            skLineSegment(sketch, "E5869", {"start": v(203.69, -0.28) * mm, "end": v(203.79, -0.12) * mm});
            skLineSegment(sketch, "E5870", {"start": v(203.79, -0.12) * mm, "end": v(203.9, 0.03) * mm});
            skLineSegment(sketch, "E5871", {"start": v(203.9, 0.03) * mm, "end": v(204.04, 0.16) * mm});
            skLineSegment(sketch, "E5872", {"start": v(204.04, 0.16) * mm, "end": v(204.2, 0.27) * mm});
            skLineSegment(sketch, "E5873", {"start": v(204.2, 0.27) * mm, "end": v(204.36, 0.36) * mm});
            skLineSegment(sketch, "E5874", {"start": v(204.36, 0.36) * mm, "end": v(204.54, 0.43) * mm});
            skLineSegment(sketch, "E5875", {"start": v(204.54, 0.43) * mm, "end": v(204.72, 0.47) * mm});
            skLineSegment(sketch, "E5876", {"start": v(204.72, 0.47) * mm, "end": v(204.9, 0.5) * mm});
            skLineSegment(sketch, "E5877", {"start": v(204.9, 0.5) * mm, "end": v(205.1, 0.5) * mm});
            skLineSegment(sketch, "E5878", {"start": v(205.1, 0.5) * mm, "end": v(205.28, 0.47) * mm});
            skLineSegment(sketch, "E5879", {"start": v(205.28, 0.47) * mm, "end": v(205.46, 0.43) * mm});
            skLineSegment(sketch, "E5880", {"start": v(205.46, 0.43) * mm, "end": v(205.64, 0.36) * mm});
            skLineSegment(sketch, "E5881", {"start": v(205.64, 0.36) * mm, "end": v(205.8, 0.27) * mm});
            skLineSegment(sketch, "E5882", {"start": v(205.8, 0.27) * mm, "end": v(205.96, 0.16) * mm});
            skLineSegment(sketch, "E5883", {"start": v(205.96, 0.16) * mm, "end": v(206.1, 0.03) * mm});
            skLineSegment(sketch, "E5884", {"start": v(206.1, 0.03) * mm, "end": v(206.21, -0.12) * mm});
            skLineSegment(sketch, "E5885", {"start": v(206.21, -0.12) * mm, "end": v(206.31, -0.28) * mm});
            skLineSegment(sketch, "E5886", {"start": v(206.31, -0.28) * mm, "end": v(206.4, -0.45) * mm});
            skLineSegment(sketch, "E5887", {"start": v(206.4, -0.45) * mm, "end": v(206.45, -0.63) * mm});
            skLineSegment(sketch, "E5888", {"start": v(206.45, -0.63) * mm, "end": v(206.49, -0.81) * mm});
            skLineSegment(sketch, "E5889", {"start": v(206.49, -0.81) * mm, "end": v(206.5, -1) * mm});
            skLineSegment(sketch, "E5890", {"start": v(206.5, -1) * mm, "end": v(206.49, -1.19) * mm});
            skLineSegment(sketch, "E5891", {"start": v(206.49, -1.19) * mm, "end": v(206.45, -1.37) * mm});
            skLineSegment(sketch, "E5892", {"start": v(206.45, -1.37) * mm, "end": v(206.4, -1.55) * mm});
            skLineSegment(sketch, "E5893", {"start": v(206.4, -1.55) * mm, "end": v(206.31, -1.72) * mm});
            skLineSegment(sketch, "E5894", {"start": v(206.31, -1.72) * mm, "end": v(206.21, -1.88) * mm});
            skLineSegment(sketch, "E5895", {"start": v(206.21, -1.88) * mm, "end": v(206.1, -2.03) * mm});
            skLineSegment(sketch, "E5896", {"start": v(206.1, -2.03) * mm, "end": v(205.96, -2.16) * mm});
            skLineSegment(sketch, "E5897", {"start": v(205.96, -2.16) * mm, "end": v(205.8, -2.27) * mm});
            skLineSegment(sketch, "E5898", {"start": v(205.8, -2.27) * mm, "end": v(205.64, -2.36) * mm});
            skLineSegment(sketch, "E5899", {"start": v(205.64, -2.36) * mm, "end": v(205.46, -2.43) * mm});
            skLineSegment(sketch, "E5900", {"start": v(205.46, -2.43) * mm, "end": v(205.28, -2.47) * mm});
            skLineSegment(sketch, "E5901", {"start": v(205.28, -2.47) * mm, "end": v(205.1, -2.5) * mm});
            skLineSegment(sketch, "E5902", {"start": v(205.1, -2.5) * mm, "end": v(204.9, -2.5) * mm});
            skLineSegment(sketch, "E5903", {"start": v(111.4, -3.5) * mm, "end": v(111.22, -3.47) * mm});
            skLineSegment(sketch, "E5904", {"start": v(111.22, -3.47) * mm, "end": v(111.04, -3.43) * mm});
            skLineSegment(sketch, "E5905", {"start": v(111.04, -3.43) * mm, "end": v(110.86, -3.36) * mm});
            skLineSegment(sketch, "E5906", {"start": v(110.86, -3.36) * mm, "end": v(110.7, -3.27) * mm});
            skLineSegment(sketch, "E5907", {"start": v(110.7, -3.27) * mm, "end": v(110.54, -3.16) * mm});
            skLineSegment(sketch, "E5908", {"start": v(110.54, -3.16) * mm, "end": v(110.4, -3.03) * mm});
            skLineSegment(sketch, "E5909", {"start": v(110.4, -3.03) * mm, "end": v(110.29, -2.88) * mm});
            skLineSegment(sketch, "E5910", {"start": v(110.29, -2.88) * mm, "end": v(110.19, -2.72) * mm});
            skLineSegment(sketch, "E5911", {"start": v(110.19, -2.72) * mm, "end": v(110.1, -2.55) * mm});
            skLineSegment(sketch, "E5912", {"start": v(110.1, -2.55) * mm, "end": v(110.05, -2.37) * mm});
            skLineSegment(sketch, "E5913", {"start": v(110.05, -2.37) * mm, "end": v(110.01, -2.19) * mm});
            skLineSegment(sketch, "E5914", {"start": v(110.01, -2.19) * mm, "end": v(110, -2) * mm});
            skLineSegment(sketch, "E5915", {"start": v(110, -2) * mm, "end": v(110.01, -1.81) * mm});
            skLineSegment(sketch, "E5916", {"start": v(110.01, -1.81) * mm, "end": v(110.05, -1.63) * mm});
            skLineSegment(sketch, "E5917", {"start": v(110.05, -1.63) * mm, "end": v(110.1, -1.45) * mm});
            skLineSegment(sketch, "E5918", {"start": v(110.1, -1.45) * mm, "end": v(110.19, -1.28) * mm});
            skLineSegment(sketch, "E5919", {"start": v(110.19, -1.28) * mm, "end": v(110.29, -1.12) * mm});
            skLineSegment(sketch, "E5920", {"start": v(110.29, -1.12) * mm, "end": v(110.4, -0.97) * mm});
            skLineSegment(sketch, "E5921", {"start": v(110.4, -0.97) * mm, "end": v(110.54, -0.84) * mm});
            skLineSegment(sketch, "E5922", {"start": v(110.54, -0.84) * mm, "end": v(110.7, -0.73) * mm});
            skLineSegment(sketch, "E5923", {"start": v(110.7, -0.73) * mm, "end": v(110.86, -0.64) * mm});
            skLineSegment(sketch, "E5924", {"start": v(110.86, -0.64) * mm, "end": v(111.04, -0.57) * mm});
            skLineSegment(sketch, "E5925", {"start": v(111.04, -0.57) * mm, "end": v(111.22, -0.53) * mm});
            skLineSegment(sketch, "E5926", {"start": v(111.22, -0.53) * mm, "end": v(111.4, -0.5) * mm});
            skLineSegment(sketch, "E5927", {"start": v(111.4, -0.5) * mm, "end": v(111.6, -0.5) * mm});
            skLineSegment(sketch, "E5928", {"start": v(111.6, -0.5) * mm, "end": v(111.78, -0.53) * mm});
            skLineSegment(sketch, "E5929", {"start": v(111.78, -0.53) * mm, "end": v(111.96, -0.57) * mm});
            skLineSegment(sketch, "E5930", {"start": v(111.96, -0.57) * mm, "end": v(112.14, -0.64) * mm});
            skLineSegment(sketch, "E5931", {"start": v(112.14, -0.64) * mm, "end": v(112.3, -0.73) * mm});
            skLineSegment(sketch, "E5932", {"start": v(112.3, -0.73) * mm, "end": v(112.46, -0.84) * mm});
            skLineSegment(sketch, "E5933", {"start": v(112.46, -0.84) * mm, "end": v(112.6, -0.97) * mm});
            skLineSegment(sketch, "E5934", {"start": v(112.6, -0.97) * mm, "end": v(112.71, -1.12) * mm});
            skLineSegment(sketch, "E5935", {"start": v(112.71, -1.12) * mm, "end": v(112.81, -1.28) * mm});
            skLineSegment(sketch, "E5936", {"start": v(112.81, -1.28) * mm, "end": v(112.9, -1.45) * mm});
            skLineSegment(sketch, "E5937", {"start": v(112.9, -1.45) * mm, "end": v(112.95, -1.63) * mm});
            skLineSegment(sketch, "E5938", {"start": v(112.95, -1.63) * mm, "end": v(112.99, -1.81) * mm});
            skLineSegment(sketch, "E5939", {"start": v(112.99, -1.81) * mm, "end": v(113, -2) * mm});
            skLineSegment(sketch, "E5940", {"start": v(113, -2) * mm, "end": v(112.99, -2.19) * mm});
            skLineSegment(sketch, "E5941", {"start": v(112.99, -2.19) * mm, "end": v(112.95, -2.37) * mm});
            skLineSegment(sketch, "E5942", {"start": v(112.95, -2.37) * mm, "end": v(112.9, -2.55) * mm});
            skLineSegment(sketch, "E5943", {"start": v(112.9, -2.55) * mm, "end": v(112.81, -2.72) * mm});
            skLineSegment(sketch, "E5944", {"start": v(112.81, -2.72) * mm, "end": v(112.71, -2.88) * mm});
            skLineSegment(sketch, "E5945", {"start": v(112.71, -2.88) * mm, "end": v(112.6, -3.03) * mm});
            skLineSegment(sketch, "E5946", {"start": v(112.6, -3.03) * mm, "end": v(112.46, -3.16) * mm});
            skLineSegment(sketch, "E5947", {"start": v(112.46, -3.16) * mm, "end": v(112.3, -3.27) * mm});
            skLineSegment(sketch, "E5948", {"start": v(112.3, -3.27) * mm, "end": v(112.14, -3.36) * mm});
            skLineSegment(sketch, "E5949", {"start": v(112.14, -3.36) * mm, "end": v(111.96, -3.43) * mm});
            skLineSegment(sketch, "E5950", {"start": v(111.96, -3.43) * mm, "end": v(111.78, -3.47) * mm});
            skLineSegment(sketch, "E5951", {"start": v(111.78, -3.47) * mm, "end": v(111.6, -3.5) * mm});
            skLineSegment(sketch, "E5952", {"start": v(111.6, -3.5) * mm, "end": v(111.4, -3.5) * mm});
            skLineSegment(sketch, "E5953", {"start": v(154.07, -80.99) * mm, "end": v(153.39, -80.9) * mm});
            skLineSegment(sketch, "E5954", {"start": v(153.39, -80.9) * mm, "end": v(152.72, -80.73) * mm});
            skLineSegment(sketch, "E5955", {"start": v(152.72, -80.73) * mm, "end": v(152.08, -80.48) * mm});
            skLineSegment(sketch, "E5956", {"start": v(152.08, -80.48) * mm, "end": v(151.47, -80.14) * mm});
            skLineSegment(sketch, "E5957", {"start": v(151.47, -80.14) * mm, "end": v(150.91, -79.74) * mm});
            skLineSegment(sketch, "E5958", {"start": v(150.91, -79.74) * mm, "end": v(150.41, -79.27) * mm});
            skLineSegment(sketch, "E5959", {"start": v(150.41, -79.27) * mm, "end": v(149.97, -78.73) * mm});
            skLineSegment(sketch, "E5960", {"start": v(149.97, -78.73) * mm, "end": v(149.6, -78.15) * mm});
            skLineSegment(sketch, "E5961", {"start": v(149.6, -78.15) * mm, "end": v(149.3, -77.53) * mm});
            skLineSegment(sketch, "E5962", {"start": v(149.3, -77.53) * mm, "end": v(149.1, -76.87) * mm});
            skLineSegment(sketch, "E5963", {"start": v(149.1, -76.87) * mm, "end": v(148.96, -76.19) * mm});
            skLineSegment(sketch, "E5964", {"start": v(148.96, -76.19) * mm, "end": v(148.92, -75.5) * mm});
            skLineSegment(sketch, "E5965", {"start": v(148.92, -75.5) * mm, "end": v(148.96, -74.81) * mm});
            skLineSegment(sketch, "E5966", {"start": v(148.96, -74.81) * mm, "end": v(149.1, -74.13) * mm});
            skLineSegment(sketch, "E5967", {"start": v(149.1, -74.13) * mm, "end": v(149.3, -73.47) * mm});
            skLineSegment(sketch, "E5968", {"start": v(149.3, -73.47) * mm, "end": v(149.6, -72.85) * mm});
            skLineSegment(sketch, "E5969", {"start": v(149.6, -72.85) * mm, "end": v(149.97, -72.27) * mm});
            skLineSegment(sketch, "E5970", {"start": v(149.97, -72.27) * mm, "end": v(150.41, -71.74) * mm});
            skLineSegment(sketch, "E5971", {"start": v(150.41, -71.74) * mm, "end": v(201, -21.16) * mm});
            skLineSegment(sketch, "E5972", {"start": v(201, -21.16) * mm, "end": v(201.5, -20.68) * mm});
            skLineSegment(sketch, "E5973", {"start": v(201.5, -20.68) * mm, "end": v(202.05, -20.28) * mm});
            skLineSegment(sketch, "E5974", {"start": v(202.05, -20.28) * mm, "end": v(202.66, -19.94) * mm});
            skLineSegment(sketch, "E5975", {"start": v(202.66, -19.94) * mm, "end": v(203.3, -19.7) * mm});
            skLineSegment(sketch, "E5976", {"start": v(203.3, -19.7) * mm, "end": v(203.97, -19.52) * mm});
            skLineSegment(sketch, "E5977", {"start": v(203.97, -19.52) * mm, "end": v(204.66, -19.43) * mm});
            skLineSegment(sketch, "E5978", {"start": v(204.66, -19.43) * mm, "end": v(205.34, -19.43) * mm});
            skLineSegment(sketch, "E5979", {"start": v(205.34, -19.43) * mm, "end": v(206.03, -19.52) * mm});
            skLineSegment(sketch, "E5980", {"start": v(206.03, -19.52) * mm, "end": v(206.7, -19.7) * mm});
            skLineSegment(sketch, "E5981", {"start": v(206.7, -19.7) * mm, "end": v(207.34, -19.94) * mm});
            skLineSegment(sketch, "E5982", {"start": v(207.34, -19.94) * mm, "end": v(207.95, -20.28) * mm});
            skLineSegment(sketch, "E5983", {"start": v(207.95, -20.28) * mm, "end": v(208.5, -20.68) * mm});
            skLineSegment(sketch, "E5984", {"start": v(208.5, -20.68) * mm, "end": v(209, -21.16) * mm});
            skLineSegment(sketch, "E5985", {"start": v(209, -21.16) * mm, "end": v(259.59, -71.73) * mm});
            skLineSegment(sketch, "E5986", {"start": v(259.59, -71.74) * mm, "end": v(260.03, -72.27) * mm});
            skLineSegment(sketch, "E5987", {"start": v(260.03, -72.27) * mm, "end": v(260.4, -72.85) * mm});
            skLineSegment(sketch, "E5988", {"start": v(260.4, -72.85) * mm, "end": v(260.7, -73.47) * mm});
            skLineSegment(sketch, "E5989", {"start": v(260.7, -73.47) * mm, "end": v(260.9, -74.13) * mm});
            skLineSegment(sketch, "E5990", {"start": v(260.9, -74.13) * mm, "end": v(261.04, -74.81) * mm});
            skLineSegment(sketch, "E5991", {"start": v(261.04, -74.81) * mm, "end": v(261.08, -75.5) * mm});
            skLineSegment(sketch, "E5992", {"start": v(261.08, -75.5) * mm, "end": v(261.04, -76.19) * mm});
            skLineSegment(sketch, "E5993", {"start": v(261.04, -76.19) * mm, "end": v(260.9, -76.87) * mm});
            skLineSegment(sketch, "E5994", {"start": v(260.9, -76.87) * mm, "end": v(260.7, -77.53) * mm});
            skLineSegment(sketch, "E5995", {"start": v(260.7, -77.53) * mm, "end": v(260.4, -78.15) * mm});
            skLineSegment(sketch, "E5996", {"start": v(260.4, -78.15) * mm, "end": v(260.03, -78.73) * mm});
            skLineSegment(sketch, "E5997", {"start": v(260.03, -78.73) * mm, "end": v(259.59, -79.27) * mm});
            skLineSegment(sketch, "E5998", {"start": v(259.59, -79.27) * mm, "end": v(259.09, -79.74) * mm});
            skLineSegment(sketch, "E5999", {"start": v(259.09, -79.74) * mm, "end": v(258.53, -80.14) * mm});
            skLineSegment(sketch, "E6000", {"start": v(258.53, -80.14) * mm, "end": v(257.92, -80.48) * mm});
            skLineSegment(sketch, "E6001", {"start": v(257.92, -80.48) * mm, "end": v(257.28, -80.73) * mm});
            skLineSegment(sketch, "E6002", {"start": v(257.28, -80.73) * mm, "end": v(256.6, -80.9) * mm});
            skLineSegment(sketch, "E6003", {"start": v(256.6, -80.9) * mm, "end": v(255.93, -80.99) * mm});
            skLineSegment(sketch, "E6004", {"start": v(255.93, -80.99) * mm, "end": v(154.07, -80.99) * mm});
            skLineSegment(sketch, "E6005", {"start": v(247.9, -49.5) * mm, "end": v(247.72, -49.47) * mm});
            skLineSegment(sketch, "E6006", {"start": v(247.72, -49.47) * mm, "end": v(247.54, -49.43) * mm});
            skLineSegment(sketch, "E6007", {"start": v(247.54, -49.43) * mm, "end": v(247.36, -49.36) * mm});
            skLineSegment(sketch, "E6008", {"start": v(247.36, -49.36) * mm, "end": v(247.2, -49.27) * mm});
            skLineSegment(sketch, "E6009", {"start": v(247.2, -49.27) * mm, "end": v(247.04, -49.16) * mm});
            skLineSegment(sketch, "E6010", {"start": v(247.04, -49.16) * mm, "end": v(246.9, -49.03) * mm});
            skLineSegment(sketch, "E6011", {"start": v(246.9, -49.03) * mm, "end": v(246.79, -48.88) * mm});
            skLineSegment(sketch, "E6012", {"start": v(246.79, -48.88) * mm, "end": v(246.69, -48.72) * mm});
            skLineSegment(sketch, "E6013", {"start": v(246.69, -48.72) * mm, "end": v(246.6, -48.55) * mm});
            skLineSegment(sketch, "E6014", {"start": v(246.6, -48.55) * mm, "end": v(246.55, -48.37) * mm});
            skLineSegment(sketch, "E6015", {"start": v(246.55, -48.37) * mm, "end": v(246.51, -48.19) * mm});
            skLineSegment(sketch, "E6016", {"start": v(246.51, -48.19) * mm, "end": v(246.5, -48) * mm});
            skLineSegment(sketch, "E6017", {"start": v(246.5, -48) * mm, "end": v(246.51, -47.81) * mm});
            skLineSegment(sketch, "E6018", {"start": v(246.51, -47.81) * mm, "end": v(246.55, -47.63) * mm});
            skLineSegment(sketch, "E6019", {"start": v(246.55, -47.63) * mm, "end": v(246.6, -47.45) * mm});
            skLineSegment(sketch, "E6020", {"start": v(246.6, -47.45) * mm, "end": v(246.69, -47.28) * mm});
            skLineSegment(sketch, "E6021", {"start": v(246.69, -47.28) * mm, "end": v(246.79, -47.12) * mm});
            skLineSegment(sketch, "E6022", {"start": v(246.79, -47.12) * mm, "end": v(246.9, -46.97) * mm});
            skLineSegment(sketch, "E6023", {"start": v(246.9, -46.97) * mm, "end": v(247.04, -46.84) * mm});
            skLineSegment(sketch, "E6024", {"start": v(247.04, -46.84) * mm, "end": v(247.2, -46.73) * mm});
            skLineSegment(sketch, "E6025", {"start": v(247.2, -46.73) * mm, "end": v(247.36, -46.64) * mm});
            skLineSegment(sketch, "E6026", {"start": v(247.36, -46.64) * mm, "end": v(247.54, -46.57) * mm});
            skLineSegment(sketch, "E6027", {"start": v(247.54, -46.57) * mm, "end": v(247.72, -46.53) * mm});
            skLineSegment(sketch, "E6028", {"start": v(247.72, -46.53) * mm, "end": v(247.9, -46.5) * mm});
            skLineSegment(sketch, "E6029", {"start": v(247.9, -46.5) * mm, "end": v(248.1, -46.5) * mm});
            skLineSegment(sketch, "E6030", {"start": v(248.1, -46.5) * mm, "end": v(248.28, -46.53) * mm});
            skLineSegment(sketch, "E6031", {"start": v(248.28, -46.53) * mm, "end": v(248.46, -46.57) * mm});
            skLineSegment(sketch, "E6032", {"start": v(248.46, -46.57) * mm, "end": v(248.64, -46.64) * mm});
            skLineSegment(sketch, "E6033", {"start": v(248.64, -46.64) * mm, "end": v(248.8, -46.73) * mm});
            skLineSegment(sketch, "E6034", {"start": v(248.8, -46.73) * mm, "end": v(248.96, -46.84) * mm});
            skLineSegment(sketch, "E6035", {"start": v(248.96, -46.84) * mm, "end": v(249.1, -46.97) * mm});
            skLineSegment(sketch, "E6036", {"start": v(249.1, -46.97) * mm, "end": v(249.21, -47.12) * mm});
            skLineSegment(sketch, "E6037", {"start": v(249.21, -47.12) * mm, "end": v(249.31, -47.28) * mm});
            skLineSegment(sketch, "E6038", {"start": v(249.31, -47.28) * mm, "end": v(249.4, -47.45) * mm});
            skLineSegment(sketch, "E6039", {"start": v(249.4, -47.45) * mm, "end": v(249.45, -47.63) * mm});
            skLineSegment(sketch, "E6040", {"start": v(249.45, -47.63) * mm, "end": v(249.49, -47.81) * mm});
            skLineSegment(sketch, "E6041", {"start": v(249.49, -47.81) * mm, "end": v(249.5, -48) * mm});
            skLineSegment(sketch, "E6042", {"start": v(249.5, -48) * mm, "end": v(249.49, -48.19) * mm});
            skLineSegment(sketch, "E6043", {"start": v(249.49, -48.19) * mm, "end": v(249.45, -48.37) * mm});
            skLineSegment(sketch, "E6044", {"start": v(249.45, -48.37) * mm, "end": v(249.4, -48.55) * mm});
            skLineSegment(sketch, "E6045", {"start": v(249.4, -48.55) * mm, "end": v(249.31, -48.72) * mm});
            skLineSegment(sketch, "E6046", {"start": v(249.31, -48.72) * mm, "end": v(249.21, -48.88) * mm});
            skLineSegment(sketch, "E6047", {"start": v(249.21, -48.88) * mm, "end": v(249.1, -49.03) * mm});
            skLineSegment(sketch, "E6048", {"start": v(249.1, -49.03) * mm, "end": v(248.96, -49.16) * mm});
            skLineSegment(sketch, "E6049", {"start": v(248.96, -49.16) * mm, "end": v(248.8, -49.27) * mm});
            skLineSegment(sketch, "E6050", {"start": v(248.8, -49.27) * mm, "end": v(248.64, -49.36) * mm});
            skLineSegment(sketch, "E6051", {"start": v(248.64, -49.36) * mm, "end": v(248.46, -49.43) * mm});
            skLineSegment(sketch, "E6052", {"start": v(248.46, -49.43) * mm, "end": v(248.28, -49.47) * mm});
            skLineSegment(sketch, "E6053", {"start": v(248.28, -49.47) * mm, "end": v(248.1, -49.5) * mm});
            skLineSegment(sketch, "E6054", {"start": v(248.1, -49.5) * mm, "end": v(247.9, -49.5) * mm});
            skLineSegment(sketch, "E6055", {"start": v(271.9, -49.5) * mm, "end": v(271.72, -49.47) * mm});
            skLineSegment(sketch, "E6056", {"start": v(271.72, -49.47) * mm, "end": v(271.54, -49.43) * mm});
            skLineSegment(sketch, "E6057", {"start": v(271.54, -49.43) * mm, "end": v(271.36, -49.36) * mm});
            skLineSegment(sketch, "E6058", {"start": v(271.36, -49.36) * mm, "end": v(271.2, -49.27) * mm});
            skLineSegment(sketch, "E6059", {"start": v(271.2, -49.27) * mm, "end": v(271.04, -49.16) * mm});
            skLineSegment(sketch, "E6060", {"start": v(271.04, -49.16) * mm, "end": v(270.9, -49.03) * mm});
            skLineSegment(sketch, "E6061", {"start": v(270.9, -49.03) * mm, "end": v(270.79, -48.88) * mm});
            skLineSegment(sketch, "E6062", {"start": v(270.79, -48.88) * mm, "end": v(270.69, -48.72) * mm});
            skLineSegment(sketch, "E6063", {"start": v(270.69, -48.72) * mm, "end": v(270.6, -48.55) * mm});
            skLineSegment(sketch, "E6064", {"start": v(270.6, -48.55) * mm, "end": v(270.55, -48.37) * mm});
            skLineSegment(sketch, "E6065", {"start": v(270.55, -48.37) * mm, "end": v(270.51, -48.19) * mm});
            skLineSegment(sketch, "E6066", {"start": v(270.51, -48.19) * mm, "end": v(270.5, -48) * mm});
            skLineSegment(sketch, "E6067", {"start": v(270.5, -48) * mm, "end": v(270.51, -47.81) * mm});
            skLineSegment(sketch, "E6068", {"start": v(270.51, -47.81) * mm, "end": v(270.55, -47.63) * mm});
            skLineSegment(sketch, "E6069", {"start": v(270.55, -47.63) * mm, "end": v(270.6, -47.45) * mm});
            skLineSegment(sketch, "E6070", {"start": v(270.6, -47.45) * mm, "end": v(270.69, -47.28) * mm});
            skLineSegment(sketch, "E6071", {"start": v(270.69, -47.28) * mm, "end": v(270.79, -47.12) * mm});
            skLineSegment(sketch, "E6072", {"start": v(270.79, -47.12) * mm, "end": v(270.9, -46.97) * mm});
            skLineSegment(sketch, "E6073", {"start": v(270.9, -46.97) * mm, "end": v(271.04, -46.84) * mm});
            skLineSegment(sketch, "E6074", {"start": v(271.04, -46.84) * mm, "end": v(271.2, -46.73) * mm});
            skLineSegment(sketch, "E6075", {"start": v(271.2, -46.73) * mm, "end": v(271.36, -46.64) * mm});
            skLineSegment(sketch, "E6076", {"start": v(271.36, -46.64) * mm, "end": v(271.54, -46.57) * mm});
            skLineSegment(sketch, "E6077", {"start": v(271.54, -46.57) * mm, "end": v(271.72, -46.53) * mm});
            skLineSegment(sketch, "E6078", {"start": v(271.72, -46.53) * mm, "end": v(271.9, -46.5) * mm});
            skLineSegment(sketch, "E6079", {"start": v(271.9, -46.5) * mm, "end": v(272.1, -46.5) * mm});
            skLineSegment(sketch, "E6080", {"start": v(272.1, -46.5) * mm, "end": v(272.28, -46.53) * mm});
            skLineSegment(sketch, "E6081", {"start": v(272.28, -46.53) * mm, "end": v(272.46, -46.57) * mm});
            skLineSegment(sketch, "E6082", {"start": v(272.46, -46.57) * mm, "end": v(272.64, -46.64) * mm});
            skLineSegment(sketch, "E6083", {"start": v(272.64, -46.64) * mm, "end": v(272.8, -46.73) * mm});
            skLineSegment(sketch, "E6084", {"start": v(272.8, -46.73) * mm, "end": v(272.96, -46.84) * mm});
            skLineSegment(sketch, "E6085", {"start": v(272.96, -46.84) * mm, "end": v(273.1, -46.97) * mm});
            skLineSegment(sketch, "E6086", {"start": v(273.1, -46.97) * mm, "end": v(273.21, -47.12) * mm});
            skLineSegment(sketch, "E6087", {"start": v(273.21, -47.12) * mm, "end": v(273.31, -47.28) * mm});
            skLineSegment(sketch, "E6088", {"start": v(273.31, -47.28) * mm, "end": v(273.4, -47.45) * mm});
            skLineSegment(sketch, "E6089", {"start": v(273.4, -47.45) * mm, "end": v(273.45, -47.63) * mm});
            skLineSegment(sketch, "E6090", {"start": v(273.45, -47.63) * mm, "end": v(273.49, -47.81) * mm});
            skLineSegment(sketch, "E6091", {"start": v(273.49, -47.81) * mm, "end": v(273.5, -48) * mm});
            skLineSegment(sketch, "E6092", {"start": v(273.5, -48) * mm, "end": v(273.49, -48.19) * mm});
            skLineSegment(sketch, "E6093", {"start": v(273.49, -48.19) * mm, "end": v(273.45, -48.37) * mm});
            skLineSegment(sketch, "E6094", {"start": v(273.45, -48.37) * mm, "end": v(273.4, -48.55) * mm});
            skLineSegment(sketch, "E6095", {"start": v(273.4, -48.55) * mm, "end": v(273.31, -48.72) * mm});
            skLineSegment(sketch, "E6096", {"start": v(273.31, -48.72) * mm, "end": v(273.21, -48.88) * mm});
            skLineSegment(sketch, "E6097", {"start": v(273.21, -48.88) * mm, "end": v(273.1, -49.03) * mm});
            skLineSegment(sketch, "E6098", {"start": v(273.1, -49.03) * mm, "end": v(272.96, -49.16) * mm});
            skLineSegment(sketch, "E6099", {"start": v(272.96, -49.16) * mm, "end": v(272.8, -49.27) * mm});
            skLineSegment(sketch, "E6100", {"start": v(272.8, -49.27) * mm, "end": v(272.64, -49.36) * mm});
            skLineSegment(sketch, "E6101", {"start": v(272.64, -49.36) * mm, "end": v(272.46, -49.43) * mm});
            skLineSegment(sketch, "E6102", {"start": v(272.46, -49.43) * mm, "end": v(272.28, -49.47) * mm});
            skLineSegment(sketch, "E6103", {"start": v(272.28, -49.47) * mm, "end": v(272.1, -49.5) * mm});
            skLineSegment(sketch, "E6104", {"start": v(272.1, -49.5) * mm, "end": v(271.9, -49.5) * mm});
            skLineSegment(sketch, "E6105", {"start": v(137.9, -49.5) * mm, "end": v(137.72, -49.47) * mm});
            skLineSegment(sketch, "E6106", {"start": v(137.72, -49.47) * mm, "end": v(137.54, -49.43) * mm});
            skLineSegment(sketch, "E6107", {"start": v(137.54, -49.43) * mm, "end": v(137.36, -49.36) * mm});
            skLineSegment(sketch, "E6108", {"start": v(137.36, -49.36) * mm, "end": v(137.2, -49.27) * mm});
            skLineSegment(sketch, "E6109", {"start": v(137.2, -49.27) * mm, "end": v(137.04, -49.16) * mm});
            skLineSegment(sketch, "E6110", {"start": v(137.04, -49.16) * mm, "end": v(136.9, -49.03) * mm});
            skLineSegment(sketch, "E6111", {"start": v(136.9, -49.03) * mm, "end": v(136.79, -48.88) * mm});
            skLineSegment(sketch, "E6112", {"start": v(136.79, -48.88) * mm, "end": v(136.69, -48.72) * mm});
            skLineSegment(sketch, "E6113", {"start": v(136.69, -48.72) * mm, "end": v(136.6, -48.55) * mm});
            skLineSegment(sketch, "E6114", {"start": v(136.6, -48.55) * mm, "end": v(136.55, -48.37) * mm});
            skLineSegment(sketch, "E6115", {"start": v(136.55, -48.37) * mm, "end": v(136.51, -48.19) * mm});
            skLineSegment(sketch, "E6116", {"start": v(136.51, -48.19) * mm, "end": v(136.5, -48) * mm});
            skLineSegment(sketch, "E6117", {"start": v(136.5, -48) * mm, "end": v(136.51, -47.81) * mm});
            skLineSegment(sketch, "E6118", {"start": v(136.51, -47.81) * mm, "end": v(136.55, -47.63) * mm});
            skLineSegment(sketch, "E6119", {"start": v(136.55, -47.63) * mm, "end": v(136.6, -47.45) * mm});
            skLineSegment(sketch, "E6120", {"start": v(136.6, -47.45) * mm, "end": v(136.69, -47.28) * mm});
            skLineSegment(sketch, "E6121", {"start": v(136.69, -47.28) * mm, "end": v(136.79, -47.12) * mm});
            skLineSegment(sketch, "E6122", {"start": v(136.79, -47.12) * mm, "end": v(136.9, -46.97) * mm});
            skLineSegment(sketch, "E6123", {"start": v(136.9, -46.97) * mm, "end": v(137.04, -46.84) * mm});
            skLineSegment(sketch, "E6124", {"start": v(137.04, -46.84) * mm, "end": v(137.2, -46.73) * mm});
            skLineSegment(sketch, "E6125", {"start": v(137.2, -46.73) * mm, "end": v(137.36, -46.64) * mm});
            skLineSegment(sketch, "E6126", {"start": v(137.36, -46.64) * mm, "end": v(137.54, -46.57) * mm});
            skLineSegment(sketch, "E6127", {"start": v(137.54, -46.57) * mm, "end": v(137.72, -46.53) * mm});
            skLineSegment(sketch, "E6128", {"start": v(137.72, -46.53) * mm, "end": v(137.9, -46.5) * mm});
            skLineSegment(sketch, "E6129", {"start": v(137.9, -46.5) * mm, "end": v(138.1, -46.5) * mm});
            skLineSegment(sketch, "E6130", {"start": v(138.1, -46.5) * mm, "end": v(138.28, -46.53) * mm});
            skLineSegment(sketch, "E6131", {"start": v(138.28, -46.53) * mm, "end": v(138.46, -46.57) * mm});
            skLineSegment(sketch, "E6132", {"start": v(138.46, -46.57) * mm, "end": v(138.64, -46.64) * mm});
            skLineSegment(sketch, "E6133", {"start": v(138.64, -46.64) * mm, "end": v(138.8, -46.73) * mm});
            skLineSegment(sketch, "E6134", {"start": v(138.8, -46.73) * mm, "end": v(138.96, -46.84) * mm});
            skLineSegment(sketch, "E6135", {"start": v(138.96, -46.84) * mm, "end": v(139.1, -46.97) * mm});
            skLineSegment(sketch, "E6136", {"start": v(139.1, -46.97) * mm, "end": v(139.21, -47.12) * mm});
            skLineSegment(sketch, "E6137", {"start": v(139.21, -47.12) * mm, "end": v(139.31, -47.28) * mm});
            skLineSegment(sketch, "E6138", {"start": v(139.31, -47.28) * mm, "end": v(139.4, -47.45) * mm});
            skLineSegment(sketch, "E6139", {"start": v(139.4, -47.45) * mm, "end": v(139.45, -47.63) * mm});
            skLineSegment(sketch, "E6140", {"start": v(139.45, -47.63) * mm, "end": v(139.49, -47.81) * mm});
            skLineSegment(sketch, "E6141", {"start": v(139.49, -47.81) * mm, "end": v(139.5, -48) * mm});
            skLineSegment(sketch, "E6142", {"start": v(139.5, -48) * mm, "end": v(139.49, -48.19) * mm});
            skLineSegment(sketch, "E6143", {"start": v(139.49, -48.19) * mm, "end": v(139.45, -48.37) * mm});
            skLineSegment(sketch, "E6144", {"start": v(139.45, -48.37) * mm, "end": v(139.4, -48.55) * mm});
            skLineSegment(sketch, "E6145", {"start": v(139.4, -48.55) * mm, "end": v(139.31, -48.72) * mm});
            skLineSegment(sketch, "E6146", {"start": v(139.31, -48.72) * mm, "end": v(139.21, -48.88) * mm});
            skLineSegment(sketch, "E6147", {"start": v(139.21, -48.88) * mm, "end": v(139.1, -49.03) * mm});
            skLineSegment(sketch, "E6148", {"start": v(139.1, -49.03) * mm, "end": v(138.96, -49.16) * mm});
            skLineSegment(sketch, "E6149", {"start": v(138.96, -49.16) * mm, "end": v(138.8, -49.27) * mm});
            skLineSegment(sketch, "E6150", {"start": v(138.8, -49.27) * mm, "end": v(138.64, -49.36) * mm});
            skLineSegment(sketch, "E6151", {"start": v(138.64, -49.36) * mm, "end": v(138.46, -49.43) * mm});
            skLineSegment(sketch, "E6152", {"start": v(138.46, -49.43) * mm, "end": v(138.28, -49.47) * mm});
            skLineSegment(sketch, "E6153", {"start": v(138.28, -49.47) * mm, "end": v(138.1, -49.5) * mm});
            skLineSegment(sketch, "E6154", {"start": v(138.1, -49.5) * mm, "end": v(137.9, -49.5) * mm});
            skLineSegment(sketch, "E6155", {"start": v(161.9, -49.5) * mm, "end": v(161.72, -49.47) * mm});
            skLineSegment(sketch, "E6156", {"start": v(161.72, -49.47) * mm, "end": v(161.54, -49.43) * mm});
            skLineSegment(sketch, "E6157", {"start": v(161.54, -49.43) * mm, "end": v(161.36, -49.36) * mm});
            skLineSegment(sketch, "E6158", {"start": v(161.36, -49.36) * mm, "end": v(161.2, -49.27) * mm});
            skLineSegment(sketch, "E6159", {"start": v(161.2, -49.27) * mm, "end": v(161.04, -49.16) * mm});
            skLineSegment(sketch, "E6160", {"start": v(161.04, -49.16) * mm, "end": v(160.9, -49.03) * mm});
            skLineSegment(sketch, "E6161", {"start": v(160.9, -49.03) * mm, "end": v(160.79, -48.88) * mm});
            skLineSegment(sketch, "E6162", {"start": v(160.79, -48.88) * mm, "end": v(160.69, -48.72) * mm});
            skLineSegment(sketch, "E6163", {"start": v(160.69, -48.72) * mm, "end": v(160.6, -48.55) * mm});
            skLineSegment(sketch, "E6164", {"start": v(160.6, -48.55) * mm, "end": v(160.55, -48.37) * mm});
            skLineSegment(sketch, "E6165", {"start": v(160.55, -48.37) * mm, "end": v(160.51, -48.19) * mm});
            skLineSegment(sketch, "E6166", {"start": v(160.51, -48.19) * mm, "end": v(160.5, -48) * mm});
            skLineSegment(sketch, "E6167", {"start": v(160.5, -48) * mm, "end": v(160.51, -47.81) * mm});
            skLineSegment(sketch, "E6168", {"start": v(160.51, -47.81) * mm, "end": v(160.55, -47.63) * mm});
            skLineSegment(sketch, "E6169", {"start": v(160.55, -47.63) * mm, "end": v(160.6, -47.45) * mm});
            skLineSegment(sketch, "E6170", {"start": v(160.6, -47.45) * mm, "end": v(160.69, -47.28) * mm});
            skLineSegment(sketch, "E6171", {"start": v(160.69, -47.28) * mm, "end": v(160.79, -47.12) * mm});
            skLineSegment(sketch, "E6172", {"start": v(160.79, -47.12) * mm, "end": v(160.9, -46.97) * mm});
            skLineSegment(sketch, "E6173", {"start": v(160.9, -46.97) * mm, "end": v(161.04, -46.84) * mm});
            skLineSegment(sketch, "E6174", {"start": v(161.04, -46.84) * mm, "end": v(161.2, -46.73) * mm});
            skLineSegment(sketch, "E6175", {"start": v(161.2, -46.73) * mm, "end": v(161.36, -46.64) * mm});
            skLineSegment(sketch, "E6176", {"start": v(161.36, -46.64) * mm, "end": v(161.54, -46.57) * mm});
            skLineSegment(sketch, "E6177", {"start": v(161.54, -46.57) * mm, "end": v(161.72, -46.53) * mm});
            skLineSegment(sketch, "E6178", {"start": v(161.72, -46.53) * mm, "end": v(161.9, -46.5) * mm});
            skLineSegment(sketch, "E6179", {"start": v(161.9, -46.5) * mm, "end": v(162.1, -46.5) * mm});
            skLineSegment(sketch, "E6180", {"start": v(162.1, -46.5) * mm, "end": v(162.28, -46.53) * mm});
            skLineSegment(sketch, "E6181", {"start": v(162.28, -46.53) * mm, "end": v(162.46, -46.57) * mm});
            skLineSegment(sketch, "E6182", {"start": v(162.46, -46.57) * mm, "end": v(162.64, -46.64) * mm});
            skLineSegment(sketch, "E6183", {"start": v(162.64, -46.64) * mm, "end": v(162.8, -46.73) * mm});
            skLineSegment(sketch, "E6184", {"start": v(162.8, -46.73) * mm, "end": v(162.96, -46.84) * mm});
            skLineSegment(sketch, "E6185", {"start": v(162.96, -46.84) * mm, "end": v(163.1, -46.97) * mm});
            skLineSegment(sketch, "E6186", {"start": v(163.1, -46.97) * mm, "end": v(163.21, -47.12) * mm});
            skLineSegment(sketch, "E6187", {"start": v(163.21, -47.12) * mm, "end": v(163.31, -47.28) * mm});
            skLineSegment(sketch, "E6188", {"start": v(163.31, -47.28) * mm, "end": v(163.4, -47.45) * mm});
            skLineSegment(sketch, "E6189", {"start": v(163.4, -47.45) * mm, "end": v(163.45, -47.63) * mm});
            skLineSegment(sketch, "E6190", {"start": v(163.45, -47.63) * mm, "end": v(163.49, -47.81) * mm});
            skLineSegment(sketch, "E6191", {"start": v(163.49, -47.81) * mm, "end": v(163.5, -48) * mm});
            skLineSegment(sketch, "E6192", {"start": v(163.5, -48) * mm, "end": v(163.49, -48.19) * mm});
            skLineSegment(sketch, "E6193", {"start": v(163.49, -48.19) * mm, "end": v(163.45, -48.37) * mm});
            skLineSegment(sketch, "E6194", {"start": v(163.45, -48.37) * mm, "end": v(163.4, -48.55) * mm});
            skLineSegment(sketch, "E6195", {"start": v(163.4, -48.55) * mm, "end": v(163.31, -48.72) * mm});
            skLineSegment(sketch, "E6196", {"start": v(163.31, -48.72) * mm, "end": v(163.21, -48.88) * mm});
            skLineSegment(sketch, "E6197", {"start": v(163.21, -48.88) * mm, "end": v(163.1, -49.03) * mm});
            skLineSegment(sketch, "E6198", {"start": v(163.1, -49.03) * mm, "end": v(162.96, -49.16) * mm});
            skLineSegment(sketch, "E6199", {"start": v(162.96, -49.16) * mm, "end": v(162.8, -49.27) * mm});
            skLineSegment(sketch, "E6200", {"start": v(162.8, -49.27) * mm, "end": v(162.64, -49.36) * mm});
            skLineSegment(sketch, "E6201", {"start": v(162.64, -49.36) * mm, "end": v(162.46, -49.43) * mm});
            skLineSegment(sketch, "E6202", {"start": v(162.46, -49.43) * mm, "end": v(162.28, -49.47) * mm});
            skLineSegment(sketch, "E6203", {"start": v(162.28, -49.47) * mm, "end": v(162.1, -49.5) * mm});
            skLineSegment(sketch, "E6204", {"start": v(162.1, -49.5) * mm, "end": v(161.9, -49.5) * mm});
            skLineSegment(sketch, "E6205", {"start": v(141.9, 231.5) * mm, "end": v(141.72, 231.53) * mm});
            skLineSegment(sketch, "E6206", {"start": v(141.72, 231.53) * mm, "end": v(141.54, 231.57) * mm});
            skLineSegment(sketch, "E6207", {"start": v(141.54, 231.57) * mm, "end": v(141.36, 231.64) * mm});
            skLineSegment(sketch, "E6208", {"start": v(141.36, 231.64) * mm, "end": v(141.2, 231.73) * mm});
            skLineSegment(sketch, "E6209", {"start": v(141.2, 231.73) * mm, "end": v(141.04, 231.84) * mm});
            skLineSegment(sketch, "E6210", {"start": v(141.04, 231.84) * mm, "end": v(140.9, 231.97) * mm});
            skLineSegment(sketch, "E6211", {"start": v(140.9, 231.97) * mm, "end": v(140.79, 232.12) * mm});
            skLineSegment(sketch, "E6212", {"start": v(140.79, 232.12) * mm, "end": v(140.69, 232.28) * mm});
            skLineSegment(sketch, "E6213", {"start": v(140.69, 232.28) * mm, "end": v(140.6, 232.45) * mm});
            skLineSegment(sketch, "E6214", {"start": v(140.6, 232.45) * mm, "end": v(140.55, 232.63) * mm});
            skLineSegment(sketch, "E6215", {"start": v(140.55, 232.63) * mm, "end": v(140.51, 232.81) * mm});
            skLineSegment(sketch, "E6216", {"start": v(140.51, 232.81) * mm, "end": v(140.5, 233) * mm});
            skLineSegment(sketch, "E6217", {"start": v(140.5, 233) * mm, "end": v(140.51, 233.19) * mm});
            skLineSegment(sketch, "E6218", {"start": v(140.51, 233.19) * mm, "end": v(140.55, 233.37) * mm});
            skLineSegment(sketch, "E6219", {"start": v(140.55, 233.37) * mm, "end": v(140.6, 233.55) * mm});
            skLineSegment(sketch, "E6220", {"start": v(140.6, 233.55) * mm, "end": v(140.69, 233.72) * mm});
            skLineSegment(sketch, "E6221", {"start": v(140.69, 233.72) * mm, "end": v(140.79, 233.88) * mm});
            skLineSegment(sketch, "E6222", {"start": v(140.79, 233.88) * mm, "end": v(140.9, 234.03) * mm});
            skLineSegment(sketch, "E6223", {"start": v(140.9, 234.03) * mm, "end": v(141.04, 234.16) * mm});
            skLineSegment(sketch, "E6224", {"start": v(141.04, 234.16) * mm, "end": v(141.2, 234.27) * mm});
            skLineSegment(sketch, "E6225", {"start": v(141.2, 234.27) * mm, "end": v(141.36, 234.36) * mm});
            skLineSegment(sketch, "E6226", {"start": v(141.36, 234.36) * mm, "end": v(141.54, 234.43) * mm});
            skLineSegment(sketch, "E6227", {"start": v(141.54, 234.43) * mm, "end": v(141.72, 234.47) * mm});
            skLineSegment(sketch, "E6228", {"start": v(141.72, 234.47) * mm, "end": v(141.9, 234.5) * mm});
            skLineSegment(sketch, "E6229", {"start": v(141.9, 234.5) * mm, "end": v(142.1, 234.5) * mm});
            skLineSegment(sketch, "E6230", {"start": v(142.1, 234.5) * mm, "end": v(142.28, 234.47) * mm});
            skLineSegment(sketch, "E6231", {"start": v(142.28, 234.47) * mm, "end": v(142.46, 234.43) * mm});
            skLineSegment(sketch, "E6232", {"start": v(142.46, 234.43) * mm, "end": v(142.64, 234.36) * mm});
            skLineSegment(sketch, "E6233", {"start": v(142.64, 234.36) * mm, "end": v(142.8, 234.27) * mm});
            skLineSegment(sketch, "E6234", {"start": v(142.8, 234.27) * mm, "end": v(142.96, 234.16) * mm});
            skLineSegment(sketch, "E6235", {"start": v(142.96, 234.16) * mm, "end": v(143.1, 234.03) * mm});
            skLineSegment(sketch, "E6236", {"start": v(143.1, 234.03) * mm, "end": v(143.21, 233.88) * mm});
            skLineSegment(sketch, "E6237", {"start": v(143.21, 233.88) * mm, "end": v(143.31, 233.72) * mm});
            skLineSegment(sketch, "E6238", {"start": v(143.31, 233.72) * mm, "end": v(143.4, 233.55) * mm});
            skLineSegment(sketch, "E6239", {"start": v(143.4, 233.55) * mm, "end": v(143.45, 233.37) * mm});
            skLineSegment(sketch, "E6240", {"start": v(143.45, 233.37) * mm, "end": v(143.49, 233.19) * mm});
            skLineSegment(sketch, "E6241", {"start": v(143.49, 233.19) * mm, "end": v(143.5, 233) * mm});
            skLineSegment(sketch, "E6242", {"start": v(143.5, 233) * mm, "end": v(143.49, 232.81) * mm});
            skLineSegment(sketch, "E6243", {"start": v(143.49, 232.81) * mm, "end": v(143.45, 232.63) * mm});
            skLineSegment(sketch, "E6244", {"start": v(143.45, 232.63) * mm, "end": v(143.4, 232.45) * mm});
            skLineSegment(sketch, "E6245", {"start": v(143.4, 232.45) * mm, "end": v(143.31, 232.28) * mm});
            skLineSegment(sketch, "E6246", {"start": v(143.31, 232.28) * mm, "end": v(143.21, 232.12) * mm});
            skLineSegment(sketch, "E6247", {"start": v(143.21, 232.12) * mm, "end": v(143.1, 231.97) * mm});
            skLineSegment(sketch, "E6248", {"start": v(143.1, 231.97) * mm, "end": v(142.96, 231.84) * mm});
            skLineSegment(sketch, "E6249", {"start": v(142.96, 231.84) * mm, "end": v(142.8, 231.73) * mm});
            skLineSegment(sketch, "E6250", {"start": v(142.8, 231.73) * mm, "end": v(142.64, 231.64) * mm});
            skLineSegment(sketch, "E6251", {"start": v(142.64, 231.64) * mm, "end": v(142.46, 231.57) * mm});
            skLineSegment(sketch, "E6252", {"start": v(142.46, 231.57) * mm, "end": v(142.28, 231.53) * mm});
            skLineSegment(sketch, "E6253", {"start": v(142.28, 231.53) * mm, "end": v(142.1, 231.5) * mm});
            skLineSegment(sketch, "E6254", {"start": v(142.1, 231.5) * mm, "end": v(141.9, 231.5) * mm});
            skLineSegment(sketch, "E6255", {"start": v(157.9, 231.5) * mm, "end": v(157.72, 231.53) * mm});
            skLineSegment(sketch, "E6256", {"start": v(157.72, 231.53) * mm, "end": v(157.54, 231.57) * mm});
            skLineSegment(sketch, "E6257", {"start": v(157.54, 231.57) * mm, "end": v(157.36, 231.64) * mm});
            skLineSegment(sketch, "E6258", {"start": v(157.36, 231.64) * mm, "end": v(157.2, 231.73) * mm});
            skLineSegment(sketch, "E6259", {"start": v(157.2, 231.73) * mm, "end": v(157.04, 231.84) * mm});
            skLineSegment(sketch, "E6260", {"start": v(157.04, 231.84) * mm, "end": v(156.9, 231.97) * mm});
            skLineSegment(sketch, "E6261", {"start": v(156.9, 231.97) * mm, "end": v(156.79, 232.12) * mm});
            skLineSegment(sketch, "E6262", {"start": v(156.79, 232.12) * mm, "end": v(156.69, 232.28) * mm});
            skLineSegment(sketch, "E6263", {"start": v(156.69, 232.28) * mm, "end": v(156.6, 232.45) * mm});
            skLineSegment(sketch, "E6264", {"start": v(156.6, 232.45) * mm, "end": v(156.55, 232.63) * mm});
            skLineSegment(sketch, "E6265", {"start": v(156.55, 232.63) * mm, "end": v(156.51, 232.81) * mm});
            skLineSegment(sketch, "E6266", {"start": v(156.51, 232.81) * mm, "end": v(156.5, 233) * mm});
            skLineSegment(sketch, "E6267", {"start": v(156.5, 233) * mm, "end": v(156.51, 233.19) * mm});
            skLineSegment(sketch, "E6268", {"start": v(156.51, 233.19) * mm, "end": v(156.55, 233.37) * mm});
            skLineSegment(sketch, "E6269", {"start": v(156.55, 233.37) * mm, "end": v(156.6, 233.55) * mm});
            skLineSegment(sketch, "E6270", {"start": v(156.6, 233.55) * mm, "end": v(156.69, 233.72) * mm});
            skLineSegment(sketch, "E6271", {"start": v(156.69, 233.72) * mm, "end": v(156.79, 233.88) * mm});
            skLineSegment(sketch, "E6272", {"start": v(156.79, 233.88) * mm, "end": v(156.9, 234.03) * mm});
            skLineSegment(sketch, "E6273", {"start": v(156.9, 234.03) * mm, "end": v(157.04, 234.16) * mm});
            skLineSegment(sketch, "E6274", {"start": v(157.04, 234.16) * mm, "end": v(157.2, 234.27) * mm});
            skLineSegment(sketch, "E6275", {"start": v(157.2, 234.27) * mm, "end": v(157.36, 234.36) * mm});
            skLineSegment(sketch, "E6276", {"start": v(157.36, 234.36) * mm, "end": v(157.54, 234.43) * mm});
            skLineSegment(sketch, "E6277", {"start": v(157.54, 234.43) * mm, "end": v(157.72, 234.47) * mm});
            skLineSegment(sketch, "E6278", {"start": v(157.72, 234.47) * mm, "end": v(157.9, 234.5) * mm});
            skLineSegment(sketch, "E6279", {"start": v(157.9, 234.5) * mm, "end": v(158.1, 234.5) * mm});
            skLineSegment(sketch, "E6280", {"start": v(158.1, 234.5) * mm, "end": v(158.28, 234.47) * mm});
            skLineSegment(sketch, "E6281", {"start": v(158.28, 234.47) * mm, "end": v(158.46, 234.43) * mm});
            skLineSegment(sketch, "E6282", {"start": v(158.46, 234.43) * mm, "end": v(158.64, 234.36) * mm});
            skLineSegment(sketch, "E6283", {"start": v(158.64, 234.36) * mm, "end": v(158.8, 234.27) * mm});
            skLineSegment(sketch, "E6284", {"start": v(158.8, 234.27) * mm, "end": v(158.96, 234.16) * mm});
            skLineSegment(sketch, "E6285", {"start": v(158.96, 234.16) * mm, "end": v(159.1, 234.03) * mm});
            skLineSegment(sketch, "E6286", {"start": v(159.1, 234.03) * mm, "end": v(159.21, 233.88) * mm});
            skLineSegment(sketch, "E6287", {"start": v(159.21, 233.88) * mm, "end": v(159.31, 233.72) * mm});
            skLineSegment(sketch, "E6288", {"start": v(159.31, 233.72) * mm, "end": v(159.4, 233.55) * mm});
            skLineSegment(sketch, "E6289", {"start": v(159.4, 233.55) * mm, "end": v(159.45, 233.37) * mm});
            skLineSegment(sketch, "E6290", {"start": v(159.45, 233.37) * mm, "end": v(159.49, 233.19) * mm});
            skLineSegment(sketch, "E6291", {"start": v(159.49, 233.19) * mm, "end": v(159.5, 233) * mm});
            skLineSegment(sketch, "E6292", {"start": v(159.5, 233) * mm, "end": v(159.49, 232.81) * mm});
            skLineSegment(sketch, "E6293", {"start": v(159.49, 232.81) * mm, "end": v(159.45, 232.63) * mm});
            skLineSegment(sketch, "E6294", {"start": v(159.45, 232.63) * mm, "end": v(159.4, 232.45) * mm});
            skLineSegment(sketch, "E6295", {"start": v(159.4, 232.45) * mm, "end": v(159.31, 232.28) * mm});
            skLineSegment(sketch, "E6296", {"start": v(159.31, 232.28) * mm, "end": v(159.21, 232.12) * mm});
            skLineSegment(sketch, "E6297", {"start": v(159.21, 232.12) * mm, "end": v(159.1, 231.97) * mm});
            skLineSegment(sketch, "E6298", {"start": v(159.1, 231.97) * mm, "end": v(158.96, 231.84) * mm});
            skLineSegment(sketch, "E6299", {"start": v(158.96, 231.84) * mm, "end": v(158.8, 231.73) * mm});
            skLineSegment(sketch, "E6300", {"start": v(158.8, 231.73) * mm, "end": v(158.64, 231.64) * mm});
            skLineSegment(sketch, "E6301", {"start": v(158.64, 231.64) * mm, "end": v(158.46, 231.57) * mm});
            skLineSegment(sketch, "E6302", {"start": v(158.46, 231.57) * mm, "end": v(158.28, 231.53) * mm});
            skLineSegment(sketch, "E6303", {"start": v(158.28, 231.53) * mm, "end": v(158.1, 231.5) * mm});
            skLineSegment(sketch, "E6304", {"start": v(158.1, 231.5) * mm, "end": v(157.9, 231.5) * mm});
            skLineSegment(sketch, "E6305", {"start": v(251.9, 231.5) * mm, "end": v(251.72, 231.53) * mm});
            skLineSegment(sketch, "E6306", {"start": v(251.72, 231.53) * mm, "end": v(251.54, 231.57) * mm});
            skLineSegment(sketch, "E6307", {"start": v(251.54, 231.57) * mm, "end": v(251.36, 231.64) * mm});
            skLineSegment(sketch, "E6308", {"start": v(251.36, 231.64) * mm, "end": v(251.2, 231.73) * mm});
            skLineSegment(sketch, "E6309", {"start": v(251.2, 231.73) * mm, "end": v(251.04, 231.84) * mm});
            skLineSegment(sketch, "E6310", {"start": v(251.04, 231.84) * mm, "end": v(250.9, 231.97) * mm});
            skLineSegment(sketch, "E6311", {"start": v(250.9, 231.97) * mm, "end": v(250.79, 232.12) * mm});
            skLineSegment(sketch, "E6312", {"start": v(250.79, 232.12) * mm, "end": v(250.69, 232.28) * mm});
            skLineSegment(sketch, "E6313", {"start": v(250.69, 232.28) * mm, "end": v(250.6, 232.45) * mm});
            skLineSegment(sketch, "E6314", {"start": v(250.6, 232.45) * mm, "end": v(250.55, 232.63) * mm});
            skLineSegment(sketch, "E6315", {"start": v(250.55, 232.63) * mm, "end": v(250.51, 232.81) * mm});
            skLineSegment(sketch, "E6316", {"start": v(250.51, 232.81) * mm, "end": v(250.5, 233) * mm});
            skLineSegment(sketch, "E6317", {"start": v(250.5, 233) * mm, "end": v(250.51, 233.19) * mm});
            skLineSegment(sketch, "E6318", {"start": v(250.51, 233.19) * mm, "end": v(250.55, 233.37) * mm});
            skLineSegment(sketch, "E6319", {"start": v(250.55, 233.37) * mm, "end": v(250.6, 233.55) * mm});
            skLineSegment(sketch, "E6320", {"start": v(250.6, 233.55) * mm, "end": v(250.69, 233.72) * mm});
            skLineSegment(sketch, "E6321", {"start": v(250.69, 233.72) * mm, "end": v(250.79, 233.88) * mm});
            skLineSegment(sketch, "E6322", {"start": v(250.79, 233.88) * mm, "end": v(250.9, 234.03) * mm});
            skLineSegment(sketch, "E6323", {"start": v(250.9, 234.03) * mm, "end": v(251.04, 234.16) * mm});
            skLineSegment(sketch, "E6324", {"start": v(251.04, 234.16) * mm, "end": v(251.2, 234.27) * mm});
            skLineSegment(sketch, "E6325", {"start": v(251.2, 234.27) * mm, "end": v(251.36, 234.36) * mm});
            skLineSegment(sketch, "E6326", {"start": v(251.36, 234.36) * mm, "end": v(251.54, 234.43) * mm});
            skLineSegment(sketch, "E6327", {"start": v(251.54, 234.43) * mm, "end": v(251.72, 234.47) * mm});
            skLineSegment(sketch, "E6328", {"start": v(251.72, 234.47) * mm, "end": v(251.9, 234.5) * mm});
            skLineSegment(sketch, "E6329", {"start": v(251.9, 234.5) * mm, "end": v(252.1, 234.5) * mm});
            skLineSegment(sketch, "E6330", {"start": v(252.1, 234.5) * mm, "end": v(252.28, 234.47) * mm});
            skLineSegment(sketch, "E6331", {"start": v(252.28, 234.47) * mm, "end": v(252.46, 234.43) * mm});
            skLineSegment(sketch, "E6332", {"start": v(252.46, 234.43) * mm, "end": v(252.64, 234.36) * mm});
            skLineSegment(sketch, "E6333", {"start": v(252.64, 234.36) * mm, "end": v(252.8, 234.27) * mm});
            skLineSegment(sketch, "E6334", {"start": v(252.8, 234.27) * mm, "end": v(252.96, 234.16) * mm});
            skLineSegment(sketch, "E6335", {"start": v(252.96, 234.16) * mm, "end": v(253.1, 234.03) * mm});
            skLineSegment(sketch, "E6336", {"start": v(253.1, 234.03) * mm, "end": v(253.21, 233.88) * mm});
            skLineSegment(sketch, "E6337", {"start": v(253.21, 233.88) * mm, "end": v(253.31, 233.72) * mm});
            skLineSegment(sketch, "E6338", {"start": v(253.31, 233.72) * mm, "end": v(253.4, 233.55) * mm});
            skLineSegment(sketch, "E6339", {"start": v(253.4, 233.55) * mm, "end": v(253.45, 233.37) * mm});
            skLineSegment(sketch, "E6340", {"start": v(253.45, 233.37) * mm, "end": v(253.49, 233.19) * mm});
            skLineSegment(sketch, "E6341", {"start": v(253.49, 233.19) * mm, "end": v(253.5, 233) * mm});
            skLineSegment(sketch, "E6342", {"start": v(253.5, 233) * mm, "end": v(253.49, 232.81) * mm});
            skLineSegment(sketch, "E6343", {"start": v(253.49, 232.81) * mm, "end": v(253.45, 232.63) * mm});
            skLineSegment(sketch, "E6344", {"start": v(253.45, 232.63) * mm, "end": v(253.4, 232.45) * mm});
            skLineSegment(sketch, "E6345", {"start": v(253.4, 232.45) * mm, "end": v(253.31, 232.28) * mm});
            skLineSegment(sketch, "E6346", {"start": v(253.31, 232.28) * mm, "end": v(253.21, 232.12) * mm});
            skLineSegment(sketch, "E6347", {"start": v(253.21, 232.12) * mm, "end": v(253.1, 231.97) * mm});
            skLineSegment(sketch, "E6348", {"start": v(253.1, 231.97) * mm, "end": v(252.96, 231.84) * mm});
            skLineSegment(sketch, "E6349", {"start": v(252.96, 231.84) * mm, "end": v(252.8, 231.73) * mm});
            skLineSegment(sketch, "E6350", {"start": v(252.8, 231.73) * mm, "end": v(252.64, 231.64) * mm});
            skLineSegment(sketch, "E6351", {"start": v(252.64, 231.64) * mm, "end": v(252.46, 231.57) * mm});
            skLineSegment(sketch, "E6352", {"start": v(252.46, 231.57) * mm, "end": v(252.28, 231.53) * mm});
            skLineSegment(sketch, "E6353", {"start": v(252.28, 231.53) * mm, "end": v(252.1, 231.5) * mm});
            skLineSegment(sketch, "E6354", {"start": v(252.1, 231.5) * mm, "end": v(251.9, 231.5) * mm});
            skLineSegment(sketch, "E6355", {"start": v(267.9, 231.5) * mm, "end": v(267.72, 231.53) * mm});
            skLineSegment(sketch, "E6356", {"start": v(267.72, 231.53) * mm, "end": v(267.54, 231.57) * mm});
            skLineSegment(sketch, "E6357", {"start": v(267.54, 231.57) * mm, "end": v(267.36, 231.64) * mm});
            skLineSegment(sketch, "E6358", {"start": v(267.36, 231.64) * mm, "end": v(267.2, 231.73) * mm});
            skLineSegment(sketch, "E6359", {"start": v(267.2, 231.73) * mm, "end": v(267.04, 231.84) * mm});
            skLineSegment(sketch, "E6360", {"start": v(267.04, 231.84) * mm, "end": v(266.9, 231.97) * mm});
            skLineSegment(sketch, "E6361", {"start": v(266.9, 231.97) * mm, "end": v(266.79, 232.12) * mm});
            skLineSegment(sketch, "E6362", {"start": v(266.79, 232.12) * mm, "end": v(266.69, 232.28) * mm});
            skLineSegment(sketch, "E6363", {"start": v(266.69, 232.28) * mm, "end": v(266.6, 232.45) * mm});
            skLineSegment(sketch, "E6364", {"start": v(266.6, 232.45) * mm, "end": v(266.55, 232.63) * mm});
            skLineSegment(sketch, "E6365", {"start": v(266.55, 232.63) * mm, "end": v(266.51, 232.81) * mm});
            skLineSegment(sketch, "E6366", {"start": v(266.51, 232.81) * mm, "end": v(266.5, 233) * mm});
            skLineSegment(sketch, "E6367", {"start": v(266.5, 233) * mm, "end": v(266.51, 233.19) * mm});
            skLineSegment(sketch, "E6368", {"start": v(266.51, 233.19) * mm, "end": v(266.55, 233.37) * mm});
            skLineSegment(sketch, "E6369", {"start": v(266.55, 233.37) * mm, "end": v(266.6, 233.55) * mm});
            skLineSegment(sketch, "E6370", {"start": v(266.6, 233.55) * mm, "end": v(266.69, 233.72) * mm});
            skLineSegment(sketch, "E6371", {"start": v(266.69, 233.72) * mm, "end": v(266.79, 233.88) * mm});
            skLineSegment(sketch, "E6372", {"start": v(266.79, 233.88) * mm, "end": v(266.9, 234.03) * mm});
            skLineSegment(sketch, "E6373", {"start": v(266.9, 234.03) * mm, "end": v(267.04, 234.16) * mm});
            skLineSegment(sketch, "E6374", {"start": v(267.04, 234.16) * mm, "end": v(267.2, 234.27) * mm});
            skLineSegment(sketch, "E6375", {"start": v(267.2, 234.27) * mm, "end": v(267.36, 234.36) * mm});
            skLineSegment(sketch, "E6376", {"start": v(267.36, 234.36) * mm, "end": v(267.54, 234.43) * mm});
            skLineSegment(sketch, "E6377", {"start": v(267.54, 234.43) * mm, "end": v(267.72, 234.47) * mm});
            skLineSegment(sketch, "E6378", {"start": v(267.72, 234.47) * mm, "end": v(267.9, 234.5) * mm});
            skLineSegment(sketch, "E6379", {"start": v(267.9, 234.5) * mm, "end": v(268.1, 234.5) * mm});
            skLineSegment(sketch, "E6380", {"start": v(268.1, 234.5) * mm, "end": v(268.28, 234.47) * mm});
            skLineSegment(sketch, "E6381", {"start": v(268.28, 234.47) * mm, "end": v(268.46, 234.43) * mm});
            skLineSegment(sketch, "E6382", {"start": v(268.46, 234.43) * mm, "end": v(268.64, 234.36) * mm});
            skLineSegment(sketch, "E6383", {"start": v(268.64, 234.36) * mm, "end": v(268.8, 234.27) * mm});
            skLineSegment(sketch, "E6384", {"start": v(268.8, 234.27) * mm, "end": v(268.96, 234.16) * mm});
            skLineSegment(sketch, "E6385", {"start": v(268.96, 234.16) * mm, "end": v(269.1, 234.03) * mm});
            skLineSegment(sketch, "E6386", {"start": v(269.1, 234.03) * mm, "end": v(269.21, 233.88) * mm});
            skLineSegment(sketch, "E6387", {"start": v(269.21, 233.88) * mm, "end": v(269.31, 233.72) * mm});
            skLineSegment(sketch, "E6388", {"start": v(269.31, 233.72) * mm, "end": v(269.4, 233.55) * mm});
            skLineSegment(sketch, "E6389", {"start": v(269.4, 233.55) * mm, "end": v(269.45, 233.37) * mm});
            skLineSegment(sketch, "E6390", {"start": v(269.45, 233.37) * mm, "end": v(269.49, 233.19) * mm});
            skLineSegment(sketch, "E6391", {"start": v(269.49, 233.19) * mm, "end": v(269.5, 233) * mm});
            skLineSegment(sketch, "E6392", {"start": v(269.5, 233) * mm, "end": v(269.49, 232.81) * mm});
            skLineSegment(sketch, "E6393", {"start": v(269.49, 232.81) * mm, "end": v(269.45, 232.63) * mm});
            skLineSegment(sketch, "E6394", {"start": v(269.45, 232.63) * mm, "end": v(269.4, 232.45) * mm});
            skLineSegment(sketch, "E6395", {"start": v(269.4, 232.45) * mm, "end": v(269.31, 232.28) * mm});
            skLineSegment(sketch, "E6396", {"start": v(269.31, 232.28) * mm, "end": v(269.21, 232.12) * mm});
            skLineSegment(sketch, "E6397", {"start": v(269.21, 232.12) * mm, "end": v(269.1, 231.97) * mm});
            skLineSegment(sketch, "E6398", {"start": v(269.1, 231.97) * mm, "end": v(268.96, 231.84) * mm});
            skLineSegment(sketch, "E6399", {"start": v(268.96, 231.84) * mm, "end": v(268.8, 231.73) * mm});
            skLineSegment(sketch, "E6400", {"start": v(268.8, 231.73) * mm, "end": v(268.64, 231.64) * mm});
            skLineSegment(sketch, "E6401", {"start": v(268.64, 231.64) * mm, "end": v(268.46, 231.57) * mm});
            skLineSegment(sketch, "E6402", {"start": v(268.46, 231.57) * mm, "end": v(268.28, 231.53) * mm});
            skLineSegment(sketch, "E6403", {"start": v(268.28, 231.53) * mm, "end": v(268.1, 231.5) * mm});
            skLineSegment(sketch, "E6404", {"start": v(268.1, 231.5) * mm, "end": v(267.9, 231.5) * mm});
            skLineSegment(sketch, "E6405", {"start": v(220.4, 225) * mm, "end": v(220.32, 225.01) * mm});
            skLineSegment(sketch, "E6406", {"start": v(220.32, 225.01) * mm, "end": v(220.22, 225.03) * mm});
            skLineSegment(sketch, "E6407", {"start": v(220.22, 225.03) * mm, "end": v(220.19, 225.03) * mm});
            skLineSegment(sketch, "E6408", {"start": v(220.19, 225.03) * mm, "end": v(220.06, 225.07) * mm});
            skLineSegment(sketch, "E6409", {"start": v(220.06, 225.07) * mm, "end": v(219.93, 225.11) * mm});
            skLineSegment(sketch, "E6410", {"start": v(219.93, 225.11) * mm, "end": v(219.86, 225.14) * mm});
            skLineSegment(sketch, "E6411", {"start": v(219.86, 225.14) * mm, "end": v(219.8, 225.17) * mm});
            skLineSegment(sketch, "E6412", {"start": v(219.8, 225.17) * mm, "end": v(219.7, 225.23) * mm});
            skLineSegment(sketch, "E6413", {"start": v(219.7, 225.23) * mm, "end": v(219.59, 225.31) * mm});
            skLineSegment(sketch, "E6414", {"start": v(219.59, 225.31) * mm, "end": v(219.54, 225.34) * mm});
            skLineSegment(sketch, "E6415", {"start": v(219.54, 225.34) * mm, "end": v(219.48, 225.4) * mm});
            skLineSegment(sketch, "E6416", {"start": v(219.48, 225.4) * mm, "end": v(219.4, 225.47) * mm});
            skLineSegment(sketch, "E6417", {"start": v(219.4, 225.47) * mm, "end": v(219.38, 225.5) * mm});
            skLineSegment(sketch, "E6418", {"start": v(219.38, 225.5) * mm, "end": v(219.3, 225.6) * mm});
            skLineSegment(sketch, "E6419", {"start": v(219.3, 225.6) * mm, "end": v(219.22, 225.71) * mm});
            skLineSegment(sketch, "E6420", {"start": v(219.22, 225.71) * mm, "end": v(219.2, 225.75) * mm});
            skLineSegment(sketch, "E6421", {"start": v(219.2, 225.75) * mm, "end": v(219.19, 225.78) * mm});
            skLineSegment(sketch, "E6422", {"start": v(219.19, 225.78) * mm, "end": v(219.16, 225.83) * mm});
            skLineSegment(sketch, "E6423", {"start": v(219.16, 225.83) * mm, "end": v(219.1, 225.95) * mm});
            skLineSegment(sketch, "E6424", {"start": v(219.1, 225.95) * mm, "end": v(219.06, 226.08) * mm});
            skLineSegment(sketch, "E6425", {"start": v(219.06, 226.08) * mm, "end": v(219.05, 226.13) * mm});
            skLineSegment(sketch, "E6426", {"start": v(219.05, 226.13) * mm, "end": v(219.03, 226.2) * mm});
            skLineSegment(sketch, "E6427", {"start": v(219.03, 226.2) * mm, "end": v(219.01, 226.31) * mm});
            skLineSegment(sketch, "E6428", {"start": v(219.01, 226.31) * mm, "end": v(219, 226.34) * mm});
            skLineSegment(sketch, "E6429", {"start": v(219, 226.34) * mm, "end": v(219, 226.47) * mm});
            skLineSegment(sketch, "E6430", {"start": v(219, 226.47) * mm, "end": v(219, 226.61) * mm});
            skLineSegment(sketch, "E6431", {"start": v(219, 226.61) * mm, "end": v(219, 226.66) * mm});
            skLineSegment(sketch, "E6432", {"start": v(219, 226.66) * mm, "end": v(219.01, 226.69) * mm});
            skLineSegment(sketch, "E6433", {"start": v(219.01, 226.69) * mm, "end": v(219.02, 226.75) * mm});
            skLineSegment(sketch, "E6434", {"start": v(219.02, 226.75) * mm, "end": v(219.05, 226.87) * mm});
            skLineSegment(sketch, "E6435", {"start": v(219.05, 226.87) * mm, "end": v(219.09, 227) * mm});
            skLineSegment(sketch, "E6436", {"start": v(219.09, 227) * mm, "end": v(219.1, 227.05) * mm});
            skLineSegment(sketch, "E6437", {"start": v(219.1, 227.05) * mm, "end": v(219.14, 227.13) * mm});
            skLineSegment(sketch, "E6438", {"start": v(219.14, 227.13) * mm, "end": v(219.19, 227.22) * mm});
            skLineSegment(sketch, "E6439", {"start": v(219.19, 227.22) * mm, "end": v(219.2, 227.25) * mm});
            skLineSegment(sketch, "E6440", {"start": v(219.2, 227.25) * mm, "end": v(219.27, 227.36) * mm});
            skLineSegment(sketch, "E6441", {"start": v(219.27, 227.36) * mm, "end": v(219.35, 227.47) * mm});
            skLineSegment(sketch, "E6442", {"start": v(219.35, 227.47) * mm, "end": v(219.4, 227.53) * mm});
            skLineSegment(sketch, "E6443", {"start": v(219.4, 227.53) * mm, "end": v(219.45, 227.57) * mm});
            skLineSegment(sketch, "E6444", {"start": v(219.45, 227.57) * mm, "end": v(219.54, 227.66) * mm});
            skLineSegment(sketch, "E6445", {"start": v(219.54, 227.66) * mm, "end": v(219.65, 227.74) * mm});
            skLineSegment(sketch, "E6446", {"start": v(219.65, 227.74) * mm, "end": v(219.7, 227.77) * mm});
            skLineSegment(sketch, "E6447", {"start": v(219.7, 227.77) * mm, "end": v(219.77, 227.8) * mm});
            skLineSegment(sketch, "E6448", {"start": v(219.77, 227.8) * mm, "end": v(219.86, 227.86) * mm});
            skLineSegment(sketch, "E6449", {"start": v(219.86, 227.86) * mm, "end": v(219.9, 227.87) * mm});
            skLineSegment(sketch, "E6450", {"start": v(219.9, 227.87) * mm, "end": v(220.01, 227.92) * mm});
            skLineSegment(sketch, "E6451", {"start": v(220.01, 227.92) * mm, "end": v(220.14, 227.96) * mm});
            skLineSegment(sketch, "E6452", {"start": v(220.14, 227.96) * mm, "end": v(220.22, 227.97) * mm});
            skLineSegment(sketch, "E6453", {"start": v(220.22, 227.97) * mm, "end": v(220.28, 227.98) * mm});
            skLineSegment(sketch, "E6454", {"start": v(220.28, 227.98) * mm, "end": v(220.4, 228) * mm});
            skLineSegment(sketch, "E6455", {"start": v(220.4, 228) * mm, "end": v(220.54, 228) * mm});
            skLineSegment(sketch, "E6456", {"start": v(220.54, 228) * mm, "end": v(220.6, 228) * mm});
            skLineSegment(sketch, "E6457", {"start": v(220.6, 228) * mm, "end": v(220.68, 227.99) * mm});
            skLineSegment(sketch, "E6458", {"start": v(220.68, 227.99) * mm, "end": v(220.78, 227.97) * mm});
            skLineSegment(sketch, "E6459", {"start": v(220.78, 227.97) * mm, "end": v(220.81, 227.97) * mm});
            skLineSegment(sketch, "E6460", {"start": v(220.81, 227.97) * mm, "end": v(220.94, 227.93) * mm});
            skLineSegment(sketch, "E6461", {"start": v(220.94, 227.93) * mm, "end": v(221.07, 227.89) * mm});
            skLineSegment(sketch, "E6462", {"start": v(221.07, 227.89) * mm, "end": v(221.14, 227.86) * mm});
            skLineSegment(sketch, "E6463", {"start": v(221.14, 227.86) * mm, "end": v(221.2, 227.83) * mm});
            skLineSegment(sketch, "E6464", {"start": v(221.2, 227.83) * mm, "end": v(221.3, 227.77) * mm});
            skLineSegment(sketch, "E6465", {"start": v(221.3, 227.77) * mm, "end": v(221.41, 227.69) * mm});
            skLineSegment(sketch, "E6466", {"start": v(221.41, 227.69) * mm, "end": v(221.46, 227.66) * mm});
            skLineSegment(sketch, "E6467", {"start": v(221.46, 227.66) * mm, "end": v(221.52, 227.6) * mm});
            skLineSegment(sketch, "E6468", {"start": v(221.52, 227.6) * mm, "end": v(221.6, 227.53) * mm});
            skLineSegment(sketch, "E6469", {"start": v(221.6, 227.53) * mm, "end": v(221.62, 227.5) * mm});
            skLineSegment(sketch, "E6470", {"start": v(221.62, 227.5) * mm, "end": v(221.7, 227.4) * mm});
            skLineSegment(sketch, "E6471", {"start": v(221.7, 227.4) * mm, "end": v(221.78, 227.29) * mm});
            skLineSegment(sketch, "E6472", {"start": v(221.78, 227.29) * mm, "end": v(221.81, 227.22) * mm});
            skLineSegment(sketch, "E6473", {"start": v(221.81, 227.22) * mm, "end": v(221.84, 227.17) * mm});
            skLineSegment(sketch, "E6474", {"start": v(221.84, 227.17) * mm, "end": v(221.9, 227.05) * mm});
            skLineSegment(sketch, "E6475", {"start": v(221.9, 227.05) * mm, "end": v(221.94, 226.92) * mm});
            skLineSegment(sketch, "E6476", {"start": v(221.94, 226.92) * mm, "end": v(221.95, 226.87) * mm});
            skLineSegment(sketch, "E6477", {"start": v(221.95, 226.87) * mm, "end": v(221.97, 226.8) * mm});
            skLineSegment(sketch, "E6478", {"start": v(221.97, 226.8) * mm, "end": v(221.99, 226.69) * mm});
            skLineSegment(sketch, "E6479", {"start": v(221.99, 226.69) * mm, "end": v(222, 226.66) * mm});
            skLineSegment(sketch, "E6480", {"start": v(222, 226.66) * mm, "end": v(222, 226.53) * mm});
            skLineSegment(sketch, "E6481", {"start": v(222, 226.53) * mm, "end": v(222, 226.39) * mm});
            skLineSegment(sketch, "E6482", {"start": v(222, 226.39) * mm, "end": v(221.99, 226.31) * mm});
            skLineSegment(sketch, "E6483", {"start": v(221.99, 226.31) * mm, "end": v(221.98, 226.26) * mm});
            skLineSegment(sketch, "E6484", {"start": v(221.98, 226.26) * mm, "end": v(221.95, 226.13) * mm});
            skLineSegment(sketch, "E6485", {"start": v(221.95, 226.13) * mm, "end": v(221.91, 226) * mm});
            skLineSegment(sketch, "E6486", {"start": v(221.91, 226) * mm, "end": v(221.9, 225.95) * mm});
            skLineSegment(sketch, "E6487", {"start": v(221.9, 225.95) * mm, "end": v(221.86, 225.87) * mm});
            skLineSegment(sketch, "E6488", {"start": v(221.86, 225.87) * mm, "end": v(221.81, 225.78) * mm});
            skLineSegment(sketch, "E6489", {"start": v(221.81, 225.78) * mm, "end": v(221.8, 225.75) * mm});
            skLineSegment(sketch, "E6490", {"start": v(221.8, 225.75) * mm, "end": v(221.73, 225.64) * mm});
            skLineSegment(sketch, "E6491", {"start": v(221.73, 225.64) * mm, "end": v(221.65, 225.53) * mm});
            skLineSegment(sketch, "E6492", {"start": v(221.65, 225.53) * mm, "end": v(221.6, 225.47) * mm});
            skLineSegment(sketch, "E6493", {"start": v(221.6, 225.47) * mm, "end": v(221.55, 225.43) * mm});
            skLineSegment(sketch, "E6494", {"start": v(221.55, 225.43) * mm, "end": v(221.46, 225.34) * mm});
            skLineSegment(sketch, "E6495", {"start": v(221.46, 225.34) * mm, "end": v(221.35, 225.26) * mm});
            skLineSegment(sketch, "E6496", {"start": v(221.35, 225.26) * mm, "end": v(221.3, 225.23) * mm});
            skLineSegment(sketch, "E6497", {"start": v(221.3, 225.23) * mm, "end": v(221.23, 225.2) * mm});
            skLineSegment(sketch, "E6498", {"start": v(221.23, 225.2) * mm, "end": v(221.14, 225.14) * mm});
            skLineSegment(sketch, "E6499", {"start": v(221.14, 225.14) * mm, "end": v(221.11, 225.13) * mm});
            skLineSegment(sketch, "E6500", {"start": v(221.11, 225.13) * mm, "end": v(220.99, 225.08) * mm});
            skLineSegment(sketch, "E6501", {"start": v(220.99, 225.08) * mm, "end": v(220.86, 225.04) * mm});
            skLineSegment(sketch, "E6502", {"start": v(220.86, 225.04) * mm, "end": v(220.8, 225.03) * mm});
            skLineSegment(sketch, "E6503", {"start": v(220.8, 225.03) * mm, "end": v(220.78, 225.03) * mm});
            skLineSegment(sketch, "E6504", {"start": v(220.78, 225.03) * mm, "end": v(220.72, 225.02) * mm});
            skLineSegment(sketch, "E6505", {"start": v(220.72, 225.02) * mm, "end": v(220.6, 225) * mm});
            skLineSegment(sketch, "E6506", {"start": v(220.6, 225) * mm, "end": v(220.46, 225) * mm});
            skLineSegment(sketch, "E6507", {"start": v(220.46, 225) * mm, "end": v(220.4, 225) * mm});
            skLineSegment(sketch, "E6508", {"start": v(189.54, 220.7) * mm, "end": v(189.36, 220.75) * mm});
            skLineSegment(sketch, "E6509", {"start": v(189.36, 220.75) * mm, "end": v(189.18, 220.82) * mm});
            skLineSegment(sketch, "E6510", {"start": v(189.18, 220.82) * mm, "end": v(189.02, 220.9) * mm});
            skLineSegment(sketch, "E6511", {"start": v(189.02, 220.9) * mm, "end": v(188.86, 221.02) * mm});
            skLineSegment(sketch, "E6512", {"start": v(188.86, 221.02) * mm, "end": v(188.72, 221.14) * mm});
            skLineSegment(sketch, "E6513", {"start": v(188.72, 221.14) * mm, "end": v(188.6, 221.29) * mm});
            skLineSegment(sketch, "E6514", {"start": v(188.6, 221.29) * mm, "end": v(188.5, 221.44) * mm});
            skLineSegment(sketch, "E6515", {"start": v(188.5, 221.44) * mm, "end": v(188.41, 221.61) * mm});
            skLineSegment(sketch, "E6516", {"start": v(188.41, 221.61) * mm, "end": v(188.35, 221.8) * mm});
            skLineSegment(sketch, "E6517", {"start": v(188.35, 221.8) * mm, "end": v(188.32, 221.98) * mm});
            skLineSegment(sketch, "E6518", {"start": v(188.32, 221.98) * mm, "end": v(188.3, 222.16) * mm});
            skLineSegment(sketch, "E6519", {"start": v(188.3, 222.16) * mm, "end": v(188.3, 222.26) * mm});
            skLineSegment(sketch, "E6520", {"start": v(188.3, 222.26) * mm, "end": v(188.28, 222.35) * mm});
            skLineSegment(sketch, "E6521", {"start": v(188.28, 222.35) * mm, "end": v(188.24, 222.54) * mm});
            skLineSegment(sketch, "E6522", {"start": v(188.24, 222.54) * mm, "end": v(188.23, 222.73) * mm});
            skLineSegment(sketch, "E6523", {"start": v(188.23, 222.73) * mm, "end": v(188.24, 222.82) * mm});
            skLineSegment(sketch, "E6524", {"start": v(188.24, 222.82) * mm, "end": v(188.2, 222.92) * mm});
            skLineSegment(sketch, "E6525", {"start": v(188.2, 222.92) * mm, "end": v(188.18, 223.1) * mm});
            skLineSegment(sketch, "E6526", {"start": v(188.18, 223.1) * mm, "end": v(188.17, 223.3) * mm});
            skLineSegment(sketch, "E6527", {"start": v(188.17, 223.3) * mm, "end": v(188.18, 223.39) * mm});
            skLineSegment(sketch, "E6528", {"start": v(188.18, 223.39) * mm, "end": v(188.15, 223.48) * mm});
            skLineSegment(sketch, "E6529", {"start": v(188.15, 223.48) * mm, "end": v(188.12, 223.67) * mm});
            skLineSegment(sketch, "E6530", {"start": v(188.12, 223.67) * mm, "end": v(188.12, 223.86) * mm});
            skLineSegment(sketch, "E6531", {"start": v(188.12, 223.86) * mm, "end": v(188.13, 223.95) * mm});
            skLineSegment(sketch, "E6532", {"start": v(188.13, 223.95) * mm, "end": v(188.1, 224.05) * mm});
            skLineSegment(sketch, "E6533", {"start": v(188.1, 224.05) * mm, "end": v(188.08, 224.23) * mm});
            skLineSegment(sketch, "E6534", {"start": v(188.08, 224.23) * mm, "end": v(188.08, 224.42) * mm});
            skLineSegment(sketch, "E6535", {"start": v(188.08, 224.42) * mm, "end": v(188.09, 224.52) * mm});
            skLineSegment(sketch, "E6536", {"start": v(188.09, 224.52) * mm, "end": v(188.07, 224.61) * mm});
            skLineSegment(sketch, "E6537", {"start": v(188.07, 224.61) * mm, "end": v(188.04, 224.8) * mm});
            skLineSegment(sketch, "E6538", {"start": v(188.04, 224.8) * mm, "end": v(188.05, 224.99) * mm});
            skLineSegment(sketch, "E6539", {"start": v(188.05, 224.99) * mm, "end": v(188.06, 225.08) * mm});
            skLineSegment(sketch, "E6540", {"start": v(188.06, 225.08) * mm, "end": v(188.04, 225.18) * mm});
            skLineSegment(sketch, "E6541", {"start": v(188.04, 225.18) * mm, "end": v(188.02, 225.37) * mm});
            skLineSegment(sketch, "E6542", {"start": v(188.02, 225.37) * mm, "end": v(188.03, 225.55) * mm});
            skLineSegment(sketch, "E6543", {"start": v(188.03, 225.55) * mm, "end": v(188.04, 225.65) * mm});
            skLineSegment(sketch, "E6544", {"start": v(188.04, 225.65) * mm, "end": v(188.02, 225.75) * mm});
            skLineSegment(sketch, "E6545", {"start": v(188.02, 225.75) * mm, "end": v(188, 225.93) * mm});
            skLineSegment(sketch, "E6546", {"start": v(188, 225.93) * mm, "end": v(188.01, 226.12) * mm});
            skLineSegment(sketch, "E6547", {"start": v(188.01, 226.12) * mm, "end": v(188.03, 226.22) * mm});
            skLineSegment(sketch, "E6548", {"start": v(188.03, 226.22) * mm, "end": v(188.01, 226.31) * mm});
            skLineSegment(sketch, "E6549", {"start": v(188.01, 226.31) * mm, "end": v(188, 226.5) * mm});
            skLineSegment(sketch, "E6550", {"start": v(188, 226.5) * mm, "end": v(188.01, 226.69) * mm});
            skLineSegment(sketch, "E6551", {"start": v(188.01, 226.69) * mm, "end": v(188.05, 226.87) * mm});
            skLineSegment(sketch, "E6552", {"start": v(188.05, 226.87) * mm, "end": v(188.1, 227.05) * mm});
            skLineSegment(sketch, "E6553", {"start": v(188.1, 227.05) * mm, "end": v(188.19, 227.22) * mm});
            skLineSegment(sketch, "E6554", {"start": v(188.19, 227.22) * mm, "end": v(188.29, 227.38) * mm});
            skLineSegment(sketch, "E6555", {"start": v(188.29, 227.38) * mm, "end": v(188.4, 227.53) * mm});
            skLineSegment(sketch, "E6556", {"start": v(188.4, 227.53) * mm, "end": v(188.54, 227.66) * mm});
            skLineSegment(sketch, "E6557", {"start": v(188.54, 227.66) * mm, "end": v(188.7, 227.77) * mm});
            skLineSegment(sketch, "E6558", {"start": v(188.7, 227.77) * mm, "end": v(188.86, 227.86) * mm});
            skLineSegment(sketch, "E6559", {"start": v(188.86, 227.86) * mm, "end": v(189.04, 227.93) * mm});
            skLineSegment(sketch, "E6560", {"start": v(189.04, 227.93) * mm, "end": v(189.22, 227.97) * mm});
            skLineSegment(sketch, "E6561", {"start": v(189.22, 227.97) * mm, "end": v(189.4, 228) * mm});
            skLineSegment(sketch, "E6562", {"start": v(189.4, 228) * mm, "end": v(189.6, 228) * mm});
            skLineSegment(sketch, "E6563", {"start": v(189.6, 228) * mm, "end": v(189.78, 227.97) * mm});
            skLineSegment(sketch, "E6564", {"start": v(189.78, 227.97) * mm, "end": v(189.96, 227.93) * mm});
            skLineSegment(sketch, "E6565", {"start": v(189.96, 227.93) * mm, "end": v(190.14, 227.86) * mm});
            skLineSegment(sketch, "E6566", {"start": v(190.14, 227.86) * mm, "end": v(190.3, 227.77) * mm});
            skLineSegment(sketch, "E6567", {"start": v(190.3, 227.77) * mm, "end": v(190.46, 227.66) * mm});
            skLineSegment(sketch, "E6568", {"start": v(190.46, 227.66) * mm, "end": v(190.6, 227.53) * mm});
            skLineSegment(sketch, "E6569", {"start": v(190.6, 227.53) * mm, "end": v(190.71, 227.38) * mm});
            skLineSegment(sketch, "E6570", {"start": v(190.71, 227.38) * mm, "end": v(190.81, 227.22) * mm});
            skLineSegment(sketch, "E6571", {"start": v(190.81, 227.22) * mm, "end": v(190.9, 227.05) * mm});
            skLineSegment(sketch, "E6572", {"start": v(190.9, 227.05) * mm, "end": v(190.95, 226.87) * mm});
            skLineSegment(sketch, "E6573", {"start": v(190.95, 226.87) * mm, "end": v(190.99, 226.69) * mm});
            skLineSegment(sketch, "E6574", {"start": v(190.99, 226.69) * mm, "end": v(191, 226.5) * mm});
            skLineSegment(sketch, "E6575", {"start": v(191, 226.5) * mm, "end": v(190.99, 226.31) * mm});
            skLineSegment(sketch, "E6576", {"start": v(190.99, 226.31) * mm, "end": v(190.97, 226.24) * mm});
            skLineSegment(sketch, "E6577", {"start": v(190.97, 226.24) * mm, "end": v(190.99, 226.17) * mm});
            skLineSegment(sketch, "E6578", {"start": v(190.99, 226.17) * mm, "end": v(191, 225.99) * mm});
            skLineSegment(sketch, "E6579", {"start": v(191, 225.99) * mm, "end": v(191, 225.8) * mm});
            skLineSegment(sketch, "E6580", {"start": v(191, 225.8) * mm, "end": v(190.98, 225.73) * mm});
            skLineSegment(sketch, "E6581", {"start": v(190.98, 225.73) * mm, "end": v(191, 225.66) * mm});
            skLineSegment(sketch, "E6582", {"start": v(191, 225.66) * mm, "end": v(191.02, 225.47) * mm});
            skLineSegment(sketch, "E6583", {"start": v(191.02, 225.47) * mm, "end": v(191.01, 225.28) * mm});
            skLineSegment(sketch, "E6584", {"start": v(191.01, 225.28) * mm, "end": v(191, 225.21) * mm});
            skLineSegment(sketch, "E6585", {"start": v(191, 225.21) * mm, "end": v(191.02, 225.14) * mm});
            skLineSegment(sketch, "E6586", {"start": v(191.02, 225.14) * mm, "end": v(191.04, 224.96) * mm});
            skLineSegment(sketch, "E6587", {"start": v(191.04, 224.96) * mm, "end": v(191.04, 224.77) * mm});
            skLineSegment(sketch, "E6588", {"start": v(191.04, 224.77) * mm, "end": v(191.03, 224.7) * mm});
            skLineSegment(sketch, "E6589", {"start": v(191.03, 224.7) * mm, "end": v(191.05, 224.63) * mm});
            skLineSegment(sketch, "E6590", {"start": v(191.05, 224.63) * mm, "end": v(191.07, 224.44) * mm});
            skLineSegment(sketch, "E6591", {"start": v(191.07, 224.44) * mm, "end": v(191.07, 224.25) * mm});
            skLineSegment(sketch, "E6592", {"start": v(191.07, 224.25) * mm, "end": v(191.07, 224.18) * mm});
            skLineSegment(sketch, "E6593", {"start": v(191.07, 224.18) * mm, "end": v(191.08, 224.12) * mm});
            skLineSegment(sketch, "E6594", {"start": v(191.08, 224.12) * mm, "end": v(191.11, 223.93) * mm});
            skLineSegment(sketch, "E6595", {"start": v(191.11, 223.93) * mm, "end": v(191.12, 223.74) * mm});
            skLineSegment(sketch, "E6596", {"start": v(191.12, 223.74) * mm, "end": v(191.11, 223.67) * mm});
            skLineSegment(sketch, "E6597", {"start": v(191.11, 223.67) * mm, "end": v(191.13, 223.6) * mm});
            skLineSegment(sketch, "E6598", {"start": v(191.13, 223.6) * mm, "end": v(191.16, 223.42) * mm});
            skLineSegment(sketch, "E6599", {"start": v(191.16, 223.42) * mm, "end": v(191.17, 223.23) * mm});
            skLineSegment(sketch, "E6600", {"start": v(191.17, 223.23) * mm, "end": v(191.16, 223.16) * mm});
            skLineSegment(sketch, "E6601", {"start": v(191.16, 223.16) * mm, "end": v(191.19, 223.1) * mm});
            skLineSegment(sketch, "E6602", {"start": v(191.19, 223.1) * mm, "end": v(191.22, 222.9) * mm});
            skLineSegment(sketch, "E6603", {"start": v(191.22, 222.9) * mm, "end": v(191.23, 222.72) * mm});
            skLineSegment(sketch, "E6604", {"start": v(191.23, 222.72) * mm, "end": v(191.23, 222.65) * mm});
            skLineSegment(sketch, "E6605", {"start": v(191.23, 222.65) * mm, "end": v(191.25, 222.58) * mm});
            skLineSegment(sketch, "E6606", {"start": v(191.25, 222.58) * mm, "end": v(191.29, 222.4) * mm});
            skLineSegment(sketch, "E6607", {"start": v(191.29, 222.4) * mm, "end": v(191.3, 222.2) * mm});
            skLineSegment(sketch, "E6608", {"start": v(191.3, 222.2) * mm, "end": v(191.3, 222.02) * mm});
            skLineSegment(sketch, "E6609", {"start": v(191.3, 222.02) * mm, "end": v(191.26, 221.83) * mm});
            skLineSegment(sketch, "E6610", {"start": v(191.26, 221.83) * mm, "end": v(191.2, 221.65) * mm});
            skLineSegment(sketch, "E6611", {"start": v(191.2, 221.65) * mm, "end": v(191.13, 221.48) * mm});
            skLineSegment(sketch, "E6612", {"start": v(191.13, 221.48) * mm, "end": v(191.03, 221.32) * mm});
            skLineSegment(sketch, "E6613", {"start": v(191.03, 221.32) * mm, "end": v(190.9, 221.17) * mm});
            skLineSegment(sketch, "E6614", {"start": v(190.9, 221.17) * mm, "end": v(190.77, 221.04) * mm});
            skLineSegment(sketch, "E6615", {"start": v(190.77, 221.04) * mm, "end": v(190.62, 220.93) * mm});
            skLineSegment(sketch, "E6616", {"start": v(190.62, 220.93) * mm, "end": v(190.46, 220.84) * mm});
            skLineSegment(sketch, "E6617", {"start": v(190.46, 220.84) * mm, "end": v(190.28, 220.77) * mm});
            skLineSegment(sketch, "E6618", {"start": v(190.28, 220.77) * mm, "end": v(190.1, 220.72) * mm});
            skLineSegment(sketch, "E6619", {"start": v(190.1, 220.72) * mm, "end": v(189.92, 220.7) * mm});
            skLineSegment(sketch, "E6620", {"start": v(189.92, 220.7) * mm, "end": v(189.73, 220.69) * mm});
            skLineSegment(sketch, "E6621", {"start": v(189.73, 220.69) * mm, "end": v(189.54, 220.7) * mm});
            skLineSegment(sketch, "E6622", {"start": v(39.87, 218) * mm, "end": v(39.63, 218.03) * mm});
            skLineSegment(sketch, "E6623", {"start": v(39.63, 218.03) * mm, "end": v(39.38, 218.1) * mm});
            skLineSegment(sketch, "E6624", {"start": v(39.38, 218.1) * mm, "end": v(39.15, 218.2) * mm});
            skLineSegment(sketch, "E6625", {"start": v(39.15, 218.2) * mm, "end": v(38.93, 218.31) * mm});
            skLineSegment(sketch, "E6626", {"start": v(38.93, 218.31) * mm, "end": v(38.73, 218.46) * mm});
            skLineSegment(sketch, "E6627", {"start": v(38.73, 218.46) * mm, "end": v(38.54, 218.63) * mm});
            skLineSegment(sketch, "E6628", {"start": v(38.54, 218.63) * mm, "end": v(38.38, 218.82) * mm});
            skLineSegment(sketch, "E6629", {"start": v(38.38, 218.82) * mm, "end": v(38.25, 219.04) * mm});
            skLineSegment(sketch, "E6630", {"start": v(38.25, 219.04) * mm, "end": v(38.14, 219.26) * mm});
            skLineSegment(sketch, "E6631", {"start": v(38.14, 219.26) * mm, "end": v(38.06, 219.5) * mm});
            skLineSegment(sketch, "E6632", {"start": v(38.06, 219.5) * mm, "end": v(38.02, 219.75) * mm});
            skLineSegment(sketch, "E6633", {"start": v(38.02, 219.75) * mm, "end": v(38, 220) * mm});
            skLineSegment(sketch, "E6634", {"start": v(38, 220) * mm, "end": v(38.02, 220.25) * mm});
            skLineSegment(sketch, "E6635", {"start": v(38.02, 220.25) * mm, "end": v(38.06, 220.5) * mm});
            skLineSegment(sketch, "E6636", {"start": v(38.06, 220.5) * mm, "end": v(38.14, 220.74) * mm});
            skLineSegment(sketch, "E6637", {"start": v(38.14, 220.74) * mm, "end": v(38.25, 220.96) * mm});
            skLineSegment(sketch, "E6638", {"start": v(38.25, 220.96) * mm, "end": v(38.38, 221.18) * mm});
            skLineSegment(sketch, "E6639", {"start": v(38.38, 221.18) * mm, "end": v(38.54, 221.37) * mm});
            skLineSegment(sketch, "E6640", {"start": v(38.54, 221.37) * mm, "end": v(38.73, 221.54) * mm});
            skLineSegment(sketch, "E6641", {"start": v(38.73, 221.54) * mm, "end": v(38.93, 221.69) * mm});
            skLineSegment(sketch, "E6642", {"start": v(38.93, 221.69) * mm, "end": v(39.15, 221.8) * mm});
            skLineSegment(sketch, "E6643", {"start": v(39.15, 221.8) * mm, "end": v(39.38, 221.9) * mm});
            skLineSegment(sketch, "E6644", {"start": v(39.38, 221.9) * mm, "end": v(39.63, 221.97) * mm});
            skLineSegment(sketch, "E6645", {"start": v(39.63, 221.97) * mm, "end": v(39.87, 222) * mm});
            skLineSegment(sketch, "E6646", {"start": v(39.87, 222) * mm, "end": v(40.13, 222) * mm});
            skLineSegment(sketch, "E6647", {"start": v(40.13, 222) * mm, "end": v(40.37, 221.97) * mm});
            skLineSegment(sketch, "E6648", {"start": v(40.37, 221.97) * mm, "end": v(40.62, 221.9) * mm});
            skLineSegment(sketch, "E6649", {"start": v(40.62, 221.9) * mm, "end": v(40.85, 221.8) * mm});
            skLineSegment(sketch, "E6650", {"start": v(40.85, 221.8) * mm, "end": v(41.07, 221.69) * mm});
            skLineSegment(sketch, "E6651", {"start": v(41.07, 221.69) * mm, "end": v(41.27, 221.54) * mm});
            skLineSegment(sketch, "E6652", {"start": v(41.27, 221.54) * mm, "end": v(41.46, 221.37) * mm});
            skLineSegment(sketch, "E6653", {"start": v(41.46, 221.37) * mm, "end": v(41.62, 221.18) * mm});
            skLineSegment(sketch, "E6654", {"start": v(41.62, 221.18) * mm, "end": v(41.75, 220.96) * mm});
            skLineSegment(sketch, "E6655", {"start": v(41.75, 220.96) * mm, "end": v(41.86, 220.74) * mm});
            skLineSegment(sketch, "E6656", {"start": v(41.86, 220.74) * mm, "end": v(41.94, 220.5) * mm});
            skLineSegment(sketch, "E6657", {"start": v(41.94, 220.5) * mm, "end": v(41.98, 220.25) * mm});
            skLineSegment(sketch, "E6658", {"start": v(41.98, 220.25) * mm, "end": v(42, 220) * mm});
            skLineSegment(sketch, "E6659", {"start": v(42, 220) * mm, "end": v(41.98, 219.75) * mm});
            skLineSegment(sketch, "E6660", {"start": v(41.98, 219.75) * mm, "end": v(41.94, 219.5) * mm});
            skLineSegment(sketch, "E6661", {"start": v(41.94, 219.5) * mm, "end": v(41.86, 219.26) * mm});
            skLineSegment(sketch, "E6662", {"start": v(41.86, 219.26) * mm, "end": v(41.75, 219.04) * mm});
            skLineSegment(sketch, "E6663", {"start": v(41.75, 219.04) * mm, "end": v(41.62, 218.82) * mm});
            skLineSegment(sketch, "E6664", {"start": v(41.62, 218.82) * mm, "end": v(41.46, 218.63) * mm});
            skLineSegment(sketch, "E6665", {"start": v(41.46, 218.63) * mm, "end": v(41.27, 218.46) * mm});
            skLineSegment(sketch, "E6666", {"start": v(41.27, 218.46) * mm, "end": v(41.07, 218.31) * mm});
            skLineSegment(sketch, "E6667", {"start": v(41.07, 218.31) * mm, "end": v(40.85, 218.2) * mm});
            skLineSegment(sketch, "E6668", {"start": v(40.85, 218.2) * mm, "end": v(40.62, 218.1) * mm});
            skLineSegment(sketch, "E6669", {"start": v(40.62, 218.1) * mm, "end": v(40.37, 218.03) * mm});
            skLineSegment(sketch, "E6670", {"start": v(40.37, 218.03) * mm, "end": v(40.13, 218) * mm});
            skLineSegment(sketch, "E6671", {"start": v(40.13, 218) * mm, "end": v(39.87, 218) * mm});
            skLineSegment(sketch, "E6672", {"start": v(369.87, 218) * mm, "end": v(369.62, 218.03) * mm});
            skLineSegment(sketch, "E6673", {"start": v(369.62, 218.03) * mm, "end": v(369.38, 218.1) * mm});
            skLineSegment(sketch, "E6674", {"start": v(369.38, 218.1) * mm, "end": v(369.15, 218.2) * mm});
            skLineSegment(sketch, "E6675", {"start": v(369.15, 218.2) * mm, "end": v(368.93, 218.31) * mm});
            skLineSegment(sketch, "E6676", {"start": v(368.93, 218.31) * mm, "end": v(368.73, 218.46) * mm});
            skLineSegment(sketch, "E6677", {"start": v(368.73, 218.46) * mm, "end": v(368.54, 218.63) * mm});
            skLineSegment(sketch, "E6678", {"start": v(368.54, 218.63) * mm, "end": v(368.38, 218.82) * mm});
            skLineSegment(sketch, "E6679", {"start": v(368.38, 218.82) * mm, "end": v(368.25, 219.04) * mm});
            skLineSegment(sketch, "E6680", {"start": v(368.25, 219.04) * mm, "end": v(368.14, 219.26) * mm});
            skLineSegment(sketch, "E6681", {"start": v(368.14, 219.26) * mm, "end": v(368.06, 219.5) * mm});
            skLineSegment(sketch, "E6682", {"start": v(368.06, 219.5) * mm, "end": v(368.02, 219.75) * mm});
            skLineSegment(sketch, "E6683", {"start": v(368.02, 219.75) * mm, "end": v(368, 220) * mm});
            skLineSegment(sketch, "E6684", {"start": v(368, 220) * mm, "end": v(368.02, 220.25) * mm});
            skLineSegment(sketch, "E6685", {"start": v(368.02, 220.25) * mm, "end": v(368.06, 220.5) * mm});
            skLineSegment(sketch, "E6686", {"start": v(368.06, 220.5) * mm, "end": v(368.14, 220.74) * mm});
            skLineSegment(sketch, "E6687", {"start": v(368.14, 220.74) * mm, "end": v(368.25, 220.96) * mm});
            skLineSegment(sketch, "E6688", {"start": v(368.25, 220.96) * mm, "end": v(368.38, 221.18) * mm});
            skLineSegment(sketch, "E6689", {"start": v(368.38, 221.18) * mm, "end": v(368.54, 221.37) * mm});
            skLineSegment(sketch, "E6690", {"start": v(368.54, 221.37) * mm, "end": v(368.73, 221.54) * mm});
            skLineSegment(sketch, "E6691", {"start": v(368.73, 221.54) * mm, "end": v(368.93, 221.69) * mm});
            skLineSegment(sketch, "E6692", {"start": v(368.93, 221.69) * mm, "end": v(369.15, 221.8) * mm});
            skLineSegment(sketch, "E6693", {"start": v(369.15, 221.8) * mm, "end": v(369.38, 221.9) * mm});
            skLineSegment(sketch, "E6694", {"start": v(369.38, 221.9) * mm, "end": v(369.62, 221.97) * mm});
            skLineSegment(sketch, "E6695", {"start": v(369.62, 221.97) * mm, "end": v(369.87, 222) * mm});
            skLineSegment(sketch, "E6696", {"start": v(369.87, 222) * mm, "end": v(370.13, 222) * mm});
            skLineSegment(sketch, "E6697", {"start": v(370.13, 222) * mm, "end": v(370.38, 221.97) * mm});
            skLineSegment(sketch, "E6698", {"start": v(370.38, 221.97) * mm, "end": v(370.62, 221.9) * mm});
            skLineSegment(sketch, "E6699", {"start": v(370.62, 221.9) * mm, "end": v(370.85, 221.8) * mm});
            skLineSegment(sketch, "E6700", {"start": v(370.85, 221.8) * mm, "end": v(371.07, 221.69) * mm});
            skLineSegment(sketch, "E6701", {"start": v(371.07, 221.69) * mm, "end": v(371.27, 221.54) * mm});
            skLineSegment(sketch, "E6702", {"start": v(371.27, 221.54) * mm, "end": v(371.46, 221.37) * mm});
            skLineSegment(sketch, "E6703", {"start": v(371.46, 221.37) * mm, "end": v(371.62, 221.18) * mm});
            skLineSegment(sketch, "E6704", {"start": v(371.62, 221.18) * mm, "end": v(371.75, 220.96) * mm});
            skLineSegment(sketch, "E6705", {"start": v(371.75, 220.96) * mm, "end": v(371.86, 220.74) * mm});
            skLineSegment(sketch, "E6706", {"start": v(371.86, 220.74) * mm, "end": v(371.94, 220.5) * mm});
            skLineSegment(sketch, "E6707", {"start": v(371.94, 220.5) * mm, "end": v(371.98, 220.25) * mm});
            skLineSegment(sketch, "E6708", {"start": v(371.98, 220.25) * mm, "end": v(372, 220) * mm});
            skLineSegment(sketch, "E6709", {"start": v(372, 220) * mm, "end": v(371.98, 219.75) * mm});
            skLineSegment(sketch, "E6710", {"start": v(371.98, 219.75) * mm, "end": v(371.94, 219.5) * mm});
            skLineSegment(sketch, "E6711", {"start": v(371.94, 219.5) * mm, "end": v(371.86, 219.26) * mm});
            skLineSegment(sketch, "E6712", {"start": v(371.86, 219.26) * mm, "end": v(371.75, 219.04) * mm});
            skLineSegment(sketch, "E6713", {"start": v(371.75, 219.04) * mm, "end": v(371.62, 218.82) * mm});
            skLineSegment(sketch, "E6714", {"start": v(371.62, 218.82) * mm, "end": v(371.46, 218.63) * mm});
            skLineSegment(sketch, "E6715", {"start": v(371.46, 218.63) * mm, "end": v(371.27, 218.46) * mm});
            skLineSegment(sketch, "E6716", {"start": v(371.27, 218.46) * mm, "end": v(371.07, 218.31) * mm});
            skLineSegment(sketch, "E6717", {"start": v(371.07, 218.31) * mm, "end": v(370.85, 218.2) * mm});
            skLineSegment(sketch, "E6718", {"start": v(370.85, 218.2) * mm, "end": v(370.62, 218.1) * mm});
            skLineSegment(sketch, "E6719", {"start": v(370.62, 218.1) * mm, "end": v(370.38, 218.03) * mm});
            skLineSegment(sketch, "E6720", {"start": v(370.38, 218.03) * mm, "end": v(370.13, 218) * mm});
            skLineSegment(sketch, "E6721", {"start": v(370.13, 218) * mm, "end": v(369.87, 218) * mm});
            skLineSegment(sketch, "E6722", {"start": v(362, 180) * mm, "end": v(362, 200) * mm});
            skLineSegment(sketch, "E6723", {"start": v(362, 200) * mm, "end": v(378, 200) * mm});
            skLineSegment(sketch, "E6724", {"start": v(378, 200) * mm, "end": v(378, 180) * mm});
            skLineSegment(sketch, "E6725", {"start": v(378, 180) * mm, "end": v(362, 180) * mm});
            skLineSegment(sketch, "E6726", {"start": v(32, 180) * mm, "end": v(32, 200) * mm});
            skLineSegment(sketch, "E6727", {"start": v(32, 200) * mm, "end": v(48, 200) * mm});
            skLineSegment(sketch, "E6728", {"start": v(48, 200) * mm, "end": v(48, 180) * mm});
            skLineSegment(sketch, "E6729", {"start": v(48, 180) * mm, "end": v(32, 180) * mm});
            skLineSegment(sketch, "E6730", {"start": v(39.87, 158) * mm, "end": v(39.63, 158.03) * mm});
            skLineSegment(sketch, "E6731", {"start": v(39.63, 158.03) * mm, "end": v(39.38, 158.1) * mm});
            skLineSegment(sketch, "E6732", {"start": v(39.38, 158.1) * mm, "end": v(39.15, 158.2) * mm});
            skLineSegment(sketch, "E6733", {"start": v(39.15, 158.2) * mm, "end": v(38.93, 158.31) * mm});
            skLineSegment(sketch, "E6734", {"start": v(38.93, 158.31) * mm, "end": v(38.73, 158.46) * mm});
            skLineSegment(sketch, "E6735", {"start": v(38.73, 158.46) * mm, "end": v(38.54, 158.63) * mm});
            skLineSegment(sketch, "E6736", {"start": v(38.54, 158.63) * mm, "end": v(38.38, 158.82) * mm});
            skLineSegment(sketch, "E6737", {"start": v(38.38, 158.82) * mm, "end": v(38.25, 159.04) * mm});
            skLineSegment(sketch, "E6738", {"start": v(38.25, 159.04) * mm, "end": v(38.14, 159.26) * mm});
            skLineSegment(sketch, "E6739", {"start": v(38.14, 159.26) * mm, "end": v(38.06, 159.5) * mm});
            skLineSegment(sketch, "E6740", {"start": v(38.06, 159.5) * mm, "end": v(38.02, 159.75) * mm});
            skLineSegment(sketch, "E6741", {"start": v(38.02, 159.75) * mm, "end": v(38, 160) * mm});
            skLineSegment(sketch, "E6742", {"start": v(38, 160) * mm, "end": v(38.02, 160.25) * mm});
            skLineSegment(sketch, "E6743", {"start": v(38.02, 160.25) * mm, "end": v(38.06, 160.5) * mm});
            skLineSegment(sketch, "E6744", {"start": v(38.06, 160.5) * mm, "end": v(38.14, 160.74) * mm});
            skLineSegment(sketch, "E6745", {"start": v(38.14, 160.74) * mm, "end": v(38.25, 160.96) * mm});
            skLineSegment(sketch, "E6746", {"start": v(38.25, 160.96) * mm, "end": v(38.38, 161.18) * mm});
            skLineSegment(sketch, "E6747", {"start": v(38.38, 161.18) * mm, "end": v(38.54, 161.37) * mm});
            skLineSegment(sketch, "E6748", {"start": v(38.54, 161.37) * mm, "end": v(38.73, 161.54) * mm});
            skLineSegment(sketch, "E6749", {"start": v(38.73, 161.54) * mm, "end": v(38.93, 161.69) * mm});
            skLineSegment(sketch, "E6750", {"start": v(38.93, 161.69) * mm, "end": v(39.15, 161.8) * mm});
            skLineSegment(sketch, "E6751", {"start": v(39.15, 161.8) * mm, "end": v(39.38, 161.9) * mm});
            skLineSegment(sketch, "E6752", {"start": v(39.38, 161.9) * mm, "end": v(39.63, 161.97) * mm});
            skLineSegment(sketch, "E6753", {"start": v(39.63, 161.97) * mm, "end": v(39.87, 162) * mm});
            skLineSegment(sketch, "E6754", {"start": v(39.87, 162) * mm, "end": v(40.13, 162) * mm});
            skLineSegment(sketch, "E6755", {"start": v(40.13, 162) * mm, "end": v(40.37, 161.97) * mm});
            skLineSegment(sketch, "E6756", {"start": v(40.37, 161.97) * mm, "end": v(40.62, 161.9) * mm});
            skLineSegment(sketch, "E6757", {"start": v(40.62, 161.9) * mm, "end": v(40.85, 161.8) * mm});
            skLineSegment(sketch, "E6758", {"start": v(40.85, 161.8) * mm, "end": v(41.07, 161.69) * mm});
            skLineSegment(sketch, "E6759", {"start": v(41.07, 161.69) * mm, "end": v(41.27, 161.54) * mm});
            skLineSegment(sketch, "E6760", {"start": v(41.27, 161.54) * mm, "end": v(41.46, 161.37) * mm});
            skLineSegment(sketch, "E6761", {"start": v(41.46, 161.37) * mm, "end": v(41.62, 161.18) * mm});
            skLineSegment(sketch, "E6762", {"start": v(41.62, 161.18) * mm, "end": v(41.75, 160.96) * mm});
            skLineSegment(sketch, "E6763", {"start": v(41.75, 160.96) * mm, "end": v(41.86, 160.74) * mm});
            skLineSegment(sketch, "E6764", {"start": v(41.86, 160.74) * mm, "end": v(41.94, 160.5) * mm});
            skLineSegment(sketch, "E6765", {"start": v(41.94, 160.5) * mm, "end": v(41.98, 160.25) * mm});
            skLineSegment(sketch, "E6766", {"start": v(41.98, 160.25) * mm, "end": v(42, 160) * mm});
            skLineSegment(sketch, "E6767", {"start": v(42, 160) * mm, "end": v(41.98, 159.75) * mm});
            skLineSegment(sketch, "E6768", {"start": v(41.98, 159.75) * mm, "end": v(41.94, 159.5) * mm});
            skLineSegment(sketch, "E6769", {"start": v(41.94, 159.5) * mm, "end": v(41.86, 159.26) * mm});
            skLineSegment(sketch, "E6770", {"start": v(41.86, 159.26) * mm, "end": v(41.75, 159.04) * mm});
            skLineSegment(sketch, "E6771", {"start": v(41.75, 159.04) * mm, "end": v(41.62, 158.82) * mm});
            skLineSegment(sketch, "E6772", {"start": v(41.62, 158.82) * mm, "end": v(41.46, 158.63) * mm});
            skLineSegment(sketch, "E6773", {"start": v(41.46, 158.63) * mm, "end": v(41.27, 158.46) * mm});
            skLineSegment(sketch, "E6774", {"start": v(41.27, 158.46) * mm, "end": v(41.07, 158.31) * mm});
            skLineSegment(sketch, "E6775", {"start": v(41.07, 158.31) * mm, "end": v(40.85, 158.2) * mm});
            skLineSegment(sketch, "E6776", {"start": v(40.85, 158.2) * mm, "end": v(40.62, 158.1) * mm});
            skLineSegment(sketch, "E6777", {"start": v(40.62, 158.1) * mm, "end": v(40.37, 158.03) * mm});
            skLineSegment(sketch, "E6778", {"start": v(40.37, 158.03) * mm, "end": v(40.13, 158) * mm});
            skLineSegment(sketch, "E6779", {"start": v(40.13, 158) * mm, "end": v(39.87, 158) * mm});
            skLineSegment(sketch, "E6780", {"start": v(369.87, 158) * mm, "end": v(369.62, 158.03) * mm});
            skLineSegment(sketch, "E6781", {"start": v(369.62, 158.03) * mm, "end": v(369.38, 158.1) * mm});
            skLineSegment(sketch, "E6782", {"start": v(369.38, 158.1) * mm, "end": v(369.15, 158.2) * mm});
            skLineSegment(sketch, "E6783", {"start": v(369.15, 158.2) * mm, "end": v(368.93, 158.31) * mm});
            skLineSegment(sketch, "E6784", {"start": v(368.93, 158.31) * mm, "end": v(368.73, 158.46) * mm});
            skLineSegment(sketch, "E6785", {"start": v(368.73, 158.46) * mm, "end": v(368.54, 158.63) * mm});
            skLineSegment(sketch, "E6786", {"start": v(368.54, 158.63) * mm, "end": v(368.38, 158.82) * mm});
            skLineSegment(sketch, "E6787", {"start": v(368.38, 158.82) * mm, "end": v(368.25, 159.04) * mm});
            skLineSegment(sketch, "E6788", {"start": v(368.25, 159.04) * mm, "end": v(368.14, 159.26) * mm});
            skLineSegment(sketch, "E6789", {"start": v(368.14, 159.26) * mm, "end": v(368.06, 159.5) * mm});
            skLineSegment(sketch, "E6790", {"start": v(368.06, 159.5) * mm, "end": v(368.02, 159.75) * mm});
            skLineSegment(sketch, "E6791", {"start": v(368.02, 159.75) * mm, "end": v(368, 160) * mm});
            skLineSegment(sketch, "E6792", {"start": v(368, 160) * mm, "end": v(368.02, 160.25) * mm});
            skLineSegment(sketch, "E6793", {"start": v(368.02, 160.25) * mm, "end": v(368.06, 160.5) * mm});
            skLineSegment(sketch, "E6794", {"start": v(368.06, 160.5) * mm, "end": v(368.14, 160.74) * mm});
            skLineSegment(sketch, "E6795", {"start": v(368.14, 160.74) * mm, "end": v(368.25, 160.96) * mm});
            skLineSegment(sketch, "E6796", {"start": v(368.25, 160.96) * mm, "end": v(368.38, 161.18) * mm});
            skLineSegment(sketch, "E6797", {"start": v(368.38, 161.18) * mm, "end": v(368.54, 161.37) * mm});
            skLineSegment(sketch, "E6798", {"start": v(368.54, 161.37) * mm, "end": v(368.73, 161.54) * mm});
            skLineSegment(sketch, "E6799", {"start": v(368.73, 161.54) * mm, "end": v(368.93, 161.69) * mm});
            skLineSegment(sketch, "E6800", {"start": v(368.93, 161.69) * mm, "end": v(369.15, 161.8) * mm});
            skLineSegment(sketch, "E6801", {"start": v(369.15, 161.8) * mm, "end": v(369.38, 161.9) * mm});
            skLineSegment(sketch, "E6802", {"start": v(369.38, 161.9) * mm, "end": v(369.62, 161.97) * mm});
            skLineSegment(sketch, "E6803", {"start": v(369.62, 161.97) * mm, "end": v(369.87, 162) * mm});
            skLineSegment(sketch, "E6804", {"start": v(369.87, 162) * mm, "end": v(370.13, 162) * mm});
            skLineSegment(sketch, "E6805", {"start": v(370.13, 162) * mm, "end": v(370.38, 161.97) * mm});
            skLineSegment(sketch, "E6806", {"start": v(370.38, 161.97) * mm, "end": v(370.62, 161.9) * mm});
            skLineSegment(sketch, "E6807", {"start": v(370.62, 161.9) * mm, "end": v(370.85, 161.8) * mm});
            skLineSegment(sketch, "E6808", {"start": v(370.85, 161.8) * mm, "end": v(371.07, 161.69) * mm});
            skLineSegment(sketch, "E6809", {"start": v(371.07, 161.69) * mm, "end": v(371.27, 161.54) * mm});
            skLineSegment(sketch, "E6810", {"start": v(371.27, 161.54) * mm, "end": v(371.46, 161.37) * mm});
            skLineSegment(sketch, "E6811", {"start": v(371.46, 161.37) * mm, "end": v(371.62, 161.18) * mm});
            skLineSegment(sketch, "E6812", {"start": v(371.62, 161.18) * mm, "end": v(371.75, 160.96) * mm});
            skLineSegment(sketch, "E6813", {"start": v(371.75, 160.96) * mm, "end": v(371.86, 160.74) * mm});
            skLineSegment(sketch, "E6814", {"start": v(371.86, 160.74) * mm, "end": v(371.94, 160.5) * mm});
            skLineSegment(sketch, "E6815", {"start": v(371.94, 160.5) * mm, "end": v(371.98, 160.25) * mm});
            skLineSegment(sketch, "E6816", {"start": v(371.98, 160.25) * mm, "end": v(372, 160) * mm});
            skLineSegment(sketch, "E6817", {"start": v(372, 160) * mm, "end": v(371.98, 159.75) * mm});
            skLineSegment(sketch, "E6818", {"start": v(371.98, 159.75) * mm, "end": v(371.94, 159.5) * mm});
            skLineSegment(sketch, "E6819", {"start": v(371.94, 159.5) * mm, "end": v(371.86, 159.26) * mm});
            skLineSegment(sketch, "E6820", {"start": v(371.86, 159.26) * mm, "end": v(371.75, 159.04) * mm});
            skLineSegment(sketch, "E6821", {"start": v(371.75, 159.04) * mm, "end": v(371.62, 158.82) * mm});
            skLineSegment(sketch, "E6822", {"start": v(371.62, 158.82) * mm, "end": v(371.46, 158.63) * mm});
            skLineSegment(sketch, "E6823", {"start": v(371.46, 158.63) * mm, "end": v(371.27, 158.46) * mm});
            skLineSegment(sketch, "E6824", {"start": v(371.27, 158.46) * mm, "end": v(371.07, 158.31) * mm});
            skLineSegment(sketch, "E6825", {"start": v(371.07, 158.31) * mm, "end": v(370.85, 158.2) * mm});
            skLineSegment(sketch, "E6826", {"start": v(370.85, 158.2) * mm, "end": v(370.62, 158.1) * mm});
            skLineSegment(sketch, "E6827", {"start": v(370.62, 158.1) * mm, "end": v(370.38, 158.03) * mm});
            skLineSegment(sketch, "E6828", {"start": v(370.38, 158.03) * mm, "end": v(370.13, 158) * mm});
            skLineSegment(sketch, "E6829", {"start": v(370.13, 158) * mm, "end": v(369.87, 158) * mm});
            skLineSegment(sketch, "E6830", {"start": v(55.4, 94) * mm, "end": v(55.22, 94.03) * mm});
            skLineSegment(sketch, "E6831", {"start": v(55.22, 94.03) * mm, "end": v(55.04, 94.07) * mm});
            skLineSegment(sketch, "E6832", {"start": v(55.04, 94.07) * mm, "end": v(54.86, 94.14) * mm});
            skLineSegment(sketch, "E6833", {"start": v(54.86, 94.14) * mm, "end": v(54.7, 94.23) * mm});
            skLineSegment(sketch, "E6834", {"start": v(54.7, 94.23) * mm, "end": v(54.54, 94.34) * mm});
            skLineSegment(sketch, "E6835", {"start": v(54.54, 94.34) * mm, "end": v(54.4, 94.47) * mm});
            skLineSegment(sketch, "E6836", {"start": v(54.4, 94.47) * mm, "end": v(54.29, 94.62) * mm});
            skLineSegment(sketch, "E6837", {"start": v(54.29, 94.62) * mm, "end": v(54.19, 94.78) * mm});
            skLineSegment(sketch, "E6838", {"start": v(54.19, 94.78) * mm, "end": v(54.1, 94.95) * mm});
            skLineSegment(sketch, "E6839", {"start": v(54.1, 94.95) * mm, "end": v(54.05, 95.13) * mm});
            skLineSegment(sketch, "E6840", {"start": v(54.05, 95.13) * mm, "end": v(54.01, 95.31) * mm});
            skLineSegment(sketch, "E6841", {"start": v(54.01, 95.31) * mm, "end": v(54, 95.5) * mm});
            skLineSegment(sketch, "E6842", {"start": v(54, 95.5) * mm, "end": v(54.01, 95.69) * mm});
            skLineSegment(sketch, "E6843", {"start": v(54.01, 95.69) * mm, "end": v(54.05, 95.87) * mm});
            skLineSegment(sketch, "E6844", {"start": v(54.05, 95.87) * mm, "end": v(54.1, 96.05) * mm});
            skLineSegment(sketch, "E6845", {"start": v(54.1, 96.05) * mm, "end": v(54.19, 96.22) * mm});
            skLineSegment(sketch, "E6846", {"start": v(54.19, 96.22) * mm, "end": v(54.29, 96.38) * mm});
            skLineSegment(sketch, "E6847", {"start": v(54.29, 96.38) * mm, "end": v(54.4, 96.53) * mm});
            skLineSegment(sketch, "E6848", {"start": v(54.4, 96.53) * mm, "end": v(54.54, 96.66) * mm});
            skLineSegment(sketch, "E6849", {"start": v(54.54, 96.66) * mm, "end": v(54.7, 96.77) * mm});
            skLineSegment(sketch, "E6850", {"start": v(54.7, 96.77) * mm, "end": v(54.86, 96.86) * mm});
            skLineSegment(sketch, "E6851", {"start": v(54.86, 96.86) * mm, "end": v(55.04, 96.93) * mm});
            skLineSegment(sketch, "E6852", {"start": v(55.04, 96.93) * mm, "end": v(55.22, 96.97) * mm});
            skLineSegment(sketch, "E6853", {"start": v(55.22, 96.97) * mm, "end": v(55.4, 97) * mm});
            skLineSegment(sketch, "E6854", {"start": v(55.4, 97) * mm, "end": v(55.6, 97) * mm});
            skLineSegment(sketch, "E6855", {"start": v(55.6, 97) * mm, "end": v(55.78, 96.97) * mm});
            skLineSegment(sketch, "E6856", {"start": v(55.78, 96.97) * mm, "end": v(55.96, 96.93) * mm});
            skLineSegment(sketch, "E6857", {"start": v(55.96, 96.93) * mm, "end": v(56.14, 96.86) * mm});
            skLineSegment(sketch, "E6858", {"start": v(56.14, 96.86) * mm, "end": v(56.3, 96.77) * mm});
            skLineSegment(sketch, "E6859", {"start": v(56.3, 96.77) * mm, "end": v(56.46, 96.66) * mm});
            skLineSegment(sketch, "E6860", {"start": v(56.46, 96.66) * mm, "end": v(56.6, 96.53) * mm});
            skLineSegment(sketch, "E6861", {"start": v(56.6, 96.53) * mm, "end": v(56.71, 96.38) * mm});
            skLineSegment(sketch, "E6862", {"start": v(56.71, 96.38) * mm, "end": v(56.81, 96.22) * mm});
            skLineSegment(sketch, "E6863", {"start": v(56.81, 96.22) * mm, "end": v(56.9, 96.05) * mm});
            skLineSegment(sketch, "E6864", {"start": v(56.9, 96.05) * mm, "end": v(56.95, 95.87) * mm});
            skLineSegment(sketch, "E6865", {"start": v(56.95, 95.87) * mm, "end": v(56.99, 95.69) * mm});
            skLineSegment(sketch, "E6866", {"start": v(56.99, 95.69) * mm, "end": v(57, 95.5) * mm});
            skLineSegment(sketch, "E6867", {"start": v(57, 95.5) * mm, "end": v(56.99, 95.31) * mm});
            skLineSegment(sketch, "E6868", {"start": v(56.99, 95.31) * mm, "end": v(56.95, 95.13) * mm});
            skLineSegment(sketch, "E6869", {"start": v(56.95, 95.13) * mm, "end": v(56.9, 94.95) * mm});
            skLineSegment(sketch, "E6870", {"start": v(56.9, 94.95) * mm, "end": v(56.81, 94.78) * mm});
            skLineSegment(sketch, "E6871", {"start": v(56.81, 94.78) * mm, "end": v(56.71, 94.62) * mm});
            skLineSegment(sketch, "E6872", {"start": v(56.71, 94.62) * mm, "end": v(56.6, 94.47) * mm});
            skLineSegment(sketch, "E6873", {"start": v(56.6, 94.47) * mm, "end": v(56.46, 94.34) * mm});
            skLineSegment(sketch, "E6874", {"start": v(56.46, 94.34) * mm, "end": v(56.3, 94.23) * mm});
            skLineSegment(sketch, "E6875", {"start": v(56.3, 94.23) * mm, "end": v(56.14, 94.14) * mm});
            skLineSegment(sketch, "E6876", {"start": v(56.14, 94.14) * mm, "end": v(55.96, 94.07) * mm});
            skLineSegment(sketch, "E6877", {"start": v(55.96, 94.07) * mm, "end": v(55.78, 94.03) * mm});
            skLineSegment(sketch, "E6878", {"start": v(55.78, 94.03) * mm, "end": v(55.6, 94) * mm});
            skLineSegment(sketch, "E6879", {"start": v(55.6, 94) * mm, "end": v(55.4, 94) * mm});
            skLineSegment(sketch, "E6880", {"start": v(354.4, 94) * mm, "end": v(354.22, 94.03) * mm});
            skLineSegment(sketch, "E6881", {"start": v(354.22, 94.03) * mm, "end": v(354.04, 94.07) * mm});
            skLineSegment(sketch, "E6882", {"start": v(354.04, 94.07) * mm, "end": v(353.86, 94.14) * mm});
            skLineSegment(sketch, "E6883", {"start": v(353.86, 94.14) * mm, "end": v(353.7, 94.23) * mm});
            skLineSegment(sketch, "E6884", {"start": v(353.7, 94.23) * mm, "end": v(353.54, 94.34) * mm});
            skLineSegment(sketch, "E6885", {"start": v(353.54, 94.34) * mm, "end": v(353.4, 94.47) * mm});
            skLineSegment(sketch, "E6886", {"start": v(353.4, 94.47) * mm, "end": v(353.29, 94.62) * mm});
            skLineSegment(sketch, "E6887", {"start": v(353.29, 94.62) * mm, "end": v(353.19, 94.78) * mm});
            skLineSegment(sketch, "E6888", {"start": v(353.19, 94.78) * mm, "end": v(353.1, 94.95) * mm});
            skLineSegment(sketch, "E6889", {"start": v(353.1, 94.95) * mm, "end": v(353.05, 95.13) * mm});
            skLineSegment(sketch, "E6890", {"start": v(353.05, 95.13) * mm, "end": v(353.01, 95.31) * mm});
            skLineSegment(sketch, "E6891", {"start": v(353.01, 95.31) * mm, "end": v(353, 95.5) * mm});
            skLineSegment(sketch, "E6892", {"start": v(353, 95.5) * mm, "end": v(353.01, 95.69) * mm});
            skLineSegment(sketch, "E6893", {"start": v(353.01, 95.69) * mm, "end": v(353.05, 95.87) * mm});
            skLineSegment(sketch, "E6894", {"start": v(353.05, 95.87) * mm, "end": v(353.1, 96.05) * mm});
            skLineSegment(sketch, "E6895", {"start": v(353.1, 96.05) * mm, "end": v(353.19, 96.22) * mm});
            skLineSegment(sketch, "E6896", {"start": v(353.19, 96.22) * mm, "end": v(353.29, 96.38) * mm});
            skLineSegment(sketch, "E6897", {"start": v(353.29, 96.38) * mm, "end": v(353.4, 96.53) * mm});
            skLineSegment(sketch, "E6898", {"start": v(353.4, 96.53) * mm, "end": v(353.54, 96.66) * mm});
            skLineSegment(sketch, "E6899", {"start": v(353.54, 96.66) * mm, "end": v(353.7, 96.77) * mm});
            skLineSegment(sketch, "E6900", {"start": v(353.7, 96.77) * mm, "end": v(353.86, 96.86) * mm});
            skLineSegment(sketch, "E6901", {"start": v(353.86, 96.86) * mm, "end": v(354.04, 96.93) * mm});
            skLineSegment(sketch, "E6902", {"start": v(354.04, 96.93) * mm, "end": v(354.22, 96.97) * mm});
            skLineSegment(sketch, "E6903", {"start": v(354.22, 96.97) * mm, "end": v(354.4, 97) * mm});
            skLineSegment(sketch, "E6904", {"start": v(354.4, 97) * mm, "end": v(354.6, 97) * mm});
            skLineSegment(sketch, "E6905", {"start": v(354.6, 97) * mm, "end": v(354.78, 96.97) * mm});
            skLineSegment(sketch, "E6906", {"start": v(354.78, 96.97) * mm, "end": v(354.96, 96.93) * mm});
            skLineSegment(sketch, "E6907", {"start": v(354.96, 96.93) * mm, "end": v(355.14, 96.86) * mm});
            skLineSegment(sketch, "E6908", {"start": v(355.14, 96.86) * mm, "end": v(355.3, 96.77) * mm});
            skLineSegment(sketch, "E6909", {"start": v(355.3, 96.77) * mm, "end": v(355.46, 96.66) * mm});
            skLineSegment(sketch, "E6910", {"start": v(355.46, 96.66) * mm, "end": v(355.6, 96.53) * mm});
            skLineSegment(sketch, "E6911", {"start": v(355.6, 96.53) * mm, "end": v(355.71, 96.38) * mm});
            skLineSegment(sketch, "E6912", {"start": v(355.71, 96.38) * mm, "end": v(355.81, 96.22) * mm});
            skLineSegment(sketch, "E6913", {"start": v(355.81, 96.22) * mm, "end": v(355.9, 96.05) * mm});
            skLineSegment(sketch, "E6914", {"start": v(355.9, 96.05) * mm, "end": v(355.95, 95.87) * mm});
            skLineSegment(sketch, "E6915", {"start": v(355.95, 95.87) * mm, "end": v(355.99, 95.69) * mm});
            skLineSegment(sketch, "E6916", {"start": v(355.99, 95.69) * mm, "end": v(356, 95.5) * mm});
            skLineSegment(sketch, "E6917", {"start": v(356, 95.5) * mm, "end": v(355.99, 95.31) * mm});
            skLineSegment(sketch, "E6918", {"start": v(355.99, 95.31) * mm, "end": v(355.95, 95.13) * mm});
            skLineSegment(sketch, "E6919", {"start": v(355.95, 95.13) * mm, "end": v(355.9, 94.95) * mm});
            skLineSegment(sketch, "E6920", {"start": v(355.9, 94.95) * mm, "end": v(355.81, 94.78) * mm});
            skLineSegment(sketch, "E6921", {"start": v(355.81, 94.78) * mm, "end": v(355.71, 94.62) * mm});
            skLineSegment(sketch, "E6922", {"start": v(355.71, 94.62) * mm, "end": v(355.6, 94.47) * mm});
            skLineSegment(sketch, "E6923", {"start": v(355.6, 94.47) * mm, "end": v(355.46, 94.34) * mm});
            skLineSegment(sketch, "E6924", {"start": v(355.46, 94.34) * mm, "end": v(355.3, 94.23) * mm});
            skLineSegment(sketch, "E6925", {"start": v(355.3, 94.23) * mm, "end": v(355.14, 94.14) * mm});
            skLineSegment(sketch, "E6926", {"start": v(355.14, 94.14) * mm, "end": v(354.96, 94.07) * mm});
            skLineSegment(sketch, "E6927", {"start": v(354.96, 94.07) * mm, "end": v(354.78, 94.03) * mm});
            skLineSegment(sketch, "E6928", {"start": v(354.78, 94.03) * mm, "end": v(354.6, 94) * mm});
            skLineSegment(sketch, "E6929", {"start": v(354.6, 94) * mm, "end": v(354.4, 94) * mm});
            skLineSegment(sketch, "E6930", {"start": v(24.4, 94) * mm, "end": v(24.22, 94.03) * mm});
            skLineSegment(sketch, "E6931", {"start": v(24.22, 94.03) * mm, "end": v(24.04, 94.07) * mm});
            skLineSegment(sketch, "E6932", {"start": v(24.04, 94.07) * mm, "end": v(23.86, 94.14) * mm});
            skLineSegment(sketch, "E6933", {"start": v(23.86, 94.14) * mm, "end": v(23.7, 94.23) * mm});
            skLineSegment(sketch, "E6934", {"start": v(23.7, 94.23) * mm, "end": v(23.54, 94.34) * mm});
            skLineSegment(sketch, "E6935", {"start": v(23.54, 94.34) * mm, "end": v(23.4, 94.47) * mm});
            skLineSegment(sketch, "E6936", {"start": v(23.4, 94.47) * mm, "end": v(23.29, 94.62) * mm});
            skLineSegment(sketch, "E6937", {"start": v(23.29, 94.62) * mm, "end": v(23.19, 94.78) * mm});
            skLineSegment(sketch, "E6938", {"start": v(23.19, 94.78) * mm, "end": v(23.1, 94.95) * mm});
            skLineSegment(sketch, "E6939", {"start": v(23.1, 94.95) * mm, "end": v(23.05, 95.13) * mm});
            skLineSegment(sketch, "E6940", {"start": v(23.05, 95.13) * mm, "end": v(23.01, 95.31) * mm});
            skLineSegment(sketch, "E6941", {"start": v(23.01, 95.31) * mm, "end": v(23, 95.5) * mm});
            skLineSegment(sketch, "E6942", {"start": v(23, 95.5) * mm, "end": v(23.01, 95.69) * mm});
            skLineSegment(sketch, "E6943", {"start": v(23.01, 95.69) * mm, "end": v(23.05, 95.87) * mm});
            skLineSegment(sketch, "E6944", {"start": v(23.05, 95.87) * mm, "end": v(23.1, 96.05) * mm});
            skLineSegment(sketch, "E6945", {"start": v(23.1, 96.05) * mm, "end": v(23.19, 96.22) * mm});
            skLineSegment(sketch, "E6946", {"start": v(23.19, 96.22) * mm, "end": v(23.29, 96.38) * mm});
            skLineSegment(sketch, "E6947", {"start": v(23.29, 96.38) * mm, "end": v(23.4, 96.53) * mm});
            skLineSegment(sketch, "E6948", {"start": v(23.4, 96.53) * mm, "end": v(23.54, 96.66) * mm});
            skLineSegment(sketch, "E6949", {"start": v(23.54, 96.66) * mm, "end": v(23.7, 96.77) * mm});
            skLineSegment(sketch, "E6950", {"start": v(23.7, 96.77) * mm, "end": v(23.86, 96.86) * mm});
            skLineSegment(sketch, "E6951", {"start": v(23.86, 96.86) * mm, "end": v(24.04, 96.93) * mm});
            skLineSegment(sketch, "E6952", {"start": v(24.04, 96.93) * mm, "end": v(24.22, 96.97) * mm});
            skLineSegment(sketch, "E6953", {"start": v(24.22, 96.97) * mm, "end": v(24.4, 97) * mm});
            skLineSegment(sketch, "E6954", {"start": v(24.4, 97) * mm, "end": v(24.6, 97) * mm});
            skLineSegment(sketch, "E6955", {"start": v(24.6, 97) * mm, "end": v(24.78, 96.97) * mm});
            skLineSegment(sketch, "E6956", {"start": v(24.78, 96.97) * mm, "end": v(24.96, 96.93) * mm});
            skLineSegment(sketch, "E6957", {"start": v(24.96, 96.93) * mm, "end": v(25.14, 96.86) * mm});
            skLineSegment(sketch, "E6958", {"start": v(25.14, 96.86) * mm, "end": v(25.3, 96.77) * mm});
            skLineSegment(sketch, "E6959", {"start": v(25.3, 96.77) * mm, "end": v(25.46, 96.66) * mm});
            skLineSegment(sketch, "E6960", {"start": v(25.46, 96.66) * mm, "end": v(25.6, 96.53) * mm});
            skLineSegment(sketch, "E6961", {"start": v(25.6, 96.53) * mm, "end": v(25.71, 96.38) * mm});
            skLineSegment(sketch, "E6962", {"start": v(25.71, 96.38) * mm, "end": v(25.81, 96.22) * mm});
            skLineSegment(sketch, "E6963", {"start": v(25.81, 96.22) * mm, "end": v(25.9, 96.05) * mm});
            skLineSegment(sketch, "E6964", {"start": v(25.9, 96.05) * mm, "end": v(25.95, 95.87) * mm});
            skLineSegment(sketch, "E6965", {"start": v(25.95, 95.87) * mm, "end": v(25.99, 95.69) * mm});
            skLineSegment(sketch, "E6966", {"start": v(25.99, 95.69) * mm, "end": v(26, 95.5) * mm});
            skLineSegment(sketch, "E6967", {"start": v(26, 95.5) * mm, "end": v(25.99, 95.31) * mm});
            skLineSegment(sketch, "E6968", {"start": v(25.99, 95.31) * mm, "end": v(25.95, 95.13) * mm});
            skLineSegment(sketch, "E6969", {"start": v(25.95, 95.13) * mm, "end": v(25.9, 94.95) * mm});
            skLineSegment(sketch, "E6970", {"start": v(25.9, 94.95) * mm, "end": v(25.81, 94.78) * mm});
            skLineSegment(sketch, "E6971", {"start": v(25.81, 94.78) * mm, "end": v(25.71, 94.62) * mm});
            skLineSegment(sketch, "E6972", {"start": v(25.71, 94.62) * mm, "end": v(25.6, 94.47) * mm});
            skLineSegment(sketch, "E6973", {"start": v(25.6, 94.47) * mm, "end": v(25.46, 94.34) * mm});
            skLineSegment(sketch, "E6974", {"start": v(25.46, 94.34) * mm, "end": v(25.3, 94.23) * mm});
            skLineSegment(sketch, "E6975", {"start": v(25.3, 94.23) * mm, "end": v(25.14, 94.14) * mm});
            skLineSegment(sketch, "E6976", {"start": v(25.14, 94.14) * mm, "end": v(24.96, 94.07) * mm});
            skLineSegment(sketch, "E6977", {"start": v(24.96, 94.07) * mm, "end": v(24.78, 94.03) * mm});
            skLineSegment(sketch, "E6978", {"start": v(24.78, 94.03) * mm, "end": v(24.6, 94) * mm});
            skLineSegment(sketch, "E6979", {"start": v(24.6, 94) * mm, "end": v(24.4, 94) * mm});
            skLineSegment(sketch, "E6980", {"start": v(385.4, 94) * mm, "end": v(385.22, 94.03) * mm});
            skLineSegment(sketch, "E6981", {"start": v(385.22, 94.03) * mm, "end": v(385.04, 94.07) * mm});
            skLineSegment(sketch, "E6982", {"start": v(385.04, 94.07) * mm, "end": v(384.86, 94.14) * mm});
            skLineSegment(sketch, "E6983", {"start": v(384.86, 94.14) * mm, "end": v(384.7, 94.23) * mm});
            skLineSegment(sketch, "E6984", {"start": v(384.7, 94.23) * mm, "end": v(384.54, 94.34) * mm});
            skLineSegment(sketch, "E6985", {"start": v(384.54, 94.34) * mm, "end": v(384.4, 94.47) * mm});
            skLineSegment(sketch, "E6986", {"start": v(384.4, 94.47) * mm, "end": v(384.29, 94.62) * mm});
            skLineSegment(sketch, "E6987", {"start": v(384.29, 94.62) * mm, "end": v(384.19, 94.78) * mm});
            skLineSegment(sketch, "E6988", {"start": v(384.19, 94.78) * mm, "end": v(384.1, 94.95) * mm});
            skLineSegment(sketch, "E6989", {"start": v(384.1, 94.95) * mm, "end": v(384.05, 95.13) * mm});
            skLineSegment(sketch, "E6990", {"start": v(384.05, 95.13) * mm, "end": v(384.01, 95.31) * mm});
            skLineSegment(sketch, "E6991", {"start": v(384.01, 95.31) * mm, "end": v(384, 95.5) * mm});
            skLineSegment(sketch, "E6992", {"start": v(384, 95.5) * mm, "end": v(384.01, 95.69) * mm});
            skLineSegment(sketch, "E6993", {"start": v(384.01, 95.69) * mm, "end": v(384.05, 95.87) * mm});
            skLineSegment(sketch, "E6994", {"start": v(384.05, 95.87) * mm, "end": v(384.1, 96.05) * mm});
            skLineSegment(sketch, "E6995", {"start": v(384.1, 96.05) * mm, "end": v(384.19, 96.22) * mm});
            skLineSegment(sketch, "E6996", {"start": v(384.19, 96.22) * mm, "end": v(384.29, 96.38) * mm});
            skLineSegment(sketch, "E6997", {"start": v(384.29, 96.38) * mm, "end": v(384.4, 96.53) * mm});
            skLineSegment(sketch, "E6998", {"start": v(384.4, 96.53) * mm, "end": v(384.54, 96.66) * mm});
            skLineSegment(sketch, "E6999", {"start": v(384.54, 96.66) * mm, "end": v(384.7, 96.77) * mm});
            skLineSegment(sketch, "E7000", {"start": v(384.7, 96.77) * mm, "end": v(384.86, 96.86) * mm});
            skLineSegment(sketch, "E7001", {"start": v(384.86, 96.86) * mm, "end": v(385.04, 96.93) * mm});
            skLineSegment(sketch, "E7002", {"start": v(385.04, 96.93) * mm, "end": v(385.22, 96.97) * mm});
            skLineSegment(sketch, "E7003", {"start": v(385.22, 96.97) * mm, "end": v(385.4, 97) * mm});
            skLineSegment(sketch, "E7004", {"start": v(385.4, 97) * mm, "end": v(385.6, 97) * mm});
            skLineSegment(sketch, "E7005", {"start": v(385.6, 97) * mm, "end": v(385.78, 96.97) * mm});
            skLineSegment(sketch, "E7006", {"start": v(385.78, 96.97) * mm, "end": v(385.96, 96.93) * mm});
            skLineSegment(sketch, "E7007", {"start": v(385.96, 96.93) * mm, "end": v(386.14, 96.86) * mm});
            skLineSegment(sketch, "E7008", {"start": v(386.14, 96.86) * mm, "end": v(386.3, 96.77) * mm});
            skLineSegment(sketch, "E7009", {"start": v(386.3, 96.77) * mm, "end": v(386.46, 96.66) * mm});
            skLineSegment(sketch, "E7010", {"start": v(386.46, 96.66) * mm, "end": v(386.6, 96.53) * mm});
            skLineSegment(sketch, "E7011", {"start": v(386.6, 96.53) * mm, "end": v(386.71, 96.38) * mm});
            skLineSegment(sketch, "E7012", {"start": v(386.71, 96.38) * mm, "end": v(386.81, 96.22) * mm});
            skLineSegment(sketch, "E7013", {"start": v(386.81, 96.22) * mm, "end": v(386.9, 96.05) * mm});
            skLineSegment(sketch, "E7014", {"start": v(386.9, 96.05) * mm, "end": v(386.95, 95.87) * mm});
            skLineSegment(sketch, "E7015", {"start": v(386.95, 95.87) * mm, "end": v(386.99, 95.69) * mm});
            skLineSegment(sketch, "E7016", {"start": v(386.99, 95.69) * mm, "end": v(387, 95.5) * mm});
            skLineSegment(sketch, "E7017", {"start": v(387, 95.5) * mm, "end": v(386.99, 95.31) * mm});
            skLineSegment(sketch, "E7018", {"start": v(386.99, 95.31) * mm, "end": v(386.95, 95.13) * mm});
            skLineSegment(sketch, "E7019", {"start": v(386.95, 95.13) * mm, "end": v(386.9, 94.95) * mm});
            skLineSegment(sketch, "E7020", {"start": v(386.9, 94.95) * mm, "end": v(386.81, 94.78) * mm});
            skLineSegment(sketch, "E7021", {"start": v(386.81, 94.78) * mm, "end": v(386.71, 94.62) * mm});
            skLineSegment(sketch, "E7022", {"start": v(386.71, 94.62) * mm, "end": v(386.6, 94.47) * mm});
            skLineSegment(sketch, "E7023", {"start": v(386.6, 94.47) * mm, "end": v(386.46, 94.34) * mm});
            skLineSegment(sketch, "E7024", {"start": v(386.46, 94.34) * mm, "end": v(386.3, 94.23) * mm});
            skLineSegment(sketch, "E7025", {"start": v(386.3, 94.23) * mm, "end": v(386.14, 94.14) * mm});
            skLineSegment(sketch, "E7026", {"start": v(386.14, 94.14) * mm, "end": v(385.96, 94.07) * mm});
            skLineSegment(sketch, "E7027", {"start": v(385.96, 94.07) * mm, "end": v(385.78, 94.03) * mm});
            skLineSegment(sketch, "E7028", {"start": v(385.78, 94.03) * mm, "end": v(385.6, 94) * mm});
            skLineSegment(sketch, "E7029", {"start": v(385.6, 94) * mm, "end": v(385.4, 94) * mm});
            skLineSegment(sketch, "E7030", {"start": v(39.25, 68.02) * mm, "end": v(37.75, 68.21) * mm});
            skLineSegment(sketch, "E7031", {"start": v(37.75, 68.21) * mm, "end": v(36.3, 68.59) * mm});
            skLineSegment(sketch, "E7032", {"start": v(36.3, 68.59) * mm, "end": v(34.9, 69.14) * mm});
            skLineSegment(sketch, "E7033", {"start": v(34.9, 69.14) * mm, "end": v(33.57, 69.87) * mm});
            skLineSegment(sketch, "E7034", {"start": v(33.57, 69.87) * mm, "end": v(32.35, 70.75) * mm});
            skLineSegment(sketch, "E7035", {"start": v(32.35, 70.75) * mm, "end": v(31.25, 71.78) * mm});
            skLineSegment(sketch, "E7036", {"start": v(31.25, 71.78) * mm, "end": v(30.3, 72.95) * mm});
            skLineSegment(sketch, "E7037", {"start": v(30.3, 72.95) * mm, "end": v(29.48, 74.22) * mm});
            skLineSegment(sketch, "E7038", {"start": v(29.48, 74.22) * mm, "end": v(28.84, 75.58) * mm});
            skLineSegment(sketch, "E7039", {"start": v(28.84, 75.58) * mm, "end": v(28.38, 77.02) * mm});
            skLineSegment(sketch, "E7040", {"start": v(28.38, 77.02) * mm, "end": v(28.1, 78.5) * mm});
            skLineSegment(sketch, "E7041", {"start": v(28.1, 78.5) * mm, "end": v(28, 80) * mm});
            skLineSegment(sketch, "E7042", {"start": v(28, 80) * mm, "end": v(28.1, 81.5) * mm});
            skLineSegment(sketch, "E7043", {"start": v(28.1, 81.5) * mm, "end": v(28.38, 82.98) * mm});
            skLineSegment(sketch, "E7044", {"start": v(28.38, 82.98) * mm, "end": v(28.84, 84.42) * mm});
            skLineSegment(sketch, "E7045", {"start": v(28.84, 84.42) * mm, "end": v(29.48, 85.78) * mm});
            skLineSegment(sketch, "E7046", {"start": v(29.48, 85.78) * mm, "end": v(30.3, 87.05) * mm});
            skLineSegment(sketch, "E7047", {"start": v(30.3, 87.05) * mm, "end": v(31.25, 88.22) * mm});
            skLineSegment(sketch, "E7048", {"start": v(31.25, 88.22) * mm, "end": v(32.35, 89.25) * mm});
            skLineSegment(sketch, "E7049", {"start": v(32.35, 89.25) * mm, "end": v(33.57, 90.13) * mm});
            skLineSegment(sketch, "E7050", {"start": v(33.57, 90.13) * mm, "end": v(34.9, 90.86) * mm});
            skLineSegment(sketch, "E7051", {"start": v(34.9, 90.86) * mm, "end": v(36.3, 91.41) * mm});
            skLineSegment(sketch, "E7052", {"start": v(36.3, 91.41) * mm, "end": v(37.75, 91.79) * mm});
            skLineSegment(sketch, "E7053", {"start": v(37.75, 91.79) * mm, "end": v(39.25, 91.98) * mm});
            skLineSegment(sketch, "E7054", {"start": v(39.25, 91.98) * mm, "end": v(40.75, 91.98) * mm});
            skLineSegment(sketch, "E7055", {"start": v(40.75, 91.98) * mm, "end": v(42.25, 91.79) * mm});
            skLineSegment(sketch, "E7056", {"start": v(42.25, 91.79) * mm, "end": v(43.7, 91.41) * mm});
            skLineSegment(sketch, "E7057", {"start": v(43.7, 91.41) * mm, "end": v(45.1, 90.86) * mm});
            skLineSegment(sketch, "E7058", {"start": v(45.1, 90.86) * mm, "end": v(46.43, 90.13) * mm});
            skLineSegment(sketch, "E7059", {"start": v(46.43, 90.13) * mm, "end": v(47.65, 89.25) * mm});
            skLineSegment(sketch, "E7060", {"start": v(47.65, 89.25) * mm, "end": v(48.75, 88.22) * mm});
            skLineSegment(sketch, "E7061", {"start": v(48.75, 88.22) * mm, "end": v(49.7, 87.05) * mm});
            skLineSegment(sketch, "E7062", {"start": v(49.7, 87.05) * mm, "end": v(50.52, 85.78) * mm});
            skLineSegment(sketch, "E7063", {"start": v(50.52, 85.78) * mm, "end": v(51.16, 84.42) * mm});
            skLineSegment(sketch, "E7064", {"start": v(51.16, 84.42) * mm, "end": v(51.62, 82.98) * mm});
            skLineSegment(sketch, "E7065", {"start": v(51.62, 82.98) * mm, "end": v(51.9, 81.5) * mm});
            skLineSegment(sketch, "E7066", {"start": v(51.9, 81.5) * mm, "end": v(52, 80) * mm});
            skLineSegment(sketch, "E7067", {"start": v(52, 80) * mm, "end": v(51.9, 78.5) * mm});
            skLineSegment(sketch, "E7068", {"start": v(51.9, 78.5) * mm, "end": v(51.62, 77.02) * mm});
            skLineSegment(sketch, "E7069", {"start": v(51.62, 77.02) * mm, "end": v(51.16, 75.58) * mm});
            skLineSegment(sketch, "E7070", {"start": v(51.16, 75.58) * mm, "end": v(50.52, 74.22) * mm});
            skLineSegment(sketch, "E7071", {"start": v(50.52, 74.22) * mm, "end": v(49.7, 72.95) * mm});
            skLineSegment(sketch, "E7072", {"start": v(49.7, 72.95) * mm, "end": v(48.75, 71.78) * mm});
            skLineSegment(sketch, "E7073", {"start": v(48.75, 71.78) * mm, "end": v(47.65, 70.75) * mm});
            skLineSegment(sketch, "E7074", {"start": v(47.65, 70.75) * mm, "end": v(46.43, 69.87) * mm});
            skLineSegment(sketch, "E7075", {"start": v(46.43, 69.87) * mm, "end": v(45.1, 69.14) * mm});
            skLineSegment(sketch, "E7076", {"start": v(45.1, 69.14) * mm, "end": v(43.7, 68.59) * mm});
            skLineSegment(sketch, "E7077", {"start": v(43.7, 68.59) * mm, "end": v(42.25, 68.21) * mm});
            skLineSegment(sketch, "E7078", {"start": v(42.25, 68.21) * mm, "end": v(40.75, 68.02) * mm});
            skLineSegment(sketch, "E7079", {"start": v(40.75, 68.02) * mm, "end": v(39.25, 68.02) * mm});
            skLineSegment(sketch, "E7080", {"start": v(369.25, 68.02) * mm, "end": v(367.75, 68.21) * mm});
            skLineSegment(sketch, "E7081", {"start": v(367.75, 68.21) * mm, "end": v(366.3, 68.59) * mm});
            skLineSegment(sketch, "E7082", {"start": v(366.3, 68.59) * mm, "end": v(364.9, 69.14) * mm});
            skLineSegment(sketch, "E7083", {"start": v(364.9, 69.14) * mm, "end": v(363.57, 69.87) * mm});
            skLineSegment(sketch, "E7084", {"start": v(363.57, 69.87) * mm, "end": v(362.35, 70.75) * mm});
            skLineSegment(sketch, "E7085", {"start": v(362.35, 70.75) * mm, "end": v(361.25, 71.78) * mm});
            skLineSegment(sketch, "E7086", {"start": v(361.25, 71.78) * mm, "end": v(360.3, 72.95) * mm});
            skLineSegment(sketch, "E7087", {"start": v(360.3, 72.95) * mm, "end": v(359.48, 74.22) * mm});
            skLineSegment(sketch, "E7088", {"start": v(359.48, 74.22) * mm, "end": v(358.84, 75.58) * mm});
            skLineSegment(sketch, "E7089", {"start": v(358.84, 75.58) * mm, "end": v(358.38, 77.02) * mm});
            skLineSegment(sketch, "E7090", {"start": v(358.38, 77.02) * mm, "end": v(358.1, 78.5) * mm});
            skLineSegment(sketch, "E7091", {"start": v(358.1, 78.5) * mm, "end": v(358, 80) * mm});
            skLineSegment(sketch, "E7092", {"start": v(358, 80) * mm, "end": v(358.1, 81.5) * mm});
            skLineSegment(sketch, "E7093", {"start": v(358.1, 81.5) * mm, "end": v(358.38, 82.98) * mm});
            skLineSegment(sketch, "E7094", {"start": v(358.38, 82.98) * mm, "end": v(358.84, 84.42) * mm});
            skLineSegment(sketch, "E7095", {"start": v(358.84, 84.42) * mm, "end": v(359.48, 85.78) * mm});
            skLineSegment(sketch, "E7096", {"start": v(359.48, 85.78) * mm, "end": v(360.3, 87.05) * mm});
            skLineSegment(sketch, "E7097", {"start": v(360.3, 87.05) * mm, "end": v(361.25, 88.22) * mm});
            skLineSegment(sketch, "E7098", {"start": v(361.25, 88.22) * mm, "end": v(362.35, 89.25) * mm});
            skLineSegment(sketch, "E7099", {"start": v(362.35, 89.25) * mm, "end": v(363.57, 90.13) * mm});
            skLineSegment(sketch, "E7100", {"start": v(363.57, 90.13) * mm, "end": v(364.9, 90.86) * mm});
            skLineSegment(sketch, "E7101", {"start": v(364.9, 90.86) * mm, "end": v(366.3, 91.41) * mm});
            skLineSegment(sketch, "E7102", {"start": v(366.3, 91.41) * mm, "end": v(367.75, 91.79) * mm});
            skLineSegment(sketch, "E7103", {"start": v(367.75, 91.79) * mm, "end": v(369.25, 91.98) * mm});
            skLineSegment(sketch, "E7104", {"start": v(369.25, 91.98) * mm, "end": v(370.75, 91.98) * mm});
            skLineSegment(sketch, "E7105", {"start": v(370.75, 91.98) * mm, "end": v(372.25, 91.79) * mm});
            skLineSegment(sketch, "E7106", {"start": v(372.25, 91.79) * mm, "end": v(373.7, 91.41) * mm});
            skLineSegment(sketch, "E7107", {"start": v(373.7, 91.41) * mm, "end": v(375.1, 90.86) * mm});
            skLineSegment(sketch, "E7108", {"start": v(375.1, 90.86) * mm, "end": v(376.43, 90.13) * mm});
            skLineSegment(sketch, "E7109", {"start": v(376.43, 90.13) * mm, "end": v(377.65, 89.25) * mm});
            skLineSegment(sketch, "E7110", {"start": v(377.65, 89.25) * mm, "end": v(378.75, 88.22) * mm});
            skLineSegment(sketch, "E7111", {"start": v(378.75, 88.22) * mm, "end": v(379.7, 87.05) * mm});
            skLineSegment(sketch, "E7112", {"start": v(379.7, 87.05) * mm, "end": v(380.52, 85.78) * mm});
            skLineSegment(sketch, "E7113", {"start": v(380.52, 85.78) * mm, "end": v(381.16, 84.42) * mm});
            skLineSegment(sketch, "E7114", {"start": v(381.16, 84.42) * mm, "end": v(381.62, 82.98) * mm});
            skLineSegment(sketch, "E7115", {"start": v(381.62, 82.98) * mm, "end": v(381.9, 81.5) * mm});
            skLineSegment(sketch, "E7116", {"start": v(381.9, 81.5) * mm, "end": v(382, 80) * mm});
            skLineSegment(sketch, "E7117", {"start": v(382, 80) * mm, "end": v(381.9, 78.5) * mm});
            skLineSegment(sketch, "E7118", {"start": v(381.9, 78.5) * mm, "end": v(381.62, 77.02) * mm});
            skLineSegment(sketch, "E7119", {"start": v(381.62, 77.02) * mm, "end": v(381.16, 75.58) * mm});
            skLineSegment(sketch, "E7120", {"start": v(381.16, 75.58) * mm, "end": v(380.52, 74.22) * mm});
            skLineSegment(sketch, "E7121", {"start": v(380.52, 74.22) * mm, "end": v(379.7, 72.95) * mm});
            skLineSegment(sketch, "E7122", {"start": v(379.7, 72.95) * mm, "end": v(378.75, 71.78) * mm});
            skLineSegment(sketch, "E7123", {"start": v(378.75, 71.78) * mm, "end": v(377.65, 70.75) * mm});
            skLineSegment(sketch, "E7124", {"start": v(377.65, 70.75) * mm, "end": v(376.43, 69.87) * mm});
            skLineSegment(sketch, "E7125", {"start": v(376.43, 69.87) * mm, "end": v(375.1, 69.14) * mm});
            skLineSegment(sketch, "E7126", {"start": v(375.1, 69.14) * mm, "end": v(373.7, 68.59) * mm});
            skLineSegment(sketch, "E7127", {"start": v(373.7, 68.59) * mm, "end": v(372.25, 68.21) * mm});
            skLineSegment(sketch, "E7128", {"start": v(372.25, 68.21) * mm, "end": v(370.75, 68.02) * mm});
            skLineSegment(sketch, "E7129", {"start": v(370.75, 68.02) * mm, "end": v(369.25, 68.02) * mm});
            skLineSegment(sketch, "E7130", {"start": v(22.75, 76) * mm, "end": v(22.25, 76.07) * mm});
            skLineSegment(sketch, "E7131", {"start": v(22.25, 76.07) * mm, "end": v(21.76, 76.2) * mm});
            skLineSegment(sketch, "E7132", {"start": v(21.76, 76.2) * mm, "end": v(21.3, 76.38) * mm});
            skLineSegment(sketch, "E7133", {"start": v(21.3, 76.38) * mm, "end": v(20.86, 76.62) * mm});
            skLineSegment(sketch, "E7134", {"start": v(20.86, 76.62) * mm, "end": v(20.45, 76.92) * mm});
            skLineSegment(sketch, "E7135", {"start": v(20.45, 76.92) * mm, "end": v(20.08, 77.26) * mm});
            skLineSegment(sketch, "E7136", {"start": v(20.08, 77.26) * mm, "end": v(19.76, 77.65) * mm});
            skLineSegment(sketch, "E7137", {"start": v(19.76, 77.65) * mm, "end": v(19.5, 78.07) * mm});
            skLineSegment(sketch, "E7138", {"start": v(19.5, 78.07) * mm, "end": v(19.28, 78.53) * mm});
            skLineSegment(sketch, "E7139", {"start": v(19.28, 78.53) * mm, "end": v(19.13, 79) * mm});
            skLineSegment(sketch, "E7140", {"start": v(19.13, 79) * mm, "end": v(19.03, 79.5) * mm});
            skLineSegment(sketch, "E7141", {"start": v(19.03, 79.5) * mm, "end": v(19, 80) * mm});
            skLineSegment(sketch, "E7142", {"start": v(19, 80) * mm, "end": v(19.03, 80.5) * mm});
            skLineSegment(sketch, "E7143", {"start": v(19.03, 80.5) * mm, "end": v(19.13, 81) * mm});
            skLineSegment(sketch, "E7144", {"start": v(19.13, 81) * mm, "end": v(19.28, 81.47) * mm});
            skLineSegment(sketch, "E7145", {"start": v(19.28, 81.47) * mm, "end": v(19.5, 81.93) * mm});
            skLineSegment(sketch, "E7146", {"start": v(19.5, 81.93) * mm, "end": v(19.76, 82.35) * mm});
            skLineSegment(sketch, "E7147", {"start": v(19.76, 82.35) * mm, "end": v(20.08, 82.74) * mm});
            skLineSegment(sketch, "E7148", {"start": v(20.08, 82.74) * mm, "end": v(20.45, 83.08) * mm});
            skLineSegment(sketch, "E7149", {"start": v(20.45, 83.08) * mm, "end": v(20.86, 83.38) * mm});
            skLineSegment(sketch, "E7150", {"start": v(20.86, 83.38) * mm, "end": v(21.3, 83.62) * mm});
            skLineSegment(sketch, "E7151", {"start": v(21.3, 83.62) * mm, "end": v(21.76, 83.8) * mm});
            skLineSegment(sketch, "E7152", {"start": v(21.76, 83.8) * mm, "end": v(22.25, 83.93) * mm});
            skLineSegment(sketch, "E7153", {"start": v(22.25, 83.93) * mm, "end": v(22.75, 84) * mm});
            skLineSegment(sketch, "E7154", {"start": v(22.75, 84) * mm, "end": v(23.25, 84) * mm});
            skLineSegment(sketch, "E7155", {"start": v(23.25, 84) * mm, "end": v(23.75, 83.93) * mm});
            skLineSegment(sketch, "E7156", {"start": v(23.75, 83.93) * mm, "end": v(24.24, 83.8) * mm});
            skLineSegment(sketch, "E7157", {"start": v(24.24, 83.8) * mm, "end": v(24.7, 83.62) * mm});
            skLineSegment(sketch, "E7158", {"start": v(24.7, 83.62) * mm, "end": v(25.14, 83.38) * mm});
            skLineSegment(sketch, "E7159", {"start": v(25.14, 83.38) * mm, "end": v(25.55, 83.08) * mm});
            skLineSegment(sketch, "E7160", {"start": v(25.55, 83.08) * mm, "end": v(25.92, 82.74) * mm});
            skLineSegment(sketch, "E7161", {"start": v(25.92, 82.74) * mm, "end": v(26.24, 82.35) * mm});
            skLineSegment(sketch, "E7162", {"start": v(26.24, 82.35) * mm, "end": v(26.5, 81.93) * mm});
            skLineSegment(sketch, "E7163", {"start": v(26.5, 81.93) * mm, "end": v(26.72, 81.47) * mm});
            skLineSegment(sketch, "E7164", {"start": v(26.72, 81.47) * mm, "end": v(26.87, 81) * mm});
            skLineSegment(sketch, "E7165", {"start": v(26.87, 81) * mm, "end": v(26.97, 80.5) * mm});
            skLineSegment(sketch, "E7166", {"start": v(26.97, 80.5) * mm, "end": v(27, 80) * mm});
            skLineSegment(sketch, "E7167", {"start": v(27, 80) * mm, "end": v(26.97, 79.5) * mm});
            skLineSegment(sketch, "E7168", {"start": v(26.97, 79.5) * mm, "end": v(26.87, 79) * mm});
            skLineSegment(sketch, "E7169", {"start": v(26.87, 79) * mm, "end": v(26.72, 78.53) * mm});
            skLineSegment(sketch, "E7170", {"start": v(26.72, 78.53) * mm, "end": v(26.5, 78.07) * mm});
            skLineSegment(sketch, "E7171", {"start": v(26.5, 78.07) * mm, "end": v(26.24, 77.65) * mm});
            skLineSegment(sketch, "E7172", {"start": v(26.24, 77.65) * mm, "end": v(25.92, 77.26) * mm});
            skLineSegment(sketch, "E7173", {"start": v(25.92, 77.26) * mm, "end": v(25.55, 76.92) * mm});
            skLineSegment(sketch, "E7174", {"start": v(25.55, 76.92) * mm, "end": v(25.14, 76.62) * mm});
            skLineSegment(sketch, "E7175", {"start": v(25.14, 76.62) * mm, "end": v(24.7, 76.38) * mm});
            skLineSegment(sketch, "E7176", {"start": v(24.7, 76.38) * mm, "end": v(24.24, 76.2) * mm});
            skLineSegment(sketch, "E7177", {"start": v(24.24, 76.2) * mm, "end": v(23.75, 76.07) * mm});
            skLineSegment(sketch, "E7178", {"start": v(23.75, 76.07) * mm, "end": v(23.25, 76) * mm});
            skLineSegment(sketch, "E7179", {"start": v(23.25, 76) * mm, "end": v(22.75, 76) * mm});
            skLineSegment(sketch, "E7180", {"start": v(386.75, 76) * mm, "end": v(386.25, 76.07) * mm});
            skLineSegment(sketch, "E7181", {"start": v(386.25, 76.07) * mm, "end": v(385.76, 76.2) * mm});
            skLineSegment(sketch, "E7182", {"start": v(385.76, 76.2) * mm, "end": v(385.3, 76.38) * mm});
            skLineSegment(sketch, "E7183", {"start": v(385.3, 76.38) * mm, "end": v(384.86, 76.62) * mm});
            skLineSegment(sketch, "E7184", {"start": v(384.86, 76.62) * mm, "end": v(384.45, 76.92) * mm});
            skLineSegment(sketch, "E7185", {"start": v(384.45, 76.92) * mm, "end": v(384.08, 77.26) * mm});
            skLineSegment(sketch, "E7186", {"start": v(384.08, 77.26) * mm, "end": v(383.76, 77.65) * mm});
            skLineSegment(sketch, "E7187", {"start": v(383.76, 77.65) * mm, "end": v(383.5, 78.07) * mm});
            skLineSegment(sketch, "E7188", {"start": v(383.5, 78.07) * mm, "end": v(383.28, 78.53) * mm});
            skLineSegment(sketch, "E7189", {"start": v(383.28, 78.53) * mm, "end": v(383.13, 79) * mm});
            skLineSegment(sketch, "E7190", {"start": v(383.13, 79) * mm, "end": v(383.03, 79.5) * mm});
            skLineSegment(sketch, "E7191", {"start": v(383.03, 79.5) * mm, "end": v(383, 80) * mm});
            skLineSegment(sketch, "E7192", {"start": v(383, 80) * mm, "end": v(383.03, 80.5) * mm});
            skLineSegment(sketch, "E7193", {"start": v(383.03, 80.5) * mm, "end": v(383.13, 81) * mm});
            skLineSegment(sketch, "E7194", {"start": v(383.13, 81) * mm, "end": v(383.28, 81.47) * mm});
            skLineSegment(sketch, "E7195", {"start": v(383.28, 81.47) * mm, "end": v(383.5, 81.93) * mm});
            skLineSegment(sketch, "E7196", {"start": v(383.5, 81.93) * mm, "end": v(383.76, 82.35) * mm});
            skLineSegment(sketch, "E7197", {"start": v(383.76, 82.35) * mm, "end": v(384.08, 82.74) * mm});
            skLineSegment(sketch, "E7198", {"start": v(384.08, 82.74) * mm, "end": v(384.45, 83.08) * mm});
            skLineSegment(sketch, "E7199", {"start": v(384.45, 83.08) * mm, "end": v(384.86, 83.38) * mm});
            skLineSegment(sketch, "E7200", {"start": v(384.86, 83.38) * mm, "end": v(385.3, 83.62) * mm});
            skLineSegment(sketch, "E7201", {"start": v(385.3, 83.62) * mm, "end": v(385.76, 83.8) * mm});
            skLineSegment(sketch, "E7202", {"start": v(385.76, 83.8) * mm, "end": v(386.25, 83.93) * mm});
            skLineSegment(sketch, "E7203", {"start": v(386.25, 83.93) * mm, "end": v(386.75, 84) * mm});
            skLineSegment(sketch, "E7204", {"start": v(386.75, 84) * mm, "end": v(387.25, 84) * mm});
            skLineSegment(sketch, "E7205", {"start": v(387.25, 84) * mm, "end": v(387.75, 83.93) * mm});
            skLineSegment(sketch, "E7206", {"start": v(387.75, 83.93) * mm, "end": v(388.24, 83.8) * mm});
            skLineSegment(sketch, "E7207", {"start": v(388.24, 83.8) * mm, "end": v(388.7, 83.62) * mm});
            skLineSegment(sketch, "E7208", {"start": v(388.7, 83.62) * mm, "end": v(389.14, 83.38) * mm});
            skLineSegment(sketch, "E7209", {"start": v(389.14, 83.38) * mm, "end": v(389.55, 83.08) * mm});
            skLineSegment(sketch, "E7210", {"start": v(389.55, 83.08) * mm, "end": v(389.92, 82.74) * mm});
            skLineSegment(sketch, "E7211", {"start": v(389.92, 82.74) * mm, "end": v(390.24, 82.35) * mm});
            skLineSegment(sketch, "E7212", {"start": v(390.24, 82.35) * mm, "end": v(390.5, 81.93) * mm});
            skLineSegment(sketch, "E7213", {"start": v(390.5, 81.93) * mm, "end": v(390.72, 81.47) * mm});
            skLineSegment(sketch, "E7214", {"start": v(390.72, 81.47) * mm, "end": v(390.87, 81) * mm});
            skLineSegment(sketch, "E7215", {"start": v(390.87, 81) * mm, "end": v(390.97, 80.5) * mm});
            skLineSegment(sketch, "E7216", {"start": v(390.97, 80.5) * mm, "end": v(391, 80) * mm});
            skLineSegment(sketch, "E7217", {"start": v(391, 80) * mm, "end": v(390.97, 79.5) * mm});
            skLineSegment(sketch, "E7218", {"start": v(390.97, 79.5) * mm, "end": v(390.87, 79) * mm});
            skLineSegment(sketch, "E7219", {"start": v(390.87, 79) * mm, "end": v(390.72, 78.53) * mm});
            skLineSegment(sketch, "E7220", {"start": v(390.72, 78.53) * mm, "end": v(390.5, 78.07) * mm});
            skLineSegment(sketch, "E7221", {"start": v(390.5, 78.07) * mm, "end": v(390.24, 77.65) * mm});
            skLineSegment(sketch, "E7222", {"start": v(390.24, 77.65) * mm, "end": v(389.92, 77.26) * mm});
            skLineSegment(sketch, "E7223", {"start": v(389.92, 77.26) * mm, "end": v(389.55, 76.92) * mm});
            skLineSegment(sketch, "E7224", {"start": v(389.55, 76.92) * mm, "end": v(389.14, 76.62) * mm});
            skLineSegment(sketch, "E7225", {"start": v(389.14, 76.62) * mm, "end": v(388.7, 76.38) * mm});
            skLineSegment(sketch, "E7226", {"start": v(388.7, 76.38) * mm, "end": v(388.24, 76.2) * mm});
            skLineSegment(sketch, "E7227", {"start": v(388.24, 76.2) * mm, "end": v(387.75, 76.07) * mm});
            skLineSegment(sketch, "E7228", {"start": v(387.75, 76.07) * mm, "end": v(387.25, 76) * mm});
            skLineSegment(sketch, "E7229", {"start": v(387.25, 76) * mm, "end": v(386.75, 76) * mm});
            skLineSegment(sketch, "E7230", {"start": v(385.4, 63) * mm, "end": v(385.22, 63.03) * mm});
            skLineSegment(sketch, "E7231", {"start": v(385.22, 63.03) * mm, "end": v(385.04, 63.07) * mm});
            skLineSegment(sketch, "E7232", {"start": v(385.04, 63.07) * mm, "end": v(384.86, 63.14) * mm});
            skLineSegment(sketch, "E7233", {"start": v(384.86, 63.14) * mm, "end": v(384.7, 63.23) * mm});
            skLineSegment(sketch, "E7234", {"start": v(384.7, 63.23) * mm, "end": v(384.54, 63.34) * mm});
            skLineSegment(sketch, "E7235", {"start": v(384.54, 63.34) * mm, "end": v(384.4, 63.47) * mm});
            skLineSegment(sketch, "E7236", {"start": v(384.4, 63.47) * mm, "end": v(384.29, 63.62) * mm});
            skLineSegment(sketch, "E7237", {"start": v(384.29, 63.62) * mm, "end": v(384.19, 63.78) * mm});
            skLineSegment(sketch, "E7238", {"start": v(384.19, 63.78) * mm, "end": v(384.1, 63.95) * mm});
            skLineSegment(sketch, "E7239", {"start": v(384.1, 63.95) * mm, "end": v(384.05, 64.13) * mm});
            skLineSegment(sketch, "E7240", {"start": v(384.05, 64.13) * mm, "end": v(384.01, 64.31) * mm});
            skLineSegment(sketch, "E7241", {"start": v(384.01, 64.31) * mm, "end": v(384, 64.5) * mm});
            skLineSegment(sketch, "E7242", {"start": v(384, 64.5) * mm, "end": v(384.01, 64.69) * mm});
            skLineSegment(sketch, "E7243", {"start": v(384.01, 64.69) * mm, "end": v(384.05, 64.87) * mm});
            skLineSegment(sketch, "E7244", {"start": v(384.05, 64.87) * mm, "end": v(384.1, 65.05) * mm});
            skLineSegment(sketch, "E7245", {"start": v(384.1, 65.05) * mm, "end": v(384.19, 65.22) * mm});
            skLineSegment(sketch, "E7246", {"start": v(384.19, 65.22) * mm, "end": v(384.29, 65.38) * mm});
            skLineSegment(sketch, "E7247", {"start": v(384.29, 65.38) * mm, "end": v(384.4, 65.53) * mm});
            skLineSegment(sketch, "E7248", {"start": v(384.4, 65.53) * mm, "end": v(384.54, 65.66) * mm});
            skLineSegment(sketch, "E7249", {"start": v(384.54, 65.66) * mm, "end": v(384.7, 65.77) * mm});
            skLineSegment(sketch, "E7250", {"start": v(384.7, 65.77) * mm, "end": v(384.86, 65.86) * mm});
            skLineSegment(sketch, "E7251", {"start": v(384.86, 65.86) * mm, "end": v(385.04, 65.93) * mm});
            skLineSegment(sketch, "E7252", {"start": v(385.04, 65.93) * mm, "end": v(385.22, 65.97) * mm});
            skLineSegment(sketch, "E7253", {"start": v(385.22, 65.97) * mm, "end": v(385.4, 66) * mm});
            skLineSegment(sketch, "E7254", {"start": v(385.4, 66) * mm, "end": v(385.6, 66) * mm});
            skLineSegment(sketch, "E7255", {"start": v(385.6, 66) * mm, "end": v(385.78, 65.97) * mm});
            skLineSegment(sketch, "E7256", {"start": v(385.78, 65.97) * mm, "end": v(385.96, 65.93) * mm});
            skLineSegment(sketch, "E7257", {"start": v(385.96, 65.93) * mm, "end": v(386.14, 65.86) * mm});
            skLineSegment(sketch, "E7258", {"start": v(386.14, 65.86) * mm, "end": v(386.3, 65.77) * mm});
            skLineSegment(sketch, "E7259", {"start": v(386.3, 65.77) * mm, "end": v(386.46, 65.66) * mm});
            skLineSegment(sketch, "E7260", {"start": v(386.46, 65.66) * mm, "end": v(386.6, 65.53) * mm});
            skLineSegment(sketch, "E7261", {"start": v(386.6, 65.53) * mm, "end": v(386.71, 65.38) * mm});
            skLineSegment(sketch, "E7262", {"start": v(386.71, 65.38) * mm, "end": v(386.81, 65.22) * mm});
            skLineSegment(sketch, "E7263", {"start": v(386.81, 65.22) * mm, "end": v(386.9, 65.05) * mm});
            skLineSegment(sketch, "E7264", {"start": v(386.9, 65.05) * mm, "end": v(386.95, 64.87) * mm});
            skLineSegment(sketch, "E7265", {"start": v(386.95, 64.87) * mm, "end": v(386.99, 64.69) * mm});
            skLineSegment(sketch, "E7266", {"start": v(386.99, 64.69) * mm, "end": v(387, 64.5) * mm});
            skLineSegment(sketch, "E7267", {"start": v(387, 64.5) * mm, "end": v(386.99, 64.31) * mm});
            skLineSegment(sketch, "E7268", {"start": v(386.99, 64.31) * mm, "end": v(386.95, 64.13) * mm});
            skLineSegment(sketch, "E7269", {"start": v(386.95, 64.13) * mm, "end": v(386.9, 63.95) * mm});
            skLineSegment(sketch, "E7270", {"start": v(386.9, 63.95) * mm, "end": v(386.81, 63.78) * mm});
            skLineSegment(sketch, "E7271", {"start": v(386.81, 63.78) * mm, "end": v(386.71, 63.62) * mm});
            skLineSegment(sketch, "E7272", {"start": v(386.71, 63.62) * mm, "end": v(386.6, 63.47) * mm});
            skLineSegment(sketch, "E7273", {"start": v(386.6, 63.47) * mm, "end": v(386.46, 63.34) * mm});
            skLineSegment(sketch, "E7274", {"start": v(386.46, 63.34) * mm, "end": v(386.3, 63.23) * mm});
            skLineSegment(sketch, "E7275", {"start": v(386.3, 63.23) * mm, "end": v(386.14, 63.14) * mm});
            skLineSegment(sketch, "E7276", {"start": v(386.14, 63.14) * mm, "end": v(385.96, 63.07) * mm});
            skLineSegment(sketch, "E7277", {"start": v(385.96, 63.07) * mm, "end": v(385.78, 63.03) * mm});
            skLineSegment(sketch, "E7278", {"start": v(385.78, 63.03) * mm, "end": v(385.6, 63) * mm});
            skLineSegment(sketch, "E7279", {"start": v(385.6, 63) * mm, "end": v(385.4, 63) * mm});
            skLineSegment(sketch, "E7280", {"start": v(354.4, 63) * mm, "end": v(354.22, 63.03) * mm});
            skLineSegment(sketch, "E7281", {"start": v(354.22, 63.03) * mm, "end": v(354.04, 63.07) * mm});
            skLineSegment(sketch, "E7282", {"start": v(354.04, 63.07) * mm, "end": v(353.86, 63.14) * mm});
            skLineSegment(sketch, "E7283", {"start": v(353.86, 63.14) * mm, "end": v(353.7, 63.23) * mm});
            skLineSegment(sketch, "E7284", {"start": v(353.7, 63.23) * mm, "end": v(353.54, 63.34) * mm});
            skLineSegment(sketch, "E7285", {"start": v(353.54, 63.34) * mm, "end": v(353.4, 63.47) * mm});
            skLineSegment(sketch, "E7286", {"start": v(353.4, 63.47) * mm, "end": v(353.29, 63.62) * mm});
            skLineSegment(sketch, "E7287", {"start": v(353.29, 63.62) * mm, "end": v(353.19, 63.78) * mm});
            skLineSegment(sketch, "E7288", {"start": v(353.19, 63.78) * mm, "end": v(353.1, 63.95) * mm});
            skLineSegment(sketch, "E7289", {"start": v(353.1, 63.95) * mm, "end": v(353.05, 64.13) * mm});
            skLineSegment(sketch, "E7290", {"start": v(353.05, 64.13) * mm, "end": v(353.01, 64.31) * mm});
            skLineSegment(sketch, "E7291", {"start": v(353.01, 64.31) * mm, "end": v(353, 64.5) * mm});
            skLineSegment(sketch, "E7292", {"start": v(353, 64.5) * mm, "end": v(353.01, 64.69) * mm});
            skLineSegment(sketch, "E7293", {"start": v(353.01, 64.69) * mm, "end": v(353.05, 64.87) * mm});
            skLineSegment(sketch, "E7294", {"start": v(353.05, 64.87) * mm, "end": v(353.1, 65.05) * mm});
            skLineSegment(sketch, "E7295", {"start": v(353.1, 65.05) * mm, "end": v(353.19, 65.22) * mm});
            skLineSegment(sketch, "E7296", {"start": v(353.19, 65.22) * mm, "end": v(353.29, 65.38) * mm});
            skLineSegment(sketch, "E7297", {"start": v(353.29, 65.38) * mm, "end": v(353.4, 65.53) * mm});
            skLineSegment(sketch, "E7298", {"start": v(353.4, 65.53) * mm, "end": v(353.54, 65.66) * mm});
            skLineSegment(sketch, "E7299", {"start": v(353.54, 65.66) * mm, "end": v(353.7, 65.77) * mm});
            skLineSegment(sketch, "E7300", {"start": v(353.7, 65.77) * mm, "end": v(353.86, 65.86) * mm});
            skLineSegment(sketch, "E7301", {"start": v(353.86, 65.86) * mm, "end": v(354.04, 65.93) * mm});
            skLineSegment(sketch, "E7302", {"start": v(354.04, 65.93) * mm, "end": v(354.22, 65.97) * mm});
            skLineSegment(sketch, "E7303", {"start": v(354.22, 65.97) * mm, "end": v(354.4, 66) * mm});
            skLineSegment(sketch, "E7304", {"start": v(354.4, 66) * mm, "end": v(354.6, 66) * mm});
            skLineSegment(sketch, "E7305", {"start": v(354.6, 66) * mm, "end": v(354.78, 65.97) * mm});
            skLineSegment(sketch, "E7306", {"start": v(354.78, 65.97) * mm, "end": v(354.96, 65.93) * mm});
            skLineSegment(sketch, "E7307", {"start": v(354.96, 65.93) * mm, "end": v(355.14, 65.86) * mm});
            skLineSegment(sketch, "E7308", {"start": v(355.14, 65.86) * mm, "end": v(355.3, 65.77) * mm});
            skLineSegment(sketch, "E7309", {"start": v(355.3, 65.77) * mm, "end": v(355.46, 65.66) * mm});
            skLineSegment(sketch, "E7310", {"start": v(355.46, 65.66) * mm, "end": v(355.6, 65.53) * mm});
            skLineSegment(sketch, "E7311", {"start": v(355.6, 65.53) * mm, "end": v(355.71, 65.38) * mm});
            skLineSegment(sketch, "E7312", {"start": v(355.71, 65.38) * mm, "end": v(355.81, 65.22) * mm});
            skLineSegment(sketch, "E7313", {"start": v(355.81, 65.22) * mm, "end": v(355.9, 65.05) * mm});
            skLineSegment(sketch, "E7314", {"start": v(355.9, 65.05) * mm, "end": v(355.95, 64.87) * mm});
            skLineSegment(sketch, "E7315", {"start": v(355.95, 64.87) * mm, "end": v(355.99, 64.69) * mm});
            skLineSegment(sketch, "E7316", {"start": v(355.99, 64.69) * mm, "end": v(356, 64.5) * mm});
            skLineSegment(sketch, "E7317", {"start": v(356, 64.5) * mm, "end": v(355.99, 64.31) * mm});
            skLineSegment(sketch, "E7318", {"start": v(355.99, 64.31) * mm, "end": v(355.95, 64.13) * mm});
            skLineSegment(sketch, "E7319", {"start": v(355.95, 64.13) * mm, "end": v(355.9, 63.95) * mm});
            skLineSegment(sketch, "E7320", {"start": v(355.9, 63.95) * mm, "end": v(355.81, 63.78) * mm});
            skLineSegment(sketch, "E7321", {"start": v(355.81, 63.78) * mm, "end": v(355.71, 63.62) * mm});
            skLineSegment(sketch, "E7322", {"start": v(355.71, 63.62) * mm, "end": v(355.6, 63.47) * mm});
            skLineSegment(sketch, "E7323", {"start": v(355.6, 63.47) * mm, "end": v(355.46, 63.34) * mm});
            skLineSegment(sketch, "E7324", {"start": v(355.46, 63.34) * mm, "end": v(355.3, 63.23) * mm});
            skLineSegment(sketch, "E7325", {"start": v(355.3, 63.23) * mm, "end": v(355.14, 63.14) * mm});
            skLineSegment(sketch, "E7326", {"start": v(355.14, 63.14) * mm, "end": v(354.96, 63.07) * mm});
            skLineSegment(sketch, "E7327", {"start": v(354.96, 63.07) * mm, "end": v(354.78, 63.03) * mm});
            skLineSegment(sketch, "E7328", {"start": v(354.78, 63.03) * mm, "end": v(354.6, 63) * mm});
            skLineSegment(sketch, "E7329", {"start": v(354.6, 63) * mm, "end": v(354.4, 63) * mm});
            skLineSegment(sketch, "E7330", {"start": v(55.4, 63) * mm, "end": v(55.22, 63.03) * mm});
            skLineSegment(sketch, "E7331", {"start": v(55.22, 63.03) * mm, "end": v(55.04, 63.07) * mm});
            skLineSegment(sketch, "E7332", {"start": v(55.04, 63.07) * mm, "end": v(54.86, 63.14) * mm});
            skLineSegment(sketch, "E7333", {"start": v(54.86, 63.14) * mm, "end": v(54.7, 63.23) * mm});
            skLineSegment(sketch, "E7334", {"start": v(54.7, 63.23) * mm, "end": v(54.54, 63.34) * mm});
            skLineSegment(sketch, "E7335", {"start": v(54.54, 63.34) * mm, "end": v(54.4, 63.47) * mm});
            skLineSegment(sketch, "E7336", {"start": v(54.4, 63.47) * mm, "end": v(54.29, 63.62) * mm});
            skLineSegment(sketch, "E7337", {"start": v(54.29, 63.62) * mm, "end": v(54.19, 63.78) * mm});
            skLineSegment(sketch, "E7338", {"start": v(54.19, 63.78) * mm, "end": v(54.1, 63.95) * mm});
            skLineSegment(sketch, "E7339", {"start": v(54.1, 63.95) * mm, "end": v(54.05, 64.13) * mm});
            skLineSegment(sketch, "E7340", {"start": v(54.05, 64.13) * mm, "end": v(54.01, 64.31) * mm});
            skLineSegment(sketch, "E7341", {"start": v(54.01, 64.31) * mm, "end": v(54, 64.5) * mm});
            skLineSegment(sketch, "E7342", {"start": v(54, 64.5) * mm, "end": v(54.01, 64.69) * mm});
            skLineSegment(sketch, "E7343", {"start": v(54.01, 64.69) * mm, "end": v(54.05, 64.87) * mm});
            skLineSegment(sketch, "E7344", {"start": v(54.05, 64.87) * mm, "end": v(54.1, 65.05) * mm});
            skLineSegment(sketch, "E7345", {"start": v(54.1, 65.05) * mm, "end": v(54.19, 65.22) * mm});
            skLineSegment(sketch, "E7346", {"start": v(54.19, 65.22) * mm, "end": v(54.29, 65.38) * mm});
            skLineSegment(sketch, "E7347", {"start": v(54.29, 65.38) * mm, "end": v(54.4, 65.53) * mm});
            skLineSegment(sketch, "E7348", {"start": v(54.4, 65.53) * mm, "end": v(54.54, 65.66) * mm});
            skLineSegment(sketch, "E7349", {"start": v(54.54, 65.66) * mm, "end": v(54.7, 65.77) * mm});
            skLineSegment(sketch, "E7350", {"start": v(54.7, 65.77) * mm, "end": v(54.86, 65.86) * mm});
            skLineSegment(sketch, "E7351", {"start": v(54.86, 65.86) * mm, "end": v(55.04, 65.93) * mm});
            skLineSegment(sketch, "E7352", {"start": v(55.04, 65.93) * mm, "end": v(55.22, 65.97) * mm});
            skLineSegment(sketch, "E7353", {"start": v(55.22, 65.97) * mm, "end": v(55.4, 66) * mm});
            skLineSegment(sketch, "E7354", {"start": v(55.4, 66) * mm, "end": v(55.6, 66) * mm});
            skLineSegment(sketch, "E7355", {"start": v(55.6, 66) * mm, "end": v(55.78, 65.97) * mm});
            skLineSegment(sketch, "E7356", {"start": v(55.78, 65.97) * mm, "end": v(55.96, 65.93) * mm});
            skLineSegment(sketch, "E7357", {"start": v(55.96, 65.93) * mm, "end": v(56.14, 65.86) * mm});
            skLineSegment(sketch, "E7358", {"start": v(56.14, 65.86) * mm, "end": v(56.3, 65.77) * mm});
            skLineSegment(sketch, "E7359", {"start": v(56.3, 65.77) * mm, "end": v(56.46, 65.66) * mm});
            skLineSegment(sketch, "E7360", {"start": v(56.46, 65.66) * mm, "end": v(56.6, 65.53) * mm});
            skLineSegment(sketch, "E7361", {"start": v(56.6, 65.53) * mm, "end": v(56.71, 65.38) * mm});
            skLineSegment(sketch, "E7362", {"start": v(56.71, 65.38) * mm, "end": v(56.81, 65.22) * mm});
            skLineSegment(sketch, "E7363", {"start": v(56.81, 65.22) * mm, "end": v(56.9, 65.05) * mm});
            skLineSegment(sketch, "E7364", {"start": v(56.9, 65.05) * mm, "end": v(56.95, 64.87) * mm});
            skLineSegment(sketch, "E7365", {"start": v(56.95, 64.87) * mm, "end": v(56.99, 64.69) * mm});
            skLineSegment(sketch, "E7366", {"start": v(56.99, 64.69) * mm, "end": v(57, 64.5) * mm});
            skLineSegment(sketch, "E7367", {"start": v(57, 64.5) * mm, "end": v(56.99, 64.31) * mm});
            skLineSegment(sketch, "E7368", {"start": v(56.99, 64.31) * mm, "end": v(56.95, 64.13) * mm});
            skLineSegment(sketch, "E7369", {"start": v(56.95, 64.13) * mm, "end": v(56.9, 63.95) * mm});
            skLineSegment(sketch, "E7370", {"start": v(56.9, 63.95) * mm, "end": v(56.81, 63.78) * mm});
            skLineSegment(sketch, "E7371", {"start": v(56.81, 63.78) * mm, "end": v(56.71, 63.62) * mm});
            skLineSegment(sketch, "E7372", {"start": v(56.71, 63.62) * mm, "end": v(56.6, 63.47) * mm});
            skLineSegment(sketch, "E7373", {"start": v(56.6, 63.47) * mm, "end": v(56.46, 63.34) * mm});
            skLineSegment(sketch, "E7374", {"start": v(56.46, 63.34) * mm, "end": v(56.3, 63.23) * mm});
            skLineSegment(sketch, "E7375", {"start": v(56.3, 63.23) * mm, "end": v(56.14, 63.14) * mm});
            skLineSegment(sketch, "E7376", {"start": v(56.14, 63.14) * mm, "end": v(55.96, 63.07) * mm});
            skLineSegment(sketch, "E7377", {"start": v(55.96, 63.07) * mm, "end": v(55.78, 63.03) * mm});
            skLineSegment(sketch, "E7378", {"start": v(55.78, 63.03) * mm, "end": v(55.6, 63) * mm});
            skLineSegment(sketch, "E7379", {"start": v(55.6, 63) * mm, "end": v(55.4, 63) * mm});
            skLineSegment(sketch, "E7380", {"start": v(24.4, 63) * mm, "end": v(24.22, 63.03) * mm});
            skLineSegment(sketch, "E7381", {"start": v(24.22, 63.03) * mm, "end": v(24.04, 63.07) * mm});
            skLineSegment(sketch, "E7382", {"start": v(24.04, 63.07) * mm, "end": v(23.86, 63.14) * mm});
            skLineSegment(sketch, "E7383", {"start": v(23.86, 63.14) * mm, "end": v(23.7, 63.23) * mm});
            skLineSegment(sketch, "E7384", {"start": v(23.7, 63.23) * mm, "end": v(23.54, 63.34) * mm});
            skLineSegment(sketch, "E7385", {"start": v(23.54, 63.34) * mm, "end": v(23.4, 63.47) * mm});
            skLineSegment(sketch, "E7386", {"start": v(23.4, 63.47) * mm, "end": v(23.29, 63.62) * mm});
            skLineSegment(sketch, "E7387", {"start": v(23.29, 63.62) * mm, "end": v(23.19, 63.78) * mm});
            skLineSegment(sketch, "E7388", {"start": v(23.19, 63.78) * mm, "end": v(23.1, 63.95) * mm});
            skLineSegment(sketch, "E7389", {"start": v(23.1, 63.95) * mm, "end": v(23.05, 64.13) * mm});
            skLineSegment(sketch, "E7390", {"start": v(23.05, 64.13) * mm, "end": v(23.01, 64.31) * mm});
            skLineSegment(sketch, "E7391", {"start": v(23.01, 64.31) * mm, "end": v(23, 64.5) * mm});
            skLineSegment(sketch, "E7392", {"start": v(23, 64.5) * mm, "end": v(23.01, 64.69) * mm});
            skLineSegment(sketch, "E7393", {"start": v(23.01, 64.69) * mm, "end": v(23.05, 64.87) * mm});
            skLineSegment(sketch, "E7394", {"start": v(23.05, 64.87) * mm, "end": v(23.1, 65.05) * mm});
            skLineSegment(sketch, "E7395", {"start": v(23.1, 65.05) * mm, "end": v(23.19, 65.22) * mm});
            skLineSegment(sketch, "E7396", {"start": v(23.19, 65.22) * mm, "end": v(23.29, 65.38) * mm});
            skLineSegment(sketch, "E7397", {"start": v(23.29, 65.38) * mm, "end": v(23.4, 65.53) * mm});
            skLineSegment(sketch, "E7398", {"start": v(23.4, 65.53) * mm, "end": v(23.54, 65.66) * mm});
            skLineSegment(sketch, "E7399", {"start": v(23.54, 65.66) * mm, "end": v(23.7, 65.77) * mm});
            skLineSegment(sketch, "E7400", {"start": v(23.7, 65.77) * mm, "end": v(23.86, 65.86) * mm});
            skLineSegment(sketch, "E7401", {"start": v(23.86, 65.86) * mm, "end": v(24.04, 65.93) * mm});
            skLineSegment(sketch, "E7402", {"start": v(24.04, 65.93) * mm, "end": v(24.22, 65.97) * mm});
            skLineSegment(sketch, "E7403", {"start": v(24.22, 65.97) * mm, "end": v(24.4, 66) * mm});
            skLineSegment(sketch, "E7404", {"start": v(24.4, 66) * mm, "end": v(24.6, 66) * mm});
            skLineSegment(sketch, "E7405", {"start": v(24.6, 66) * mm, "end": v(24.78, 65.97) * mm});
            skLineSegment(sketch, "E7406", {"start": v(24.78, 65.97) * mm, "end": v(24.96, 65.93) * mm});
            skLineSegment(sketch, "E7407", {"start": v(24.96, 65.93) * mm, "end": v(25.14, 65.86) * mm});
            skLineSegment(sketch, "E7408", {"start": v(25.14, 65.86) * mm, "end": v(25.3, 65.77) * mm});
            skLineSegment(sketch, "E7409", {"start": v(25.3, 65.77) * mm, "end": v(25.46, 65.66) * mm});
            skLineSegment(sketch, "E7410", {"start": v(25.46, 65.66) * mm, "end": v(25.6, 65.53) * mm});
            skLineSegment(sketch, "E7411", {"start": v(25.6, 65.53) * mm, "end": v(25.71, 65.38) * mm});
            skLineSegment(sketch, "E7412", {"start": v(25.71, 65.38) * mm, "end": v(25.81, 65.22) * mm});
            skLineSegment(sketch, "E7413", {"start": v(25.81, 65.22) * mm, "end": v(25.9, 65.05) * mm});
            skLineSegment(sketch, "E7414", {"start": v(25.9, 65.05) * mm, "end": v(25.95, 64.87) * mm});
            skLineSegment(sketch, "E7415", {"start": v(25.95, 64.87) * mm, "end": v(25.99, 64.69) * mm});
            skLineSegment(sketch, "E7416", {"start": v(25.99, 64.69) * mm, "end": v(26, 64.5) * mm});
            skLineSegment(sketch, "E7417", {"start": v(26, 64.5) * mm, "end": v(25.99, 64.31) * mm});
            skLineSegment(sketch, "E7418", {"start": v(25.99, 64.31) * mm, "end": v(25.95, 64.13) * mm});
            skLineSegment(sketch, "E7419", {"start": v(25.95, 64.13) * mm, "end": v(25.9, 63.95) * mm});
            skLineSegment(sketch, "E7420", {"start": v(25.9, 63.95) * mm, "end": v(25.81, 63.78) * mm});
            skLineSegment(sketch, "E7421", {"start": v(25.81, 63.78) * mm, "end": v(25.71, 63.62) * mm});
            skLineSegment(sketch, "E7422", {"start": v(25.71, 63.62) * mm, "end": v(25.6, 63.47) * mm});
            skLineSegment(sketch, "E7423", {"start": v(25.6, 63.47) * mm, "end": v(25.46, 63.34) * mm});
            skLineSegment(sketch, "E7424", {"start": v(25.46, 63.34) * mm, "end": v(25.3, 63.23) * mm});
            skLineSegment(sketch, "E7425", {"start": v(25.3, 63.23) * mm, "end": v(25.14, 63.14) * mm});
            skLineSegment(sketch, "E7426", {"start": v(25.14, 63.14) * mm, "end": v(24.96, 63.07) * mm});
            skLineSegment(sketch, "E7427", {"start": v(24.96, 63.07) * mm, "end": v(24.78, 63.03) * mm});
            skLineSegment(sketch, "E7428", {"start": v(24.78, 63.03) * mm, "end": v(24.6, 63) * mm});
            skLineSegment(sketch, "E7429", {"start": v(24.6, 63) * mm, "end": v(24.4, 63) * mm});
            skLineSegment(sketch, "E7430", {"start": v(267.9, -148.5) * mm, "end": v(267.72, -148.47) * mm});
            skLineSegment(sketch, "E7431", {"start": v(267.72, -148.47) * mm, "end": v(267.54, -148.43) * mm});
            skLineSegment(sketch, "E7432", {"start": v(267.54, -148.43) * mm, "end": v(267.36, -148.36) * mm});
            skLineSegment(sketch, "E7433", {"start": v(267.36, -148.36) * mm, "end": v(267.2, -148.27) * mm});
            skLineSegment(sketch, "E7434", {"start": v(267.2, -148.27) * mm, "end": v(267.04, -148.16) * mm});
            skLineSegment(sketch, "E7435", {"start": v(267.04, -148.16) * mm, "end": v(266.9, -148.03) * mm});
            skLineSegment(sketch, "E7436", {"start": v(266.9, -148.03) * mm, "end": v(266.79, -147.88) * mm});
            skLineSegment(sketch, "E7437", {"start": v(266.79, -147.88) * mm, "end": v(266.69, -147.72) * mm});
            skLineSegment(sketch, "E7438", {"start": v(266.69, -147.72) * mm, "end": v(266.6, -147.55) * mm});
            skLineSegment(sketch, "E7439", {"start": v(266.6, -147.55) * mm, "end": v(266.55, -147.37) * mm});
            skLineSegment(sketch, "E7440", {"start": v(266.55, -147.37) * mm, "end": v(266.51, -147.19) * mm});
            skLineSegment(sketch, "E7441", {"start": v(266.51, -147.19) * mm, "end": v(266.5, -147) * mm});
            skLineSegment(sketch, "E7442", {"start": v(266.5, -147) * mm, "end": v(266.51, -146.81) * mm});
            skLineSegment(sketch, "E7443", {"start": v(266.51, -146.81) * mm, "end": v(266.55, -146.63) * mm});
            skLineSegment(sketch, "E7444", {"start": v(266.55, -146.63) * mm, "end": v(266.6, -146.45) * mm});
            skLineSegment(sketch, "E7445", {"start": v(266.6, -146.45) * mm, "end": v(266.69, -146.28) * mm});
            skLineSegment(sketch, "E7446", {"start": v(266.69, -146.28) * mm, "end": v(266.79, -146.12) * mm});
            skLineSegment(sketch, "E7447", {"start": v(266.79, -146.12) * mm, "end": v(266.9, -145.97) * mm});
            skLineSegment(sketch, "E7448", {"start": v(266.9, -145.97) * mm, "end": v(267.04, -145.84) * mm});
            skLineSegment(sketch, "E7449", {"start": v(267.04, -145.84) * mm, "end": v(267.2, -145.73) * mm});
            skLineSegment(sketch, "E7450", {"start": v(267.2, -145.73) * mm, "end": v(267.36, -145.64) * mm});
            skLineSegment(sketch, "E7451", {"start": v(267.36, -145.64) * mm, "end": v(267.54, -145.57) * mm});
            skLineSegment(sketch, "E7452", {"start": v(267.54, -145.57) * mm, "end": v(267.72, -145.53) * mm});
            skLineSegment(sketch, "E7453", {"start": v(267.72, -145.53) * mm, "end": v(267.9, -145.5) * mm});
            skLineSegment(sketch, "E7454", {"start": v(267.9, -145.5) * mm, "end": v(268.1, -145.5) * mm});
            skLineSegment(sketch, "E7455", {"start": v(268.1, -145.5) * mm, "end": v(268.28, -145.53) * mm});
            skLineSegment(sketch, "E7456", {"start": v(268.28, -145.53) * mm, "end": v(268.46, -145.57) * mm});
            skLineSegment(sketch, "E7457", {"start": v(268.46, -145.57) * mm, "end": v(268.64, -145.64) * mm});
            skLineSegment(sketch, "E7458", {"start": v(268.64, -145.64) * mm, "end": v(268.8, -145.73) * mm});
            skLineSegment(sketch, "E7459", {"start": v(268.8, -145.73) * mm, "end": v(268.96, -145.84) * mm});
            skLineSegment(sketch, "E7460", {"start": v(268.96, -145.84) * mm, "end": v(269.1, -145.97) * mm});
            skLineSegment(sketch, "E7461", {"start": v(269.1, -145.97) * mm, "end": v(269.21, -146.12) * mm});
            skLineSegment(sketch, "E7462", {"start": v(269.21, -146.12) * mm, "end": v(269.31, -146.28) * mm});
            skLineSegment(sketch, "E7463", {"start": v(269.31, -146.28) * mm, "end": v(269.4, -146.45) * mm});
            skLineSegment(sketch, "E7464", {"start": v(269.4, -146.45) * mm, "end": v(269.45, -146.63) * mm});
            skLineSegment(sketch, "E7465", {"start": v(269.45, -146.63) * mm, "end": v(269.49, -146.81) * mm});
            skLineSegment(sketch, "E7466", {"start": v(269.49, -146.81) * mm, "end": v(269.5, -147) * mm});
            skLineSegment(sketch, "E7467", {"start": v(269.5, -147) * mm, "end": v(269.49, -147.19) * mm});
            skLineSegment(sketch, "E7468", {"start": v(269.49, -147.19) * mm, "end": v(269.45, -147.37) * mm});
            skLineSegment(sketch, "E7469", {"start": v(269.45, -147.37) * mm, "end": v(269.4, -147.55) * mm});
            skLineSegment(sketch, "E7470", {"start": v(269.4, -147.55) * mm, "end": v(269.31, -147.72) * mm});
            skLineSegment(sketch, "E7471", {"start": v(269.31, -147.72) * mm, "end": v(269.21, -147.88) * mm});
            skLineSegment(sketch, "E7472", {"start": v(269.21, -147.88) * mm, "end": v(269.1, -148.03) * mm});
            skLineSegment(sketch, "E7473", {"start": v(269.1, -148.03) * mm, "end": v(268.96, -148.16) * mm});
            skLineSegment(sketch, "E7474", {"start": v(268.96, -148.16) * mm, "end": v(268.8, -148.27) * mm});
            skLineSegment(sketch, "E7475", {"start": v(268.8, -148.27) * mm, "end": v(268.64, -148.36) * mm});
            skLineSegment(sketch, "E7476", {"start": v(268.64, -148.36) * mm, "end": v(268.46, -148.43) * mm});
            skLineSegment(sketch, "E7477", {"start": v(268.46, -148.43) * mm, "end": v(268.28, -148.47) * mm});
            skLineSegment(sketch, "E7478", {"start": v(268.28, -148.47) * mm, "end": v(268.1, -148.5) * mm});
            skLineSegment(sketch, "E7479", {"start": v(268.1, -148.5) * mm, "end": v(267.9, -148.5) * mm});
            skLineSegment(sketch, "E7480", {"start": v(251.9, -148.5) * mm, "end": v(251.72, -148.47) * mm});
            skLineSegment(sketch, "E7481", {"start": v(251.72, -148.47) * mm, "end": v(251.54, -148.43) * mm});
            skLineSegment(sketch, "E7482", {"start": v(251.54, -148.43) * mm, "end": v(251.36, -148.36) * mm});
            skLineSegment(sketch, "E7483", {"start": v(251.36, -148.36) * mm, "end": v(251.2, -148.27) * mm});
            skLineSegment(sketch, "E7484", {"start": v(251.2, -148.27) * mm, "end": v(251.04, -148.16) * mm});
            skLineSegment(sketch, "E7485", {"start": v(251.04, -148.16) * mm, "end": v(250.9, -148.03) * mm});
            skLineSegment(sketch, "E7486", {"start": v(250.9, -148.03) * mm, "end": v(250.79, -147.88) * mm});
            skLineSegment(sketch, "E7487", {"start": v(250.79, -147.88) * mm, "end": v(250.69, -147.72) * mm});
            skLineSegment(sketch, "E7488", {"start": v(250.69, -147.72) * mm, "end": v(250.6, -147.55) * mm});
            skLineSegment(sketch, "E7489", {"start": v(250.6, -147.55) * mm, "end": v(250.55, -147.37) * mm});
            skLineSegment(sketch, "E7490", {"start": v(250.55, -147.37) * mm, "end": v(250.51, -147.19) * mm});
            skLineSegment(sketch, "E7491", {"start": v(250.51, -147.19) * mm, "end": v(250.5, -147) * mm});
            skLineSegment(sketch, "E7492", {"start": v(250.5, -147) * mm, "end": v(250.51, -146.81) * mm});
            skLineSegment(sketch, "E7493", {"start": v(250.51, -146.81) * mm, "end": v(250.55, -146.63) * mm});
            skLineSegment(sketch, "E7494", {"start": v(250.55, -146.63) * mm, "end": v(250.6, -146.45) * mm});
            skLineSegment(sketch, "E7495", {"start": v(250.6, -146.45) * mm, "end": v(250.69, -146.28) * mm});
            skLineSegment(sketch, "E7496", {"start": v(250.69, -146.28) * mm, "end": v(250.79, -146.12) * mm});
            skLineSegment(sketch, "E7497", {"start": v(250.79, -146.12) * mm, "end": v(250.9, -145.97) * mm});
            skLineSegment(sketch, "E7498", {"start": v(250.9, -145.97) * mm, "end": v(251.04, -145.84) * mm});
            skLineSegment(sketch, "E7499", {"start": v(251.04, -145.84) * mm, "end": v(251.2, -145.73) * mm});
            skLineSegment(sketch, "E7500", {"start": v(251.2, -145.73) * mm, "end": v(251.36, -145.64) * mm});
            skLineSegment(sketch, "E7501", {"start": v(251.36, -145.64) * mm, "end": v(251.54, -145.57) * mm});
            skLineSegment(sketch, "E7502", {"start": v(251.54, -145.57) * mm, "end": v(251.72, -145.53) * mm});
            skLineSegment(sketch, "E7503", {"start": v(251.72, -145.53) * mm, "end": v(251.9, -145.5) * mm});
            skLineSegment(sketch, "E7504", {"start": v(251.9, -145.5) * mm, "end": v(252.1, -145.5) * mm});
            skLineSegment(sketch, "E7505", {"start": v(252.1, -145.5) * mm, "end": v(252.28, -145.53) * mm});
            skLineSegment(sketch, "E7506", {"start": v(252.28, -145.53) * mm, "end": v(252.46, -145.57) * mm});
            skLineSegment(sketch, "E7507", {"start": v(252.46, -145.57) * mm, "end": v(252.64, -145.64) * mm});
            skLineSegment(sketch, "E7508", {"start": v(252.64, -145.64) * mm, "end": v(252.8, -145.73) * mm});
            skLineSegment(sketch, "E7509", {"start": v(252.8, -145.73) * mm, "end": v(252.96, -145.84) * mm});
            skLineSegment(sketch, "E7510", {"start": v(252.96, -145.84) * mm, "end": v(253.1, -145.97) * mm});
            skLineSegment(sketch, "E7511", {"start": v(253.1, -145.97) * mm, "end": v(253.21, -146.12) * mm});
            skLineSegment(sketch, "E7512", {"start": v(253.21, -146.12) * mm, "end": v(253.31, -146.28) * mm});
            skLineSegment(sketch, "E7513", {"start": v(253.31, -146.28) * mm, "end": v(253.4, -146.45) * mm});
            skLineSegment(sketch, "E7514", {"start": v(253.4, -146.45) * mm, "end": v(253.45, -146.63) * mm});
            skLineSegment(sketch, "E7515", {"start": v(253.45, -146.63) * mm, "end": v(253.49, -146.81) * mm});
            skLineSegment(sketch, "E7516", {"start": v(253.49, -146.81) * mm, "end": v(253.5, -147) * mm});
            skLineSegment(sketch, "E7517", {"start": v(253.5, -147) * mm, "end": v(253.49, -147.19) * mm});
            skLineSegment(sketch, "E7518", {"start": v(253.49, -147.19) * mm, "end": v(253.45, -147.37) * mm});
            skLineSegment(sketch, "E7519", {"start": v(253.45, -147.37) * mm, "end": v(253.4, -147.55) * mm});
            skLineSegment(sketch, "E7520", {"start": v(253.4, -147.55) * mm, "end": v(253.31, -147.72) * mm});
            skLineSegment(sketch, "E7521", {"start": v(253.31, -147.72) * mm, "end": v(253.21, -147.88) * mm});
            skLineSegment(sketch, "E7522", {"start": v(253.21, -147.88) * mm, "end": v(253.1, -148.03) * mm});
            skLineSegment(sketch, "E7523", {"start": v(253.1, -148.03) * mm, "end": v(252.96, -148.16) * mm});
            skLineSegment(sketch, "E7524", {"start": v(252.96, -148.16) * mm, "end": v(252.8, -148.27) * mm});
            skLineSegment(sketch, "E7525", {"start": v(252.8, -148.27) * mm, "end": v(252.64, -148.36) * mm});
            skLineSegment(sketch, "E7526", {"start": v(252.64, -148.36) * mm, "end": v(252.46, -148.43) * mm});
            skLineSegment(sketch, "E7527", {"start": v(252.46, -148.43) * mm, "end": v(252.28, -148.47) * mm});
            skLineSegment(sketch, "E7528", {"start": v(252.28, -148.47) * mm, "end": v(252.1, -148.5) * mm});
            skLineSegment(sketch, "E7529", {"start": v(252.1, -148.5) * mm, "end": v(251.9, -148.5) * mm});
            skLineSegment(sketch, "E7530", {"start": v(157.9, -148.5) * mm, "end": v(157.72, -148.47) * mm});
            skLineSegment(sketch, "E7531", {"start": v(157.72, -148.47) * mm, "end": v(157.54, -148.43) * mm});
            skLineSegment(sketch, "E7532", {"start": v(157.54, -148.43) * mm, "end": v(157.36, -148.36) * mm});
            skLineSegment(sketch, "E7533", {"start": v(157.36, -148.36) * mm, "end": v(157.2, -148.27) * mm});
            skLineSegment(sketch, "E7534", {"start": v(157.2, -148.27) * mm, "end": v(157.04, -148.16) * mm});
            skLineSegment(sketch, "E7535", {"start": v(157.04, -148.16) * mm, "end": v(156.9, -148.03) * mm});
            skLineSegment(sketch, "E7536", {"start": v(156.9, -148.03) * mm, "end": v(156.79, -147.88) * mm});
            skLineSegment(sketch, "E7537", {"start": v(156.79, -147.88) * mm, "end": v(156.69, -147.72) * mm});
            skLineSegment(sketch, "E7538", {"start": v(156.69, -147.72) * mm, "end": v(156.6, -147.55) * mm});
            skLineSegment(sketch, "E7539", {"start": v(156.6, -147.55) * mm, "end": v(156.55, -147.37) * mm});
            skLineSegment(sketch, "E7540", {"start": v(156.55, -147.37) * mm, "end": v(156.51, -147.19) * mm});
            skLineSegment(sketch, "E7541", {"start": v(156.51, -147.19) * mm, "end": v(156.5, -147) * mm});
            skLineSegment(sketch, "E7542", {"start": v(156.5, -147) * mm, "end": v(156.51, -146.81) * mm});
            skLineSegment(sketch, "E7543", {"start": v(156.51, -146.81) * mm, "end": v(156.55, -146.63) * mm});
            skLineSegment(sketch, "E7544", {"start": v(156.55, -146.63) * mm, "end": v(156.6, -146.45) * mm});
            skLineSegment(sketch, "E7545", {"start": v(156.6, -146.45) * mm, "end": v(156.69, -146.28) * mm});
            skLineSegment(sketch, "E7546", {"start": v(156.69, -146.28) * mm, "end": v(156.79, -146.12) * mm});
            skLineSegment(sketch, "E7547", {"start": v(156.79, -146.12) * mm, "end": v(156.9, -145.97) * mm});
            skLineSegment(sketch, "E7548", {"start": v(156.9, -145.97) * mm, "end": v(157.04, -145.84) * mm});
            skLineSegment(sketch, "E7549", {"start": v(157.04, -145.84) * mm, "end": v(157.2, -145.73) * mm});
            skLineSegment(sketch, "E7550", {"start": v(157.2, -145.73) * mm, "end": v(157.36, -145.64) * mm});
            skLineSegment(sketch, "E7551", {"start": v(157.36, -145.64) * mm, "end": v(157.54, -145.57) * mm});
            skLineSegment(sketch, "E7552", {"start": v(157.54, -145.57) * mm, "end": v(157.72, -145.53) * mm});
            skLineSegment(sketch, "E7553", {"start": v(157.72, -145.53) * mm, "end": v(157.9, -145.5) * mm});
            skLineSegment(sketch, "E7554", {"start": v(157.9, -145.5) * mm, "end": v(158.1, -145.5) * mm});
            skLineSegment(sketch, "E7555", {"start": v(158.1, -145.5) * mm, "end": v(158.28, -145.53) * mm});
            skLineSegment(sketch, "E7556", {"start": v(158.28, -145.53) * mm, "end": v(158.46, -145.57) * mm});
            skLineSegment(sketch, "E7557", {"start": v(158.46, -145.57) * mm, "end": v(158.64, -145.64) * mm});
            skLineSegment(sketch, "E7558", {"start": v(158.64, -145.64) * mm, "end": v(158.8, -145.73) * mm});
            skLineSegment(sketch, "E7559", {"start": v(158.8, -145.73) * mm, "end": v(158.96, -145.84) * mm});
            skLineSegment(sketch, "E7560", {"start": v(158.96, -145.84) * mm, "end": v(159.1, -145.97) * mm});
            skLineSegment(sketch, "E7561", {"start": v(159.1, -145.97) * mm, "end": v(159.21, -146.12) * mm});
            skLineSegment(sketch, "E7562", {"start": v(159.21, -146.12) * mm, "end": v(159.31, -146.28) * mm});
            skLineSegment(sketch, "E7563", {"start": v(159.31, -146.28) * mm, "end": v(159.4, -146.45) * mm});
            skLineSegment(sketch, "E7564", {"start": v(159.4, -146.45) * mm, "end": v(159.45, -146.63) * mm});
            skLineSegment(sketch, "E7565", {"start": v(159.45, -146.63) * mm, "end": v(159.49, -146.81) * mm});
            skLineSegment(sketch, "E7566", {"start": v(159.49, -146.81) * mm, "end": v(159.5, -147) * mm});
            skLineSegment(sketch, "E7567", {"start": v(159.5, -147) * mm, "end": v(159.49, -147.19) * mm});
            skLineSegment(sketch, "E7568", {"start": v(159.49, -147.19) * mm, "end": v(159.45, -147.37) * mm});
            skLineSegment(sketch, "E7569", {"start": v(159.45, -147.37) * mm, "end": v(159.4, -147.55) * mm});
            skLineSegment(sketch, "E7570", {"start": v(159.4, -147.55) * mm, "end": v(159.31, -147.72) * mm});
            skLineSegment(sketch, "E7571", {"start": v(159.31, -147.72) * mm, "end": v(159.21, -147.88) * mm});
            skLineSegment(sketch, "E7572", {"start": v(159.21, -147.88) * mm, "end": v(159.1, -148.03) * mm});
            skLineSegment(sketch, "E7573", {"start": v(159.1, -148.03) * mm, "end": v(158.96, -148.16) * mm});
            skLineSegment(sketch, "E7574", {"start": v(158.96, -148.16) * mm, "end": v(158.8, -148.27) * mm});
            skLineSegment(sketch, "E7575", {"start": v(158.8, -148.27) * mm, "end": v(158.64, -148.36) * mm});
            skLineSegment(sketch, "E7576", {"start": v(158.64, -148.36) * mm, "end": v(158.46, -148.43) * mm});
            skLineSegment(sketch, "E7577", {"start": v(158.46, -148.43) * mm, "end": v(158.28, -148.47) * mm});
            skLineSegment(sketch, "E7578", {"start": v(158.28, -148.47) * mm, "end": v(158.1, -148.5) * mm});
            skLineSegment(sketch, "E7579", {"start": v(158.1, -148.5) * mm, "end": v(157.9, -148.5) * mm});
            skLineSegment(sketch, "E7580", {"start": v(141.9, -148.5) * mm, "end": v(141.72, -148.47) * mm});
            skLineSegment(sketch, "E7581", {"start": v(141.72, -148.47) * mm, "end": v(141.54, -148.43) * mm});
            skLineSegment(sketch, "E7582", {"start": v(141.54, -148.43) * mm, "end": v(141.36, -148.36) * mm});
            skLineSegment(sketch, "E7583", {"start": v(141.36, -148.36) * mm, "end": v(141.2, -148.27) * mm});
            skLineSegment(sketch, "E7584", {"start": v(141.2, -148.27) * mm, "end": v(141.04, -148.16) * mm});
            skLineSegment(sketch, "E7585", {"start": v(141.04, -148.16) * mm, "end": v(140.9, -148.03) * mm});
            skLineSegment(sketch, "E7586", {"start": v(140.9, -148.03) * mm, "end": v(140.79, -147.88) * mm});
            skLineSegment(sketch, "E7587", {"start": v(140.79, -147.88) * mm, "end": v(140.69, -147.72) * mm});
            skLineSegment(sketch, "E7588", {"start": v(140.69, -147.72) * mm, "end": v(140.6, -147.55) * mm});
            skLineSegment(sketch, "E7589", {"start": v(140.6, -147.55) * mm, "end": v(140.55, -147.37) * mm});
            skLineSegment(sketch, "E7590", {"start": v(140.55, -147.37) * mm, "end": v(140.51, -147.19) * mm});
            skLineSegment(sketch, "E7591", {"start": v(140.51, -147.19) * mm, "end": v(140.5, -147) * mm});
            skLineSegment(sketch, "E7592", {"start": v(140.5, -147) * mm, "end": v(140.51, -146.81) * mm});
            skLineSegment(sketch, "E7593", {"start": v(140.51, -146.81) * mm, "end": v(140.55, -146.63) * mm});
            skLineSegment(sketch, "E7594", {"start": v(140.55, -146.63) * mm, "end": v(140.6, -146.45) * mm});
            skLineSegment(sketch, "E7595", {"start": v(140.6, -146.45) * mm, "end": v(140.69, -146.28) * mm});
            skLineSegment(sketch, "E7596", {"start": v(140.69, -146.28) * mm, "end": v(140.79, -146.12) * mm});
            skLineSegment(sketch, "E7597", {"start": v(140.79, -146.12) * mm, "end": v(140.9, -145.97) * mm});
            skLineSegment(sketch, "E7598", {"start": v(140.9, -145.97) * mm, "end": v(141.04, -145.84) * mm});
            skLineSegment(sketch, "E7599", {"start": v(141.04, -145.84) * mm, "end": v(141.2, -145.73) * mm});
            skLineSegment(sketch, "E7600", {"start": v(141.2, -145.73) * mm, "end": v(141.36, -145.64) * mm});
            skLineSegment(sketch, "E7601", {"start": v(141.36, -145.64) * mm, "end": v(141.54, -145.57) * mm});
            skLineSegment(sketch, "E7602", {"start": v(141.54, -145.57) * mm, "end": v(141.72, -145.53) * mm});
            skLineSegment(sketch, "E7603", {"start": v(141.72, -145.53) * mm, "end": v(141.9, -145.5) * mm});
            skLineSegment(sketch, "E7604", {"start": v(141.9, -145.5) * mm, "end": v(142.1, -145.5) * mm});
            skLineSegment(sketch, "E7605", {"start": v(142.1, -145.5) * mm, "end": v(142.28, -145.53) * mm});
            skLineSegment(sketch, "E7606", {"start": v(142.28, -145.53) * mm, "end": v(142.46, -145.57) * mm});
            skLineSegment(sketch, "E7607", {"start": v(142.46, -145.57) * mm, "end": v(142.64, -145.64) * mm});
            skLineSegment(sketch, "E7608", {"start": v(142.64, -145.64) * mm, "end": v(142.8, -145.73) * mm});
            skLineSegment(sketch, "E7609", {"start": v(142.8, -145.73) * mm, "end": v(142.96, -145.84) * mm});
            skLineSegment(sketch, "E7610", {"start": v(142.96, -145.84) * mm, "end": v(143.1, -145.97) * mm});
            skLineSegment(sketch, "E7611", {"start": v(143.1, -145.97) * mm, "end": v(143.21, -146.12) * mm});
            skLineSegment(sketch, "E7612", {"start": v(143.21, -146.12) * mm, "end": v(143.31, -146.28) * mm});
            skLineSegment(sketch, "E7613", {"start": v(143.31, -146.28) * mm, "end": v(143.4, -146.45) * mm});
            skLineSegment(sketch, "E7614", {"start": v(143.4, -146.45) * mm, "end": v(143.45, -146.63) * mm});
            skLineSegment(sketch, "E7615", {"start": v(143.45, -146.63) * mm, "end": v(143.49, -146.81) * mm});
            skLineSegment(sketch, "E7616", {"start": v(143.49, -146.81) * mm, "end": v(143.5, -147) * mm});
            skLineSegment(sketch, "E7617", {"start": v(143.5, -147) * mm, "end": v(143.49, -147.19) * mm});
            skLineSegment(sketch, "E7618", {"start": v(143.49, -147.19) * mm, "end": v(143.45, -147.37) * mm});
            skLineSegment(sketch, "E7619", {"start": v(143.45, -147.37) * mm, "end": v(143.4, -147.55) * mm});
            skLineSegment(sketch, "E7620", {"start": v(143.4, -147.55) * mm, "end": v(143.31, -147.72) * mm});
            skLineSegment(sketch, "E7621", {"start": v(143.31, -147.72) * mm, "end": v(143.21, -147.88) * mm});
            skLineSegment(sketch, "E7622", {"start": v(143.21, -147.88) * mm, "end": v(143.1, -148.03) * mm});
            skLineSegment(sketch, "E7623", {"start": v(143.1, -148.03) * mm, "end": v(142.96, -148.16) * mm});
            skLineSegment(sketch, "E7624", {"start": v(142.96, -148.16) * mm, "end": v(142.8, -148.27) * mm});
            skLineSegment(sketch, "E7625", {"start": v(142.8, -148.27) * mm, "end": v(142.64, -148.36) * mm});
            skLineSegment(sketch, "E7626", {"start": v(142.64, -148.36) * mm, "end": v(142.46, -148.43) * mm});
            skLineSegment(sketch, "E7627", {"start": v(142.46, -148.43) * mm, "end": v(142.28, -148.47) * mm});
            skLineSegment(sketch, "E7628", {"start": v(142.28, -148.47) * mm, "end": v(142.1, -148.5) * mm});
            skLineSegment(sketch, "E7629", {"start": v(142.1, -148.5) * mm, "end": v(141.9, -148.5) * mm});
            skLineSegment(sketch, "E7630", {"start": v(340, -166.5) * mm, "end": v(340, -150.5) * mm});
            skLineSegment(sketch, "E7631", {"start": v(340, -150.5) * mm, "end": v(360, -150.5) * mm});
            skLineSegment(sketch, "E7632", {"start": v(360, -150.5) * mm, "end": v(360, -166.5) * mm});
            skLineSegment(sketch, "E7633", {"start": v(360, -166.5) * mm, "end": v(340, -166.5) * mm});
            skLineSegment(sketch, "E7634", {"start": v(195, -166.5) * mm, "end": v(195, -150.5) * mm});
            skLineSegment(sketch, "E7635", {"start": v(195, -150.5) * mm, "end": v(215, -150.5) * mm});
            skLineSegment(sketch, "E7636", {"start": v(215, -150.5) * mm, "end": v(215, -166.5) * mm});
            skLineSegment(sketch, "E7637", {"start": v(215, -166.5) * mm, "end": v(195, -166.5) * mm});
            skLineSegment(sketch, "E7638", {"start": v(50, -166.5) * mm, "end": v(50, -150.5) * mm});
            skLineSegment(sketch, "E7639", {"start": v(50, -150.5) * mm, "end": v(70, -150.5) * mm});
            skLineSegment(sketch, "E7640", {"start": v(70, -150.5) * mm, "end": v(70, -166.5) * mm});
            skLineSegment(sketch, "E7641", {"start": v(70, -166.5) * mm, "end": v(50, -166.5) * mm});
            skLineSegment(sketch, "E7642", {"start": v(287.37, -160.5) * mm, "end": v(287.12, -160.47) * mm});
            skLineSegment(sketch, "E7643", {"start": v(287.12, -160.47) * mm, "end": v(286.88, -160.4) * mm});
            skLineSegment(sketch, "E7644", {"start": v(286.88, -160.4) * mm, "end": v(286.65, -160.3) * mm});
            skLineSegment(sketch, "E7645", {"start": v(286.65, -160.3) * mm, "end": v(286.43, -160.19) * mm});
            skLineSegment(sketch, "E7646", {"start": v(286.43, -160.19) * mm, "end": v(286.23, -160.04) * mm});
            skLineSegment(sketch, "E7647", {"start": v(286.23, -160.04) * mm, "end": v(286.04, -159.87) * mm});
            skLineSegment(sketch, "E7648", {"start": v(286.04, -159.87) * mm, "end": v(285.88, -159.68) * mm});
            skLineSegment(sketch, "E7649", {"start": v(285.88, -159.68) * mm, "end": v(285.75, -159.46) * mm});
            skLineSegment(sketch, "E7650", {"start": v(285.75, -159.46) * mm, "end": v(285.64, -159.24) * mm});
            skLineSegment(sketch, "E7651", {"start": v(285.64, -159.24) * mm, "end": v(285.56, -159) * mm});
            skLineSegment(sketch, "E7652", {"start": v(285.56, -159) * mm, "end": v(285.52, -158.75) * mm});
            skLineSegment(sketch, "E7653", {"start": v(285.52, -158.75) * mm, "end": v(285.5, -158.5) * mm});
            skLineSegment(sketch, "E7654", {"start": v(285.5, -158.5) * mm, "end": v(285.52, -158.25) * mm});
            skLineSegment(sketch, "E7655", {"start": v(285.52, -158.25) * mm, "end": v(285.56, -158) * mm});
            skLineSegment(sketch, "E7656", {"start": v(285.56, -158) * mm, "end": v(285.64, -157.76) * mm});
            skLineSegment(sketch, "E7657", {"start": v(285.64, -157.76) * mm, "end": v(285.75, -157.54) * mm});
            skLineSegment(sketch, "E7658", {"start": v(285.75, -157.54) * mm, "end": v(285.88, -157.32) * mm});
            skLineSegment(sketch, "E7659", {"start": v(285.88, -157.32) * mm, "end": v(286.04, -157.13) * mm});
            skLineSegment(sketch, "E7660", {"start": v(286.04, -157.13) * mm, "end": v(286.23, -156.96) * mm});
            skLineSegment(sketch, "E7661", {"start": v(286.23, -156.96) * mm, "end": v(286.43, -156.81) * mm});
            skLineSegment(sketch, "E7662", {"start": v(286.43, -156.81) * mm, "end": v(286.65, -156.7) * mm});
            skLineSegment(sketch, "E7663", {"start": v(286.65, -156.7) * mm, "end": v(286.88, -156.6) * mm});
            skLineSegment(sketch, "E7664", {"start": v(286.88, -156.6) * mm, "end": v(287.12, -156.53) * mm});
            skLineSegment(sketch, "E7665", {"start": v(287.12, -156.53) * mm, "end": v(287.37, -156.5) * mm});
            skLineSegment(sketch, "E7666", {"start": v(287.37, -156.5) * mm, "end": v(287.63, -156.5) * mm});
            skLineSegment(sketch, "E7667", {"start": v(287.63, -156.5) * mm, "end": v(287.88, -156.53) * mm});
            skLineSegment(sketch, "E7668", {"start": v(287.88, -156.53) * mm, "end": v(288.12, -156.6) * mm});
            skLineSegment(sketch, "E7669", {"start": v(288.12, -156.6) * mm, "end": v(288.35, -156.7) * mm});
            skLineSegment(sketch, "E7670", {"start": v(288.35, -156.7) * mm, "end": v(288.57, -156.81) * mm});
            skLineSegment(sketch, "E7671", {"start": v(288.57, -156.81) * mm, "end": v(288.77, -156.96) * mm});
            skLineSegment(sketch, "E7672", {"start": v(288.77, -156.96) * mm, "end": v(288.96, -157.13) * mm});
            skLineSegment(sketch, "E7673", {"start": v(288.96, -157.13) * mm, "end": v(289.12, -157.32) * mm});
            skLineSegment(sketch, "E7674", {"start": v(289.12, -157.32) * mm, "end": v(289.25, -157.54) * mm});
            skLineSegment(sketch, "E7675", {"start": v(289.25, -157.54) * mm, "end": v(289.36, -157.76) * mm});
            skLineSegment(sketch, "E7676", {"start": v(289.36, -157.76) * mm, "end": v(289.44, -158) * mm});
            skLineSegment(sketch, "E7677", {"start": v(289.44, -158) * mm, "end": v(289.48, -158.25) * mm});
            skLineSegment(sketch, "E7678", {"start": v(289.48, -158.25) * mm, "end": v(289.5, -158.5) * mm});
            skLineSegment(sketch, "E7679", {"start": v(289.5, -158.5) * mm, "end": v(289.48, -158.75) * mm});
            skLineSegment(sketch, "E7680", {"start": v(289.48, -158.75) * mm, "end": v(289.44, -159) * mm});
            skLineSegment(sketch, "E7681", {"start": v(289.44, -159) * mm, "end": v(289.36, -159.24) * mm});
            skLineSegment(sketch, "E7682", {"start": v(289.36, -159.24) * mm, "end": v(289.25, -159.46) * mm});
            skLineSegment(sketch, "E7683", {"start": v(289.25, -159.46) * mm, "end": v(289.12, -159.68) * mm});
            skLineSegment(sketch, "E7684", {"start": v(289.12, -159.68) * mm, "end": v(288.96, -159.87) * mm});
            skLineSegment(sketch, "E7685", {"start": v(288.96, -159.87) * mm, "end": v(288.77, -160.04) * mm});
            skLineSegment(sketch, "E7686", {"start": v(288.77, -160.04) * mm, "end": v(288.57, -160.19) * mm});
            skLineSegment(sketch, "E7687", {"start": v(288.57, -160.19) * mm, "end": v(288.35, -160.3) * mm});
            skLineSegment(sketch, "E7688", {"start": v(288.35, -160.3) * mm, "end": v(288.12, -160.4) * mm});
            skLineSegment(sketch, "E7689", {"start": v(288.12, -160.4) * mm, "end": v(287.88, -160.47) * mm});
            skLineSegment(sketch, "E7690", {"start": v(287.88, -160.47) * mm, "end": v(287.63, -160.5) * mm});
            skLineSegment(sketch, "E7691", {"start": v(287.63, -160.5) * mm, "end": v(287.37, -160.5) * mm});
            skLineSegment(sketch, "E7692", {"start": v(122.37, -160.5) * mm, "end": v(122.12, -160.47) * mm});
            skLineSegment(sketch, "E7693", {"start": v(122.12, -160.47) * mm, "end": v(121.88, -160.4) * mm});
            skLineSegment(sketch, "E7694", {"start": v(121.88, -160.4) * mm, "end": v(121.65, -160.3) * mm});
            skLineSegment(sketch, "E7695", {"start": v(121.65, -160.3) * mm, "end": v(121.43, -160.19) * mm});
            skLineSegment(sketch, "E7696", {"start": v(121.43, -160.19) * mm, "end": v(121.22, -160.04) * mm});
            skLineSegment(sketch, "E7697", {"start": v(121.22, -160.04) * mm, "end": v(121.04, -159.87) * mm});
            skLineSegment(sketch, "E7698", {"start": v(121.04, -159.87) * mm, "end": v(120.88, -159.68) * mm});
            skLineSegment(sketch, "E7699", {"start": v(120.88, -159.68) * mm, "end": v(120.75, -159.46) * mm});
            skLineSegment(sketch, "E7700", {"start": v(120.75, -159.46) * mm, "end": v(120.64, -159.24) * mm});
            skLineSegment(sketch, "E7701", {"start": v(120.64, -159.24) * mm, "end": v(120.56, -159) * mm});
            skLineSegment(sketch, "E7702", {"start": v(120.56, -159) * mm, "end": v(120.52, -158.75) * mm});
            skLineSegment(sketch, "E7703", {"start": v(120.52, -158.75) * mm, "end": v(120.5, -158.5) * mm});
            skLineSegment(sketch, "E7704", {"start": v(120.5, -158.5) * mm, "end": v(120.52, -158.25) * mm});
            skLineSegment(sketch, "E7705", {"start": v(120.52, -158.25) * mm, "end": v(120.56, -158) * mm});
            skLineSegment(sketch, "E7706", {"start": v(120.56, -158) * mm, "end": v(120.64, -157.76) * mm});
            skLineSegment(sketch, "E7707", {"start": v(120.64, -157.76) * mm, "end": v(120.75, -157.54) * mm});
            skLineSegment(sketch, "E7708", {"start": v(120.75, -157.54) * mm, "end": v(120.88, -157.32) * mm});
            skLineSegment(sketch, "E7709", {"start": v(120.88, -157.32) * mm, "end": v(121.04, -157.13) * mm});
            skLineSegment(sketch, "E7710", {"start": v(121.04, -157.13) * mm, "end": v(121.22, -156.96) * mm});
            skLineSegment(sketch, "E7711", {"start": v(121.22, -156.96) * mm, "end": v(121.43, -156.81) * mm});
            skLineSegment(sketch, "E7712", {"start": v(121.43, -156.81) * mm, "end": v(121.65, -156.7) * mm});
            skLineSegment(sketch, "E7713", {"start": v(121.65, -156.7) * mm, "end": v(121.88, -156.6) * mm});
            skLineSegment(sketch, "E7714", {"start": v(121.88, -156.6) * mm, "end": v(122.12, -156.53) * mm});
            skLineSegment(sketch, "E7715", {"start": v(122.12, -156.53) * mm, "end": v(122.37, -156.5) * mm});
            skLineSegment(sketch, "E7716", {"start": v(122.37, -156.5) * mm, "end": v(122.63, -156.5) * mm});
            skLineSegment(sketch, "E7717", {"start": v(122.63, -156.5) * mm, "end": v(122.88, -156.53) * mm});
            skLineSegment(sketch, "E7718", {"start": v(122.88, -156.53) * mm, "end": v(123.12, -156.6) * mm});
            skLineSegment(sketch, "E7719", {"start": v(123.12, -156.6) * mm, "end": v(123.35, -156.7) * mm});
            skLineSegment(sketch, "E7720", {"start": v(123.35, -156.7) * mm, "end": v(123.57, -156.81) * mm});
            skLineSegment(sketch, "E7721", {"start": v(123.57, -156.81) * mm, "end": v(123.78, -156.96) * mm});
            skLineSegment(sketch, "E7722", {"start": v(123.78, -156.96) * mm, "end": v(123.96, -157.13) * mm});
            skLineSegment(sketch, "E7723", {"start": v(123.96, -157.13) * mm, "end": v(124.12, -157.32) * mm});
            skLineSegment(sketch, "E7724", {"start": v(124.12, -157.32) * mm, "end": v(124.25, -157.54) * mm});
            skLineSegment(sketch, "E7725", {"start": v(124.25, -157.54) * mm, "end": v(124.36, -157.76) * mm});
            skLineSegment(sketch, "E7726", {"start": v(124.36, -157.76) * mm, "end": v(124.44, -158) * mm});
            skLineSegment(sketch, "E7727", {"start": v(124.44, -158) * mm, "end": v(124.48, -158.25) * mm});
            skLineSegment(sketch, "E7728", {"start": v(124.48, -158.25) * mm, "end": v(124.5, -158.5) * mm});
            skLineSegment(sketch, "E7729", {"start": v(124.5, -158.5) * mm, "end": v(124.48, -158.75) * mm});
            skLineSegment(sketch, "E7730", {"start": v(124.48, -158.75) * mm, "end": v(124.44, -159) * mm});
            skLineSegment(sketch, "E7731", {"start": v(124.44, -159) * mm, "end": v(124.36, -159.24) * mm});
            skLineSegment(sketch, "E7732", {"start": v(124.36, -159.24) * mm, "end": v(124.25, -159.46) * mm});
            skLineSegment(sketch, "E7733", {"start": v(124.25, -159.46) * mm, "end": v(124.12, -159.68) * mm});
            skLineSegment(sketch, "E7734", {"start": v(124.12, -159.68) * mm, "end": v(123.96, -159.87) * mm});
            skLineSegment(sketch, "E7735", {"start": v(123.96, -159.87) * mm, "end": v(123.78, -160.04) * mm});
            skLineSegment(sketch, "E7736", {"start": v(123.78, -160.04) * mm, "end": v(123.57, -160.19) * mm});
            skLineSegment(sketch, "E7737", {"start": v(123.57, -160.19) * mm, "end": v(123.35, -160.3) * mm});
            skLineSegment(sketch, "E7738", {"start": v(123.35, -160.3) * mm, "end": v(123.12, -160.4) * mm});
            skLineSegment(sketch, "E7739", {"start": v(123.12, -160.4) * mm, "end": v(122.88, -160.47) * mm});
            skLineSegment(sketch, "E7740", {"start": v(122.88, -160.47) * mm, "end": v(122.63, -160.5) * mm});
            skLineSegment(sketch, "E7741", {"start": v(122.63, -160.5) * mm, "end": v(122.37, -160.5) * mm});
            skLineSegment(sketch, "E7742", {"start": v(-368.75, -176.92) * mm, "end": v(-367.51, -176.69) * mm});
            skLineSegment(sketch, "E7743", {"start": v(-367.51, -176.69) * mm, "end": v(-366.32, -176.3) * mm});
            skLineSegment(sketch, "E7744", {"start": v(-366.32, -176.3) * mm, "end": v(-365.18, -175.76) * mm});
            skLineSegment(sketch, "E7745", {"start": v(-365.18, -175.76) * mm, "end": v(-364.12, -175.1) * mm});
            skLineSegment(sketch, "E7746", {"start": v(-364.12, -175.1) * mm, "end": v(-363.16, -174.29) * mm});
            skLineSegment(sketch, "E7747", {"start": v(-363.16, -174.29) * mm, "end": v(-362.3, -173.37) * mm});
            skLineSegment(sketch, "E7748", {"start": v(-362.3, -173.37) * mm, "end": v(-361.56, -172.36) * mm});
            skLineSegment(sketch, "E7749", {"start": v(-361.56, -172.36) * mm, "end": v(-360.95, -171.26) * mm});
            skLineSegment(sketch, "E7750", {"start": v(-360.95, -171.26) * mm, "end": v(-360.49, -170.1) * mm});
            skLineSegment(sketch, "E7751", {"start": v(-360.49, -170.1) * mm, "end": v(-360.18, -168.87) * mm});
            skLineSegment(sketch, "E7752", {"start": v(-360.18, -168.87) * mm, "end": v(-360.02, -167.63) * mm});
            skLineSegment(sketch, "E7753", {"start": v(-360.02, -167.63) * mm, "end": v(-360.02, -167) * mm});
            skLineSegment(sketch, "E7754", {"start": v(-360.02, -167) * mm, "end": v(-360, -167) * mm});
            skLineSegment(sketch, "E7755", {"start": v(-360, -167) * mm, "end": v(-360, -117) * mm});
            skLineSegment(sketch, "E7756", {"start": v(-360, -117) * mm, "end": v(-340, -117) * mm});
            skLineSegment(sketch, "E7757", {"start": v(-340, -117) * mm, "end": v(-340, 193) * mm});
            skLineSegment(sketch, "E7758", {"start": v(-340, 193) * mm, "end": v(-339.98, 193) * mm});
            skLineSegment(sketch, "E7759", {"start": v(-339.98, 193) * mm, "end": v(-339.98, 193.63) * mm});
            skLineSegment(sketch, "E7760", {"start": v(-339.98, 193.63) * mm, "end": v(-339.82, 194.87) * mm});
            skLineSegment(sketch, "E7761", {"start": v(-339.82, 194.87) * mm, "end": v(-339.51, 196.1) * mm});
            skLineSegment(sketch, "E7762", {"start": v(-339.51, 196.1) * mm, "end": v(-339.05, 197.26) * mm});
            skLineSegment(sketch, "E7763", {"start": v(-339.05, 197.26) * mm, "end": v(-338.44, 198.36) * mm});
            skLineSegment(sketch, "E7764", {"start": v(-338.44, 198.36) * mm, "end": v(-337.7, 199.37) * mm});
            skLineSegment(sketch, "E7765", {"start": v(-337.7, 199.37) * mm, "end": v(-336.85, 200.29) * mm});
            skLineSegment(sketch, "E7766", {"start": v(-336.85, 200.29) * mm, "end": v(-335.88, 201.1) * mm});
            skLineSegment(sketch, "E7767", {"start": v(-335.88, 201.1) * mm, "end": v(-334.82, 201.76) * mm});
            skLineSegment(sketch, "E7768", {"start": v(-334.82, 201.76) * mm, "end": v(-333.68, 202.3) * mm});
            skLineSegment(sketch, "E7769", {"start": v(-333.68, 202.3) * mm, "end": v(-332.49, 202.69) * mm});
            skLineSegment(sketch, "E7770", {"start": v(-332.49, 202.69) * mm, "end": v(-331.25, 202.92) * mm});
            skLineSegment(sketch, "E7771", {"start": v(-331.25, 202.92) * mm, "end": v(-330, 203) * mm});
            skLineSegment(sketch, "E7772", {"start": v(-330, 203) * mm, "end": v(-80, 203) * mm});
            skLineSegment(sketch, "E7773", {"start": v(-80, 203) * mm, "end": v(-80, 202.98) * mm});
            skLineSegment(sketch, "E7774", {"start": v(-80, 202.98) * mm, "end": v(-79.37, 202.98) * mm});
            skLineSegment(sketch, "E7775", {"start": v(-79.37, 202.98) * mm, "end": v(-78.13, 202.82) * mm});
            skLineSegment(sketch, "E7776", {"start": v(-78.13, 202.82) * mm, "end": v(-76.9, 202.51) * mm});
            skLineSegment(sketch, "E7777", {"start": v(-76.9, 202.51) * mm, "end": v(-75.74, 202.05) * mm});
            skLineSegment(sketch, "E7778", {"start": v(-75.74, 202.05) * mm, "end": v(-74.64, 201.44) * mm});
            skLineSegment(sketch, "E7779", {"start": v(-74.64, 201.44) * mm, "end": v(-73.63, 200.7) * mm});
            skLineSegment(sketch, "E7780", {"start": v(-73.63, 200.7) * mm, "end": v(-72.71, 199.84) * mm});
            skLineSegment(sketch, "E7781", {"start": v(-72.71, 199.84) * mm, "end": v(-71.9, 198.88) * mm});
            skLineSegment(sketch, "E7782", {"start": v(-71.9, 198.88) * mm, "end": v(-71.24, 197.82) * mm});
            skLineSegment(sketch, "E7783", {"start": v(-71.24, 197.82) * mm, "end": v(-70.7, 196.68) * mm});
            skLineSegment(sketch, "E7784", {"start": v(-70.7, 196.68) * mm, "end": v(-70.31, 195.49) * mm});
            skLineSegment(sketch, "E7785", {"start": v(-70.31, 195.49) * mm, "end": v(-70.08, 194.25) * mm});
            skLineSegment(sketch, "E7786", {"start": v(-70.08, 194.25) * mm, "end": v(-70, 193) * mm});
            skLineSegment(sketch, "E7787", {"start": v(-70, 193) * mm, "end": v(-70, -117) * mm});
            skLineSegment(sketch, "E7788", {"start": v(-70, -117) * mm, "end": v(-50, -117) * mm});
            skLineSegment(sketch, "E7789", {"start": v(-50, -117) * mm, "end": v(-50, -167) * mm});
            skLineSegment(sketch, "E7790", {"start": v(-50, -167) * mm, "end": v(-49.92, -168.25) * mm});
            skLineSegment(sketch, "E7791", {"start": v(-49.92, -168.25) * mm, "end": v(-49.69, -169.49) * mm});
            skLineSegment(sketch, "E7792", {"start": v(-49.69, -169.49) * mm, "end": v(-49.3, -170.68) * mm});
            skLineSegment(sketch, "E7793", {"start": v(-49.3, -170.68) * mm, "end": v(-48.76, -171.82) * mm});
            skLineSegment(sketch, "E7794", {"start": v(-48.76, -171.82) * mm, "end": v(-48.1, -172.88) * mm});
            skLineSegment(sketch, "E7795", {"start": v(-48.1, -172.88) * mm, "end": v(-47.29, -173.85) * mm});
            skLineSegment(sketch, "E7796", {"start": v(-47.29, -173.85) * mm, "end": v(-46.37, -174.7) * mm});
            skLineSegment(sketch, "E7797", {"start": v(-46.37, -174.7) * mm, "end": v(-45.36, -175.44) * mm});
            skLineSegment(sketch, "E7798", {"start": v(-45.36, -175.44) * mm, "end": v(-44.26, -176.05) * mm});
            skLineSegment(sketch, "E7799", {"start": v(-44.26, -176.05) * mm, "end": v(-43.1, -176.51) * mm});
            skLineSegment(sketch, "E7800", {"start": v(-43.1, -176.51) * mm, "end": v(-41.87, -176.82) * mm});
            skLineSegment(sketch, "E7801", {"start": v(-41.87, -176.82) * mm, "end": v(-40.63, -176.98) * mm});
            skLineSegment(sketch, "E7802", {"start": v(-40.63, -176.98) * mm, "end": v(-40, -176.98) * mm});
            skLineSegment(sketch, "E7803", {"start": v(-40, -176.98) * mm, "end": v(-40, -177) * mm});
            skLineSegment(sketch, "E7804", {"start": v(-40, -177) * mm, "end": v(-20, -177) * mm});
            skLineSegment(sketch, "E7805", {"start": v(-20, -177) * mm, "end": v(-18.75, -176.92) * mm});
            skLineSegment(sketch, "E7806", {"start": v(-18.75, -176.92) * mm, "end": v(-17.51, -176.69) * mm});
            skLineSegment(sketch, "E7807", {"start": v(-17.51, -176.69) * mm, "end": v(-16.32, -176.3) * mm});
            skLineSegment(sketch, "E7808", {"start": v(-16.32, -176.3) * mm, "end": v(-15.18, -175.76) * mm});
            skLineSegment(sketch, "E7809", {"start": v(-15.18, -175.76) * mm, "end": v(-14.12, -175.1) * mm});
            skLineSegment(sketch, "E7810", {"start": v(-14.12, -175.1) * mm, "end": v(-13.15, -174.29) * mm});
            skLineSegment(sketch, "E7811", {"start": v(-13.15, -174.29) * mm, "end": v(-12.3, -173.37) * mm});
            skLineSegment(sketch, "E7812", {"start": v(-12.3, -173.37) * mm, "end": v(-11.56, -172.36) * mm});
            skLineSegment(sketch, "E7813", {"start": v(-11.56, -172.36) * mm, "end": v(-10.95, -171.26) * mm});
            skLineSegment(sketch, "E7814", {"start": v(-10.95, -171.26) * mm, "end": v(-10.49, -170.1) * mm});
            skLineSegment(sketch, "E7815", {"start": v(-10.49, -170.1) * mm, "end": v(-10.18, -168.87) * mm});
            skLineSegment(sketch, "E7816", {"start": v(-10.18, -168.87) * mm, "end": v(-10.02, -167.63) * mm});
            skLineSegment(sketch, "E7817", {"start": v(-10.02, -167.63) * mm, "end": v(-10.02, -167) * mm});
            skLineSegment(sketch, "E7818", {"start": v(-10.02, -167) * mm, "end": v(-10, -167) * mm});
            skLineSegment(sketch, "E7819", {"start": v(-10, -167) * mm, "end": v(-10, 253) * mm});
            skLineSegment(sketch, "E7820", {"start": v(-10, 253) * mm, "end": v(-10.08, 254.25) * mm});
            skLineSegment(sketch, "E7821", {"start": v(-10.08, 254.25) * mm, "end": v(-10.31, 255.49) * mm});
            skLineSegment(sketch, "E7822", {"start": v(-10.31, 255.49) * mm, "end": v(-10.7, 256.68) * mm});
            skLineSegment(sketch, "E7823", {"start": v(-10.7, 256.68) * mm, "end": v(-11.24, 257.82) * mm});
            skLineSegment(sketch, "E7824", {"start": v(-11.24, 257.82) * mm, "end": v(-11.9, 258.88) * mm});
            skLineSegment(sketch, "E7825", {"start": v(-11.9, 258.88) * mm, "end": v(-12.71, 259.85) * mm});
            skLineSegment(sketch, "E7826", {"start": v(-12.71, 259.85) * mm, "end": v(-13.63, 260.7) * mm});
            skLineSegment(sketch, "E7827", {"start": v(-13.63, 260.7) * mm, "end": v(-14.64, 261.44) * mm});
            skLineSegment(sketch, "E7828", {"start": v(-14.64, 261.44) * mm, "end": v(-15.74, 262.05) * mm});
            skLineSegment(sketch, "E7829", {"start": v(-15.74, 262.05) * mm, "end": v(-16.9, 262.51) * mm});
            skLineSegment(sketch, "E7830", {"start": v(-16.9, 262.51) * mm, "end": v(-18.13, 262.82) * mm});
            skLineSegment(sketch, "E7831", {"start": v(-18.13, 262.82) * mm, "end": v(-19.37, 262.98) * mm});
            skLineSegment(sketch, "E7832", {"start": v(-19.37, 262.98) * mm, "end": v(-20, 262.98) * mm});
            skLineSegment(sketch, "E7833", {"start": v(-20, 262.98) * mm, "end": v(-20, 263) * mm});
            skLineSegment(sketch, "E7834", {"start": v(-20, 263) * mm, "end": v(-390, 263) * mm});
            skLineSegment(sketch, "E7835", {"start": v(-390, 263) * mm, "end": v(-391.25, 262.92) * mm});
            skLineSegment(sketch, "E7836", {"start": v(-391.25, 262.92) * mm, "end": v(-392.49, 262.69) * mm});
            skLineSegment(sketch, "E7837", {"start": v(-392.49, 262.69) * mm, "end": v(-393.68, 262.3) * mm});
            skLineSegment(sketch, "E7838", {"start": v(-393.68, 262.3) * mm, "end": v(-394.82, 261.76) * mm});
            skLineSegment(sketch, "E7839", {"start": v(-394.82, 261.76) * mm, "end": v(-395.88, 261.09) * mm});
            skLineSegment(sketch, "E7840", {"start": v(-395.88, 261.09) * mm, "end": v(-396.85, 260.3) * mm});
            skLineSegment(sketch, "E7841", {"start": v(-396.85, 260.3) * mm, "end": v(-397.7, 259.37) * mm});
            skLineSegment(sketch, "E7842", {"start": v(-397.7, 259.37) * mm, "end": v(-398.44, 258.36) * mm});
            skLineSegment(sketch, "E7843", {"start": v(-398.44, 258.36) * mm, "end": v(-399.05, 257.26) * mm});
            skLineSegment(sketch, "E7844", {"start": v(-399.05, 257.26) * mm, "end": v(-399.51, 256.09) * mm});
            skLineSegment(sketch, "E7845", {"start": v(-399.51, 256.09) * mm, "end": v(-399.82, 254.87) * mm});
            skLineSegment(sketch, "E7846", {"start": v(-399.82, 254.87) * mm, "end": v(-399.98, 253.63) * mm});
            skLineSegment(sketch, "E7847", {"start": v(-399.98, 253.63) * mm, "end": v(-399.98, 253) * mm});
            skLineSegment(sketch, "E7848", {"start": v(-399.98, 253) * mm, "end": v(-400, 253) * mm});
            skLineSegment(sketch, "E7849", {"start": v(-400, 253) * mm, "end": v(-400, -167) * mm});
            skLineSegment(sketch, "E7850", {"start": v(-400, -167) * mm, "end": v(-399.92, -168.25) * mm});
            skLineSegment(sketch, "E7851", {"start": v(-399.92, -168.25) * mm, "end": v(-399.69, -169.49) * mm});
            skLineSegment(sketch, "E7852", {"start": v(-399.69, -169.49) * mm, "end": v(-399.3, -170.68) * mm});
            skLineSegment(sketch, "E7853", {"start": v(-399.3, -170.68) * mm, "end": v(-398.76, -171.82) * mm});
            skLineSegment(sketch, "E7854", {"start": v(-398.76, -171.82) * mm, "end": v(-398.09, -172.88) * mm});
            skLineSegment(sketch, "E7855", {"start": v(-398.09, -172.88) * mm, "end": v(-397.3, -173.85) * mm});
            skLineSegment(sketch, "E7856", {"start": v(-397.3, -173.85) * mm, "end": v(-396.37, -174.7) * mm});
            skLineSegment(sketch, "E7857", {"start": v(-396.37, -174.7) * mm, "end": v(-395.36, -175.44) * mm});
            skLineSegment(sketch, "E7858", {"start": v(-395.36, -175.44) * mm, "end": v(-394.26, -176.05) * mm});
            skLineSegment(sketch, "E7859", {"start": v(-394.26, -176.05) * mm, "end": v(-393.09, -176.51) * mm});
            skLineSegment(sketch, "E7860", {"start": v(-393.09, -176.51) * mm, "end": v(-391.87, -176.82) * mm});
            skLineSegment(sketch, "E7861", {"start": v(-391.87, -176.82) * mm, "end": v(-390.63, -176.98) * mm});
            skLineSegment(sketch, "E7862", {"start": v(-390.63, -176.98) * mm, "end": v(-390, -176.98) * mm});
            skLineSegment(sketch, "E7863", {"start": v(-390, -176.98) * mm, "end": v(-390, -177) * mm});
            skLineSegment(sketch, "E7864", {"start": v(-390, -177) * mm, "end": v(-370, -177) * mm});
            skLineSegment(sketch, "E7865", {"start": v(-370, -177) * mm, "end": v(-368.75, -176.92) * mm});
            skLineSegment(sketch, "E7866", {"start": v(-197.12, 219.95) * mm, "end": v(-199.32, 219.32) * mm});
            skLineSegment(sketch, "E7867", {"start": v(-199.32, 219.32) * mm, "end": v(-202.61, 228.04) * mm});
            skLineSegment(sketch, "E7868", {"start": v(-202.61, 228.04) * mm, "end": v(-202.21, 228.24) * mm});
            skLineSegment(sketch, "E7869", {"start": v(-202.21, 228.24) * mm, "end": v(-201.83, 228.48) * mm});
            skLineSegment(sketch, "E7870", {"start": v(-201.83, 228.48) * mm, "end": v(-201.47, 228.74) * mm});
            skLineSegment(sketch, "E7871", {"start": v(-201.47, 228.74) * mm, "end": v(-201.13, 229.03) * mm});
            skLineSegment(sketch, "E7872", {"start": v(-201.13, 229.03) * mm, "end": v(-200.8, 229.35) * mm});
            skLineSegment(sketch, "E7873", {"start": v(-200.8, 229.35) * mm, "end": v(-200.52, 229.69) * mm});
            skLineSegment(sketch, "E7874", {"start": v(-200.52, 229.69) * mm, "end": v(-200.25, 230.05) * mm});
            skLineSegment(sketch, "E7875", {"start": v(-200.25, 230.05) * mm, "end": v(-200.02, 230.44) * mm});
            skLineSegment(sketch, "E7876", {"start": v(-200.02, 230.44) * mm, "end": v(-199.82, 230.83) * mm});
            skLineSegment(sketch, "E7877", {"start": v(-199.82, 230.83) * mm, "end": v(-199.65, 231.25) * mm});
            skLineSegment(sketch, "E7878", {"start": v(-199.65, 231.25) * mm, "end": v(-199.5, 231.67) * mm});
            skLineSegment(sketch, "E7879", {"start": v(-199.5, 231.67) * mm, "end": v(-199.4, 232.11) * mm});
            skLineSegment(sketch, "E7880", {"start": v(-199.4, 232.11) * mm, "end": v(-199.33, 232.55) * mm});
            skLineSegment(sketch, "E7881", {"start": v(-199.33, 232.55) * mm, "end": v(-199.3, 233) * mm});
            skLineSegment(sketch, "E7882", {"start": v(-199.3, 233) * mm, "end": v(-199.3, 233.45) * mm});
            skLineSegment(sketch, "E7883", {"start": v(-199.3, 233.45) * mm, "end": v(-199.33, 233.9) * mm});
            skLineSegment(sketch, "E7884", {"start": v(-199.33, 233.9) * mm, "end": v(-199.4, 234.34) * mm});
            skLineSegment(sketch, "E7885", {"start": v(-199.4, 234.34) * mm, "end": v(-199.5, 234.77) * mm});
            skLineSegment(sketch, "E7886", {"start": v(-199.5, 234.77) * mm, "end": v(-199.64, 235.2) * mm});
            skLineSegment(sketch, "E7887", {"start": v(-199.64, 235.2) * mm, "end": v(-199.81, 235.62) * mm});
            skLineSegment(sketch, "E7888", {"start": v(-199.81, 235.62) * mm, "end": v(-200.02, 236.02) * mm});
            skLineSegment(sketch, "E7889", {"start": v(-200.02, 236.02) * mm, "end": v(-200.25, 236.4) * mm});
            skLineSegment(sketch, "E7890", {"start": v(-200.25, 236.4) * mm, "end": v(-200.52, 236.76) * mm});
            skLineSegment(sketch, "E7891", {"start": v(-200.52, 236.76) * mm, "end": v(-200.8, 237.1) * mm});
            skLineSegment(sketch, "E7892", {"start": v(-200.8, 237.1) * mm, "end": v(-201.12, 237.42) * mm});
            skLineSegment(sketch, "E7893", {"start": v(-201.12, 237.42) * mm, "end": v(-201.47, 237.7) * mm});
            skLineSegment(sketch, "E7894", {"start": v(-201.47, 237.7) * mm, "end": v(-201.83, 237.97) * mm});
            skLineSegment(sketch, "E7895", {"start": v(-201.83, 237.97) * mm, "end": v(-202.21, 238.2) * mm});
            skLineSegment(sketch, "E7896", {"start": v(-202.21, 238.2) * mm, "end": v(-202.6, 238.41) * mm});
            skLineSegment(sketch, "E7897", {"start": v(-202.6, 238.41) * mm, "end": v(-203.02, 238.58) * mm});
            skLineSegment(sketch, "E7898", {"start": v(-203.02, 238.58) * mm, "end": v(-203.45, 238.72) * mm});
            skLineSegment(sketch, "E7899", {"start": v(-203.45, 238.72) * mm, "end": v(-203.89, 238.82) * mm});
            skLineSegment(sketch, "E7900", {"start": v(-203.89, 238.82) * mm, "end": v(-204.33, 238.9) * mm});
            skLineSegment(sketch, "E7901", {"start": v(-204.33, 238.9) * mm, "end": v(-204.78, 238.93) * mm});
            skLineSegment(sketch, "E7902", {"start": v(-204.78, 238.93) * mm, "end": v(-205.22, 238.93) * mm});
            skLineSegment(sketch, "E7903", {"start": v(-205.22, 238.93) * mm, "end": v(-205.67, 238.9) * mm});
            skLineSegment(sketch, "E7904", {"start": v(-205.67, 238.9) * mm, "end": v(-206.11, 238.82) * mm});
            skLineSegment(sketch, "E7905", {"start": v(-206.11, 238.82) * mm, "end": v(-206.55, 238.72) * mm});
            skLineSegment(sketch, "E7906", {"start": v(-206.55, 238.72) * mm, "end": v(-206.98, 238.58) * mm});
            skLineSegment(sketch, "E7907", {"start": v(-206.98, 238.58) * mm, "end": v(-207.4, 238.41) * mm});
            skLineSegment(sketch, "E7908", {"start": v(-207.4, 238.41) * mm, "end": v(-207.79, 238.2) * mm});
            skLineSegment(sketch, "E7909", {"start": v(-207.79, 238.2) * mm, "end": v(-208.17, 237.97) * mm});
            skLineSegment(sketch, "E7910", {"start": v(-208.17, 237.97) * mm, "end": v(-208.53, 237.7) * mm});
            skLineSegment(sketch, "E7911", {"start": v(-208.53, 237.7) * mm, "end": v(-208.88, 237.42) * mm});
            skLineSegment(sketch, "E7912", {"start": v(-208.88, 237.42) * mm, "end": v(-209.2, 237.1) * mm});
            skLineSegment(sketch, "E7913", {"start": v(-209.2, 237.1) * mm, "end": v(-209.48, 236.76) * mm});
            skLineSegment(sketch, "E7914", {"start": v(-209.48, 236.76) * mm, "end": v(-209.75, 236.4) * mm});
            skLineSegment(sketch, "E7915", {"start": v(-209.75, 236.4) * mm, "end": v(-209.98, 236.02) * mm});
            skLineSegment(sketch, "E7916", {"start": v(-209.98, 236.02) * mm, "end": v(-210.19, 235.62) * mm});
            skLineSegment(sketch, "E7917", {"start": v(-210.19, 235.62) * mm, "end": v(-210.36, 235.2) * mm});
            skLineSegment(sketch, "E7918", {"start": v(-210.36, 235.2) * mm, "end": v(-210.5, 234.77) * mm});
            skLineSegment(sketch, "E7919", {"start": v(-210.5, 234.77) * mm, "end": v(-210.6, 234.34) * mm});
            skLineSegment(sketch, "E7920", {"start": v(-210.6, 234.34) * mm, "end": v(-210.67, 233.9) * mm});
            skLineSegment(sketch, "E7921", {"start": v(-210.67, 233.9) * mm, "end": v(-210.7, 233.45) * mm});
            skLineSegment(sketch, "E7922", {"start": v(-210.7, 233.45) * mm, "end": v(-210.7, 233) * mm});
            skLineSegment(sketch, "E7923", {"start": v(-210.7, 233) * mm, "end": v(-210.67, 232.55) * mm});
            skLineSegment(sketch, "E7924", {"start": v(-210.67, 232.55) * mm, "end": v(-210.6, 232.11) * mm});
            skLineSegment(sketch, "E7925", {"start": v(-210.6, 232.11) * mm, "end": v(-210.5, 231.67) * mm});
            skLineSegment(sketch, "E7926", {"start": v(-210.5, 231.67) * mm, "end": v(-210.35, 231.25) * mm});
            skLineSegment(sketch, "E7927", {"start": v(-210.35, 231.25) * mm, "end": v(-210.18, 230.83) * mm});
            skLineSegment(sketch, "E7928", {"start": v(-210.18, 230.83) * mm, "end": v(-209.98, 230.44) * mm});
            skLineSegment(sketch, "E7929", {"start": v(-209.98, 230.44) * mm, "end": v(-209.75, 230.05) * mm});
            skLineSegment(sketch, "E7930", {"start": v(-209.75, 230.05) * mm, "end": v(-209.48, 229.69) * mm});
            skLineSegment(sketch, "E7931", {"start": v(-209.48, 229.69) * mm, "end": v(-209.2, 229.35) * mm});
            skLineSegment(sketch, "E7932", {"start": v(-209.2, 229.35) * mm, "end": v(-208.87, 229.03) * mm});
            skLineSegment(sketch, "E7933", {"start": v(-208.87, 229.03) * mm, "end": v(-208.53, 228.74) * mm});
            skLineSegment(sketch, "E7934", {"start": v(-208.53, 228.74) * mm, "end": v(-208.17, 228.48) * mm});
            skLineSegment(sketch, "E7935", {"start": v(-208.17, 228.48) * mm, "end": v(-207.79, 228.24) * mm});
            skLineSegment(sketch, "E7936", {"start": v(-207.79, 228.24) * mm, "end": v(-207.25, 227.7) * mm});
            skLineSegment(sketch, "E7937", {"start": v(-207.25, 227.7) * mm, "end": v(-211.02, 219.18) * mm});
            skLineSegment(sketch, "E7938", {"start": v(-211.02, 219.18) * mm, "end": v(-213.12, 219.93) * mm});
            skLineSegment(sketch, "E7939", {"start": v(-213.12, 219.93) * mm, "end": v(-217.54, 217.2) * mm});
            skLineSegment(sketch, "E7940", {"start": v(-217.54, 217.2) * mm, "end": v(-221.07, 221.01) * mm});
            skLineSegment(sketch, "E7941", {"start": v(-221.07, 221.01) * mm, "end": v(-218.28, 225.35) * mm});
            skLineSegment(sketch, "E7942", {"start": v(-218.28, 225.35) * mm, "end": v(-220.15, 229.56) * mm});
            skLineSegment(sketch, "E7943", {"start": v(-220.15, 229.56) * mm, "end": v(-225.2, 230.76) * mm});
            skLineSegment(sketch, "E7944", {"start": v(-225.2, 230.76) * mm, "end": v(-225, 235.95) * mm});
            skLineSegment(sketch, "E7945", {"start": v(-225, 235.95) * mm, "end": v(-219.96, 237.04) * mm});
            skLineSegment(sketch, "E7946", {"start": v(-219.96, 237.04) * mm, "end": v(-218.3, 241.35) * mm});
            skLineSegment(sketch, "E7947", {"start": v(-218.3, 241.35) * mm, "end": v(-221.03, 245.77) * mm});
            skLineSegment(sketch, "E7948", {"start": v(-221.03, 245.77) * mm, "end": v(-217.21, 249.3) * mm});
            skLineSegment(sketch, "E7949", {"start": v(-217.21, 249.3) * mm, "end": v(-212.88, 246.5) * mm});
            skLineSegment(sketch, "E7950", {"start": v(-212.88, 246.5) * mm, "end": v(-208.66, 248.38) * mm});
            skLineSegment(sketch, "E7951", {"start": v(-208.66, 248.38) * mm, "end": v(-207.47, 253.43) * mm});
            skLineSegment(sketch, "E7952", {"start": v(-207.47, 253.43) * mm, "end": v(-202.27, 253.22) * mm});
            skLineSegment(sketch, "E7953", {"start": v(-202.27, 253.22) * mm, "end": v(-201.18, 248.18) * mm});
            skLineSegment(sketch, "E7954", {"start": v(-201.18, 248.18) * mm, "end": v(-196.88, 246.53) * mm});
            skLineSegment(sketch, "E7955", {"start": v(-196.88, 246.53) * mm, "end": v(-192.46, 249.26) * mm});
            skLineSegment(sketch, "E7956", {"start": v(-192.46, 249.26) * mm, "end": v(-188.93, 245.44) * mm});
            skLineSegment(sketch, "E7957", {"start": v(-188.93, 245.44) * mm, "end": v(-191.72, 241.1) * mm});
            skLineSegment(sketch, "E7958", {"start": v(-191.72, 241.1) * mm, "end": v(-189.85, 236.89) * mm});
            skLineSegment(sketch, "E7959", {"start": v(-189.85, 236.89) * mm, "end": v(-184.8, 235.7) * mm});
            skLineSegment(sketch, "E7960", {"start": v(-184.8, 235.7) * mm, "end": v(-185, 230.5) * mm});
            skLineSegment(sketch, "E7961", {"start": v(-185, 230.5) * mm, "end": v(-190.04, 229.4) * mm});
            skLineSegment(sketch, "E7962", {"start": v(-190.04, 229.4) * mm, "end": v(-191.7, 225.1) * mm});
            skLineSegment(sketch, "E7963", {"start": v(-191.7, 225.1) * mm, "end": v(-188.97, 220.68) * mm});
            skLineSegment(sketch, "E7964", {"start": v(-188.97, 220.68) * mm, "end": v(-192.79, 217.16) * mm});
            skLineSegment(sketch, "E7965", {"start": v(-192.79, 217.16) * mm, "end": v(-197.12, 219.95) * mm});
            skLineSegment(sketch, "E7966", {"start": v(-387.1, 249.5) * mm, "end": v(-387.28, 249.53) * mm});
            skLineSegment(sketch, "E7967", {"start": v(-387.28, 249.53) * mm, "end": v(-387.46, 249.57) * mm});
            skLineSegment(sketch, "E7968", {"start": v(-387.46, 249.57) * mm, "end": v(-387.64, 249.64) * mm});
            skLineSegment(sketch, "E7969", {"start": v(-387.64, 249.64) * mm, "end": v(-387.8, 249.73) * mm});
            skLineSegment(sketch, "E7970", {"start": v(-387.8, 249.73) * mm, "end": v(-387.96, 249.84) * mm});
            skLineSegment(sketch, "E7971", {"start": v(-387.96, 249.84) * mm, "end": v(-388.1, 249.97) * mm});
            skLineSegment(sketch, "E7972", {"start": v(-388.1, 249.97) * mm, "end": v(-388.21, 250.12) * mm});
            skLineSegment(sketch, "E7973", {"start": v(-388.21, 250.12) * mm, "end": v(-388.31, 250.28) * mm});
            skLineSegment(sketch, "E7974", {"start": v(-388.31, 250.28) * mm, "end": v(-388.4, 250.45) * mm});
            skLineSegment(sketch, "E7975", {"start": v(-388.4, 250.45) * mm, "end": v(-388.45, 250.63) * mm});
            skLineSegment(sketch, "E7976", {"start": v(-388.45, 250.63) * mm, "end": v(-388.49, 250.81) * mm});
            skLineSegment(sketch, "E7977", {"start": v(-388.49, 250.81) * mm, "end": v(-388.5, 251) * mm});
            skLineSegment(sketch, "E7978", {"start": v(-388.5, 251) * mm, "end": v(-388.49, 251.19) * mm});
            skLineSegment(sketch, "E7979", {"start": v(-388.49, 251.19) * mm, "end": v(-388.45, 251.37) * mm});
            skLineSegment(sketch, "E7980", {"start": v(-388.45, 251.37) * mm, "end": v(-388.4, 251.55) * mm});
            skLineSegment(sketch, "E7981", {"start": v(-388.4, 251.55) * mm, "end": v(-388.31, 251.72) * mm});
            skLineSegment(sketch, "E7982", {"start": v(-388.31, 251.72) * mm, "end": v(-388.21, 251.88) * mm});
            skLineSegment(sketch, "E7983", {"start": v(-388.21, 251.88) * mm, "end": v(-388.1, 252.03) * mm});
            skLineSegment(sketch, "E7984", {"start": v(-388.1, 252.03) * mm, "end": v(-387.96, 252.16) * mm});
            skLineSegment(sketch, "E7985", {"start": v(-387.96, 252.16) * mm, "end": v(-387.8, 252.27) * mm});
            skLineSegment(sketch, "E7986", {"start": v(-387.8, 252.27) * mm, "end": v(-387.64, 252.36) * mm});
            skLineSegment(sketch, "E7987", {"start": v(-387.64, 252.36) * mm, "end": v(-387.46, 252.43) * mm});
            skLineSegment(sketch, "E7988", {"start": v(-387.46, 252.43) * mm, "end": v(-387.28, 252.47) * mm});
            skLineSegment(sketch, "E7989", {"start": v(-387.28, 252.47) * mm, "end": v(-387.1, 252.5) * mm});
            skLineSegment(sketch, "E7990", {"start": v(-387.1, 252.5) * mm, "end": v(-386.9, 252.5) * mm});
            skLineSegment(sketch, "E7991", {"start": v(-386.9, 252.5) * mm, "end": v(-386.72, 252.47) * mm});
            skLineSegment(sketch, "E7992", {"start": v(-386.72, 252.47) * mm, "end": v(-386.54, 252.43) * mm});
            skLineSegment(sketch, "E7993", {"start": v(-386.54, 252.43) * mm, "end": v(-386.36, 252.36) * mm});
            skLineSegment(sketch, "E7994", {"start": v(-386.36, 252.36) * mm, "end": v(-386.2, 252.27) * mm});
            skLineSegment(sketch, "E7995", {"start": v(-386.2, 252.27) * mm, "end": v(-386.04, 252.16) * mm});
            skLineSegment(sketch, "E7996", {"start": v(-386.04, 252.16) * mm, "end": v(-385.9, 252.03) * mm});
            skLineSegment(sketch, "E7997", {"start": v(-385.9, 252.03) * mm, "end": v(-385.79, 251.88) * mm});
            skLineSegment(sketch, "E7998", {"start": v(-385.79, 251.88) * mm, "end": v(-385.69, 251.72) * mm});
            skLineSegment(sketch, "E7999", {"start": v(-385.69, 251.72) * mm, "end": v(-385.6, 251.55) * mm});
            skLineSegment(sketch, "E8000", {"start": v(-385.6, 251.55) * mm, "end": v(-385.55, 251.37) * mm});
            skLineSegment(sketch, "E8001", {"start": v(-385.55, 251.37) * mm, "end": v(-385.51, 251.19) * mm});
            skLineSegment(sketch, "E8002", {"start": v(-385.51, 251.19) * mm, "end": v(-385.5, 251) * mm});
            skLineSegment(sketch, "E8003", {"start": v(-385.5, 251) * mm, "end": v(-385.51, 250.81) * mm});
            skLineSegment(sketch, "E8004", {"start": v(-385.51, 250.81) * mm, "end": v(-385.55, 250.63) * mm});
            skLineSegment(sketch, "E8005", {"start": v(-385.55, 250.63) * mm, "end": v(-385.6, 250.45) * mm});
            skLineSegment(sketch, "E8006", {"start": v(-385.6, 250.45) * mm, "end": v(-385.69, 250.28) * mm});
            skLineSegment(sketch, "E8007", {"start": v(-385.69, 250.28) * mm, "end": v(-385.79, 250.12) * mm});
            skLineSegment(sketch, "E8008", {"start": v(-385.79, 250.12) * mm, "end": v(-385.9, 249.97) * mm});
            skLineSegment(sketch, "E8009", {"start": v(-385.9, 249.97) * mm, "end": v(-386.04, 249.84) * mm});
            skLineSegment(sketch, "E8010", {"start": v(-386.04, 249.84) * mm, "end": v(-386.2, 249.73) * mm});
            skLineSegment(sketch, "E8011", {"start": v(-386.2, 249.73) * mm, "end": v(-386.36, 249.64) * mm});
            skLineSegment(sketch, "E8012", {"start": v(-386.36, 249.64) * mm, "end": v(-386.54, 249.57) * mm});
            skLineSegment(sketch, "E8013", {"start": v(-386.54, 249.57) * mm, "end": v(-386.72, 249.53) * mm});
            skLineSegment(sketch, "E8014", {"start": v(-386.72, 249.53) * mm, "end": v(-386.9, 249.5) * mm});
            skLineSegment(sketch, "E8015", {"start": v(-386.9, 249.5) * mm, "end": v(-387.1, 249.5) * mm});
            skLineSegment(sketch, "E8016", {"start": v(-367.1, 249.5) * mm, "end": v(-367.28, 249.53) * mm});
            skLineSegment(sketch, "E8017", {"start": v(-367.28, 249.53) * mm, "end": v(-367.46, 249.57) * mm});
            skLineSegment(sketch, "E8018", {"start": v(-367.46, 249.57) * mm, "end": v(-367.64, 249.64) * mm});
            skLineSegment(sketch, "E8019", {"start": v(-367.64, 249.64) * mm, "end": v(-367.8, 249.73) * mm});
            skLineSegment(sketch, "E8020", {"start": v(-367.8, 249.73) * mm, "end": v(-367.96, 249.84) * mm});
            skLineSegment(sketch, "E8021", {"start": v(-367.96, 249.84) * mm, "end": v(-368.1, 249.97) * mm});
            skLineSegment(sketch, "E8022", {"start": v(-368.1, 249.97) * mm, "end": v(-368.21, 250.12) * mm});
            skLineSegment(sketch, "E8023", {"start": v(-368.21, 250.12) * mm, "end": v(-368.31, 250.28) * mm});
            skLineSegment(sketch, "E8024", {"start": v(-368.31, 250.28) * mm, "end": v(-368.4, 250.45) * mm});
            skLineSegment(sketch, "E8025", {"start": v(-368.4, 250.45) * mm, "end": v(-368.45, 250.63) * mm});
            skLineSegment(sketch, "E8026", {"start": v(-368.45, 250.63) * mm, "end": v(-368.49, 250.81) * mm});
            skLineSegment(sketch, "E8027", {"start": v(-368.49, 250.81) * mm, "end": v(-368.5, 251) * mm});
            skLineSegment(sketch, "E8028", {"start": v(-368.5, 251) * mm, "end": v(-368.49, 251.19) * mm});
            skLineSegment(sketch, "E8029", {"start": v(-368.49, 251.19) * mm, "end": v(-368.45, 251.37) * mm});
            skLineSegment(sketch, "E8030", {"start": v(-368.45, 251.37) * mm, "end": v(-368.4, 251.55) * mm});
            skLineSegment(sketch, "E8031", {"start": v(-368.4, 251.55) * mm, "end": v(-368.31, 251.72) * mm});
            skLineSegment(sketch, "E8032", {"start": v(-368.31, 251.72) * mm, "end": v(-368.21, 251.88) * mm});
            skLineSegment(sketch, "E8033", {"start": v(-368.21, 251.88) * mm, "end": v(-368.1, 252.03) * mm});
            skLineSegment(sketch, "E8034", {"start": v(-368.1, 252.03) * mm, "end": v(-367.96, 252.16) * mm});
            skLineSegment(sketch, "E8035", {"start": v(-367.96, 252.16) * mm, "end": v(-367.8, 252.27) * mm});
            skLineSegment(sketch, "E8036", {"start": v(-367.8, 252.27) * mm, "end": v(-367.64, 252.36) * mm});
            skLineSegment(sketch, "E8037", {"start": v(-367.64, 252.36) * mm, "end": v(-367.46, 252.43) * mm});
            skLineSegment(sketch, "E8038", {"start": v(-367.46, 252.43) * mm, "end": v(-367.28, 252.47) * mm});
            skLineSegment(sketch, "E8039", {"start": v(-367.28, 252.47) * mm, "end": v(-367.1, 252.5) * mm});
            skLineSegment(sketch, "E8040", {"start": v(-367.1, 252.5) * mm, "end": v(-366.9, 252.5) * mm});
            skLineSegment(sketch, "E8041", {"start": v(-366.9, 252.5) * mm, "end": v(-366.72, 252.47) * mm});
            skLineSegment(sketch, "E8042", {"start": v(-366.72, 252.47) * mm, "end": v(-366.54, 252.43) * mm});
            skLineSegment(sketch, "E8043", {"start": v(-366.54, 252.43) * mm, "end": v(-366.36, 252.36) * mm});
            skLineSegment(sketch, "E8044", {"start": v(-366.36, 252.36) * mm, "end": v(-366.2, 252.27) * mm});
            skLineSegment(sketch, "E8045", {"start": v(-366.2, 252.27) * mm, "end": v(-366.04, 252.16) * mm});
            skLineSegment(sketch, "E8046", {"start": v(-366.04, 252.16) * mm, "end": v(-365.9, 252.03) * mm});
            skLineSegment(sketch, "E8047", {"start": v(-365.9, 252.03) * mm, "end": v(-365.79, 251.88) * mm});
            skLineSegment(sketch, "E8048", {"start": v(-365.79, 251.88) * mm, "end": v(-365.69, 251.72) * mm});
            skLineSegment(sketch, "E8049", {"start": v(-365.69, 251.72) * mm, "end": v(-365.6, 251.55) * mm});
            skLineSegment(sketch, "E8050", {"start": v(-365.6, 251.55) * mm, "end": v(-365.55, 251.37) * mm});
            skLineSegment(sketch, "E8051", {"start": v(-365.55, 251.37) * mm, "end": v(-365.51, 251.19) * mm});
            skLineSegment(sketch, "E8052", {"start": v(-365.51, 251.19) * mm, "end": v(-365.5, 251) * mm});
            skLineSegment(sketch, "E8053", {"start": v(-365.5, 251) * mm, "end": v(-365.51, 250.81) * mm});
            skLineSegment(sketch, "E8054", {"start": v(-365.51, 250.81) * mm, "end": v(-365.55, 250.63) * mm});
            skLineSegment(sketch, "E8055", {"start": v(-365.55, 250.63) * mm, "end": v(-365.6, 250.45) * mm});
            skLineSegment(sketch, "E8056", {"start": v(-365.6, 250.45) * mm, "end": v(-365.69, 250.28) * mm});
            skLineSegment(sketch, "E8057", {"start": v(-365.69, 250.28) * mm, "end": v(-365.79, 250.12) * mm});
            skLineSegment(sketch, "E8058", {"start": v(-365.79, 250.12) * mm, "end": v(-365.9, 249.97) * mm});
            skLineSegment(sketch, "E8059", {"start": v(-365.9, 249.97) * mm, "end": v(-366.04, 249.84) * mm});
            skLineSegment(sketch, "E8060", {"start": v(-366.04, 249.84) * mm, "end": v(-366.2, 249.73) * mm});
            skLineSegment(sketch, "E8061", {"start": v(-366.2, 249.73) * mm, "end": v(-366.36, 249.64) * mm});
            skLineSegment(sketch, "E8062", {"start": v(-366.36, 249.64) * mm, "end": v(-366.54, 249.57) * mm});
            skLineSegment(sketch, "E8063", {"start": v(-366.54, 249.57) * mm, "end": v(-366.72, 249.53) * mm});
            skLineSegment(sketch, "E8064", {"start": v(-366.72, 249.53) * mm, "end": v(-366.9, 249.5) * mm});
            skLineSegment(sketch, "E8065", {"start": v(-366.9, 249.5) * mm, "end": v(-367.1, 249.5) * mm});
            skLineSegment(sketch, "E8066", {"start": v(-43.1, 249.5) * mm, "end": v(-43.28, 249.53) * mm});
            skLineSegment(sketch, "E8067", {"start": v(-43.28, 249.53) * mm, "end": v(-43.46, 249.57) * mm});
            skLineSegment(sketch, "E8068", {"start": v(-43.46, 249.57) * mm, "end": v(-43.64, 249.64) * mm});
            skLineSegment(sketch, "E8069", {"start": v(-43.64, 249.64) * mm, "end": v(-43.8, 249.73) * mm});
            skLineSegment(sketch, "E8070", {"start": v(-43.8, 249.73) * mm, "end": v(-43.96, 249.84) * mm});
            skLineSegment(sketch, "E8071", {"start": v(-43.96, 249.84) * mm, "end": v(-44.1, 249.97) * mm});
            skLineSegment(sketch, "E8072", {"start": v(-44.1, 249.97) * mm, "end": v(-44.21, 250.12) * mm});
            skLineSegment(sketch, "E8073", {"start": v(-44.21, 250.12) * mm, "end": v(-44.31, 250.28) * mm});
            skLineSegment(sketch, "E8074", {"start": v(-44.31, 250.28) * mm, "end": v(-44.4, 250.45) * mm});
            skLineSegment(sketch, "E8075", {"start": v(-44.4, 250.45) * mm, "end": v(-44.45, 250.63) * mm});
            skLineSegment(sketch, "E8076", {"start": v(-44.45, 250.63) * mm, "end": v(-44.49, 250.81) * mm});
            skLineSegment(sketch, "E8077", {"start": v(-44.49, 250.81) * mm, "end": v(-44.5, 251) * mm});
            skLineSegment(sketch, "E8078", {"start": v(-44.5, 251) * mm, "end": v(-44.49, 251.19) * mm});
            skLineSegment(sketch, "E8079", {"start": v(-44.49, 251.19) * mm, "end": v(-44.45, 251.37) * mm});
            skLineSegment(sketch, "E8080", {"start": v(-44.45, 251.37) * mm, "end": v(-44.4, 251.55) * mm});
            skLineSegment(sketch, "E8081", {"start": v(-44.4, 251.55) * mm, "end": v(-44.31, 251.72) * mm});
            skLineSegment(sketch, "E8082", {"start": v(-44.31, 251.72) * mm, "end": v(-44.21, 251.88) * mm});
            skLineSegment(sketch, "E8083", {"start": v(-44.21, 251.88) * mm, "end": v(-44.1, 252.03) * mm});
            skLineSegment(sketch, "E8084", {"start": v(-44.1, 252.03) * mm, "end": v(-43.96, 252.16) * mm});
            skLineSegment(sketch, "E8085", {"start": v(-43.96, 252.16) * mm, "end": v(-43.8, 252.27) * mm});
            skLineSegment(sketch, "E8086", {"start": v(-43.8, 252.27) * mm, "end": v(-43.64, 252.36) * mm});
            skLineSegment(sketch, "E8087", {"start": v(-43.64, 252.36) * mm, "end": v(-43.46, 252.43) * mm});
            skLineSegment(sketch, "E8088", {"start": v(-43.46, 252.43) * mm, "end": v(-43.28, 252.47) * mm});
            skLineSegment(sketch, "E8089", {"start": v(-43.28, 252.47) * mm, "end": v(-43.1, 252.5) * mm});
            skLineSegment(sketch, "E8090", {"start": v(-43.1, 252.5) * mm, "end": v(-42.9, 252.5) * mm});
            skLineSegment(sketch, "E8091", {"start": v(-42.9, 252.5) * mm, "end": v(-42.72, 252.47) * mm});
            skLineSegment(sketch, "E8092", {"start": v(-42.72, 252.47) * mm, "end": v(-42.54, 252.43) * mm});
            skLineSegment(sketch, "E8093", {"start": v(-42.54, 252.43) * mm, "end": v(-42.36, 252.36) * mm});
            skLineSegment(sketch, "E8094", {"start": v(-42.36, 252.36) * mm, "end": v(-42.2, 252.27) * mm});
            skLineSegment(sketch, "E8095", {"start": v(-42.2, 252.27) * mm, "end": v(-42.04, 252.16) * mm});
            skLineSegment(sketch, "E8096", {"start": v(-42.04, 252.16) * mm, "end": v(-41.9, 252.03) * mm});
            skLineSegment(sketch, "E8097", {"start": v(-41.9, 252.03) * mm, "end": v(-41.79, 251.88) * mm});
            skLineSegment(sketch, "E8098", {"start": v(-41.79, 251.88) * mm, "end": v(-41.69, 251.72) * mm});
            skLineSegment(sketch, "E8099", {"start": v(-41.69, 251.72) * mm, "end": v(-41.6, 251.55) * mm});
            skLineSegment(sketch, "E8100", {"start": v(-41.6, 251.55) * mm, "end": v(-41.55, 251.37) * mm});
            skLineSegment(sketch, "E8101", {"start": v(-41.55, 251.37) * mm, "end": v(-41.51, 251.19) * mm});
            skLineSegment(sketch, "E8102", {"start": v(-41.51, 251.19) * mm, "end": v(-41.5, 251) * mm});
            skLineSegment(sketch, "E8103", {"start": v(-41.5, 251) * mm, "end": v(-41.51, 250.81) * mm});
            skLineSegment(sketch, "E8104", {"start": v(-41.51, 250.81) * mm, "end": v(-41.55, 250.63) * mm});
            skLineSegment(sketch, "E8105", {"start": v(-41.55, 250.63) * mm, "end": v(-41.6, 250.45) * mm});
            skLineSegment(sketch, "E8106", {"start": v(-41.6, 250.45) * mm, "end": v(-41.69, 250.28) * mm});
            skLineSegment(sketch, "E8107", {"start": v(-41.69, 250.28) * mm, "end": v(-41.79, 250.12) * mm});
            skLineSegment(sketch, "E8108", {"start": v(-41.79, 250.12) * mm, "end": v(-41.9, 249.97) * mm});
            skLineSegment(sketch, "E8109", {"start": v(-41.9, 249.97) * mm, "end": v(-42.04, 249.84) * mm});
            skLineSegment(sketch, "E8110", {"start": v(-42.04, 249.84) * mm, "end": v(-42.2, 249.73) * mm});
            skLineSegment(sketch, "E8111", {"start": v(-42.2, 249.73) * mm, "end": v(-42.36, 249.64) * mm});
            skLineSegment(sketch, "E8112", {"start": v(-42.36, 249.64) * mm, "end": v(-42.54, 249.57) * mm});
            skLineSegment(sketch, "E8113", {"start": v(-42.54, 249.57) * mm, "end": v(-42.72, 249.53) * mm});
            skLineSegment(sketch, "E8114", {"start": v(-42.72, 249.53) * mm, "end": v(-42.9, 249.5) * mm});
            skLineSegment(sketch, "E8115", {"start": v(-42.9, 249.5) * mm, "end": v(-43.1, 249.5) * mm});
            skLineSegment(sketch, "E8116", {"start": v(-23.1, 249.5) * mm, "end": v(-23.28, 249.53) * mm});
            skLineSegment(sketch, "E8117", {"start": v(-23.28, 249.53) * mm, "end": v(-23.46, 249.57) * mm});
            skLineSegment(sketch, "E8118", {"start": v(-23.46, 249.57) * mm, "end": v(-23.64, 249.64) * mm});
            skLineSegment(sketch, "E8119", {"start": v(-23.64, 249.64) * mm, "end": v(-23.8, 249.73) * mm});
            skLineSegment(sketch, "E8120", {"start": v(-23.8, 249.73) * mm, "end": v(-23.96, 249.84) * mm});
            skLineSegment(sketch, "E8121", {"start": v(-23.96, 249.84) * mm, "end": v(-24.1, 249.97) * mm});
            skLineSegment(sketch, "E8122", {"start": v(-24.1, 249.97) * mm, "end": v(-24.21, 250.12) * mm});
            skLineSegment(sketch, "E8123", {"start": v(-24.21, 250.12) * mm, "end": v(-24.31, 250.28) * mm});
            skLineSegment(sketch, "E8124", {"start": v(-24.31, 250.28) * mm, "end": v(-24.4, 250.45) * mm});
            skLineSegment(sketch, "E8125", {"start": v(-24.4, 250.45) * mm, "end": v(-24.45, 250.63) * mm});
            skLineSegment(sketch, "E8126", {"start": v(-24.45, 250.63) * mm, "end": v(-24.49, 250.81) * mm});
            skLineSegment(sketch, "E8127", {"start": v(-24.49, 250.81) * mm, "end": v(-24.5, 251) * mm});
            skLineSegment(sketch, "E8128", {"start": v(-24.5, 251) * mm, "end": v(-24.49, 251.19) * mm});
            skLineSegment(sketch, "E8129", {"start": v(-24.49, 251.19) * mm, "end": v(-24.45, 251.37) * mm});
            skLineSegment(sketch, "E8130", {"start": v(-24.45, 251.37) * mm, "end": v(-24.4, 251.55) * mm});
            skLineSegment(sketch, "E8131", {"start": v(-24.4, 251.55) * mm, "end": v(-24.31, 251.72) * mm});
            skLineSegment(sketch, "E8132", {"start": v(-24.31, 251.72) * mm, "end": v(-24.21, 251.88) * mm});
            skLineSegment(sketch, "E8133", {"start": v(-24.21, 251.88) * mm, "end": v(-24.1, 252.03) * mm});
            skLineSegment(sketch, "E8134", {"start": v(-24.1, 252.03) * mm, "end": v(-23.96, 252.16) * mm});
            skLineSegment(sketch, "E8135", {"start": v(-23.96, 252.16) * mm, "end": v(-23.8, 252.27) * mm});
            skLineSegment(sketch, "E8136", {"start": v(-23.8, 252.27) * mm, "end": v(-23.64, 252.36) * mm});
            skLineSegment(sketch, "E8137", {"start": v(-23.64, 252.36) * mm, "end": v(-23.46, 252.43) * mm});
            skLineSegment(sketch, "E8138", {"start": v(-23.46, 252.43) * mm, "end": v(-23.28, 252.47) * mm});
            skLineSegment(sketch, "E8139", {"start": v(-23.28, 252.47) * mm, "end": v(-23.1, 252.5) * mm});
            skLineSegment(sketch, "E8140", {"start": v(-23.1, 252.5) * mm, "end": v(-22.9, 252.5) * mm});
            skLineSegment(sketch, "E8141", {"start": v(-22.9, 252.5) * mm, "end": v(-22.72, 252.47) * mm});
            skLineSegment(sketch, "E8142", {"start": v(-22.72, 252.47) * mm, "end": v(-22.54, 252.43) * mm});
            skLineSegment(sketch, "E8143", {"start": v(-22.54, 252.43) * mm, "end": v(-22.36, 252.36) * mm});
            skLineSegment(sketch, "E8144", {"start": v(-22.36, 252.36) * mm, "end": v(-22.2, 252.27) * mm});
            skLineSegment(sketch, "E8145", {"start": v(-22.2, 252.27) * mm, "end": v(-22.04, 252.16) * mm});
            skLineSegment(sketch, "E8146", {"start": v(-22.04, 252.16) * mm, "end": v(-21.9, 252.03) * mm});
            skLineSegment(sketch, "E8147", {"start": v(-21.9, 252.03) * mm, "end": v(-21.79, 251.88) * mm});
            skLineSegment(sketch, "E8148", {"start": v(-21.79, 251.88) * mm, "end": v(-21.69, 251.72) * mm});
            skLineSegment(sketch, "E8149", {"start": v(-21.69, 251.72) * mm, "end": v(-21.6, 251.55) * mm});
            skLineSegment(sketch, "E8150", {"start": v(-21.6, 251.55) * mm, "end": v(-21.55, 251.37) * mm});
            skLineSegment(sketch, "E8151", {"start": v(-21.55, 251.37) * mm, "end": v(-21.51, 251.19) * mm});
            skLineSegment(sketch, "E8152", {"start": v(-21.51, 251.19) * mm, "end": v(-21.5, 251) * mm});
            skLineSegment(sketch, "E8153", {"start": v(-21.5, 251) * mm, "end": v(-21.51, 250.81) * mm});
            skLineSegment(sketch, "E8154", {"start": v(-21.51, 250.81) * mm, "end": v(-21.55, 250.63) * mm});
            skLineSegment(sketch, "E8155", {"start": v(-21.55, 250.63) * mm, "end": v(-21.6, 250.45) * mm});
            skLineSegment(sketch, "E8156", {"start": v(-21.6, 250.45) * mm, "end": v(-21.69, 250.28) * mm});
            skLineSegment(sketch, "E8157", {"start": v(-21.69, 250.28) * mm, "end": v(-21.79, 250.12) * mm});
            skLineSegment(sketch, "E8158", {"start": v(-21.79, 250.12) * mm, "end": v(-21.9, 249.97) * mm});
            skLineSegment(sketch, "E8159", {"start": v(-21.9, 249.97) * mm, "end": v(-22.04, 249.84) * mm});
            skLineSegment(sketch, "E8160", {"start": v(-22.04, 249.84) * mm, "end": v(-22.2, 249.73) * mm});
            skLineSegment(sketch, "E8161", {"start": v(-22.2, 249.73) * mm, "end": v(-22.36, 249.64) * mm});
            skLineSegment(sketch, "E8162", {"start": v(-22.36, 249.64) * mm, "end": v(-22.54, 249.57) * mm});
            skLineSegment(sketch, "E8163", {"start": v(-22.54, 249.57) * mm, "end": v(-22.72, 249.53) * mm});
            skLineSegment(sketch, "E8164", {"start": v(-22.72, 249.53) * mm, "end": v(-22.9, 249.5) * mm});
            skLineSegment(sketch, "E8165", {"start": v(-22.9, 249.5) * mm, "end": v(-23.1, 249.5) * mm});
            skLineSegment(sketch, "E8166", {"start": v(-162.03, 246.19) * mm, "end": v(-162.03, 250.1) * mm});
            skLineSegment(sketch, "E8167", {"start": v(-162.03, 250.1) * mm, "end": v(-154.32, 250.1) * mm});
            skLineSegment(sketch, "E8168", {"start": v(-154.32, 250.1) * mm, "end": v(-154.32, 246.19) * mm});
            skLineSegment(sketch, "E8169", {"start": v(-154.32, 246.19) * mm, "end": v(-162.03, 246.19) * mm});
            skLineSegment(sketch, "E8170", {"start": v(-242.1, 217.56) * mm, "end": v(-235.89, 240.74) * mm});
            skLineSegment(sketch, "E8171", {"start": v(-235.89, 240.74) * mm, "end": v(-240.34, 241.94) * mm});
            skLineSegment(sketch, "E8172", {"start": v(-240.34, 241.94) * mm, "end": v(-238.8, 247.74) * mm});
            skLineSegment(sketch, "E8173", {"start": v(-238.8, 247.74) * mm, "end": v(-222.32, 243.32) * mm});
            skLineSegment(sketch, "E8174", {"start": v(-222.32, 243.32) * mm, "end": v(-223.88, 237.53) * mm});
            skLineSegment(sketch, "E8175", {"start": v(-223.88, 237.53) * mm, "end": v(-228.35, 238.73) * mm});
            skLineSegment(sketch, "E8176", {"start": v(-228.35, 238.73) * mm, "end": v(-234.56, 215.55) * mm});
            skLineSegment(sketch, "E8177", {"start": v(-234.56, 215.55) * mm, "end": v(-242.1, 217.56) * mm});
            skLineSegment(sketch, "E8178", {"start": v(-252.18, 242.29) * mm, "end": v(-252.18, 246.2) * mm});
            skLineSegment(sketch, "E8179", {"start": v(-252.18, 246.2) * mm, "end": v(-244.47, 246.2) * mm});
            skLineSegment(sketch, "E8180", {"start": v(-244.47, 246.2) * mm, "end": v(-244.47, 242.29) * mm});
            skLineSegment(sketch, "E8181", {"start": v(-244.47, 242.29) * mm, "end": v(-252.18, 242.29) * mm});
            skLineSegment(sketch, "E8182", {"start": v(-181.72, 216.6) * mm, "end": v(-181.72, 244.69) * mm});
            skLineSegment(sketch, "E8183", {"start": v(-181.72, 244.69) * mm, "end": v(-174.1, 244.69) * mm});
            skLineSegment(sketch, "E8184", {"start": v(-174.1, 244.69) * mm, "end": v(-174.24, 242.51) * mm});
            skLineSegment(sketch, "E8185", {"start": v(-174.24, 242.51) * mm, "end": v(-173.19, 243.66) * mm});
            skLineSegment(sketch, "E8186", {"start": v(-173.19, 243.66) * mm, "end": v(-172.03, 244.48) * mm});
            skLineSegment(sketch, "E8187", {"start": v(-172.03, 244.48) * mm, "end": v(-170.77, 244.97) * mm});
            skLineSegment(sketch, "E8188", {"start": v(-170.77, 244.97) * mm, "end": v(-169.4, 245.13) * mm});
            skLineSegment(sketch, "E8189", {"start": v(-169.4, 245.13) * mm, "end": v(-167.78, 244.9) * mm});
            skLineSegment(sketch, "E8190", {"start": v(-167.78, 244.9) * mm, "end": v(-166.4, 244.2) * mm});
            skLineSegment(sketch, "E8191", {"start": v(-166.4, 244.2) * mm, "end": v(-165.36, 243.19) * mm});
            skLineSegment(sketch, "E8192", {"start": v(-165.36, 243.19) * mm, "end": v(-164.8, 242.04) * mm});
            skLineSegment(sketch, "E8193", {"start": v(-164.8, 242.04) * mm, "end": v(-164.5, 237.89) * mm});
            skLineSegment(sketch, "E8194", {"start": v(-164.5, 237.89) * mm, "end": v(-164.5, 227.53) * mm});
            skLineSegment(sketch, "E8195", {"start": v(-164.5, 227.53) * mm, "end": v(-164.6, 224.66) * mm});
            skLineSegment(sketch, "E8196", {"start": v(-164.6, 224.66) * mm, "end": v(-164.89, 222.76) * mm});
            skLineSegment(sketch, "E8197", {"start": v(-164.89, 222.76) * mm, "end": v(-165.5, 221.48) * mm});
            skLineSegment(sketch, "E8198", {"start": v(-165.5, 221.48) * mm, "end": v(-166.52, 220.5) * mm});
            skLineSegment(sketch, "E8199", {"start": v(-166.52, 220.5) * mm, "end": v(-167.88, 219.86) * mm});
            skLineSegment(sketch, "E8200", {"start": v(-167.88, 219.86) * mm, "end": v(-169.5, 219.65) * mm});
            skLineSegment(sketch, "E8201", {"start": v(-169.5, 219.65) * mm, "end": v(-170.83, 219.81) * mm});
            skLineSegment(sketch, "E8202", {"start": v(-170.83, 219.81) * mm, "end": v(-172.07, 220.3) * mm});
            skLineSegment(sketch, "E8203", {"start": v(-172.07, 220.3) * mm, "end": v(-173.2, 221.1) * mm});
            skLineSegment(sketch, "E8204", {"start": v(-173.2, 221.1) * mm, "end": v(-174.24, 222.23) * mm});
            skLineSegment(sketch, "E8205", {"start": v(-174.24, 222.23) * mm, "end": v(-174.24, 216.6) * mm});
            skLineSegment(sketch, "E8206", {"start": v(-174.24, 216.6) * mm, "end": v(-181.72, 216.6) * mm});
            skLineSegment(sketch, "E8207", {"start": v(-172.47, 225.23) * mm, "end": v(-172.15, 225.62) * mm});
            skLineSegment(sketch, "E8208", {"start": v(-172.15, 225.62) * mm, "end": v(-172, 227.75) * mm});
            skLineSegment(sketch, "E8209", {"start": v(-172, 227.75) * mm, "end": v(-172, 236.82) * mm});
            skLineSegment(sketch, "E8210", {"start": v(-172, 236.82) * mm, "end": v(-172.14, 239.2) * mm});
            skLineSegment(sketch, "E8211", {"start": v(-172.14, 239.2) * mm, "end": v(-172.46, 239.56) * mm});
            skLineSegment(sketch, "E8212", {"start": v(-172.46, 239.56) * mm, "end": v(-173.07, 239.68) * mm});
            skLineSegment(sketch, "E8213", {"start": v(-173.07, 239.68) * mm, "end": v(-173.68, 239.54) * mm});
            skLineSegment(sketch, "E8214", {"start": v(-173.68, 239.54) * mm, "end": v(-174.02, 239.12) * mm});
            skLineSegment(sketch, "E8215", {"start": v(-174.02, 239.12) * mm, "end": v(-174.2, 236.81) * mm});
            skLineSegment(sketch, "E8216", {"start": v(-174.2, 236.81) * mm, "end": v(-174.2, 228.05) * mm});
            skLineSegment(sketch, "E8217", {"start": v(-174.2, 228.05) * mm, "end": v(-174.02, 225.66) * mm});
            skLineSegment(sketch, "E8218", {"start": v(-174.02, 225.66) * mm, "end": v(-173.66, 225.25) * mm});
            skLineSegment(sketch, "E8219", {"start": v(-173.66, 225.25) * mm, "end": v(-173.05, 225.1) * mm});
            skLineSegment(sketch, "E8220", {"start": v(-173.05, 225.1) * mm, "end": v(-172.47, 225.23) * mm});
            skLineSegment(sketch, "E8221", {"start": v(-145.28, 219.82) * mm, "end": v(-147.24, 220.34) * mm});
            skLineSegment(sketch, "E8222", {"start": v(-147.24, 220.34) * mm, "end": v(-148.85, 221.15) * mm});
            skLineSegment(sketch, "E8223", {"start": v(-148.85, 221.15) * mm, "end": v(-150.06, 222.22) * mm});
            skLineSegment(sketch, "E8224", {"start": v(-150.06, 222.22) * mm, "end": v(-150.92, 223.47) * mm});
            skLineSegment(sketch, "E8225", {"start": v(-150.92, 223.47) * mm, "end": v(-151.46, 224.85) * mm});
            skLineSegment(sketch, "E8226", {"start": v(-151.46, 224.85) * mm, "end": v(-151.76, 226.61) * mm});
            skLineSegment(sketch, "E8227", {"start": v(-151.76, 226.61) * mm, "end": v(-151.85, 229.03) * mm});
            skLineSegment(sketch, "E8228", {"start": v(-151.85, 229.03) * mm, "end": v(-151.85, 236.2) * mm});
            skLineSegment(sketch, "E8229", {"start": v(-151.85, 236.2) * mm, "end": v(-151.64, 239.08) * mm});
            skLineSegment(sketch, "E8230", {"start": v(-151.64, 239.08) * mm, "end": v(-150.98, 241.29) * mm});
            skLineSegment(sketch, "E8231", {"start": v(-150.98, 241.29) * mm, "end": v(-149.83, 242.93) * mm});
            skLineSegment(sketch, "E8232", {"start": v(-149.83, 242.93) * mm, "end": v(-148.13, 244.14) * mm});
            skLineSegment(sketch, "E8233", {"start": v(-148.13, 244.14) * mm, "end": v(-146, 244.88) * mm});
            skLineSegment(sketch, "E8234", {"start": v(-146, 244.88) * mm, "end": v(-143.57, 245.13) * mm});
            skLineSegment(sketch, "E8235", {"start": v(-143.57, 245.13) * mm, "end": v(-140.7, 244.83) * mm});
            skLineSegment(sketch, "E8236", {"start": v(-140.7, 244.83) * mm, "end": v(-138.37, 243.94) * mm});
            skLineSegment(sketch, "E8237", {"start": v(-138.37, 243.94) * mm, "end": v(-136.63, 242.55) * mm});
            skLineSegment(sketch, "E8238", {"start": v(-136.63, 242.55) * mm, "end": v(-135.5, 240.77) * mm});
            skLineSegment(sketch, "E8239", {"start": v(-135.5, 240.77) * mm, "end": v(-134.88, 238.4) * mm});
            skLineSegment(sketch, "E8240", {"start": v(-134.88, 238.4) * mm, "end": v(-134.68, 235.22) * mm});
            skLineSegment(sketch, "E8241", {"start": v(-134.68, 235.22) * mm, "end": v(-134.68, 231.96) * mm});
            skLineSegment(sketch, "E8242", {"start": v(-134.68, 231.96) * mm, "end": v(-144.37, 231.96) * mm});
            skLineSegment(sketch, "E8243", {"start": v(-144.37, 231.96) * mm, "end": v(-144.37, 226.64) * mm});
            skLineSegment(sketch, "E8244", {"start": v(-144.37, 226.64) * mm, "end": v(-144.13, 224.49) * mm});
            skLineSegment(sketch, "E8245", {"start": v(-144.13, 224.49) * mm, "end": v(-143.77, 224.13) * mm});
            skLineSegment(sketch, "E8246", {"start": v(-143.77, 224.13) * mm, "end": v(-143.2, 224) * mm});
            skLineSegment(sketch, "E8247", {"start": v(-143.2, 224) * mm, "end": v(-142.49, 224.17) * mm});
            skLineSegment(sketch, "E8248", {"start": v(-142.49, 224.17) * mm, "end": v(-142.06, 224.65) * mm});
            skLineSegment(sketch, "E8249", {"start": v(-142.06, 224.65) * mm, "end": v(-141.77, 227.12) * mm});
            skLineSegment(sketch, "E8250", {"start": v(-141.77, 227.12) * mm, "end": v(-141.77, 230.36) * mm});
            skLineSegment(sketch, "E8251", {"start": v(-141.77, 230.36) * mm, "end": v(-134.68, 230.36) * mm});
            skLineSegment(sketch, "E8252", {"start": v(-134.68, 230.36) * mm, "end": v(-134.68, 228.55) * mm});
            skLineSegment(sketch, "E8253", {"start": v(-134.68, 228.55) * mm, "end": v(-134.96, 225.04) * mm});
            skLineSegment(sketch, "E8254", {"start": v(-134.96, 225.04) * mm, "end": v(-135.44, 223.78) * mm});
            skLineSegment(sketch, "E8255", {"start": v(-135.44, 223.78) * mm, "end": v(-136.3, 222.43) * mm});
            skLineSegment(sketch, "E8256", {"start": v(-136.3, 222.43) * mm, "end": v(-137.5, 221.22) * mm});
            skLineSegment(sketch, "E8257", {"start": v(-137.5, 221.22) * mm, "end": v(-138.98, 220.35) * mm});
            skLineSegment(sketch, "E8258", {"start": v(-138.98, 220.35) * mm, "end": v(-140.81, 219.83) * mm});
            skLineSegment(sketch, "E8259", {"start": v(-140.81, 219.83) * mm, "end": v(-143.05, 219.65) * mm});
            skLineSegment(sketch, "E8260", {"start": v(-143.05, 219.65) * mm, "end": v(-145.28, 219.82) * mm});
            skLineSegment(sketch, "E8261", {"start": v(-142.18, 237.76) * mm, "end": v(-142.38, 240.22) * mm});
            skLineSegment(sketch, "E8262", {"start": v(-142.38, 240.22) * mm, "end": v(-142.7, 240.64) * mm});
            skLineSegment(sketch, "E8263", {"start": v(-142.7, 240.64) * mm, "end": v(-143.22, 240.78) * mm});
            skLineSegment(sketch, "E8264", {"start": v(-143.22, 240.78) * mm, "end": v(-143.85, 240.66) * mm});
            skLineSegment(sketch, "E8265", {"start": v(-143.85, 240.66) * mm, "end": v(-144.18, 240.3) * mm});
            skLineSegment(sketch, "E8266", {"start": v(-144.18, 240.3) * mm, "end": v(-144.37, 237.76) * mm});
            skLineSegment(sketch, "E8267", {"start": v(-144.37, 237.76) * mm, "end": v(-144.37, 235.96) * mm});
            skLineSegment(sketch, "E8268", {"start": v(-144.37, 235.96) * mm, "end": v(-142.18, 235.96) * mm});
            skLineSegment(sketch, "E8269", {"start": v(-142.18, 235.96) * mm, "end": v(-142.18, 237.76) * mm});
            skLineSegment(sketch, "E8270", {"start": v(-162.03, 220.1) * mm, "end": v(-162.03, 244.69) * mm});
            skLineSegment(sketch, "E8271", {"start": v(-162.03, 244.69) * mm, "end": v(-154.32, 244.69) * mm});
            skLineSegment(sketch, "E8272", {"start": v(-154.32, 244.69) * mm, "end": v(-154.32, 220.1) * mm});
            skLineSegment(sketch, "E8273", {"start": v(-154.32, 220.1) * mm, "end": v(-162.03, 220.1) * mm});
            skLineSegment(sketch, "E8274", {"start": v(-252.18, 216.2) * mm, "end": v(-252.18, 240.79) * mm});
            skLineSegment(sketch, "E8275", {"start": v(-252.18, 240.79) * mm, "end": v(-244.47, 240.79) * mm});
            skLineSegment(sketch, "E8276", {"start": v(-244.47, 240.79) * mm, "end": v(-244.47, 216.2) * mm});
            skLineSegment(sketch, "E8277", {"start": v(-244.47, 216.2) * mm, "end": v(-252.18, 216.2) * mm});
            skLineSegment(sketch, "E8278", {"start": v(-378, 183) * mm, "end": v(-378, 203) * mm});
            skLineSegment(sketch, "E8279", {"start": v(-378, 203) * mm, "end": v(-362, 203) * mm});
            skLineSegment(sketch, "E8280", {"start": v(-362, 203) * mm, "end": v(-362, 183) * mm});
            skLineSegment(sketch, "E8281", {"start": v(-362, 183) * mm, "end": v(-378, 183) * mm});
            skLineSegment(sketch, "E8282", {"start": v(-48, 183) * mm, "end": v(-48, 203) * mm});
            skLineSegment(sketch, "E8283", {"start": v(-48, 203) * mm, "end": v(-32, 203) * mm});
            skLineSegment(sketch, "E8284", {"start": v(-32, 203) * mm, "end": v(-32, 183) * mm});
            skLineSegment(sketch, "E8285", {"start": v(-32, 183) * mm, "end": v(-48, 183) * mm});
            skLineSegment(sketch, "E8286", {"start": v(-40.13, 121) * mm, "end": v(-40.37, 121.03) * mm});
            skLineSegment(sketch, "E8287", {"start": v(-40.37, 121.03) * mm, "end": v(-40.62, 121.1) * mm});
            skLineSegment(sketch, "E8288", {"start": v(-40.62, 121.1) * mm, "end": v(-40.85, 121.2) * mm});
            skLineSegment(sketch, "E8289", {"start": v(-40.85, 121.2) * mm, "end": v(-41.07, 121.31) * mm});
            skLineSegment(sketch, "E8290", {"start": v(-41.07, 121.31) * mm, "end": v(-41.27, 121.46) * mm});
            skLineSegment(sketch, "E8291", {"start": v(-41.27, 121.46) * mm, "end": v(-41.46, 121.63) * mm});
            skLineSegment(sketch, "E8292", {"start": v(-41.46, 121.63) * mm, "end": v(-41.62, 121.82) * mm});
            skLineSegment(sketch, "E8293", {"start": v(-41.62, 121.82) * mm, "end": v(-41.75, 122.04) * mm});
            skLineSegment(sketch, "E8294", {"start": v(-41.75, 122.04) * mm, "end": v(-41.86, 122.26) * mm});
            skLineSegment(sketch, "E8295", {"start": v(-41.86, 122.26) * mm, "end": v(-41.94, 122.5) * mm});
            skLineSegment(sketch, "E8296", {"start": v(-41.94, 122.5) * mm, "end": v(-41.98, 122.75) * mm});
            skLineSegment(sketch, "E8297", {"start": v(-41.98, 122.75) * mm, "end": v(-42, 123) * mm});
            skLineSegment(sketch, "E8298", {"start": v(-42, 123) * mm, "end": v(-41.98, 123.25) * mm});
            skLineSegment(sketch, "E8299", {"start": v(-41.98, 123.25) * mm, "end": v(-41.94, 123.5) * mm});
            skLineSegment(sketch, "E8300", {"start": v(-41.94, 123.5) * mm, "end": v(-41.86, 123.74) * mm});
            skLineSegment(sketch, "E8301", {"start": v(-41.86, 123.74) * mm, "end": v(-41.75, 123.96) * mm});
            skLineSegment(sketch, "E8302", {"start": v(-41.75, 123.96) * mm, "end": v(-41.62, 124.18) * mm});
            skLineSegment(sketch, "E8303", {"start": v(-41.62, 124.18) * mm, "end": v(-41.46, 124.37) * mm});
            skLineSegment(sketch, "E8304", {"start": v(-41.46, 124.37) * mm, "end": v(-41.27, 124.54) * mm});
            skLineSegment(sketch, "E8305", {"start": v(-41.27, 124.54) * mm, "end": v(-41.07, 124.69) * mm});
            skLineSegment(sketch, "E8306", {"start": v(-41.07, 124.69) * mm, "end": v(-40.85, 124.81) * mm});
            skLineSegment(sketch, "E8307", {"start": v(-40.85, 124.81) * mm, "end": v(-40.62, 124.9) * mm});
            skLineSegment(sketch, "E8308", {"start": v(-40.62, 124.9) * mm, "end": v(-40.37, 124.97) * mm});
            skLineSegment(sketch, "E8309", {"start": v(-40.37, 124.97) * mm, "end": v(-40.13, 125) * mm});
            skLineSegment(sketch, "E8310", {"start": v(-40.13, 125) * mm, "end": v(-39.87, 125) * mm});
            skLineSegment(sketch, "E8311", {"start": v(-39.87, 125) * mm, "end": v(-39.63, 124.97) * mm});
            skLineSegment(sketch, "E8312", {"start": v(-39.63, 124.97) * mm, "end": v(-39.38, 124.9) * mm});
            skLineSegment(sketch, "E8313", {"start": v(-39.38, 124.9) * mm, "end": v(-39.15, 124.81) * mm});
            skLineSegment(sketch, "E8314", {"start": v(-39.15, 124.81) * mm, "end": v(-38.93, 124.69) * mm});
            skLineSegment(sketch, "E8315", {"start": v(-38.93, 124.69) * mm, "end": v(-38.73, 124.54) * mm});
            skLineSegment(sketch, "E8316", {"start": v(-38.73, 124.54) * mm, "end": v(-38.54, 124.37) * mm});
            skLineSegment(sketch, "E8317", {"start": v(-38.54, 124.37) * mm, "end": v(-38.38, 124.18) * mm});
            skLineSegment(sketch, "E8318", {"start": v(-38.38, 124.18) * mm, "end": v(-38.25, 123.96) * mm});
            skLineSegment(sketch, "E8319", {"start": v(-38.25, 123.96) * mm, "end": v(-38.14, 123.74) * mm});
            skLineSegment(sketch, "E8320", {"start": v(-38.14, 123.74) * mm, "end": v(-38.06, 123.5) * mm});
            skLineSegment(sketch, "E8321", {"start": v(-38.06, 123.5) * mm, "end": v(-38.02, 123.25) * mm});
            skLineSegment(sketch, "E8322", {"start": v(-38.02, 123.25) * mm, "end": v(-38, 123) * mm});
            skLineSegment(sketch, "E8323", {"start": v(-38, 123) * mm, "end": v(-38.02, 122.75) * mm});
            skLineSegment(sketch, "E8324", {"start": v(-38.02, 122.75) * mm, "end": v(-38.06, 122.5) * mm});
            skLineSegment(sketch, "E8325", {"start": v(-38.06, 122.5) * mm, "end": v(-38.14, 122.26) * mm});
            skLineSegment(sketch, "E8326", {"start": v(-38.14, 122.26) * mm, "end": v(-38.25, 122.04) * mm});
            skLineSegment(sketch, "E8327", {"start": v(-38.25, 122.04) * mm, "end": v(-38.38, 121.82) * mm});
            skLineSegment(sketch, "E8328", {"start": v(-38.38, 121.82) * mm, "end": v(-38.54, 121.63) * mm});
            skLineSegment(sketch, "E8329", {"start": v(-38.54, 121.63) * mm, "end": v(-38.73, 121.46) * mm});
            skLineSegment(sketch, "E8330", {"start": v(-38.73, 121.46) * mm, "end": v(-38.93, 121.31) * mm});
            skLineSegment(sketch, "E8331", {"start": v(-38.93, 121.31) * mm, "end": v(-39.15, 121.2) * mm});
            skLineSegment(sketch, "E8332", {"start": v(-39.15, 121.2) * mm, "end": v(-39.38, 121.1) * mm});
            skLineSegment(sketch, "E8333", {"start": v(-39.38, 121.1) * mm, "end": v(-39.63, 121.03) * mm});
            skLineSegment(sketch, "E8334", {"start": v(-39.63, 121.03) * mm, "end": v(-39.87, 121) * mm});
            skLineSegment(sketch, "E8335", {"start": v(-39.87, 121) * mm, "end": v(-40.13, 121) * mm});
            skLineSegment(sketch, "E8336", {"start": v(-370.13, 121) * mm, "end": v(-370.38, 121.03) * mm});
            skLineSegment(sketch, "E8337", {"start": v(-370.38, 121.03) * mm, "end": v(-370.62, 121.1) * mm});
            skLineSegment(sketch, "E8338", {"start": v(-370.62, 121.1) * mm, "end": v(-370.85, 121.2) * mm});
            skLineSegment(sketch, "E8339", {"start": v(-370.85, 121.2) * mm, "end": v(-371.07, 121.31) * mm});
            skLineSegment(sketch, "E8340", {"start": v(-371.07, 121.31) * mm, "end": v(-371.27, 121.46) * mm});
            skLineSegment(sketch, "E8341", {"start": v(-371.27, 121.46) * mm, "end": v(-371.46, 121.63) * mm});
            skLineSegment(sketch, "E8342", {"start": v(-371.46, 121.63) * mm, "end": v(-371.62, 121.82) * mm});
            skLineSegment(sketch, "E8343", {"start": v(-371.62, 121.82) * mm, "end": v(-371.75, 122.04) * mm});
            skLineSegment(sketch, "E8344", {"start": v(-371.75, 122.04) * mm, "end": v(-371.86, 122.26) * mm});
            skLineSegment(sketch, "E8345", {"start": v(-371.86, 122.26) * mm, "end": v(-371.94, 122.5) * mm});
            skLineSegment(sketch, "E8346", {"start": v(-371.94, 122.5) * mm, "end": v(-371.98, 122.75) * mm});
            skLineSegment(sketch, "E8347", {"start": v(-371.98, 122.75) * mm, "end": v(-372, 123) * mm});
            skLineSegment(sketch, "E8348", {"start": v(-372, 123) * mm, "end": v(-371.98, 123.25) * mm});
            skLineSegment(sketch, "E8349", {"start": v(-371.98, 123.25) * mm, "end": v(-371.94, 123.5) * mm});
            skLineSegment(sketch, "E8350", {"start": v(-371.94, 123.5) * mm, "end": v(-371.86, 123.74) * mm});
            skLineSegment(sketch, "E8351", {"start": v(-371.86, 123.74) * mm, "end": v(-371.75, 123.96) * mm});
            skLineSegment(sketch, "E8352", {"start": v(-371.75, 123.96) * mm, "end": v(-371.62, 124.18) * mm});
            skLineSegment(sketch, "E8353", {"start": v(-371.62, 124.18) * mm, "end": v(-371.46, 124.37) * mm});
            skLineSegment(sketch, "E8354", {"start": v(-371.46, 124.37) * mm, "end": v(-371.27, 124.54) * mm});
            skLineSegment(sketch, "E8355", {"start": v(-371.27, 124.54) * mm, "end": v(-371.07, 124.69) * mm});
            skLineSegment(sketch, "E8356", {"start": v(-371.07, 124.69) * mm, "end": v(-370.85, 124.81) * mm});
            skLineSegment(sketch, "E8357", {"start": v(-370.85, 124.81) * mm, "end": v(-370.62, 124.9) * mm});
            skLineSegment(sketch, "E8358", {"start": v(-370.62, 124.9) * mm, "end": v(-370.38, 124.97) * mm});
            skLineSegment(sketch, "E8359", {"start": v(-370.38, 124.97) * mm, "end": v(-370.13, 125) * mm});
            skLineSegment(sketch, "E8360", {"start": v(-370.13, 125) * mm, "end": v(-369.87, 125) * mm});
            skLineSegment(sketch, "E8361", {"start": v(-369.87, 125) * mm, "end": v(-369.62, 124.97) * mm});
            skLineSegment(sketch, "E8362", {"start": v(-369.62, 124.97) * mm, "end": v(-369.38, 124.9) * mm});
            skLineSegment(sketch, "E8363", {"start": v(-369.38, 124.9) * mm, "end": v(-369.15, 124.81) * mm});
            skLineSegment(sketch, "E8364", {"start": v(-369.15, 124.81) * mm, "end": v(-368.93, 124.69) * mm});
            skLineSegment(sketch, "E8365", {"start": v(-368.93, 124.69) * mm, "end": v(-368.73, 124.54) * mm});
            skLineSegment(sketch, "E8366", {"start": v(-368.73, 124.54) * mm, "end": v(-368.54, 124.37) * mm});
            skLineSegment(sketch, "E8367", {"start": v(-368.54, 124.37) * mm, "end": v(-368.38, 124.18) * mm});
            skLineSegment(sketch, "E8368", {"start": v(-368.38, 124.18) * mm, "end": v(-368.25, 123.96) * mm});
            skLineSegment(sketch, "E8369", {"start": v(-368.25, 123.96) * mm, "end": v(-368.14, 123.74) * mm});
            skLineSegment(sketch, "E8370", {"start": v(-368.14, 123.74) * mm, "end": v(-368.06, 123.5) * mm});
            skLineSegment(sketch, "E8371", {"start": v(-368.06, 123.5) * mm, "end": v(-368.02, 123.25) * mm});
            skLineSegment(sketch, "E8372", {"start": v(-368.02, 123.25) * mm, "end": v(-368, 123) * mm});
            skLineSegment(sketch, "E8373", {"start": v(-368, 123) * mm, "end": v(-368.02, 122.75) * mm});
            skLineSegment(sketch, "E8374", {"start": v(-368.02, 122.75) * mm, "end": v(-368.06, 122.5) * mm});
            skLineSegment(sketch, "E8375", {"start": v(-368.06, 122.5) * mm, "end": v(-368.14, 122.26) * mm});
            skLineSegment(sketch, "E8376", {"start": v(-368.14, 122.26) * mm, "end": v(-368.25, 122.04) * mm});
            skLineSegment(sketch, "E8377", {"start": v(-368.25, 122.04) * mm, "end": v(-368.38, 121.82) * mm});
            skLineSegment(sketch, "E8378", {"start": v(-368.38, 121.82) * mm, "end": v(-368.54, 121.63) * mm});
            skLineSegment(sketch, "E8379", {"start": v(-368.54, 121.63) * mm, "end": v(-368.73, 121.46) * mm});
            skLineSegment(sketch, "E8380", {"start": v(-368.73, 121.46) * mm, "end": v(-368.93, 121.31) * mm});
            skLineSegment(sketch, "E8381", {"start": v(-368.93, 121.31) * mm, "end": v(-369.15, 121.2) * mm});
            skLineSegment(sketch, "E8382", {"start": v(-369.15, 121.2) * mm, "end": v(-369.38, 121.1) * mm});
            skLineSegment(sketch, "E8383", {"start": v(-369.38, 121.1) * mm, "end": v(-369.62, 121.03) * mm});
            skLineSegment(sketch, "E8384", {"start": v(-369.62, 121.03) * mm, "end": v(-369.87, 121) * mm});
            skLineSegment(sketch, "E8385", {"start": v(-369.87, 121) * mm, "end": v(-370.13, 121) * mm});
            skLineSegment(sketch, "E8386", {"start": v(-378, 43) * mm, "end": v(-378, 63) * mm});
            skLineSegment(sketch, "E8387", {"start": v(-378, 63) * mm, "end": v(-362, 63) * mm});
            skLineSegment(sketch, "E8388", {"start": v(-362, 63) * mm, "end": v(-362, 43) * mm});
            skLineSegment(sketch, "E8389", {"start": v(-362, 43) * mm, "end": v(-378, 43) * mm});
            skLineSegment(sketch, "E8390", {"start": v(-48, 43) * mm, "end": v(-48, 63) * mm});
            skLineSegment(sketch, "E8391", {"start": v(-48, 63) * mm, "end": v(-32, 63) * mm});
            skLineSegment(sketch, "E8392", {"start": v(-32, 63) * mm, "end": v(-32, 43) * mm});
            skLineSegment(sketch, "E8393", {"start": v(-32, 43) * mm, "end": v(-48, 43) * mm});
            skLineSegment(sketch, "E8394", {"start": v(-40.13, -19) * mm, "end": v(-40.37, -18.96) * mm});
            skLineSegment(sketch, "E8395", {"start": v(-40.37, -18.96) * mm, "end": v(-40.62, -18.9) * mm});
            skLineSegment(sketch, "E8396", {"start": v(-40.62, -18.9) * mm, "end": v(-40.85, -18.8) * mm});
            skLineSegment(sketch, "E8397", {"start": v(-40.85, -18.8) * mm, "end": v(-41.07, -18.69) * mm});
            skLineSegment(sketch, "E8398", {"start": v(-41.07, -18.69) * mm, "end": v(-41.27, -18.54) * mm});
            skLineSegment(sketch, "E8399", {"start": v(-41.27, -18.54) * mm, "end": v(-41.46, -18.37) * mm});
            skLineSegment(sketch, "E8400", {"start": v(-41.46, -18.37) * mm, "end": v(-41.62, -18.18) * mm});
            skLineSegment(sketch, "E8401", {"start": v(-41.62, -18.18) * mm, "end": v(-41.75, -17.96) * mm});
            skLineSegment(sketch, "E8402", {"start": v(-41.75, -17.96) * mm, "end": v(-41.86, -17.74) * mm});
            skLineSegment(sketch, "E8403", {"start": v(-41.86, -17.74) * mm, "end": v(-41.94, -17.5) * mm});
            skLineSegment(sketch, "E8404", {"start": v(-41.94, -17.5) * mm, "end": v(-41.98, -17.25) * mm});
            skLineSegment(sketch, "E8405", {"start": v(-41.98, -17.25) * mm, "end": v(-42, -17) * mm});
            skLineSegment(sketch, "E8406", {"start": v(-42, -17) * mm, "end": v(-41.98, -16.75) * mm});
            skLineSegment(sketch, "E8407", {"start": v(-41.98, -16.75) * mm, "end": v(-41.94, -16.5) * mm});
            skLineSegment(sketch, "E8408", {"start": v(-41.94, -16.5) * mm, "end": v(-41.86, -16.26) * mm});
            skLineSegment(sketch, "E8409", {"start": v(-41.86, -16.26) * mm, "end": v(-41.75, -16.04) * mm});
            skLineSegment(sketch, "E8410", {"start": v(-41.75, -16.04) * mm, "end": v(-41.62, -15.82) * mm});
            skLineSegment(sketch, "E8411", {"start": v(-41.62, -15.82) * mm, "end": v(-41.46, -15.63) * mm});
            skLineSegment(sketch, "E8412", {"start": v(-41.46, -15.63) * mm, "end": v(-41.27, -15.46) * mm});
            skLineSegment(sketch, "E8413", {"start": v(-41.27, -15.46) * mm, "end": v(-41.07, -15.31) * mm});
            skLineSegment(sketch, "E8414", {"start": v(-41.07, -15.31) * mm, "end": v(-40.85, -15.2) * mm});
            skLineSegment(sketch, "E8415", {"start": v(-40.85, -15.2) * mm, "end": v(-40.62, -15.1) * mm});
            skLineSegment(sketch, "E8416", {"start": v(-40.62, -15.1) * mm, "end": v(-40.37, -15.04) * mm});
            skLineSegment(sketch, "E8417", {"start": v(-40.37, -15.04) * mm, "end": v(-40.13, -15) * mm});
            skLineSegment(sketch, "E8418", {"start": v(-40.13, -15) * mm, "end": v(-39.87, -15) * mm});
            skLineSegment(sketch, "E8419", {"start": v(-39.87, -15) * mm, "end": v(-39.63, -15.04) * mm});
            skLineSegment(sketch, "E8420", {"start": v(-39.63, -15.04) * mm, "end": v(-39.38, -15.1) * mm});
            skLineSegment(sketch, "E8421", {"start": v(-39.38, -15.1) * mm, "end": v(-39.15, -15.2) * mm});
            skLineSegment(sketch, "E8422", {"start": v(-39.15, -15.2) * mm, "end": v(-38.93, -15.31) * mm});
            skLineSegment(sketch, "E8423", {"start": v(-38.93, -15.31) * mm, "end": v(-38.73, -15.46) * mm});
            skLineSegment(sketch, "E8424", {"start": v(-38.73, -15.46) * mm, "end": v(-38.54, -15.63) * mm});
            skLineSegment(sketch, "E8425", {"start": v(-38.54, -15.63) * mm, "end": v(-38.38, -15.82) * mm});
            skLineSegment(sketch, "E8426", {"start": v(-38.38, -15.82) * mm, "end": v(-38.25, -16.04) * mm});
            skLineSegment(sketch, "E8427", {"start": v(-38.25, -16.04) * mm, "end": v(-38.14, -16.26) * mm});
            skLineSegment(sketch, "E8428", {"start": v(-38.14, -16.26) * mm, "end": v(-38.06, -16.5) * mm});
            skLineSegment(sketch, "E8429", {"start": v(-38.06, -16.5) * mm, "end": v(-38.02, -16.75) * mm});
            skLineSegment(sketch, "E8430", {"start": v(-38.02, -16.75) * mm, "end": v(-38, -17) * mm});
            skLineSegment(sketch, "E8431", {"start": v(-38, -17) * mm, "end": v(-38.02, -17.25) * mm});
            skLineSegment(sketch, "E8432", {"start": v(-38.02, -17.25) * mm, "end": v(-38.06, -17.5) * mm});
            skLineSegment(sketch, "E8433", {"start": v(-38.06, -17.5) * mm, "end": v(-38.14, -17.74) * mm});
            skLineSegment(sketch, "E8434", {"start": v(-38.14, -17.74) * mm, "end": v(-38.25, -17.96) * mm});
            skLineSegment(sketch, "E8435", {"start": v(-38.25, -17.96) * mm, "end": v(-38.38, -18.18) * mm});
            skLineSegment(sketch, "E8436", {"start": v(-38.38, -18.18) * mm, "end": v(-38.54, -18.37) * mm});
            skLineSegment(sketch, "E8437", {"start": v(-38.54, -18.37) * mm, "end": v(-38.73, -18.54) * mm});
            skLineSegment(sketch, "E8438", {"start": v(-38.73, -18.54) * mm, "end": v(-38.93, -18.69) * mm});
            skLineSegment(sketch, "E8439", {"start": v(-38.93, -18.69) * mm, "end": v(-39.15, -18.8) * mm});
            skLineSegment(sketch, "E8440", {"start": v(-39.15, -18.8) * mm, "end": v(-39.38, -18.9) * mm});
            skLineSegment(sketch, "E8441", {"start": v(-39.38, -18.9) * mm, "end": v(-39.63, -18.96) * mm});
            skLineSegment(sketch, "E8442", {"start": v(-39.63, -18.96) * mm, "end": v(-39.87, -19) * mm});
            skLineSegment(sketch, "E8443", {"start": v(-39.87, -19) * mm, "end": v(-40.13, -19) * mm});
            skLineSegment(sketch, "E8444", {"start": v(-370.13, -19) * mm, "end": v(-370.38, -18.96) * mm});
            skLineSegment(sketch, "E8445", {"start": v(-370.38, -18.96) * mm, "end": v(-370.62, -18.9) * mm});
            skLineSegment(sketch, "E8446", {"start": v(-370.62, -18.9) * mm, "end": v(-370.85, -18.8) * mm});
            skLineSegment(sketch, "E8447", {"start": v(-370.85, -18.8) * mm, "end": v(-371.07, -18.69) * mm});
            skLineSegment(sketch, "E8448", {"start": v(-371.07, -18.69) * mm, "end": v(-371.27, -18.54) * mm});
            skLineSegment(sketch, "E8449", {"start": v(-371.27, -18.54) * mm, "end": v(-371.46, -18.37) * mm});
            skLineSegment(sketch, "E8450", {"start": v(-371.46, -18.37) * mm, "end": v(-371.62, -18.18) * mm});
            skLineSegment(sketch, "E8451", {"start": v(-371.62, -18.18) * mm, "end": v(-371.75, -17.96) * mm});
            skLineSegment(sketch, "E8452", {"start": v(-371.75, -17.96) * mm, "end": v(-371.86, -17.74) * mm});
            skLineSegment(sketch, "E8453", {"start": v(-371.86, -17.74) * mm, "end": v(-371.94, -17.5) * mm});
            skLineSegment(sketch, "E8454", {"start": v(-371.94, -17.5) * mm, "end": v(-371.98, -17.25) * mm});
            skLineSegment(sketch, "E8455", {"start": v(-371.98, -17.25) * mm, "end": v(-372, -17) * mm});
            skLineSegment(sketch, "E8456", {"start": v(-372, -17) * mm, "end": v(-371.98, -16.75) * mm});
            skLineSegment(sketch, "E8457", {"start": v(-371.98, -16.75) * mm, "end": v(-371.94, -16.5) * mm});
            skLineSegment(sketch, "E8458", {"start": v(-371.94, -16.5) * mm, "end": v(-371.86, -16.26) * mm});
            skLineSegment(sketch, "E8459", {"start": v(-371.86, -16.26) * mm, "end": v(-371.75, -16.04) * mm});
            skLineSegment(sketch, "E8460", {"start": v(-371.75, -16.04) * mm, "end": v(-371.62, -15.82) * mm});
            skLineSegment(sketch, "E8461", {"start": v(-371.62, -15.82) * mm, "end": v(-371.46, -15.63) * mm});
            skLineSegment(sketch, "E8462", {"start": v(-371.46, -15.63) * mm, "end": v(-371.27, -15.46) * mm});
            skLineSegment(sketch, "E8463", {"start": v(-371.27, -15.46) * mm, "end": v(-371.07, -15.31) * mm});
            skLineSegment(sketch, "E8464", {"start": v(-371.07, -15.31) * mm, "end": v(-370.85, -15.2) * mm});
            skLineSegment(sketch, "E8465", {"start": v(-370.85, -15.2) * mm, "end": v(-370.62, -15.1) * mm});
            skLineSegment(sketch, "E8466", {"start": v(-370.62, -15.1) * mm, "end": v(-370.38, -15.04) * mm});
            skLineSegment(sketch, "E8467", {"start": v(-370.38, -15.04) * mm, "end": v(-370.13, -15) * mm});
            skLineSegment(sketch, "E8468", {"start": v(-370.13, -15) * mm, "end": v(-369.87, -15) * mm});
            skLineSegment(sketch, "E8469", {"start": v(-369.87, -15) * mm, "end": v(-369.62, -15.04) * mm});
            skLineSegment(sketch, "E8470", {"start": v(-369.62, -15.04) * mm, "end": v(-369.38, -15.1) * mm});
            skLineSegment(sketch, "E8471", {"start": v(-369.38, -15.1) * mm, "end": v(-369.15, -15.2) * mm});
            skLineSegment(sketch, "E8472", {"start": v(-369.15, -15.2) * mm, "end": v(-368.93, -15.31) * mm});
            skLineSegment(sketch, "E8473", {"start": v(-368.93, -15.31) * mm, "end": v(-368.73, -15.46) * mm});
            skLineSegment(sketch, "E8474", {"start": v(-368.73, -15.46) * mm, "end": v(-368.54, -15.63) * mm});
            skLineSegment(sketch, "E8475", {"start": v(-368.54, -15.63) * mm, "end": v(-368.38, -15.82) * mm});
            skLineSegment(sketch, "E8476", {"start": v(-368.38, -15.82) * mm, "end": v(-368.25, -16.04) * mm});
            skLineSegment(sketch, "E8477", {"start": v(-368.25, -16.04) * mm, "end": v(-368.14, -16.26) * mm});
            skLineSegment(sketch, "E8478", {"start": v(-368.14, -16.26) * mm, "end": v(-368.06, -16.5) * mm});
            skLineSegment(sketch, "E8479", {"start": v(-368.06, -16.5) * mm, "end": v(-368.02, -16.75) * mm});
            skLineSegment(sketch, "E8480", {"start": v(-368.02, -16.75) * mm, "end": v(-368, -17) * mm});
            skLineSegment(sketch, "E8481", {"start": v(-368, -17) * mm, "end": v(-368.02, -17.25) * mm});
            skLineSegment(sketch, "E8482", {"start": v(-368.02, -17.25) * mm, "end": v(-368.06, -17.5) * mm});
            skLineSegment(sketch, "E8483", {"start": v(-368.06, -17.5) * mm, "end": v(-368.14, -17.74) * mm});
            skLineSegment(sketch, "E8484", {"start": v(-368.14, -17.74) * mm, "end": v(-368.25, -17.96) * mm});
            skLineSegment(sketch, "E8485", {"start": v(-368.25, -17.96) * mm, "end": v(-368.38, -18.18) * mm});
            skLineSegment(sketch, "E8486", {"start": v(-368.38, -18.18) * mm, "end": v(-368.54, -18.37) * mm});
            skLineSegment(sketch, "E8487", {"start": v(-368.54, -18.37) * mm, "end": v(-368.73, -18.54) * mm});
            skLineSegment(sketch, "E8488", {"start": v(-368.73, -18.54) * mm, "end": v(-368.93, -18.69) * mm});
            skLineSegment(sketch, "E8489", {"start": v(-368.93, -18.69) * mm, "end": v(-369.15, -18.8) * mm});
            skLineSegment(sketch, "E8490", {"start": v(-369.15, -18.8) * mm, "end": v(-369.38, -18.9) * mm});
            skLineSegment(sketch, "E8491", {"start": v(-369.38, -18.9) * mm, "end": v(-369.62, -18.96) * mm});
            skLineSegment(sketch, "E8492", {"start": v(-369.62, -18.96) * mm, "end": v(-369.87, -19) * mm});
            skLineSegment(sketch, "E8493", {"start": v(-369.87, -19) * mm, "end": v(-370.13, -19) * mm});
            skLineSegment(sketch, "E8494", {"start": v(-48, -97) * mm, "end": v(-48, -77) * mm});
            skLineSegment(sketch, "E8495", {"start": v(-48, -77) * mm, "end": v(-32, -77) * mm});
            skLineSegment(sketch, "E8496", {"start": v(-32, -77) * mm, "end": v(-32, -97) * mm});
            skLineSegment(sketch, "E8497", {"start": v(-32, -97) * mm, "end": v(-48, -97) * mm});
            skLineSegment(sketch, "E8498", {"start": v(-378, -97) * mm, "end": v(-378, -77) * mm});
            skLineSegment(sketch, "E8499", {"start": v(-378, -77) * mm, "end": v(-362, -77) * mm});
            skLineSegment(sketch, "E8500", {"start": v(-362, -77) * mm, "end": v(-362, -97) * mm});
            skLineSegment(sketch, "E8501", {"start": v(-362, -97) * mm, "end": v(-378, -97) * mm});
            skLineSegment(sketch, "E8502", {"start": v(-234, -146) * mm, "end": v(-171, -146) * mm});
            skLineSegment(sketch, "E8503", {"start": v(-171, -146) * mm, "end": v(-222.99, 14) * mm});
            skLineSegment(sketch, "E8504", {"start": v(-222.99, 14) * mm, "end": v(-223, 14) * mm});
            skLineSegment(sketch, "E8505", {"start": v(-223, 14) * mm, "end": v(-272.94, 167.68) * mm});
            skLineSegment(sketch, "E8506", {"start": v(-272.94, 167.68) * mm, "end": v(-273.48, 168.82) * mm});
            skLineSegment(sketch, "E8507", {"start": v(-273.48, 168.82) * mm, "end": v(-274.15, 169.88) * mm});
            skLineSegment(sketch, "E8508", {"start": v(-274.15, 169.88) * mm, "end": v(-274.95, 170.84) * mm});
            skLineSegment(sketch, "E8509", {"start": v(-274.95, 170.84) * mm, "end": v(-275.87, 171.7) * mm});
            skLineSegment(sketch, "E8510", {"start": v(-275.87, 171.7) * mm, "end": v(-276.88, 172.44) * mm});
            skLineSegment(sketch, "E8511", {"start": v(-276.88, 172.44) * mm, "end": v(-277.98, 173.05) * mm});
            skLineSegment(sketch, "E8512", {"start": v(-277.98, 173.05) * mm, "end": v(-279.15, 173.51) * mm});
            skLineSegment(sketch, "E8513", {"start": v(-279.15, 173.51) * mm, "end": v(-280.37, 173.82) * mm});
            skLineSegment(sketch, "E8514", {"start": v(-280.37, 173.82) * mm, "end": v(-281.61, 173.98) * mm});
            skLineSegment(sketch, "E8515", {"start": v(-281.61, 173.98) * mm, "end": v(-299, 173.98) * mm});
            skLineSegment(sketch, "E8516", {"start": v(-299, 173.98) * mm, "end": v(-299, 174) * mm});
            skLineSegment(sketch, "E8517", {"start": v(-299, 174) * mm, "end": v(-325, 174) * mm});
            skLineSegment(sketch, "E8518", {"start": v(-325, 174) * mm, "end": v(-325, 154) * mm});
            skLineSegment(sketch, "E8519", {"start": v(-325, 154) * mm, "end": v(-309, 154) * mm});
            skLineSegment(sketch, "E8520", {"start": v(-309, 154) * mm, "end": v(-309, 34) * mm});
            skLineSegment(sketch, "E8521", {"start": v(-309, 34) * mm, "end": v(-325, 34) * mm});
            skLineSegment(sketch, "E8522", {"start": v(-325, 34) * mm, "end": v(-325, 14) * mm});
            skLineSegment(sketch, "E8523", {"start": v(-325, 14) * mm, "end": v(-309, 14) * mm});
            skLineSegment(sketch, "E8524", {"start": v(-309, 14) * mm, "end": v(-309, -106) * mm});
            skLineSegment(sketch, "E8525", {"start": v(-309, -106) * mm, "end": v(-325, -106) * mm});
            skLineSegment(sketch, "E8526", {"start": v(-325, -106) * mm, "end": v(-325, -126) * mm});
            skLineSegment(sketch, "E8527", {"start": v(-325, -126) * mm, "end": v(-309, -126) * mm});
            skLineSegment(sketch, "E8528", {"start": v(-309, -126) * mm, "end": v(-309, -146) * mm});
            skLineSegment(sketch, "E8529", {"start": v(-309, -146) * mm, "end": v(-254, -146) * mm});
            skLineSegment(sketch, "E8530", {"start": v(-254, -146) * mm, "end": v(-254, -162) * mm});
            skLineSegment(sketch, "E8531", {"start": v(-254, -162) * mm, "end": v(-234, -162) * mm});
            skLineSegment(sketch, "E8532", {"start": v(-234, -162) * mm, "end": v(-234, -146) * mm});
            skLineSegment(sketch, "E8533", {"start": v(-85, -142) * mm, "end": v(-101, -142) * mm});
            skLineSegment(sketch, "E8534", {"start": v(-101, -142) * mm, "end": v(-101, -22) * mm});
            skLineSegment(sketch, "E8535", {"start": v(-101, -22) * mm, "end": v(-85, -22) * mm});
            skLineSegment(sketch, "E8536", {"start": v(-85, -22) * mm, "end": v(-85, -2) * mm});
            skLineSegment(sketch, "E8537", {"start": v(-85, -2) * mm, "end": v(-101, -2) * mm});
            skLineSegment(sketch, "E8538", {"start": v(-101, -2) * mm, "end": v(-101, 118) * mm});
            skLineSegment(sketch, "E8539", {"start": v(-101, 118) * mm, "end": v(-85, 118) * mm});
            skLineSegment(sketch, "E8540", {"start": v(-85, 118) * mm, "end": v(-85, 138) * mm});
            skLineSegment(sketch, "E8541", {"start": v(-85, 138) * mm, "end": v(-101, 138) * mm});
            skLineSegment(sketch, "E8542", {"start": v(-101, 138) * mm, "end": v(-101, 158) * mm});
            skLineSegment(sketch, "E8543", {"start": v(-101, 158) * mm, "end": v(-156, 158) * mm});
            skLineSegment(sketch, "E8544", {"start": v(-156, 158) * mm, "end": v(-156, 174) * mm});
            skLineSegment(sketch, "E8545", {"start": v(-156, 174) * mm, "end": v(-176, 174) * mm});
            skLineSegment(sketch, "E8546", {"start": v(-176, 174) * mm, "end": v(-176, 158) * mm});
            skLineSegment(sketch, "E8547", {"start": v(-176, 158) * mm, "end": v(-239, 158) * mm});
            skLineSegment(sketch, "E8548", {"start": v(-239, 158) * mm, "end": v(-187.01, -2) * mm});
            skLineSegment(sketch, "E8549", {"start": v(-187.01, -2) * mm, "end": v(-187, -2) * mm});
            skLineSegment(sketch, "E8550", {"start": v(-187, -2) * mm, "end": v(-137.06, -155.68) * mm});
            skLineSegment(sketch, "E8551", {"start": v(-137.06, -155.68) * mm, "end": v(-136.52, -156.82) * mm});
            skLineSegment(sketch, "E8552", {"start": v(-136.52, -156.82) * mm, "end": v(-135.85, -157.88) * mm});
            skLineSegment(sketch, "E8553", {"start": v(-135.85, -157.88) * mm, "end": v(-135.05, -158.85) * mm});
            skLineSegment(sketch, "E8554", {"start": v(-135.05, -158.85) * mm, "end": v(-134.13, -159.7) * mm});
            skLineSegment(sketch, "E8555", {"start": v(-134.13, -159.7) * mm, "end": v(-133.12, -160.44) * mm});
            skLineSegment(sketch, "E8556", {"start": v(-133.12, -160.44) * mm, "end": v(-132.02, -161.05) * mm});
            skLineSegment(sketch, "E8557", {"start": v(-132.02, -161.05) * mm, "end": v(-130.85, -161.51) * mm});
            skLineSegment(sketch, "E8558", {"start": v(-130.85, -161.51) * mm, "end": v(-129.63, -161.82) * mm});
            skLineSegment(sketch, "E8559", {"start": v(-129.63, -161.82) * mm, "end": v(-128.39, -161.98) * mm});
            skLineSegment(sketch, "E8560", {"start": v(-128.39, -161.98) * mm, "end": v(-111, -161.98) * mm});
            skLineSegment(sketch, "E8561", {"start": v(-111, -161.98) * mm, "end": v(-111, -162) * mm});
            skLineSegment(sketch, "E8562", {"start": v(-111, -162) * mm, "end": v(-85, -162) * mm});
            skLineSegment(sketch, "E8563", {"start": v(-85, -162) * mm, "end": v(-85, -142) * mm});
            skLineSegment(sketch, "E8564", {"start": v(40, -262.98) * mm, "end": v(40.63, -262.98) * mm});
            skLineSegment(sketch, "E8565", {"start": v(40.63, -262.98) * mm, "end": v(41.87, -262.82) * mm});
            skLineSegment(sketch, "E8566", {"start": v(41.87, -262.82) * mm, "end": v(43.1, -262.51) * mm});
            skLineSegment(sketch, "E8567", {"start": v(43.1, -262.51) * mm, "end": v(44.26, -262.05) * mm});
            skLineSegment(sketch, "E8568", {"start": v(44.26, -262.05) * mm, "end": v(45.36, -261.44) * mm});
            skLineSegment(sketch, "E8569", {"start": v(45.36, -261.44) * mm, "end": v(46.37, -260.7) * mm});
            skLineSegment(sketch, "E8570", {"start": v(46.37, -260.7) * mm, "end": v(47.29, -259.85) * mm});
            skLineSegment(sketch, "E8571", {"start": v(47.29, -259.85) * mm, "end": v(48.1, -258.88) * mm});
            skLineSegment(sketch, "E8572", {"start": v(48.1, -258.88) * mm, "end": v(48.76, -257.82) * mm});
            skLineSegment(sketch, "E8573", {"start": v(48.76, -257.82) * mm, "end": v(49.3, -256.68) * mm});
            skLineSegment(sketch, "E8574", {"start": v(49.3, -256.68) * mm, "end": v(49.69, -255.49) * mm});
            skLineSegment(sketch, "E8575", {"start": v(49.69, -255.49) * mm, "end": v(49.92, -254.25) * mm});
            skLineSegment(sketch, "E8576", {"start": v(49.92, -254.25) * mm, "end": v(50, -253) * mm});
            skLineSegment(sketch, "E8577", {"start": v(50, -253) * mm, "end": v(50.02, -253) * mm});
            skLineSegment(sketch, "E8578", {"start": v(50.02, -253) * mm, "end": v(50.02, -252.37) * mm});
            skLineSegment(sketch, "E8579", {"start": v(50.02, -252.37) * mm, "end": v(50.18, -251.13) * mm});
            skLineSegment(sketch, "E8580", {"start": v(50.18, -251.13) * mm, "end": v(50.49, -249.9) * mm});
            skLineSegment(sketch, "E8581", {"start": v(50.49, -249.9) * mm, "end": v(50.95, -248.74) * mm});
            skLineSegment(sketch, "E8582", {"start": v(50.95, -248.74) * mm, "end": v(51.56, -247.64) * mm});
            skLineSegment(sketch, "E8583", {"start": v(51.56, -247.64) * mm, "end": v(52.3, -246.63) * mm});
            skLineSegment(sketch, "E8584", {"start": v(52.3, -246.63) * mm, "end": v(53.15, -245.71) * mm});
            skLineSegment(sketch, "E8585", {"start": v(53.15, -245.71) * mm, "end": v(54.12, -244.9) * mm});
            skLineSegment(sketch, "E8586", {"start": v(54.12, -244.9) * mm, "end": v(55.18, -244.24) * mm});
            skLineSegment(sketch, "E8587", {"start": v(55.18, -244.24) * mm, "end": v(56.32, -243.7) * mm});
            skLineSegment(sketch, "E8588", {"start": v(56.32, -243.7) * mm, "end": v(57.51, -243.31) * mm});
            skLineSegment(sketch, "E8589", {"start": v(57.51, -243.31) * mm, "end": v(58.75, -243.08) * mm});
            skLineSegment(sketch, "E8590", {"start": v(58.75, -243.08) * mm, "end": v(60, -243) * mm});
            skLineSegment(sketch, "E8591", {"start": v(60, -243) * mm, "end": v(350, -243) * mm});
            skLineSegment(sketch, "E8592", {"start": v(350, -243) * mm, "end": v(350, -243.02) * mm});
            skLineSegment(sketch, "E8593", {"start": v(350, -243.02) * mm, "end": v(350.63, -243.02) * mm});
            skLineSegment(sketch, "E8594", {"start": v(350.63, -243.02) * mm, "end": v(351.87, -243.18) * mm});
            skLineSegment(sketch, "E8595", {"start": v(351.87, -243.18) * mm, "end": v(353.09, -243.49) * mm});
            skLineSegment(sketch, "E8596", {"start": v(353.09, -243.49) * mm, "end": v(354.26, -243.95) * mm});
            skLineSegment(sketch, "E8597", {"start": v(354.26, -243.95) * mm, "end": v(355.36, -244.56) * mm});
            skLineSegment(sketch, "E8598", {"start": v(355.36, -244.56) * mm, "end": v(356.37, -245.3) * mm});
            skLineSegment(sketch, "E8599", {"start": v(356.37, -245.3) * mm, "end": v(357.3, -246.15) * mm});
            skLineSegment(sketch, "E8600", {"start": v(357.3, -246.15) * mm, "end": v(358.09, -247.12) * mm});
            skLineSegment(sketch, "E8601", {"start": v(358.09, -247.12) * mm, "end": v(358.76, -248.18) * mm});
            skLineSegment(sketch, "E8602", {"start": v(358.76, -248.18) * mm, "end": v(359.3, -249.32) * mm});
            skLineSegment(sketch, "E8603", {"start": v(359.3, -249.32) * mm, "end": v(359.69, -250.51) * mm});
            skLineSegment(sketch, "E8604", {"start": v(359.69, -250.51) * mm, "end": v(359.92, -251.75) * mm});
            skLineSegment(sketch, "E8605", {"start": v(359.92, -251.75) * mm, "end": v(360.08, -254.25) * mm});
            skLineSegment(sketch, "E8606", {"start": v(360.08, -254.25) * mm, "end": v(360.31, -255.49) * mm});
            skLineSegment(sketch, "E8607", {"start": v(360.31, -255.49) * mm, "end": v(360.7, -256.68) * mm});
            skLineSegment(sketch, "E8608", {"start": v(360.7, -256.68) * mm, "end": v(361.24, -257.82) * mm});
            skLineSegment(sketch, "E8609", {"start": v(361.24, -257.82) * mm, "end": v(361.91, -258.88) * mm});
            skLineSegment(sketch, "E8610", {"start": v(361.91, -258.88) * mm, "end": v(362.7, -259.85) * mm});
            skLineSegment(sketch, "E8611", {"start": v(362.7, -259.85) * mm, "end": v(363.63, -260.7) * mm});
            skLineSegment(sketch, "E8612", {"start": v(363.63, -260.7) * mm, "end": v(364.64, -261.44) * mm});
            skLineSegment(sketch, "E8613", {"start": v(364.64, -261.44) * mm, "end": v(365.74, -262.05) * mm});
            skLineSegment(sketch, "E8614", {"start": v(365.74, -262.05) * mm, "end": v(366.91, -262.51) * mm});
            skLineSegment(sketch, "E8615", {"start": v(366.91, -262.51) * mm, "end": v(368.13, -262.82) * mm});
            skLineSegment(sketch, "E8616", {"start": v(368.13, -262.82) * mm, "end": v(369.37, -262.98) * mm});
            skLineSegment(sketch, "E8617", {"start": v(369.37, -262.98) * mm, "end": v(370, -262.98) * mm});
            skLineSegment(sketch, "E8618", {"start": v(370, -262.98) * mm, "end": v(370, -263) * mm});
            skLineSegment(sketch, "E8619", {"start": v(370, -263) * mm, "end": v(390, -263) * mm});
            skLineSegment(sketch, "E8620", {"start": v(390, -263) * mm, "end": v(391.25, -262.92) * mm});
            skLineSegment(sketch, "E8621", {"start": v(391.25, -262.92) * mm, "end": v(392.49, -262.69) * mm});
            skLineSegment(sketch, "E8622", {"start": v(392.49, -262.69) * mm, "end": v(393.68, -262.3) * mm});
            skLineSegment(sketch, "E8623", {"start": v(393.68, -262.3) * mm, "end": v(394.82, -261.76) * mm});
            skLineSegment(sketch, "E8624", {"start": v(394.82, -261.76) * mm, "end": v(395.88, -261.1) * mm});
            skLineSegment(sketch, "E8625", {"start": v(395.88, -261.1) * mm, "end": v(396.85, -260.29) * mm});
            skLineSegment(sketch, "E8626", {"start": v(396.85, -260.29) * mm, "end": v(397.7, -259.37) * mm});
            skLineSegment(sketch, "E8627", {"start": v(397.7, -259.37) * mm, "end": v(398.44, -258.36) * mm});
            skLineSegment(sketch, "E8628", {"start": v(398.44, -258.36) * mm, "end": v(399.05, -257.26) * mm});
            skLineSegment(sketch, "E8629", {"start": v(399.05, -257.26) * mm, "end": v(399.51, -256.1) * mm});
            skLineSegment(sketch, "E8630", {"start": v(399.51, -256.1) * mm, "end": v(399.82, -254.87) * mm});
            skLineSegment(sketch, "E8631", {"start": v(399.82, -254.87) * mm, "end": v(399.98, -253.63) * mm});
            skLineSegment(sketch, "E8632", {"start": v(399.98, -253.63) * mm, "end": v(399.98, -253) * mm});
            skLineSegment(sketch, "E8633", {"start": v(399.98, -253) * mm, "end": v(400, -253) * mm});
            skLineSegment(sketch, "E8634", {"start": v(400, -253) * mm, "end": v(400, -203) * mm});
            skLineSegment(sketch, "E8635", {"start": v(400, -203) * mm, "end": v(360, -203) * mm});
            skLineSegment(sketch, "E8636", {"start": v(360, -203) * mm, "end": v(360, -187) * mm});
            skLineSegment(sketch, "E8637", {"start": v(360, -187) * mm, "end": v(340, -187) * mm});
            skLineSegment(sketch, "E8638", {"start": v(340, -187) * mm, "end": v(340, -203) * mm});
            skLineSegment(sketch, "E8639", {"start": v(340, -203) * mm, "end": v(215, -203) * mm});
            skLineSegment(sketch, "E8640", {"start": v(215, -203) * mm, "end": v(215, -187) * mm});
            skLineSegment(sketch, "E8641", {"start": v(215, -187) * mm, "end": v(195, -187) * mm});
            skLineSegment(sketch, "E8642", {"start": v(195, -187) * mm, "end": v(195, -203) * mm});
            skLineSegment(sketch, "E8643", {"start": v(195, -203) * mm, "end": v(70, -203) * mm});
            skLineSegment(sketch, "E8644", {"start": v(70, -203) * mm, "end": v(70, -187) * mm});
            skLineSegment(sketch, "E8645", {"start": v(70, -187) * mm, "end": v(50, -187) * mm});
            skLineSegment(sketch, "E8646", {"start": v(50, -187) * mm, "end": v(50, -203) * mm});
            skLineSegment(sketch, "E8647", {"start": v(50, -203) * mm, "end": v(10, -203) * mm});
            skLineSegment(sketch, "E8648", {"start": v(10, -203) * mm, "end": v(10, -253) * mm});
            skLineSegment(sketch, "E8649", {"start": v(10, -253) * mm, "end": v(10.08, -254.25) * mm});
            skLineSegment(sketch, "E8650", {"start": v(10.08, -254.25) * mm, "end": v(10.31, -255.49) * mm});
            skLineSegment(sketch, "E8651", {"start": v(10.31, -255.49) * mm, "end": v(10.7, -256.68) * mm});
            skLineSegment(sketch, "E8652", {"start": v(10.7, -256.68) * mm, "end": v(11.24, -257.82) * mm});
            skLineSegment(sketch, "E8653", {"start": v(11.24, -257.82) * mm, "end": v(11.9, -258.88) * mm});
            skLineSegment(sketch, "E8654", {"start": v(11.9, -258.88) * mm, "end": v(12.71, -259.85) * mm});
            skLineSegment(sketch, "E8655", {"start": v(12.71, -259.85) * mm, "end": v(13.63, -260.7) * mm});
            skLineSegment(sketch, "E8656", {"start": v(13.63, -260.7) * mm, "end": v(14.64, -261.44) * mm});
            skLineSegment(sketch, "E8657", {"start": v(14.64, -261.44) * mm, "end": v(15.74, -262.05) * mm});
            skLineSegment(sketch, "E8658", {"start": v(15.74, -262.05) * mm, "end": v(16.9, -262.51) * mm});
            skLineSegment(sketch, "E8659", {"start": v(16.9, -262.51) * mm, "end": v(18.13, -262.82) * mm});
            skLineSegment(sketch, "E8660", {"start": v(18.13, -262.82) * mm, "end": v(19.37, -262.98) * mm});
            skLineSegment(sketch, "E8661", {"start": v(19.37, -262.98) * mm, "end": v(20, -262.98) * mm});
            skLineSegment(sketch, "E8662", {"start": v(20, -262.98) * mm, "end": v(20, -263) * mm});
            skLineSegment(sketch, "E8663", {"start": v(20, -263) * mm, "end": v(40, -263) * mm});
            skLineSegment(sketch, "E8664", {"start": v(40, -263) * mm, "end": v(40, -262.98) * mm});
            skLineSegment(sketch, "E8665", {"start": v(-370, -262.98) * mm, "end": v(-369.37, -262.98) * mm});
            skLineSegment(sketch, "E8666", {"start": v(-369.37, -262.98) * mm, "end": v(-368.13, -262.82) * mm});
            skLineSegment(sketch, "E8667", {"start": v(-368.13, -262.82) * mm, "end": v(-366.91, -262.51) * mm});
            skLineSegment(sketch, "E8668", {"start": v(-366.91, -262.51) * mm, "end": v(-365.74, -262.05) * mm});
            skLineSegment(sketch, "E8669", {"start": v(-365.74, -262.05) * mm, "end": v(-364.64, -261.44) * mm});
            skLineSegment(sketch, "E8670", {"start": v(-364.64, -261.44) * mm, "end": v(-363.63, -260.7) * mm});
            skLineSegment(sketch, "E8671", {"start": v(-363.63, -260.7) * mm, "end": v(-362.7, -259.85) * mm});
            skLineSegment(sketch, "E8672", {"start": v(-362.7, -259.85) * mm, "end": v(-361.91, -258.88) * mm});
            skLineSegment(sketch, "E8673", {"start": v(-361.91, -258.88) * mm, "end": v(-361.24, -257.82) * mm});
            skLineSegment(sketch, "E8674", {"start": v(-361.24, -257.82) * mm, "end": v(-360.7, -256.68) * mm});
            skLineSegment(sketch, "E8675", {"start": v(-360.7, -256.68) * mm, "end": v(-360.31, -255.49) * mm});
            skLineSegment(sketch, "E8676", {"start": v(-360.31, -255.49) * mm, "end": v(-360.08, -254.25) * mm});
            skLineSegment(sketch, "E8677", {"start": v(-360.08, -254.25) * mm, "end": v(-360, -253) * mm});
            skLineSegment(sketch, "E8678", {"start": v(-360, -253) * mm, "end": v(-359.98, -253) * mm});
            skLineSegment(sketch, "E8679", {"start": v(-359.98, -253) * mm, "end": v(-359.98, -252.37) * mm});
            skLineSegment(sketch, "E8680", {"start": v(-359.98, -252.37) * mm, "end": v(-359.82, -251.13) * mm});
            skLineSegment(sketch, "E8681", {"start": v(-359.82, -251.13) * mm, "end": v(-359.51, -249.9) * mm});
            skLineSegment(sketch, "E8682", {"start": v(-359.51, -249.9) * mm, "end": v(-359.05, -248.74) * mm});
            skLineSegment(sketch, "E8683", {"start": v(-359.05, -248.74) * mm, "end": v(-358.44, -247.64) * mm});
            skLineSegment(sketch, "E8684", {"start": v(-358.44, -247.64) * mm, "end": v(-357.7, -246.63) * mm});
            skLineSegment(sketch, "E8685", {"start": v(-357.7, -246.63) * mm, "end": v(-356.85, -245.71) * mm});
            skLineSegment(sketch, "E8686", {"start": v(-356.85, -245.71) * mm, "end": v(-355.88, -244.9) * mm});
            skLineSegment(sketch, "E8687", {"start": v(-355.88, -244.9) * mm, "end": v(-354.82, -244.24) * mm});
            skLineSegment(sketch, "E8688", {"start": v(-354.82, -244.24) * mm, "end": v(-353.68, -243.7) * mm});
            skLineSegment(sketch, "E8689", {"start": v(-353.68, -243.7) * mm, "end": v(-352.49, -243.31) * mm});
            skLineSegment(sketch, "E8690", {"start": v(-352.49, -243.31) * mm, "end": v(-351.25, -243.08) * mm});
            skLineSegment(sketch, "E8691", {"start": v(-351.25, -243.08) * mm, "end": v(-350, -243) * mm});
            skLineSegment(sketch, "E8692", {"start": v(-350, -243) * mm, "end": v(-60, -243) * mm});
            skLineSegment(sketch, "E8693", {"start": v(-60, -243) * mm, "end": v(-60, -243.02) * mm});
            skLineSegment(sketch, "E8694", {"start": v(-60, -243.02) * mm, "end": v(-59.37, -243.02) * mm});
            skLineSegment(sketch, "E8695", {"start": v(-59.37, -243.02) * mm, "end": v(-58.13, -243.18) * mm});
            skLineSegment(sketch, "E8696", {"start": v(-58.13, -243.18) * mm, "end": v(-56.9, -243.49) * mm});
            skLineSegment(sketch, "E8697", {"start": v(-56.9, -243.49) * mm, "end": v(-55.74, -243.95) * mm});
            skLineSegment(sketch, "E8698", {"start": v(-55.74, -243.95) * mm, "end": v(-54.64, -244.56) * mm});
            skLineSegment(sketch, "E8699", {"start": v(-54.64, -244.56) * mm, "end": v(-53.63, -245.3) * mm});
            skLineSegment(sketch, "E8700", {"start": v(-53.63, -245.3) * mm, "end": v(-52.71, -246.15) * mm});
            skLineSegment(sketch, "E8701", {"start": v(-52.71, -246.15) * mm, "end": v(-51.9, -247.12) * mm});
            skLineSegment(sketch, "E8702", {"start": v(-51.9, -247.12) * mm, "end": v(-51.24, -248.18) * mm});
            skLineSegment(sketch, "E8703", {"start": v(-51.24, -248.18) * mm, "end": v(-50.7, -249.32) * mm});
            skLineSegment(sketch, "E8704", {"start": v(-50.7, -249.32) * mm, "end": v(-50.31, -250.51) * mm});
            skLineSegment(sketch, "E8705", {"start": v(-50.31, -250.51) * mm, "end": v(-50.08, -251.75) * mm});
            skLineSegment(sketch, "E8706", {"start": v(-50.08, -251.75) * mm, "end": v(-49.92, -254.25) * mm});
            skLineSegment(sketch, "E8707", {"start": v(-49.92, -254.25) * mm, "end": v(-49.69, -255.49) * mm});
            skLineSegment(sketch, "E8708", {"start": v(-49.69, -255.49) * mm, "end": v(-49.3, -256.68) * mm});
            skLineSegment(sketch, "E8709", {"start": v(-49.3, -256.68) * mm, "end": v(-48.76, -257.82) * mm});
            skLineSegment(sketch, "E8710", {"start": v(-48.76, -257.82) * mm, "end": v(-48.1, -258.88) * mm});
            skLineSegment(sketch, "E8711", {"start": v(-48.1, -258.88) * mm, "end": v(-47.29, -259.85) * mm});
            skLineSegment(sketch, "E8712", {"start": v(-47.29, -259.85) * mm, "end": v(-46.37, -260.7) * mm});
            skLineSegment(sketch, "E8713", {"start": v(-46.37, -260.7) * mm, "end": v(-45.36, -261.44) * mm});
            skLineSegment(sketch, "E8714", {"start": v(-45.36, -261.44) * mm, "end": v(-44.26, -262.05) * mm});
            skLineSegment(sketch, "E8715", {"start": v(-44.26, -262.05) * mm, "end": v(-43.1, -262.51) * mm});
            skLineSegment(sketch, "E8716", {"start": v(-43.1, -262.51) * mm, "end": v(-41.87, -262.82) * mm});
            skLineSegment(sketch, "E8717", {"start": v(-41.87, -262.82) * mm, "end": v(-40.63, -262.98) * mm});
            skLineSegment(sketch, "E8718", {"start": v(-40.63, -262.98) * mm, "end": v(-40, -262.98) * mm});
            skLineSegment(sketch, "E8719", {"start": v(-40, -262.98) * mm, "end": v(-40, -263) * mm});
            skLineSegment(sketch, "E8720", {"start": v(-40, -263) * mm, "end": v(-20, -263) * mm});
            skLineSegment(sketch, "E8721", {"start": v(-20, -263) * mm, "end": v(-18.75, -262.92) * mm});
            skLineSegment(sketch, "E8722", {"start": v(-18.75, -262.92) * mm, "end": v(-17.51, -262.69) * mm});
            skLineSegment(sketch, "E8723", {"start": v(-17.51, -262.69) * mm, "end": v(-16.32, -262.3) * mm});
            skLineSegment(sketch, "E8724", {"start": v(-16.32, -262.3) * mm, "end": v(-15.18, -261.76) * mm});
            skLineSegment(sketch, "E8725", {"start": v(-15.18, -261.76) * mm, "end": v(-14.12, -261.1) * mm});
            skLineSegment(sketch, "E8726", {"start": v(-14.12, -261.1) * mm, "end": v(-13.15, -260.29) * mm});
            skLineSegment(sketch, "E8727", {"start": v(-13.15, -260.29) * mm, "end": v(-12.3, -259.37) * mm});
            skLineSegment(sketch, "E8728", {"start": v(-12.3, -259.37) * mm, "end": v(-11.56, -258.36) * mm});
            skLineSegment(sketch, "E8729", {"start": v(-11.56, -258.36) * mm, "end": v(-10.95, -257.26) * mm});
            skLineSegment(sketch, "E8730", {"start": v(-10.95, -257.26) * mm, "end": v(-10.49, -256.1) * mm});
            skLineSegment(sketch, "E8731", {"start": v(-10.49, -256.1) * mm, "end": v(-10.18, -254.87) * mm});
            skLineSegment(sketch, "E8732", {"start": v(-10.18, -254.87) * mm, "end": v(-10.02, -253.63) * mm});
            skLineSegment(sketch, "E8733", {"start": v(-10.02, -253.63) * mm, "end": v(-10.02, -253) * mm});
            skLineSegment(sketch, "E8734", {"start": v(-10.02, -253) * mm, "end": v(-10, -253) * mm});
            skLineSegment(sketch, "E8735", {"start": v(-10, -253) * mm, "end": v(-10, -203) * mm});
            skLineSegment(sketch, "E8736", {"start": v(-10, -203) * mm, "end": v(-50, -203) * mm});
            skLineSegment(sketch, "E8737", {"start": v(-50, -203) * mm, "end": v(-50, -187) * mm});
            skLineSegment(sketch, "E8738", {"start": v(-50, -187) * mm, "end": v(-70, -187) * mm});
            skLineSegment(sketch, "E8739", {"start": v(-70, -187) * mm, "end": v(-70, -203) * mm});
            skLineSegment(sketch, "E8740", {"start": v(-70, -203) * mm, "end": v(-195, -203) * mm});
            skLineSegment(sketch, "E8741", {"start": v(-195, -203) * mm, "end": v(-195, -187) * mm});
            skLineSegment(sketch, "E8742", {"start": v(-195, -187) * mm, "end": v(-215, -187) * mm});
            skLineSegment(sketch, "E8743", {"start": v(-215, -187) * mm, "end": v(-215, -203) * mm});
            skLineSegment(sketch, "E8744", {"start": v(-215, -203) * mm, "end": v(-340, -203) * mm});
            skLineSegment(sketch, "E8745", {"start": v(-340, -203) * mm, "end": v(-340, -187) * mm});
            skLineSegment(sketch, "E8746", {"start": v(-340, -187) * mm, "end": v(-360, -187) * mm});
            skLineSegment(sketch, "E8747", {"start": v(-360, -187) * mm, "end": v(-360, -203) * mm});
            skLineSegment(sketch, "E8748", {"start": v(-360, -203) * mm, "end": v(-400, -203) * mm});
            skLineSegment(sketch, "E8749", {"start": v(-400, -203) * mm, "end": v(-400, -253) * mm});
            skLineSegment(sketch, "E8750", {"start": v(-400, -253) * mm, "end": v(-399.92, -254.25) * mm});
            skLineSegment(sketch, "E8751", {"start": v(-399.92, -254.25) * mm, "end": v(-399.69, -255.49) * mm});
            skLineSegment(sketch, "E8752", {"start": v(-399.69, -255.49) * mm, "end": v(-399.3, -256.68) * mm});
            skLineSegment(sketch, "E8753", {"start": v(-399.3, -256.68) * mm, "end": v(-398.76, -257.82) * mm});
            skLineSegment(sketch, "E8754", {"start": v(-398.76, -257.82) * mm, "end": v(-398.09, -258.88) * mm});
            skLineSegment(sketch, "E8755", {"start": v(-398.09, -258.88) * mm, "end": v(-397.3, -259.85) * mm});
            skLineSegment(sketch, "E8756", {"start": v(-397.3, -259.85) * mm, "end": v(-396.37, -260.7) * mm});
            skLineSegment(sketch, "E8757", {"start": v(-396.37, -260.7) * mm, "end": v(-395.36, -261.44) * mm});
            skLineSegment(sketch, "E8758", {"start": v(-395.36, -261.44) * mm, "end": v(-394.26, -262.05) * mm});
            skLineSegment(sketch, "E8759", {"start": v(-394.26, -262.05) * mm, "end": v(-393.09, -262.51) * mm});
            skLineSegment(sketch, "E8760", {"start": v(-393.09, -262.51) * mm, "end": v(-391.87, -262.82) * mm});
            skLineSegment(sketch, "E8761", {"start": v(-391.87, -262.82) * mm, "end": v(-390.63, -262.98) * mm});
            skLineSegment(sketch, "E8762", {"start": v(-390.63, -262.98) * mm, "end": v(-390, -262.98) * mm});
            skLineSegment(sketch, "E8763", {"start": v(-390, -262.98) * mm, "end": v(-390, -263) * mm});
            skLineSegment(sketch, "E8764", {"start": v(-390, -263) * mm, "end": v(-370, -263) * mm});
            skLineSegment(sketch, "E8765", {"start": v(-370, -263) * mm, "end": v(-370, -262.98) * mm});
            skSolve(sketch);
        }
        {
            var Q0;
            {var subQ3=sQuery(id+"F2.wireOp",EDGE,"E5204");Q0=makeQuery(id+"F2.imprint","IMPRINT",FACE,{"disambiguationData":[TD([[makeQuery(id+"F2.imprint","IMPRINT",EDGE,{"derivedFrom":subQ3}),1.0]])]});}
            extrude(context, id + "F3", {"entities" : qUnion([Q0]), "depth" : 8 * mm});
        }
        {
            var Q0;
            Q0=makeQuery(id+"F1.opExtrude","SWEPT_BODY",BODY,{"disambiguationData":[OSD([sQuery(id+"F0.wireOp",EDGE,"E836"),sQuery(id+"F0.wireOp",EDGE,"E837"),sQuery(id+"F0.wireOp",EDGE,"E838"),sQuery(id+"F0.wireOp",EDGE,"E839"),sQuery(id+"F0.wireOp",EDGE,"E840"),sQuery(id+"F0.wireOp",EDGE,"E841"),sQuery(id+"F0.wireOp",EDGE,"E842"),sQuery(id+"F0.wireOp",EDGE,"E843"),sQuery(id+"F0.wireOp",EDGE,"E844"),sQuery(id+"F0.wireOp",EDGE,"E845"),sQuery(id+"F0.wireOp",EDGE,"E846"),sQuery(id+"F0.wireOp",EDGE,"E847"),sQuery(id+"F0.wireOp",EDGE,"E848"),sQuery(id+"F0.wireOp",EDGE,"E849"),sQuery(id+"F0.wireOp",EDGE,"E850"),sQuery(id+"F0.wireOp",EDGE,"E851"),sQuery(id+"F0.wireOp",EDGE,"E852"),sQuery(id+"F0.wireOp",EDGE,"E853"),sQuery(id+"F0.wireOp",EDGE,"E854"),sQuery(id+"F0.wireOp",EDGE,"E855"),sQuery(id+"F0.wireOp",EDGE,"E856"),sQuery(id+"F0.wireOp",EDGE,"E857"),sQuery(id+"F0.wireOp",EDGE,"E858"),sQuery(id+"F0.wireOp",EDGE,"E859"),sQuery(id+"F0.wireOp",EDGE,"E860"),sQuery(id+"F0.wireOp",EDGE,"E861"),sQuery(id+"F0.wireOp",EDGE,"E862"),sQuery(id+"F0.wireOp",EDGE,"E863"),sQuery(id+"F0.wireOp",EDGE,"E864"),sQuery(id+"F0.wireOp",EDGE,"E865"),sQuery(id+"F0.wireOp",EDGE,"E866"),sQuery(id+"F0.wireOp",EDGE,"E867"),sQuery(id+"F0.wireOp",EDGE,"E868"),sQuery(id+"F0.wireOp",EDGE,"E869"),sQuery(id+"F0.wireOp",EDGE,"E870"),sQuery(id+"F0.wireOp",EDGE,"E871"),sQuery(id+"F0.wireOp",EDGE,"E872"),sQuery(id+"F0.wireOp",EDGE,"E873"),sQuery(id+"F0.wireOp",EDGE,"E874"),sQuery(id+"F0.wireOp",EDGE,"E875"),sQuery(id+"F0.wireOp",EDGE,"E876"),sQuery(id+"F0.wireOp",EDGE,"E877"),sQuery(id+"F0.wireOp",EDGE,"E878"),sQuery(id+"F0.wireOp",EDGE,"E879"),sQuery(id+"F0.wireOp",EDGE,"E880"),sQuery(id+"F0.wireOp",EDGE,"E881"),sQuery(id+"F0.wireOp",EDGE,"E882"),sQuery(id+"F0.wireOp",EDGE,"E883"),sQuery(id+"F0.wireOp",EDGE,"E884"),sQuery(id+"F0.wireOp",EDGE,"E885"),sQuery(id+"F0.wireOp",EDGE,"E886"),sQuery(id+"F0.wireOp",EDGE,"E887"),sQuery(id+"F0.wireOp",EDGE,"E888"),sQuery(id+"F0.wireOp",EDGE,"E889"),sQuery(id+"F0.wireOp",EDGE,"E890"),sQuery(id+"F0.wireOp",EDGE,"E891"),sQuery(id+"F0.wireOp",EDGE,"E892"),sQuery(id+"F0.wireOp",EDGE,"E893"),sQuery(id+"F0.wireOp",EDGE,"E894"),sQuery(id+"F0.wireOp",EDGE,"E895"),sQuery(id+"F0.wireOp",EDGE,"E896"),sQuery(id+"F0.wireOp",EDGE,"E897"),sQuery(id+"F0.wireOp",EDGE,"E898"),sQuery(id+"F0.wireOp",EDGE,"E899"),sQuery(id+"F0.wireOp",EDGE,"E900"),sQuery(id+"F0.wireOp",EDGE,"E901"),sQuery(id+"F0.wireOp",EDGE,"E902"),sQuery(id+"F0.wireOp",EDGE,"E903"),sQuery(id+"F0.wireOp",EDGE,"E904"),sQuery(id+"F0.wireOp",EDGE,"E905"),sQuery(id+"F0.wireOp",EDGE,"E906"),sQuery(id+"F0.wireOp",EDGE,"E907"),sQuery(id+"F0.wireOp",EDGE,"E908"),sQuery(id+"F0.wireOp",EDGE,"E909"),sQuery(id+"F0.wireOp",EDGE,"E910"),sQuery(id+"F0.wireOp",EDGE,"E911"),sQuery(id+"F0.wireOp",EDGE,"E912"),sQuery(id+"F0.wireOp",EDGE,"E913"),sQuery(id+"F0.wireOp",EDGE,"E914"),sQuery(id+"F0.wireOp",EDGE,"E915"),sQuery(id+"F0.wireOp",EDGE,"E916"),sQuery(id+"F0.wireOp",EDGE,"E917"),sQuery(id+"F0.wireOp",EDGE,"E918"),sQuery(id+"F0.wireOp",EDGE,"E919"),sQuery(id+"F0.wireOp",EDGE,"E920"),sQuery(id+"F0.wireOp",EDGE,"E921"),sQuery(id+"F0.wireOp",EDGE,"E922"),sQuery(id+"F0.wireOp",EDGE,"E923"),sQuery(id+"F0.wireOp",EDGE,"E924"),sQuery(id+"F0.wireOp",EDGE,"E925"),sQuery(id+"F0.wireOp",EDGE,"E926"),sQuery(id+"F0.wireOp",EDGE,"E927"),sQuery(id+"F0.wireOp",EDGE,"E928"),sQuery(id+"F0.wireOp",EDGE,"E929"),sQuery(id+"F0.wireOp",EDGE,"E930"),sQuery(id+"F0.wireOp",EDGE,"E931"),sQuery(id+"F0.wireOp",EDGE,"E932"),sQuery(id+"F0.wireOp",EDGE,"E933"),sQuery(id+"F0.wireOp",EDGE,"E934"),sQuery(id+"F0.wireOp",EDGE,"E935"),sQuery(id+"F0.wireOp",EDGE,"E936"),sQuery(id+"F0.wireOp",EDGE,"E937"),sQuery(id+"F0.wireOp",EDGE,"E938"),sQuery(id+"F0.wireOp",EDGE,"E939"),sQuery(id+"F0.wireOp",EDGE,"E940"),sQuery(id+"F0.wireOp",EDGE,"E941"),sQuery(id+"F0.wireOp",EDGE,"E942"),sQuery(id+"F0.wireOp",EDGE,"E943"),sQuery(id+"F0.wireOp",EDGE,"E944"),sQuery(id+"F0.wireOp",EDGE,"E945"),sQuery(id+"F0.wireOp",EDGE,"E946"),sQuery(id+"F0.wireOp",EDGE,"E947"),sQuery(id+"F0.wireOp",EDGE,"E948"),sQuery(id+"F0.wireOp",EDGE,"E949"),sQuery(id+"F0.wireOp",EDGE,"E950"),sQuery(id+"F0.wireOp",EDGE,"E951"),sQuery(id+"F0.wireOp",EDGE,"E952"),sQuery(id+"F0.wireOp",EDGE,"E953"),sQuery(id+"F0.wireOp",EDGE,"E954"),sQuery(id+"F0.wireOp",EDGE,"E955"),sQuery(id+"F0.wireOp",EDGE,"E956"),sQuery(id+"F0.wireOp",EDGE,"E957"),sQuery(id+"F0.wireOp",EDGE,"E958"),sQuery(id+"F0.wireOp",EDGE,"E959"),sQuery(id+"F0.wireOp",EDGE,"E960"),sQuery(id+"F0.wireOp",EDGE,"E961"),sQuery(id+"F0.wireOp",EDGE,"E962"),sQuery(id+"F0.wireOp",EDGE,"E963"),sQuery(id+"F0.wireOp",EDGE,"E964"),sQuery(id+"F0.wireOp",EDGE,"E965"),sQuery(id+"F0.wireOp",EDGE,"E966"),sQuery(id+"F0.wireOp",EDGE,"E967"),sQuery(id+"F0.wireOp",EDGE,"E968"),sQuery(id+"F0.wireOp",EDGE,"E969"),sQuery(id+"F0.wireOp",EDGE,"E970"),sQuery(id+"F0.wireOp",EDGE,"E971"),sQuery(id+"F0.wireOp",EDGE,"E972"),sQuery(id+"F0.wireOp",EDGE,"E973"),sQuery(id+"F0.wireOp",EDGE,"E974"),sQuery(id+"F0.wireOp",EDGE,"E975"),sQuery(id+"F0.wireOp",EDGE,"E976"),sQuery(id+"F0.wireOp",EDGE,"E977"),sQuery(id+"F0.wireOp",EDGE,"E978"),sQuery(id+"F0.wireOp",EDGE,"E979"),sQuery(id+"F0.wireOp",EDGE,"E980"),sQuery(id+"F0.wireOp",EDGE,"E981"),sQuery(id+"F0.wireOp",EDGE,"E982"),sQuery(id+"F0.wireOp",EDGE,"E983"),sQuery(id+"F0.wireOp",EDGE,"E984"),sQuery(id+"F0.wireOp",EDGE,"E985"),sQuery(id+"F0.wireOp",EDGE,"E986"),sQuery(id+"F0.wireOp",EDGE,"E987"),sQuery(id+"F0.wireOp",EDGE,"E988"),sQuery(id+"F0.wireOp",EDGE,"E989"),sQuery(id+"F0.wireOp",EDGE,"E990"),sQuery(id+"F0.wireOp",EDGE,"E991"),sQuery(id+"F0.wireOp",EDGE,"E992"),sQuery(id+"F0.wireOp",EDGE,"E993"),sQuery(id+"F0.wireOp",EDGE,"E994"),sQuery(id+"F0.wireOp",EDGE,"E995"),sQuery(id+"F0.wireOp",EDGE,"E996"),sQuery(id+"F0.wireOp",EDGE,"E997"),sQuery(id+"F0.wireOp",EDGE,"E998"),sQuery(id+"F0.wireOp",EDGE,"E999"),sQuery(id+"F0.wireOp",EDGE,"E1000"),sQuery(id+"F0.wireOp",EDGE,"E1001"),sQuery(id+"F0.wireOp",EDGE,"E1002"),sQuery(id+"F0.wireOp",EDGE,"E1003"),sQuery(id+"F0.wireOp",EDGE,"E1004"),sQuery(id+"F0.wireOp",EDGE,"E1005"),sQuery(id+"F0.wireOp",EDGE,"E1006"),sQuery(id+"F0.wireOp",EDGE,"E1007"),sQuery(id+"F0.wireOp",EDGE,"E1008"),sQuery(id+"F0.wireOp",EDGE,"E1009"),sQuery(id+"F0.wireOp",EDGE,"E1010"),sQuery(id+"F0.wireOp",EDGE,"E1011"),sQuery(id+"F0.wireOp",EDGE,"E1012"),sQuery(id+"F0.wireOp",EDGE,"E1013"),sQuery(id+"F0.wireOp",EDGE,"E1014"),sQuery(id+"F0.wireOp",EDGE,"E1015"),sQuery(id+"F0.wireOp",EDGE,"E1016"),sQuery(id+"F0.wireOp",EDGE,"E1017"),sQuery(id+"F0.wireOp",EDGE,"E1018"),sQuery(id+"F0.wireOp",EDGE,"E1019"),sQuery(id+"F0.wireOp",EDGE,"E1020"),sQuery(id+"F0.wireOp",EDGE,"E1021"),sQuery(id+"F0.wireOp",EDGE,"E1022"),sQuery(id+"F0.wireOp",EDGE,"E1023"),sQuery(id+"F0.wireOp",EDGE,"E1024"),sQuery(id+"F0.wireOp",EDGE,"E1025"),sQuery(id+"F0.wireOp",EDGE,"E1026"),sQuery(id+"F0.wireOp",EDGE,"E1027"),sQuery(id+"F0.wireOp",EDGE,"E1028"),sQuery(id+"F0.wireOp",EDGE,"E1029"),sQuery(id+"F0.wireOp",EDGE,"E1030"),sQuery(id+"F0.wireOp",EDGE,"E1031"),sQuery(id+"F0.wireOp",EDGE,"E1032"),sQuery(id+"F0.wireOp",EDGE,"E1033"),sQuery(id+"F0.wireOp",EDGE,"E1034"),sQuery(id+"F0.wireOp",EDGE,"E1035"),sQuery(id+"F0.wireOp",EDGE,"E1036"),sQuery(id+"F0.wireOp",EDGE,"E1037"),sQuery(id+"F0.wireOp",EDGE,"E1038"),sQuery(id+"F0.wireOp",EDGE,"E1039"),sQuery(id+"F0.wireOp",EDGE,"E1040"),sQuery(id+"F0.wireOp",EDGE,"E1041"),sQuery(id+"F0.wireOp",EDGE,"E1042"),sQuery(id+"F0.wireOp",EDGE,"E1043"),sQuery(id+"F0.wireOp",EDGE,"E1044"),sQuery(id+"F0.wireOp",EDGE,"E1045"),sQuery(id+"F0.wireOp",EDGE,"E1046"),sQuery(id+"F0.wireOp",EDGE,"E1047"),sQuery(id+"F0.wireOp",EDGE,"E1048"),sQuery(id+"F0.wireOp",EDGE,"E1049"),sQuery(id+"F0.wireOp",EDGE,"E1050"),sQuery(id+"F0.wireOp",EDGE,"E1051"),sQuery(id+"F0.wireOp",EDGE,"E1052"),sQuery(id+"F0.wireOp",EDGE,"E1053"),sQuery(id+"F0.wireOp",EDGE,"E1054"),sQuery(id+"F0.wireOp",EDGE,"E1055"),sQuery(id+"F0.wireOp",EDGE,"E1056"),sQuery(id+"F0.wireOp",EDGE,"E1057"),sQuery(id+"F0.wireOp",EDGE,"E1058"),sQuery(id+"F0.wireOp",EDGE,"E1059"),sQuery(id+"F0.wireOp",EDGE,"E1060"),sQuery(id+"F0.wireOp",EDGE,"E1061"),sQuery(id+"F0.wireOp",EDGE,"E1062"),sQuery(id+"F0.wireOp",EDGE,"E1063"),sQuery(id+"F0.wireOp",EDGE,"E1064"),sQuery(id+"F0.wireOp",EDGE,"E1065"),sQuery(id+"F0.wireOp",EDGE,"E1066"),sQuery(id+"F0.wireOp",EDGE,"E1067"),sQuery(id+"F0.wireOp",EDGE,"E1068"),sQuery(id+"F0.wireOp",EDGE,"E1069"),sQuery(id+"F0.wireOp",EDGE,"E1070"),sQuery(id+"F0.wireOp",EDGE,"E1071"),sQuery(id+"F0.wireOp",EDGE,"E1072"),sQuery(id+"F0.wireOp",EDGE,"E1073"),sQuery(id+"F0.wireOp",EDGE,"E1074"),sQuery(id+"F0.wireOp",EDGE,"E1075"),sQuery(id+"F0.wireOp",EDGE,"E1076"),sQuery(id+"F0.wireOp",EDGE,"E1077"),sQuery(id+"F0.wireOp",EDGE,"E1078"),sQuery(id+"F0.wireOp",EDGE,"E1079"),sQuery(id+"F0.wireOp",EDGE,"E1080"),sQuery(id+"F0.wireOp",EDGE,"E1081"),sQuery(id+"F0.wireOp",EDGE,"E1082"),sQuery(id+"F0.wireOp",EDGE,"E1083"),sQuery(id+"F0.wireOp",EDGE,"E1084"),sQuery(id+"F0.wireOp",EDGE,"E1085"),sQuery(id+"F0.wireOp",EDGE,"E1086"),sQuery(id+"F0.wireOp",EDGE,"E1087"),sQuery(id+"F0.wireOp",EDGE,"E1088"),sQuery(id+"F0.wireOp",EDGE,"E1089"),sQuery(id+"F0.wireOp",EDGE,"E1090"),sQuery(id+"F0.wireOp",EDGE,"E1091"),sQuery(id+"F0.wireOp",EDGE,"E1092"),sQuery(id+"F0.wireOp",EDGE,"E1093"),sQuery(id+"F0.wireOp",EDGE,"E1094"),sQuery(id+"F0.wireOp",EDGE,"E1095"),sQuery(id+"F0.wireOp",EDGE,"E1096"),sQuery(id+"F0.wireOp",EDGE,"E1097"),sQuery(id+"F0.wireOp",EDGE,"E1098"),sQuery(id+"F0.wireOp",EDGE,"E1099"),sQuery(id+"F0.wireOp",EDGE,"E1100"),sQuery(id+"F0.wireOp",EDGE,"E1101"),sQuery(id+"F0.wireOp",EDGE,"E1102"),sQuery(id+"F0.wireOp",EDGE,"E1103"),sQuery(id+"F0.wireOp",EDGE,"E1104"),sQuery(id+"F0.wireOp",EDGE,"E1105"),sQuery(id+"F0.wireOp",EDGE,"E1106"),sQuery(id+"F0.wireOp",EDGE,"E1107"),sQuery(id+"F0.wireOp",EDGE,"E1108"),sQuery(id+"F0.wireOp",EDGE,"E1109"),sQuery(id+"F0.wireOp",EDGE,"E1110"),sQuery(id+"F0.wireOp",EDGE,"E1111"),sQuery(id+"F0.wireOp",EDGE,"E1112"),sQuery(id+"F0.wireOp",EDGE,"E1113"),sQuery(id+"F0.wireOp",EDGE,"E1114"),sQuery(id+"F0.wireOp",EDGE,"E1115"),sQuery(id+"F0.wireOp",EDGE,"E1116"),sQuery(id+"F0.wireOp",EDGE,"E1117"),sQuery(id+"F0.wireOp",EDGE,"E1118"),sQuery(id+"F0.wireOp",EDGE,"E1119"),sQuery(id+"F0.wireOp",EDGE,"E1120"),sQuery(id+"F0.wireOp",EDGE,"E1121"),sQuery(id+"F0.wireOp",EDGE,"E1122"),sQuery(id+"F0.wireOp",EDGE,"E1123"),sQuery(id+"F0.wireOp",EDGE,"E1124"),sQuery(id+"F0.wireOp",EDGE,"E1125"),sQuery(id+"F0.wireOp",EDGE,"E1126"),sQuery(id+"F0.wireOp",EDGE,"E1127"),sQuery(id+"F0.wireOp",EDGE,"E1128"),sQuery(id+"F0.wireOp",EDGE,"E1129"),sQuery(id+"F0.wireOp",EDGE,"E1130"),sQuery(id+"F0.wireOp",EDGE,"E1131"),sQuery(id+"F0.wireOp",EDGE,"E1132"),sQuery(id+"F0.wireOp",EDGE,"E1133"),sQuery(id+"F0.wireOp",EDGE,"E1134"),sQuery(id+"F0.wireOp",EDGE,"E1135"),sQuery(id+"F0.wireOp",EDGE,"E1136"),sQuery(id+"F0.wireOp",EDGE,"E1137"),sQuery(id+"F0.wireOp",EDGE,"E1138"),sQuery(id+"F0.wireOp",EDGE,"E1139"),sQuery(id+"F0.wireOp",EDGE,"E1140"),sQuery(id+"F0.wireOp",EDGE,"E1141"),sQuery(id+"F0.wireOp",EDGE,"E1142"),sQuery(id+"F0.wireOp",EDGE,"E1143"),sQuery(id+"F0.wireOp",EDGE,"E1144"),sQuery(id+"F0.wireOp",EDGE,"E1145"),sQuery(id+"F0.wireOp",EDGE,"E1146"),sQuery(id+"F0.wireOp",EDGE,"E1147"),sQuery(id+"F0.wireOp",EDGE,"E1148"),sQuery(id+"F0.wireOp",EDGE,"E1149"),sQuery(id+"F0.wireOp",EDGE,"E1150"),sQuery(id+"F0.wireOp",EDGE,"E1151"),sQuery(id+"F0.wireOp",EDGE,"E1152"),sQuery(id+"F0.wireOp",EDGE,"E1153"),sQuery(id+"F0.wireOp",EDGE,"E1154"),sQuery(id+"F0.wireOp",EDGE,"E1155"),sQuery(id+"F0.wireOp",EDGE,"E1156"),sQuery(id+"F0.wireOp",EDGE,"E1157"),sQuery(id+"F0.wireOp",EDGE,"E1158"),sQuery(id+"F0.wireOp",EDGE,"E1159"),sQuery(id+"F0.wireOp",EDGE,"E1160"),sQuery(id+"F0.wireOp",EDGE,"E1161"),sQuery(id+"F0.wireOp",EDGE,"E1162"),sQuery(id+"F0.wireOp",EDGE,"E1163"),sQuery(id+"F0.wireOp",EDGE,"E1164"),sQuery(id+"F0.wireOp",EDGE,"E1165"),sQuery(id+"F0.wireOp",EDGE,"E1166"),sQuery(id+"F0.wireOp",EDGE,"E1167"),sQuery(id+"F0.wireOp",EDGE,"E1168"),sQuery(id+"F0.wireOp",EDGE,"E1169"),sQuery(id+"F0.wireOp",EDGE,"E1170"),sQuery(id+"F0.wireOp",EDGE,"E1171"),sQuery(id+"F0.wireOp",EDGE,"E1172"),sQuery(id+"F0.wireOp",EDGE,"E1173"),sQuery(id+"F0.wireOp",EDGE,"E1174"),sQuery(id+"F0.wireOp",EDGE,"E1175"),sQuery(id+"F0.wireOp",EDGE,"E1176"),sQuery(id+"F0.wireOp",EDGE,"E1177"),sQuery(id+"F0.wireOp",EDGE,"E1178"),sQuery(id+"F0.wireOp",EDGE,"E1179"),sQuery(id+"F0.wireOp",EDGE,"E1180"),sQuery(id+"F0.wireOp",EDGE,"E1181"),sQuery(id+"F0.wireOp",EDGE,"E1182"),sQuery(id+"F0.wireOp",EDGE,"E1183"),sQuery(id+"F0.wireOp",EDGE,"E1184"),sQuery(id+"F0.wireOp",EDGE,"E1185"),sQuery(id+"F0.wireOp",EDGE,"E1186"),sQuery(id+"F0.wireOp",EDGE,"E1187"),sQuery(id+"F0.wireOp",EDGE,"E1188"),sQuery(id+"F0.wireOp",EDGE,"E1189"),sQuery(id+"F0.wireOp",EDGE,"E1190"),sQuery(id+"F0.wireOp",EDGE,"E1191"),sQuery(id+"F0.wireOp",EDGE,"E1192"),sQuery(id+"F0.wireOp",EDGE,"E1193"),sQuery(id+"F0.wireOp",EDGE,"E1194"),sQuery(id+"F0.wireOp",EDGE,"E1195"),sQuery(id+"F0.wireOp",EDGE,"E1196"),sQuery(id+"F0.wireOp",EDGE,"E1197"),sQuery(id+"F0.wireOp",EDGE,"E1198"),sQuery(id+"F0.wireOp",EDGE,"E1199"),sQuery(id+"F0.wireOp",EDGE,"E1200"),sQuery(id+"F0.wireOp",EDGE,"E1201"),sQuery(id+"F0.wireOp",EDGE,"E1202"),sQuery(id+"F0.wireOp",EDGE,"E1203"),sQuery(id+"F0.wireOp",EDGE,"E1204"),sQuery(id+"F0.wireOp",EDGE,"E1205"),sQuery(id+"F0.wireOp",EDGE,"E1206"),sQuery(id+"F0.wireOp",EDGE,"E1207"),sQuery(id+"F0.wireOp",EDGE,"E1208"),sQuery(id+"F0.wireOp",EDGE,"E1209"),sQuery(id+"F0.wireOp",EDGE,"E1210"),sQuery(id+"F0.wireOp",EDGE,"E1211"),sQuery(id+"F0.wireOp",EDGE,"E1212"),sQuery(id+"F0.wireOp",EDGE,"E1213"),sQuery(id+"F0.wireOp",EDGE,"E1214"),sQuery(id+"F0.wireOp",EDGE,"E1215"),sQuery(id+"F0.wireOp",EDGE,"E1216"),sQuery(id+"F0.wireOp",EDGE,"E1217"),sQuery(id+"F0.wireOp",EDGE,"E1218"),sQuery(id+"F0.wireOp",EDGE,"E1219"),sQuery(id+"F0.wireOp",EDGE,"E1220"),sQuery(id+"F0.wireOp",EDGE,"E1221"),sQuery(id+"F0.wireOp",EDGE,"E1222"),sQuery(id+"F0.wireOp",EDGE,"E1223"),sQuery(id+"F0.wireOp",EDGE,"E1224"),sQuery(id+"F0.wireOp",EDGE,"E1225"),sQuery(id+"F0.wireOp",EDGE,"E1226"),sQuery(id+"F0.wireOp",EDGE,"E1227"),sQuery(id+"F0.wireOp",EDGE,"E1228"),sQuery(id+"F0.wireOp",EDGE,"E1229"),sQuery(id+"F0.wireOp",EDGE,"E1230"),sQuery(id+"F0.wireOp",EDGE,"E1231"),sQuery(id+"F0.wireOp",EDGE,"E1232"),sQuery(id+"F0.wireOp",EDGE,"E1233"),sQuery(id+"F0.wireOp",EDGE,"E1234"),sQuery(id+"F0.wireOp",EDGE,"E1235"),sQuery(id+"F0.wireOp",EDGE,"E1236"),sQuery(id+"F0.wireOp",EDGE,"E1237"),sQuery(id+"F0.wireOp",EDGE,"E1238"),sQuery(id+"F0.wireOp",EDGE,"E1239"),sQuery(id+"F0.wireOp",EDGE,"E1240"),sQuery(id+"F0.wireOp",EDGE,"E1241"),sQuery(id+"F0.wireOp",EDGE,"E1242"),sQuery(id+"F0.wireOp",EDGE,"E1243"),sQuery(id+"F0.wireOp",EDGE,"E1244"),sQuery(id+"F0.wireOp",EDGE,"E1245"),sQuery(id+"F0.wireOp",EDGE,"E1246"),sQuery(id+"F0.wireOp",EDGE,"E1247"),sQuery(id+"F0.wireOp",EDGE,"E1248"),sQuery(id+"F0.wireOp",EDGE,"E1249"),sQuery(id+"F0.wireOp",EDGE,"E1250"),sQuery(id+"F0.wireOp",EDGE,"E1251"),sQuery(id+"F0.wireOp",EDGE,"E1252"),sQuery(id+"F0.wireOp",EDGE,"E1253"),sQuery(id+"F0.wireOp",EDGE,"E1254"),sQuery(id+"F0.wireOp",EDGE,"E1255"),sQuery(id+"F0.wireOp",EDGE,"E1256"),sQuery(id+"F0.wireOp",EDGE,"E1257"),sQuery(id+"F0.wireOp",EDGE,"E1258"),sQuery(id+"F0.wireOp",EDGE,"E1259"),sQuery(id+"F0.wireOp",EDGE,"E1260"),sQuery(id+"F0.wireOp",EDGE,"E1261"),sQuery(id+"F0.wireOp",EDGE,"E1262"),sQuery(id+"F0.wireOp",EDGE,"E1263"),sQuery(id+"F0.wireOp",EDGE,"E1264"),sQuery(id+"F0.wireOp",EDGE,"E1265"),sQuery(id+"F0.wireOp",EDGE,"E1266"),sQuery(id+"F0.wireOp",EDGE,"E1267"),sQuery(id+"F0.wireOp",EDGE,"E1268"),sQuery(id+"F0.wireOp",EDGE,"E1269"),sQuery(id+"F0.wireOp",EDGE,"E1270"),sQuery(id+"F0.wireOp",EDGE,"E1271"),sQuery(id+"F0.wireOp",EDGE,"E1272"),sQuery(id+"F0.wireOp",EDGE,"E1273"),sQuery(id+"F0.wireOp",EDGE,"E1274"),sQuery(id+"F0.wireOp",EDGE,"E1275"),sQuery(id+"F0.wireOp",EDGE,"E1276"),sQuery(id+"F0.wireOp",EDGE,"E1277"),sQuery(id+"F0.wireOp",EDGE,"E1278"),sQuery(id+"F0.wireOp",EDGE,"E1279"),sQuery(id+"F0.wireOp",EDGE,"E1280"),sQuery(id+"F0.wireOp",EDGE,"E1281"),sQuery(id+"F0.wireOp",EDGE,"E1282"),sQuery(id+"F0.wireOp",EDGE,"E1283"),sQuery(id+"F0.wireOp",EDGE,"E1284"),sQuery(id+"F0.wireOp",EDGE,"E1285"),sQuery(id+"F0.wireOp",EDGE,"E1286"),sQuery(id+"F0.wireOp",EDGE,"E1287"),sQuery(id+"F0.wireOp",EDGE,"E1288"),sQuery(id+"F0.wireOp",EDGE,"E1289"),sQuery(id+"F0.wireOp",EDGE,"E1290"),sQuery(id+"F0.wireOp",EDGE,"E1291"),sQuery(id+"F0.wireOp",EDGE,"E1292"),sQuery(id+"F0.wireOp",EDGE,"E1293"),sQuery(id+"F0.wireOp",EDGE,"E1294"),sQuery(id+"F0.wireOp",EDGE,"E1295"),sQuery(id+"F0.wireOp",EDGE,"E1296"),sQuery(id+"F0.wireOp",EDGE,"E1297"),sQuery(id+"F0.wireOp",EDGE,"E1298"),sQuery(id+"F0.wireOp",EDGE,"E1299"),sQuery(id+"F0.wireOp",EDGE,"E1300"),sQuery(id+"F0.wireOp",EDGE,"E1301"),sQuery(id+"F0.wireOp",EDGE,"E1302"),sQuery(id+"F0.wireOp",EDGE,"E1303"),sQuery(id+"F0.wireOp",EDGE,"E1304"),sQuery(id+"F0.wireOp",EDGE,"E1305"),sQuery(id+"F0.wireOp",EDGE,"E1306"),sQuery(id+"F0.wireOp",EDGE,"E1307"),sQuery(id+"F0.wireOp",EDGE,"E1308"),sQuery(id+"F0.wireOp",EDGE,"E1309"),sQuery(id+"F0.wireOp",EDGE,"E1310"),sQuery(id+"F0.wireOp",EDGE,"E1311"),sQuery(id+"F0.wireOp",EDGE,"E1312"),sQuery(id+"F0.wireOp",EDGE,"E1313"),sQuery(id+"F0.wireOp",EDGE,"E1314"),sQuery(id+"F0.wireOp",EDGE,"E1315"),sQuery(id+"F0.wireOp",EDGE,"E1316"),sQuery(id+"F0.wireOp",EDGE,"E1317"),sQuery(id+"F0.wireOp",EDGE,"E1318"),sQuery(id+"F0.wireOp",EDGE,"E1319"),sQuery(id+"F0.wireOp",EDGE,"E1320"),sQuery(id+"F0.wireOp",EDGE,"E1321"),sQuery(id+"F0.wireOp",EDGE,"E1322"),sQuery(id+"F0.wireOp",EDGE,"E1323"),sQuery(id+"F0.wireOp",EDGE,"E1324"),sQuery(id+"F0.wireOp",EDGE,"E1325"),sQuery(id+"F0.wireOp",EDGE,"E1326"),sQuery(id+"F0.wireOp",EDGE,"E1327"),sQuery(id+"F0.wireOp",EDGE,"E1328"),sQuery(id+"F0.wireOp",EDGE,"E1329"),sQuery(id+"F0.wireOp",EDGE,"E1330"),sQuery(id+"F0.wireOp",EDGE,"E1331"),sQuery(id+"F0.wireOp",EDGE,"E1332"),sQuery(id+"F0.wireOp",EDGE,"E1333"),sQuery(id+"F0.wireOp",EDGE,"E1334"),sQuery(id+"F0.wireOp",EDGE,"E1335"),sQuery(id+"F0.wireOp",EDGE,"E1336"),sQuery(id+"F0.wireOp",EDGE,"E1337"),sQuery(id+"F0.wireOp",EDGE,"E1338"),sQuery(id+"F0.wireOp",EDGE,"E1339"),sQuery(id+"F0.wireOp",EDGE,"E1340"),sQuery(id+"F0.wireOp",EDGE,"E1341"),sQuery(id+"F0.wireOp",EDGE,"E1342"),sQuery(id+"F0.wireOp",EDGE,"E1343"),sQuery(id+"F0.wireOp",EDGE,"E1344"),sQuery(id+"F0.wireOp",EDGE,"E1345"),sQuery(id+"F0.wireOp",EDGE,"E1346"),sQuery(id+"F0.wireOp",EDGE,"E1347"),sQuery(id+"F0.wireOp",EDGE,"E1348"),sQuery(id+"F0.wireOp",EDGE,"E1349"),sQuery(id+"F0.wireOp",EDGE,"E1350"),sQuery(id+"F0.wireOp",EDGE,"E1351"),sQuery(id+"F0.wireOp",EDGE,"E1352"),sQuery(id+"F0.wireOp",EDGE,"E1353"),sQuery(id+"F0.wireOp",EDGE,"E1354"),sQuery(id+"F0.wireOp",EDGE,"E1355"),sQuery(id+"F0.wireOp",EDGE,"E1356"),sQuery(id+"F0.wireOp",EDGE,"E1357"),sQuery(id+"F0.wireOp",EDGE,"E1358"),sQuery(id+"F0.wireOp",EDGE,"E1359"),sQuery(id+"F0.wireOp",EDGE,"E1360"),sQuery(id+"F0.wireOp",EDGE,"E1361"),sQuery(id+"F0.wireOp",EDGE,"E1362"),sQuery(id+"F0.wireOp",EDGE,"E1363"),sQuery(id+"F0.wireOp",EDGE,"E1364"),sQuery(id+"F0.wireOp",EDGE,"E1365"),sQuery(id+"F0.wireOp",EDGE,"E1366"),sQuery(id+"F0.wireOp",EDGE,"E1367"),sQuery(id+"F0.wireOp",EDGE,"E1368"),sQuery(id+"F0.wireOp",EDGE,"E1369"),sQuery(id+"F0.wireOp",EDGE,"E1370"),sQuery(id+"F0.wireOp",EDGE,"E1371"),sQuery(id+"F0.wireOp",EDGE,"E1372"),sQuery(id+"F0.wireOp",EDGE,"E1373"),sQuery(id+"F0.wireOp",EDGE,"E1374"),sQuery(id+"F0.wireOp",EDGE,"E1375"),sQuery(id+"F0.wireOp",EDGE,"E1376"),sQuery(id+"F0.wireOp",EDGE,"E1377"),sQuery(id+"F0.wireOp",EDGE,"E1378"),sQuery(id+"F0.wireOp",EDGE,"E1379"),sQuery(id+"F0.wireOp",EDGE,"E1380"),sQuery(id+"F0.wireOp",EDGE,"E1381"),sQuery(id+"F0.wireOp",EDGE,"E1382"),sQuery(id+"F0.wireOp",EDGE,"E1383"),sQuery(id+"F0.wireOp",EDGE,"E1384"),sQuery(id+"F0.wireOp",EDGE,"E1385"),sQuery(id+"F0.wireOp",EDGE,"E1386"),sQuery(id+"F0.wireOp",EDGE,"E1387"),sQuery(id+"F0.wireOp",EDGE,"E1388"),sQuery(id+"F0.wireOp",EDGE,"E1389"),sQuery(id+"F0.wireOp",EDGE,"E1390"),sQuery(id+"F0.wireOp",EDGE,"E1391"),sQuery(id+"F0.wireOp",EDGE,"E1392"),sQuery(id+"F0.wireOp",EDGE,"E1393"),sQuery(id+"F0.wireOp",EDGE,"E1394"),sQuery(id+"F0.wireOp",EDGE,"E1395"),sQuery(id+"F0.wireOp",EDGE,"E1396"),sQuery(id+"F0.wireOp",EDGE,"E1397"),sQuery(id+"F0.wireOp",EDGE,"E1398"),sQuery(id+"F0.wireOp",EDGE,"E1399"),sQuery(id+"F0.wireOp",EDGE,"E1400"),sQuery(id+"F0.wireOp",EDGE,"E1401"),sQuery(id+"F0.wireOp",EDGE,"E1402"),sQuery(id+"F0.wireOp",EDGE,"E1403"),sQuery(id+"F0.wireOp",EDGE,"E1404"),sQuery(id+"F0.wireOp",EDGE,"E1405"),sQuery(id+"F0.wireOp",EDGE,"E1406"),sQuery(id+"F0.wireOp",EDGE,"E1407"),sQuery(id+"F0.wireOp",EDGE,"E1408"),sQuery(id+"F0.wireOp",EDGE,"E1409"),sQuery(id+"F0.wireOp",EDGE,"E1410"),sQuery(id+"F0.wireOp",EDGE,"E1411"),sQuery(id+"F0.wireOp",EDGE,"E1412"),sQuery(id+"F0.wireOp",EDGE,"E1413"),sQuery(id+"F0.wireOp",EDGE,"E1414"),sQuery(id+"F0.wireOp",EDGE,"E1415"),sQuery(id+"F0.wireOp",EDGE,"E1416"),sQuery(id+"F0.wireOp",EDGE,"E1417"),sQuery(id+"F0.wireOp",EDGE,"E1418"),sQuery(id+"F0.wireOp",EDGE,"E1419"),sQuery(id+"F0.wireOp",EDGE,"E1420"),sQuery(id+"F0.wireOp",EDGE,"E1421"),sQuery(id+"F0.wireOp",EDGE,"E1422"),sQuery(id+"F0.wireOp",EDGE,"E1423"),sQuery(id+"F0.wireOp",EDGE,"E1424"),sQuery(id+"F0.wireOp",EDGE,"E1425"),sQuery(id+"F0.wireOp",EDGE,"E1426"),sQuery(id+"F0.wireOp",EDGE,"E1427"),sQuery(id+"F0.wireOp",EDGE,"E1428"),sQuery(id+"F0.wireOp",EDGE,"E1429"),sQuery(id+"F0.wireOp",EDGE,"E1430"),sQuery(id+"F0.wireOp",EDGE,"E1431"),sQuery(id+"F0.wireOp",EDGE,"E1432"),sQuery(id+"F0.wireOp",EDGE,"E1433"),sQuery(id+"F0.wireOp",EDGE,"E1434"),sQuery(id+"F0.wireOp",EDGE,"E1435"),sQuery(id+"F0.wireOp",EDGE,"E1436"),sQuery(id+"F0.wireOp",EDGE,"E1437"),sQuery(id+"F0.wireOp",EDGE,"E1438"),sQuery(id+"F0.wireOp",EDGE,"E1439"),sQuery(id+"F0.wireOp",EDGE,"E1440"),sQuery(id+"F0.wireOp",EDGE,"E1441"),sQuery(id+"F0.wireOp",EDGE,"E1442"),sQuery(id+"F0.wireOp",EDGE,"E1443"),sQuery(id+"F0.wireOp",EDGE,"E1444"),sQuery(id+"F0.wireOp",EDGE,"E1445"),sQuery(id+"F0.wireOp",EDGE,"E1446"),sQuery(id+"F0.wireOp",EDGE,"E1447"),sQuery(id+"F0.wireOp",EDGE,"E1448"),sQuery(id+"F0.wireOp",EDGE,"E1449"),sQuery(id+"F0.wireOp",EDGE,"E1450"),sQuery(id+"F0.wireOp",EDGE,"E1451"),sQuery(id+"F0.wireOp",EDGE,"E1452"),sQuery(id+"F0.wireOp",EDGE,"E1453"),sQuery(id+"F0.wireOp",EDGE,"E1454"),sQuery(id+"F0.wireOp",EDGE,"E1455"),sQuery(id+"F0.wireOp",EDGE,"E1456"),sQuery(id+"F0.wireOp",EDGE,"E1457"),sQuery(id+"F0.wireOp",EDGE,"E1458"),sQuery(id+"F0.wireOp",EDGE,"E1459"),sQuery(id+"F0.wireOp",EDGE,"E1460"),sQuery(id+"F0.wireOp",EDGE,"E1461"),sQuery(id+"F0.wireOp",EDGE,"E1462"),sQuery(id+"F0.wireOp",EDGE,"E1463"),sQuery(id+"F0.wireOp",EDGE,"E1464"),sQuery(id+"F0.wireOp",EDGE,"E1465"),sQuery(id+"F0.wireOp",EDGE,"E1466"),sQuery(id+"F0.wireOp",EDGE,"E1467"),sQuery(id+"F0.wireOp",EDGE,"E1468"),sQuery(id+"F0.wireOp",EDGE,"E1469"),sQuery(id+"F0.wireOp",EDGE,"E1470"),sQuery(id+"F0.wireOp",EDGE,"E1471"),sQuery(id+"F0.wireOp",EDGE,"E1472"),sQuery(id+"F0.wireOp",EDGE,"E1473"),sQuery(id+"F0.wireOp",EDGE,"E1474"),sQuery(id+"F0.wireOp",EDGE,"E1475"),sQuery(id+"F0.wireOp",EDGE,"E1476"),sQuery(id+"F0.wireOp",EDGE,"E1477"),sQuery(id+"F0.wireOp",EDGE,"E1478"),sQuery(id+"F0.wireOp",EDGE,"E1479"),sQuery(id+"F0.wireOp",EDGE,"E1480"),sQuery(id+"F0.wireOp",EDGE,"E1481"),sQuery(id+"F0.wireOp",EDGE,"E1482"),sQuery(id+"F0.wireOp",EDGE,"E1483"),sQuery(id+"F0.wireOp",EDGE,"E1484"),sQuery(id+"F0.wireOp",EDGE,"E1485"),sQuery(id+"F0.wireOp",EDGE,"E1486"),sQuery(id+"F0.wireOp",EDGE,"E1487"),sQuery(id+"F0.wireOp",EDGE,"E1488"),sQuery(id+"F0.wireOp",EDGE,"E1489"),sQuery(id+"F0.wireOp",EDGE,"E1490"),sQuery(id+"F0.wireOp",EDGE,"E1491"),sQuery(id+"F0.wireOp",EDGE,"E1492"),sQuery(id+"F0.wireOp",EDGE,"E1493"),sQuery(id+"F0.wireOp",EDGE,"E1494"),sQuery(id+"F0.wireOp",EDGE,"E1495"),sQuery(id+"F0.wireOp",EDGE,"E1496"),sQuery(id+"F0.wireOp",EDGE,"E1497"),sQuery(id+"F0.wireOp",EDGE,"E1498"),sQuery(id+"F0.wireOp",EDGE,"E1499"),sQuery(id+"F0.wireOp",EDGE,"E1500"),sQuery(id+"F0.wireOp",EDGE,"E1501"),sQuery(id+"F0.wireOp",EDGE,"E1502"),sQuery(id+"F0.wireOp",EDGE,"E1503"),sQuery(id+"F0.wireOp",EDGE,"E1504"),sQuery(id+"F0.wireOp",EDGE,"E1505"),sQuery(id+"F0.wireOp",EDGE,"E1506"),sQuery(id+"F0.wireOp",EDGE,"E1507"),sQuery(id+"F0.wireOp",EDGE,"E1508"),sQuery(id+"F0.wireOp",EDGE,"E1509"),sQuery(id+"F0.wireOp",EDGE,"E1510"),sQuery(id+"F0.wireOp",EDGE,"E1511"),sQuery(id+"F0.wireOp",EDGE,"E1512"),sQuery(id+"F0.wireOp",EDGE,"E1513"),sQuery(id+"F0.wireOp",EDGE,"E1514"),sQuery(id+"F0.wireOp",EDGE,"E1515"),sQuery(id+"F0.wireOp",EDGE,"E1516"),sQuery(id+"F0.wireOp",EDGE,"E1517"),sQuery(id+"F0.wireOp",EDGE,"E1518"),sQuery(id+"F0.wireOp",EDGE,"E1519"),sQuery(id+"F0.wireOp",EDGE,"E1520"),sQuery(id+"F0.wireOp",EDGE,"E1521"),sQuery(id+"F0.wireOp",EDGE,"E1522"),sQuery(id+"F0.wireOp",EDGE,"E1523"),sQuery(id+"F0.wireOp",EDGE,"E1524"),sQuery(id+"F0.wireOp",EDGE,"E1525"),sQuery(id+"F0.wireOp",EDGE,"E1526"),sQuery(id+"F0.wireOp",EDGE,"E1527"),sQuery(id+"F0.wireOp",EDGE,"E1528"),sQuery(id+"F0.wireOp",EDGE,"E1529"),sQuery(id+"F0.wireOp",EDGE,"E1530"),sQuery(id+"F0.wireOp",EDGE,"E1531"),sQuery(id+"F0.wireOp",EDGE,"E1532"),sQuery(id+"F0.wireOp",EDGE,"E1533"),sQuery(id+"F0.wireOp",EDGE,"E1534"),sQuery(id+"F0.wireOp",EDGE,"E1535"),sQuery(id+"F0.wireOp",EDGE,"E1536"),sQuery(id+"F0.wireOp",EDGE,"E1537"),sQuery(id+"F0.wireOp",EDGE,"E1538"),sQuery(id+"F0.wireOp",EDGE,"E1539"),sQuery(id+"F0.wireOp",EDGE,"E1540"),sQuery(id+"F0.wireOp",EDGE,"E1541"),sQuery(id+"F0.wireOp",EDGE,"E1542"),sQuery(id+"F0.wireOp",EDGE,"E1543"),sQuery(id+"F0.wireOp",EDGE,"E1544"),sQuery(id+"F0.wireOp",EDGE,"E1545"),sQuery(id+"F0.wireOp",EDGE,"E1546"),sQuery(id+"F0.wireOp",EDGE,"E1547"),sQuery(id+"F0.wireOp",EDGE,"E1548"),sQuery(id+"F0.wireOp",EDGE,"E1549"),sQuery(id+"F0.wireOp",EDGE,"E1550"),sQuery(id+"F0.wireOp",EDGE,"E1551"),sQuery(id+"F0.wireOp",EDGE,"E1552"),sQuery(id+"F0.wireOp",EDGE,"E1553"),sQuery(id+"F0.wireOp",EDGE,"E1554"),sQuery(id+"F0.wireOp",EDGE,"E1555"),sQuery(id+"F0.wireOp",EDGE,"E1556"),sQuery(id+"F0.wireOp",EDGE,"E1557"),sQuery(id+"F0.wireOp",EDGE,"E1558"),sQuery(id+"F0.wireOp",EDGE,"E1559"),sQuery(id+"F0.wireOp",EDGE,"E1560"),sQuery(id+"F0.wireOp",EDGE,"E1561"),sQuery(id+"F0.wireOp",EDGE,"E1562"),sQuery(id+"F0.wireOp",EDGE,"E1563"),sQuery(id+"F0.wireOp",EDGE,"E1564"),sQuery(id+"F0.wireOp",EDGE,"E1565"),sQuery(id+"F0.wireOp",EDGE,"E1566"),sQuery(id+"F0.wireOp",EDGE,"E1567"),sQuery(id+"F0.wireOp",EDGE,"E1568"),sQuery(id+"F0.wireOp",EDGE,"E1569"),sQuery(id+"F0.wireOp",EDGE,"E1570"),sQuery(id+"F0.wireOp",EDGE,"E1571"),sQuery(id+"F0.wireOp",EDGE,"E1572"),sQuery(id+"F0.wireOp",EDGE,"E1573"),sQuery(id+"F0.wireOp",EDGE,"E1574"),sQuery(id+"F0.wireOp",EDGE,"E1575"),sQuery(id+"F0.wireOp",EDGE,"E1576"),sQuery(id+"F0.wireOp",EDGE,"E1577"),sQuery(id+"F0.wireOp",EDGE,"E1578"),sQuery(id+"F0.wireOp",EDGE,"E1579"),sQuery(id+"F0.wireOp",EDGE,"E1580"),sQuery(id+"F0.wireOp",EDGE,"E1581"),sQuery(id+"F0.wireOp",EDGE,"E1582"),sQuery(id+"F0.wireOp",EDGE,"E1583"),sQuery(id+"F0.wireOp",EDGE,"E1584"),sQuery(id+"F0.wireOp",EDGE,"E1585"),sQuery(id+"F0.wireOp",EDGE,"E1586"),sQuery(id+"F0.wireOp",EDGE,"E1587"),sQuery(id+"F0.wireOp",EDGE,"E1588"),sQuery(id+"F0.wireOp",EDGE,"E1589"),sQuery(id+"F0.wireOp",EDGE,"E1590"),sQuery(id+"F0.wireOp",EDGE,"E1591"),sQuery(id+"F0.wireOp",EDGE,"E1592"),sQuery(id+"F0.wireOp",EDGE,"E1593"),sQuery(id+"F0.wireOp",EDGE,"E1594"),sQuery(id+"F0.wireOp",EDGE,"E1595"),sQuery(id+"F0.wireOp",EDGE,"E1596"),sQuery(id+"F0.wireOp",EDGE,"E1597"),sQuery(id+"F0.wireOp",EDGE,"E1598"),sQuery(id+"F0.wireOp",EDGE,"E1599"),sQuery(id+"F0.wireOp",EDGE,"E1600"),sQuery(id+"F0.wireOp",EDGE,"E1601"),sQuery(id+"F0.wireOp",EDGE,"E1602"),sQuery(id+"F0.wireOp",EDGE,"E1603"),sQuery(id+"F0.wireOp",EDGE,"E1604"),sQuery(id+"F0.wireOp",EDGE,"E1605"),sQuery(id+"F0.wireOp",EDGE,"E1606"),sQuery(id+"F0.wireOp",EDGE,"E1607"),sQuery(id+"F0.wireOp",EDGE,"E1608"),sQuery(id+"F0.wireOp",EDGE,"E1609"),sQuery(id+"F0.wireOp",EDGE,"E1610"),sQuery(id+"F0.wireOp",EDGE,"E1611"),sQuery(id+"F0.wireOp",EDGE,"E1612"),sQuery(id+"F0.wireOp",EDGE,"E1613"),sQuery(id+"F0.wireOp",EDGE,"E1614"),sQuery(id+"F0.wireOp",EDGE,"E1615"),sQuery(id+"F0.wireOp",EDGE,"E1616"),sQuery(id+"F0.wireOp",EDGE,"E1617"),sQuery(id+"F0.wireOp",EDGE,"E1618"),sQuery(id+"F0.wireOp",EDGE,"E1619"),sQuery(id+"F0.wireOp",EDGE,"E1620"),sQuery(id+"F0.wireOp",EDGE,"E1621"),sQuery(id+"F0.wireOp",EDGE,"E1622"),sQuery(id+"F0.wireOp",EDGE,"E1623"),sQuery(id+"F0.wireOp",EDGE,"E1624"),sQuery(id+"F0.wireOp",EDGE,"E1625"),sQuery(id+"F0.wireOp",EDGE,"E1626"),sQuery(id+"F0.wireOp",EDGE,"E1627"),sQuery(id+"F0.wireOp",EDGE,"E1628"),sQuery(id+"F0.wireOp",EDGE,"E1629"),sQuery(id+"F0.wireOp",EDGE,"E1630"),sQuery(id+"F0.wireOp",EDGE,"E1631"),sQuery(id+"F0.wireOp",EDGE,"E1632"),sQuery(id+"F0.wireOp",EDGE,"E1633"),sQuery(id+"F0.wireOp",EDGE,"E1634"),sQuery(id+"F0.wireOp",EDGE,"E1635"),sQuery(id+"F0.wireOp",EDGE,"E1636"),sQuery(id+"F0.wireOp",EDGE,"E1637"),sQuery(id+"F0.wireOp",EDGE,"E1638"),sQuery(id+"F0.wireOp",EDGE,"E1639"),sQuery(id+"F0.wireOp",EDGE,"E1640"),sQuery(id+"F0.wireOp",EDGE,"E1641"),sQuery(id+"F0.wireOp",EDGE,"E1642"),sQuery(id+"F0.wireOp",EDGE,"E1643"),sQuery(id+"F0.wireOp",EDGE,"E1644"),sQuery(id+"F0.wireOp",EDGE,"E1645"),sQuery(id+"F0.wireOp",EDGE,"E1646"),sQuery(id+"F0.wireOp",EDGE,"E1647"),sQuery(id+"F0.wireOp",EDGE,"E1648"),sQuery(id+"F0.wireOp",EDGE,"E1649"),sQuery(id+"F0.wireOp",EDGE,"E1650"),sQuery(id+"F0.wireOp",EDGE,"E1651"),sQuery(id+"F0.wireOp",EDGE,"E1652"),sQuery(id+"F0.wireOp",EDGE,"E1653"),sQuery(id+"F0.wireOp",EDGE,"E1654"),sQuery(id+"F0.wireOp",EDGE,"E1655"),sQuery(id+"F0.wireOp",EDGE,"E1656"),sQuery(id+"F0.wireOp",EDGE,"E1657"),sQuery(id+"F0.wireOp",EDGE,"E1658"),sQuery(id+"F0.wireOp",EDGE,"E1659"),sQuery(id+"F0.wireOp",EDGE,"E1660"),sQuery(id+"F0.wireOp",EDGE,"E1661"),sQuery(id+"F0.wireOp",EDGE,"E1662"),sQuery(id+"F0.wireOp",EDGE,"E1663"),sQuery(id+"F0.wireOp",EDGE,"E1664"),sQuery(id+"F0.wireOp",EDGE,"E1665"),sQuery(id+"F0.wireOp",EDGE,"E1666"),sQuery(id+"F0.wireOp",EDGE,"E1667"),sQuery(id+"F0.wireOp",EDGE,"E1668"),sQuery(id+"F0.wireOp",EDGE,"E1669"),sQuery(id+"F0.wireOp",EDGE,"E1670"),sQuery(id+"F0.wireOp",EDGE,"E1671"),sQuery(id+"F0.wireOp",EDGE,"E1672"),sQuery(id+"F0.wireOp",EDGE,"E1673"),sQuery(id+"F0.wireOp",EDGE,"E1674"),sQuery(id+"F0.wireOp",EDGE,"E1675"),sQuery(id+"F0.wireOp",EDGE,"E1676"),sQuery(id+"F0.wireOp",EDGE,"E1677"),sQuery(id+"F0.wireOp",EDGE,"E1678"),sQuery(id+"F0.wireOp",EDGE,"E1679"),sQuery(id+"F0.wireOp",EDGE,"E1680"),sQuery(id+"F0.wireOp",EDGE,"E1681"),sQuery(id+"F0.wireOp",EDGE,"E1682"),sQuery(id+"F0.wireOp",EDGE,"E1683"),sQuery(id+"F0.wireOp",EDGE,"E1684"),sQuery(id+"F0.wireOp",EDGE,"E1685"),sQuery(id+"F0.wireOp",EDGE,"E1686"),sQuery(id+"F0.wireOp",EDGE,"E1687"),sQuery(id+"F0.wireOp",EDGE,"E1688"),sQuery(id+"F0.wireOp",EDGE,"E1689"),sQuery(id+"F0.wireOp",EDGE,"E1690"),sQuery(id+"F0.wireOp",EDGE,"E1691"),sQuery(id+"F0.wireOp",EDGE,"E1692"),sQuery(id+"F0.wireOp",EDGE,"E1693"),sQuery(id+"F0.wireOp",EDGE,"E1694"),sQuery(id+"F0.wireOp",EDGE,"E1695"),sQuery(id+"F0.wireOp",EDGE,"E1696"),sQuery(id+"F0.wireOp",EDGE,"E1697"),sQuery(id+"F0.wireOp",EDGE,"E1698"),sQuery(id+"F0.wireOp",EDGE,"E1699"),sQuery(id+"F0.wireOp",EDGE,"E1700"),sQuery(id+"F0.wireOp",EDGE,"E1701"),sQuery(id+"F0.wireOp",EDGE,"E1702"),sQuery(id+"F0.wireOp",EDGE,"E1703"),sQuery(id+"F0.wireOp",EDGE,"E1704"),sQuery(id+"F0.wireOp",EDGE,"E1705"),sQuery(id+"F0.wireOp",EDGE,"E1706"),sQuery(id+"F0.wireOp",EDGE,"E1707"),sQuery(id+"F0.wireOp",EDGE,"E1708"),sQuery(id+"F0.wireOp",EDGE,"E1709"),sQuery(id+"F0.wireOp",EDGE,"E1710"),sQuery(id+"F0.wireOp",EDGE,"E1711"),sQuery(id+"F0.wireOp",EDGE,"E1712"),sQuery(id+"F0.wireOp",EDGE,"E1713"),sQuery(id+"F0.wireOp",EDGE,"E1714"),sQuery(id+"F0.wireOp",EDGE,"E1715"),sQuery(id+"F0.wireOp",EDGE,"E1716"),sQuery(id+"F0.wireOp",EDGE,"E1717"),sQuery(id+"F0.wireOp",EDGE,"E1718"),sQuery(id+"F0.wireOp",EDGE,"E1719"),sQuery(id+"F0.wireOp",EDGE,"E1720"),sQuery(id+"F0.wireOp",EDGE,"E1721"),sQuery(id+"F0.wireOp",EDGE,"E1722"),sQuery(id+"F0.wireOp",EDGE,"E1723"),sQuery(id+"F0.wireOp",EDGE,"E1724"),sQuery(id+"F0.wireOp",EDGE,"E1725"),sQuery(id+"F0.wireOp",EDGE,"E1726"),sQuery(id+"F0.wireOp",EDGE,"E1727"),sQuery(id+"F0.wireOp",EDGE,"E1728"),sQuery(id+"F0.wireOp",EDGE,"E1729"),sQuery(id+"F0.wireOp",EDGE,"E1730"),sQuery(id+"F0.wireOp",EDGE,"E1731"),sQuery(id+"F0.wireOp",EDGE,"E1732"),sQuery(id+"F0.wireOp",EDGE,"E1733"),sQuery(id+"F0.wireOp",EDGE,"E1734"),sQuery(id+"F0.wireOp",EDGE,"E1735"),sQuery(id+"F0.wireOp",EDGE,"E1736"),sQuery(id+"F0.wireOp",EDGE,"E1737"),sQuery(id+"F0.wireOp",EDGE,"E1738"),sQuery(id+"F0.wireOp",EDGE,"E1739"),sQuery(id+"F0.wireOp",EDGE,"E1740"),sQuery(id+"F0.wireOp",EDGE,"E1741"),sQuery(id+"F0.wireOp",EDGE,"E1742"),sQuery(id+"F0.wireOp",EDGE,"E1743"),sQuery(id+"F0.wireOp",EDGE,"E1744"),sQuery(id+"F0.wireOp",EDGE,"E1745"),sQuery(id+"F0.wireOp",EDGE,"E1746"),sQuery(id+"F0.wireOp",EDGE,"E1747"),sQuery(id+"F0.wireOp",EDGE,"E1748"),sQuery(id+"F0.wireOp",EDGE,"E1749"),sQuery(id+"F0.wireOp",EDGE,"E1750"),sQuery(id+"F0.wireOp",EDGE,"E1751"),sQuery(id+"F0.wireOp",EDGE,"E1752"),sQuery(id+"F0.wireOp",EDGE,"E1753"),sQuery(id+"F0.wireOp",EDGE,"E1754"),sQuery(id+"F0.wireOp",EDGE,"E1755"),sQuery(id+"F0.wireOp",EDGE,"E1756"),sQuery(id+"F0.wireOp",EDGE,"E1757"),sQuery(id+"F0.wireOp",EDGE,"E1758"),sQuery(id+"F0.wireOp",EDGE,"E1759"),sQuery(id+"F0.wireOp",EDGE,"E1760"),sQuery(id+"F0.wireOp",EDGE,"E1761"),sQuery(id+"F0.wireOp",EDGE,"E1762"),sQuery(id+"F0.wireOp",EDGE,"E1763"),sQuery(id+"F0.wireOp",EDGE,"E1764"),sQuery(id+"F0.wireOp",EDGE,"E1765"),sQuery(id+"F0.wireOp",EDGE,"E1766"),sQuery(id+"F0.wireOp",EDGE,"E1767"),sQuery(id+"F0.wireOp",EDGE,"E1768"),sQuery(id+"F0.wireOp",EDGE,"E1769"),sQuery(id+"F0.wireOp",EDGE,"E1770"),sQuery(id+"F0.wireOp",EDGE,"E1771"),sQuery(id+"F0.wireOp",EDGE,"E1772"),sQuery(id+"F0.wireOp",EDGE,"E1773"),sQuery(id+"F0.wireOp",EDGE,"E1774"),sQuery(id+"F0.wireOp",EDGE,"E1775"),sQuery(id+"F0.wireOp",EDGE,"E1776"),sQuery(id+"F0.wireOp",EDGE,"E1777"),sQuery(id+"F0.wireOp",EDGE,"E1778"),sQuery(id+"F0.wireOp",EDGE,"E1779"),sQuery(id+"F0.wireOp",EDGE,"E1780"),sQuery(id+"F0.wireOp",EDGE,"E1781"),sQuery(id+"F0.wireOp",EDGE,"E1782"),sQuery(id+"F0.wireOp",EDGE,"E1783"),sQuery(id+"F0.wireOp",EDGE,"E1784"),sQuery(id+"F0.wireOp",EDGE,"E1785"),sQuery(id+"F0.wireOp",EDGE,"E1786"),sQuery(id+"F0.wireOp",EDGE,"E1787"),sQuery(id+"F0.wireOp",EDGE,"E1788"),sQuery(id+"F0.wireOp",EDGE,"E1789"),sQuery(id+"F0.wireOp",EDGE,"E1790"),sQuery(id+"F0.wireOp",EDGE,"E1791"),sQuery(id+"F0.wireOp",EDGE,"E1792"),sQuery(id+"F0.wireOp",EDGE,"E1793"),sQuery(id+"F0.wireOp",EDGE,"E1794"),sQuery(id+"F0.wireOp",EDGE,"E1795"),sQuery(id+"F0.wireOp",EDGE,"E1796"),sQuery(id+"F0.wireOp",EDGE,"E1797"),sQuery(id+"F0.wireOp",EDGE,"E1798"),sQuery(id+"F0.wireOp",EDGE,"E1799"),sQuery(id+"F0.wireOp",EDGE,"E1800"),sQuery(id+"F0.wireOp",EDGE,"E1801"),sQuery(id+"F0.wireOp",EDGE,"E1802"),sQuery(id+"F0.wireOp",EDGE,"E1803"),sQuery(id+"F0.wireOp",EDGE,"E1804"),sQuery(id+"F0.wireOp",EDGE,"E1805"),sQuery(id+"F0.wireOp",EDGE,"E1806"),sQuery(id+"F0.wireOp",EDGE,"E1807"),sQuery(id+"F0.wireOp",EDGE,"E1808"),sQuery(id+"F0.wireOp",EDGE,"E1809"),sQuery(id+"F0.wireOp",EDGE,"E1810"),sQuery(id+"F0.wireOp",EDGE,"E1811"),sQuery(id+"F0.wireOp",EDGE,"E1812"),sQuery(id+"F0.wireOp",EDGE,"E1813"),sQuery(id+"F0.wireOp",EDGE,"E1814"),sQuery(id+"F0.wireOp",EDGE,"E1815"),sQuery(id+"F0.wireOp",EDGE,"E1816"),sQuery(id+"F0.wireOp",EDGE,"E1817"),sQuery(id+"F0.wireOp",EDGE,"E1818"),sQuery(id+"F0.wireOp",EDGE,"E1819"),sQuery(id+"F0.wireOp",EDGE,"E1820"),sQuery(id+"F0.wireOp",EDGE,"E1821"),sQuery(id+"F0.wireOp",EDGE,"E1822"),sQuery(id+"F0.wireOp",EDGE,"E1823"),sQuery(id+"F0.wireOp",EDGE,"E1824"),sQuery(id+"F0.wireOp",EDGE,"E1825"),sQuery(id+"F0.wireOp",EDGE,"E1826"),sQuery(id+"F0.wireOp",EDGE,"E1827"),sQuery(id+"F0.wireOp",EDGE,"E1828"),sQuery(id+"F0.wireOp",EDGE,"E1829"),sQuery(id+"F0.wireOp",EDGE,"E1830"),sQuery(id+"F0.wireOp",EDGE,"E1831"),sQuery(id+"F0.wireOp",EDGE,"E1832"),sQuery(id+"F0.wireOp",EDGE,"E1833"),sQuery(id+"F0.wireOp",EDGE,"E1834"),sQuery(id+"F0.wireOp",EDGE,"E1835"),sQuery(id+"F0.wireOp",EDGE,"E1836"),sQuery(id+"F0.wireOp",EDGE,"E1837"),sQuery(id+"F0.wireOp",EDGE,"E1838"),sQuery(id+"F0.wireOp",EDGE,"E1839"),sQuery(id+"F0.wireOp",EDGE,"E1840"),sQuery(id+"F0.wireOp",EDGE,"E1841"),sQuery(id+"F0.wireOp",EDGE,"E1842"),sQuery(id+"F0.wireOp",EDGE,"E1843"),sQuery(id+"F0.wireOp",EDGE,"E1844"),sQuery(id+"F0.wireOp",EDGE,"E1845"),sQuery(id+"F0.wireOp",EDGE,"E1846"),sQuery(id+"F0.wireOp",EDGE,"E1847"),sQuery(id+"F0.wireOp",EDGE,"E1848"),sQuery(id+"F0.wireOp",EDGE,"E1849"),sQuery(id+"F0.wireOp",EDGE,"E1850"),sQuery(id+"F0.wireOp",EDGE,"E1851"),sQuery(id+"F0.wireOp",EDGE,"E1852"),sQuery(id+"F0.wireOp",EDGE,"E1853"),sQuery(id+"F0.wireOp",EDGE,"E1854"),sQuery(id+"F0.wireOp",EDGE,"E1855"),sQuery(id+"F0.wireOp",EDGE,"E1856"),sQuery(id+"F0.wireOp",EDGE,"E1857"),sQuery(id+"F0.wireOp",EDGE,"E1858"),sQuery(id+"F0.wireOp",EDGE,"E1859"),sQuery(id+"F0.wireOp",EDGE,"E1860"),sQuery(id+"F0.wireOp",EDGE,"E1861"),sQuery(id+"F0.wireOp",EDGE,"E1862"),sQuery(id+"F0.wireOp",EDGE,"E1863"),sQuery(id+"F0.wireOp",EDGE,"E1864"),sQuery(id+"F0.wireOp",EDGE,"E1865"),sQuery(id+"F0.wireOp",EDGE,"E1866"),sQuery(id+"F0.wireOp",EDGE,"E1867"),sQuery(id+"F0.wireOp",EDGE,"E1868"),sQuery(id+"F0.wireOp",EDGE,"E1869"),sQuery(id+"F0.wireOp",EDGE,"E1870"),sQuery(id+"F0.wireOp",EDGE,"E1871"),sQuery(id+"F0.wireOp",EDGE,"E1872"),sQuery(id+"F0.wireOp",EDGE,"E1873"),sQuery(id+"F0.wireOp",EDGE,"E1874"),sQuery(id+"F0.wireOp",EDGE,"E1875"),sQuery(id+"F0.wireOp",EDGE,"E1876"),sQuery(id+"F0.wireOp",EDGE,"E1877"),sQuery(id+"F0.wireOp",EDGE,"E1878"),sQuery(id+"F0.wireOp",EDGE,"E1879"),sQuery(id+"F0.wireOp",EDGE,"E1880"),sQuery(id+"F0.wireOp",EDGE,"E1881"),sQuery(id+"F0.wireOp",EDGE,"E1882"),sQuery(id+"F0.wireOp",EDGE,"E1883"),sQuery(id+"F0.wireOp",EDGE,"E1884"),sQuery(id+"F0.wireOp",EDGE,"E1885"),sQuery(id+"F0.wireOp",EDGE,"E1886"),sQuery(id+"F0.wireOp",EDGE,"E1887"),sQuery(id+"F0.wireOp",EDGE,"E1888"),sQuery(id+"F0.wireOp",EDGE,"E1889"),sQuery(id+"F0.wireOp",EDGE,"E1890"),sQuery(id+"F0.wireOp",EDGE,"E1891"),sQuery(id+"F0.wireOp",EDGE,"E1892"),sQuery(id+"F0.wireOp",EDGE,"E1893"),sQuery(id+"F0.wireOp",EDGE,"E1894"),sQuery(id+"F0.wireOp",EDGE,"E1895"),sQuery(id+"F0.wireOp",EDGE,"E1896"),sQuery(id+"F0.wireOp",EDGE,"E1897"),sQuery(id+"F0.wireOp",EDGE,"E1898"),sQuery(id+"F0.wireOp",EDGE,"E1899"),sQuery(id+"F0.wireOp",EDGE,"E1900"),sQuery(id+"F0.wireOp",EDGE,"E1901"),sQuery(id+"F0.wireOp",EDGE,"E1902"),sQuery(id+"F0.wireOp",EDGE,"E1903"),sQuery(id+"F0.wireOp",EDGE,"E1904"),sQuery(id+"F0.wireOp",EDGE,"E1905"),sQuery(id+"F0.wireOp",EDGE,"E1906"),sQuery(id+"F0.wireOp",EDGE,"E1907"),sQuery(id+"F0.wireOp",EDGE,"E1908"),sQuery(id+"F0.wireOp",EDGE,"E1909"),sQuery(id+"F0.wireOp",EDGE,"E1910"),sQuery(id+"F0.wireOp",EDGE,"E1911"),sQuery(id+"F0.wireOp",EDGE,"E1912"),sQuery(id+"F0.wireOp",EDGE,"E1913"),sQuery(id+"F0.wireOp",EDGE,"E1914"),sQuery(id+"F0.wireOp",EDGE,"E1915"),sQuery(id+"F0.wireOp",EDGE,"E1916"),sQuery(id+"F0.wireOp",EDGE,"E1917"),sQuery(id+"F0.wireOp",EDGE,"E1918"),sQuery(id+"F0.wireOp",EDGE,"E1919"),sQuery(id+"F0.wireOp",EDGE,"E1920"),sQuery(id+"F0.wireOp",EDGE,"E1921"),sQuery(id+"F0.wireOp",EDGE,"E1922"),sQuery(id+"F0.wireOp",EDGE,"E1923"),sQuery(id+"F0.wireOp",EDGE,"E1924"),sQuery(id+"F0.wireOp",EDGE,"E1925"),sQuery(id+"F0.wireOp",EDGE,"E1926"),sQuery(id+"F0.wireOp",EDGE,"E1927"),sQuery(id+"F0.wireOp",EDGE,"E1928"),sQuery(id+"F0.wireOp",EDGE,"E1929"),sQuery(id+"F0.wireOp",EDGE,"E1930"),sQuery(id+"F0.wireOp",EDGE,"E1931"),sQuery(id+"F0.wireOp",EDGE,"E1932"),sQuery(id+"F0.wireOp",EDGE,"E1933"),sQuery(id+"F0.wireOp",EDGE,"E1934"),sQuery(id+"F0.wireOp",EDGE,"E1935"),sQuery(id+"F0.wireOp",EDGE,"E1936"),sQuery(id+"F0.wireOp",EDGE,"E1937"),sQuery(id+"F0.wireOp",EDGE,"E1938"),sQuery(id+"F0.wireOp",EDGE,"E1939"),sQuery(id+"F0.wireOp",EDGE,"E1940"),sQuery(id+"F0.wireOp",EDGE,"E1941"),sQuery(id+"F0.wireOp",EDGE,"E1942"),sQuery(id+"F0.wireOp",EDGE,"E1943"),sQuery(id+"F0.wireOp",EDGE,"E1944"),sQuery(id+"F0.wireOp",EDGE,"E1945"),sQuery(id+"F0.wireOp",EDGE,"E1946"),sQuery(id+"F0.wireOp",EDGE,"E1947"),sQuery(id+"F0.wireOp",EDGE,"E1948"),sQuery(id+"F0.wireOp",EDGE,"E1949"),sQuery(id+"F0.wireOp",EDGE,"E1950"),sQuery(id+"F0.wireOp",EDGE,"E1951"),sQuery(id+"F0.wireOp",EDGE,"E1952"),sQuery(id+"F0.wireOp",EDGE,"E1953"),sQuery(id+"F0.wireOp",EDGE,"E1954"),sQuery(id+"F0.wireOp",EDGE,"E1955"),sQuery(id+"F0.wireOp",EDGE,"E1956"),sQuery(id+"F0.wireOp",EDGE,"E1957"),sQuery(id+"F0.wireOp",EDGE,"E1958"),sQuery(id+"F0.wireOp",EDGE,"E1959"),sQuery(id+"F0.wireOp",EDGE,"E1960"),sQuery(id+"F0.wireOp",EDGE,"E1961"),sQuery(id+"F0.wireOp",EDGE,"E1962"),sQuery(id+"F0.wireOp",EDGE,"E1963"),sQuery(id+"F0.wireOp",EDGE,"E1964"),sQuery(id+"F0.wireOp",EDGE,"E1965"),sQuery(id+"F0.wireOp",EDGE,"E1966"),sQuery(id+"F0.wireOp",EDGE,"E1967"),sQuery(id+"F0.wireOp",EDGE,"E1968"),sQuery(id+"F0.wireOp",EDGE,"E1969"),sQuery(id+"F0.wireOp",EDGE,"E1970"),sQuery(id+"F0.wireOp",EDGE,"E1971"),sQuery(id+"F0.wireOp",EDGE,"E1972"),sQuery(id+"F0.wireOp",EDGE,"E1973"),sQuery(id+"F0.wireOp",EDGE,"E1974"),sQuery(id+"F0.wireOp",EDGE,"E1975"),sQuery(id+"F0.wireOp",EDGE,"E1976"),sQuery(id+"F0.wireOp",EDGE,"E1977"),sQuery(id+"F0.wireOp",EDGE,"E1978"),sQuery(id+"F0.wireOp",EDGE,"E1979"),sQuery(id+"F0.wireOp",EDGE,"E1980"),sQuery(id+"F0.wireOp",EDGE,"E1981"),sQuery(id+"F0.wireOp",EDGE,"E1982"),sQuery(id+"F0.wireOp",EDGE,"E1983"),sQuery(id+"F0.wireOp",EDGE,"E1984"),sQuery(id+"F0.wireOp",EDGE,"E1985"),sQuery(id+"F0.wireOp",EDGE,"E1986"),sQuery(id+"F0.wireOp",EDGE,"E1987"),sQuery(id+"F0.wireOp",EDGE,"E1988"),sQuery(id+"F0.wireOp",EDGE,"E1989"),sQuery(id+"F0.wireOp",EDGE,"E1990"),sQuery(id+"F0.wireOp",EDGE,"E1991"),sQuery(id+"F0.wireOp",EDGE,"E1992"),sQuery(id+"F0.wireOp",EDGE,"E1993"),sQuery(id+"F0.wireOp",EDGE,"E1994"),sQuery(id+"F0.wireOp",EDGE,"E1995"),sQuery(id+"F0.wireOp",EDGE,"E1996"),sQuery(id+"F0.wireOp",EDGE,"E1997"),sQuery(id+"F0.wireOp",EDGE,"E1998"),sQuery(id+"F0.wireOp",EDGE,"E1999"),sQuery(id+"F0.wireOp",EDGE,"E2000"),sQuery(id+"F0.wireOp",EDGE,"E2001"),sQuery(id+"F0.wireOp",EDGE,"E2002"),sQuery(id+"F0.wireOp",EDGE,"E2003"),sQuery(id+"F0.wireOp",EDGE,"E2004"),sQuery(id+"F0.wireOp",EDGE,"E2005"),sQuery(id+"F0.wireOp",EDGE,"E2006"),sQuery(id+"F0.wireOp",EDGE,"E2007"),sQuery(id+"F0.wireOp",EDGE,"E2008"),sQuery(id+"F0.wireOp",EDGE,"E2009"),sQuery(id+"F0.wireOp",EDGE,"E2010"),sQuery(id+"F0.wireOp",EDGE,"E2011"),sQuery(id+"F0.wireOp",EDGE,"E2012"),sQuery(id+"F0.wireOp",EDGE,"E2013"),sQuery(id+"F0.wireOp",EDGE,"E2014"),sQuery(id+"F0.wireOp",EDGE,"E2015"),sQuery(id+"F0.wireOp",EDGE,"E2016"),sQuery(id+"F0.wireOp",EDGE,"E2017"),sQuery(id+"F0.wireOp",EDGE,"E2018"),sQuery(id+"F0.wireOp",EDGE,"E2019"),sQuery(id+"F0.wireOp",EDGE,"E2020"),sQuery(id+"F0.wireOp",EDGE,"E2021"),sQuery(id+"F0.wireOp",EDGE,"E2022"),sQuery(id+"F0.wireOp",EDGE,"E2023"),sQuery(id+"F0.wireOp",EDGE,"E2024"),sQuery(id+"F0.wireOp",EDGE,"E2025"),sQuery(id+"F0.wireOp",EDGE,"E2026"),sQuery(id+"F0.wireOp",EDGE,"E2027"),sQuery(id+"F0.wireOp",EDGE,"E2028"),sQuery(id+"F0.wireOp",EDGE,"E2029"),sQuery(id+"F0.wireOp",EDGE,"E2030"),sQuery(id+"F0.wireOp",EDGE,"E2031"),sQuery(id+"F0.wireOp",EDGE,"E2032"),sQuery(id+"F0.wireOp",EDGE,"E2033"),sQuery(id+"F0.wireOp",EDGE,"E2034"),sQuery(id+"F0.wireOp",EDGE,"E2035"),sQuery(id+"F0.wireOp",EDGE,"E2036"),sQuery(id+"F0.wireOp",EDGE,"E2037"),sQuery(id+"F0.wireOp",EDGE,"E2038"),sQuery(id+"F0.wireOp",EDGE,"E2039"),sQuery(id+"F0.wireOp",EDGE,"E2040"),sQuery(id+"F0.wireOp",EDGE,"E2041"),sQuery(id+"F0.wireOp",EDGE,"E2042"),sQuery(id+"F0.wireOp",EDGE,"E2043"),sQuery(id+"F0.wireOp",EDGE,"E2044"),sQuery(id+"F0.wireOp",EDGE,"E2045"),sQuery(id+"F0.wireOp",EDGE,"E2046"),sQuery(id+"F0.wireOp",EDGE,"E2047"),sQuery(id+"F0.wireOp",EDGE,"E2048"),sQuery(id+"F0.wireOp",EDGE,"E2049"),sQuery(id+"F0.wireOp",EDGE,"E2050"),sQuery(id+"F0.wireOp",EDGE,"E2051"),sQuery(id+"F0.wireOp",EDGE,"E2052"),sQuery(id+"F0.wireOp",EDGE,"E2053"),sQuery(id+"F0.wireOp",EDGE,"E2054"),sQuery(id+"F0.wireOp",EDGE,"E2055"),sQuery(id+"F0.wireOp",EDGE,"E2056"),sQuery(id+"F0.wireOp",EDGE,"E2057"),sQuery(id+"F0.wireOp",EDGE,"E2058"),sQuery(id+"F0.wireOp",EDGE,"E2059"),sQuery(id+"F0.wireOp",EDGE,"E2060"),sQuery(id+"F0.wireOp",EDGE,"E2061"),sQuery(id+"F0.wireOp",EDGE,"E2062"),sQuery(id+"F0.wireOp",EDGE,"E2063"),sQuery(id+"F0.wireOp",EDGE,"E2064"),sQuery(id+"F0.wireOp",EDGE,"E2065"),sQuery(id+"F0.wireOp",EDGE,"E2066"),sQuery(id+"F0.wireOp",EDGE,"E2067"),sQuery(id+"F0.wireOp",EDGE,"E2068"),sQuery(id+"F0.wireOp",EDGE,"E2069"),sQuery(id+"F0.wireOp",EDGE,"E2070"),sQuery(id+"F0.wireOp",EDGE,"E2071"),sQuery(id+"F0.wireOp",EDGE,"E2072"),sQuery(id+"F0.wireOp",EDGE,"E2073"),sQuery(id+"F0.wireOp",EDGE,"E2074"),sQuery(id+"F0.wireOp",EDGE,"E2075"),sQuery(id+"F0.wireOp",EDGE,"E2076"),sQuery(id+"F0.wireOp",EDGE,"E2077"),sQuery(id+"F0.wireOp",EDGE,"E2078"),sQuery(id+"F0.wireOp",EDGE,"E2079"),sQuery(id+"F0.wireOp",EDGE,"E2080"),sQuery(id+"F0.wireOp",EDGE,"E2081"),sQuery(id+"F0.wireOp",EDGE,"E2082"),sQuery(id+"F0.wireOp",EDGE,"E2083"),sQuery(id+"F0.wireOp",EDGE,"E2084"),sQuery(id+"F0.wireOp",EDGE,"E2085"),sQuery(id+"F0.wireOp",EDGE,"E2086"),sQuery(id+"F0.wireOp",EDGE,"E2087"),sQuery(id+"F0.wireOp",EDGE,"E2088"),sQuery(id+"F0.wireOp",EDGE,"E2089"),sQuery(id+"F0.wireOp",EDGE,"E2090"),sQuery(id+"F0.wireOp",EDGE,"E2091"),sQuery(id+"F0.wireOp",EDGE,"E2092"),sQuery(id+"F0.wireOp",EDGE,"E2093"),sQuery(id+"F0.wireOp",EDGE,"E2094"),sQuery(id+"F0.wireOp",EDGE,"E2095"),sQuery(id+"F0.wireOp",EDGE,"E2096"),sQuery(id+"F0.wireOp",EDGE,"E2097"),sQuery(id+"F0.wireOp",EDGE,"E2098"),sQuery(id+"F0.wireOp",EDGE,"E2099"),sQuery(id+"F0.wireOp",EDGE,"E2100"),sQuery(id+"F0.wireOp",EDGE,"E2101"),sQuery(id+"F0.wireOp",EDGE,"E2102"),sQuery(id+"F0.wireOp",EDGE,"E2103"),sQuery(id+"F0.wireOp",EDGE,"E2104"),sQuery(id+"F0.wireOp",EDGE,"E2105"),sQuery(id+"F0.wireOp",EDGE,"E2106"),sQuery(id+"F0.wireOp",EDGE,"E2107"),sQuery(id+"F0.wireOp",EDGE,"E2108"),sQuery(id+"F0.wireOp",EDGE,"E2109"),sQuery(id+"F0.wireOp",EDGE,"E2110"),sQuery(id+"F0.wireOp",EDGE,"E2111"),sQuery(id+"F0.wireOp",EDGE,"E2112"),sQuery(id+"F0.wireOp",EDGE,"E2113"),sQuery(id+"F0.wireOp",EDGE,"E2114"),sQuery(id+"F0.wireOp",EDGE,"E2115"),sQuery(id+"F0.wireOp",EDGE,"E2116"),sQuery(id+"F0.wireOp",EDGE,"E2117"),sQuery(id+"F0.wireOp",EDGE,"E2118"),sQuery(id+"F0.wireOp",EDGE,"E2119"),sQuery(id+"F0.wireOp",EDGE,"E2120"),sQuery(id+"F0.wireOp",EDGE,"E2121"),sQuery(id+"F0.wireOp",EDGE,"E2122"),sQuery(id+"F0.wireOp",EDGE,"E2123"),sQuery(id+"F0.wireOp",EDGE,"E2124"),sQuery(id+"F0.wireOp",EDGE,"E2125"),sQuery(id+"F0.wireOp",EDGE,"E2126"),sQuery(id+"F0.wireOp",EDGE,"E2127"),sQuery(id+"F0.wireOp",EDGE,"E2128"),sQuery(id+"F0.wireOp",EDGE,"E2129"),sQuery(id+"F0.wireOp",EDGE,"E2130"),sQuery(id+"F0.wireOp",EDGE,"E2131"),sQuery(id+"F0.wireOp",EDGE,"E2132"),sQuery(id+"F0.wireOp",EDGE,"E2133"),sQuery(id+"F0.wireOp",EDGE,"E2134"),sQuery(id+"F0.wireOp",EDGE,"E2135"),sQuery(id+"F0.wireOp",EDGE,"E2136"),sQuery(id+"F0.wireOp",EDGE,"E2137"),sQuery(id+"F0.wireOp",EDGE,"E2138"),sQuery(id+"F0.wireOp",EDGE,"E2139"),sQuery(id+"F0.wireOp",EDGE,"E2140"),sQuery(id+"F0.wireOp",EDGE,"E2141"),sQuery(id+"F0.wireOp",EDGE,"E2142"),sQuery(id+"F0.wireOp",EDGE,"E2143"),sQuery(id+"F0.wireOp",EDGE,"E2144"),sQuery(id+"F0.wireOp",EDGE,"E2145"),sQuery(id+"F0.wireOp",EDGE,"E2146"),sQuery(id+"F0.wireOp",EDGE,"E2147"),sQuery(id+"F0.wireOp",EDGE,"E2148"),sQuery(id+"F0.wireOp",EDGE,"E2149"),sQuery(id+"F0.wireOp",EDGE,"E2150"),sQuery(id+"F0.wireOp",EDGE,"E2151"),sQuery(id+"F0.wireOp",EDGE,"E2152"),sQuery(id+"F0.wireOp",EDGE,"E2153"),sQuery(id+"F0.wireOp",EDGE,"E2154"),sQuery(id+"F0.wireOp",EDGE,"E2155"),sQuery(id+"F0.wireOp",EDGE,"E2156"),sQuery(id+"F0.wireOp",EDGE,"E2157"),sQuery(id+"F0.wireOp",EDGE,"E2158"),sQuery(id+"F0.wireOp",EDGE,"E2159"),sQuery(id+"F0.wireOp",EDGE,"E2160"),sQuery(id+"F0.wireOp",EDGE,"E2161"),sQuery(id+"F0.wireOp",EDGE,"E2162"),sQuery(id+"F0.wireOp",EDGE,"E2163"),sQuery(id+"F0.wireOp",EDGE,"E2164"),sQuery(id+"F0.wireOp",EDGE,"E2165"),sQuery(id+"F0.wireOp",EDGE,"E2166"),sQuery(id+"F0.wireOp",EDGE,"E2167"),sQuery(id+"F0.wireOp",EDGE,"E2168"),sQuery(id+"F0.wireOp",EDGE,"E2169"),sQuery(id+"F0.wireOp",EDGE,"E2170"),sQuery(id+"F0.wireOp",EDGE,"E2171"),sQuery(id+"F0.wireOp",EDGE,"E2172"),sQuery(id+"F0.wireOp",EDGE,"E2173"),sQuery(id+"F0.wireOp",EDGE,"E2174"),sQuery(id+"F0.wireOp",EDGE,"E2175"),sQuery(id+"F0.wireOp",EDGE,"E2176"),sQuery(id+"F0.wireOp",EDGE,"E2177"),sQuery(id+"F0.wireOp",EDGE,"E2178"),sQuery(id+"F0.wireOp",EDGE,"E2179"),sQuery(id+"F0.wireOp",EDGE,"E2180"),sQuery(id+"F0.wireOp",EDGE,"E2181"),sQuery(id+"F0.wireOp",EDGE,"E2182"),sQuery(id+"F0.wireOp",EDGE,"E2183"),sQuery(id+"F0.wireOp",EDGE,"E2184"),sQuery(id+"F0.wireOp",EDGE,"E2185"),sQuery(id+"F0.wireOp",EDGE,"E2186"),sQuery(id+"F0.wireOp",EDGE,"E2187"),sQuery(id+"F0.wireOp",EDGE,"E2188"),sQuery(id+"F0.wireOp",EDGE,"E2189"),sQuery(id+"F0.wireOp",EDGE,"E2190"),sQuery(id+"F0.wireOp",EDGE,"E2191"),sQuery(id+"F0.wireOp",EDGE,"E2192"),sQuery(id+"F0.wireOp",EDGE,"E2193"),sQuery(id+"F0.wireOp",EDGE,"E2194"),sQuery(id+"F0.wireOp",EDGE,"E2195"),sQuery(id+"F0.wireOp",EDGE,"E2196"),sQuery(id+"F0.wireOp",EDGE,"E2197"),sQuery(id+"F0.wireOp",EDGE,"E2198"),sQuery(id+"F0.wireOp",EDGE,"E2199"),sQuery(id+"F0.wireOp",EDGE,"E2200"),sQuery(id+"F0.wireOp",EDGE,"E2201"),sQuery(id+"F0.wireOp",EDGE,"E2202"),sQuery(id+"F0.wireOp",EDGE,"E2203"),sQuery(id+"F0.wireOp",EDGE,"E2204"),sQuery(id+"F0.wireOp",EDGE,"E2205"),sQuery(id+"F0.wireOp",EDGE,"E2206"),sQuery(id+"F0.wireOp",EDGE,"E2207"),sQuery(id+"F0.wireOp",EDGE,"E2208"),sQuery(id+"F0.wireOp",EDGE,"E2209"),sQuery(id+"F0.wireOp",EDGE,"E2210"),sQuery(id+"F0.wireOp",EDGE,"E2211"),sQuery(id+"F0.wireOp",EDGE,"E2212"),sQuery(id+"F0.wireOp",EDGE,"E2213"),sQuery(id+"F0.wireOp",EDGE,"E2214"),sQuery(id+"F0.wireOp",EDGE,"E2215"),sQuery(id+"F0.wireOp",EDGE,"E2216"),sQuery(id+"F0.wireOp",EDGE,"E2217"),sQuery(id+"F0.wireOp",EDGE,"E2218"),sQuery(id+"F0.wireOp",EDGE,"E2219"),sQuery(id+"F0.wireOp",EDGE,"E2220"),sQuery(id+"F0.wireOp",EDGE,"E2221"),sQuery(id+"F0.wireOp",EDGE,"E2222"),sQuery(id+"F0.wireOp",EDGE,"E2223"),sQuery(id+"F0.wireOp",EDGE,"E2224"),sQuery(id+"F0.wireOp",EDGE,"E2225"),sQuery(id+"F0.wireOp",EDGE,"E2226"),sQuery(id+"F0.wireOp",EDGE,"E2227"),sQuery(id+"F0.wireOp",EDGE,"E2228"),sQuery(id+"F0.wireOp",EDGE,"E2229"),sQuery(id+"F0.wireOp",EDGE,"E2230"),sQuery(id+"F0.wireOp",EDGE,"E2231"),sQuery(id+"F0.wireOp",EDGE,"E2232"),sQuery(id+"F0.wireOp",EDGE,"E2233"),sQuery(id+"F0.wireOp",EDGE,"E2234"),sQuery(id+"F0.wireOp",EDGE,"E2235"),sQuery(id+"F0.wireOp",EDGE,"E2236"),sQuery(id+"F0.wireOp",EDGE,"E2237"),sQuery(id+"F0.wireOp",EDGE,"E2238"),sQuery(id+"F0.wireOp",EDGE,"E2239"),sQuery(id+"F0.wireOp",EDGE,"E2240"),sQuery(id+"F0.wireOp",EDGE,"E2241"),sQuery(id+"F0.wireOp",EDGE,"E2242"),sQuery(id+"F0.wireOp",EDGE,"E2243"),sQuery(id+"F0.wireOp",EDGE,"E2244"),sQuery(id+"F0.wireOp",EDGE,"E2245"),sQuery(id+"F0.wireOp",EDGE,"E2246"),sQuery(id+"F0.wireOp",EDGE,"E2247"),sQuery(id+"F0.wireOp",EDGE,"E2248"),sQuery(id+"F0.wireOp",EDGE,"E2249"),sQuery(id+"F0.wireOp",EDGE,"E2250"),sQuery(id+"F0.wireOp",EDGE,"E2251"),sQuery(id+"F0.wireOp",EDGE,"E2252"),sQuery(id+"F0.wireOp",EDGE,"E2253"),sQuery(id+"F0.wireOp",EDGE,"E2254"),sQuery(id+"F0.wireOp",EDGE,"E2255"),sQuery(id+"F0.wireOp",EDGE,"E2256"),sQuery(id+"F0.wireOp",EDGE,"E2257"),sQuery(id+"F0.wireOp",EDGE,"E2258"),sQuery(id+"F0.wireOp",EDGE,"E2259")])]});
            transform(context, id + "F4", {"entities" : qUnion([Q0]), "transformType" : TransformType.TRANSLATION_3D, "dx" : 0 * mm, "dy" : 0 * mm, "dz" : 0 * mm, "makeCopy" : true});
        }
    });
